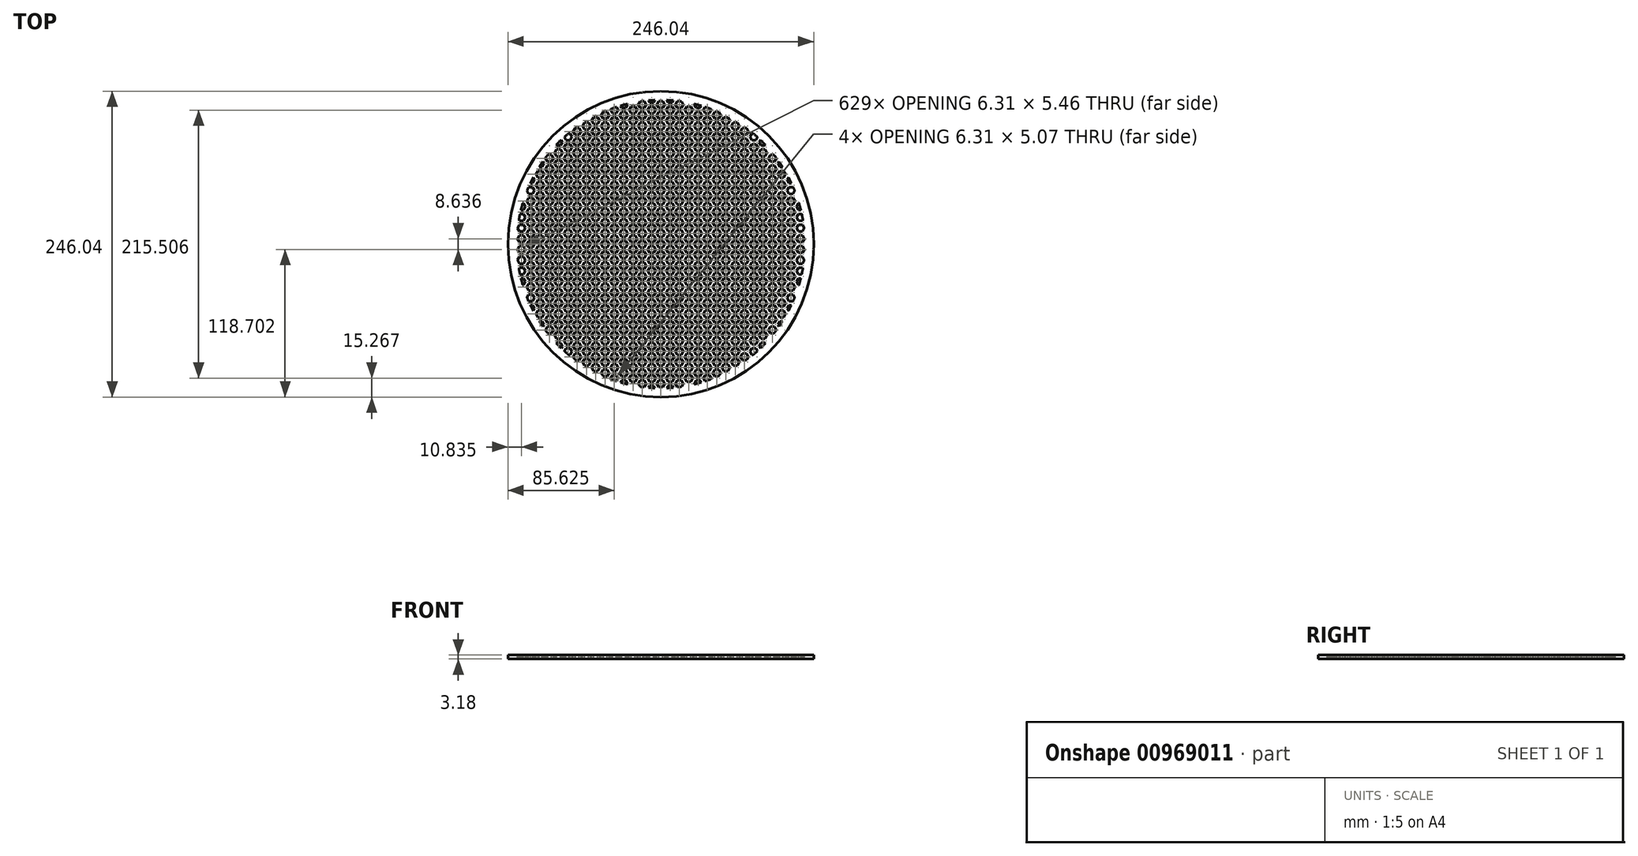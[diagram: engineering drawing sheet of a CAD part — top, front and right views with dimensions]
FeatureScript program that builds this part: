
annotation { "Feature Type Name" : "Feature", "Feature Type Description" : "" }
export const myFeature = defineFeature(function(context is Context, id is Id, definition is map)
    precondition{}
    {
        {
            var Q0;
            Q0=qCreatedBy(makeId("Top.planeOp"),FACE);
            var sketch = newSketch(context, id + "F0", { "sketchPlane" : qUnion([Q0])});
            skCircle(sketch, "E0", {"center": v(0, 0) * mm, "radius": 123.02 * mm});
            skSolve(sketch);
        }
        {
            var Q0;
            Q0=qSketchRegion(id+"F0",true);
            extrude(context, id + "F1", {"entities" : qUnion([Q0]), "depth" : 3.17 * mm, "offsetDistance" : 25.4 * mm});
        }
        {
            var Q0;
            Q0=makeQuery(id+"F1.opExtrude","CAP_FACE",FACE,{"disambiguationData":[OSD([sQuery(id+"F0.wireOp",EDGE,"E0")])],"isStart":false});
            var sketch = newSketch(context, id + "F2", { "sketchPlane" : qUnion([Q0])});
            skCircle(sketch, "E1.cCircle", {"center": v(-127.14, -133.86) * mm, "radius": 2.73 * mm, "construction": true});
            skLineSegment(sketch, "E1.0", {"start": v(-128.72, -131.13) * mm, "end": v(-125.57, -131.13) * mm});
            skLineSegment(sketch, "E1.1", {"start": v(-125.57, -131.13) * mm, "end": v(-124, -133.86) * mm});
            skLineSegment(sketch, "E1.2", {"start": v(-124, -133.86) * mm, "end": v(-125.57, -136.59) * mm});
            skLineSegment(sketch, "E1.3", {"start": v(-125.57, -136.59) * mm, "end": v(-128.72, -136.59) * mm});
            skLineSegment(sketch, "E1.4", {"start": v(-128.72, -136.59) * mm, "end": v(-130.3, -133.86) * mm});
            skLineSegment(sketch, "E1.5", {"start": v(-130.3, -133.86) * mm, "end": v(-128.72, -131.13) * mm});
            skPoint(sketch, "E1.0.midPoint", {"position": v(-127.14, -131.13) * mm});
            skCircle(sketch, "E2.cCircle", {"center": v(-119.66, -129.54) * mm, "radius": 2.73 * mm, "construction": true});
            skLineSegment(sketch, "E2.0", {"start": v(-121.24, -126.8) * mm, "end": v(-118.09, -126.8) * mm});
            skLineSegment(sketch, "E2.1", {"start": v(-118.09, -126.8) * mm, "end": v(-116.51, -129.54) * mm});
            skLineSegment(sketch, "E2.2", {"start": v(-116.51, -129.54) * mm, "end": v(-118.09, -132.27) * mm});
            skLineSegment(sketch, "E2.3", {"start": v(-118.09, -132.27) * mm, "end": v(-121.24, -132.27) * mm});
            skLineSegment(sketch, "E2.4", {"start": v(-121.24, -132.27) * mm, "end": v(-122.82, -129.54) * mm});
            skLineSegment(sketch, "E2.5", {"start": v(-122.82, -129.54) * mm, "end": v(-121.24, -126.8) * mm});
            skPoint(sketch, "E2.0.midPoint", {"position": v(-119.66, -126.8) * mm});
            skLineSegment(sketch, "E3.0.1.0", {"start": v(-128.72, -122.5) * mm, "end": v(-125.57, -122.5) * mm});
            skLineSegment(sketch, "E3.0.1.1", {"start": v(-125.57, -122.5) * mm, "end": v(-124, -125.22) * mm});
            skLineSegment(sketch, "E3.0.1.2", {"start": v(-124, -125.22) * mm, "end": v(-125.57, -127.95) * mm});
            skCircle(sketch, "E3.0.1.3", {"center": v(-127.14, -125.22) * mm, "radius": 2.73 * mm, "construction": true});
            skLineSegment(sketch, "E3.0.1.4", {"start": v(-125.57, -127.95) * mm, "end": v(-128.72, -127.95) * mm});
            skLineSegment(sketch, "E3.0.1.5", {"start": v(-128.72, -127.95) * mm, "end": v(-130.3, -125.22) * mm});
            skLineSegment(sketch, "E3.0.1.6", {"start": v(-130.3, -125.22) * mm, "end": v(-128.72, -122.5) * mm});
            skLineSegment(sketch, "E3.0.2.0", {"start": v(-128.72, -113.86) * mm, "end": v(-125.57, -113.86) * mm});
            skLineSegment(sketch, "E3.0.2.1", {"start": v(-125.57, -113.86) * mm, "end": v(-124, -116.59) * mm});
            skLineSegment(sketch, "E3.0.2.2", {"start": v(-124, -116.59) * mm, "end": v(-125.57, -119.32) * mm});
            skCircle(sketch, "E3.0.2.3", {"center": v(-127.14, -116.59) * mm, "radius": 2.73 * mm, "construction": true});
            skLineSegment(sketch, "E3.0.2.4", {"start": v(-125.57, -119.32) * mm, "end": v(-128.72, -119.32) * mm});
            skLineSegment(sketch, "E3.0.2.5", {"start": v(-128.72, -119.32) * mm, "end": v(-130.3, -116.59) * mm});
            skLineSegment(sketch, "E3.0.2.6", {"start": v(-130.3, -116.59) * mm, "end": v(-128.72, -113.86) * mm});
            skLineSegment(sketch, "E3.1.0.0", {"start": v(-113.76, -131.13) * mm, "end": v(-110.6, -131.13) * mm});
            skLineSegment(sketch, "E3.1.0.1", {"start": v(-110.6, -131.13) * mm, "end": v(-109.03, -133.86) * mm});
            skLineSegment(sketch, "E3.1.0.2", {"start": v(-109.03, -133.86) * mm, "end": v(-110.6, -136.59) * mm});
            skCircle(sketch, "E3.1.0.3", {"center": v(-112.19, -133.86) * mm, "radius": 2.73 * mm, "construction": true});
            skLineSegment(sketch, "E3.1.0.4", {"start": v(-110.6, -136.59) * mm, "end": v(-113.76, -136.59) * mm});
            skLineSegment(sketch, "E3.1.0.5", {"start": v(-113.76, -136.59) * mm, "end": v(-115.34, -133.86) * mm});
            skLineSegment(sketch, "E3.1.0.6", {"start": v(-115.34, -133.86) * mm, "end": v(-113.76, -131.13) * mm});
            skLineSegment(sketch, "E3.1.1.0", {"start": v(-113.76, -122.5) * mm, "end": v(-110.6, -122.5) * mm});
            skLineSegment(sketch, "E3.1.1.1", {"start": v(-110.6, -122.5) * mm, "end": v(-109.03, -125.22) * mm});
            skLineSegment(sketch, "E3.1.1.2", {"start": v(-109.03, -125.22) * mm, "end": v(-110.6, -127.95) * mm});
            skCircle(sketch, "E3.1.1.3", {"center": v(-112.19, -125.22) * mm, "radius": 2.73 * mm, "construction": true});
            skLineSegment(sketch, "E3.1.1.4", {"start": v(-110.6, -127.95) * mm, "end": v(-113.76, -127.95) * mm});
            skLineSegment(sketch, "E3.1.1.5", {"start": v(-113.76, -127.95) * mm, "end": v(-115.34, -125.22) * mm});
            skLineSegment(sketch, "E3.1.1.6", {"start": v(-115.34, -125.22) * mm, "end": v(-113.76, -122.5) * mm});
            skLineSegment(sketch, "E3.1.2.0", {"start": v(-113.76, -113.86) * mm, "end": v(-110.6, -113.86) * mm});
            skLineSegment(sketch, "E3.1.2.1", {"start": v(-110.6, -113.86) * mm, "end": v(-109.03, -116.59) * mm});
            skLineSegment(sketch, "E3.1.2.2", {"start": v(-109.03, -116.59) * mm, "end": v(-110.6, -119.32) * mm});
            skCircle(sketch, "E3.1.2.3", {"center": v(-112.19, -116.59) * mm, "radius": 2.73 * mm, "construction": true});
            skLineSegment(sketch, "E3.1.2.4", {"start": v(-110.6, -119.32) * mm, "end": v(-113.76, -119.32) * mm});
            skLineSegment(sketch, "E3.1.2.5", {"start": v(-113.76, -119.32) * mm, "end": v(-115.34, -116.59) * mm});
            skLineSegment(sketch, "E3.1.2.6", {"start": v(-115.34, -116.59) * mm, "end": v(-113.76, -113.86) * mm});
            skLineSegment(sketch, "E3.2.0.0", {"start": v(-98.8, -131.13) * mm, "end": v(-95.65, -131.13) * mm});
            skLineSegment(sketch, "E3.2.0.1", {"start": v(-95.65, -131.13) * mm, "end": v(-94.07, -133.86) * mm});
            skLineSegment(sketch, "E3.2.0.2", {"start": v(-94.07, -133.86) * mm, "end": v(-95.65, -136.59) * mm});
            skCircle(sketch, "E3.2.0.3", {"center": v(-97.23, -133.86) * mm, "radius": 2.73 * mm, "construction": true});
            skLineSegment(sketch, "E3.2.0.4", {"start": v(-95.65, -136.59) * mm, "end": v(-98.8, -136.59) * mm});
            skLineSegment(sketch, "E3.2.0.5", {"start": v(-98.8, -136.59) * mm, "end": v(-100.38, -133.86) * mm});
            skLineSegment(sketch, "E3.2.0.6", {"start": v(-100.38, -133.86) * mm, "end": v(-98.8, -131.13) * mm});
            skLineSegment(sketch, "E3.2.1.0", {"start": v(-98.8, -122.5) * mm, "end": v(-95.65, -122.5) * mm});
            skLineSegment(sketch, "E3.2.1.1", {"start": v(-95.65, -122.5) * mm, "end": v(-94.07, -125.22) * mm});
            skLineSegment(sketch, "E3.2.1.2", {"start": v(-94.07, -125.22) * mm, "end": v(-95.65, -127.95) * mm});
            skCircle(sketch, "E3.2.1.3", {"center": v(-97.23, -125.22) * mm, "radius": 2.73 * mm, "construction": true});
            skLineSegment(sketch, "E3.2.1.4", {"start": v(-95.65, -127.95) * mm, "end": v(-98.8, -127.95) * mm});
            skLineSegment(sketch, "E3.2.1.5", {"start": v(-98.8, -127.95) * mm, "end": v(-100.38, -125.22) * mm});
            skLineSegment(sketch, "E3.2.1.6", {"start": v(-100.38, -125.22) * mm, "end": v(-98.8, -122.5) * mm});
            skLineSegment(sketch, "E3.2.2.0", {"start": v(-98.8, -113.86) * mm, "end": v(-95.65, -113.86) * mm});
            skLineSegment(sketch, "E3.2.2.1", {"start": v(-95.65, -113.86) * mm, "end": v(-94.07, -116.59) * mm});
            skLineSegment(sketch, "E3.2.2.2", {"start": v(-94.07, -116.59) * mm, "end": v(-95.65, -119.32) * mm});
            skCircle(sketch, "E3.2.2.3", {"center": v(-97.23, -116.59) * mm, "radius": 2.73 * mm, "construction": true});
            skLineSegment(sketch, "E3.2.2.4", {"start": v(-95.65, -119.32) * mm, "end": v(-98.8, -119.32) * mm});
            skLineSegment(sketch, "E3.2.2.5", {"start": v(-98.8, -119.32) * mm, "end": v(-100.38, -116.59) * mm});
            skLineSegment(sketch, "E3.2.2.6", {"start": v(-100.38, -116.59) * mm, "end": v(-98.8, -113.86) * mm});
            skLineSegment(sketch, "E3.direction1", {"start": v(-128.72, -136.59) * mm, "end": v(-113.76, -136.59) * mm, "construction": true});
            skLineSegment(sketch, "E3.direction2", {"start": v(-128.72, -136.59) * mm, "end": v(-128.72, -127.95) * mm, "construction": true});
            skLineSegment(sketch, "E4.0.0.3", {"start": v(-128.72, -105.22) * mm, "end": v(-125.57, -105.22) * mm});
            skLineSegment(sketch, "E4.3.0.3", {"start": v(-125.57, -105.22) * mm, "end": v(-124, -107.95) * mm});
            skLineSegment(sketch, "E4.6.0.3", {"start": v(-124, -107.95) * mm, "end": v(-125.57, -110.68) * mm});
            skCircle(sketch, "E4.9.0.3", {"center": v(-127.14, -107.95) * mm, "radius": 2.73 * mm, "construction": true});
            skLineSegment(sketch, "E4.11.0.3", {"start": v(-125.57, -110.68) * mm, "end": v(-128.72, -110.68) * mm});
            skLineSegment(sketch, "E4.14.0.3", {"start": v(-128.72, -110.68) * mm, "end": v(-130.3, -107.95) * mm});
            skLineSegment(sketch, "E4.17.0.3", {"start": v(-130.3, -107.95) * mm, "end": v(-128.72, -105.22) * mm});
            skLineSegment(sketch, "E4.0.1.3", {"start": v(-113.76, -105.22) * mm, "end": v(-110.6, -105.22) * mm});
            skLineSegment(sketch, "E4.3.1.3", {"start": v(-110.6, -105.22) * mm, "end": v(-109.03, -107.95) * mm});
            skLineSegment(sketch, "E4.6.1.3", {"start": v(-109.03, -107.95) * mm, "end": v(-110.6, -110.68) * mm});
            skCircle(sketch, "E4.9.1.3", {"center": v(-112.19, -107.95) * mm, "radius": 2.73 * mm, "construction": true});
            skLineSegment(sketch, "E4.11.1.3", {"start": v(-110.6, -110.68) * mm, "end": v(-113.76, -110.68) * mm});
            skLineSegment(sketch, "E4.14.1.3", {"start": v(-113.76, -110.68) * mm, "end": v(-115.34, -107.95) * mm});
            skLineSegment(sketch, "E4.17.1.3", {"start": v(-115.34, -107.95) * mm, "end": v(-113.76, -105.22) * mm});
            skLineSegment(sketch, "E4.0.2.3", {"start": v(-98.8, -105.22) * mm, "end": v(-95.65, -105.22) * mm});
            skLineSegment(sketch, "E4.3.2.3", {"start": v(-95.65, -105.22) * mm, "end": v(-94.07, -107.95) * mm});
            skLineSegment(sketch, "E4.6.2.3", {"start": v(-94.07, -107.95) * mm, "end": v(-95.65, -110.68) * mm});
            skCircle(sketch, "E4.9.2.3", {"center": v(-97.23, -107.95) * mm, "radius": 2.73 * mm, "construction": true});
            skLineSegment(sketch, "E4.11.2.3", {"start": v(-95.65, -110.68) * mm, "end": v(-98.8, -110.68) * mm});
            skLineSegment(sketch, "E4.14.2.3", {"start": v(-98.8, -110.68) * mm, "end": v(-100.38, -107.95) * mm});
            skLineSegment(sketch, "E4.17.2.3", {"start": v(-100.38, -107.95) * mm, "end": v(-98.8, -105.22) * mm});
            skCircle(sketch, "E5.0.1.0", {"center": v(-119.66, -120.9) * mm, "radius": 2.73 * mm, "construction": true});
            skLineSegment(sketch, "E5.0.1.1", {"start": v(-122.82, -120.9) * mm, "end": v(-121.24, -118.17) * mm});
            skLineSegment(sketch, "E5.0.1.2", {"start": v(-121.24, -118.17) * mm, "end": v(-118.09, -118.17) * mm});
            skLineSegment(sketch, "E5.0.1.3", {"start": v(-118.09, -118.17) * mm, "end": v(-116.51, -120.9) * mm});
            skLineSegment(sketch, "E5.0.1.4", {"start": v(-116.51, -120.9) * mm, "end": v(-118.09, -123.63) * mm});
            skLineSegment(sketch, "E5.0.1.5", {"start": v(-118.09, -123.63) * mm, "end": v(-121.24, -123.63) * mm});
            skLineSegment(sketch, "E5.0.1.6", {"start": v(-121.24, -123.63) * mm, "end": v(-122.82, -120.9) * mm});
            skCircle(sketch, "E5.0.2.0", {"center": v(-119.66, -112.27) * mm, "radius": 2.73 * mm, "construction": true});
            skLineSegment(sketch, "E5.0.2.1", {"start": v(-122.82, -112.27) * mm, "end": v(-121.24, -109.54) * mm});
            skLineSegment(sketch, "E5.0.2.2", {"start": v(-121.24, -109.54) * mm, "end": v(-118.09, -109.54) * mm});
            skLineSegment(sketch, "E5.0.2.3", {"start": v(-118.09, -109.54) * mm, "end": v(-116.51, -112.27) * mm});
            skLineSegment(sketch, "E5.0.2.4", {"start": v(-116.51, -112.27) * mm, "end": v(-118.09, -115) * mm});
            skLineSegment(sketch, "E5.0.2.5", {"start": v(-118.09, -115) * mm, "end": v(-121.24, -115) * mm});
            skLineSegment(sketch, "E5.0.2.6", {"start": v(-121.24, -115) * mm, "end": v(-122.82, -112.27) * mm});
            skCircle(sketch, "E5.0.3.0", {"center": v(-119.66, -103.63) * mm, "radius": 2.73 * mm, "construction": true});
            skLineSegment(sketch, "E5.0.3.1", {"start": v(-122.82, -103.63) * mm, "end": v(-121.24, -100.9) * mm});
            skLineSegment(sketch, "E5.0.3.2", {"start": v(-121.24, -100.9) * mm, "end": v(-118.09, -100.9) * mm});
            skLineSegment(sketch, "E5.0.3.3", {"start": v(-118.09, -100.9) * mm, "end": v(-116.51, -103.63) * mm});
            skLineSegment(sketch, "E5.0.3.4", {"start": v(-116.51, -103.63) * mm, "end": v(-118.09, -106.36) * mm});
            skLineSegment(sketch, "E5.0.3.5", {"start": v(-118.09, -106.36) * mm, "end": v(-121.24, -106.36) * mm});
            skLineSegment(sketch, "E5.0.3.6", {"start": v(-121.24, -106.36) * mm, "end": v(-122.82, -103.63) * mm});
            skCircle(sketch, "E5.1.0.0", {"center": v(-104.7, -129.54) * mm, "radius": 2.73 * mm, "construction": true});
            skLineSegment(sketch, "E5.1.0.1", {"start": v(-107.86, -129.54) * mm, "end": v(-106.28, -126.8) * mm});
            skLineSegment(sketch, "E5.1.0.2", {"start": v(-106.28, -126.8) * mm, "end": v(-103.13, -126.8) * mm});
            skLineSegment(sketch, "E5.1.0.3", {"start": v(-103.13, -126.8) * mm, "end": v(-101.55, -129.54) * mm});
            skLineSegment(sketch, "E5.1.0.4", {"start": v(-101.55, -129.54) * mm, "end": v(-103.13, -132.27) * mm});
            skLineSegment(sketch, "E5.1.0.5", {"start": v(-103.13, -132.27) * mm, "end": v(-106.28, -132.27) * mm});
            skLineSegment(sketch, "E5.1.0.6", {"start": v(-106.28, -132.27) * mm, "end": v(-107.86, -129.54) * mm});
            skCircle(sketch, "E5.1.1.0", {"center": v(-104.7, -120.9) * mm, "radius": 2.73 * mm, "construction": true});
            skLineSegment(sketch, "E5.1.1.1", {"start": v(-107.86, -120.9) * mm, "end": v(-106.28, -118.17) * mm});
            skLineSegment(sketch, "E5.1.1.2", {"start": v(-106.28, -118.17) * mm, "end": v(-103.13, -118.17) * mm});
            skLineSegment(sketch, "E5.1.1.3", {"start": v(-103.13, -118.17) * mm, "end": v(-101.55, -120.9) * mm});
            skLineSegment(sketch, "E5.1.1.4", {"start": v(-101.55, -120.9) * mm, "end": v(-103.13, -123.63) * mm});
            skLineSegment(sketch, "E5.1.1.5", {"start": v(-103.13, -123.63) * mm, "end": v(-106.28, -123.63) * mm});
            skLineSegment(sketch, "E5.1.1.6", {"start": v(-106.28, -123.63) * mm, "end": v(-107.86, -120.9) * mm});
            skCircle(sketch, "E5.1.2.0", {"center": v(-104.7, -112.27) * mm, "radius": 2.73 * mm, "construction": true});
            skLineSegment(sketch, "E5.1.2.1", {"start": v(-107.86, -112.27) * mm, "end": v(-106.28, -109.54) * mm});
            skLineSegment(sketch, "E5.1.2.2", {"start": v(-106.28, -109.54) * mm, "end": v(-103.13, -109.54) * mm});
            skLineSegment(sketch, "E5.1.2.3", {"start": v(-103.13, -109.54) * mm, "end": v(-101.55, -112.27) * mm});
            skLineSegment(sketch, "E5.1.2.4", {"start": v(-101.55, -112.27) * mm, "end": v(-103.13, -115) * mm});
            skLineSegment(sketch, "E5.1.2.5", {"start": v(-103.13, -115) * mm, "end": v(-106.28, -115) * mm});
            skLineSegment(sketch, "E5.1.2.6", {"start": v(-106.28, -115) * mm, "end": v(-107.86, -112.27) * mm});
            skCircle(sketch, "E5.1.3.0", {"center": v(-104.7, -103.63) * mm, "radius": 2.73 * mm, "construction": true});
            skLineSegment(sketch, "E5.1.3.1", {"start": v(-107.86, -103.63) * mm, "end": v(-106.28, -100.9) * mm});
            skLineSegment(sketch, "E5.1.3.2", {"start": v(-106.28, -100.9) * mm, "end": v(-103.13, -100.9) * mm});
            skLineSegment(sketch, "E5.1.3.3", {"start": v(-103.13, -100.9) * mm, "end": v(-101.55, -103.63) * mm});
            skLineSegment(sketch, "E5.1.3.4", {"start": v(-101.55, -103.63) * mm, "end": v(-103.13, -106.36) * mm});
            skLineSegment(sketch, "E5.1.3.5", {"start": v(-103.13, -106.36) * mm, "end": v(-106.28, -106.36) * mm});
            skLineSegment(sketch, "E5.1.3.6", {"start": v(-106.28, -106.36) * mm, "end": v(-107.86, -103.63) * mm});
            skLineSegment(sketch, "E5.direction1", {"start": v(-121.24, -132.27) * mm, "end": v(-106.28, -132.27) * mm, "construction": true});
            skLineSegment(sketch, "E5.direction2", {"start": v(-121.24, -132.27) * mm, "end": v(-121.24, -123.63) * mm, "construction": true});
            skLineSegment(sketch, "E6.0.3.0", {"start": v(-83.85, -131.13) * mm, "end": v(-80.7, -131.13) * mm});
            skLineSegment(sketch, "E6.3.3.0", {"start": v(-80.7, -131.13) * mm, "end": v(-79.12, -133.86) * mm});
            skLineSegment(sketch, "E6.6.3.0", {"start": v(-79.12, -133.86) * mm, "end": v(-80.7, -136.59) * mm});
            skCircle(sketch, "E6.9.3.0", {"center": v(-82.27, -133.86) * mm, "radius": 2.73 * mm, "construction": true});
            skLineSegment(sketch, "E6.11.3.0", {"start": v(-80.7, -136.59) * mm, "end": v(-83.85, -136.59) * mm});
            skLineSegment(sketch, "E6.14.3.0", {"start": v(-83.85, -136.59) * mm, "end": v(-85.42, -133.86) * mm});
            skLineSegment(sketch, "E6.17.3.0", {"start": v(-85.42, -133.86) * mm, "end": v(-83.85, -131.13) * mm});
            skLineSegment(sketch, "E6.0.3.1", {"start": v(-83.85, -122.5) * mm, "end": v(-80.7, -122.5) * mm});
            skLineSegment(sketch, "E6.3.3.1", {"start": v(-80.7, -122.5) * mm, "end": v(-79.12, -125.22) * mm});
            skLineSegment(sketch, "E6.6.3.1", {"start": v(-79.12, -125.22) * mm, "end": v(-80.7, -127.95) * mm});
            skCircle(sketch, "E6.9.3.1", {"center": v(-82.27, -125.22) * mm, "radius": 2.73 * mm, "construction": true});
            skLineSegment(sketch, "E6.11.3.1", {"start": v(-80.7, -127.95) * mm, "end": v(-83.85, -127.95) * mm});
            skLineSegment(sketch, "E6.14.3.1", {"start": v(-83.85, -127.95) * mm, "end": v(-85.42, -125.22) * mm});
            skLineSegment(sketch, "E6.17.3.1", {"start": v(-85.42, -125.22) * mm, "end": v(-83.85, -122.5) * mm});
            skLineSegment(sketch, "E6.0.3.2", {"start": v(-83.85, -113.86) * mm, "end": v(-80.7, -113.86) * mm});
            skLineSegment(sketch, "E6.3.3.2", {"start": v(-80.7, -113.86) * mm, "end": v(-79.12, -116.59) * mm});
            skLineSegment(sketch, "E6.6.3.2", {"start": v(-79.12, -116.59) * mm, "end": v(-80.7, -119.32) * mm});
            skCircle(sketch, "E6.9.3.2", {"center": v(-82.27, -116.59) * mm, "radius": 2.73 * mm, "construction": true});
            skLineSegment(sketch, "E6.11.3.2", {"start": v(-80.7, -119.32) * mm, "end": v(-83.85, -119.32) * mm});
            skLineSegment(sketch, "E6.14.3.2", {"start": v(-83.85, -119.32) * mm, "end": v(-85.42, -116.59) * mm});
            skLineSegment(sketch, "E6.17.3.2", {"start": v(-85.42, -116.59) * mm, "end": v(-83.85, -113.86) * mm});
            skLineSegment(sketch, "E6.0.3.3", {"start": v(-83.85, -105.22) * mm, "end": v(-80.7, -105.22) * mm});
            skLineSegment(sketch, "E6.3.3.3", {"start": v(-80.7, -105.22) * mm, "end": v(-79.12, -107.95) * mm});
            skLineSegment(sketch, "E6.6.3.3", {"start": v(-79.12, -107.95) * mm, "end": v(-80.7, -110.68) * mm});
            skCircle(sketch, "E6.9.3.3", {"center": v(-82.27, -107.95) * mm, "radius": 2.73 * mm, "construction": true});
            skLineSegment(sketch, "E6.11.3.3", {"start": v(-80.7, -110.68) * mm, "end": v(-83.85, -110.68) * mm});
            skLineSegment(sketch, "E6.14.3.3", {"start": v(-83.85, -110.68) * mm, "end": v(-85.42, -107.95) * mm});
            skLineSegment(sketch, "E6.17.3.3", {"start": v(-85.42, -107.95) * mm, "end": v(-83.85, -105.22) * mm});
            skLineSegment(sketch, "E6.0.4.0", {"start": v(-68.89, -131.13) * mm, "end": v(-65.73, -131.13) * mm});
            skLineSegment(sketch, "E6.3.4.0", {"start": v(-65.73, -131.13) * mm, "end": v(-64.16, -133.86) * mm});
            skLineSegment(sketch, "E6.6.4.0", {"start": v(-64.16, -133.86) * mm, "end": v(-65.73, -136.59) * mm});
            skCircle(sketch, "E6.9.4.0", {"center": v(-67.31, -133.86) * mm, "radius": 2.73 * mm, "construction": true});
            skLineSegment(sketch, "E6.11.4.0", {"start": v(-65.73, -136.59) * mm, "end": v(-68.89, -136.59) * mm});
            skLineSegment(sketch, "E6.14.4.0", {"start": v(-68.89, -136.59) * mm, "end": v(-70.46, -133.86) * mm});
            skLineSegment(sketch, "E6.17.4.0", {"start": v(-70.46, -133.86) * mm, "end": v(-68.89, -131.13) * mm});
            skLineSegment(sketch, "E6.0.4.1", {"start": v(-68.89, -122.5) * mm, "end": v(-65.73, -122.5) * mm});
            skLineSegment(sketch, "E6.3.4.1", {"start": v(-65.73, -122.5) * mm, "end": v(-64.16, -125.22) * mm});
            skLineSegment(sketch, "E6.6.4.1", {"start": v(-64.16, -125.22) * mm, "end": v(-65.73, -127.95) * mm});
            skCircle(sketch, "E6.9.4.1", {"center": v(-67.31, -125.22) * mm, "radius": 2.73 * mm, "construction": true});
            skLineSegment(sketch, "E6.11.4.1", {"start": v(-65.73, -127.95) * mm, "end": v(-68.89, -127.95) * mm});
            skLineSegment(sketch, "E6.14.4.1", {"start": v(-68.89, -127.95) * mm, "end": v(-70.46, -125.22) * mm});
            skLineSegment(sketch, "E6.17.4.1", {"start": v(-70.46, -125.22) * mm, "end": v(-68.89, -122.5) * mm});
            skLineSegment(sketch, "E6.0.4.2", {"start": v(-68.89, -113.86) * mm, "end": v(-65.73, -113.86) * mm});
            skLineSegment(sketch, "E6.3.4.2", {"start": v(-65.73, -113.86) * mm, "end": v(-64.16, -116.59) * mm});
            skLineSegment(sketch, "E6.6.4.2", {"start": v(-64.16, -116.59) * mm, "end": v(-65.73, -119.32) * mm});
            skCircle(sketch, "E6.9.4.2", {"center": v(-67.31, -116.59) * mm, "radius": 2.73 * mm, "construction": true});
            skLineSegment(sketch, "E6.11.4.2", {"start": v(-65.73, -119.32) * mm, "end": v(-68.89, -119.32) * mm});
            skLineSegment(sketch, "E6.14.4.2", {"start": v(-68.89, -119.32) * mm, "end": v(-70.46, -116.59) * mm});
            skLineSegment(sketch, "E6.17.4.2", {"start": v(-70.46, -116.59) * mm, "end": v(-68.89, -113.86) * mm});
            skLineSegment(sketch, "E6.0.4.3", {"start": v(-68.89, -105.22) * mm, "end": v(-65.73, -105.22) * mm});
            skLineSegment(sketch, "E6.3.4.3", {"start": v(-65.73, -105.22) * mm, "end": v(-64.16, -107.95) * mm});
            skLineSegment(sketch, "E6.6.4.3", {"start": v(-64.16, -107.95) * mm, "end": v(-65.73, -110.68) * mm});
            skCircle(sketch, "E6.9.4.3", {"center": v(-67.31, -107.95) * mm, "radius": 2.73 * mm, "construction": true});
            skLineSegment(sketch, "E6.11.4.3", {"start": v(-65.73, -110.68) * mm, "end": v(-68.89, -110.68) * mm});
            skLineSegment(sketch, "E6.14.4.3", {"start": v(-68.89, -110.68) * mm, "end": v(-70.46, -107.95) * mm});
            skLineSegment(sketch, "E6.17.4.3", {"start": v(-70.46, -107.95) * mm, "end": v(-68.89, -105.22) * mm});
            skLineSegment(sketch, "E6.0.5.0", {"start": v(-53.93, -131.13) * mm, "end": v(-50.78, -131.13) * mm});
            skLineSegment(sketch, "E6.3.5.0", {"start": v(-50.78, -131.13) * mm, "end": v(-49.2, -133.86) * mm});
            skLineSegment(sketch, "E6.6.5.0", {"start": v(-49.2, -133.86) * mm, "end": v(-50.78, -136.59) * mm});
            skCircle(sketch, "E6.9.5.0", {"center": v(-52.35, -133.86) * mm, "radius": 2.73 * mm, "construction": true});
            skLineSegment(sketch, "E6.11.5.0", {"start": v(-50.78, -136.59) * mm, "end": v(-53.93, -136.59) * mm});
            skLineSegment(sketch, "E6.14.5.0", {"start": v(-53.93, -136.59) * mm, "end": v(-55.5, -133.86) * mm});
            skLineSegment(sketch, "E6.17.5.0", {"start": v(-55.5, -133.86) * mm, "end": v(-53.93, -131.13) * mm});
            skLineSegment(sketch, "E6.0.5.1", {"start": v(-53.93, -122.5) * mm, "end": v(-50.78, -122.5) * mm});
            skLineSegment(sketch, "E6.3.5.1", {"start": v(-50.78, -122.5) * mm, "end": v(-49.2, -125.22) * mm});
            skLineSegment(sketch, "E6.6.5.1", {"start": v(-49.2, -125.22) * mm, "end": v(-50.78, -127.95) * mm});
            skCircle(sketch, "E6.9.5.1", {"center": v(-52.35, -125.22) * mm, "radius": 2.73 * mm, "construction": true});
            skLineSegment(sketch, "E6.11.5.1", {"start": v(-50.78, -127.95) * mm, "end": v(-53.93, -127.95) * mm});
            skLineSegment(sketch, "E6.14.5.1", {"start": v(-53.93, -127.95) * mm, "end": v(-55.5, -125.22) * mm});
            skLineSegment(sketch, "E6.17.5.1", {"start": v(-55.5, -125.22) * mm, "end": v(-53.93, -122.5) * mm});
            skLineSegment(sketch, "E6.0.5.2", {"start": v(-53.93, -113.86) * mm, "end": v(-50.78, -113.86) * mm});
            skLineSegment(sketch, "E6.3.5.2", {"start": v(-50.78, -113.86) * mm, "end": v(-49.2, -116.59) * mm});
            skLineSegment(sketch, "E6.6.5.2", {"start": v(-49.2, -116.59) * mm, "end": v(-50.78, -119.32) * mm});
            skCircle(sketch, "E6.9.5.2", {"center": v(-52.35, -116.59) * mm, "radius": 2.73 * mm, "construction": true});
            skLineSegment(sketch, "E6.11.5.2", {"start": v(-50.78, -119.32) * mm, "end": v(-53.93, -119.32) * mm});
            skLineSegment(sketch, "E6.14.5.2", {"start": v(-53.93, -119.32) * mm, "end": v(-55.5, -116.59) * mm});
            skLineSegment(sketch, "E6.17.5.2", {"start": v(-55.5, -116.59) * mm, "end": v(-53.93, -113.86) * mm});
            skLineSegment(sketch, "E6.0.5.3", {"start": v(-53.93, -105.22) * mm, "end": v(-50.78, -105.22) * mm});
            skLineSegment(sketch, "E6.3.5.3", {"start": v(-50.78, -105.22) * mm, "end": v(-49.2, -107.95) * mm});
            skLineSegment(sketch, "E6.6.5.3", {"start": v(-49.2, -107.95) * mm, "end": v(-50.78, -110.68) * mm});
            skCircle(sketch, "E6.9.5.3", {"center": v(-52.35, -107.95) * mm, "radius": 2.73 * mm, "construction": true});
            skLineSegment(sketch, "E6.11.5.3", {"start": v(-50.78, -110.68) * mm, "end": v(-53.93, -110.68) * mm});
            skLineSegment(sketch, "E6.14.5.3", {"start": v(-53.93, -110.68) * mm, "end": v(-55.5, -107.95) * mm});
            skLineSegment(sketch, "E6.17.5.3", {"start": v(-55.5, -107.95) * mm, "end": v(-53.93, -105.22) * mm});
            skCircle(sketch, "E7.0.2.0", {"center": v(-89.75, -129.54) * mm, "radius": 2.73 * mm, "construction": true});
            skLineSegment(sketch, "E7.2.2.0", {"start": v(-92.9, -129.54) * mm, "end": v(-91.32, -126.8) * mm});
            skLineSegment(sketch, "E7.5.2.0", {"start": v(-91.32, -126.8) * mm, "end": v(-88.17, -126.8) * mm});
            skLineSegment(sketch, "E7.8.2.0", {"start": v(-88.17, -126.8) * mm, "end": v(-86.6, -129.54) * mm});
            skLineSegment(sketch, "E7.11.2.0", {"start": v(-86.6, -129.54) * mm, "end": v(-88.17, -132.27) * mm});
            skLineSegment(sketch, "E7.14.2.0", {"start": v(-88.17, -132.27) * mm, "end": v(-91.32, -132.27) * mm});
            skLineSegment(sketch, "E7.17.2.0", {"start": v(-91.32, -132.27) * mm, "end": v(-92.9, -129.54) * mm});
            skCircle(sketch, "E7.0.2.1", {"center": v(-89.75, -120.9) * mm, "radius": 2.73 * mm, "construction": true});
            skLineSegment(sketch, "E7.2.2.1", {"start": v(-92.9, -120.9) * mm, "end": v(-91.32, -118.17) * mm});
            skLineSegment(sketch, "E7.5.2.1", {"start": v(-91.32, -118.17) * mm, "end": v(-88.17, -118.17) * mm});
            skLineSegment(sketch, "E7.8.2.1", {"start": v(-88.17, -118.17) * mm, "end": v(-86.6, -120.9) * mm});
            skLineSegment(sketch, "E7.11.2.1", {"start": v(-86.6, -120.9) * mm, "end": v(-88.17, -123.63) * mm});
            skLineSegment(sketch, "E7.14.2.1", {"start": v(-88.17, -123.63) * mm, "end": v(-91.32, -123.63) * mm});
            skLineSegment(sketch, "E7.17.2.1", {"start": v(-91.32, -123.63) * mm, "end": v(-92.9, -120.9) * mm});
            skCircle(sketch, "E7.0.2.2", {"center": v(-89.75, -112.27) * mm, "radius": 2.73 * mm, "construction": true});
            skLineSegment(sketch, "E7.2.2.2", {"start": v(-92.9, -112.27) * mm, "end": v(-91.32, -109.54) * mm});
            skLineSegment(sketch, "E7.5.2.2", {"start": v(-91.32, -109.54) * mm, "end": v(-88.17, -109.54) * mm});
            skLineSegment(sketch, "E7.8.2.2", {"start": v(-88.17, -109.54) * mm, "end": v(-86.6, -112.27) * mm});
            skLineSegment(sketch, "E7.11.2.2", {"start": v(-86.6, -112.27) * mm, "end": v(-88.17, -115) * mm});
            skLineSegment(sketch, "E7.14.2.2", {"start": v(-88.17, -115) * mm, "end": v(-91.32, -115) * mm});
            skLineSegment(sketch, "E7.17.2.2", {"start": v(-91.32, -115) * mm, "end": v(-92.9, -112.27) * mm});
            skCircle(sketch, "E7.0.2.3", {"center": v(-89.75, -103.63) * mm, "radius": 2.73 * mm, "construction": true});
            skLineSegment(sketch, "E7.2.2.3", {"start": v(-92.9, -103.63) * mm, "end": v(-91.32, -100.9) * mm});
            skLineSegment(sketch, "E7.5.2.3", {"start": v(-91.32, -100.9) * mm, "end": v(-88.17, -100.9) * mm});
            skLineSegment(sketch, "E7.8.2.3", {"start": v(-88.17, -100.9) * mm, "end": v(-86.6, -103.63) * mm});
            skLineSegment(sketch, "E7.11.2.3", {"start": v(-86.6, -103.63) * mm, "end": v(-88.17, -106.36) * mm});
            skLineSegment(sketch, "E7.14.2.3", {"start": v(-88.17, -106.36) * mm, "end": v(-91.32, -106.36) * mm});
            skLineSegment(sketch, "E7.17.2.3", {"start": v(-91.32, -106.36) * mm, "end": v(-92.9, -103.63) * mm});
            skCircle(sketch, "E7.0.3.0", {"center": v(-74.8, -129.54) * mm, "radius": 2.73 * mm, "construction": true});
            skLineSegment(sketch, "E7.2.3.0", {"start": v(-77.94, -129.54) * mm, "end": v(-76.37, -126.8) * mm});
            skLineSegment(sketch, "E7.5.3.0", {"start": v(-76.37, -126.8) * mm, "end": v(-73.21, -126.8) * mm});
            skLineSegment(sketch, "E7.8.3.0", {"start": v(-73.21, -126.8) * mm, "end": v(-71.64, -129.54) * mm});
            skLineSegment(sketch, "E7.11.3.0", {"start": v(-71.64, -129.54) * mm, "end": v(-73.21, -132.27) * mm});
            skLineSegment(sketch, "E7.14.3.0", {"start": v(-73.21, -132.27) * mm, "end": v(-76.37, -132.27) * mm});
            skLineSegment(sketch, "E7.17.3.0", {"start": v(-76.37, -132.27) * mm, "end": v(-77.94, -129.54) * mm});
            skCircle(sketch, "E7.0.3.1", {"center": v(-74.8, -120.9) * mm, "radius": 2.73 * mm, "construction": true});
            skLineSegment(sketch, "E7.2.3.1", {"start": v(-77.94, -120.9) * mm, "end": v(-76.37, -118.17) * mm});
            skLineSegment(sketch, "E7.5.3.1", {"start": v(-76.37, -118.17) * mm, "end": v(-73.21, -118.17) * mm});
            skLineSegment(sketch, "E7.8.3.1", {"start": v(-73.21, -118.17) * mm, "end": v(-71.64, -120.9) * mm});
            skLineSegment(sketch, "E7.11.3.1", {"start": v(-71.64, -120.9) * mm, "end": v(-73.21, -123.63) * mm});
            skLineSegment(sketch, "E7.14.3.1", {"start": v(-73.21, -123.63) * mm, "end": v(-76.37, -123.63) * mm});
            skLineSegment(sketch, "E7.17.3.1", {"start": v(-76.37, -123.63) * mm, "end": v(-77.94, -120.9) * mm});
            skCircle(sketch, "E7.0.3.2", {"center": v(-74.8, -112.27) * mm, "radius": 2.73 * mm, "construction": true});
            skLineSegment(sketch, "E7.2.3.2", {"start": v(-77.94, -112.27) * mm, "end": v(-76.37, -109.54) * mm});
            skLineSegment(sketch, "E7.5.3.2", {"start": v(-76.37, -109.54) * mm, "end": v(-73.21, -109.54) * mm});
            skLineSegment(sketch, "E7.8.3.2", {"start": v(-73.21, -109.54) * mm, "end": v(-71.64, -112.27) * mm});
            skLineSegment(sketch, "E7.11.3.2", {"start": v(-71.64, -112.27) * mm, "end": v(-73.21, -115) * mm});
            skLineSegment(sketch, "E7.14.3.2", {"start": v(-73.21, -115) * mm, "end": v(-76.37, -115) * mm});
            skLineSegment(sketch, "E7.17.3.2", {"start": v(-76.37, -115) * mm, "end": v(-77.94, -112.27) * mm});
            skCircle(sketch, "E7.0.3.3", {"center": v(-74.8, -103.63) * mm, "radius": 2.73 * mm, "construction": true});
            skLineSegment(sketch, "E7.2.3.3", {"start": v(-77.94, -103.63) * mm, "end": v(-76.37, -100.9) * mm});
            skLineSegment(sketch, "E7.5.3.3", {"start": v(-76.37, -100.9) * mm, "end": v(-73.21, -100.9) * mm});
            skLineSegment(sketch, "E7.8.3.3", {"start": v(-73.21, -100.9) * mm, "end": v(-71.64, -103.63) * mm});
            skLineSegment(sketch, "E7.11.3.3", {"start": v(-71.64, -103.63) * mm, "end": v(-73.21, -106.36) * mm});
            skLineSegment(sketch, "E7.14.3.3", {"start": v(-73.21, -106.36) * mm, "end": v(-76.37, -106.36) * mm});
            skLineSegment(sketch, "E7.17.3.3", {"start": v(-76.37, -106.36) * mm, "end": v(-77.94, -103.63) * mm});
            skCircle(sketch, "E7.0.4.0", {"center": v(-59.83, -129.54) * mm, "radius": 2.73 * mm, "construction": true});
            skLineSegment(sketch, "E7.2.4.0", {"start": v(-62.99, -129.54) * mm, "end": v(-61.4, -126.8) * mm});
            skLineSegment(sketch, "E7.5.4.0", {"start": v(-61.4, -126.8) * mm, "end": v(-58.26, -126.8) * mm});
            skLineSegment(sketch, "E7.8.4.0", {"start": v(-58.26, -126.8) * mm, "end": v(-56.68, -129.54) * mm});
            skLineSegment(sketch, "E7.11.4.0", {"start": v(-56.68, -129.54) * mm, "end": v(-58.26, -132.27) * mm});
            skLineSegment(sketch, "E7.14.4.0", {"start": v(-58.26, -132.27) * mm, "end": v(-61.4, -132.27) * mm});
            skLineSegment(sketch, "E7.17.4.0", {"start": v(-61.4, -132.27) * mm, "end": v(-62.99, -129.54) * mm});
            skCircle(sketch, "E7.0.4.1", {"center": v(-59.83, -120.9) * mm, "radius": 2.73 * mm, "construction": true});
            skLineSegment(sketch, "E7.2.4.1", {"start": v(-62.99, -120.9) * mm, "end": v(-61.4, -118.17) * mm});
            skLineSegment(sketch, "E7.5.4.1", {"start": v(-61.4, -118.17) * mm, "end": v(-58.26, -118.17) * mm});
            skLineSegment(sketch, "E7.8.4.1", {"start": v(-58.26, -118.17) * mm, "end": v(-56.68, -120.9) * mm});
            skLineSegment(sketch, "E7.11.4.1", {"start": v(-56.68, -120.9) * mm, "end": v(-58.26, -123.63) * mm});
            skLineSegment(sketch, "E7.14.4.1", {"start": v(-58.26, -123.63) * mm, "end": v(-61.4, -123.63) * mm});
            skLineSegment(sketch, "E7.17.4.1", {"start": v(-61.4, -123.63) * mm, "end": v(-62.99, -120.9) * mm});
            skCircle(sketch, "E7.0.4.2", {"center": v(-59.83, -112.27) * mm, "radius": 2.73 * mm, "construction": true});
            skLineSegment(sketch, "E7.2.4.2", {"start": v(-62.99, -112.27) * mm, "end": v(-61.4, -109.54) * mm});
            skLineSegment(sketch, "E7.5.4.2", {"start": v(-61.4, -109.54) * mm, "end": v(-58.26, -109.54) * mm});
            skLineSegment(sketch, "E7.8.4.2", {"start": v(-58.26, -109.54) * mm, "end": v(-56.68, -112.27) * mm});
            skLineSegment(sketch, "E7.11.4.2", {"start": v(-56.68, -112.27) * mm, "end": v(-58.26, -115) * mm});
            skLineSegment(sketch, "E7.14.4.2", {"start": v(-58.26, -115) * mm, "end": v(-61.4, -115) * mm});
            skLineSegment(sketch, "E7.17.4.2", {"start": v(-61.4, -115) * mm, "end": v(-62.99, -112.27) * mm});
            skCircle(sketch, "E7.0.4.3", {"center": v(-59.83, -103.63) * mm, "radius": 2.73 * mm, "construction": true});
            skLineSegment(sketch, "E7.2.4.3", {"start": v(-62.99, -103.63) * mm, "end": v(-61.4, -100.9) * mm});
            skLineSegment(sketch, "E7.5.4.3", {"start": v(-61.4, -100.9) * mm, "end": v(-58.26, -100.9) * mm});
            skLineSegment(sketch, "E7.8.4.3", {"start": v(-58.26, -100.9) * mm, "end": v(-56.68, -103.63) * mm});
            skLineSegment(sketch, "E7.11.4.3", {"start": v(-56.68, -103.63) * mm, "end": v(-58.26, -106.36) * mm});
            skLineSegment(sketch, "E7.14.4.3", {"start": v(-58.26, -106.36) * mm, "end": v(-61.4, -106.36) * mm});
            skLineSegment(sketch, "E7.17.4.3", {"start": v(-61.4, -106.36) * mm, "end": v(-62.99, -103.63) * mm});
            skLineSegment(sketch, "E8.0.0.4", {"start": v(-128.72, -96.58) * mm, "end": v(-125.57, -96.58) * mm});
            skLineSegment(sketch, "E8.3.0.4", {"start": v(-125.57, -96.58) * mm, "end": v(-124, -99.31) * mm});
            skLineSegment(sketch, "E8.6.0.4", {"start": v(-124, -99.31) * mm, "end": v(-125.57, -102.04) * mm});
            skCircle(sketch, "E8.9.0.4", {"center": v(-127.14, -99.31) * mm, "radius": 2.73 * mm, "construction": true});
            skLineSegment(sketch, "E8.11.0.4", {"start": v(-125.57, -102.04) * mm, "end": v(-128.72, -102.04) * mm});
            skLineSegment(sketch, "E8.14.0.4", {"start": v(-128.72, -102.04) * mm, "end": v(-130.3, -99.31) * mm});
            skLineSegment(sketch, "E8.17.0.4", {"start": v(-130.3, -99.31) * mm, "end": v(-128.72, -96.58) * mm});
            skLineSegment(sketch, "E8.0.0.5", {"start": v(-128.72, -87.95) * mm, "end": v(-125.57, -87.95) * mm});
            skLineSegment(sketch, "E8.3.0.5", {"start": v(-125.57, -87.95) * mm, "end": v(-124, -90.68) * mm});
            skLineSegment(sketch, "E8.6.0.5", {"start": v(-124, -90.68) * mm, "end": v(-125.57, -93.4) * mm});
            skCircle(sketch, "E8.9.0.5", {"center": v(-127.14, -90.68) * mm, "radius": 2.73 * mm, "construction": true});
            skLineSegment(sketch, "E8.11.0.5", {"start": v(-125.57, -93.4) * mm, "end": v(-128.72, -93.4) * mm});
            skLineSegment(sketch, "E8.14.0.5", {"start": v(-128.72, -93.4) * mm, "end": v(-130.3, -90.68) * mm});
            skLineSegment(sketch, "E8.17.0.5", {"start": v(-130.3, -90.68) * mm, "end": v(-128.72, -87.95) * mm});
            skLineSegment(sketch, "E8.0.0.6", {"start": v(-128.72, -79.31) * mm, "end": v(-125.57, -79.31) * mm});
            skLineSegment(sketch, "E8.3.0.6", {"start": v(-125.57, -79.31) * mm, "end": v(-124, -82.04) * mm});
            skLineSegment(sketch, "E8.6.0.6", {"start": v(-124, -82.04) * mm, "end": v(-125.57, -84.77) * mm});
            skCircle(sketch, "E8.9.0.6", {"center": v(-127.14, -82.04) * mm, "radius": 2.73 * mm, "construction": true});
            skLineSegment(sketch, "E8.11.0.6", {"start": v(-125.57, -84.77) * mm, "end": v(-128.72, -84.77) * mm});
            skLineSegment(sketch, "E8.14.0.6", {"start": v(-128.72, -84.77) * mm, "end": v(-130.3, -82.04) * mm});
            skLineSegment(sketch, "E8.17.0.6", {"start": v(-130.3, -82.04) * mm, "end": v(-128.72, -79.31) * mm});
            skLineSegment(sketch, "E8.0.0.7", {"start": v(-128.72, -70.68) * mm, "end": v(-125.57, -70.68) * mm});
            skLineSegment(sketch, "E8.3.0.7", {"start": v(-125.57, -70.68) * mm, "end": v(-124, -73.4) * mm});
            skLineSegment(sketch, "E8.6.0.7", {"start": v(-124, -73.4) * mm, "end": v(-125.57, -76.14) * mm});
            skCircle(sketch, "E8.9.0.7", {"center": v(-127.14, -73.4) * mm, "radius": 2.73 * mm, "construction": true});
            skLineSegment(sketch, "E8.11.0.7", {"start": v(-125.57, -76.14) * mm, "end": v(-128.72, -76.14) * mm});
            skLineSegment(sketch, "E8.14.0.7", {"start": v(-128.72, -76.14) * mm, "end": v(-130.3, -73.4) * mm});
            skLineSegment(sketch, "E8.17.0.7", {"start": v(-130.3, -73.4) * mm, "end": v(-128.72, -70.68) * mm});
            skLineSegment(sketch, "E8.0.1.4", {"start": v(-113.76, -96.58) * mm, "end": v(-110.6, -96.58) * mm});
            skLineSegment(sketch, "E8.3.1.4", {"start": v(-110.6, -96.58) * mm, "end": v(-109.03, -99.31) * mm});
            skLineSegment(sketch, "E8.6.1.4", {"start": v(-109.03, -99.31) * mm, "end": v(-110.6, -102.04) * mm});
            skCircle(sketch, "E8.9.1.4", {"center": v(-112.19, -99.31) * mm, "radius": 2.73 * mm, "construction": true});
            skLineSegment(sketch, "E8.11.1.4", {"start": v(-110.6, -102.04) * mm, "end": v(-113.76, -102.04) * mm});
            skLineSegment(sketch, "E8.14.1.4", {"start": v(-113.76, -102.04) * mm, "end": v(-115.34, -99.31) * mm});
            skLineSegment(sketch, "E8.17.1.4", {"start": v(-115.34, -99.31) * mm, "end": v(-113.76, -96.58) * mm});
            skLineSegment(sketch, "E8.0.1.5", {"start": v(-113.76, -87.95) * mm, "end": v(-110.6, -87.95) * mm});
            skLineSegment(sketch, "E8.3.1.5", {"start": v(-110.6, -87.95) * mm, "end": v(-109.03, -90.68) * mm});
            skLineSegment(sketch, "E8.6.1.5", {"start": v(-109.03, -90.68) * mm, "end": v(-110.6, -93.4) * mm});
            skCircle(sketch, "E8.9.1.5", {"center": v(-112.19, -90.68) * mm, "radius": 2.73 * mm, "construction": true});
            skLineSegment(sketch, "E8.11.1.5", {"start": v(-110.6, -93.4) * mm, "end": v(-113.76, -93.4) * mm});
            skLineSegment(sketch, "E8.14.1.5", {"start": v(-113.76, -93.4) * mm, "end": v(-115.34, -90.68) * mm});
            skLineSegment(sketch, "E8.17.1.5", {"start": v(-115.34, -90.68) * mm, "end": v(-113.76, -87.95) * mm});
            skLineSegment(sketch, "E8.0.1.6", {"start": v(-113.76, -79.31) * mm, "end": v(-110.6, -79.31) * mm});
            skLineSegment(sketch, "E8.3.1.6", {"start": v(-110.6, -79.31) * mm, "end": v(-109.03, -82.04) * mm});
            skLineSegment(sketch, "E8.6.1.6", {"start": v(-109.03, -82.04) * mm, "end": v(-110.6, -84.77) * mm});
            skCircle(sketch, "E8.9.1.6", {"center": v(-112.19, -82.04) * mm, "radius": 2.73 * mm, "construction": true});
            skLineSegment(sketch, "E8.11.1.6", {"start": v(-110.6, -84.77) * mm, "end": v(-113.76, -84.77) * mm});
            skLineSegment(sketch, "E8.14.1.6", {"start": v(-113.76, -84.77) * mm, "end": v(-115.34, -82.04) * mm});
            skLineSegment(sketch, "E8.17.1.6", {"start": v(-115.34, -82.04) * mm, "end": v(-113.76, -79.31) * mm});
            skLineSegment(sketch, "E8.0.1.7", {"start": v(-113.76, -70.68) * mm, "end": v(-110.6, -70.68) * mm});
            skLineSegment(sketch, "E8.3.1.7", {"start": v(-110.6, -70.68) * mm, "end": v(-109.03, -73.4) * mm});
            skLineSegment(sketch, "E8.6.1.7", {"start": v(-109.03, -73.4) * mm, "end": v(-110.6, -76.14) * mm});
            skCircle(sketch, "E8.9.1.7", {"center": v(-112.19, -73.4) * mm, "radius": 2.73 * mm, "construction": true});
            skLineSegment(sketch, "E8.11.1.7", {"start": v(-110.6, -76.14) * mm, "end": v(-113.76, -76.14) * mm});
            skLineSegment(sketch, "E8.14.1.7", {"start": v(-113.76, -76.14) * mm, "end": v(-115.34, -73.4) * mm});
            skLineSegment(sketch, "E8.17.1.7", {"start": v(-115.34, -73.4) * mm, "end": v(-113.76, -70.68) * mm});
            skLineSegment(sketch, "E8.0.2.4", {"start": v(-98.8, -96.58) * mm, "end": v(-95.65, -96.58) * mm});
            skLineSegment(sketch, "E8.3.2.4", {"start": v(-95.65, -96.58) * mm, "end": v(-94.07, -99.31) * mm});
            skLineSegment(sketch, "E8.6.2.4", {"start": v(-94.07, -99.31) * mm, "end": v(-95.65, -102.04) * mm});
            skCircle(sketch, "E8.9.2.4", {"center": v(-97.23, -99.31) * mm, "radius": 2.73 * mm, "construction": true});
            skLineSegment(sketch, "E8.11.2.4", {"start": v(-95.65, -102.04) * mm, "end": v(-98.8, -102.04) * mm});
            skLineSegment(sketch, "E8.14.2.4", {"start": v(-98.8, -102.04) * mm, "end": v(-100.38, -99.31) * mm});
            skLineSegment(sketch, "E8.17.2.4", {"start": v(-100.38, -99.31) * mm, "end": v(-98.8, -96.58) * mm});
            skLineSegment(sketch, "E8.0.2.5", {"start": v(-98.8, -87.95) * mm, "end": v(-95.65, -87.95) * mm});
            skLineSegment(sketch, "E8.3.2.5", {"start": v(-95.65, -87.95) * mm, "end": v(-94.07, -90.68) * mm});
            skLineSegment(sketch, "E8.6.2.5", {"start": v(-94.07, -90.68) * mm, "end": v(-95.65, -93.4) * mm});
            skCircle(sketch, "E8.9.2.5", {"center": v(-97.23, -90.68) * mm, "radius": 2.73 * mm, "construction": true});
            skLineSegment(sketch, "E8.11.2.5", {"start": v(-95.65, -93.4) * mm, "end": v(-98.8, -93.4) * mm});
            skLineSegment(sketch, "E8.14.2.5", {"start": v(-98.8, -93.4) * mm, "end": v(-100.38, -90.68) * mm});
            skLineSegment(sketch, "E8.17.2.5", {"start": v(-100.38, -90.68) * mm, "end": v(-98.8, -87.95) * mm});
            skLineSegment(sketch, "E8.0.2.6", {"start": v(-98.8, -79.31) * mm, "end": v(-95.65, -79.31) * mm});
            skLineSegment(sketch, "E8.3.2.6", {"start": v(-95.65, -79.31) * mm, "end": v(-94.07, -82.04) * mm});
            skLineSegment(sketch, "E8.6.2.6", {"start": v(-94.07, -82.04) * mm, "end": v(-95.65, -84.77) * mm});
            skCircle(sketch, "E8.9.2.6", {"center": v(-97.23, -82.04) * mm, "radius": 2.73 * mm, "construction": true});
            skLineSegment(sketch, "E8.11.2.6", {"start": v(-95.65, -84.77) * mm, "end": v(-98.8, -84.77) * mm});
            skLineSegment(sketch, "E8.14.2.6", {"start": v(-98.8, -84.77) * mm, "end": v(-100.38, -82.04) * mm});
            skLineSegment(sketch, "E8.17.2.6", {"start": v(-100.38, -82.04) * mm, "end": v(-98.8, -79.31) * mm});
            skLineSegment(sketch, "E8.0.2.7", {"start": v(-98.8, -70.68) * mm, "end": v(-95.65, -70.68) * mm});
            skLineSegment(sketch, "E8.3.2.7", {"start": v(-95.65, -70.68) * mm, "end": v(-94.07, -73.4) * mm});
            skLineSegment(sketch, "E8.6.2.7", {"start": v(-94.07, -73.4) * mm, "end": v(-95.65, -76.14) * mm});
            skCircle(sketch, "E8.9.2.7", {"center": v(-97.23, -73.4) * mm, "radius": 2.73 * mm, "construction": true});
            skLineSegment(sketch, "E8.11.2.7", {"start": v(-95.65, -76.14) * mm, "end": v(-98.8, -76.14) * mm});
            skLineSegment(sketch, "E8.14.2.7", {"start": v(-98.8, -76.14) * mm, "end": v(-100.38, -73.4) * mm});
            skLineSegment(sketch, "E8.17.2.7", {"start": v(-100.38, -73.4) * mm, "end": v(-98.8, -70.68) * mm});
            skLineSegment(sketch, "E8.0.3.4", {"start": v(-83.85, -96.58) * mm, "end": v(-80.7, -96.58) * mm});
            skLineSegment(sketch, "E8.3.3.4", {"start": v(-80.7, -96.58) * mm, "end": v(-79.12, -99.31) * mm});
            skLineSegment(sketch, "E8.6.3.4", {"start": v(-79.12, -99.31) * mm, "end": v(-80.7, -102.04) * mm});
            skCircle(sketch, "E8.9.3.4", {"center": v(-82.27, -99.31) * mm, "radius": 2.73 * mm, "construction": true});
            skLineSegment(sketch, "E8.11.3.4", {"start": v(-80.7, -102.04) * mm, "end": v(-83.85, -102.04) * mm});
            skLineSegment(sketch, "E8.14.3.4", {"start": v(-83.85, -102.04) * mm, "end": v(-85.42, -99.31) * mm});
            skLineSegment(sketch, "E8.17.3.4", {"start": v(-85.42, -99.31) * mm, "end": v(-83.85, -96.58) * mm});
            skLineSegment(sketch, "E8.0.3.5", {"start": v(-83.85, -87.95) * mm, "end": v(-80.7, -87.95) * mm});
            skLineSegment(sketch, "E8.3.3.5", {"start": v(-80.7, -87.95) * mm, "end": v(-79.12, -90.68) * mm});
            skLineSegment(sketch, "E8.6.3.5", {"start": v(-79.12, -90.68) * mm, "end": v(-80.7, -93.4) * mm});
            skCircle(sketch, "E8.9.3.5", {"center": v(-82.27, -90.68) * mm, "radius": 2.73 * mm, "construction": true});
            skLineSegment(sketch, "E8.11.3.5", {"start": v(-80.7, -93.4) * mm, "end": v(-83.85, -93.4) * mm});
            skLineSegment(sketch, "E8.14.3.5", {"start": v(-83.85, -93.4) * mm, "end": v(-85.42, -90.68) * mm});
            skLineSegment(sketch, "E8.17.3.5", {"start": v(-85.42, -90.68) * mm, "end": v(-83.85, -87.95) * mm});
            skLineSegment(sketch, "E8.0.3.6", {"start": v(-83.85, -79.31) * mm, "end": v(-80.7, -79.31) * mm});
            skLineSegment(sketch, "E8.3.3.6", {"start": v(-80.7, -79.31) * mm, "end": v(-79.12, -82.04) * mm});
            skLineSegment(sketch, "E8.6.3.6", {"start": v(-79.12, -82.04) * mm, "end": v(-80.7, -84.77) * mm});
            skCircle(sketch, "E8.9.3.6", {"center": v(-82.27, -82.04) * mm, "radius": 2.73 * mm, "construction": true});
            skLineSegment(sketch, "E8.11.3.6", {"start": v(-80.7, -84.77) * mm, "end": v(-83.85, -84.77) * mm});
            skLineSegment(sketch, "E8.14.3.6", {"start": v(-83.85, -84.77) * mm, "end": v(-85.42, -82.04) * mm});
            skLineSegment(sketch, "E8.17.3.6", {"start": v(-85.42, -82.04) * mm, "end": v(-83.85, -79.31) * mm});
            skLineSegment(sketch, "E8.0.3.7", {"start": v(-83.85, -70.68) * mm, "end": v(-80.7, -70.68) * mm});
            skLineSegment(sketch, "E8.3.3.7", {"start": v(-80.7, -70.68) * mm, "end": v(-79.12, -73.4) * mm});
            skLineSegment(sketch, "E8.6.3.7", {"start": v(-79.12, -73.4) * mm, "end": v(-80.7, -76.14) * mm});
            skCircle(sketch, "E8.9.3.7", {"center": v(-82.27, -73.4) * mm, "radius": 2.73 * mm, "construction": true});
            skLineSegment(sketch, "E8.11.3.7", {"start": v(-80.7, -76.14) * mm, "end": v(-83.85, -76.14) * mm});
            skLineSegment(sketch, "E8.14.3.7", {"start": v(-83.85, -76.14) * mm, "end": v(-85.42, -73.4) * mm});
            skLineSegment(sketch, "E8.17.3.7", {"start": v(-85.42, -73.4) * mm, "end": v(-83.85, -70.68) * mm});
            skLineSegment(sketch, "E8.0.4.4", {"start": v(-68.89, -96.58) * mm, "end": v(-65.73, -96.58) * mm});
            skLineSegment(sketch, "E8.3.4.4", {"start": v(-65.73, -96.58) * mm, "end": v(-64.16, -99.31) * mm});
            skLineSegment(sketch, "E8.6.4.4", {"start": v(-64.16, -99.31) * mm, "end": v(-65.73, -102.04) * mm});
            skCircle(sketch, "E8.9.4.4", {"center": v(-67.31, -99.31) * mm, "radius": 2.73 * mm, "construction": true});
            skLineSegment(sketch, "E8.11.4.4", {"start": v(-65.73, -102.04) * mm, "end": v(-68.89, -102.04) * mm});
            skLineSegment(sketch, "E8.14.4.4", {"start": v(-68.89, -102.04) * mm, "end": v(-70.46, -99.31) * mm});
            skLineSegment(sketch, "E8.17.4.4", {"start": v(-70.46, -99.31) * mm, "end": v(-68.89, -96.58) * mm});
            skLineSegment(sketch, "E8.0.4.5", {"start": v(-68.89, -87.95) * mm, "end": v(-65.73, -87.95) * mm});
            skLineSegment(sketch, "E8.3.4.5", {"start": v(-65.73, -87.95) * mm, "end": v(-64.16, -90.68) * mm});
            skLineSegment(sketch, "E8.6.4.5", {"start": v(-64.16, -90.68) * mm, "end": v(-65.73, -93.4) * mm});
            skCircle(sketch, "E8.9.4.5", {"center": v(-67.31, -90.68) * mm, "radius": 2.73 * mm, "construction": true});
            skLineSegment(sketch, "E8.11.4.5", {"start": v(-65.73, -93.4) * mm, "end": v(-68.89, -93.4) * mm});
            skLineSegment(sketch, "E8.14.4.5", {"start": v(-68.89, -93.4) * mm, "end": v(-70.46, -90.68) * mm});
            skLineSegment(sketch, "E8.17.4.5", {"start": v(-70.46, -90.68) * mm, "end": v(-68.89, -87.95) * mm});
            skLineSegment(sketch, "E8.0.4.6", {"start": v(-68.89, -79.31) * mm, "end": v(-65.73, -79.31) * mm});
            skLineSegment(sketch, "E8.3.4.6", {"start": v(-65.73, -79.31) * mm, "end": v(-64.16, -82.04) * mm});
            skLineSegment(sketch, "E8.6.4.6", {"start": v(-64.16, -82.04) * mm, "end": v(-65.73, -84.77) * mm});
            skCircle(sketch, "E8.9.4.6", {"center": v(-67.31, -82.04) * mm, "radius": 2.73 * mm, "construction": true});
            skLineSegment(sketch, "E8.11.4.6", {"start": v(-65.73, -84.77) * mm, "end": v(-68.89, -84.77) * mm});
            skLineSegment(sketch, "E8.14.4.6", {"start": v(-68.89, -84.77) * mm, "end": v(-70.46, -82.04) * mm});
            skLineSegment(sketch, "E8.17.4.6", {"start": v(-70.46, -82.04) * mm, "end": v(-68.89, -79.31) * mm});
            skLineSegment(sketch, "E8.0.4.7", {"start": v(-68.89, -70.68) * mm, "end": v(-65.73, -70.68) * mm});
            skLineSegment(sketch, "E8.3.4.7", {"start": v(-65.73, -70.68) * mm, "end": v(-64.16, -73.4) * mm});
            skLineSegment(sketch, "E8.6.4.7", {"start": v(-64.16, -73.4) * mm, "end": v(-65.73, -76.14) * mm});
            skCircle(sketch, "E8.9.4.7", {"center": v(-67.31, -73.4) * mm, "radius": 2.73 * mm, "construction": true});
            skLineSegment(sketch, "E8.11.4.7", {"start": v(-65.73, -76.14) * mm, "end": v(-68.89, -76.14) * mm});
            skLineSegment(sketch, "E8.14.4.7", {"start": v(-68.89, -76.14) * mm, "end": v(-70.46, -73.4) * mm});
            skLineSegment(sketch, "E8.17.4.7", {"start": v(-70.46, -73.4) * mm, "end": v(-68.89, -70.68) * mm});
            skLineSegment(sketch, "E8.0.5.4", {"start": v(-53.93, -96.58) * mm, "end": v(-50.78, -96.58) * mm});
            skLineSegment(sketch, "E8.3.5.4", {"start": v(-50.78, -96.58) * mm, "end": v(-49.2, -99.31) * mm});
            skLineSegment(sketch, "E8.6.5.4", {"start": v(-49.2, -99.31) * mm, "end": v(-50.78, -102.04) * mm});
            skCircle(sketch, "E8.9.5.4", {"center": v(-52.35, -99.31) * mm, "radius": 2.73 * mm, "construction": true});
            skLineSegment(sketch, "E8.11.5.4", {"start": v(-50.78, -102.04) * mm, "end": v(-53.93, -102.04) * mm});
            skLineSegment(sketch, "E8.14.5.4", {"start": v(-53.93, -102.04) * mm, "end": v(-55.5, -99.31) * mm});
            skLineSegment(sketch, "E8.17.5.4", {"start": v(-55.5, -99.31) * mm, "end": v(-53.93, -96.58) * mm});
            skLineSegment(sketch, "E8.0.5.5", {"start": v(-53.93, -87.95) * mm, "end": v(-50.78, -87.95) * mm});
            skLineSegment(sketch, "E8.3.5.5", {"start": v(-50.78, -87.95) * mm, "end": v(-49.2, -90.68) * mm});
            skLineSegment(sketch, "E8.6.5.5", {"start": v(-49.2, -90.68) * mm, "end": v(-50.78, -93.4) * mm});
            skCircle(sketch, "E8.9.5.5", {"center": v(-52.35, -90.68) * mm, "radius": 2.73 * mm, "construction": true});
            skLineSegment(sketch, "E8.11.5.5", {"start": v(-50.78, -93.4) * mm, "end": v(-53.93, -93.4) * mm});
            skLineSegment(sketch, "E8.14.5.5", {"start": v(-53.93, -93.4) * mm, "end": v(-55.5, -90.68) * mm});
            skLineSegment(sketch, "E8.17.5.5", {"start": v(-55.5, -90.68) * mm, "end": v(-53.93, -87.95) * mm});
            skLineSegment(sketch, "E8.0.5.6", {"start": v(-53.93, -79.31) * mm, "end": v(-50.78, -79.31) * mm});
            skLineSegment(sketch, "E8.3.5.6", {"start": v(-50.78, -79.31) * mm, "end": v(-49.2, -82.04) * mm});
            skLineSegment(sketch, "E8.6.5.6", {"start": v(-49.2, -82.04) * mm, "end": v(-50.78, -84.77) * mm});
            skCircle(sketch, "E8.9.5.6", {"center": v(-52.35, -82.04) * mm, "radius": 2.73 * mm, "construction": true});
            skLineSegment(sketch, "E8.11.5.6", {"start": v(-50.78, -84.77) * mm, "end": v(-53.93, -84.77) * mm});
            skLineSegment(sketch, "E8.14.5.6", {"start": v(-53.93, -84.77) * mm, "end": v(-55.5, -82.04) * mm});
            skLineSegment(sketch, "E8.17.5.6", {"start": v(-55.5, -82.04) * mm, "end": v(-53.93, -79.31) * mm});
            skLineSegment(sketch, "E8.0.5.7", {"start": v(-53.93, -70.68) * mm, "end": v(-50.78, -70.68) * mm});
            skLineSegment(sketch, "E8.3.5.7", {"start": v(-50.78, -70.68) * mm, "end": v(-49.2, -73.4) * mm});
            skLineSegment(sketch, "E8.6.5.7", {"start": v(-49.2, -73.4) * mm, "end": v(-50.78, -76.14) * mm});
            skCircle(sketch, "E8.9.5.7", {"center": v(-52.35, -73.4) * mm, "radius": 2.73 * mm, "construction": true});
            skLineSegment(sketch, "E8.11.5.7", {"start": v(-50.78, -76.14) * mm, "end": v(-53.93, -76.14) * mm});
            skLineSegment(sketch, "E8.14.5.7", {"start": v(-53.93, -76.14) * mm, "end": v(-55.5, -73.4) * mm});
            skLineSegment(sketch, "E8.17.5.7", {"start": v(-55.5, -73.4) * mm, "end": v(-53.93, -70.68) * mm});
            skCircle(sketch, "E9.0.0.4", {"center": v(-119.66, -95) * mm, "radius": 2.73 * mm, "construction": true});
            skLineSegment(sketch, "E9.2.0.4", {"start": v(-122.82, -95) * mm, "end": v(-121.24, -92.27) * mm});
            skLineSegment(sketch, "E9.5.0.4", {"start": v(-121.24, -92.27) * mm, "end": v(-118.09, -92.27) * mm});
            skLineSegment(sketch, "E9.8.0.4", {"start": v(-118.09, -92.27) * mm, "end": v(-116.51, -95) * mm});
            skLineSegment(sketch, "E9.11.0.4", {"start": v(-116.51, -95) * mm, "end": v(-118.09, -97.73) * mm});
            skLineSegment(sketch, "E9.14.0.4", {"start": v(-118.09, -97.73) * mm, "end": v(-121.24, -97.73) * mm});
            skLineSegment(sketch, "E9.17.0.4", {"start": v(-121.24, -97.73) * mm, "end": v(-122.82, -95) * mm});
            skCircle(sketch, "E9.0.0.5", {"center": v(-119.66, -86.36) * mm, "radius": 2.73 * mm, "construction": true});
            skLineSegment(sketch, "E9.2.0.5", {"start": v(-122.82, -86.36) * mm, "end": v(-121.24, -83.63) * mm});
            skLineSegment(sketch, "E9.5.0.5", {"start": v(-121.24, -83.63) * mm, "end": v(-118.09, -83.63) * mm});
            skLineSegment(sketch, "E9.8.0.5", {"start": v(-118.09, -83.63) * mm, "end": v(-116.51, -86.36) * mm});
            skLineSegment(sketch, "E9.11.0.5", {"start": v(-116.51, -86.36) * mm, "end": v(-118.09, -89.1) * mm});
            skLineSegment(sketch, "E9.14.0.5", {"start": v(-118.09, -89.1) * mm, "end": v(-121.24, -89.1) * mm});
            skLineSegment(sketch, "E9.17.0.5", {"start": v(-121.24, -89.1) * mm, "end": v(-122.82, -86.36) * mm});
            skCircle(sketch, "E9.0.0.6", {"center": v(-119.66, -77.72) * mm, "radius": 2.73 * mm, "construction": true});
            skLineSegment(sketch, "E9.2.0.6", {"start": v(-122.82, -77.72) * mm, "end": v(-121.24, -75) * mm});
            skLineSegment(sketch, "E9.5.0.6", {"start": v(-121.24, -75) * mm, "end": v(-118.09, -75) * mm});
            skLineSegment(sketch, "E9.8.0.6", {"start": v(-118.09, -75) * mm, "end": v(-116.51, -77.72) * mm});
            skLineSegment(sketch, "E9.11.0.6", {"start": v(-116.51, -77.72) * mm, "end": v(-118.09, -80.45) * mm});
            skLineSegment(sketch, "E9.14.0.6", {"start": v(-118.09, -80.45) * mm, "end": v(-121.24, -80.45) * mm});
            skLineSegment(sketch, "E9.17.0.6", {"start": v(-121.24, -80.45) * mm, "end": v(-122.82, -77.72) * mm});
            skCircle(sketch, "E9.0.1.4", {"center": v(-104.7, -95) * mm, "radius": 2.73 * mm, "construction": true});
            skLineSegment(sketch, "E9.2.1.4", {"start": v(-107.86, -95) * mm, "end": v(-106.28, -92.27) * mm});
            skLineSegment(sketch, "E9.5.1.4", {"start": v(-106.28, -92.27) * mm, "end": v(-103.13, -92.27) * mm});
            skLineSegment(sketch, "E9.8.1.4", {"start": v(-103.13, -92.27) * mm, "end": v(-101.55, -95) * mm});
            skLineSegment(sketch, "E9.11.1.4", {"start": v(-101.55, -95) * mm, "end": v(-103.13, -97.73) * mm});
            skLineSegment(sketch, "E9.14.1.4", {"start": v(-103.13, -97.73) * mm, "end": v(-106.28, -97.73) * mm});
            skLineSegment(sketch, "E9.17.1.4", {"start": v(-106.28, -97.73) * mm, "end": v(-107.86, -95) * mm});
            skCircle(sketch, "E9.0.1.5", {"center": v(-104.7, -86.36) * mm, "radius": 2.73 * mm, "construction": true});
            skLineSegment(sketch, "E9.2.1.5", {"start": v(-107.86, -86.36) * mm, "end": v(-106.28, -83.63) * mm});
            skLineSegment(sketch, "E9.5.1.5", {"start": v(-106.28, -83.63) * mm, "end": v(-103.13, -83.63) * mm});
            skLineSegment(sketch, "E9.8.1.5", {"start": v(-103.13, -83.63) * mm, "end": v(-101.55, -86.36) * mm});
            skLineSegment(sketch, "E9.11.1.5", {"start": v(-101.55, -86.36) * mm, "end": v(-103.13, -89.1) * mm});
            skLineSegment(sketch, "E9.14.1.5", {"start": v(-103.13, -89.1) * mm, "end": v(-106.28, -89.1) * mm});
            skLineSegment(sketch, "E9.17.1.5", {"start": v(-106.28, -89.1) * mm, "end": v(-107.86, -86.36) * mm});
            skCircle(sketch, "E9.0.1.6", {"center": v(-104.7, -77.72) * mm, "radius": 2.73 * mm, "construction": true});
            skLineSegment(sketch, "E9.2.1.6", {"start": v(-107.86, -77.72) * mm, "end": v(-106.28, -75) * mm});
            skLineSegment(sketch, "E9.5.1.6", {"start": v(-106.28, -75) * mm, "end": v(-103.13, -75) * mm});
            skLineSegment(sketch, "E9.8.1.6", {"start": v(-103.13, -75) * mm, "end": v(-101.55, -77.72) * mm});
            skLineSegment(sketch, "E9.11.1.6", {"start": v(-101.55, -77.72) * mm, "end": v(-103.13, -80.45) * mm});
            skLineSegment(sketch, "E9.14.1.6", {"start": v(-103.13, -80.45) * mm, "end": v(-106.28, -80.45) * mm});
            skLineSegment(sketch, "E9.17.1.6", {"start": v(-106.28, -80.45) * mm, "end": v(-107.86, -77.72) * mm});
            skCircle(sketch, "E9.0.2.4", {"center": v(-89.75, -95) * mm, "radius": 2.73 * mm, "construction": true});
            skLineSegment(sketch, "E9.2.2.4", {"start": v(-92.9, -95) * mm, "end": v(-91.32, -92.27) * mm});
            skLineSegment(sketch, "E9.5.2.4", {"start": v(-91.32, -92.27) * mm, "end": v(-88.17, -92.27) * mm});
            skLineSegment(sketch, "E9.8.2.4", {"start": v(-88.17, -92.27) * mm, "end": v(-86.6, -95) * mm});
            skLineSegment(sketch, "E9.11.2.4", {"start": v(-86.6, -95) * mm, "end": v(-88.17, -97.73) * mm});
            skLineSegment(sketch, "E9.14.2.4", {"start": v(-88.17, -97.73) * mm, "end": v(-91.32, -97.73) * mm});
            skLineSegment(sketch, "E9.17.2.4", {"start": v(-91.32, -97.73) * mm, "end": v(-92.9, -95) * mm});
            skCircle(sketch, "E9.0.2.5", {"center": v(-89.75, -86.36) * mm, "radius": 2.73 * mm, "construction": true});
            skLineSegment(sketch, "E9.2.2.5", {"start": v(-92.9, -86.36) * mm, "end": v(-91.32, -83.63) * mm});
            skLineSegment(sketch, "E9.5.2.5", {"start": v(-91.32, -83.63) * mm, "end": v(-88.17, -83.63) * mm});
            skLineSegment(sketch, "E9.8.2.5", {"start": v(-88.17, -83.63) * mm, "end": v(-86.6, -86.36) * mm});
            skLineSegment(sketch, "E9.11.2.5", {"start": v(-86.6, -86.36) * mm, "end": v(-88.17, -89.1) * mm});
            skLineSegment(sketch, "E9.14.2.5", {"start": v(-88.17, -89.1) * mm, "end": v(-91.32, -89.1) * mm});
            skLineSegment(sketch, "E9.17.2.5", {"start": v(-91.32, -89.1) * mm, "end": v(-92.9, -86.36) * mm});
            skCircle(sketch, "E9.0.2.6", {"center": v(-89.75, -77.72) * mm, "radius": 2.73 * mm, "construction": true});
            skLineSegment(sketch, "E9.2.2.6", {"start": v(-92.9, -77.72) * mm, "end": v(-91.32, -75) * mm});
            skLineSegment(sketch, "E9.5.2.6", {"start": v(-91.32, -75) * mm, "end": v(-88.17, -75) * mm});
            skLineSegment(sketch, "E9.8.2.6", {"start": v(-88.17, -75) * mm, "end": v(-86.6, -77.72) * mm});
            skLineSegment(sketch, "E9.11.2.6", {"start": v(-86.6, -77.72) * mm, "end": v(-88.17, -80.45) * mm});
            skLineSegment(sketch, "E9.14.2.6", {"start": v(-88.17, -80.45) * mm, "end": v(-91.32, -80.45) * mm});
            skLineSegment(sketch, "E9.17.2.6", {"start": v(-91.32, -80.45) * mm, "end": v(-92.9, -77.72) * mm});
            skCircle(sketch, "E9.0.3.4", {"center": v(-74.8, -95) * mm, "radius": 2.73 * mm, "construction": true});
            skLineSegment(sketch, "E9.2.3.4", {"start": v(-77.94, -95) * mm, "end": v(-76.37, -92.27) * mm});
            skLineSegment(sketch, "E9.5.3.4", {"start": v(-76.37, -92.27) * mm, "end": v(-73.21, -92.27) * mm});
            skLineSegment(sketch, "E9.8.3.4", {"start": v(-73.21, -92.27) * mm, "end": v(-71.64, -95) * mm});
            skLineSegment(sketch, "E9.11.3.4", {"start": v(-71.64, -95) * mm, "end": v(-73.21, -97.73) * mm});
            skLineSegment(sketch, "E9.14.3.4", {"start": v(-73.21, -97.73) * mm, "end": v(-76.37, -97.73) * mm});
            skLineSegment(sketch, "E9.17.3.4", {"start": v(-76.37, -97.73) * mm, "end": v(-77.94, -95) * mm});
            skCircle(sketch, "E9.0.3.5", {"center": v(-74.8, -86.36) * mm, "radius": 2.73 * mm, "construction": true});
            skLineSegment(sketch, "E9.2.3.5", {"start": v(-77.94, -86.36) * mm, "end": v(-76.37, -83.63) * mm});
            skLineSegment(sketch, "E9.5.3.5", {"start": v(-76.37, -83.63) * mm, "end": v(-73.21, -83.63) * mm});
            skLineSegment(sketch, "E9.8.3.5", {"start": v(-73.21, -83.63) * mm, "end": v(-71.64, -86.36) * mm});
            skLineSegment(sketch, "E9.11.3.5", {"start": v(-71.64, -86.36) * mm, "end": v(-73.21, -89.1) * mm});
            skLineSegment(sketch, "E9.14.3.5", {"start": v(-73.21, -89.1) * mm, "end": v(-76.37, -89.1) * mm});
            skLineSegment(sketch, "E9.17.3.5", {"start": v(-76.37, -89.1) * mm, "end": v(-77.94, -86.36) * mm});
            skCircle(sketch, "E9.0.3.6", {"center": v(-74.8, -77.72) * mm, "radius": 2.73 * mm, "construction": true});
            skLineSegment(sketch, "E9.2.3.6", {"start": v(-77.94, -77.72) * mm, "end": v(-76.37, -75) * mm});
            skLineSegment(sketch, "E9.5.3.6", {"start": v(-76.37, -75) * mm, "end": v(-73.21, -75) * mm});
            skLineSegment(sketch, "E9.8.3.6", {"start": v(-73.21, -75) * mm, "end": v(-71.64, -77.72) * mm});
            skLineSegment(sketch, "E9.11.3.6", {"start": v(-71.64, -77.72) * mm, "end": v(-73.21, -80.45) * mm});
            skLineSegment(sketch, "E9.14.3.6", {"start": v(-73.21, -80.45) * mm, "end": v(-76.37, -80.45) * mm});
            skLineSegment(sketch, "E9.17.3.6", {"start": v(-76.37, -80.45) * mm, "end": v(-77.94, -77.72) * mm});
            skCircle(sketch, "E9.0.4.4", {"center": v(-59.83, -95) * mm, "radius": 2.73 * mm, "construction": true});
            skLineSegment(sketch, "E9.2.4.4", {"start": v(-62.99, -95) * mm, "end": v(-61.4, -92.27) * mm});
            skLineSegment(sketch, "E9.5.4.4", {"start": v(-61.4, -92.27) * mm, "end": v(-58.26, -92.27) * mm});
            skLineSegment(sketch, "E9.8.4.4", {"start": v(-58.26, -92.27) * mm, "end": v(-56.68, -95) * mm});
            skLineSegment(sketch, "E9.11.4.4", {"start": v(-56.68, -95) * mm, "end": v(-58.26, -97.73) * mm});
            skLineSegment(sketch, "E9.14.4.4", {"start": v(-58.26, -97.73) * mm, "end": v(-61.4, -97.73) * mm});
            skLineSegment(sketch, "E9.17.4.4", {"start": v(-61.4, -97.73) * mm, "end": v(-62.99, -95) * mm});
            skCircle(sketch, "E9.0.4.5", {"center": v(-59.83, -86.36) * mm, "radius": 2.73 * mm, "construction": true});
            skLineSegment(sketch, "E9.2.4.5", {"start": v(-62.99, -86.36) * mm, "end": v(-61.4, -83.63) * mm});
            skLineSegment(sketch, "E9.5.4.5", {"start": v(-61.4, -83.63) * mm, "end": v(-58.26, -83.63) * mm});
            skLineSegment(sketch, "E9.8.4.5", {"start": v(-58.26, -83.63) * mm, "end": v(-56.68, -86.36) * mm});
            skLineSegment(sketch, "E9.11.4.5", {"start": v(-56.68, -86.36) * mm, "end": v(-58.26, -89.1) * mm});
            skLineSegment(sketch, "E9.14.4.5", {"start": v(-58.26, -89.1) * mm, "end": v(-61.4, -89.1) * mm});
            skLineSegment(sketch, "E9.17.4.5", {"start": v(-61.4, -89.1) * mm, "end": v(-62.99, -86.36) * mm});
            skCircle(sketch, "E9.0.4.6", {"center": v(-59.83, -77.72) * mm, "radius": 2.73 * mm, "construction": true});
            skLineSegment(sketch, "E9.2.4.6", {"start": v(-62.99, -77.72) * mm, "end": v(-61.4, -75) * mm});
            skLineSegment(sketch, "E9.5.4.6", {"start": v(-61.4, -75) * mm, "end": v(-58.26, -75) * mm});
            skLineSegment(sketch, "E9.8.4.6", {"start": v(-58.26, -75) * mm, "end": v(-56.68, -77.72) * mm});
            skLineSegment(sketch, "E9.11.4.6", {"start": v(-56.68, -77.72) * mm, "end": v(-58.26, -80.45) * mm});
            skLineSegment(sketch, "E9.14.4.6", {"start": v(-58.26, -80.45) * mm, "end": v(-61.4, -80.45) * mm});
            skLineSegment(sketch, "E9.17.4.6", {"start": v(-61.4, -80.45) * mm, "end": v(-62.99, -77.72) * mm});
            skCircle(sketch, "E10.0.0.7", {"center": v(-119.66, -69.09) * mm, "radius": 2.73 * mm, "construction": true});
            skLineSegment(sketch, "E10.2.0.7", {"start": v(-122.82, -69.09) * mm, "end": v(-121.24, -66.36) * mm});
            skLineSegment(sketch, "E10.5.0.7", {"start": v(-121.24, -66.36) * mm, "end": v(-118.09, -66.36) * mm});
            skLineSegment(sketch, "E10.8.0.7", {"start": v(-118.09, -66.36) * mm, "end": v(-116.51, -69.09) * mm});
            skLineSegment(sketch, "E10.11.0.7", {"start": v(-116.51, -69.09) * mm, "end": v(-118.09, -71.82) * mm});
            skLineSegment(sketch, "E10.14.0.7", {"start": v(-118.09, -71.82) * mm, "end": v(-121.24, -71.82) * mm});
            skLineSegment(sketch, "E10.17.0.7", {"start": v(-121.24, -71.82) * mm, "end": v(-122.82, -69.09) * mm});
            skCircle(sketch, "E10.0.1.7", {"center": v(-104.7, -69.09) * mm, "radius": 2.73 * mm, "construction": true});
            skLineSegment(sketch, "E10.2.1.7", {"start": v(-107.86, -69.09) * mm, "end": v(-106.28, -66.36) * mm});
            skLineSegment(sketch, "E10.5.1.7", {"start": v(-106.28, -66.36) * mm, "end": v(-103.13, -66.36) * mm});
            skLineSegment(sketch, "E10.8.1.7", {"start": v(-103.13, -66.36) * mm, "end": v(-101.55, -69.09) * mm});
            skLineSegment(sketch, "E10.11.1.7", {"start": v(-101.55, -69.09) * mm, "end": v(-103.13, -71.82) * mm});
            skLineSegment(sketch, "E10.14.1.7", {"start": v(-103.13, -71.82) * mm, "end": v(-106.28, -71.82) * mm});
            skLineSegment(sketch, "E10.17.1.7", {"start": v(-106.28, -71.82) * mm, "end": v(-107.86, -69.09) * mm});
            skCircle(sketch, "E10.0.2.7", {"center": v(-89.75, -69.09) * mm, "radius": 2.73 * mm, "construction": true});
            skLineSegment(sketch, "E10.2.2.7", {"start": v(-92.9, -69.09) * mm, "end": v(-91.32, -66.36) * mm});
            skLineSegment(sketch, "E10.5.2.7", {"start": v(-91.32, -66.36) * mm, "end": v(-88.17, -66.36) * mm});
            skLineSegment(sketch, "E10.8.2.7", {"start": v(-88.17, -66.36) * mm, "end": v(-86.6, -69.09) * mm});
            skLineSegment(sketch, "E10.11.2.7", {"start": v(-86.6, -69.09) * mm, "end": v(-88.17, -71.82) * mm});
            skLineSegment(sketch, "E10.14.2.7", {"start": v(-88.17, -71.82) * mm, "end": v(-91.32, -71.82) * mm});
            skLineSegment(sketch, "E10.17.2.7", {"start": v(-91.32, -71.82) * mm, "end": v(-92.9, -69.09) * mm});
            skCircle(sketch, "E10.0.3.7", {"center": v(-74.8, -69.09) * mm, "radius": 2.73 * mm, "construction": true});
            skLineSegment(sketch, "E10.2.3.7", {"start": v(-77.94, -69.09) * mm, "end": v(-76.37, -66.36) * mm});
            skLineSegment(sketch, "E10.5.3.7", {"start": v(-76.37, -66.36) * mm, "end": v(-73.21, -66.36) * mm});
            skLineSegment(sketch, "E10.8.3.7", {"start": v(-73.21, -66.36) * mm, "end": v(-71.64, -69.09) * mm});
            skLineSegment(sketch, "E10.11.3.7", {"start": v(-71.64, -69.09) * mm, "end": v(-73.21, -71.82) * mm});
            skLineSegment(sketch, "E10.14.3.7", {"start": v(-73.21, -71.82) * mm, "end": v(-76.37, -71.82) * mm});
            skLineSegment(sketch, "E10.17.3.7", {"start": v(-76.37, -71.82) * mm, "end": v(-77.94, -69.09) * mm});
            skCircle(sketch, "E10.0.4.7", {"center": v(-59.83, -69.09) * mm, "radius": 2.73 * mm, "construction": true});
            skLineSegment(sketch, "E10.2.4.7", {"start": v(-62.99, -69.09) * mm, "end": v(-61.4, -66.36) * mm});
            skLineSegment(sketch, "E10.5.4.7", {"start": v(-61.4, -66.36) * mm, "end": v(-58.26, -66.36) * mm});
            skLineSegment(sketch, "E10.8.4.7", {"start": v(-58.26, -66.36) * mm, "end": v(-56.68, -69.09) * mm});
            skLineSegment(sketch, "E10.11.4.7", {"start": v(-56.68, -69.09) * mm, "end": v(-58.26, -71.82) * mm});
            skLineSegment(sketch, "E10.14.4.7", {"start": v(-58.26, -71.82) * mm, "end": v(-61.4, -71.82) * mm});
            skLineSegment(sketch, "E10.17.4.7", {"start": v(-61.4, -71.82) * mm, "end": v(-62.99, -69.09) * mm});
            skLineSegment(sketch, "E11.0.0.8", {"start": v(-128.72, -62.04) * mm, "end": v(-125.57, -62.04) * mm});
            skLineSegment(sketch, "E11.3.0.8", {"start": v(-125.57, -62.04) * mm, "end": v(-124, -64.77) * mm});
            skLineSegment(sketch, "E11.6.0.8", {"start": v(-124, -64.77) * mm, "end": v(-125.57, -67.5) * mm});
            skCircle(sketch, "E11.9.0.8", {"center": v(-127.14, -64.77) * mm, "radius": 2.73 * mm, "construction": true});
            skLineSegment(sketch, "E11.11.0.8", {"start": v(-125.57, -67.5) * mm, "end": v(-128.72, -67.5) * mm});
            skLineSegment(sketch, "E11.14.0.8", {"start": v(-128.72, -67.5) * mm, "end": v(-130.3, -64.77) * mm});
            skLineSegment(sketch, "E11.17.0.8", {"start": v(-130.3, -64.77) * mm, "end": v(-128.72, -62.04) * mm});
            skLineSegment(sketch, "E11.0.1.8", {"start": v(-113.76, -62.04) * mm, "end": v(-110.6, -62.04) * mm});
            skLineSegment(sketch, "E11.3.1.8", {"start": v(-110.6, -62.04) * mm, "end": v(-109.03, -64.77) * mm});
            skLineSegment(sketch, "E11.6.1.8", {"start": v(-109.03, -64.77) * mm, "end": v(-110.6, -67.5) * mm});
            skCircle(sketch, "E11.9.1.8", {"center": v(-112.19, -64.77) * mm, "radius": 2.73 * mm, "construction": true});
            skLineSegment(sketch, "E11.11.1.8", {"start": v(-110.6, -67.5) * mm, "end": v(-113.76, -67.5) * mm});
            skLineSegment(sketch, "E11.14.1.8", {"start": v(-113.76, -67.5) * mm, "end": v(-115.34, -64.77) * mm});
            skLineSegment(sketch, "E11.17.1.8", {"start": v(-115.34, -64.77) * mm, "end": v(-113.76, -62.04) * mm});
            skLineSegment(sketch, "E11.0.2.8", {"start": v(-98.8, -62.04) * mm, "end": v(-95.65, -62.04) * mm});
            skLineSegment(sketch, "E11.3.2.8", {"start": v(-95.65, -62.04) * mm, "end": v(-94.07, -64.77) * mm});
            skLineSegment(sketch, "E11.6.2.8", {"start": v(-94.07, -64.77) * mm, "end": v(-95.65, -67.5) * mm});
            skCircle(sketch, "E11.9.2.8", {"center": v(-97.23, -64.77) * mm, "radius": 2.73 * mm, "construction": true});
            skLineSegment(sketch, "E11.11.2.8", {"start": v(-95.65, -67.5) * mm, "end": v(-98.8, -67.5) * mm});
            skLineSegment(sketch, "E11.14.2.8", {"start": v(-98.8, -67.5) * mm, "end": v(-100.38, -64.77) * mm});
            skLineSegment(sketch, "E11.17.2.8", {"start": v(-100.38, -64.77) * mm, "end": v(-98.8, -62.04) * mm});
            skLineSegment(sketch, "E11.0.3.8", {"start": v(-83.85, -62.04) * mm, "end": v(-80.7, -62.04) * mm});
            skLineSegment(sketch, "E11.3.3.8", {"start": v(-80.7, -62.04) * mm, "end": v(-79.12, -64.77) * mm});
            skLineSegment(sketch, "E11.6.3.8", {"start": v(-79.12, -64.77) * mm, "end": v(-80.7, -67.5) * mm});
            skCircle(sketch, "E11.9.3.8", {"center": v(-82.27, -64.77) * mm, "radius": 2.73 * mm, "construction": true});
            skLineSegment(sketch, "E11.11.3.8", {"start": v(-80.7, -67.5) * mm, "end": v(-83.85, -67.5) * mm});
            skLineSegment(sketch, "E11.14.3.8", {"start": v(-83.85, -67.5) * mm, "end": v(-85.42, -64.77) * mm});
            skLineSegment(sketch, "E11.17.3.8", {"start": v(-85.42, -64.77) * mm, "end": v(-83.85, -62.04) * mm});
            skLineSegment(sketch, "E11.0.4.8", {"start": v(-68.89, -62.04) * mm, "end": v(-65.73, -62.04) * mm});
            skLineSegment(sketch, "E11.3.4.8", {"start": v(-65.73, -62.04) * mm, "end": v(-64.16, -64.77) * mm});
            skLineSegment(sketch, "E11.6.4.8", {"start": v(-64.16, -64.77) * mm, "end": v(-65.73, -67.5) * mm});
            skCircle(sketch, "E11.9.4.8", {"center": v(-67.31, -64.77) * mm, "radius": 2.73 * mm, "construction": true});
            skLineSegment(sketch, "E11.11.4.8", {"start": v(-65.73, -67.5) * mm, "end": v(-68.89, -67.5) * mm});
            skLineSegment(sketch, "E11.14.4.8", {"start": v(-68.89, -67.5) * mm, "end": v(-70.46, -64.77) * mm});
            skLineSegment(sketch, "E11.17.4.8", {"start": v(-70.46, -64.77) * mm, "end": v(-68.89, -62.04) * mm});
            skLineSegment(sketch, "E11.0.5.8", {"start": v(-53.93, -62.04) * mm, "end": v(-50.78, -62.04) * mm});
            skLineSegment(sketch, "E11.3.5.8", {"start": v(-50.78, -62.04) * mm, "end": v(-49.2, -64.77) * mm});
            skLineSegment(sketch, "E11.6.5.8", {"start": v(-49.2, -64.77) * mm, "end": v(-50.78, -67.5) * mm});
            skCircle(sketch, "E11.9.5.8", {"center": v(-52.35, -64.77) * mm, "radius": 2.73 * mm, "construction": true});
            skLineSegment(sketch, "E11.11.5.8", {"start": v(-50.78, -67.5) * mm, "end": v(-53.93, -67.5) * mm});
            skLineSegment(sketch, "E11.14.5.8", {"start": v(-53.93, -67.5) * mm, "end": v(-55.5, -64.77) * mm});
            skLineSegment(sketch, "E11.17.5.8", {"start": v(-55.5, -64.77) * mm, "end": v(-53.93, -62.04) * mm});
            skLineSegment(sketch, "E12.0.0.9", {"start": v(-128.72, -53.4) * mm, "end": v(-125.57, -53.4) * mm});
            skLineSegment(sketch, "E12.3.0.9", {"start": v(-125.57, -53.4) * mm, "end": v(-124, -56.13) * mm});
            skLineSegment(sketch, "E12.6.0.9", {"start": v(-124, -56.13) * mm, "end": v(-125.57, -58.86) * mm});
            skCircle(sketch, "E12.9.0.9", {"center": v(-127.14, -56.13) * mm, "radius": 2.73 * mm, "construction": true});
            skLineSegment(sketch, "E12.11.0.9", {"start": v(-125.57, -58.86) * mm, "end": v(-128.72, -58.86) * mm});
            skLineSegment(sketch, "E12.14.0.9", {"start": v(-128.72, -58.86) * mm, "end": v(-130.3, -56.13) * mm});
            skLineSegment(sketch, "E12.17.0.9", {"start": v(-130.3, -56.13) * mm, "end": v(-128.72, -53.4) * mm});
            skLineSegment(sketch, "E12.0.0.10", {"start": v(-128.72, -44.77) * mm, "end": v(-125.57, -44.77) * mm});
            skLineSegment(sketch, "E12.3.0.10", {"start": v(-125.57, -44.77) * mm, "end": v(-124, -47.5) * mm});
            skLineSegment(sketch, "E12.6.0.10", {"start": v(-124, -47.5) * mm, "end": v(-125.57, -50.23) * mm});
            skCircle(sketch, "E12.9.0.10", {"center": v(-127.14, -47.5) * mm, "radius": 2.73 * mm, "construction": true});
            skLineSegment(sketch, "E12.11.0.10", {"start": v(-125.57, -50.23) * mm, "end": v(-128.72, -50.23) * mm});
            skLineSegment(sketch, "E12.14.0.10", {"start": v(-128.72, -50.23) * mm, "end": v(-130.3, -47.5) * mm});
            skLineSegment(sketch, "E12.17.0.10", {"start": v(-130.3, -47.5) * mm, "end": v(-128.72, -44.77) * mm});
            skLineSegment(sketch, "E12.0.0.11", {"start": v(-128.72, -36.13) * mm, "end": v(-125.57, -36.13) * mm});
            skLineSegment(sketch, "E12.3.0.11", {"start": v(-125.57, -36.13) * mm, "end": v(-124, -38.86) * mm});
            skLineSegment(sketch, "E12.6.0.11", {"start": v(-124, -38.86) * mm, "end": v(-125.57, -41.6) * mm});
            skCircle(sketch, "E12.9.0.11", {"center": v(-127.14, -38.86) * mm, "radius": 2.73 * mm, "construction": true});
            skLineSegment(sketch, "E12.11.0.11", {"start": v(-125.57, -41.6) * mm, "end": v(-128.72, -41.6) * mm});
            skLineSegment(sketch, "E12.14.0.11", {"start": v(-128.72, -41.6) * mm, "end": v(-130.3, -38.86) * mm});
            skLineSegment(sketch, "E12.17.0.11", {"start": v(-130.3, -38.86) * mm, "end": v(-128.72, -36.13) * mm});
            skLineSegment(sketch, "E12.0.0.12", {"start": v(-128.72, -27.5) * mm, "end": v(-125.57, -27.5) * mm});
            skLineSegment(sketch, "E12.3.0.12", {"start": v(-125.57, -27.5) * mm, "end": v(-124, -30.23) * mm});
            skLineSegment(sketch, "E12.6.0.12", {"start": v(-124, -30.23) * mm, "end": v(-125.57, -32.96) * mm});
            skCircle(sketch, "E12.9.0.12", {"center": v(-127.14, -30.23) * mm, "radius": 2.73 * mm, "construction": true});
            skLineSegment(sketch, "E12.11.0.12", {"start": v(-125.57, -32.96) * mm, "end": v(-128.72, -32.96) * mm});
            skLineSegment(sketch, "E12.14.0.12", {"start": v(-128.72, -32.96) * mm, "end": v(-130.3, -30.23) * mm});
            skLineSegment(sketch, "E12.17.0.12", {"start": v(-130.3, -30.23) * mm, "end": v(-128.72, -27.5) * mm});
            skLineSegment(sketch, "E12.0.0.13", {"start": v(-128.72, -18.86) * mm, "end": v(-125.57, -18.86) * mm});
            skLineSegment(sketch, "E12.3.0.13", {"start": v(-125.57, -18.86) * mm, "end": v(-124, -21.6) * mm});
            skLineSegment(sketch, "E12.6.0.13", {"start": v(-124, -21.6) * mm, "end": v(-125.57, -24.32) * mm});
            skCircle(sketch, "E12.9.0.13", {"center": v(-127.14, -21.6) * mm, "radius": 2.73 * mm, "construction": true});
            skLineSegment(sketch, "E12.11.0.13", {"start": v(-125.57, -24.32) * mm, "end": v(-128.72, -24.32) * mm});
            skLineSegment(sketch, "E12.14.0.13", {"start": v(-128.72, -24.32) * mm, "end": v(-130.3, -21.6) * mm});
            skLineSegment(sketch, "E12.17.0.13", {"start": v(-130.3, -21.59) * mm, "end": v(-128.72, -18.86) * mm});
            skLineSegment(sketch, "E12.0.0.14", {"start": v(-128.72, -10.22) * mm, "end": v(-125.57, -10.22) * mm});
            skLineSegment(sketch, "E12.3.0.14", {"start": v(-125.57, -10.22) * mm, "end": v(-124, -12.95) * mm});
            skLineSegment(sketch, "E12.6.0.14", {"start": v(-124, -12.95) * mm, "end": v(-125.57, -15.68) * mm});
            skCircle(sketch, "E12.9.0.14", {"center": v(-127.14, -12.95) * mm, "radius": 2.73 * mm, "construction": true});
            skLineSegment(sketch, "E12.11.0.14", {"start": v(-125.57, -15.68) * mm, "end": v(-128.72, -15.68) * mm});
            skLineSegment(sketch, "E12.14.0.14", {"start": v(-128.72, -15.68) * mm, "end": v(-130.3, -12.95) * mm});
            skLineSegment(sketch, "E12.17.0.14", {"start": v(-130.3, -12.95) * mm, "end": v(-128.72, -10.22) * mm});
            skLineSegment(sketch, "E12.0.0.15", {"start": v(-128.72, -1.59) * mm, "end": v(-125.57, -1.59) * mm});
            skLineSegment(sketch, "E12.3.0.15", {"start": v(-125.57, -1.59) * mm, "end": v(-124, -4.32) * mm});
            skLineSegment(sketch, "E12.6.0.15", {"start": v(-124, -4.32) * mm, "end": v(-125.57, -7.05) * mm});
            skCircle(sketch, "E12.9.0.15", {"center": v(-127.14, -4.32) * mm, "radius": 2.73 * mm, "construction": true});
            skLineSegment(sketch, "E12.11.0.15", {"start": v(-125.57, -7.05) * mm, "end": v(-128.72, -7.05) * mm});
            skLineSegment(sketch, "E12.14.0.15", {"start": v(-128.72, -7.05) * mm, "end": v(-130.3, -4.32) * mm});
            skLineSegment(sketch, "E12.17.0.15", {"start": v(-130.3, -4.32) * mm, "end": v(-128.72, -1.59) * mm});
            skLineSegment(sketch, "E12.0.0.16", {"start": v(-128.72, 7.05) * mm, "end": v(-125.57, 7.05) * mm});
            skLineSegment(sketch, "E12.3.0.16", {"start": v(-125.57, 7.05) * mm, "end": v(-124, 4.32) * mm});
            skLineSegment(sketch, "E12.6.0.16", {"start": v(-124, 4.32) * mm, "end": v(-125.57, 1.59) * mm});
            skCircle(sketch, "E12.9.0.16", {"center": v(-127.14, 4.32) * mm, "radius": 2.73 * mm, "construction": true});
            skLineSegment(sketch, "E12.11.0.16", {"start": v(-125.57, 1.59) * mm, "end": v(-128.72, 1.59) * mm});
            skLineSegment(sketch, "E12.14.0.16", {"start": v(-128.72, 1.59) * mm, "end": v(-130.3, 4.32) * mm});
            skLineSegment(sketch, "E12.17.0.16", {"start": v(-130.3, 4.32) * mm, "end": v(-128.72, 7.05) * mm});
            skLineSegment(sketch, "E12.0.0.17", {"start": v(-128.72, 15.68) * mm, "end": v(-125.57, 15.68) * mm});
            skLineSegment(sketch, "E12.3.0.17", {"start": v(-125.57, 15.68) * mm, "end": v(-124, 12.95) * mm});
            skLineSegment(sketch, "E12.6.0.17", {"start": v(-124, 12.95) * mm, "end": v(-125.57, 10.22) * mm});
            skCircle(sketch, "E12.9.0.17", {"center": v(-127.14, 12.95) * mm, "radius": 2.73 * mm, "construction": true});
            skLineSegment(sketch, "E12.11.0.17", {"start": v(-125.57, 10.22) * mm, "end": v(-128.72, 10.22) * mm});
            skLineSegment(sketch, "E12.14.0.17", {"start": v(-128.72, 10.22) * mm, "end": v(-130.3, 12.95) * mm});
            skLineSegment(sketch, "E12.17.0.17", {"start": v(-130.3, 12.95) * mm, "end": v(-128.72, 15.68) * mm});
            skLineSegment(sketch, "E12.0.0.18", {"start": v(-128.72, 24.32) * mm, "end": v(-125.57, 24.32) * mm});
            skLineSegment(sketch, "E12.3.0.18", {"start": v(-125.57, 24.32) * mm, "end": v(-124, 21.59) * mm});
            skLineSegment(sketch, "E12.6.0.18", {"start": v(-124, 21.59) * mm, "end": v(-125.57, 18.86) * mm});
            skCircle(sketch, "E12.9.0.18", {"center": v(-127.14, 21.59) * mm, "radius": 2.73 * mm, "construction": true});
            skLineSegment(sketch, "E12.11.0.18", {"start": v(-125.57, 18.86) * mm, "end": v(-128.72, 18.86) * mm});
            skLineSegment(sketch, "E12.14.0.18", {"start": v(-128.72, 18.86) * mm, "end": v(-130.3, 21.59) * mm});
            skLineSegment(sketch, "E12.17.0.18", {"start": v(-130.3, 21.6) * mm, "end": v(-128.72, 24.32) * mm});
            skLineSegment(sketch, "E12.0.0.19", {"start": v(-128.72, 32.96) * mm, "end": v(-125.57, 32.96) * mm});
            skLineSegment(sketch, "E12.3.0.19", {"start": v(-125.57, 32.96) * mm, "end": v(-124, 30.23) * mm});
            skLineSegment(sketch, "E12.6.0.19", {"start": v(-124, 30.23) * mm, "end": v(-125.57, 27.5) * mm});
            skCircle(sketch, "E12.9.0.19", {"center": v(-127.14, 30.23) * mm, "radius": 2.73 * mm, "construction": true});
            skLineSegment(sketch, "E12.11.0.19", {"start": v(-125.57, 27.5) * mm, "end": v(-128.72, 27.5) * mm});
            skLineSegment(sketch, "E12.14.0.19", {"start": v(-128.72, 27.5) * mm, "end": v(-130.3, 30.23) * mm});
            skLineSegment(sketch, "E12.17.0.19", {"start": v(-130.3, 30.23) * mm, "end": v(-128.72, 32.96) * mm});
            skLineSegment(sketch, "E12.0.1.9", {"start": v(-113.76, -53.4) * mm, "end": v(-110.6, -53.4) * mm});
            skLineSegment(sketch, "E12.3.1.9", {"start": v(-110.6, -53.4) * mm, "end": v(-109.03, -56.13) * mm});
            skLineSegment(sketch, "E12.6.1.9", {"start": v(-109.03, -56.13) * mm, "end": v(-110.6, -58.86) * mm});
            skCircle(sketch, "E12.9.1.9", {"center": v(-112.19, -56.13) * mm, "radius": 2.73 * mm, "construction": true});
            skLineSegment(sketch, "E12.11.1.9", {"start": v(-110.6, -58.86) * mm, "end": v(-113.76, -58.86) * mm});
            skLineSegment(sketch, "E12.14.1.9", {"start": v(-113.76, -58.86) * mm, "end": v(-115.34, -56.13) * mm});
            skLineSegment(sketch, "E12.17.1.9", {"start": v(-115.34, -56.13) * mm, "end": v(-113.76, -53.4) * mm});
            skLineSegment(sketch, "E12.0.1.10", {"start": v(-113.76, -44.77) * mm, "end": v(-110.6, -44.77) * mm});
            skLineSegment(sketch, "E12.3.1.10", {"start": v(-110.6, -44.77) * mm, "end": v(-109.03, -47.5) * mm});
            skLineSegment(sketch, "E12.6.1.10", {"start": v(-109.03, -47.5) * mm, "end": v(-110.6, -50.23) * mm});
            skCircle(sketch, "E12.9.1.10", {"center": v(-112.19, -47.5) * mm, "radius": 2.73 * mm, "construction": true});
            skLineSegment(sketch, "E12.11.1.10", {"start": v(-110.6, -50.23) * mm, "end": v(-113.76, -50.23) * mm});
            skLineSegment(sketch, "E12.14.1.10", {"start": v(-113.76, -50.23) * mm, "end": v(-115.34, -47.5) * mm});
            skLineSegment(sketch, "E12.17.1.10", {"start": v(-115.34, -47.5) * mm, "end": v(-113.76, -44.77) * mm});
            skLineSegment(sketch, "E12.0.1.11", {"start": v(-113.76, -36.13) * mm, "end": v(-110.6, -36.13) * mm});
            skLineSegment(sketch, "E12.3.1.11", {"start": v(-110.6, -36.13) * mm, "end": v(-109.03, -38.86) * mm});
            skLineSegment(sketch, "E12.6.1.11", {"start": v(-109.03, -38.86) * mm, "end": v(-110.6, -41.6) * mm});
            skCircle(sketch, "E12.9.1.11", {"center": v(-112.19, -38.86) * mm, "radius": 2.73 * mm, "construction": true});
            skLineSegment(sketch, "E12.11.1.11", {"start": v(-110.6, -41.6) * mm, "end": v(-113.76, -41.6) * mm});
            skLineSegment(sketch, "E12.14.1.11", {"start": v(-113.76, -41.6) * mm, "end": v(-115.34, -38.86) * mm});
            skLineSegment(sketch, "E12.17.1.11", {"start": v(-115.34, -38.86) * mm, "end": v(-113.76, -36.13) * mm});
            skLineSegment(sketch, "E12.0.1.12", {"start": v(-113.76, -27.5) * mm, "end": v(-110.6, -27.5) * mm});
            skLineSegment(sketch, "E12.3.1.12", {"start": v(-110.6, -27.5) * mm, "end": v(-109.03, -30.23) * mm});
            skLineSegment(sketch, "E12.6.1.12", {"start": v(-109.03, -30.23) * mm, "end": v(-110.6, -32.96) * mm});
            skCircle(sketch, "E12.9.1.12", {"center": v(-112.19, -30.23) * mm, "radius": 2.73 * mm, "construction": true});
            skLineSegment(sketch, "E12.11.1.12", {"start": v(-110.6, -32.96) * mm, "end": v(-113.76, -32.96) * mm});
            skLineSegment(sketch, "E12.14.1.12", {"start": v(-113.76, -32.96) * mm, "end": v(-115.34, -30.23) * mm});
            skLineSegment(sketch, "E12.17.1.12", {"start": v(-115.34, -30.23) * mm, "end": v(-113.76, -27.5) * mm});
            skLineSegment(sketch, "E12.0.1.13", {"start": v(-113.76, -18.86) * mm, "end": v(-110.6, -18.86) * mm});
            skLineSegment(sketch, "E12.3.1.13", {"start": v(-110.6, -18.86) * mm, "end": v(-109.03, -21.6) * mm});
            skLineSegment(sketch, "E12.6.1.13", {"start": v(-109.03, -21.6) * mm, "end": v(-110.6, -24.32) * mm});
            skCircle(sketch, "E12.9.1.13", {"center": v(-112.19, -21.6) * mm, "radius": 2.73 * mm, "construction": true});
            skLineSegment(sketch, "E12.11.1.13", {"start": v(-110.6, -24.32) * mm, "end": v(-113.76, -24.32) * mm});
            skLineSegment(sketch, "E12.14.1.13", {"start": v(-113.76, -24.32) * mm, "end": v(-115.34, -21.6) * mm});
            skLineSegment(sketch, "E12.17.1.13", {"start": v(-115.34, -21.59) * mm, "end": v(-113.76, -18.86) * mm});
            skLineSegment(sketch, "E12.0.1.14", {"start": v(-113.76, -10.22) * mm, "end": v(-110.6, -10.22) * mm});
            skLineSegment(sketch, "E12.3.1.14", {"start": v(-110.6, -10.22) * mm, "end": v(-109.03, -12.95) * mm});
            skLineSegment(sketch, "E12.6.1.14", {"start": v(-109.03, -12.95) * mm, "end": v(-110.6, -15.68) * mm});
            skCircle(sketch, "E12.9.1.14", {"center": v(-112.19, -12.95) * mm, "radius": 2.73 * mm, "construction": true});
            skLineSegment(sketch, "E12.11.1.14", {"start": v(-110.6, -15.68) * mm, "end": v(-113.76, -15.68) * mm});
            skLineSegment(sketch, "E12.14.1.14", {"start": v(-113.76, -15.68) * mm, "end": v(-115.34, -12.95) * mm});
            skLineSegment(sketch, "E12.17.1.14", {"start": v(-115.34, -12.95) * mm, "end": v(-113.76, -10.22) * mm});
            skLineSegment(sketch, "E12.0.1.15", {"start": v(-113.76, -1.59) * mm, "end": v(-110.6, -1.59) * mm});
            skLineSegment(sketch, "E12.3.1.15", {"start": v(-110.6, -1.59) * mm, "end": v(-109.03, -4.32) * mm});
            skLineSegment(sketch, "E12.6.1.15", {"start": v(-109.03, -4.32) * mm, "end": v(-110.6, -7.05) * mm});
            skCircle(sketch, "E12.9.1.15", {"center": v(-112.19, -4.32) * mm, "radius": 2.73 * mm, "construction": true});
            skLineSegment(sketch, "E12.11.1.15", {"start": v(-110.6, -7.05) * mm, "end": v(-113.76, -7.05) * mm});
            skLineSegment(sketch, "E12.14.1.15", {"start": v(-113.76, -7.05) * mm, "end": v(-115.34, -4.32) * mm});
            skLineSegment(sketch, "E12.17.1.15", {"start": v(-115.34, -4.32) * mm, "end": v(-113.76, -1.59) * mm});
            skLineSegment(sketch, "E12.0.1.16", {"start": v(-113.76, 7.05) * mm, "end": v(-110.6, 7.05) * mm});
            skLineSegment(sketch, "E12.3.1.16", {"start": v(-110.6, 7.05) * mm, "end": v(-109.03, 4.32) * mm});
            skLineSegment(sketch, "E12.6.1.16", {"start": v(-109.03, 4.32) * mm, "end": v(-110.6, 1.59) * mm});
            skCircle(sketch, "E12.9.1.16", {"center": v(-112.19, 4.32) * mm, "radius": 2.73 * mm, "construction": true});
            skLineSegment(sketch, "E12.11.1.16", {"start": v(-110.6, 1.59) * mm, "end": v(-113.76, 1.59) * mm});
            skLineSegment(sketch, "E12.14.1.16", {"start": v(-113.76, 1.59) * mm, "end": v(-115.34, 4.32) * mm});
            skLineSegment(sketch, "E12.17.1.16", {"start": v(-115.34, 4.32) * mm, "end": v(-113.76, 7.05) * mm});
            skLineSegment(sketch, "E12.0.1.17", {"start": v(-113.76, 15.68) * mm, "end": v(-110.6, 15.68) * mm});
            skLineSegment(sketch, "E12.3.1.17", {"start": v(-110.6, 15.68) * mm, "end": v(-109.03, 12.95) * mm});
            skLineSegment(sketch, "E12.6.1.17", {"start": v(-109.03, 12.95) * mm, "end": v(-110.6, 10.22) * mm});
            skCircle(sketch, "E12.9.1.17", {"center": v(-112.19, 12.95) * mm, "radius": 2.73 * mm, "construction": true});
            skLineSegment(sketch, "E12.11.1.17", {"start": v(-110.6, 10.22) * mm, "end": v(-113.76, 10.22) * mm});
            skLineSegment(sketch, "E12.14.1.17", {"start": v(-113.76, 10.22) * mm, "end": v(-115.34, 12.95) * mm});
            skLineSegment(sketch, "E12.17.1.17", {"start": v(-115.34, 12.95) * mm, "end": v(-113.76, 15.68) * mm});
            skLineSegment(sketch, "E12.0.1.18", {"start": v(-113.76, 24.32) * mm, "end": v(-110.6, 24.32) * mm});
            skLineSegment(sketch, "E12.3.1.18", {"start": v(-110.6, 24.32) * mm, "end": v(-109.03, 21.59) * mm});
            skLineSegment(sketch, "E12.6.1.18", {"start": v(-109.03, 21.59) * mm, "end": v(-110.6, 18.86) * mm});
            skCircle(sketch, "E12.9.1.18", {"center": v(-112.19, 21.59) * mm, "radius": 2.73 * mm, "construction": true});
            skLineSegment(sketch, "E12.11.1.18", {"start": v(-110.6, 18.86) * mm, "end": v(-113.76, 18.86) * mm});
            skLineSegment(sketch, "E12.14.1.18", {"start": v(-113.76, 18.86) * mm, "end": v(-115.34, 21.59) * mm});
            skLineSegment(sketch, "E12.17.1.18", {"start": v(-115.34, 21.59) * mm, "end": v(-113.76, 24.32) * mm});
            skLineSegment(sketch, "E12.0.1.19", {"start": v(-113.76, 32.96) * mm, "end": v(-110.6, 32.96) * mm});
            skLineSegment(sketch, "E12.3.1.19", {"start": v(-110.6, 32.96) * mm, "end": v(-109.03, 30.23) * mm});
            skLineSegment(sketch, "E12.6.1.19", {"start": v(-109.03, 30.23) * mm, "end": v(-110.6, 27.5) * mm});
            skCircle(sketch, "E12.9.1.19", {"center": v(-112.19, 30.23) * mm, "radius": 2.73 * mm, "construction": true});
            skLineSegment(sketch, "E12.11.1.19", {"start": v(-110.6, 27.5) * mm, "end": v(-113.76, 27.5) * mm});
            skLineSegment(sketch, "E12.14.1.19", {"start": v(-113.76, 27.5) * mm, "end": v(-115.34, 30.23) * mm});
            skLineSegment(sketch, "E12.17.1.19", {"start": v(-115.34, 30.23) * mm, "end": v(-113.76, 32.96) * mm});
            skLineSegment(sketch, "E12.0.2.9", {"start": v(-98.8, -53.4) * mm, "end": v(-95.65, -53.4) * mm});
            skLineSegment(sketch, "E12.3.2.9", {"start": v(-95.65, -53.4) * mm, "end": v(-94.07, -56.13) * mm});
            skLineSegment(sketch, "E12.6.2.9", {"start": v(-94.07, -56.13) * mm, "end": v(-95.65, -58.86) * mm});
            skCircle(sketch, "E12.9.2.9", {"center": v(-97.23, -56.13) * mm, "radius": 2.73 * mm, "construction": true});
            skLineSegment(sketch, "E12.11.2.9", {"start": v(-95.65, -58.86) * mm, "end": v(-98.8, -58.86) * mm});
            skLineSegment(sketch, "E12.14.2.9", {"start": v(-98.8, -58.86) * mm, "end": v(-100.38, -56.13) * mm});
            skLineSegment(sketch, "E12.17.2.9", {"start": v(-100.38, -56.13) * mm, "end": v(-98.8, -53.4) * mm});
            skLineSegment(sketch, "E12.0.2.10", {"start": v(-98.8, -44.77) * mm, "end": v(-95.65, -44.77) * mm});
            skLineSegment(sketch, "E12.3.2.10", {"start": v(-95.65, -44.77) * mm, "end": v(-94.07, -47.5) * mm});
            skLineSegment(sketch, "E12.6.2.10", {"start": v(-94.07, -47.5) * mm, "end": v(-95.65, -50.23) * mm});
            skCircle(sketch, "E12.9.2.10", {"center": v(-97.23, -47.5) * mm, "radius": 2.73 * mm, "construction": true});
            skLineSegment(sketch, "E12.11.2.10", {"start": v(-95.65, -50.23) * mm, "end": v(-98.8, -50.23) * mm});
            skLineSegment(sketch, "E12.14.2.10", {"start": v(-98.8, -50.23) * mm, "end": v(-100.38, -47.5) * mm});
            skLineSegment(sketch, "E12.17.2.10", {"start": v(-100.38, -47.5) * mm, "end": v(-98.8, -44.77) * mm});
            skLineSegment(sketch, "E12.0.2.11", {"start": v(-98.8, -36.13) * mm, "end": v(-95.65, -36.13) * mm});
            skLineSegment(sketch, "E12.3.2.11", {"start": v(-95.65, -36.13) * mm, "end": v(-94.07, -38.86) * mm});
            skLineSegment(sketch, "E12.6.2.11", {"start": v(-94.07, -38.86) * mm, "end": v(-95.65, -41.6) * mm});
            skCircle(sketch, "E12.9.2.11", {"center": v(-97.23, -38.86) * mm, "radius": 2.73 * mm, "construction": true});
            skLineSegment(sketch, "E12.11.2.11", {"start": v(-95.65, -41.6) * mm, "end": v(-98.8, -41.6) * mm});
            skLineSegment(sketch, "E12.14.2.11", {"start": v(-98.8, -41.6) * mm, "end": v(-100.38, -38.86) * mm});
            skLineSegment(sketch, "E12.17.2.11", {"start": v(-100.38, -38.86) * mm, "end": v(-98.8, -36.13) * mm});
            skLineSegment(sketch, "E12.0.2.12", {"start": v(-98.8, -27.5) * mm, "end": v(-95.65, -27.5) * mm});
            skLineSegment(sketch, "E12.3.2.12", {"start": v(-95.65, -27.5) * mm, "end": v(-94.07, -30.23) * mm});
            skLineSegment(sketch, "E12.6.2.12", {"start": v(-94.07, -30.23) * mm, "end": v(-95.65, -32.96) * mm});
            skCircle(sketch, "E12.9.2.12", {"center": v(-97.23, -30.23) * mm, "radius": 2.73 * mm, "construction": true});
            skLineSegment(sketch, "E12.11.2.12", {"start": v(-95.65, -32.96) * mm, "end": v(-98.8, -32.96) * mm});
            skLineSegment(sketch, "E12.14.2.12", {"start": v(-98.8, -32.96) * mm, "end": v(-100.38, -30.23) * mm});
            skLineSegment(sketch, "E12.17.2.12", {"start": v(-100.38, -30.23) * mm, "end": v(-98.8, -27.5) * mm});
            skLineSegment(sketch, "E12.0.2.13", {"start": v(-98.8, -18.86) * mm, "end": v(-95.65, -18.86) * mm});
            skLineSegment(sketch, "E12.3.2.13", {"start": v(-95.65, -18.86) * mm, "end": v(-94.07, -21.6) * mm});
            skLineSegment(sketch, "E12.6.2.13", {"start": v(-94.07, -21.6) * mm, "end": v(-95.65, -24.32) * mm});
            skCircle(sketch, "E12.9.2.13", {"center": v(-97.23, -21.6) * mm, "radius": 2.73 * mm, "construction": true});
            skLineSegment(sketch, "E12.11.2.13", {"start": v(-95.65, -24.32) * mm, "end": v(-98.8, -24.32) * mm});
            skLineSegment(sketch, "E12.14.2.13", {"start": v(-98.8, -24.32) * mm, "end": v(-100.38, -21.6) * mm});
            skLineSegment(sketch, "E12.17.2.13", {"start": v(-100.38, -21.59) * mm, "end": v(-98.8, -18.86) * mm});
            skLineSegment(sketch, "E12.0.2.14", {"start": v(-98.8, -10.22) * mm, "end": v(-95.65, -10.22) * mm});
            skLineSegment(sketch, "E12.3.2.14", {"start": v(-95.65, -10.22) * mm, "end": v(-94.07, -12.95) * mm});
            skLineSegment(sketch, "E12.6.2.14", {"start": v(-94.07, -12.95) * mm, "end": v(-95.65, -15.68) * mm});
            skCircle(sketch, "E12.9.2.14", {"center": v(-97.23, -12.95) * mm, "radius": 2.73 * mm, "construction": true});
            skLineSegment(sketch, "E12.11.2.14", {"start": v(-95.65, -15.68) * mm, "end": v(-98.8, -15.68) * mm});
            skLineSegment(sketch, "E12.14.2.14", {"start": v(-98.8, -15.68) * mm, "end": v(-100.38, -12.95) * mm});
            skLineSegment(sketch, "E12.17.2.14", {"start": v(-100.38, -12.95) * mm, "end": v(-98.8, -10.22) * mm});
            skLineSegment(sketch, "E12.0.2.15", {"start": v(-98.8, -1.59) * mm, "end": v(-95.65, -1.59) * mm});
            skLineSegment(sketch, "E12.3.2.15", {"start": v(-95.65, -1.59) * mm, "end": v(-94.07, -4.32) * mm});
            skLineSegment(sketch, "E12.6.2.15", {"start": v(-94.07, -4.32) * mm, "end": v(-95.65, -7.05) * mm});
            skCircle(sketch, "E12.9.2.15", {"center": v(-97.23, -4.32) * mm, "radius": 2.73 * mm, "construction": true});
            skLineSegment(sketch, "E12.11.2.15", {"start": v(-95.65, -7.05) * mm, "end": v(-98.8, -7.05) * mm});
            skLineSegment(sketch, "E12.14.2.15", {"start": v(-98.8, -7.05) * mm, "end": v(-100.38, -4.32) * mm});
            skLineSegment(sketch, "E12.17.2.15", {"start": v(-100.38, -4.32) * mm, "end": v(-98.8, -1.59) * mm});
            skLineSegment(sketch, "E12.0.2.16", {"start": v(-98.8, 7.05) * mm, "end": v(-95.65, 7.05) * mm});
            skLineSegment(sketch, "E12.3.2.16", {"start": v(-95.65, 7.05) * mm, "end": v(-94.07, 4.32) * mm});
            skLineSegment(sketch, "E12.6.2.16", {"start": v(-94.07, 4.32) * mm, "end": v(-95.65, 1.59) * mm});
            skCircle(sketch, "E12.9.2.16", {"center": v(-97.23, 4.32) * mm, "radius": 2.73 * mm, "construction": true});
            skLineSegment(sketch, "E12.11.2.16", {"start": v(-95.65, 1.59) * mm, "end": v(-98.8, 1.59) * mm});
            skLineSegment(sketch, "E12.14.2.16", {"start": v(-98.8, 1.59) * mm, "end": v(-100.38, 4.32) * mm});
            skLineSegment(sketch, "E12.17.2.16", {"start": v(-100.38, 4.32) * mm, "end": v(-98.8, 7.05) * mm});
            skLineSegment(sketch, "E12.0.2.17", {"start": v(-98.8, 15.68) * mm, "end": v(-95.65, 15.68) * mm});
            skLineSegment(sketch, "E12.3.2.17", {"start": v(-95.65, 15.68) * mm, "end": v(-94.07, 12.95) * mm});
            skLineSegment(sketch, "E12.6.2.17", {"start": v(-94.07, 12.95) * mm, "end": v(-95.65, 10.22) * mm});
            skCircle(sketch, "E12.9.2.17", {"center": v(-97.23, 12.95) * mm, "radius": 2.73 * mm, "construction": true});
            skLineSegment(sketch, "E12.11.2.17", {"start": v(-95.65, 10.22) * mm, "end": v(-98.8, 10.22) * mm});
            skLineSegment(sketch, "E12.14.2.17", {"start": v(-98.8, 10.22) * mm, "end": v(-100.38, 12.95) * mm});
            skLineSegment(sketch, "E12.17.2.17", {"start": v(-100.38, 12.95) * mm, "end": v(-98.8, 15.68) * mm});
            skLineSegment(sketch, "E12.0.2.18", {"start": v(-98.8, 24.32) * mm, "end": v(-95.65, 24.32) * mm});
            skLineSegment(sketch, "E12.3.2.18", {"start": v(-95.65, 24.32) * mm, "end": v(-94.07, 21.59) * mm});
            skLineSegment(sketch, "E12.6.2.18", {"start": v(-94.07, 21.59) * mm, "end": v(-95.65, 18.86) * mm});
            skCircle(sketch, "E12.9.2.18", {"center": v(-97.23, 21.59) * mm, "radius": 2.73 * mm, "construction": true});
            skLineSegment(sketch, "E12.11.2.18", {"start": v(-95.65, 18.86) * mm, "end": v(-98.8, 18.86) * mm});
            skLineSegment(sketch, "E12.14.2.18", {"start": v(-98.8, 18.86) * mm, "end": v(-100.38, 21.59) * mm});
            skLineSegment(sketch, "E12.17.2.18", {"start": v(-100.38, 21.59) * mm, "end": v(-98.8, 24.32) * mm});
            skLineSegment(sketch, "E12.0.2.19", {"start": v(-98.8, 32.96) * mm, "end": v(-95.65, 32.96) * mm});
            skLineSegment(sketch, "E12.3.2.19", {"start": v(-95.65, 32.96) * mm, "end": v(-94.07, 30.23) * mm});
            skLineSegment(sketch, "E12.6.2.19", {"start": v(-94.07, 30.23) * mm, "end": v(-95.65, 27.5) * mm});
            skCircle(sketch, "E12.9.2.19", {"center": v(-97.23, 30.23) * mm, "radius": 2.73 * mm, "construction": true});
            skLineSegment(sketch, "E12.11.2.19", {"start": v(-95.65, 27.5) * mm, "end": v(-98.8, 27.5) * mm});
            skLineSegment(sketch, "E12.14.2.19", {"start": v(-98.8, 27.5) * mm, "end": v(-100.38, 30.23) * mm});
            skLineSegment(sketch, "E12.17.2.19", {"start": v(-100.38, 30.23) * mm, "end": v(-98.8, 32.96) * mm});
            skLineSegment(sketch, "E12.0.3.9", {"start": v(-83.85, -53.4) * mm, "end": v(-80.7, -53.4) * mm});
            skLineSegment(sketch, "E12.3.3.9", {"start": v(-80.7, -53.4) * mm, "end": v(-79.12, -56.13) * mm});
            skLineSegment(sketch, "E12.6.3.9", {"start": v(-79.12, -56.13) * mm, "end": v(-80.7, -58.86) * mm});
            skCircle(sketch, "E12.9.3.9", {"center": v(-82.27, -56.13) * mm, "radius": 2.73 * mm, "construction": true});
            skLineSegment(sketch, "E12.11.3.9", {"start": v(-80.7, -58.86) * mm, "end": v(-83.85, -58.86) * mm});
            skLineSegment(sketch, "E12.14.3.9", {"start": v(-83.85, -58.86) * mm, "end": v(-85.42, -56.13) * mm});
            skLineSegment(sketch, "E12.17.3.9", {"start": v(-85.42, -56.13) * mm, "end": v(-83.85, -53.4) * mm});
            skLineSegment(sketch, "E12.0.3.10", {"start": v(-83.85, -44.77) * mm, "end": v(-80.7, -44.77) * mm});
            skLineSegment(sketch, "E12.3.3.10", {"start": v(-80.7, -44.77) * mm, "end": v(-79.12, -47.5) * mm});
            skLineSegment(sketch, "E12.6.3.10", {"start": v(-79.12, -47.5) * mm, "end": v(-80.7, -50.23) * mm});
            skCircle(sketch, "E12.9.3.10", {"center": v(-82.27, -47.5) * mm, "radius": 2.73 * mm, "construction": true});
            skLineSegment(sketch, "E12.11.3.10", {"start": v(-80.7, -50.23) * mm, "end": v(-83.85, -50.23) * mm});
            skLineSegment(sketch, "E12.14.3.10", {"start": v(-83.85, -50.23) * mm, "end": v(-85.42, -47.5) * mm});
            skLineSegment(sketch, "E12.17.3.10", {"start": v(-85.42, -47.5) * mm, "end": v(-83.85, -44.77) * mm});
            skLineSegment(sketch, "E12.0.3.11", {"start": v(-83.85, -36.13) * mm, "end": v(-80.7, -36.13) * mm});
            skLineSegment(sketch, "E12.3.3.11", {"start": v(-80.7, -36.13) * mm, "end": v(-79.12, -38.86) * mm});
            skLineSegment(sketch, "E12.6.3.11", {"start": v(-79.12, -38.86) * mm, "end": v(-80.7, -41.6) * mm});
            skCircle(sketch, "E12.9.3.11", {"center": v(-82.27, -38.86) * mm, "radius": 2.73 * mm, "construction": true});
            skLineSegment(sketch, "E12.11.3.11", {"start": v(-80.7, -41.6) * mm, "end": v(-83.85, -41.6) * mm});
            skLineSegment(sketch, "E12.14.3.11", {"start": v(-83.85, -41.6) * mm, "end": v(-85.42, -38.86) * mm});
            skLineSegment(sketch, "E12.17.3.11", {"start": v(-85.42, -38.86) * mm, "end": v(-83.85, -36.13) * mm});
            skLineSegment(sketch, "E12.0.3.12", {"start": v(-83.85, -27.5) * mm, "end": v(-80.7, -27.5) * mm});
            skLineSegment(sketch, "E12.3.3.12", {"start": v(-80.7, -27.5) * mm, "end": v(-79.12, -30.23) * mm});
            skLineSegment(sketch, "E12.6.3.12", {"start": v(-79.12, -30.23) * mm, "end": v(-80.7, -32.96) * mm});
            skCircle(sketch, "E12.9.3.12", {"center": v(-82.27, -30.23) * mm, "radius": 2.73 * mm, "construction": true});
            skLineSegment(sketch, "E12.11.3.12", {"start": v(-80.7, -32.96) * mm, "end": v(-83.85, -32.96) * mm});
            skLineSegment(sketch, "E12.14.3.12", {"start": v(-83.85, -32.96) * mm, "end": v(-85.42, -30.23) * mm});
            skLineSegment(sketch, "E12.17.3.12", {"start": v(-85.42, -30.23) * mm, "end": v(-83.85, -27.5) * mm});
            skLineSegment(sketch, "E12.0.3.13", {"start": v(-83.85, -18.86) * mm, "end": v(-80.7, -18.86) * mm});
            skLineSegment(sketch, "E12.3.3.13", {"start": v(-80.7, -18.86) * mm, "end": v(-79.12, -21.6) * mm});
            skLineSegment(sketch, "E12.6.3.13", {"start": v(-79.12, -21.6) * mm, "end": v(-80.7, -24.32) * mm});
            skCircle(sketch, "E12.9.3.13", {"center": v(-82.27, -21.6) * mm, "radius": 2.73 * mm, "construction": true});
            skLineSegment(sketch, "E12.11.3.13", {"start": v(-80.7, -24.32) * mm, "end": v(-83.85, -24.32) * mm});
            skLineSegment(sketch, "E12.14.3.13", {"start": v(-83.85, -24.32) * mm, "end": v(-85.42, -21.6) * mm});
            skLineSegment(sketch, "E12.17.3.13", {"start": v(-85.42, -21.59) * mm, "end": v(-83.85, -18.86) * mm});
            skLineSegment(sketch, "E12.0.3.14", {"start": v(-83.85, -10.22) * mm, "end": v(-80.7, -10.22) * mm});
            skLineSegment(sketch, "E12.3.3.14", {"start": v(-80.7, -10.22) * mm, "end": v(-79.12, -12.95) * mm});
            skLineSegment(sketch, "E12.6.3.14", {"start": v(-79.12, -12.95) * mm, "end": v(-80.7, -15.68) * mm});
            skCircle(sketch, "E12.9.3.14", {"center": v(-82.27, -12.95) * mm, "radius": 2.73 * mm, "construction": true});
            skLineSegment(sketch, "E12.11.3.14", {"start": v(-80.7, -15.68) * mm, "end": v(-83.85, -15.68) * mm});
            skLineSegment(sketch, "E12.14.3.14", {"start": v(-83.85, -15.68) * mm, "end": v(-85.42, -12.95) * mm});
            skLineSegment(sketch, "E12.17.3.14", {"start": v(-85.42, -12.95) * mm, "end": v(-83.85, -10.22) * mm});
            skLineSegment(sketch, "E12.0.3.15", {"start": v(-83.85, -1.59) * mm, "end": v(-80.7, -1.59) * mm});
            skLineSegment(sketch, "E12.3.3.15", {"start": v(-80.7, -1.59) * mm, "end": v(-79.12, -4.32) * mm});
            skLineSegment(sketch, "E12.6.3.15", {"start": v(-79.12, -4.32) * mm, "end": v(-80.7, -7.05) * mm});
            skCircle(sketch, "E12.9.3.15", {"center": v(-82.27, -4.32) * mm, "radius": 2.73 * mm, "construction": true});
            skLineSegment(sketch, "E12.11.3.15", {"start": v(-80.7, -7.05) * mm, "end": v(-83.85, -7.05) * mm});
            skLineSegment(sketch, "E12.14.3.15", {"start": v(-83.85, -7.05) * mm, "end": v(-85.42, -4.32) * mm});
            skLineSegment(sketch, "E12.17.3.15", {"start": v(-85.42, -4.32) * mm, "end": v(-83.85, -1.59) * mm});
            skLineSegment(sketch, "E12.0.3.16", {"start": v(-83.85, 7.05) * mm, "end": v(-80.7, 7.05) * mm});
            skLineSegment(sketch, "E12.3.3.16", {"start": v(-80.7, 7.05) * mm, "end": v(-79.12, 4.32) * mm});
            skLineSegment(sketch, "E12.6.3.16", {"start": v(-79.12, 4.32) * mm, "end": v(-80.7, 1.59) * mm});
            skCircle(sketch, "E12.9.3.16", {"center": v(-82.27, 4.32) * mm, "radius": 2.73 * mm, "construction": true});
            skLineSegment(sketch, "E12.11.3.16", {"start": v(-80.7, 1.59) * mm, "end": v(-83.85, 1.59) * mm});
            skLineSegment(sketch, "E12.14.3.16", {"start": v(-83.85, 1.59) * mm, "end": v(-85.42, 4.32) * mm});
            skLineSegment(sketch, "E12.17.3.16", {"start": v(-85.42, 4.32) * mm, "end": v(-83.85, 7.05) * mm});
            skLineSegment(sketch, "E12.0.3.17", {"start": v(-83.85, 15.68) * mm, "end": v(-80.7, 15.68) * mm});
            skLineSegment(sketch, "E12.3.3.17", {"start": v(-80.7, 15.68) * mm, "end": v(-79.12, 12.95) * mm});
            skLineSegment(sketch, "E12.6.3.17", {"start": v(-79.12, 12.95) * mm, "end": v(-80.7, 10.22) * mm});
            skCircle(sketch, "E12.9.3.17", {"center": v(-82.27, 12.95) * mm, "radius": 2.73 * mm, "construction": true});
            skLineSegment(sketch, "E12.11.3.17", {"start": v(-80.7, 10.22) * mm, "end": v(-83.85, 10.22) * mm});
            skLineSegment(sketch, "E12.14.3.17", {"start": v(-83.85, 10.22) * mm, "end": v(-85.42, 12.95) * mm});
            skLineSegment(sketch, "E12.17.3.17", {"start": v(-85.42, 12.95) * mm, "end": v(-83.85, 15.68) * mm});
            skLineSegment(sketch, "E12.0.3.18", {"start": v(-83.85, 24.32) * mm, "end": v(-80.7, 24.32) * mm});
            skLineSegment(sketch, "E12.3.3.18", {"start": v(-80.7, 24.32) * mm, "end": v(-79.12, 21.59) * mm});
            skLineSegment(sketch, "E12.6.3.18", {"start": v(-79.12, 21.59) * mm, "end": v(-80.7, 18.86) * mm});
            skCircle(sketch, "E12.9.3.18", {"center": v(-82.27, 21.59) * mm, "radius": 2.73 * mm, "construction": true});
            skLineSegment(sketch, "E12.11.3.18", {"start": v(-80.7, 18.86) * mm, "end": v(-83.85, 18.86) * mm});
            skLineSegment(sketch, "E12.14.3.18", {"start": v(-83.85, 18.86) * mm, "end": v(-85.42, 21.59) * mm});
            skLineSegment(sketch, "E12.17.3.18", {"start": v(-85.42, 21.6) * mm, "end": v(-83.85, 24.32) * mm});
            skLineSegment(sketch, "E12.0.3.19", {"start": v(-83.85, 32.96) * mm, "end": v(-80.7, 32.96) * mm});
            skLineSegment(sketch, "E12.3.3.19", {"start": v(-80.7, 32.96) * mm, "end": v(-79.12, 30.23) * mm});
            skLineSegment(sketch, "E12.6.3.19", {"start": v(-79.12, 30.23) * mm, "end": v(-80.7, 27.5) * mm});
            skCircle(sketch, "E12.9.3.19", {"center": v(-82.27, 30.23) * mm, "radius": 2.73 * mm, "construction": true});
            skLineSegment(sketch, "E12.11.3.19", {"start": v(-80.7, 27.5) * mm, "end": v(-83.85, 27.5) * mm});
            skLineSegment(sketch, "E12.14.3.19", {"start": v(-83.85, 27.5) * mm, "end": v(-85.42, 30.23) * mm});
            skLineSegment(sketch, "E12.17.3.19", {"start": v(-85.42, 30.23) * mm, "end": v(-83.85, 32.96) * mm});
            skLineSegment(sketch, "E12.0.4.9", {"start": v(-68.89, -53.4) * mm, "end": v(-65.73, -53.4) * mm});
            skLineSegment(sketch, "E12.3.4.9", {"start": v(-65.73, -53.4) * mm, "end": v(-64.16, -56.13) * mm});
            skLineSegment(sketch, "E12.6.4.9", {"start": v(-64.16, -56.13) * mm, "end": v(-65.73, -58.86) * mm});
            skCircle(sketch, "E12.9.4.9", {"center": v(-67.31, -56.13) * mm, "radius": 2.73 * mm, "construction": true});
            skLineSegment(sketch, "E12.11.4.9", {"start": v(-65.73, -58.86) * mm, "end": v(-68.89, -58.86) * mm});
            skLineSegment(sketch, "E12.14.4.9", {"start": v(-68.89, -58.86) * mm, "end": v(-70.46, -56.13) * mm});
            skLineSegment(sketch, "E12.17.4.9", {"start": v(-70.46, -56.13) * mm, "end": v(-68.89, -53.4) * mm});
            skLineSegment(sketch, "E12.0.4.10", {"start": v(-68.89, -44.77) * mm, "end": v(-65.73, -44.77) * mm});
            skLineSegment(sketch, "E12.3.4.10", {"start": v(-65.73, -44.77) * mm, "end": v(-64.16, -47.5) * mm});
            skLineSegment(sketch, "E12.6.4.10", {"start": v(-64.16, -47.5) * mm, "end": v(-65.73, -50.23) * mm});
            skCircle(sketch, "E12.9.4.10", {"center": v(-67.31, -47.5) * mm, "radius": 2.73 * mm, "construction": true});
            skLineSegment(sketch, "E12.11.4.10", {"start": v(-65.73, -50.23) * mm, "end": v(-68.89, -50.23) * mm});
            skLineSegment(sketch, "E12.14.4.10", {"start": v(-68.89, -50.23) * mm, "end": v(-70.46, -47.5) * mm});
            skLineSegment(sketch, "E12.17.4.10", {"start": v(-70.46, -47.5) * mm, "end": v(-68.89, -44.77) * mm});
            skLineSegment(sketch, "E12.0.4.11", {"start": v(-68.89, -36.13) * mm, "end": v(-65.73, -36.13) * mm});
            skLineSegment(sketch, "E12.3.4.11", {"start": v(-65.73, -36.13) * mm, "end": v(-64.16, -38.86) * mm});
            skLineSegment(sketch, "E12.6.4.11", {"start": v(-64.16, -38.86) * mm, "end": v(-65.73, -41.6) * mm});
            skCircle(sketch, "E12.9.4.11", {"center": v(-67.31, -38.86) * mm, "radius": 2.73 * mm, "construction": true});
            skLineSegment(sketch, "E12.11.4.11", {"start": v(-65.73, -41.6) * mm, "end": v(-68.89, -41.6) * mm});
            skLineSegment(sketch, "E12.14.4.11", {"start": v(-68.89, -41.6) * mm, "end": v(-70.46, -38.86) * mm});
            skLineSegment(sketch, "E12.17.4.11", {"start": v(-70.46, -38.86) * mm, "end": v(-68.89, -36.13) * mm});
            skLineSegment(sketch, "E12.0.4.12", {"start": v(-68.89, -27.5) * mm, "end": v(-65.73, -27.5) * mm});
            skLineSegment(sketch, "E12.3.4.12", {"start": v(-65.73, -27.5) * mm, "end": v(-64.16, -30.23) * mm});
            skLineSegment(sketch, "E12.6.4.12", {"start": v(-64.16, -30.23) * mm, "end": v(-65.73, -32.96) * mm});
            skCircle(sketch, "E12.9.4.12", {"center": v(-67.31, -30.23) * mm, "radius": 2.73 * mm, "construction": true});
            skLineSegment(sketch, "E12.11.4.12", {"start": v(-65.73, -32.96) * mm, "end": v(-68.89, -32.96) * mm});
            skLineSegment(sketch, "E12.14.4.12", {"start": v(-68.89, -32.96) * mm, "end": v(-70.46, -30.23) * mm});
            skLineSegment(sketch, "E12.17.4.12", {"start": v(-70.46, -30.23) * mm, "end": v(-68.89, -27.5) * mm});
            skLineSegment(sketch, "E12.0.4.13", {"start": v(-68.89, -18.86) * mm, "end": v(-65.73, -18.86) * mm});
            skLineSegment(sketch, "E12.3.4.13", {"start": v(-65.73, -18.86) * mm, "end": v(-64.16, -21.6) * mm});
            skLineSegment(sketch, "E12.6.4.13", {"start": v(-64.16, -21.6) * mm, "end": v(-65.73, -24.32) * mm});
            skCircle(sketch, "E12.9.4.13", {"center": v(-67.31, -21.6) * mm, "radius": 2.73 * mm, "construction": true});
            skLineSegment(sketch, "E12.11.4.13", {"start": v(-65.73, -24.32) * mm, "end": v(-68.89, -24.32) * mm});
            skLineSegment(sketch, "E12.14.4.13", {"start": v(-68.89, -24.32) * mm, "end": v(-70.46, -21.6) * mm});
            skLineSegment(sketch, "E12.17.4.13", {"start": v(-70.46, -21.59) * mm, "end": v(-68.89, -18.86) * mm});
            skLineSegment(sketch, "E12.0.4.14", {"start": v(-68.89, -10.22) * mm, "end": v(-65.73, -10.22) * mm});
            skLineSegment(sketch, "E12.3.4.14", {"start": v(-65.73, -10.22) * mm, "end": v(-64.16, -12.95) * mm});
            skLineSegment(sketch, "E12.6.4.14", {"start": v(-64.16, -12.95) * mm, "end": v(-65.73, -15.68) * mm});
            skCircle(sketch, "E12.9.4.14", {"center": v(-67.31, -12.95) * mm, "radius": 2.73 * mm, "construction": true});
            skLineSegment(sketch, "E12.11.4.14", {"start": v(-65.73, -15.68) * mm, "end": v(-68.89, -15.68) * mm});
            skLineSegment(sketch, "E12.14.4.14", {"start": v(-68.89, -15.68) * mm, "end": v(-70.46, -12.95) * mm});
            skLineSegment(sketch, "E12.17.4.14", {"start": v(-70.46, -12.95) * mm, "end": v(-68.89, -10.22) * mm});
            skLineSegment(sketch, "E12.0.4.15", {"start": v(-68.89, -1.59) * mm, "end": v(-65.73, -1.59) * mm});
            skLineSegment(sketch, "E12.3.4.15", {"start": v(-65.73, -1.59) * mm, "end": v(-64.16, -4.32) * mm});
            skLineSegment(sketch, "E12.6.4.15", {"start": v(-64.16, -4.32) * mm, "end": v(-65.73, -7.05) * mm});
            skCircle(sketch, "E12.9.4.15", {"center": v(-67.31, -4.32) * mm, "radius": 2.73 * mm, "construction": true});
            skLineSegment(sketch, "E12.11.4.15", {"start": v(-65.73, -7.05) * mm, "end": v(-68.89, -7.05) * mm});
            skLineSegment(sketch, "E12.14.4.15", {"start": v(-68.89, -7.05) * mm, "end": v(-70.46, -4.32) * mm});
            skLineSegment(sketch, "E12.17.4.15", {"start": v(-70.46, -4.32) * mm, "end": v(-68.89, -1.59) * mm});
            skLineSegment(sketch, "E12.0.4.16", {"start": v(-68.89, 7.05) * mm, "end": v(-65.73, 7.05) * mm});
            skLineSegment(sketch, "E12.3.4.16", {"start": v(-65.73, 7.05) * mm, "end": v(-64.16, 4.32) * mm});
            skLineSegment(sketch, "E12.6.4.16", {"start": v(-64.16, 4.32) * mm, "end": v(-65.73, 1.59) * mm});
            skCircle(sketch, "E12.9.4.16", {"center": v(-67.31, 4.32) * mm, "radius": 2.73 * mm, "construction": true});
            skLineSegment(sketch, "E12.11.4.16", {"start": v(-65.73, 1.59) * mm, "end": v(-68.89, 1.59) * mm});
            skLineSegment(sketch, "E12.14.4.16", {"start": v(-68.89, 1.59) * mm, "end": v(-70.46, 4.32) * mm});
            skLineSegment(sketch, "E12.17.4.16", {"start": v(-70.46, 4.32) * mm, "end": v(-68.89, 7.05) * mm});
            skLineSegment(sketch, "E12.0.4.17", {"start": v(-68.89, 15.68) * mm, "end": v(-65.73, 15.68) * mm});
            skLineSegment(sketch, "E12.3.4.17", {"start": v(-65.73, 15.68) * mm, "end": v(-64.16, 12.95) * mm});
            skLineSegment(sketch, "E12.6.4.17", {"start": v(-64.16, 12.95) * mm, "end": v(-65.73, 10.22) * mm});
            skCircle(sketch, "E12.9.4.17", {"center": v(-67.31, 12.95) * mm, "radius": 2.73 * mm, "construction": true});
            skLineSegment(sketch, "E12.11.4.17", {"start": v(-65.73, 10.22) * mm, "end": v(-68.89, 10.22) * mm});
            skLineSegment(sketch, "E12.14.4.17", {"start": v(-68.89, 10.22) * mm, "end": v(-70.46, 12.95) * mm});
            skLineSegment(sketch, "E12.17.4.17", {"start": v(-70.46, 12.95) * mm, "end": v(-68.89, 15.68) * mm});
            skLineSegment(sketch, "E12.0.4.18", {"start": v(-68.89, 24.32) * mm, "end": v(-65.73, 24.32) * mm});
            skLineSegment(sketch, "E12.3.4.18", {"start": v(-65.73, 24.32) * mm, "end": v(-64.16, 21.59) * mm});
            skLineSegment(sketch, "E12.6.4.18", {"start": v(-64.16, 21.59) * mm, "end": v(-65.73, 18.86) * mm});
            skCircle(sketch, "E12.9.4.18", {"center": v(-67.31, 21.59) * mm, "radius": 2.73 * mm, "construction": true});
            skLineSegment(sketch, "E12.11.4.18", {"start": v(-65.73, 18.86) * mm, "end": v(-68.89, 18.86) * mm});
            skLineSegment(sketch, "E12.14.4.18", {"start": v(-68.89, 18.86) * mm, "end": v(-70.46, 21.59) * mm});
            skLineSegment(sketch, "E12.17.4.18", {"start": v(-70.46, 21.6) * mm, "end": v(-68.89, 24.32) * mm});
            skLineSegment(sketch, "E12.0.4.19", {"start": v(-68.89, 32.96) * mm, "end": v(-65.73, 32.96) * mm});
            skLineSegment(sketch, "E12.3.4.19", {"start": v(-65.73, 32.96) * mm, "end": v(-64.16, 30.23) * mm});
            skLineSegment(sketch, "E12.6.4.19", {"start": v(-64.16, 30.23) * mm, "end": v(-65.73, 27.5) * mm});
            skCircle(sketch, "E12.9.4.19", {"center": v(-67.31, 30.23) * mm, "radius": 2.73 * mm, "construction": true});
            skLineSegment(sketch, "E12.11.4.19", {"start": v(-65.73, 27.5) * mm, "end": v(-68.89, 27.5) * mm});
            skLineSegment(sketch, "E12.14.4.19", {"start": v(-68.89, 27.5) * mm, "end": v(-70.46, 30.23) * mm});
            skLineSegment(sketch, "E12.17.4.19", {"start": v(-70.46, 30.23) * mm, "end": v(-68.89, 32.96) * mm});
            skLineSegment(sketch, "E12.0.5.9", {"start": v(-53.93, -53.4) * mm, "end": v(-50.78, -53.4) * mm});
            skLineSegment(sketch, "E12.3.5.9", {"start": v(-50.78, -53.4) * mm, "end": v(-49.2, -56.13) * mm});
            skLineSegment(sketch, "E12.6.5.9", {"start": v(-49.2, -56.13) * mm, "end": v(-50.78, -58.86) * mm});
            skCircle(sketch, "E12.9.5.9", {"center": v(-52.35, -56.13) * mm, "radius": 2.73 * mm, "construction": true});
            skLineSegment(sketch, "E12.11.5.9", {"start": v(-50.78, -58.86) * mm, "end": v(-53.93, -58.86) * mm});
            skLineSegment(sketch, "E12.14.5.9", {"start": v(-53.93, -58.86) * mm, "end": v(-55.5, -56.13) * mm});
            skLineSegment(sketch, "E12.17.5.9", {"start": v(-55.5, -56.13) * mm, "end": v(-53.93, -53.4) * mm});
            skLineSegment(sketch, "E12.0.5.10", {"start": v(-53.93, -44.77) * mm, "end": v(-50.78, -44.77) * mm});
            skLineSegment(sketch, "E12.3.5.10", {"start": v(-50.78, -44.77) * mm, "end": v(-49.2, -47.5) * mm});
            skLineSegment(sketch, "E12.6.5.10", {"start": v(-49.2, -47.5) * mm, "end": v(-50.78, -50.23) * mm});
            skCircle(sketch, "E12.9.5.10", {"center": v(-52.35, -47.5) * mm, "radius": 2.73 * mm, "construction": true});
            skLineSegment(sketch, "E12.11.5.10", {"start": v(-50.78, -50.23) * mm, "end": v(-53.93, -50.23) * mm});
            skLineSegment(sketch, "E12.14.5.10", {"start": v(-53.93, -50.23) * mm, "end": v(-55.5, -47.5) * mm});
            skLineSegment(sketch, "E12.17.5.10", {"start": v(-55.5, -47.5) * mm, "end": v(-53.93, -44.77) * mm});
            skLineSegment(sketch, "E12.0.5.11", {"start": v(-53.93, -36.13) * mm, "end": v(-50.78, -36.13) * mm});
            skLineSegment(sketch, "E12.3.5.11", {"start": v(-50.78, -36.13) * mm, "end": v(-49.2, -38.86) * mm});
            skLineSegment(sketch, "E12.6.5.11", {"start": v(-49.2, -38.86) * mm, "end": v(-50.78, -41.6) * mm});
            skCircle(sketch, "E12.9.5.11", {"center": v(-52.35, -38.86) * mm, "radius": 2.73 * mm, "construction": true});
            skLineSegment(sketch, "E12.11.5.11", {"start": v(-50.78, -41.6) * mm, "end": v(-53.93, -41.6) * mm});
            skLineSegment(sketch, "E12.14.5.11", {"start": v(-53.93, -41.6) * mm, "end": v(-55.5, -38.86) * mm});
            skLineSegment(sketch, "E12.17.5.11", {"start": v(-55.5, -38.86) * mm, "end": v(-53.93, -36.13) * mm});
            skLineSegment(sketch, "E12.0.5.12", {"start": v(-53.93, -27.5) * mm, "end": v(-50.78, -27.5) * mm});
            skLineSegment(sketch, "E12.3.5.12", {"start": v(-50.78, -27.5) * mm, "end": v(-49.2, -30.23) * mm});
            skLineSegment(sketch, "E12.6.5.12", {"start": v(-49.2, -30.23) * mm, "end": v(-50.78, -32.96) * mm});
            skCircle(sketch, "E12.9.5.12", {"center": v(-52.35, -30.23) * mm, "radius": 2.73 * mm, "construction": true});
            skLineSegment(sketch, "E12.11.5.12", {"start": v(-50.78, -32.96) * mm, "end": v(-53.93, -32.96) * mm});
            skLineSegment(sketch, "E12.14.5.12", {"start": v(-53.93, -32.96) * mm, "end": v(-55.5, -30.23) * mm});
            skLineSegment(sketch, "E12.17.5.12", {"start": v(-55.5, -30.23) * mm, "end": v(-53.93, -27.5) * mm});
            skLineSegment(sketch, "E12.0.5.13", {"start": v(-53.93, -18.86) * mm, "end": v(-50.78, -18.86) * mm});
            skLineSegment(sketch, "E12.3.5.13", {"start": v(-50.78, -18.86) * mm, "end": v(-49.2, -21.6) * mm});
            skLineSegment(sketch, "E12.6.5.13", {"start": v(-49.2, -21.6) * mm, "end": v(-50.78, -24.32) * mm});
            skCircle(sketch, "E12.9.5.13", {"center": v(-52.35, -21.6) * mm, "radius": 2.73 * mm, "construction": true});
            skLineSegment(sketch, "E12.11.5.13", {"start": v(-50.78, -24.32) * mm, "end": v(-53.93, -24.32) * mm});
            skLineSegment(sketch, "E12.14.5.13", {"start": v(-53.93, -24.32) * mm, "end": v(-55.5, -21.6) * mm});
            skLineSegment(sketch, "E12.17.5.13", {"start": v(-55.5, -21.59) * mm, "end": v(-53.93, -18.86) * mm});
            skLineSegment(sketch, "E12.0.5.14", {"start": v(-53.93, -10.22) * mm, "end": v(-50.78, -10.22) * mm});
            skLineSegment(sketch, "E12.3.5.14", {"start": v(-50.78, -10.22) * mm, "end": v(-49.2, -12.95) * mm});
            skLineSegment(sketch, "E12.6.5.14", {"start": v(-49.2, -12.95) * mm, "end": v(-50.78, -15.68) * mm});
            skCircle(sketch, "E12.9.5.14", {"center": v(-52.35, -12.95) * mm, "radius": 2.73 * mm, "construction": true});
            skLineSegment(sketch, "E12.11.5.14", {"start": v(-50.78, -15.68) * mm, "end": v(-53.93, -15.68) * mm});
            skLineSegment(sketch, "E12.14.5.14", {"start": v(-53.93, -15.68) * mm, "end": v(-55.5, -12.95) * mm});
            skLineSegment(sketch, "E12.17.5.14", {"start": v(-55.5, -12.95) * mm, "end": v(-53.93, -10.22) * mm});
            skLineSegment(sketch, "E12.0.5.15", {"start": v(-53.93, -1.59) * mm, "end": v(-50.78, -1.59) * mm});
            skLineSegment(sketch, "E12.3.5.15", {"start": v(-50.78, -1.59) * mm, "end": v(-49.2, -4.32) * mm});
            skLineSegment(sketch, "E12.6.5.15", {"start": v(-49.2, -4.32) * mm, "end": v(-50.78, -7.05) * mm});
            skCircle(sketch, "E12.9.5.15", {"center": v(-52.35, -4.32) * mm, "radius": 2.73 * mm, "construction": true});
            skLineSegment(sketch, "E12.11.5.15", {"start": v(-50.78, -7.05) * mm, "end": v(-53.93, -7.05) * mm});
            skLineSegment(sketch, "E12.14.5.15", {"start": v(-53.93, -7.05) * mm, "end": v(-55.5, -4.32) * mm});
            skLineSegment(sketch, "E12.17.5.15", {"start": v(-55.5, -4.32) * mm, "end": v(-53.93, -1.59) * mm});
            skLineSegment(sketch, "E12.0.5.16", {"start": v(-53.93, 7.05) * mm, "end": v(-50.78, 7.05) * mm});
            skLineSegment(sketch, "E12.3.5.16", {"start": v(-50.78, 7.05) * mm, "end": v(-49.2, 4.32) * mm});
            skLineSegment(sketch, "E12.6.5.16", {"start": v(-49.2, 4.32) * mm, "end": v(-50.78, 1.59) * mm});
            skCircle(sketch, "E12.9.5.16", {"center": v(-52.35, 4.32) * mm, "radius": 2.73 * mm, "construction": true});
            skLineSegment(sketch, "E12.11.5.16", {"start": v(-50.78, 1.59) * mm, "end": v(-53.93, 1.59) * mm});
            skLineSegment(sketch, "E12.14.5.16", {"start": v(-53.93, 1.59) * mm, "end": v(-55.5, 4.32) * mm});
            skLineSegment(sketch, "E12.17.5.16", {"start": v(-55.5, 4.32) * mm, "end": v(-53.93, 7.05) * mm});
            skLineSegment(sketch, "E12.0.5.17", {"start": v(-53.93, 15.68) * mm, "end": v(-50.78, 15.68) * mm});
            skLineSegment(sketch, "E12.3.5.17", {"start": v(-50.78, 15.68) * mm, "end": v(-49.2, 12.95) * mm});
            skLineSegment(sketch, "E12.6.5.17", {"start": v(-49.2, 12.95) * mm, "end": v(-50.78, 10.22) * mm});
            skCircle(sketch, "E12.9.5.17", {"center": v(-52.35, 12.95) * mm, "radius": 2.73 * mm, "construction": true});
            skLineSegment(sketch, "E12.11.5.17", {"start": v(-50.78, 10.22) * mm, "end": v(-53.93, 10.22) * mm});
            skLineSegment(sketch, "E12.14.5.17", {"start": v(-53.93, 10.22) * mm, "end": v(-55.5, 12.95) * mm});
            skLineSegment(sketch, "E12.17.5.17", {"start": v(-55.5, 12.95) * mm, "end": v(-53.93, 15.68) * mm});
            skLineSegment(sketch, "E12.0.5.18", {"start": v(-53.93, 24.32) * mm, "end": v(-50.78, 24.32) * mm});
            skLineSegment(sketch, "E12.3.5.18", {"start": v(-50.78, 24.32) * mm, "end": v(-49.2, 21.59) * mm});
            skLineSegment(sketch, "E12.6.5.18", {"start": v(-49.2, 21.59) * mm, "end": v(-50.78, 18.86) * mm});
            skCircle(sketch, "E12.9.5.18", {"center": v(-52.35, 21.59) * mm, "radius": 2.73 * mm, "construction": true});
            skLineSegment(sketch, "E12.11.5.18", {"start": v(-50.78, 18.86) * mm, "end": v(-53.93, 18.86) * mm});
            skLineSegment(sketch, "E12.14.5.18", {"start": v(-53.93, 18.86) * mm, "end": v(-55.5, 21.59) * mm});
            skLineSegment(sketch, "E12.17.5.18", {"start": v(-55.5, 21.59) * mm, "end": v(-53.93, 24.32) * mm});
            skLineSegment(sketch, "E12.0.5.19", {"start": v(-53.93, 32.96) * mm, "end": v(-50.78, 32.96) * mm});
            skLineSegment(sketch, "E12.3.5.19", {"start": v(-50.78, 32.96) * mm, "end": v(-49.2, 30.23) * mm});
            skLineSegment(sketch, "E12.6.5.19", {"start": v(-49.2, 30.23) * mm, "end": v(-50.78, 27.5) * mm});
            skCircle(sketch, "E12.9.5.19", {"center": v(-52.35, 30.23) * mm, "radius": 2.73 * mm, "construction": true});
            skLineSegment(sketch, "E12.11.5.19", {"start": v(-50.78, 27.5) * mm, "end": v(-53.93, 27.5) * mm});
            skLineSegment(sketch, "E12.14.5.19", {"start": v(-53.93, 27.5) * mm, "end": v(-55.5, 30.23) * mm});
            skLineSegment(sketch, "E12.17.5.19", {"start": v(-55.5, 30.23) * mm, "end": v(-53.93, 32.96) * mm});
            skCircle(sketch, "E13.0.0.8", {"center": v(-119.66, -60.45) * mm, "radius": 2.73 * mm, "construction": true});
            skLineSegment(sketch, "E13.2.0.8", {"start": v(-122.82, -60.45) * mm, "end": v(-121.24, -57.72) * mm});
            skLineSegment(sketch, "E13.5.0.8", {"start": v(-121.24, -57.72) * mm, "end": v(-118.09, -57.72) * mm});
            skLineSegment(sketch, "E13.8.0.8", {"start": v(-118.09, -57.72) * mm, "end": v(-116.51, -60.45) * mm});
            skLineSegment(sketch, "E13.11.0.8", {"start": v(-116.51, -60.45) * mm, "end": v(-118.09, -63.18) * mm});
            skLineSegment(sketch, "E13.14.0.8", {"start": v(-118.09, -63.18) * mm, "end": v(-121.24, -63.18) * mm});
            skLineSegment(sketch, "E13.17.0.8", {"start": v(-121.24, -63.18) * mm, "end": v(-122.82, -60.45) * mm});
            skCircle(sketch, "E13.0.0.9", {"center": v(-119.66, -51.82) * mm, "radius": 2.73 * mm, "construction": true});
            skLineSegment(sketch, "E13.2.0.9", {"start": v(-122.82, -51.82) * mm, "end": v(-121.24, -49.09) * mm});
            skLineSegment(sketch, "E13.5.0.9", {"start": v(-121.24, -49.09) * mm, "end": v(-118.09, -49.09) * mm});
            skLineSegment(sketch, "E13.8.0.9", {"start": v(-118.09, -49.09) * mm, "end": v(-116.51, -51.82) * mm});
            skLineSegment(sketch, "E13.11.0.9", {"start": v(-116.51, -51.82) * mm, "end": v(-118.09, -54.55) * mm});
            skLineSegment(sketch, "E13.14.0.9", {"start": v(-118.09, -54.55) * mm, "end": v(-121.24, -54.55) * mm});
            skLineSegment(sketch, "E13.17.0.9", {"start": v(-121.24, -54.55) * mm, "end": v(-122.82, -51.82) * mm});
            skCircle(sketch, "E13.0.0.10", {"center": v(-119.66, -43.18) * mm, "radius": 2.73 * mm, "construction": true});
            skLineSegment(sketch, "E13.2.0.10", {"start": v(-122.82, -43.18) * mm, "end": v(-121.24, -40.45) * mm});
            skLineSegment(sketch, "E13.5.0.10", {"start": v(-121.24, -40.45) * mm, "end": v(-118.09, -40.45) * mm});
            skLineSegment(sketch, "E13.8.0.10", {"start": v(-118.09, -40.45) * mm, "end": v(-116.51, -43.18) * mm});
            skLineSegment(sketch, "E13.11.0.10", {"start": v(-116.51, -43.18) * mm, "end": v(-118.09, -45.91) * mm});
            skLineSegment(sketch, "E13.14.0.10", {"start": v(-118.09, -45.91) * mm, "end": v(-121.24, -45.91) * mm});
            skLineSegment(sketch, "E13.17.0.10", {"start": v(-121.24, -45.91) * mm, "end": v(-122.82, -43.18) * mm});
            skCircle(sketch, "E13.0.0.11", {"center": v(-119.66, -34.54) * mm, "radius": 2.73 * mm, "construction": true});
            skLineSegment(sketch, "E13.2.0.11", {"start": v(-122.82, -34.54) * mm, "end": v(-121.24, -31.81) * mm});
            skLineSegment(sketch, "E13.5.0.11", {"start": v(-121.24, -31.81) * mm, "end": v(-118.09, -31.81) * mm});
            skLineSegment(sketch, "E13.8.0.11", {"start": v(-118.09, -31.81) * mm, "end": v(-116.51, -34.54) * mm});
            skLineSegment(sketch, "E13.11.0.11", {"start": v(-116.51, -34.54) * mm, "end": v(-118.09, -37.27) * mm});
            skLineSegment(sketch, "E13.14.0.11", {"start": v(-118.09, -37.27) * mm, "end": v(-121.24, -37.27) * mm});
            skLineSegment(sketch, "E13.17.0.11", {"start": v(-121.24, -37.27) * mm, "end": v(-122.82, -34.54) * mm});
            skCircle(sketch, "E13.0.0.12", {"center": v(-119.66, -25.9) * mm, "radius": 2.73 * mm, "construction": true});
            skLineSegment(sketch, "E13.2.0.12", {"start": v(-122.82, -25.9) * mm, "end": v(-121.24, -23.18) * mm});
            skLineSegment(sketch, "E13.5.0.12", {"start": v(-121.24, -23.18) * mm, "end": v(-118.09, -23.18) * mm});
            skLineSegment(sketch, "E13.8.0.12", {"start": v(-118.09, -23.18) * mm, "end": v(-116.51, -25.9) * mm});
            skLineSegment(sketch, "E13.11.0.12", {"start": v(-116.51, -25.9) * mm, "end": v(-118.09, -28.64) * mm});
            skLineSegment(sketch, "E13.14.0.12", {"start": v(-118.09, -28.64) * mm, "end": v(-121.24, -28.64) * mm});
            skLineSegment(sketch, "E13.17.0.12", {"start": v(-121.24, -28.64) * mm, "end": v(-122.82, -25.9) * mm});
            skCircle(sketch, "E13.0.0.13", {"center": v(-119.66, -17.27) * mm, "radius": 2.73 * mm, "construction": true});
            skLineSegment(sketch, "E13.2.0.13", {"start": v(-122.82, -17.27) * mm, "end": v(-121.24, -14.54) * mm});
            skLineSegment(sketch, "E13.5.0.13", {"start": v(-121.24, -14.54) * mm, "end": v(-118.09, -14.54) * mm});
            skLineSegment(sketch, "E13.8.0.13", {"start": v(-118.09, -14.54) * mm, "end": v(-116.51, -17.27) * mm});
            skLineSegment(sketch, "E13.11.0.13", {"start": v(-116.51, -17.27) * mm, "end": v(-118.09, -20) * mm});
            skLineSegment(sketch, "E13.14.0.13", {"start": v(-118.09, -20) * mm, "end": v(-121.24, -20) * mm});
            skLineSegment(sketch, "E13.17.0.13", {"start": v(-121.24, -20) * mm, "end": v(-122.82, -17.27) * mm});
            skCircle(sketch, "E13.0.0.14", {"center": v(-119.66, -8.64) * mm, "radius": 2.73 * mm, "construction": true});
            skLineSegment(sketch, "E13.2.0.14", {"start": v(-122.82, -8.64) * mm, "end": v(-121.24, -5.9) * mm});
            skLineSegment(sketch, "E13.5.0.14", {"start": v(-121.24, -5.9) * mm, "end": v(-118.09, -5.9) * mm});
            skLineSegment(sketch, "E13.8.0.14", {"start": v(-118.09, -5.9) * mm, "end": v(-116.51, -8.64) * mm});
            skLineSegment(sketch, "E13.11.0.14", {"start": v(-116.51, -8.64) * mm, "end": v(-118.09, -11.37) * mm});
            skLineSegment(sketch, "E13.14.0.14", {"start": v(-118.09, -11.37) * mm, "end": v(-121.24, -11.37) * mm});
            skLineSegment(sketch, "E13.17.0.14", {"start": v(-121.24, -11.37) * mm, "end": v(-122.82, -8.64) * mm});
            skCircle(sketch, "E13.0.0.15", {"center": v(-119.66, 0) * mm, "radius": 2.73 * mm, "construction": true});
            skLineSegment(sketch, "E13.2.0.15", {"start": v(-122.82, 0) * mm, "end": v(-121.24, 2.73) * mm});
            skLineSegment(sketch, "E13.5.0.15", {"start": v(-121.24, 2.73) * mm, "end": v(-118.09, 2.73) * mm});
            skLineSegment(sketch, "E13.8.0.15", {"start": v(-118.09, 2.73) * mm, "end": v(-116.51, 0) * mm});
            skLineSegment(sketch, "E13.11.0.15", {"start": v(-116.51, 0) * mm, "end": v(-118.09, -2.73) * mm});
            skLineSegment(sketch, "E13.14.0.15", {"start": v(-118.09, -2.73) * mm, "end": v(-121.24, -2.73) * mm});
            skLineSegment(sketch, "E13.17.0.15", {"start": v(-121.24, -2.73) * mm, "end": v(-122.82, 0) * mm});
            skCircle(sketch, "E13.0.0.16", {"center": v(-119.66, 8.64) * mm, "radius": 2.73 * mm, "construction": true});
            skLineSegment(sketch, "E13.2.0.16", {"start": v(-122.82, 8.64) * mm, "end": v(-121.24, 11.37) * mm});
            skLineSegment(sketch, "E13.5.0.16", {"start": v(-121.24, 11.37) * mm, "end": v(-118.09, 11.37) * mm});
            skLineSegment(sketch, "E13.8.0.16", {"start": v(-118.09, 11.37) * mm, "end": v(-116.51, 8.64) * mm});
            skLineSegment(sketch, "E13.11.0.16", {"start": v(-116.51, 8.64) * mm, "end": v(-118.09, 5.9) * mm});
            skLineSegment(sketch, "E13.14.0.16", {"start": v(-118.09, 5.9) * mm, "end": v(-121.24, 5.9) * mm});
            skLineSegment(sketch, "E13.17.0.16", {"start": v(-121.24, 5.9) * mm, "end": v(-122.82, 8.64) * mm});
            skCircle(sketch, "E13.0.0.17", {"center": v(-119.66, 17.27) * mm, "radius": 2.73 * mm, "construction": true});
            skLineSegment(sketch, "E13.2.0.17", {"start": v(-122.82, 17.27) * mm, "end": v(-121.24, 20) * mm});
            skLineSegment(sketch, "E13.5.0.17", {"start": v(-121.24, 20) * mm, "end": v(-118.09, 20) * mm});
            skLineSegment(sketch, "E13.8.0.17", {"start": v(-118.09, 20) * mm, "end": v(-116.51, 17.27) * mm});
            skLineSegment(sketch, "E13.11.0.17", {"start": v(-116.51, 17.27) * mm, "end": v(-118.09, 14.54) * mm});
            skLineSegment(sketch, "E13.14.0.17", {"start": v(-118.09, 14.54) * mm, "end": v(-121.24, 14.54) * mm});
            skLineSegment(sketch, "E13.17.0.17", {"start": v(-121.24, 14.54) * mm, "end": v(-122.82, 17.27) * mm});
            skCircle(sketch, "E13.0.0.18", {"center": v(-119.66, 25.9) * mm, "radius": 2.73 * mm, "construction": true});
            skLineSegment(sketch, "E13.2.0.18", {"start": v(-122.82, 25.9) * mm, "end": v(-121.24, 28.64) * mm});
            skLineSegment(sketch, "E13.5.0.18", {"start": v(-121.24, 28.64) * mm, "end": v(-118.09, 28.64) * mm});
            skLineSegment(sketch, "E13.8.0.18", {"start": v(-118.09, 28.64) * mm, "end": v(-116.51, 25.9) * mm});
            skLineSegment(sketch, "E13.11.0.18", {"start": v(-116.51, 25.9) * mm, "end": v(-118.09, 23.18) * mm});
            skLineSegment(sketch, "E13.14.0.18", {"start": v(-118.09, 23.18) * mm, "end": v(-121.24, 23.18) * mm});
            skLineSegment(sketch, "E13.17.0.18", {"start": v(-121.24, 23.18) * mm, "end": v(-122.82, 25.9) * mm});
            skCircle(sketch, "E13.0.0.19", {"center": v(-119.66, 34.54) * mm, "radius": 2.73 * mm, "construction": true});
            skLineSegment(sketch, "E13.2.0.19", {"start": v(-122.82, 34.54) * mm, "end": v(-121.24, 37.27) * mm});
            skLineSegment(sketch, "E13.5.0.19", {"start": v(-121.24, 37.27) * mm, "end": v(-118.09, 37.27) * mm});
            skLineSegment(sketch, "E13.8.0.19", {"start": v(-118.09, 37.27) * mm, "end": v(-116.51, 34.54) * mm});
            skLineSegment(sketch, "E13.11.0.19", {"start": v(-116.51, 34.54) * mm, "end": v(-118.09, 31.81) * mm});
            skLineSegment(sketch, "E13.14.0.19", {"start": v(-118.09, 31.81) * mm, "end": v(-121.24, 31.81) * mm});
            skLineSegment(sketch, "E13.17.0.19", {"start": v(-121.24, 31.81) * mm, "end": v(-122.82, 34.54) * mm});
            skCircle(sketch, "E13.0.1.8", {"center": v(-104.7, -60.45) * mm, "radius": 2.73 * mm, "construction": true});
            skLineSegment(sketch, "E13.2.1.8", {"start": v(-107.86, -60.45) * mm, "end": v(-106.28, -57.72) * mm});
            skLineSegment(sketch, "E13.5.1.8", {"start": v(-106.28, -57.72) * mm, "end": v(-103.13, -57.72) * mm});
            skLineSegment(sketch, "E13.8.1.8", {"start": v(-103.13, -57.72) * mm, "end": v(-101.55, -60.45) * mm});
            skLineSegment(sketch, "E13.11.1.8", {"start": v(-101.55, -60.45) * mm, "end": v(-103.13, -63.18) * mm});
            skLineSegment(sketch, "E13.14.1.8", {"start": v(-103.13, -63.18) * mm, "end": v(-106.28, -63.18) * mm});
            skLineSegment(sketch, "E13.17.1.8", {"start": v(-106.28, -63.18) * mm, "end": v(-107.86, -60.45) * mm});
            skCircle(sketch, "E13.0.1.9", {"center": v(-104.7, -51.82) * mm, "radius": 2.73 * mm, "construction": true});
            skLineSegment(sketch, "E13.2.1.9", {"start": v(-107.86, -51.82) * mm, "end": v(-106.28, -49.09) * mm});
            skLineSegment(sketch, "E13.5.1.9", {"start": v(-106.28, -49.09) * mm, "end": v(-103.13, -49.09) * mm});
            skLineSegment(sketch, "E13.8.1.9", {"start": v(-103.13, -49.09) * mm, "end": v(-101.55, -51.82) * mm});
            skLineSegment(sketch, "E13.11.1.9", {"start": v(-101.55, -51.82) * mm, "end": v(-103.13, -54.55) * mm});
            skLineSegment(sketch, "E13.14.1.9", {"start": v(-103.13, -54.55) * mm, "end": v(-106.28, -54.55) * mm});
            skLineSegment(sketch, "E13.17.1.9", {"start": v(-106.28, -54.55) * mm, "end": v(-107.86, -51.82) * mm});
            skCircle(sketch, "E13.0.1.10", {"center": v(-104.7, -43.18) * mm, "radius": 2.73 * mm, "construction": true});
            skLineSegment(sketch, "E13.2.1.10", {"start": v(-107.86, -43.18) * mm, "end": v(-106.28, -40.45) * mm});
            skLineSegment(sketch, "E13.5.1.10", {"start": v(-106.28, -40.45) * mm, "end": v(-103.13, -40.45) * mm});
            skLineSegment(sketch, "E13.8.1.10", {"start": v(-103.13, -40.45) * mm, "end": v(-101.55, -43.18) * mm});
            skLineSegment(sketch, "E13.11.1.10", {"start": v(-101.55, -43.18) * mm, "end": v(-103.13, -45.91) * mm});
            skLineSegment(sketch, "E13.14.1.10", {"start": v(-103.13, -45.91) * mm, "end": v(-106.28, -45.91) * mm});
            skLineSegment(sketch, "E13.17.1.10", {"start": v(-106.28, -45.91) * mm, "end": v(-107.86, -43.18) * mm});
            skCircle(sketch, "E13.0.1.11", {"center": v(-104.7, -34.54) * mm, "radius": 2.73 * mm, "construction": true});
            skLineSegment(sketch, "E13.2.1.11", {"start": v(-107.86, -34.54) * mm, "end": v(-106.28, -31.81) * mm});
            skLineSegment(sketch, "E13.5.1.11", {"start": v(-106.28, -31.81) * mm, "end": v(-103.13, -31.81) * mm});
            skLineSegment(sketch, "E13.8.1.11", {"start": v(-103.13, -31.81) * mm, "end": v(-101.55, -34.54) * mm});
            skLineSegment(sketch, "E13.11.1.11", {"start": v(-101.55, -34.54) * mm, "end": v(-103.13, -37.27) * mm});
            skLineSegment(sketch, "E13.14.1.11", {"start": v(-103.13, -37.27) * mm, "end": v(-106.28, -37.27) * mm});
            skLineSegment(sketch, "E13.17.1.11", {"start": v(-106.28, -37.27) * mm, "end": v(-107.86, -34.54) * mm});
            skCircle(sketch, "E13.0.1.12", {"center": v(-104.7, -25.9) * mm, "radius": 2.73 * mm, "construction": true});
            skLineSegment(sketch, "E13.2.1.12", {"start": v(-107.86, -25.9) * mm, "end": v(-106.28, -23.18) * mm});
            skLineSegment(sketch, "E13.5.1.12", {"start": v(-106.28, -23.18) * mm, "end": v(-103.13, -23.18) * mm});
            skLineSegment(sketch, "E13.8.1.12", {"start": v(-103.13, -23.18) * mm, "end": v(-101.55, -25.9) * mm});
            skLineSegment(sketch, "E13.11.1.12", {"start": v(-101.55, -25.9) * mm, "end": v(-103.13, -28.64) * mm});
            skLineSegment(sketch, "E13.14.1.12", {"start": v(-103.13, -28.64) * mm, "end": v(-106.28, -28.64) * mm});
            skLineSegment(sketch, "E13.17.1.12", {"start": v(-106.28, -28.64) * mm, "end": v(-107.86, -25.9) * mm});
            skCircle(sketch, "E13.0.1.13", {"center": v(-104.7, -17.27) * mm, "radius": 2.73 * mm, "construction": true});
            skLineSegment(sketch, "E13.2.1.13", {"start": v(-107.86, -17.27) * mm, "end": v(-106.28, -14.54) * mm});
            skLineSegment(sketch, "E13.5.1.13", {"start": v(-106.28, -14.54) * mm, "end": v(-103.13, -14.54) * mm});
            skLineSegment(sketch, "E13.8.1.13", {"start": v(-103.13, -14.54) * mm, "end": v(-101.55, -17.27) * mm});
            skLineSegment(sketch, "E13.11.1.13", {"start": v(-101.55, -17.27) * mm, "end": v(-103.13, -20) * mm});
            skLineSegment(sketch, "E13.14.1.13", {"start": v(-103.13, -20) * mm, "end": v(-106.28, -20) * mm});
            skLineSegment(sketch, "E13.17.1.13", {"start": v(-106.28, -20) * mm, "end": v(-107.86, -17.27) * mm});
            skCircle(sketch, "E13.0.1.14", {"center": v(-104.7, -8.64) * mm, "radius": 2.73 * mm, "construction": true});
            skLineSegment(sketch, "E13.2.1.14", {"start": v(-107.86, -8.64) * mm, "end": v(-106.28, -5.9) * mm});
            skLineSegment(sketch, "E13.5.1.14", {"start": v(-106.28, -5.9) * mm, "end": v(-103.13, -5.9) * mm});
            skLineSegment(sketch, "E13.8.1.14", {"start": v(-103.13, -5.9) * mm, "end": v(-101.55, -8.64) * mm});
            skLineSegment(sketch, "E13.11.1.14", {"start": v(-101.55, -8.64) * mm, "end": v(-103.13, -11.37) * mm});
            skLineSegment(sketch, "E13.14.1.14", {"start": v(-103.13, -11.37) * mm, "end": v(-106.28, -11.37) * mm});
            skLineSegment(sketch, "E13.17.1.14", {"start": v(-106.28, -11.37) * mm, "end": v(-107.86, -8.64) * mm});
            skCircle(sketch, "E13.0.1.15", {"center": v(-104.7, 0) * mm, "radius": 2.73 * mm, "construction": true});
            skLineSegment(sketch, "E13.2.1.15", {"start": v(-107.86, 0) * mm, "end": v(-106.28, 2.73) * mm});
            skLineSegment(sketch, "E13.5.1.15", {"start": v(-106.28, 2.73) * mm, "end": v(-103.13, 2.73) * mm});
            skLineSegment(sketch, "E13.8.1.15", {"start": v(-103.13, 2.73) * mm, "end": v(-101.55, 0) * mm});
            skLineSegment(sketch, "E13.11.1.15", {"start": v(-101.55, 0) * mm, "end": v(-103.13, -2.73) * mm});
            skLineSegment(sketch, "E13.14.1.15", {"start": v(-103.13, -2.73) * mm, "end": v(-106.28, -2.73) * mm});
            skLineSegment(sketch, "E13.17.1.15", {"start": v(-106.28, -2.73) * mm, "end": v(-107.86, 0) * mm});
            skCircle(sketch, "E13.0.1.16", {"center": v(-104.7, 8.64) * mm, "radius": 2.73 * mm, "construction": true});
            skLineSegment(sketch, "E13.2.1.16", {"start": v(-107.86, 8.64) * mm, "end": v(-106.28, 11.37) * mm});
            skLineSegment(sketch, "E13.5.1.16", {"start": v(-106.28, 11.37) * mm, "end": v(-103.13, 11.37) * mm});
            skLineSegment(sketch, "E13.8.1.16", {"start": v(-103.13, 11.37) * mm, "end": v(-101.55, 8.64) * mm});
            skLineSegment(sketch, "E13.11.1.16", {"start": v(-101.55, 8.64) * mm, "end": v(-103.13, 5.9) * mm});
            skLineSegment(sketch, "E13.14.1.16", {"start": v(-103.13, 5.9) * mm, "end": v(-106.28, 5.9) * mm});
            skLineSegment(sketch, "E13.17.1.16", {"start": v(-106.28, 5.9) * mm, "end": v(-107.86, 8.64) * mm});
            skCircle(sketch, "E13.0.1.17", {"center": v(-104.7, 17.27) * mm, "radius": 2.73 * mm, "construction": true});
            skLineSegment(sketch, "E13.2.1.17", {"start": v(-107.86, 17.27) * mm, "end": v(-106.28, 20) * mm});
            skLineSegment(sketch, "E13.5.1.17", {"start": v(-106.28, 20) * mm, "end": v(-103.13, 20) * mm});
            skLineSegment(sketch, "E13.8.1.17", {"start": v(-103.13, 20) * mm, "end": v(-101.55, 17.27) * mm});
            skLineSegment(sketch, "E13.11.1.17", {"start": v(-101.55, 17.27) * mm, "end": v(-103.13, 14.54) * mm});
            skLineSegment(sketch, "E13.14.1.17", {"start": v(-103.13, 14.54) * mm, "end": v(-106.28, 14.54) * mm});
            skLineSegment(sketch, "E13.17.1.17", {"start": v(-106.28, 14.54) * mm, "end": v(-107.86, 17.27) * mm});
            skCircle(sketch, "E13.0.1.18", {"center": v(-104.7, 25.9) * mm, "radius": 2.73 * mm, "construction": true});
            skLineSegment(sketch, "E13.2.1.18", {"start": v(-107.86, 25.9) * mm, "end": v(-106.28, 28.64) * mm});
            skLineSegment(sketch, "E13.5.1.18", {"start": v(-106.28, 28.64) * mm, "end": v(-103.13, 28.64) * mm});
            skLineSegment(sketch, "E13.8.1.18", {"start": v(-103.13, 28.64) * mm, "end": v(-101.55, 25.9) * mm});
            skLineSegment(sketch, "E13.11.1.18", {"start": v(-101.55, 25.9) * mm, "end": v(-103.13, 23.18) * mm});
            skLineSegment(sketch, "E13.14.1.18", {"start": v(-103.13, 23.18) * mm, "end": v(-106.28, 23.18) * mm});
            skLineSegment(sketch, "E13.17.1.18", {"start": v(-106.28, 23.18) * mm, "end": v(-107.86, 25.9) * mm});
            skCircle(sketch, "E13.0.1.19", {"center": v(-104.7, 34.54) * mm, "radius": 2.73 * mm, "construction": true});
            skLineSegment(sketch, "E13.2.1.19", {"start": v(-107.86, 34.54) * mm, "end": v(-106.28, 37.27) * mm});
            skLineSegment(sketch, "E13.5.1.19", {"start": v(-106.28, 37.27) * mm, "end": v(-103.13, 37.27) * mm});
            skLineSegment(sketch, "E13.8.1.19", {"start": v(-103.13, 37.27) * mm, "end": v(-101.55, 34.54) * mm});
            skLineSegment(sketch, "E13.11.1.19", {"start": v(-101.55, 34.54) * mm, "end": v(-103.13, 31.81) * mm});
            skLineSegment(sketch, "E13.14.1.19", {"start": v(-103.13, 31.81) * mm, "end": v(-106.28, 31.81) * mm});
            skLineSegment(sketch, "E13.17.1.19", {"start": v(-106.28, 31.81) * mm, "end": v(-107.86, 34.54) * mm});
            skCircle(sketch, "E13.0.2.8", {"center": v(-89.75, -60.45) * mm, "radius": 2.73 * mm, "construction": true});
            skLineSegment(sketch, "E13.2.2.8", {"start": v(-92.9, -60.45) * mm, "end": v(-91.32, -57.72) * mm});
            skLineSegment(sketch, "E13.5.2.8", {"start": v(-91.32, -57.72) * mm, "end": v(-88.17, -57.72) * mm});
            skLineSegment(sketch, "E13.8.2.8", {"start": v(-88.17, -57.72) * mm, "end": v(-86.6, -60.45) * mm});
            skLineSegment(sketch, "E13.11.2.8", {"start": v(-86.6, -60.45) * mm, "end": v(-88.17, -63.18) * mm});
            skLineSegment(sketch, "E13.14.2.8", {"start": v(-88.17, -63.18) * mm, "end": v(-91.32, -63.18) * mm});
            skLineSegment(sketch, "E13.17.2.8", {"start": v(-91.32, -63.18) * mm, "end": v(-92.9, -60.45) * mm});
            skCircle(sketch, "E13.0.2.9", {"center": v(-89.75, -51.82) * mm, "radius": 2.73 * mm, "construction": true});
            skLineSegment(sketch, "E13.2.2.9", {"start": v(-92.9, -51.82) * mm, "end": v(-91.32, -49.09) * mm});
            skLineSegment(sketch, "E13.5.2.9", {"start": v(-91.32, -49.09) * mm, "end": v(-88.17, -49.09) * mm});
            skLineSegment(sketch, "E13.8.2.9", {"start": v(-88.17, -49.09) * mm, "end": v(-86.6, -51.82) * mm});
            skLineSegment(sketch, "E13.11.2.9", {"start": v(-86.6, -51.82) * mm, "end": v(-88.17, -54.55) * mm});
            skLineSegment(sketch, "E13.14.2.9", {"start": v(-88.17, -54.55) * mm, "end": v(-91.32, -54.55) * mm});
            skLineSegment(sketch, "E13.17.2.9", {"start": v(-91.32, -54.55) * mm, "end": v(-92.9, -51.82) * mm});
            skCircle(sketch, "E13.0.2.10", {"center": v(-89.75, -43.18) * mm, "radius": 2.73 * mm, "construction": true});
            skLineSegment(sketch, "E13.2.2.10", {"start": v(-92.9, -43.18) * mm, "end": v(-91.32, -40.45) * mm});
            skLineSegment(sketch, "E13.5.2.10", {"start": v(-91.32, -40.45) * mm, "end": v(-88.17, -40.45) * mm});
            skLineSegment(sketch, "E13.8.2.10", {"start": v(-88.17, -40.45) * mm, "end": v(-86.6, -43.18) * mm});
            skLineSegment(sketch, "E13.11.2.10", {"start": v(-86.6, -43.18) * mm, "end": v(-88.17, -45.91) * mm});
            skLineSegment(sketch, "E13.14.2.10", {"start": v(-88.17, -45.91) * mm, "end": v(-91.32, -45.91) * mm});
            skLineSegment(sketch, "E13.17.2.10", {"start": v(-91.32, -45.91) * mm, "end": v(-92.9, -43.18) * mm});
            skCircle(sketch, "E13.0.2.11", {"center": v(-89.75, -34.54) * mm, "radius": 2.73 * mm, "construction": true});
            skLineSegment(sketch, "E13.2.2.11", {"start": v(-92.9, -34.54) * mm, "end": v(-91.32, -31.81) * mm});
            skLineSegment(sketch, "E13.5.2.11", {"start": v(-91.32, -31.81) * mm, "end": v(-88.17, -31.81) * mm});
            skLineSegment(sketch, "E13.8.2.11", {"start": v(-88.17, -31.81) * mm, "end": v(-86.6, -34.54) * mm});
            skLineSegment(sketch, "E13.11.2.11", {"start": v(-86.6, -34.54) * mm, "end": v(-88.17, -37.27) * mm});
            skLineSegment(sketch, "E13.14.2.11", {"start": v(-88.17, -37.27) * mm, "end": v(-91.32, -37.27) * mm});
            skLineSegment(sketch, "E13.17.2.11", {"start": v(-91.32, -37.27) * mm, "end": v(-92.9, -34.54) * mm});
            skCircle(sketch, "E13.0.2.12", {"center": v(-89.75, -25.9) * mm, "radius": 2.73 * mm, "construction": true});
            skLineSegment(sketch, "E13.2.2.12", {"start": v(-92.9, -25.9) * mm, "end": v(-91.32, -23.18) * mm});
            skLineSegment(sketch, "E13.5.2.12", {"start": v(-91.32, -23.18) * mm, "end": v(-88.17, -23.18) * mm});
            skLineSegment(sketch, "E13.8.2.12", {"start": v(-88.17, -23.18) * mm, "end": v(-86.6, -25.9) * mm});
            skLineSegment(sketch, "E13.11.2.12", {"start": v(-86.6, -25.9) * mm, "end": v(-88.17, -28.64) * mm});
            skLineSegment(sketch, "E13.14.2.12", {"start": v(-88.17, -28.64) * mm, "end": v(-91.32, -28.64) * mm});
            skLineSegment(sketch, "E13.17.2.12", {"start": v(-91.32, -28.64) * mm, "end": v(-92.9, -25.9) * mm});
            skCircle(sketch, "E13.0.2.13", {"center": v(-89.75, -17.27) * mm, "radius": 2.73 * mm, "construction": true});
            skLineSegment(sketch, "E13.2.2.13", {"start": v(-92.9, -17.27) * mm, "end": v(-91.32, -14.54) * mm});
            skLineSegment(sketch, "E13.5.2.13", {"start": v(-91.32, -14.54) * mm, "end": v(-88.17, -14.54) * mm});
            skLineSegment(sketch, "E13.8.2.13", {"start": v(-88.17, -14.54) * mm, "end": v(-86.6, -17.27) * mm});
            skLineSegment(sketch, "E13.11.2.13", {"start": v(-86.6, -17.27) * mm, "end": v(-88.17, -20) * mm});
            skLineSegment(sketch, "E13.14.2.13", {"start": v(-88.17, -20) * mm, "end": v(-91.32, -20) * mm});
            skLineSegment(sketch, "E13.17.2.13", {"start": v(-91.32, -20) * mm, "end": v(-92.9, -17.27) * mm});
            skCircle(sketch, "E13.0.2.14", {"center": v(-89.75, -8.64) * mm, "radius": 2.73 * mm, "construction": true});
            skLineSegment(sketch, "E13.2.2.14", {"start": v(-92.9, -8.64) * mm, "end": v(-91.32, -5.9) * mm});
            skLineSegment(sketch, "E13.5.2.14", {"start": v(-91.32, -5.9) * mm, "end": v(-88.17, -5.9) * mm});
            skLineSegment(sketch, "E13.8.2.14", {"start": v(-88.17, -5.9) * mm, "end": v(-86.6, -8.64) * mm});
            skLineSegment(sketch, "E13.11.2.14", {"start": v(-86.6, -8.64) * mm, "end": v(-88.17, -11.37) * mm});
            skLineSegment(sketch, "E13.14.2.14", {"start": v(-88.17, -11.37) * mm, "end": v(-91.32, -11.37) * mm});
            skLineSegment(sketch, "E13.17.2.14", {"start": v(-91.32, -11.37) * mm, "end": v(-92.9, -8.64) * mm});
            skCircle(sketch, "E13.0.2.15", {"center": v(-89.75, 0) * mm, "radius": 2.73 * mm, "construction": true});
            skLineSegment(sketch, "E13.2.2.15", {"start": v(-92.9, 0) * mm, "end": v(-91.32, 2.73) * mm});
            skLineSegment(sketch, "E13.5.2.15", {"start": v(-91.32, 2.73) * mm, "end": v(-88.17, 2.73) * mm});
            skLineSegment(sketch, "E13.8.2.15", {"start": v(-88.17, 2.73) * mm, "end": v(-86.6, 0) * mm});
            skLineSegment(sketch, "E13.11.2.15", {"start": v(-86.6, 0) * mm, "end": v(-88.17, -2.73) * mm});
            skLineSegment(sketch, "E13.14.2.15", {"start": v(-88.17, -2.73) * mm, "end": v(-91.32, -2.73) * mm});
            skLineSegment(sketch, "E13.17.2.15", {"start": v(-91.32, -2.73) * mm, "end": v(-92.9, 0) * mm});
            skCircle(sketch, "E13.0.2.16", {"center": v(-89.75, 8.64) * mm, "radius": 2.73 * mm, "construction": true});
            skLineSegment(sketch, "E13.2.2.16", {"start": v(-92.9, 8.64) * mm, "end": v(-91.32, 11.37) * mm});
            skLineSegment(sketch, "E13.5.2.16", {"start": v(-91.32, 11.37) * mm, "end": v(-88.17, 11.37) * mm});
            skLineSegment(sketch, "E13.8.2.16", {"start": v(-88.17, 11.37) * mm, "end": v(-86.6, 8.64) * mm});
            skLineSegment(sketch, "E13.11.2.16", {"start": v(-86.6, 8.64) * mm, "end": v(-88.17, 5.9) * mm});
            skLineSegment(sketch, "E13.14.2.16", {"start": v(-88.17, 5.9) * mm, "end": v(-91.32, 5.9) * mm});
            skLineSegment(sketch, "E13.17.2.16", {"start": v(-91.32, 5.9) * mm, "end": v(-92.9, 8.64) * mm});
            skCircle(sketch, "E13.0.2.17", {"center": v(-89.75, 17.27) * mm, "radius": 2.73 * mm, "construction": true});
            skLineSegment(sketch, "E13.2.2.17", {"start": v(-92.9, 17.27) * mm, "end": v(-91.32, 20) * mm});
            skLineSegment(sketch, "E13.5.2.17", {"start": v(-91.32, 20) * mm, "end": v(-88.17, 20) * mm});
            skLineSegment(sketch, "E13.8.2.17", {"start": v(-88.17, 20) * mm, "end": v(-86.6, 17.27) * mm});
            skLineSegment(sketch, "E13.11.2.17", {"start": v(-86.6, 17.27) * mm, "end": v(-88.17, 14.54) * mm});
            skLineSegment(sketch, "E13.14.2.17", {"start": v(-88.17, 14.54) * mm, "end": v(-91.32, 14.54) * mm});
            skLineSegment(sketch, "E13.17.2.17", {"start": v(-91.32, 14.54) * mm, "end": v(-92.9, 17.27) * mm});
            skCircle(sketch, "E13.0.2.18", {"center": v(-89.75, 25.9) * mm, "radius": 2.73 * mm, "construction": true});
            skLineSegment(sketch, "E13.2.2.18", {"start": v(-92.9, 25.9) * mm, "end": v(-91.32, 28.64) * mm});
            skLineSegment(sketch, "E13.5.2.18", {"start": v(-91.32, 28.64) * mm, "end": v(-88.17, 28.64) * mm});
            skLineSegment(sketch, "E13.8.2.18", {"start": v(-88.17, 28.64) * mm, "end": v(-86.6, 25.9) * mm});
            skLineSegment(sketch, "E13.11.2.18", {"start": v(-86.6, 25.9) * mm, "end": v(-88.17, 23.18) * mm});
            skLineSegment(sketch, "E13.14.2.18", {"start": v(-88.17, 23.18) * mm, "end": v(-91.32, 23.18) * mm});
            skLineSegment(sketch, "E13.17.2.18", {"start": v(-91.32, 23.18) * mm, "end": v(-92.9, 25.9) * mm});
            skCircle(sketch, "E13.0.2.19", {"center": v(-89.75, 34.54) * mm, "radius": 2.73 * mm, "construction": true});
            skLineSegment(sketch, "E13.2.2.19", {"start": v(-92.9, 34.54) * mm, "end": v(-91.32, 37.27) * mm});
            skLineSegment(sketch, "E13.5.2.19", {"start": v(-91.32, 37.27) * mm, "end": v(-88.17, 37.27) * mm});
            skLineSegment(sketch, "E13.8.2.19", {"start": v(-88.17, 37.27) * mm, "end": v(-86.6, 34.54) * mm});
            skLineSegment(sketch, "E13.11.2.19", {"start": v(-86.6, 34.54) * mm, "end": v(-88.17, 31.81) * mm});
            skLineSegment(sketch, "E13.14.2.19", {"start": v(-88.17, 31.81) * mm, "end": v(-91.32, 31.81) * mm});
            skLineSegment(sketch, "E13.17.2.19", {"start": v(-91.32, 31.81) * mm, "end": v(-92.9, 34.54) * mm});
            skCircle(sketch, "E13.0.3.8", {"center": v(-74.8, -60.45) * mm, "radius": 2.73 * mm, "construction": true});
            skLineSegment(sketch, "E13.2.3.8", {"start": v(-77.94, -60.45) * mm, "end": v(-76.37, -57.72) * mm});
            skLineSegment(sketch, "E13.5.3.8", {"start": v(-76.37, -57.72) * mm, "end": v(-73.21, -57.72) * mm});
            skLineSegment(sketch, "E13.8.3.8", {"start": v(-73.21, -57.72) * mm, "end": v(-71.64, -60.45) * mm});
            skLineSegment(sketch, "E13.11.3.8", {"start": v(-71.64, -60.45) * mm, "end": v(-73.21, -63.18) * mm});
            skLineSegment(sketch, "E13.14.3.8", {"start": v(-73.21, -63.18) * mm, "end": v(-76.37, -63.18) * mm});
            skLineSegment(sketch, "E13.17.3.8", {"start": v(-76.37, -63.18) * mm, "end": v(-77.94, -60.45) * mm});
            skCircle(sketch, "E13.0.3.9", {"center": v(-74.8, -51.82) * mm, "radius": 2.73 * mm, "construction": true});
            skLineSegment(sketch, "E13.2.3.9", {"start": v(-77.94, -51.82) * mm, "end": v(-76.37, -49.09) * mm});
            skLineSegment(sketch, "E13.5.3.9", {"start": v(-76.37, -49.09) * mm, "end": v(-73.21, -49.09) * mm});
            skLineSegment(sketch, "E13.8.3.9", {"start": v(-73.21, -49.09) * mm, "end": v(-71.64, -51.82) * mm});
            skLineSegment(sketch, "E13.11.3.9", {"start": v(-71.64, -51.82) * mm, "end": v(-73.21, -54.55) * mm});
            skLineSegment(sketch, "E13.14.3.9", {"start": v(-73.21, -54.55) * mm, "end": v(-76.37, -54.55) * mm});
            skLineSegment(sketch, "E13.17.3.9", {"start": v(-76.37, -54.55) * mm, "end": v(-77.94, -51.82) * mm});
            skCircle(sketch, "E13.0.3.10", {"center": v(-74.8, -43.18) * mm, "radius": 2.73 * mm, "construction": true});
            skLineSegment(sketch, "E13.2.3.10", {"start": v(-77.94, -43.18) * mm, "end": v(-76.37, -40.45) * mm});
            skLineSegment(sketch, "E13.5.3.10", {"start": v(-76.37, -40.45) * mm, "end": v(-73.21, -40.45) * mm});
            skLineSegment(sketch, "E13.8.3.10", {"start": v(-73.21, -40.45) * mm, "end": v(-71.64, -43.18) * mm});
            skLineSegment(sketch, "E13.11.3.10", {"start": v(-71.64, -43.18) * mm, "end": v(-73.21, -45.91) * mm});
            skLineSegment(sketch, "E13.14.3.10", {"start": v(-73.21, -45.91) * mm, "end": v(-76.37, -45.91) * mm});
            skLineSegment(sketch, "E13.17.3.10", {"start": v(-76.37, -45.91) * mm, "end": v(-77.94, -43.18) * mm});
            skCircle(sketch, "E13.0.3.11", {"center": v(-74.8, -34.54) * mm, "radius": 2.73 * mm, "construction": true});
            skLineSegment(sketch, "E13.2.3.11", {"start": v(-77.94, -34.54) * mm, "end": v(-76.37, -31.81) * mm});
            skLineSegment(sketch, "E13.5.3.11", {"start": v(-76.37, -31.81) * mm, "end": v(-73.21, -31.81) * mm});
            skLineSegment(sketch, "E13.8.3.11", {"start": v(-73.21, -31.81) * mm, "end": v(-71.64, -34.54) * mm});
            skLineSegment(sketch, "E13.11.3.11", {"start": v(-71.64, -34.54) * mm, "end": v(-73.21, -37.27) * mm});
            skLineSegment(sketch, "E13.14.3.11", {"start": v(-73.21, -37.27) * mm, "end": v(-76.37, -37.27) * mm});
            skLineSegment(sketch, "E13.17.3.11", {"start": v(-76.37, -37.27) * mm, "end": v(-77.94, -34.54) * mm});
            skCircle(sketch, "E13.0.3.12", {"center": v(-74.8, -25.9) * mm, "radius": 2.73 * mm, "construction": true});
            skLineSegment(sketch, "E13.2.3.12", {"start": v(-77.94, -25.9) * mm, "end": v(-76.37, -23.18) * mm});
            skLineSegment(sketch, "E13.5.3.12", {"start": v(-76.37, -23.18) * mm, "end": v(-73.21, -23.18) * mm});
            skLineSegment(sketch, "E13.8.3.12", {"start": v(-73.21, -23.18) * mm, "end": v(-71.64, -25.9) * mm});
            skLineSegment(sketch, "E13.11.3.12", {"start": v(-71.64, -25.9) * mm, "end": v(-73.21, -28.64) * mm});
            skLineSegment(sketch, "E13.14.3.12", {"start": v(-73.21, -28.64) * mm, "end": v(-76.37, -28.64) * mm});
            skLineSegment(sketch, "E13.17.3.12", {"start": v(-76.37, -28.64) * mm, "end": v(-77.94, -25.9) * mm});
            skCircle(sketch, "E13.0.3.13", {"center": v(-74.8, -17.27) * mm, "radius": 2.73 * mm, "construction": true});
            skLineSegment(sketch, "E13.2.3.13", {"start": v(-77.94, -17.27) * mm, "end": v(-76.37, -14.54) * mm});
            skLineSegment(sketch, "E13.5.3.13", {"start": v(-76.37, -14.54) * mm, "end": v(-73.21, -14.54) * mm});
            skLineSegment(sketch, "E13.8.3.13", {"start": v(-73.21, -14.54) * mm, "end": v(-71.64, -17.27) * mm});
            skLineSegment(sketch, "E13.11.3.13", {"start": v(-71.64, -17.27) * mm, "end": v(-73.21, -20) * mm});
            skLineSegment(sketch, "E13.14.3.13", {"start": v(-73.21, -20) * mm, "end": v(-76.37, -20) * mm});
            skLineSegment(sketch, "E13.17.3.13", {"start": v(-76.37, -20) * mm, "end": v(-77.94, -17.27) * mm});
            skCircle(sketch, "E13.0.3.14", {"center": v(-74.8, -8.64) * mm, "radius": 2.73 * mm, "construction": true});
            skLineSegment(sketch, "E13.2.3.14", {"start": v(-77.94, -8.64) * mm, "end": v(-76.37, -5.9) * mm});
            skLineSegment(sketch, "E13.5.3.14", {"start": v(-76.37, -5.9) * mm, "end": v(-73.21, -5.9) * mm});
            skLineSegment(sketch, "E13.8.3.14", {"start": v(-73.21, -5.9) * mm, "end": v(-71.64, -8.64) * mm});
            skLineSegment(sketch, "E13.11.3.14", {"start": v(-71.64, -8.64) * mm, "end": v(-73.21, -11.37) * mm});
            skLineSegment(sketch, "E13.14.3.14", {"start": v(-73.21, -11.37) * mm, "end": v(-76.37, -11.37) * mm});
            skLineSegment(sketch, "E13.17.3.14", {"start": v(-76.37, -11.37) * mm, "end": v(-77.94, -8.64) * mm});
            skCircle(sketch, "E13.0.3.15", {"center": v(-74.8, 0) * mm, "radius": 2.73 * mm, "construction": true});
            skLineSegment(sketch, "E13.2.3.15", {"start": v(-77.94, 0) * mm, "end": v(-76.37, 2.73) * mm});
            skLineSegment(sketch, "E13.5.3.15", {"start": v(-76.37, 2.73) * mm, "end": v(-73.21, 2.73) * mm});
            skLineSegment(sketch, "E13.8.3.15", {"start": v(-73.21, 2.73) * mm, "end": v(-71.64, 0) * mm});
            skLineSegment(sketch, "E13.11.3.15", {"start": v(-71.64, 0) * mm, "end": v(-73.21, -2.73) * mm});
            skLineSegment(sketch, "E13.14.3.15", {"start": v(-73.21, -2.73) * mm, "end": v(-76.37, -2.73) * mm});
            skLineSegment(sketch, "E13.17.3.15", {"start": v(-76.37, -2.73) * mm, "end": v(-77.94, 0) * mm});
            skCircle(sketch, "E13.0.3.16", {"center": v(-74.8, 8.64) * mm, "radius": 2.73 * mm, "construction": true});
            skLineSegment(sketch, "E13.2.3.16", {"start": v(-77.94, 8.64) * mm, "end": v(-76.37, 11.37) * mm});
            skLineSegment(sketch, "E13.5.3.16", {"start": v(-76.37, 11.37) * mm, "end": v(-73.21, 11.37) * mm});
            skLineSegment(sketch, "E13.8.3.16", {"start": v(-73.21, 11.37) * mm, "end": v(-71.64, 8.64) * mm});
            skLineSegment(sketch, "E13.11.3.16", {"start": v(-71.64, 8.64) * mm, "end": v(-73.21, 5.9) * mm});
            skLineSegment(sketch, "E13.14.3.16", {"start": v(-73.21, 5.9) * mm, "end": v(-76.37, 5.9) * mm});
            skLineSegment(sketch, "E13.17.3.16", {"start": v(-76.37, 5.9) * mm, "end": v(-77.94, 8.64) * mm});
            skCircle(sketch, "E13.0.3.17", {"center": v(-74.8, 17.27) * mm, "radius": 2.73 * mm, "construction": true});
            skLineSegment(sketch, "E13.2.3.17", {"start": v(-77.94, 17.27) * mm, "end": v(-76.37, 20) * mm});
            skLineSegment(sketch, "E13.5.3.17", {"start": v(-76.37, 20) * mm, "end": v(-73.21, 20) * mm});
            skLineSegment(sketch, "E13.8.3.17", {"start": v(-73.21, 20) * mm, "end": v(-71.64, 17.27) * mm});
            skLineSegment(sketch, "E13.11.3.17", {"start": v(-71.64, 17.27) * mm, "end": v(-73.21, 14.54) * mm});
            skLineSegment(sketch, "E13.14.3.17", {"start": v(-73.21, 14.54) * mm, "end": v(-76.37, 14.54) * mm});
            skLineSegment(sketch, "E13.17.3.17", {"start": v(-76.37, 14.54) * mm, "end": v(-77.94, 17.27) * mm});
            skCircle(sketch, "E13.0.3.18", {"center": v(-74.8, 25.9) * mm, "radius": 2.73 * mm, "construction": true});
            skLineSegment(sketch, "E13.2.3.18", {"start": v(-77.94, 25.9) * mm, "end": v(-76.37, 28.64) * mm});
            skLineSegment(sketch, "E13.5.3.18", {"start": v(-76.37, 28.64) * mm, "end": v(-73.21, 28.64) * mm});
            skLineSegment(sketch, "E13.8.3.18", {"start": v(-73.21, 28.64) * mm, "end": v(-71.64, 25.9) * mm});
            skLineSegment(sketch, "E13.11.3.18", {"start": v(-71.64, 25.9) * mm, "end": v(-73.21, 23.18) * mm});
            skLineSegment(sketch, "E13.14.3.18", {"start": v(-73.21, 23.18) * mm, "end": v(-76.37, 23.18) * mm});
            skLineSegment(sketch, "E13.17.3.18", {"start": v(-76.37, 23.18) * mm, "end": v(-77.94, 25.9) * mm});
            skCircle(sketch, "E13.0.3.19", {"center": v(-74.8, 34.54) * mm, "radius": 2.73 * mm, "construction": true});
            skLineSegment(sketch, "E13.2.3.19", {"start": v(-77.94, 34.54) * mm, "end": v(-76.37, 37.27) * mm});
            skLineSegment(sketch, "E13.5.3.19", {"start": v(-76.37, 37.27) * mm, "end": v(-73.21, 37.27) * mm});
            skLineSegment(sketch, "E13.8.3.19", {"start": v(-73.21, 37.27) * mm, "end": v(-71.64, 34.54) * mm});
            skLineSegment(sketch, "E13.11.3.19", {"start": v(-71.64, 34.54) * mm, "end": v(-73.21, 31.81) * mm});
            skLineSegment(sketch, "E13.14.3.19", {"start": v(-73.21, 31.81) * mm, "end": v(-76.37, 31.81) * mm});
            skLineSegment(sketch, "E13.17.3.19", {"start": v(-76.37, 31.81) * mm, "end": v(-77.94, 34.54) * mm});
            skCircle(sketch, "E13.0.4.8", {"center": v(-59.83, -60.45) * mm, "radius": 2.73 * mm, "construction": true});
            skLineSegment(sketch, "E13.2.4.8", {"start": v(-62.99, -60.45) * mm, "end": v(-61.4, -57.72) * mm});
            skLineSegment(sketch, "E13.5.4.8", {"start": v(-61.4, -57.72) * mm, "end": v(-58.26, -57.72) * mm});
            skLineSegment(sketch, "E13.8.4.8", {"start": v(-58.26, -57.72) * mm, "end": v(-56.68, -60.45) * mm});
            skLineSegment(sketch, "E13.11.4.8", {"start": v(-56.68, -60.45) * mm, "end": v(-58.26, -63.18) * mm});
            skLineSegment(sketch, "E13.14.4.8", {"start": v(-58.26, -63.18) * mm, "end": v(-61.4, -63.18) * mm});
            skLineSegment(sketch, "E13.17.4.8", {"start": v(-61.4, -63.18) * mm, "end": v(-62.99, -60.45) * mm});
            skCircle(sketch, "E13.0.4.9", {"center": v(-59.83, -51.82) * mm, "radius": 2.73 * mm, "construction": true});
            skLineSegment(sketch, "E13.2.4.9", {"start": v(-62.99, -51.82) * mm, "end": v(-61.4, -49.09) * mm});
            skLineSegment(sketch, "E13.5.4.9", {"start": v(-61.4, -49.09) * mm, "end": v(-58.26, -49.09) * mm});
            skLineSegment(sketch, "E13.8.4.9", {"start": v(-58.26, -49.09) * mm, "end": v(-56.68, -51.82) * mm});
            skLineSegment(sketch, "E13.11.4.9", {"start": v(-56.68, -51.82) * mm, "end": v(-58.26, -54.55) * mm});
            skLineSegment(sketch, "E13.14.4.9", {"start": v(-58.26, -54.55) * mm, "end": v(-61.4, -54.55) * mm});
            skLineSegment(sketch, "E13.17.4.9", {"start": v(-61.4, -54.55) * mm, "end": v(-62.99, -51.82) * mm});
            skCircle(sketch, "E13.0.4.10", {"center": v(-59.83, -43.18) * mm, "radius": 2.73 * mm, "construction": true});
            skLineSegment(sketch, "E13.2.4.10", {"start": v(-62.99, -43.18) * mm, "end": v(-61.4, -40.45) * mm});
            skLineSegment(sketch, "E13.5.4.10", {"start": v(-61.4, -40.45) * mm, "end": v(-58.26, -40.45) * mm});
            skLineSegment(sketch, "E13.8.4.10", {"start": v(-58.26, -40.45) * mm, "end": v(-56.68, -43.18) * mm});
            skLineSegment(sketch, "E13.11.4.10", {"start": v(-56.68, -43.18) * mm, "end": v(-58.26, -45.91) * mm});
            skLineSegment(sketch, "E13.14.4.10", {"start": v(-58.26, -45.91) * mm, "end": v(-61.4, -45.91) * mm});
            skLineSegment(sketch, "E13.17.4.10", {"start": v(-61.4, -45.91) * mm, "end": v(-62.99, -43.18) * mm});
            skCircle(sketch, "E13.0.4.11", {"center": v(-59.83, -34.54) * mm, "radius": 2.73 * mm, "construction": true});
            skLineSegment(sketch, "E13.2.4.11", {"start": v(-62.99, -34.54) * mm, "end": v(-61.4, -31.81) * mm});
            skLineSegment(sketch, "E13.5.4.11", {"start": v(-61.4, -31.81) * mm, "end": v(-58.26, -31.81) * mm});
            skLineSegment(sketch, "E13.8.4.11", {"start": v(-58.26, -31.81) * mm, "end": v(-56.68, -34.54) * mm});
            skLineSegment(sketch, "E13.11.4.11", {"start": v(-56.68, -34.54) * mm, "end": v(-58.26, -37.27) * mm});
            skLineSegment(sketch, "E13.14.4.11", {"start": v(-58.26, -37.27) * mm, "end": v(-61.4, -37.27) * mm});
            skLineSegment(sketch, "E13.17.4.11", {"start": v(-61.4, -37.27) * mm, "end": v(-62.99, -34.54) * mm});
            skCircle(sketch, "E13.0.4.12", {"center": v(-59.83, -25.9) * mm, "radius": 2.73 * mm, "construction": true});
            skLineSegment(sketch, "E13.2.4.12", {"start": v(-62.99, -25.9) * mm, "end": v(-61.4, -23.18) * mm});
            skLineSegment(sketch, "E13.5.4.12", {"start": v(-61.4, -23.18) * mm, "end": v(-58.26, -23.18) * mm});
            skLineSegment(sketch, "E13.8.4.12", {"start": v(-58.26, -23.18) * mm, "end": v(-56.68, -25.9) * mm});
            skLineSegment(sketch, "E13.11.4.12", {"start": v(-56.68, -25.9) * mm, "end": v(-58.26, -28.64) * mm});
            skLineSegment(sketch, "E13.14.4.12", {"start": v(-58.26, -28.64) * mm, "end": v(-61.4, -28.64) * mm});
            skLineSegment(sketch, "E13.17.4.12", {"start": v(-61.4, -28.64) * mm, "end": v(-62.99, -25.9) * mm});
            skCircle(sketch, "E13.0.4.13", {"center": v(-59.83, -17.27) * mm, "radius": 2.73 * mm, "construction": true});
            skLineSegment(sketch, "E13.2.4.13", {"start": v(-62.99, -17.27) * mm, "end": v(-61.4, -14.54) * mm});
            skLineSegment(sketch, "E13.5.4.13", {"start": v(-61.4, -14.54) * mm, "end": v(-58.26, -14.54) * mm});
            skLineSegment(sketch, "E13.8.4.13", {"start": v(-58.26, -14.54) * mm, "end": v(-56.68, -17.27) * mm});
            skLineSegment(sketch, "E13.11.4.13", {"start": v(-56.68, -17.27) * mm, "end": v(-58.26, -20) * mm});
            skLineSegment(sketch, "E13.14.4.13", {"start": v(-58.26, -20) * mm, "end": v(-61.4, -20) * mm});
            skLineSegment(sketch, "E13.17.4.13", {"start": v(-61.4, -20) * mm, "end": v(-62.99, -17.27) * mm});
            skCircle(sketch, "E13.0.4.14", {"center": v(-59.83, -8.64) * mm, "radius": 2.73 * mm, "construction": true});
            skLineSegment(sketch, "E13.2.4.14", {"start": v(-62.99, -8.64) * mm, "end": v(-61.4, -5.9) * mm});
            skLineSegment(sketch, "E13.5.4.14", {"start": v(-61.4, -5.9) * mm, "end": v(-58.26, -5.9) * mm});
            skLineSegment(sketch, "E13.8.4.14", {"start": v(-58.26, -5.9) * mm, "end": v(-56.68, -8.64) * mm});
            skLineSegment(sketch, "E13.11.4.14", {"start": v(-56.68, -8.64) * mm, "end": v(-58.26, -11.37) * mm});
            skLineSegment(sketch, "E13.14.4.14", {"start": v(-58.26, -11.37) * mm, "end": v(-61.4, -11.37) * mm});
            skLineSegment(sketch, "E13.17.4.14", {"start": v(-61.4, -11.37) * mm, "end": v(-62.99, -8.64) * mm});
            skCircle(sketch, "E13.0.4.15", {"center": v(-59.83, 0) * mm, "radius": 2.73 * mm, "construction": true});
            skLineSegment(sketch, "E13.2.4.15", {"start": v(-62.99, 0) * mm, "end": v(-61.4, 2.73) * mm});
            skLineSegment(sketch, "E13.5.4.15", {"start": v(-61.4, 2.73) * mm, "end": v(-58.26, 2.73) * mm});
            skLineSegment(sketch, "E13.8.4.15", {"start": v(-58.26, 2.73) * mm, "end": v(-56.68, 0) * mm});
            skLineSegment(sketch, "E13.11.4.15", {"start": v(-56.68, 0) * mm, "end": v(-58.26, -2.73) * mm});
            skLineSegment(sketch, "E13.14.4.15", {"start": v(-58.26, -2.73) * mm, "end": v(-61.4, -2.73) * mm});
            skLineSegment(sketch, "E13.17.4.15", {"start": v(-61.4, -2.73) * mm, "end": v(-62.99, 0) * mm});
            skCircle(sketch, "E13.0.4.16", {"center": v(-59.83, 8.64) * mm, "radius": 2.73 * mm, "construction": true});
            skLineSegment(sketch, "E13.2.4.16", {"start": v(-62.99, 8.64) * mm, "end": v(-61.4, 11.37) * mm});
            skLineSegment(sketch, "E13.5.4.16", {"start": v(-61.4, 11.37) * mm, "end": v(-58.26, 11.37) * mm});
            skLineSegment(sketch, "E13.8.4.16", {"start": v(-58.26, 11.37) * mm, "end": v(-56.68, 8.64) * mm});
            skLineSegment(sketch, "E13.11.4.16", {"start": v(-56.68, 8.64) * mm, "end": v(-58.26, 5.9) * mm});
            skLineSegment(sketch, "E13.14.4.16", {"start": v(-58.26, 5.9) * mm, "end": v(-61.4, 5.9) * mm});
            skLineSegment(sketch, "E13.17.4.16", {"start": v(-61.4, 5.9) * mm, "end": v(-62.99, 8.64) * mm});
            skCircle(sketch, "E13.0.4.17", {"center": v(-59.83, 17.27) * mm, "radius": 2.73 * mm, "construction": true});
            skLineSegment(sketch, "E13.2.4.17", {"start": v(-62.99, 17.27) * mm, "end": v(-61.4, 20) * mm});
            skLineSegment(sketch, "E13.5.4.17", {"start": v(-61.4, 20) * mm, "end": v(-58.26, 20) * mm});
            skLineSegment(sketch, "E13.8.4.17", {"start": v(-58.26, 20) * mm, "end": v(-56.68, 17.27) * mm});
            skLineSegment(sketch, "E13.11.4.17", {"start": v(-56.68, 17.27) * mm, "end": v(-58.26, 14.54) * mm});
            skLineSegment(sketch, "E13.14.4.17", {"start": v(-58.26, 14.54) * mm, "end": v(-61.4, 14.54) * mm});
            skLineSegment(sketch, "E13.17.4.17", {"start": v(-61.4, 14.54) * mm, "end": v(-62.99, 17.27) * mm});
            skCircle(sketch, "E13.0.4.18", {"center": v(-59.83, 25.9) * mm, "radius": 2.73 * mm, "construction": true});
            skLineSegment(sketch, "E13.2.4.18", {"start": v(-62.99, 25.9) * mm, "end": v(-61.4, 28.64) * mm});
            skLineSegment(sketch, "E13.5.4.18", {"start": v(-61.4, 28.64) * mm, "end": v(-58.26, 28.64) * mm});
            skLineSegment(sketch, "E13.8.4.18", {"start": v(-58.26, 28.64) * mm, "end": v(-56.68, 25.9) * mm});
            skLineSegment(sketch, "E13.11.4.18", {"start": v(-56.68, 25.9) * mm, "end": v(-58.26, 23.18) * mm});
            skLineSegment(sketch, "E13.14.4.18", {"start": v(-58.26, 23.18) * mm, "end": v(-61.4, 23.18) * mm});
            skLineSegment(sketch, "E13.17.4.18", {"start": v(-61.4, 23.18) * mm, "end": v(-62.99, 25.9) * mm});
            skCircle(sketch, "E13.0.4.19", {"center": v(-59.83, 34.54) * mm, "radius": 2.73 * mm, "construction": true});
            skLineSegment(sketch, "E13.2.4.19", {"start": v(-62.99, 34.54) * mm, "end": v(-61.4, 37.27) * mm});
            skLineSegment(sketch, "E13.5.4.19", {"start": v(-61.4, 37.27) * mm, "end": v(-58.26, 37.27) * mm});
            skLineSegment(sketch, "E13.8.4.19", {"start": v(-58.26, 37.27) * mm, "end": v(-56.68, 34.54) * mm});
            skLineSegment(sketch, "E13.11.4.19", {"start": v(-56.68, 34.54) * mm, "end": v(-58.26, 31.81) * mm});
            skLineSegment(sketch, "E13.14.4.19", {"start": v(-58.26, 31.81) * mm, "end": v(-61.4, 31.81) * mm});
            skLineSegment(sketch, "E13.17.4.19", {"start": v(-61.4, 31.81) * mm, "end": v(-62.99, 34.54) * mm});
            skLineSegment(sketch, "E14.0.6.0", {"start": v(-38.97, -131.13) * mm, "end": v(-35.82, -131.13) * mm});
            skLineSegment(sketch, "E14.3.6.0", {"start": v(-35.82, -131.13) * mm, "end": v(-34.24, -133.86) * mm});
            skLineSegment(sketch, "E14.6.6.0", {"start": v(-34.24, -133.86) * mm, "end": v(-35.82, -136.59) * mm});
            skCircle(sketch, "E14.9.6.0", {"center": v(-37.4, -133.86) * mm, "radius": 2.73 * mm, "construction": true});
            skLineSegment(sketch, "E14.11.6.0", {"start": v(-35.82, -136.59) * mm, "end": v(-38.97, -136.59) * mm});
            skLineSegment(sketch, "E14.14.6.0", {"start": v(-38.97, -136.59) * mm, "end": v(-40.55, -133.86) * mm});
            skLineSegment(sketch, "E14.17.6.0", {"start": v(-40.55, -133.86) * mm, "end": v(-38.97, -131.13) * mm});
            skLineSegment(sketch, "E14.0.6.1", {"start": v(-38.97, -122.5) * mm, "end": v(-35.82, -122.5) * mm});
            skLineSegment(sketch, "E14.3.6.1", {"start": v(-35.82, -122.5) * mm, "end": v(-34.24, -125.22) * mm});
            skLineSegment(sketch, "E14.6.6.1", {"start": v(-34.24, -125.22) * mm, "end": v(-35.82, -127.95) * mm});
            skCircle(sketch, "E14.9.6.1", {"center": v(-37.4, -125.22) * mm, "radius": 2.73 * mm, "construction": true});
            skLineSegment(sketch, "E14.11.6.1", {"start": v(-35.82, -127.95) * mm, "end": v(-38.97, -127.95) * mm});
            skLineSegment(sketch, "E14.14.6.1", {"start": v(-38.97, -127.95) * mm, "end": v(-40.55, -125.22) * mm});
            skLineSegment(sketch, "E14.17.6.1", {"start": v(-40.55, -125.22) * mm, "end": v(-38.97, -122.5) * mm});
            skLineSegment(sketch, "E14.0.6.2", {"start": v(-38.97, -113.86) * mm, "end": v(-35.82, -113.86) * mm});
            skLineSegment(sketch, "E14.3.6.2", {"start": v(-35.82, -113.86) * mm, "end": v(-34.24, -116.59) * mm});
            skLineSegment(sketch, "E14.6.6.2", {"start": v(-34.24, -116.59) * mm, "end": v(-35.82, -119.32) * mm});
            skCircle(sketch, "E14.9.6.2", {"center": v(-37.4, -116.59) * mm, "radius": 2.73 * mm, "construction": true});
            skLineSegment(sketch, "E14.11.6.2", {"start": v(-35.82, -119.32) * mm, "end": v(-38.97, -119.32) * mm});
            skLineSegment(sketch, "E14.14.6.2", {"start": v(-38.97, -119.32) * mm, "end": v(-40.55, -116.59) * mm});
            skLineSegment(sketch, "E14.17.6.2", {"start": v(-40.55, -116.59) * mm, "end": v(-38.97, -113.86) * mm});
            skLineSegment(sketch, "E14.0.6.3", {"start": v(-38.97, -105.22) * mm, "end": v(-35.82, -105.22) * mm});
            skLineSegment(sketch, "E14.3.6.3", {"start": v(-35.82, -105.22) * mm, "end": v(-34.24, -107.95) * mm});
            skLineSegment(sketch, "E14.6.6.3", {"start": v(-34.24, -107.95) * mm, "end": v(-35.82, -110.68) * mm});
            skCircle(sketch, "E14.9.6.3", {"center": v(-37.4, -107.95) * mm, "radius": 2.73 * mm, "construction": true});
            skLineSegment(sketch, "E14.11.6.3", {"start": v(-35.82, -110.68) * mm, "end": v(-38.97, -110.68) * mm});
            skLineSegment(sketch, "E14.14.6.3", {"start": v(-38.97, -110.68) * mm, "end": v(-40.55, -107.95) * mm});
            skLineSegment(sketch, "E14.17.6.3", {"start": v(-40.55, -107.95) * mm, "end": v(-38.97, -105.22) * mm});
            skLineSegment(sketch, "E14.0.6.4", {"start": v(-38.97, -96.58) * mm, "end": v(-35.82, -96.58) * mm});
            skLineSegment(sketch, "E14.3.6.4", {"start": v(-35.82, -96.58) * mm, "end": v(-34.24, -99.31) * mm});
            skLineSegment(sketch, "E14.6.6.4", {"start": v(-34.24, -99.31) * mm, "end": v(-35.82, -102.04) * mm});
            skCircle(sketch, "E14.9.6.4", {"center": v(-37.4, -99.31) * mm, "radius": 2.73 * mm, "construction": true});
            skLineSegment(sketch, "E14.11.6.4", {"start": v(-35.82, -102.04) * mm, "end": v(-38.97, -102.04) * mm});
            skLineSegment(sketch, "E14.14.6.4", {"start": v(-38.97, -102.04) * mm, "end": v(-40.55, -99.31) * mm});
            skLineSegment(sketch, "E14.17.6.4", {"start": v(-40.55, -99.31) * mm, "end": v(-38.97, -96.58) * mm});
            skLineSegment(sketch, "E14.0.6.5", {"start": v(-38.97, -87.95) * mm, "end": v(-35.82, -87.95) * mm});
            skLineSegment(sketch, "E14.3.6.5", {"start": v(-35.82, -87.95) * mm, "end": v(-34.24, -90.68) * mm});
            skLineSegment(sketch, "E14.6.6.5", {"start": v(-34.24, -90.68) * mm, "end": v(-35.82, -93.4) * mm});
            skCircle(sketch, "E14.9.6.5", {"center": v(-37.4, -90.68) * mm, "radius": 2.73 * mm, "construction": true});
            skLineSegment(sketch, "E14.11.6.5", {"start": v(-35.82, -93.4) * mm, "end": v(-38.97, -93.4) * mm});
            skLineSegment(sketch, "E14.14.6.5", {"start": v(-38.97, -93.4) * mm, "end": v(-40.55, -90.68) * mm});
            skLineSegment(sketch, "E14.17.6.5", {"start": v(-40.55, -90.68) * mm, "end": v(-38.97, -87.95) * mm});
            skLineSegment(sketch, "E14.0.6.6", {"start": v(-38.97, -79.31) * mm, "end": v(-35.82, -79.31) * mm});
            skLineSegment(sketch, "E14.3.6.6", {"start": v(-35.82, -79.31) * mm, "end": v(-34.24, -82.04) * mm});
            skLineSegment(sketch, "E14.6.6.6", {"start": v(-34.24, -82.04) * mm, "end": v(-35.82, -84.77) * mm});
            skCircle(sketch, "E14.9.6.6", {"center": v(-37.4, -82.04) * mm, "radius": 2.73 * mm, "construction": true});
            skLineSegment(sketch, "E14.11.6.6", {"start": v(-35.82, -84.77) * mm, "end": v(-38.97, -84.77) * mm});
            skLineSegment(sketch, "E14.14.6.6", {"start": v(-38.97, -84.77) * mm, "end": v(-40.55, -82.04) * mm});
            skLineSegment(sketch, "E14.17.6.6", {"start": v(-40.55, -82.04) * mm, "end": v(-38.97, -79.31) * mm});
            skLineSegment(sketch, "E14.0.6.7", {"start": v(-38.97, -70.68) * mm, "end": v(-35.82, -70.68) * mm});
            skLineSegment(sketch, "E14.3.6.7", {"start": v(-35.82, -70.68) * mm, "end": v(-34.24, -73.4) * mm});
            skLineSegment(sketch, "E14.6.6.7", {"start": v(-34.24, -73.4) * mm, "end": v(-35.82, -76.14) * mm});
            skCircle(sketch, "E14.9.6.7", {"center": v(-37.4, -73.4) * mm, "radius": 2.73 * mm, "construction": true});
            skLineSegment(sketch, "E14.11.6.7", {"start": v(-35.82, -76.14) * mm, "end": v(-38.97, -76.14) * mm});
            skLineSegment(sketch, "E14.14.6.7", {"start": v(-38.97, -76.14) * mm, "end": v(-40.55, -73.4) * mm});
            skLineSegment(sketch, "E14.17.6.7", {"start": v(-40.55, -73.4) * mm, "end": v(-38.97, -70.68) * mm});
            skLineSegment(sketch, "E14.0.6.8", {"start": v(-38.97, -62.04) * mm, "end": v(-35.82, -62.04) * mm});
            skLineSegment(sketch, "E14.3.6.8", {"start": v(-35.82, -62.04) * mm, "end": v(-34.24, -64.77) * mm});
            skLineSegment(sketch, "E14.6.6.8", {"start": v(-34.24, -64.77) * mm, "end": v(-35.82, -67.5) * mm});
            skCircle(sketch, "E14.9.6.8", {"center": v(-37.4, -64.77) * mm, "radius": 2.73 * mm, "construction": true});
            skLineSegment(sketch, "E14.11.6.8", {"start": v(-35.82, -67.5) * mm, "end": v(-38.97, -67.5) * mm});
            skLineSegment(sketch, "E14.14.6.8", {"start": v(-38.97, -67.5) * mm, "end": v(-40.55, -64.77) * mm});
            skLineSegment(sketch, "E14.17.6.8", {"start": v(-40.55, -64.77) * mm, "end": v(-38.97, -62.04) * mm});
            skLineSegment(sketch, "E14.0.6.9", {"start": v(-38.97, -53.4) * mm, "end": v(-35.82, -53.4) * mm});
            skLineSegment(sketch, "E14.3.6.9", {"start": v(-35.82, -53.4) * mm, "end": v(-34.24, -56.13) * mm});
            skLineSegment(sketch, "E14.6.6.9", {"start": v(-34.24, -56.13) * mm, "end": v(-35.82, -58.86) * mm});
            skCircle(sketch, "E14.9.6.9", {"center": v(-37.4, -56.13) * mm, "radius": 2.73 * mm, "construction": true});
            skLineSegment(sketch, "E14.11.6.9", {"start": v(-35.82, -58.86) * mm, "end": v(-38.97, -58.86) * mm});
            skLineSegment(sketch, "E14.14.6.9", {"start": v(-38.97, -58.86) * mm, "end": v(-40.55, -56.13) * mm});
            skLineSegment(sketch, "E14.17.6.9", {"start": v(-40.55, -56.13) * mm, "end": v(-38.97, -53.4) * mm});
            skLineSegment(sketch, "E14.0.6.10", {"start": v(-38.97, -44.77) * mm, "end": v(-35.82, -44.77) * mm});
            skLineSegment(sketch, "E14.3.6.10", {"start": v(-35.82, -44.77) * mm, "end": v(-34.24, -47.5) * mm});
            skLineSegment(sketch, "E14.6.6.10", {"start": v(-34.24, -47.5) * mm, "end": v(-35.82, -50.23) * mm});
            skCircle(sketch, "E14.9.6.10", {"center": v(-37.4, -47.5) * mm, "radius": 2.73 * mm, "construction": true});
            skLineSegment(sketch, "E14.11.6.10", {"start": v(-35.82, -50.23) * mm, "end": v(-38.97, -50.23) * mm});
            skLineSegment(sketch, "E14.14.6.10", {"start": v(-38.97, -50.23) * mm, "end": v(-40.55, -47.5) * mm});
            skLineSegment(sketch, "E14.17.6.10", {"start": v(-40.55, -47.5) * mm, "end": v(-38.97, -44.77) * mm});
            skLineSegment(sketch, "E14.0.6.11", {"start": v(-38.97, -36.13) * mm, "end": v(-35.82, -36.13) * mm});
            skLineSegment(sketch, "E14.3.6.11", {"start": v(-35.82, -36.13) * mm, "end": v(-34.24, -38.86) * mm});
            skLineSegment(sketch, "E14.6.6.11", {"start": v(-34.24, -38.86) * mm, "end": v(-35.82, -41.6) * mm});
            skCircle(sketch, "E14.9.6.11", {"center": v(-37.4, -38.86) * mm, "radius": 2.73 * mm, "construction": true});
            skLineSegment(sketch, "E14.11.6.11", {"start": v(-35.82, -41.6) * mm, "end": v(-38.97, -41.6) * mm});
            skLineSegment(sketch, "E14.14.6.11", {"start": v(-38.97, -41.6) * mm, "end": v(-40.55, -38.86) * mm});
            skLineSegment(sketch, "E14.17.6.11", {"start": v(-40.55, -38.86) * mm, "end": v(-38.97, -36.13) * mm});
            skLineSegment(sketch, "E14.0.6.12", {"start": v(-38.97, -27.5) * mm, "end": v(-35.82, -27.5) * mm});
            skLineSegment(sketch, "E14.3.6.12", {"start": v(-35.82, -27.5) * mm, "end": v(-34.24, -30.23) * mm});
            skLineSegment(sketch, "E14.6.6.12", {"start": v(-34.24, -30.23) * mm, "end": v(-35.82, -32.96) * mm});
            skCircle(sketch, "E14.9.6.12", {"center": v(-37.4, -30.23) * mm, "radius": 2.73 * mm, "construction": true});
            skLineSegment(sketch, "E14.11.6.12", {"start": v(-35.82, -32.96) * mm, "end": v(-38.97, -32.96) * mm});
            skLineSegment(sketch, "E14.14.6.12", {"start": v(-38.97, -32.96) * mm, "end": v(-40.55, -30.23) * mm});
            skLineSegment(sketch, "E14.17.6.12", {"start": v(-40.55, -30.23) * mm, "end": v(-38.97, -27.5) * mm});
            skLineSegment(sketch, "E14.0.6.13", {"start": v(-38.97, -18.86) * mm, "end": v(-35.82, -18.86) * mm});
            skLineSegment(sketch, "E14.3.6.13", {"start": v(-35.82, -18.86) * mm, "end": v(-34.24, -21.6) * mm});
            skLineSegment(sketch, "E14.6.6.13", {"start": v(-34.24, -21.6) * mm, "end": v(-35.82, -24.32) * mm});
            skCircle(sketch, "E14.9.6.13", {"center": v(-37.4, -21.6) * mm, "radius": 2.73 * mm, "construction": true});
            skLineSegment(sketch, "E14.11.6.13", {"start": v(-35.82, -24.32) * mm, "end": v(-38.97, -24.32) * mm});
            skLineSegment(sketch, "E14.14.6.13", {"start": v(-38.97, -24.32) * mm, "end": v(-40.55, -21.6) * mm});
            skLineSegment(sketch, "E14.17.6.13", {"start": v(-40.55, -21.59) * mm, "end": v(-38.97, -18.86) * mm});
            skLineSegment(sketch, "E14.0.6.14", {"start": v(-38.97, -10.22) * mm, "end": v(-35.82, -10.22) * mm});
            skLineSegment(sketch, "E14.3.6.14", {"start": v(-35.82, -10.22) * mm, "end": v(-34.24, -12.95) * mm});
            skLineSegment(sketch, "E14.6.6.14", {"start": v(-34.24, -12.95) * mm, "end": v(-35.82, -15.68) * mm});
            skCircle(sketch, "E14.9.6.14", {"center": v(-37.4, -12.95) * mm, "radius": 2.73 * mm, "construction": true});
            skLineSegment(sketch, "E14.11.6.14", {"start": v(-35.82, -15.68) * mm, "end": v(-38.97, -15.68) * mm});
            skLineSegment(sketch, "E14.14.6.14", {"start": v(-38.97, -15.68) * mm, "end": v(-40.55, -12.95) * mm});
            skLineSegment(sketch, "E14.17.6.14", {"start": v(-40.55, -12.95) * mm, "end": v(-38.97, -10.22) * mm});
            skLineSegment(sketch, "E14.0.6.15", {"start": v(-38.97, -1.59) * mm, "end": v(-35.82, -1.59) * mm});
            skLineSegment(sketch, "E14.3.6.15", {"start": v(-35.82, -1.59) * mm, "end": v(-34.24, -4.32) * mm});
            skLineSegment(sketch, "E14.6.6.15", {"start": v(-34.24, -4.32) * mm, "end": v(-35.82, -7.05) * mm});
            skCircle(sketch, "E14.9.6.15", {"center": v(-37.4, -4.32) * mm, "radius": 2.73 * mm, "construction": true});
            skLineSegment(sketch, "E14.11.6.15", {"start": v(-35.82, -7.05) * mm, "end": v(-38.97, -7.05) * mm});
            skLineSegment(sketch, "E14.14.6.15", {"start": v(-38.97, -7.05) * mm, "end": v(-40.55, -4.32) * mm});
            skLineSegment(sketch, "E14.17.6.15", {"start": v(-40.55, -4.32) * mm, "end": v(-38.97, -1.59) * mm});
            skLineSegment(sketch, "E14.0.6.16", {"start": v(-38.97, 7.05) * mm, "end": v(-35.82, 7.05) * mm});
            skLineSegment(sketch, "E14.3.6.16", {"start": v(-35.82, 7.05) * mm, "end": v(-34.24, 4.32) * mm});
            skLineSegment(sketch, "E14.6.6.16", {"start": v(-34.24, 4.32) * mm, "end": v(-35.82, 1.59) * mm});
            skCircle(sketch, "E14.9.6.16", {"center": v(-37.4, 4.32) * mm, "radius": 2.73 * mm, "construction": true});
            skLineSegment(sketch, "E14.11.6.16", {"start": v(-35.82, 1.59) * mm, "end": v(-38.97, 1.59) * mm});
            skLineSegment(sketch, "E14.14.6.16", {"start": v(-38.97, 1.59) * mm, "end": v(-40.55, 4.32) * mm});
            skLineSegment(sketch, "E14.17.6.16", {"start": v(-40.55, 4.32) * mm, "end": v(-38.97, 7.05) * mm});
            skLineSegment(sketch, "E14.0.6.17", {"start": v(-38.97, 15.68) * mm, "end": v(-35.82, 15.68) * mm});
            skLineSegment(sketch, "E14.3.6.17", {"start": v(-35.82, 15.68) * mm, "end": v(-34.24, 12.95) * mm});
            skLineSegment(sketch, "E14.6.6.17", {"start": v(-34.24, 12.95) * mm, "end": v(-35.82, 10.22) * mm});
            skCircle(sketch, "E14.9.6.17", {"center": v(-37.4, 12.95) * mm, "radius": 2.73 * mm, "construction": true});
            skLineSegment(sketch, "E14.11.6.17", {"start": v(-35.82, 10.22) * mm, "end": v(-38.97, 10.22) * mm});
            skLineSegment(sketch, "E14.14.6.17", {"start": v(-38.97, 10.22) * mm, "end": v(-40.55, 12.95) * mm});
            skLineSegment(sketch, "E14.17.6.17", {"start": v(-40.55, 12.95) * mm, "end": v(-38.97, 15.68) * mm});
            skLineSegment(sketch, "E14.0.6.18", {"start": v(-38.97, 24.32) * mm, "end": v(-35.82, 24.32) * mm});
            skLineSegment(sketch, "E14.3.6.18", {"start": v(-35.82, 24.32) * mm, "end": v(-34.24, 21.59) * mm});
            skLineSegment(sketch, "E14.6.6.18", {"start": v(-34.24, 21.59) * mm, "end": v(-35.82, 18.86) * mm});
            skCircle(sketch, "E14.9.6.18", {"center": v(-37.4, 21.59) * mm, "radius": 2.73 * mm, "construction": true});
            skLineSegment(sketch, "E14.11.6.18", {"start": v(-35.82, 18.86) * mm, "end": v(-38.97, 18.86) * mm});
            skLineSegment(sketch, "E14.14.6.18", {"start": v(-38.97, 18.86) * mm, "end": v(-40.55, 21.59) * mm});
            skLineSegment(sketch, "E14.17.6.18", {"start": v(-40.55, 21.6) * mm, "end": v(-38.97, 24.32) * mm});
            skLineSegment(sketch, "E14.0.6.19", {"start": v(-38.97, 32.96) * mm, "end": v(-35.82, 32.96) * mm});
            skLineSegment(sketch, "E14.3.6.19", {"start": v(-35.82, 32.96) * mm, "end": v(-34.24, 30.23) * mm});
            skLineSegment(sketch, "E14.6.6.19", {"start": v(-34.24, 30.23) * mm, "end": v(-35.82, 27.5) * mm});
            skCircle(sketch, "E14.9.6.19", {"center": v(-37.4, 30.23) * mm, "radius": 2.73 * mm, "construction": true});
            skLineSegment(sketch, "E14.11.6.19", {"start": v(-35.82, 27.5) * mm, "end": v(-38.97, 27.5) * mm});
            skLineSegment(sketch, "E14.14.6.19", {"start": v(-38.97, 27.5) * mm, "end": v(-40.55, 30.23) * mm});
            skLineSegment(sketch, "E14.17.6.19", {"start": v(-40.55, 30.23) * mm, "end": v(-38.97, 32.96) * mm});
            skLineSegment(sketch, "E14.0.7.0", {"start": v(-24.01, -131.13) * mm, "end": v(-20.86, -131.13) * mm});
            skLineSegment(sketch, "E14.3.7.0", {"start": v(-20.86, -131.13) * mm, "end": v(-19.28, -133.86) * mm});
            skLineSegment(sketch, "E14.6.7.0", {"start": v(-19.28, -133.86) * mm, "end": v(-20.86, -136.59) * mm});
            skCircle(sketch, "E14.9.7.0", {"center": v(-22.44, -133.86) * mm, "radius": 2.73 * mm, "construction": true});
            skLineSegment(sketch, "E14.11.7.0", {"start": v(-20.86, -136.59) * mm, "end": v(-24.01, -136.59) * mm});
            skLineSegment(sketch, "E14.14.7.0", {"start": v(-24.01, -136.59) * mm, "end": v(-25.59, -133.86) * mm});
            skLineSegment(sketch, "E14.17.7.0", {"start": v(-25.59, -133.86) * mm, "end": v(-24.01, -131.13) * mm});
            skLineSegment(sketch, "E14.0.7.1", {"start": v(-24.01, -122.5) * mm, "end": v(-20.86, -122.5) * mm});
            skLineSegment(sketch, "E14.3.7.1", {"start": v(-20.86, -122.5) * mm, "end": v(-19.28, -125.22) * mm});
            skLineSegment(sketch, "E14.6.7.1", {"start": v(-19.28, -125.22) * mm, "end": v(-20.86, -127.95) * mm});
            skCircle(sketch, "E14.9.7.1", {"center": v(-22.44, -125.22) * mm, "radius": 2.73 * mm, "construction": true});
            skLineSegment(sketch, "E14.11.7.1", {"start": v(-20.86, -127.95) * mm, "end": v(-24.01, -127.95) * mm});
            skLineSegment(sketch, "E14.14.7.1", {"start": v(-24.01, -127.95) * mm, "end": v(-25.59, -125.22) * mm});
            skLineSegment(sketch, "E14.17.7.1", {"start": v(-25.59, -125.22) * mm, "end": v(-24.01, -122.5) * mm});
            skLineSegment(sketch, "E14.0.7.2", {"start": v(-24.01, -113.86) * mm, "end": v(-20.86, -113.86) * mm});
            skLineSegment(sketch, "E14.3.7.2", {"start": v(-20.86, -113.86) * mm, "end": v(-19.28, -116.59) * mm});
            skLineSegment(sketch, "E14.6.7.2", {"start": v(-19.28, -116.59) * mm, "end": v(-20.86, -119.32) * mm});
            skCircle(sketch, "E14.9.7.2", {"center": v(-22.44, -116.59) * mm, "radius": 2.73 * mm, "construction": true});
            skLineSegment(sketch, "E14.11.7.2", {"start": v(-20.86, -119.32) * mm, "end": v(-24.01, -119.32) * mm});
            skLineSegment(sketch, "E14.14.7.2", {"start": v(-24.01, -119.32) * mm, "end": v(-25.59, -116.59) * mm});
            skLineSegment(sketch, "E14.17.7.2", {"start": v(-25.59, -116.59) * mm, "end": v(-24.01, -113.86) * mm});
            skLineSegment(sketch, "E14.0.7.3", {"start": v(-24.01, -105.22) * mm, "end": v(-20.86, -105.22) * mm});
            skLineSegment(sketch, "E14.3.7.3", {"start": v(-20.86, -105.22) * mm, "end": v(-19.28, -107.95) * mm});
            skLineSegment(sketch, "E14.6.7.3", {"start": v(-19.28, -107.95) * mm, "end": v(-20.86, -110.68) * mm});
            skCircle(sketch, "E14.9.7.3", {"center": v(-22.44, -107.95) * mm, "radius": 2.73 * mm, "construction": true});
            skLineSegment(sketch, "E14.11.7.3", {"start": v(-20.86, -110.68) * mm, "end": v(-24.01, -110.68) * mm});
            skLineSegment(sketch, "E14.14.7.3", {"start": v(-24.01, -110.68) * mm, "end": v(-25.59, -107.95) * mm});
            skLineSegment(sketch, "E14.17.7.3", {"start": v(-25.59, -107.95) * mm, "end": v(-24.01, -105.22) * mm});
            skLineSegment(sketch, "E14.0.7.4", {"start": v(-24.01, -96.58) * mm, "end": v(-20.86, -96.58) * mm});
            skLineSegment(sketch, "E14.3.7.4", {"start": v(-20.86, -96.58) * mm, "end": v(-19.28, -99.31) * mm});
            skLineSegment(sketch, "E14.6.7.4", {"start": v(-19.28, -99.31) * mm, "end": v(-20.86, -102.04) * mm});
            skCircle(sketch, "E14.9.7.4", {"center": v(-22.44, -99.31) * mm, "radius": 2.73 * mm, "construction": true});
            skLineSegment(sketch, "E14.11.7.4", {"start": v(-20.86, -102.04) * mm, "end": v(-24.01, -102.04) * mm});
            skLineSegment(sketch, "E14.14.7.4", {"start": v(-24.01, -102.04) * mm, "end": v(-25.59, -99.31) * mm});
            skLineSegment(sketch, "E14.17.7.4", {"start": v(-25.59, -99.31) * mm, "end": v(-24.01, -96.58) * mm});
            skLineSegment(sketch, "E14.0.7.5", {"start": v(-24.01, -87.95) * mm, "end": v(-20.86, -87.95) * mm});
            skLineSegment(sketch, "E14.3.7.5", {"start": v(-20.86, -87.95) * mm, "end": v(-19.28, -90.68) * mm});
            skLineSegment(sketch, "E14.6.7.5", {"start": v(-19.28, -90.68) * mm, "end": v(-20.86, -93.4) * mm});
            skCircle(sketch, "E14.9.7.5", {"center": v(-22.44, -90.68) * mm, "radius": 2.73 * mm, "construction": true});
            skLineSegment(sketch, "E14.11.7.5", {"start": v(-20.86, -93.4) * mm, "end": v(-24.01, -93.4) * mm});
            skLineSegment(sketch, "E14.14.7.5", {"start": v(-24.01, -93.4) * mm, "end": v(-25.59, -90.68) * mm});
            skLineSegment(sketch, "E14.17.7.5", {"start": v(-25.59, -90.68) * mm, "end": v(-24.01, -87.95) * mm});
            skLineSegment(sketch, "E14.0.7.6", {"start": v(-24.01, -79.31) * mm, "end": v(-20.86, -79.31) * mm});
            skLineSegment(sketch, "E14.3.7.6", {"start": v(-20.86, -79.31) * mm, "end": v(-19.28, -82.04) * mm});
            skLineSegment(sketch, "E14.6.7.6", {"start": v(-19.28, -82.04) * mm, "end": v(-20.86, -84.77) * mm});
            skCircle(sketch, "E14.9.7.6", {"center": v(-22.44, -82.04) * mm, "radius": 2.73 * mm, "construction": true});
            skLineSegment(sketch, "E14.11.7.6", {"start": v(-20.86, -84.77) * mm, "end": v(-24.01, -84.77) * mm});
            skLineSegment(sketch, "E14.14.7.6", {"start": v(-24.01, -84.77) * mm, "end": v(-25.59, -82.04) * mm});
            skLineSegment(sketch, "E14.17.7.6", {"start": v(-25.59, -82.04) * mm, "end": v(-24.01, -79.31) * mm});
            skLineSegment(sketch, "E14.0.7.7", {"start": v(-24.01, -70.68) * mm, "end": v(-20.86, -70.68) * mm});
            skLineSegment(sketch, "E14.3.7.7", {"start": v(-20.86, -70.68) * mm, "end": v(-19.28, -73.4) * mm});
            skLineSegment(sketch, "E14.6.7.7", {"start": v(-19.28, -73.4) * mm, "end": v(-20.86, -76.14) * mm});
            skCircle(sketch, "E14.9.7.7", {"center": v(-22.44, -73.4) * mm, "radius": 2.73 * mm, "construction": true});
            skLineSegment(sketch, "E14.11.7.7", {"start": v(-20.86, -76.14) * mm, "end": v(-24.01, -76.14) * mm});
            skLineSegment(sketch, "E14.14.7.7", {"start": v(-24.01, -76.14) * mm, "end": v(-25.59, -73.4) * mm});
            skLineSegment(sketch, "E14.17.7.7", {"start": v(-25.59, -73.4) * mm, "end": v(-24.01, -70.68) * mm});
            skLineSegment(sketch, "E14.0.7.8", {"start": v(-24.01, -62.04) * mm, "end": v(-20.86, -62.04) * mm});
            skLineSegment(sketch, "E14.3.7.8", {"start": v(-20.86, -62.04) * mm, "end": v(-19.28, -64.77) * mm});
            skLineSegment(sketch, "E14.6.7.8", {"start": v(-19.28, -64.77) * mm, "end": v(-20.86, -67.5) * mm});
            skCircle(sketch, "E14.9.7.8", {"center": v(-22.44, -64.77) * mm, "radius": 2.73 * mm, "construction": true});
            skLineSegment(sketch, "E14.11.7.8", {"start": v(-20.86, -67.5) * mm, "end": v(-24.01, -67.5) * mm});
            skLineSegment(sketch, "E14.14.7.8", {"start": v(-24.01, -67.5) * mm, "end": v(-25.59, -64.77) * mm});
            skLineSegment(sketch, "E14.17.7.8", {"start": v(-25.59, -64.77) * mm, "end": v(-24.01, -62.04) * mm});
            skLineSegment(sketch, "E14.0.7.9", {"start": v(-24.01, -53.4) * mm, "end": v(-20.86, -53.4) * mm});
            skLineSegment(sketch, "E14.3.7.9", {"start": v(-20.86, -53.4) * mm, "end": v(-19.28, -56.13) * mm});
            skLineSegment(sketch, "E14.6.7.9", {"start": v(-19.28, -56.13) * mm, "end": v(-20.86, -58.86) * mm});
            skCircle(sketch, "E14.9.7.9", {"center": v(-22.44, -56.13) * mm, "radius": 2.73 * mm, "construction": true});
            skLineSegment(sketch, "E14.11.7.9", {"start": v(-20.86, -58.86) * mm, "end": v(-24.01, -58.86) * mm});
            skLineSegment(sketch, "E14.14.7.9", {"start": v(-24.01, -58.86) * mm, "end": v(-25.59, -56.13) * mm});
            skLineSegment(sketch, "E14.17.7.9", {"start": v(-25.59, -56.13) * mm, "end": v(-24.01, -53.4) * mm});
            skLineSegment(sketch, "E14.0.7.10", {"start": v(-24.01, -44.77) * mm, "end": v(-20.86, -44.77) * mm});
            skLineSegment(sketch, "E14.3.7.10", {"start": v(-20.86, -44.77) * mm, "end": v(-19.28, -47.5) * mm});
            skLineSegment(sketch, "E14.6.7.10", {"start": v(-19.28, -47.5) * mm, "end": v(-20.86, -50.23) * mm});
            skCircle(sketch, "E14.9.7.10", {"center": v(-22.44, -47.5) * mm, "radius": 2.73 * mm, "construction": true});
            skLineSegment(sketch, "E14.11.7.10", {"start": v(-20.86, -50.23) * mm, "end": v(-24.01, -50.23) * mm});
            skLineSegment(sketch, "E14.14.7.10", {"start": v(-24.01, -50.23) * mm, "end": v(-25.59, -47.5) * mm});
            skLineSegment(sketch, "E14.17.7.10", {"start": v(-25.59, -47.5) * mm, "end": v(-24.01, -44.77) * mm});
            skLineSegment(sketch, "E14.0.7.11", {"start": v(-24.01, -36.13) * mm, "end": v(-20.86, -36.13) * mm});
            skLineSegment(sketch, "E14.3.7.11", {"start": v(-20.86, -36.13) * mm, "end": v(-19.28, -38.86) * mm});
            skLineSegment(sketch, "E14.6.7.11", {"start": v(-19.28, -38.86) * mm, "end": v(-20.86, -41.6) * mm});
            skCircle(sketch, "E14.9.7.11", {"center": v(-22.44, -38.86) * mm, "radius": 2.73 * mm, "construction": true});
            skLineSegment(sketch, "E14.11.7.11", {"start": v(-20.86, -41.6) * mm, "end": v(-24.01, -41.6) * mm});
            skLineSegment(sketch, "E14.14.7.11", {"start": v(-24.01, -41.6) * mm, "end": v(-25.59, -38.86) * mm});
            skLineSegment(sketch, "E14.17.7.11", {"start": v(-25.59, -38.86) * mm, "end": v(-24.01, -36.13) * mm});
            skLineSegment(sketch, "E14.0.7.12", {"start": v(-24.01, -27.5) * mm, "end": v(-20.86, -27.5) * mm});
            skLineSegment(sketch, "E14.3.7.12", {"start": v(-20.86, -27.5) * mm, "end": v(-19.28, -30.23) * mm});
            skLineSegment(sketch, "E14.6.7.12", {"start": v(-19.28, -30.23) * mm, "end": v(-20.86, -32.96) * mm});
            skCircle(sketch, "E14.9.7.12", {"center": v(-22.44, -30.23) * mm, "radius": 2.73 * mm, "construction": true});
            skLineSegment(sketch, "E14.11.7.12", {"start": v(-20.86, -32.96) * mm, "end": v(-24.01, -32.96) * mm});
            skLineSegment(sketch, "E14.14.7.12", {"start": v(-24.01, -32.96) * mm, "end": v(-25.59, -30.23) * mm});
            skLineSegment(sketch, "E14.17.7.12", {"start": v(-25.59, -30.23) * mm, "end": v(-24.01, -27.5) * mm});
            skLineSegment(sketch, "E14.0.7.13", {"start": v(-24.01, -18.86) * mm, "end": v(-20.86, -18.86) * mm});
            skLineSegment(sketch, "E14.3.7.13", {"start": v(-20.86, -18.86) * mm, "end": v(-19.28, -21.6) * mm});
            skLineSegment(sketch, "E14.6.7.13", {"start": v(-19.28, -21.6) * mm, "end": v(-20.86, -24.32) * mm});
            skCircle(sketch, "E14.9.7.13", {"center": v(-22.44, -21.6) * mm, "radius": 2.73 * mm, "construction": true});
            skLineSegment(sketch, "E14.11.7.13", {"start": v(-20.86, -24.32) * mm, "end": v(-24.01, -24.32) * mm});
            skLineSegment(sketch, "E14.14.7.13", {"start": v(-24.01, -24.32) * mm, "end": v(-25.59, -21.6) * mm});
            skLineSegment(sketch, "E14.17.7.13", {"start": v(-25.59, -21.59) * mm, "end": v(-24.01, -18.86) * mm});
            skLineSegment(sketch, "E14.0.7.14", {"start": v(-24.01, -10.22) * mm, "end": v(-20.86, -10.22) * mm});
            skLineSegment(sketch, "E14.3.7.14", {"start": v(-20.86, -10.22) * mm, "end": v(-19.28, -12.95) * mm});
            skLineSegment(sketch, "E14.6.7.14", {"start": v(-19.28, -12.95) * mm, "end": v(-20.86, -15.68) * mm});
            skCircle(sketch, "E14.9.7.14", {"center": v(-22.44, -12.95) * mm, "radius": 2.73 * mm, "construction": true});
            skLineSegment(sketch, "E14.11.7.14", {"start": v(-20.86, -15.68) * mm, "end": v(-24.01, -15.68) * mm});
            skLineSegment(sketch, "E14.14.7.14", {"start": v(-24.01, -15.68) * mm, "end": v(-25.59, -12.95) * mm});
            skLineSegment(sketch, "E14.17.7.14", {"start": v(-25.59, -12.95) * mm, "end": v(-24.01, -10.22) * mm});
            skLineSegment(sketch, "E14.0.7.15", {"start": v(-24.01, -1.59) * mm, "end": v(-20.86, -1.59) * mm});
            skLineSegment(sketch, "E14.3.7.15", {"start": v(-20.86, -1.59) * mm, "end": v(-19.28, -4.32) * mm});
            skLineSegment(sketch, "E14.6.7.15", {"start": v(-19.28, -4.32) * mm, "end": v(-20.86, -7.05) * mm});
            skCircle(sketch, "E14.9.7.15", {"center": v(-22.44, -4.32) * mm, "radius": 2.73 * mm, "construction": true});
            skLineSegment(sketch, "E14.11.7.15", {"start": v(-20.86, -7.05) * mm, "end": v(-24.01, -7.05) * mm});
            skLineSegment(sketch, "E14.14.7.15", {"start": v(-24.01, -7.05) * mm, "end": v(-25.59, -4.32) * mm});
            skLineSegment(sketch, "E14.17.7.15", {"start": v(-25.59, -4.32) * mm, "end": v(-24.01, -1.59) * mm});
            skLineSegment(sketch, "E14.0.7.16", {"start": v(-24.01, 7.05) * mm, "end": v(-20.86, 7.05) * mm});
            skLineSegment(sketch, "E14.3.7.16", {"start": v(-20.86, 7.05) * mm, "end": v(-19.28, 4.32) * mm});
            skLineSegment(sketch, "E14.6.7.16", {"start": v(-19.28, 4.32) * mm, "end": v(-20.86, 1.59) * mm});
            skCircle(sketch, "E14.9.7.16", {"center": v(-22.44, 4.32) * mm, "radius": 2.73 * mm, "construction": true});
            skLineSegment(sketch, "E14.11.7.16", {"start": v(-20.86, 1.59) * mm, "end": v(-24.01, 1.59) * mm});
            skLineSegment(sketch, "E14.14.7.16", {"start": v(-24.01, 1.59) * mm, "end": v(-25.59, 4.32) * mm});
            skLineSegment(sketch, "E14.17.7.16", {"start": v(-25.59, 4.32) * mm, "end": v(-24.01, 7.05) * mm});
            skLineSegment(sketch, "E14.0.7.17", {"start": v(-24.01, 15.68) * mm, "end": v(-20.86, 15.68) * mm});
            skLineSegment(sketch, "E14.3.7.17", {"start": v(-20.86, 15.68) * mm, "end": v(-19.28, 12.95) * mm});
            skLineSegment(sketch, "E14.6.7.17", {"start": v(-19.28, 12.95) * mm, "end": v(-20.86, 10.22) * mm});
            skCircle(sketch, "E14.9.7.17", {"center": v(-22.44, 12.95) * mm, "radius": 2.73 * mm, "construction": true});
            skLineSegment(sketch, "E14.11.7.17", {"start": v(-20.86, 10.22) * mm, "end": v(-24.01, 10.22) * mm});
            skLineSegment(sketch, "E14.14.7.17", {"start": v(-24.01, 10.22) * mm, "end": v(-25.59, 12.95) * mm});
            skLineSegment(sketch, "E14.17.7.17", {"start": v(-25.59, 12.95) * mm, "end": v(-24.01, 15.68) * mm});
            skLineSegment(sketch, "E14.0.7.18", {"start": v(-24.01, 24.32) * mm, "end": v(-20.86, 24.32) * mm});
            skLineSegment(sketch, "E14.3.7.18", {"start": v(-20.86, 24.32) * mm, "end": v(-19.28, 21.59) * mm});
            skLineSegment(sketch, "E14.6.7.18", {"start": v(-19.28, 21.59) * mm, "end": v(-20.86, 18.86) * mm});
            skCircle(sketch, "E14.9.7.18", {"center": v(-22.44, 21.59) * mm, "radius": 2.73 * mm, "construction": true});
            skLineSegment(sketch, "E14.11.7.18", {"start": v(-20.86, 18.86) * mm, "end": v(-24.01, 18.86) * mm});
            skLineSegment(sketch, "E14.14.7.18", {"start": v(-24.01, 18.86) * mm, "end": v(-25.59, 21.59) * mm});
            skLineSegment(sketch, "E14.17.7.18", {"start": v(-25.59, 21.6) * mm, "end": v(-24.01, 24.32) * mm});
            skLineSegment(sketch, "E14.0.7.19", {"start": v(-24.01, 32.96) * mm, "end": v(-20.86, 32.96) * mm});
            skLineSegment(sketch, "E14.3.7.19", {"start": v(-20.86, 32.96) * mm, "end": v(-19.28, 30.23) * mm});
            skLineSegment(sketch, "E14.6.7.19", {"start": v(-19.28, 30.23) * mm, "end": v(-20.86, 27.5) * mm});
            skCircle(sketch, "E14.9.7.19", {"center": v(-22.44, 30.23) * mm, "radius": 2.73 * mm, "construction": true});
            skLineSegment(sketch, "E14.11.7.19", {"start": v(-20.86, 27.5) * mm, "end": v(-24.01, 27.5) * mm});
            skLineSegment(sketch, "E14.14.7.19", {"start": v(-24.01, 27.5) * mm, "end": v(-25.59, 30.23) * mm});
            skLineSegment(sketch, "E14.17.7.19", {"start": v(-25.59, 30.23) * mm, "end": v(-24.01, 32.96) * mm});
            skLineSegment(sketch, "E14.0.8.0", {"start": v(-9.06, -131.13) * mm, "end": v(-5.9, -131.13) * mm});
            skLineSegment(sketch, "E14.3.8.0", {"start": v(-5.9, -131.13) * mm, "end": v(-4.33, -133.86) * mm});
            skLineSegment(sketch, "E14.6.8.0", {"start": v(-4.33, -133.86) * mm, "end": v(-5.9, -136.59) * mm});
            skCircle(sketch, "E14.9.8.0", {"center": v(-7.48, -133.86) * mm, "radius": 2.73 * mm, "construction": true});
            skLineSegment(sketch, "E14.11.8.0", {"start": v(-5.9, -136.59) * mm, "end": v(-9.06, -136.59) * mm});
            skLineSegment(sketch, "E14.14.8.0", {"start": v(-9.06, -136.59) * mm, "end": v(-10.63, -133.86) * mm});
            skLineSegment(sketch, "E14.17.8.0", {"start": v(-10.63, -133.86) * mm, "end": v(-9.06, -131.13) * mm});
            skLineSegment(sketch, "E14.0.8.1", {"start": v(-9.06, -122.5) * mm, "end": v(-5.9, -122.5) * mm});
            skLineSegment(sketch, "E14.3.8.1", {"start": v(-5.9, -122.5) * mm, "end": v(-4.33, -125.22) * mm});
            skLineSegment(sketch, "E14.6.8.1", {"start": v(-4.33, -125.22) * mm, "end": v(-5.9, -127.95) * mm});
            skCircle(sketch, "E14.9.8.1", {"center": v(-7.48, -125.22) * mm, "radius": 2.73 * mm, "construction": true});
            skLineSegment(sketch, "E14.11.8.1", {"start": v(-5.9, -127.95) * mm, "end": v(-9.06, -127.95) * mm});
            skLineSegment(sketch, "E14.14.8.1", {"start": v(-9.06, -127.95) * mm, "end": v(-10.63, -125.22) * mm});
            skLineSegment(sketch, "E14.17.8.1", {"start": v(-10.63, -125.22) * mm, "end": v(-9.06, -122.5) * mm});
            skLineSegment(sketch, "E14.0.8.2", {"start": v(-9.06, -113.86) * mm, "end": v(-5.9, -113.86) * mm});
            skLineSegment(sketch, "E14.3.8.2", {"start": v(-5.9, -113.86) * mm, "end": v(-4.33, -116.59) * mm});
            skLineSegment(sketch, "E14.6.8.2", {"start": v(-4.33, -116.59) * mm, "end": v(-5.9, -119.32) * mm});
            skCircle(sketch, "E14.9.8.2", {"center": v(-7.48, -116.59) * mm, "radius": 2.73 * mm, "construction": true});
            skLineSegment(sketch, "E14.11.8.2", {"start": v(-5.9, -119.32) * mm, "end": v(-9.06, -119.32) * mm});
            skLineSegment(sketch, "E14.14.8.2", {"start": v(-9.06, -119.32) * mm, "end": v(-10.63, -116.59) * mm});
            skLineSegment(sketch, "E14.17.8.2", {"start": v(-10.63, -116.59) * mm, "end": v(-9.06, -113.86) * mm});
            skLineSegment(sketch, "E14.0.8.3", {"start": v(-9.06, -105.22) * mm, "end": v(-5.9, -105.22) * mm});
            skLineSegment(sketch, "E14.3.8.3", {"start": v(-5.9, -105.22) * mm, "end": v(-4.33, -107.95) * mm});
            skLineSegment(sketch, "E14.6.8.3", {"start": v(-4.33, -107.95) * mm, "end": v(-5.9, -110.68) * mm});
            skCircle(sketch, "E14.9.8.3", {"center": v(-7.48, -107.95) * mm, "radius": 2.73 * mm, "construction": true});
            skLineSegment(sketch, "E14.11.8.3", {"start": v(-5.9, -110.68) * mm, "end": v(-9.06, -110.68) * mm});
            skLineSegment(sketch, "E14.14.8.3", {"start": v(-9.06, -110.68) * mm, "end": v(-10.63, -107.95) * mm});
            skLineSegment(sketch, "E14.17.8.3", {"start": v(-10.63, -107.95) * mm, "end": v(-9.06, -105.22) * mm});
            skLineSegment(sketch, "E14.0.8.4", {"start": v(-9.06, -96.58) * mm, "end": v(-5.9, -96.58) * mm});
            skLineSegment(sketch, "E14.3.8.4", {"start": v(-5.9, -96.58) * mm, "end": v(-4.33, -99.31) * mm});
            skLineSegment(sketch, "E14.6.8.4", {"start": v(-4.33, -99.31) * mm, "end": v(-5.9, -102.04) * mm});
            skCircle(sketch, "E14.9.8.4", {"center": v(-7.48, -99.31) * mm, "radius": 2.73 * mm, "construction": true});
            skLineSegment(sketch, "E14.11.8.4", {"start": v(-5.9, -102.04) * mm, "end": v(-9.06, -102.04) * mm});
            skLineSegment(sketch, "E14.14.8.4", {"start": v(-9.06, -102.04) * mm, "end": v(-10.63, -99.31) * mm});
            skLineSegment(sketch, "E14.17.8.4", {"start": v(-10.63, -99.31) * mm, "end": v(-9.06, -96.58) * mm});
            skLineSegment(sketch, "E14.0.8.5", {"start": v(-9.06, -87.95) * mm, "end": v(-5.9, -87.95) * mm});
            skLineSegment(sketch, "E14.3.8.5", {"start": v(-5.9, -87.95) * mm, "end": v(-4.33, -90.68) * mm});
            skLineSegment(sketch, "E14.6.8.5", {"start": v(-4.33, -90.68) * mm, "end": v(-5.9, -93.4) * mm});
            skCircle(sketch, "E14.9.8.5", {"center": v(-7.48, -90.68) * mm, "radius": 2.73 * mm, "construction": true});
            skLineSegment(sketch, "E14.11.8.5", {"start": v(-5.9, -93.4) * mm, "end": v(-9.06, -93.4) * mm});
            skLineSegment(sketch, "E14.14.8.5", {"start": v(-9.06, -93.4) * mm, "end": v(-10.63, -90.68) * mm});
            skLineSegment(sketch, "E14.17.8.5", {"start": v(-10.63, -90.68) * mm, "end": v(-9.06, -87.95) * mm});
            skLineSegment(sketch, "E14.0.8.6", {"start": v(-9.06, -79.31) * mm, "end": v(-5.9, -79.31) * mm});
            skLineSegment(sketch, "E14.3.8.6", {"start": v(-5.9, -79.31) * mm, "end": v(-4.33, -82.04) * mm});
            skLineSegment(sketch, "E14.6.8.6", {"start": v(-4.33, -82.04) * mm, "end": v(-5.9, -84.77) * mm});
            skCircle(sketch, "E14.9.8.6", {"center": v(-7.48, -82.04) * mm, "radius": 2.73 * mm, "construction": true});
            skLineSegment(sketch, "E14.11.8.6", {"start": v(-5.9, -84.77) * mm, "end": v(-9.06, -84.77) * mm});
            skLineSegment(sketch, "E14.14.8.6", {"start": v(-9.06, -84.77) * mm, "end": v(-10.63, -82.04) * mm});
            skLineSegment(sketch, "E14.17.8.6", {"start": v(-10.63, -82.04) * mm, "end": v(-9.06, -79.31) * mm});
            skLineSegment(sketch, "E14.0.8.7", {"start": v(-9.06, -70.68) * mm, "end": v(-5.9, -70.68) * mm});
            skLineSegment(sketch, "E14.3.8.7", {"start": v(-5.9, -70.68) * mm, "end": v(-4.33, -73.4) * mm});
            skLineSegment(sketch, "E14.6.8.7", {"start": v(-4.33, -73.4) * mm, "end": v(-5.9, -76.14) * mm});
            skCircle(sketch, "E14.9.8.7", {"center": v(-7.48, -73.4) * mm, "radius": 2.73 * mm, "construction": true});
            skLineSegment(sketch, "E14.11.8.7", {"start": v(-5.9, -76.14) * mm, "end": v(-9.06, -76.14) * mm});
            skLineSegment(sketch, "E14.14.8.7", {"start": v(-9.06, -76.14) * mm, "end": v(-10.63, -73.4) * mm});
            skLineSegment(sketch, "E14.17.8.7", {"start": v(-10.63, -73.4) * mm, "end": v(-9.06, -70.68) * mm});
            skLineSegment(sketch, "E14.0.8.8", {"start": v(-9.06, -62.04) * mm, "end": v(-5.9, -62.04) * mm});
            skLineSegment(sketch, "E14.3.8.8", {"start": v(-5.9, -62.04) * mm, "end": v(-4.33, -64.77) * mm});
            skLineSegment(sketch, "E14.6.8.8", {"start": v(-4.33, -64.77) * mm, "end": v(-5.9, -67.5) * mm});
            skCircle(sketch, "E14.9.8.8", {"center": v(-7.48, -64.77) * mm, "radius": 2.73 * mm, "construction": true});
            skLineSegment(sketch, "E14.11.8.8", {"start": v(-5.9, -67.5) * mm, "end": v(-9.06, -67.5) * mm});
            skLineSegment(sketch, "E14.14.8.8", {"start": v(-9.06, -67.5) * mm, "end": v(-10.63, -64.77) * mm});
            skLineSegment(sketch, "E14.17.8.8", {"start": v(-10.63, -64.77) * mm, "end": v(-9.06, -62.04) * mm});
            skLineSegment(sketch, "E14.0.8.9", {"start": v(-9.06, -53.4) * mm, "end": v(-5.9, -53.4) * mm});
            skLineSegment(sketch, "E14.3.8.9", {"start": v(-5.9, -53.4) * mm, "end": v(-4.33, -56.13) * mm});
            skLineSegment(sketch, "E14.6.8.9", {"start": v(-4.33, -56.13) * mm, "end": v(-5.9, -58.86) * mm});
            skCircle(sketch, "E14.9.8.9", {"center": v(-7.48, -56.13) * mm, "radius": 2.73 * mm, "construction": true});
            skLineSegment(sketch, "E14.11.8.9", {"start": v(-5.9, -58.86) * mm, "end": v(-9.06, -58.86) * mm});
            skLineSegment(sketch, "E14.14.8.9", {"start": v(-9.06, -58.86) * mm, "end": v(-10.63, -56.13) * mm});
            skLineSegment(sketch, "E14.17.8.9", {"start": v(-10.63, -56.13) * mm, "end": v(-9.06, -53.4) * mm});
            skLineSegment(sketch, "E14.0.8.10", {"start": v(-9.06, -44.77) * mm, "end": v(-5.9, -44.77) * mm});
            skLineSegment(sketch, "E14.3.8.10", {"start": v(-5.9, -44.77) * mm, "end": v(-4.33, -47.5) * mm});
            skLineSegment(sketch, "E14.6.8.10", {"start": v(-4.33, -47.5) * mm, "end": v(-5.9, -50.23) * mm});
            skCircle(sketch, "E14.9.8.10", {"center": v(-7.48, -47.5) * mm, "radius": 2.73 * mm, "construction": true});
            skLineSegment(sketch, "E14.11.8.10", {"start": v(-5.9, -50.23) * mm, "end": v(-9.06, -50.23) * mm});
            skLineSegment(sketch, "E14.14.8.10", {"start": v(-9.06, -50.23) * mm, "end": v(-10.63, -47.5) * mm});
            skLineSegment(sketch, "E14.17.8.10", {"start": v(-10.63, -47.5) * mm, "end": v(-9.06, -44.77) * mm});
            skLineSegment(sketch, "E14.0.8.11", {"start": v(-9.06, -36.13) * mm, "end": v(-5.9, -36.13) * mm});
            skLineSegment(sketch, "E14.3.8.11", {"start": v(-5.9, -36.13) * mm, "end": v(-4.33, -38.86) * mm});
            skLineSegment(sketch, "E14.6.8.11", {"start": v(-4.33, -38.86) * mm, "end": v(-5.9, -41.6) * mm});
            skCircle(sketch, "E14.9.8.11", {"center": v(-7.48, -38.86) * mm, "radius": 2.73 * mm, "construction": true});
            skLineSegment(sketch, "E14.11.8.11", {"start": v(-5.9, -41.6) * mm, "end": v(-9.06, -41.6) * mm});
            skLineSegment(sketch, "E14.14.8.11", {"start": v(-9.06, -41.6) * mm, "end": v(-10.63, -38.86) * mm});
            skLineSegment(sketch, "E14.17.8.11", {"start": v(-10.63, -38.86) * mm, "end": v(-9.06, -36.13) * mm});
            skLineSegment(sketch, "E14.0.8.12", {"start": v(-9.06, -27.5) * mm, "end": v(-5.9, -27.5) * mm});
            skLineSegment(sketch, "E14.3.8.12", {"start": v(-5.9, -27.5) * mm, "end": v(-4.33, -30.23) * mm});
            skLineSegment(sketch, "E14.6.8.12", {"start": v(-4.33, -30.23) * mm, "end": v(-5.9, -32.96) * mm});
            skCircle(sketch, "E14.9.8.12", {"center": v(-7.48, -30.23) * mm, "radius": 2.73 * mm, "construction": true});
            skLineSegment(sketch, "E14.11.8.12", {"start": v(-5.9, -32.96) * mm, "end": v(-9.06, -32.96) * mm});
            skLineSegment(sketch, "E14.14.8.12", {"start": v(-9.06, -32.96) * mm, "end": v(-10.63, -30.23) * mm});
            skLineSegment(sketch, "E14.17.8.12", {"start": v(-10.63, -30.23) * mm, "end": v(-9.06, -27.5) * mm});
            skLineSegment(sketch, "E14.0.8.13", {"start": v(-9.06, -18.86) * mm, "end": v(-5.9, -18.86) * mm});
            skLineSegment(sketch, "E14.3.8.13", {"start": v(-5.9, -18.86) * mm, "end": v(-4.33, -21.6) * mm});
            skLineSegment(sketch, "E14.6.8.13", {"start": v(-4.33, -21.6) * mm, "end": v(-5.9, -24.32) * mm});
            skCircle(sketch, "E14.9.8.13", {"center": v(-7.48, -21.6) * mm, "radius": 2.73 * mm, "construction": true});
            skLineSegment(sketch, "E14.11.8.13", {"start": v(-5.9, -24.32) * mm, "end": v(-9.06, -24.32) * mm});
            skLineSegment(sketch, "E14.14.8.13", {"start": v(-9.06, -24.32) * mm, "end": v(-10.63, -21.6) * mm});
            skLineSegment(sketch, "E14.17.8.13", {"start": v(-10.63, -21.59) * mm, "end": v(-9.06, -18.86) * mm});
            skLineSegment(sketch, "E14.0.8.14", {"start": v(-9.06, -10.22) * mm, "end": v(-5.9, -10.22) * mm});
            skLineSegment(sketch, "E14.3.8.14", {"start": v(-5.9, -10.22) * mm, "end": v(-4.33, -12.95) * mm});
            skLineSegment(sketch, "E14.6.8.14", {"start": v(-4.33, -12.95) * mm, "end": v(-5.9, -15.68) * mm});
            skCircle(sketch, "E14.9.8.14", {"center": v(-7.48, -12.95) * mm, "radius": 2.73 * mm, "construction": true});
            skLineSegment(sketch, "E14.11.8.14", {"start": v(-5.9, -15.68) * mm, "end": v(-9.06, -15.68) * mm});
            skLineSegment(sketch, "E14.14.8.14", {"start": v(-9.06, -15.68) * mm, "end": v(-10.63, -12.95) * mm});
            skLineSegment(sketch, "E14.17.8.14", {"start": v(-10.63, -12.95) * mm, "end": v(-9.06, -10.22) * mm});
            skLineSegment(sketch, "E14.0.8.15", {"start": v(-9.06, -1.59) * mm, "end": v(-5.9, -1.59) * mm});
            skLineSegment(sketch, "E14.3.8.15", {"start": v(-5.9, -1.59) * mm, "end": v(-4.33, -4.32) * mm});
            skLineSegment(sketch, "E14.6.8.15", {"start": v(-4.33, -4.32) * mm, "end": v(-5.9, -7.05) * mm});
            skCircle(sketch, "E14.9.8.15", {"center": v(-7.48, -4.32) * mm, "radius": 2.73 * mm, "construction": true});
            skLineSegment(sketch, "E14.11.8.15", {"start": v(-5.9, -7.05) * mm, "end": v(-9.06, -7.05) * mm});
            skLineSegment(sketch, "E14.14.8.15", {"start": v(-9.06, -7.05) * mm, "end": v(-10.63, -4.32) * mm});
            skLineSegment(sketch, "E14.17.8.15", {"start": v(-10.63, -4.32) * mm, "end": v(-9.06, -1.59) * mm});
            skLineSegment(sketch, "E14.0.8.16", {"start": v(-9.06, 7.05) * mm, "end": v(-5.9, 7.05) * mm});
            skLineSegment(sketch, "E14.3.8.16", {"start": v(-5.9, 7.05) * mm, "end": v(-4.33, 4.32) * mm});
            skLineSegment(sketch, "E14.6.8.16", {"start": v(-4.33, 4.32) * mm, "end": v(-5.9, 1.59) * mm});
            skCircle(sketch, "E14.9.8.16", {"center": v(-7.48, 4.32) * mm, "radius": 2.73 * mm, "construction": true});
            skLineSegment(sketch, "E14.11.8.16", {"start": v(-5.9, 1.59) * mm, "end": v(-9.06, 1.59) * mm});
            skLineSegment(sketch, "E14.14.8.16", {"start": v(-9.06, 1.59) * mm, "end": v(-10.63, 4.32) * mm});
            skLineSegment(sketch, "E14.17.8.16", {"start": v(-10.63, 4.32) * mm, "end": v(-9.06, 7.05) * mm});
            skLineSegment(sketch, "E14.0.8.17", {"start": v(-9.06, 15.68) * mm, "end": v(-5.9, 15.68) * mm});
            skLineSegment(sketch, "E14.3.8.17", {"start": v(-5.9, 15.68) * mm, "end": v(-4.33, 12.95) * mm});
            skLineSegment(sketch, "E14.6.8.17", {"start": v(-4.33, 12.95) * mm, "end": v(-5.9, 10.22) * mm});
            skCircle(sketch, "E14.9.8.17", {"center": v(-7.48, 12.95) * mm, "radius": 2.73 * mm, "construction": true});
            skLineSegment(sketch, "E14.11.8.17", {"start": v(-5.9, 10.22) * mm, "end": v(-9.06, 10.22) * mm});
            skLineSegment(sketch, "E14.14.8.17", {"start": v(-9.06, 10.22) * mm, "end": v(-10.63, 12.95) * mm});
            skLineSegment(sketch, "E14.17.8.17", {"start": v(-10.63, 12.95) * mm, "end": v(-9.06, 15.68) * mm});
            skLineSegment(sketch, "E14.0.8.18", {"start": v(-9.06, 24.32) * mm, "end": v(-5.9, 24.32) * mm});
            skLineSegment(sketch, "E14.3.8.18", {"start": v(-5.9, 24.32) * mm, "end": v(-4.33, 21.59) * mm});
            skLineSegment(sketch, "E14.6.8.18", {"start": v(-4.33, 21.59) * mm, "end": v(-5.9, 18.86) * mm});
            skCircle(sketch, "E14.9.8.18", {"center": v(-7.48, 21.59) * mm, "radius": 2.73 * mm, "construction": true});
            skLineSegment(sketch, "E14.11.8.18", {"start": v(-5.9, 18.86) * mm, "end": v(-9.06, 18.86) * mm});
            skLineSegment(sketch, "E14.14.8.18", {"start": v(-9.06, 18.86) * mm, "end": v(-10.63, 21.59) * mm});
            skLineSegment(sketch, "E14.17.8.18", {"start": v(-10.63, 21.6) * mm, "end": v(-9.06, 24.32) * mm});
            skLineSegment(sketch, "E14.0.8.19", {"start": v(-9.06, 32.96) * mm, "end": v(-5.9, 32.96) * mm});
            skLineSegment(sketch, "E14.3.8.19", {"start": v(-5.9, 32.96) * mm, "end": v(-4.33, 30.23) * mm});
            skLineSegment(sketch, "E14.6.8.19", {"start": v(-4.33, 30.23) * mm, "end": v(-5.9, 27.5) * mm});
            skCircle(sketch, "E14.9.8.19", {"center": v(-7.48, 30.23) * mm, "radius": 2.73 * mm, "construction": true});
            skLineSegment(sketch, "E14.11.8.19", {"start": v(-5.9, 27.5) * mm, "end": v(-9.06, 27.5) * mm});
            skLineSegment(sketch, "E14.14.8.19", {"start": v(-9.06, 27.5) * mm, "end": v(-10.63, 30.23) * mm});
            skLineSegment(sketch, "E14.17.8.19", {"start": v(-10.63, 30.23) * mm, "end": v(-9.06, 32.96) * mm});
            skLineSegment(sketch, "E14.0.9.0", {"start": v(5.9, -131.13) * mm, "end": v(9.06, -131.13) * mm});
            skLineSegment(sketch, "E14.3.9.0", {"start": v(9.06, -131.13) * mm, "end": v(10.63, -133.86) * mm});
            skLineSegment(sketch, "E14.6.9.0", {"start": v(10.63, -133.86) * mm, "end": v(9.06, -136.59) * mm});
            skCircle(sketch, "E14.9.9.0", {"center": v(7.48, -133.86) * mm, "radius": 2.73 * mm, "construction": true});
            skLineSegment(sketch, "E14.11.9.0", {"start": v(9.06, -136.59) * mm, "end": v(5.9, -136.59) * mm});
            skLineSegment(sketch, "E14.14.9.0", {"start": v(5.9, -136.59) * mm, "end": v(4.33, -133.86) * mm});
            skLineSegment(sketch, "E14.17.9.0", {"start": v(4.33, -133.86) * mm, "end": v(5.9, -131.13) * mm});
            skLineSegment(sketch, "E14.0.9.1", {"start": v(5.9, -122.5) * mm, "end": v(9.06, -122.5) * mm});
            skLineSegment(sketch, "E14.3.9.1", {"start": v(9.06, -122.5) * mm, "end": v(10.63, -125.22) * mm});
            skLineSegment(sketch, "E14.6.9.1", {"start": v(10.63, -125.22) * mm, "end": v(9.06, -127.95) * mm});
            skCircle(sketch, "E14.9.9.1", {"center": v(7.48, -125.22) * mm, "radius": 2.73 * mm, "construction": true});
            skLineSegment(sketch, "E14.11.9.1", {"start": v(9.06, -127.95) * mm, "end": v(5.9, -127.95) * mm});
            skLineSegment(sketch, "E14.14.9.1", {"start": v(5.9, -127.95) * mm, "end": v(4.33, -125.22) * mm});
            skLineSegment(sketch, "E14.17.9.1", {"start": v(4.33, -125.22) * mm, "end": v(5.9, -122.5) * mm});
            skLineSegment(sketch, "E14.0.9.2", {"start": v(5.9, -113.86) * mm, "end": v(9.06, -113.86) * mm});
            skLineSegment(sketch, "E14.3.9.2", {"start": v(9.06, -113.86) * mm, "end": v(10.63, -116.59) * mm});
            skLineSegment(sketch, "E14.6.9.2", {"start": v(10.63, -116.59) * mm, "end": v(9.06, -119.32) * mm});
            skCircle(sketch, "E14.9.9.2", {"center": v(7.48, -116.59) * mm, "radius": 2.73 * mm, "construction": true});
            skLineSegment(sketch, "E14.11.9.2", {"start": v(9.06, -119.32) * mm, "end": v(5.9, -119.32) * mm});
            skLineSegment(sketch, "E14.14.9.2", {"start": v(5.9, -119.32) * mm, "end": v(4.33, -116.59) * mm});
            skLineSegment(sketch, "E14.17.9.2", {"start": v(4.33, -116.59) * mm, "end": v(5.9, -113.86) * mm});
            skLineSegment(sketch, "E14.0.9.3", {"start": v(5.9, -105.22) * mm, "end": v(9.06, -105.22) * mm});
            skLineSegment(sketch, "E14.3.9.3", {"start": v(9.06, -105.22) * mm, "end": v(10.63, -107.95) * mm});
            skLineSegment(sketch, "E14.6.9.3", {"start": v(10.63, -107.95) * mm, "end": v(9.06, -110.68) * mm});
            skCircle(sketch, "E14.9.9.3", {"center": v(7.48, -107.95) * mm, "radius": 2.73 * mm, "construction": true});
            skLineSegment(sketch, "E14.11.9.3", {"start": v(9.06, -110.68) * mm, "end": v(5.9, -110.68) * mm});
            skLineSegment(sketch, "E14.14.9.3", {"start": v(5.9, -110.68) * mm, "end": v(4.33, -107.95) * mm});
            skLineSegment(sketch, "E14.17.9.3", {"start": v(4.33, -107.95) * mm, "end": v(5.9, -105.22) * mm});
            skLineSegment(sketch, "E14.0.9.4", {"start": v(5.9, -96.58) * mm, "end": v(9.06, -96.58) * mm});
            skLineSegment(sketch, "E14.3.9.4", {"start": v(9.06, -96.58) * mm, "end": v(10.63, -99.31) * mm});
            skLineSegment(sketch, "E14.6.9.4", {"start": v(10.63, -99.31) * mm, "end": v(9.06, -102.04) * mm});
            skCircle(sketch, "E14.9.9.4", {"center": v(7.48, -99.31) * mm, "radius": 2.73 * mm, "construction": true});
            skLineSegment(sketch, "E14.11.9.4", {"start": v(9.06, -102.04) * mm, "end": v(5.9, -102.04) * mm});
            skLineSegment(sketch, "E14.14.9.4", {"start": v(5.9, -102.04) * mm, "end": v(4.33, -99.31) * mm});
            skLineSegment(sketch, "E14.17.9.4", {"start": v(4.33, -99.31) * mm, "end": v(5.9, -96.58) * mm});
            skLineSegment(sketch, "E14.0.9.5", {"start": v(5.9, -87.95) * mm, "end": v(9.06, -87.95) * mm});
            skLineSegment(sketch, "E14.3.9.5", {"start": v(9.06, -87.95) * mm, "end": v(10.63, -90.68) * mm});
            skLineSegment(sketch, "E14.6.9.5", {"start": v(10.63, -90.68) * mm, "end": v(9.06, -93.4) * mm});
            skCircle(sketch, "E14.9.9.5", {"center": v(7.48, -90.68) * mm, "radius": 2.73 * mm, "construction": true});
            skLineSegment(sketch, "E14.11.9.5", {"start": v(9.06, -93.4) * mm, "end": v(5.9, -93.4) * mm});
            skLineSegment(sketch, "E14.14.9.5", {"start": v(5.9, -93.4) * mm, "end": v(4.33, -90.68) * mm});
            skLineSegment(sketch, "E14.17.9.5", {"start": v(4.33, -90.68) * mm, "end": v(5.9, -87.95) * mm});
            skLineSegment(sketch, "E14.0.9.6", {"start": v(5.9, -79.31) * mm, "end": v(9.06, -79.31) * mm});
            skLineSegment(sketch, "E14.3.9.6", {"start": v(9.06, -79.31) * mm, "end": v(10.63, -82.04) * mm});
            skLineSegment(sketch, "E14.6.9.6", {"start": v(10.63, -82.04) * mm, "end": v(9.06, -84.77) * mm});
            skCircle(sketch, "E14.9.9.6", {"center": v(7.48, -82.04) * mm, "radius": 2.73 * mm, "construction": true});
            skLineSegment(sketch, "E14.11.9.6", {"start": v(9.06, -84.77) * mm, "end": v(5.9, -84.77) * mm});
            skLineSegment(sketch, "E14.14.9.6", {"start": v(5.9, -84.77) * mm, "end": v(4.33, -82.04) * mm});
            skLineSegment(sketch, "E14.17.9.6", {"start": v(4.33, -82.04) * mm, "end": v(5.9, -79.31) * mm});
            skLineSegment(sketch, "E14.0.9.7", {"start": v(5.9, -70.68) * mm, "end": v(9.06, -70.68) * mm});
            skLineSegment(sketch, "E14.3.9.7", {"start": v(9.06, -70.68) * mm, "end": v(10.63, -73.4) * mm});
            skLineSegment(sketch, "E14.6.9.7", {"start": v(10.63, -73.4) * mm, "end": v(9.06, -76.14) * mm});
            skCircle(sketch, "E14.9.9.7", {"center": v(7.48, -73.4) * mm, "radius": 2.73 * mm, "construction": true});
            skLineSegment(sketch, "E14.11.9.7", {"start": v(9.06, -76.14) * mm, "end": v(5.9, -76.14) * mm});
            skLineSegment(sketch, "E14.14.9.7", {"start": v(5.9, -76.14) * mm, "end": v(4.33, -73.4) * mm});
            skLineSegment(sketch, "E14.17.9.7", {"start": v(4.33, -73.4) * mm, "end": v(5.9, -70.68) * mm});
            skLineSegment(sketch, "E14.0.9.8", {"start": v(5.9, -62.04) * mm, "end": v(9.06, -62.04) * mm});
            skLineSegment(sketch, "E14.3.9.8", {"start": v(9.06, -62.04) * mm, "end": v(10.63, -64.77) * mm});
            skLineSegment(sketch, "E14.6.9.8", {"start": v(10.63, -64.77) * mm, "end": v(9.06, -67.5) * mm});
            skCircle(sketch, "E14.9.9.8", {"center": v(7.48, -64.77) * mm, "radius": 2.73 * mm, "construction": true});
            skLineSegment(sketch, "E14.11.9.8", {"start": v(9.06, -67.5) * mm, "end": v(5.9, -67.5) * mm});
            skLineSegment(sketch, "E14.14.9.8", {"start": v(5.9, -67.5) * mm, "end": v(4.33, -64.77) * mm});
            skLineSegment(sketch, "E14.17.9.8", {"start": v(4.33, -64.77) * mm, "end": v(5.9, -62.04) * mm});
            skLineSegment(sketch, "E14.0.9.9", {"start": v(5.9, -53.4) * mm, "end": v(9.06, -53.4) * mm});
            skLineSegment(sketch, "E14.3.9.9", {"start": v(9.06, -53.4) * mm, "end": v(10.63, -56.13) * mm});
            skLineSegment(sketch, "E14.6.9.9", {"start": v(10.63, -56.13) * mm, "end": v(9.06, -58.86) * mm});
            skCircle(sketch, "E14.9.9.9", {"center": v(7.48, -56.13) * mm, "radius": 2.73 * mm, "construction": true});
            skLineSegment(sketch, "E14.11.9.9", {"start": v(9.06, -58.86) * mm, "end": v(5.9, -58.86) * mm});
            skLineSegment(sketch, "E14.14.9.9", {"start": v(5.9, -58.86) * mm, "end": v(4.33, -56.13) * mm});
            skLineSegment(sketch, "E14.17.9.9", {"start": v(4.33, -56.13) * mm, "end": v(5.9, -53.4) * mm});
            skLineSegment(sketch, "E14.0.9.10", {"start": v(5.9, -44.77) * mm, "end": v(9.06, -44.77) * mm});
            skLineSegment(sketch, "E14.3.9.10", {"start": v(9.06, -44.77) * mm, "end": v(10.63, -47.5) * mm});
            skLineSegment(sketch, "E14.6.9.10", {"start": v(10.63, -47.5) * mm, "end": v(9.06, -50.23) * mm});
            skCircle(sketch, "E14.9.9.10", {"center": v(7.48, -47.5) * mm, "radius": 2.73 * mm, "construction": true});
            skLineSegment(sketch, "E14.11.9.10", {"start": v(9.06, -50.23) * mm, "end": v(5.9, -50.23) * mm});
            skLineSegment(sketch, "E14.14.9.10", {"start": v(5.9, -50.23) * mm, "end": v(4.33, -47.5) * mm});
            skLineSegment(sketch, "E14.17.9.10", {"start": v(4.33, -47.5) * mm, "end": v(5.9, -44.77) * mm});
            skLineSegment(sketch, "E14.0.9.11", {"start": v(5.9, -36.13) * mm, "end": v(9.06, -36.13) * mm});
            skLineSegment(sketch, "E14.3.9.11", {"start": v(9.06, -36.13) * mm, "end": v(10.63, -38.86) * mm});
            skLineSegment(sketch, "E14.6.9.11", {"start": v(10.63, -38.86) * mm, "end": v(9.06, -41.6) * mm});
            skCircle(sketch, "E14.9.9.11", {"center": v(7.48, -38.86) * mm, "radius": 2.73 * mm, "construction": true});
            skLineSegment(sketch, "E14.11.9.11", {"start": v(9.06, -41.6) * mm, "end": v(5.9, -41.6) * mm});
            skLineSegment(sketch, "E14.14.9.11", {"start": v(5.9, -41.6) * mm, "end": v(4.33, -38.86) * mm});
            skLineSegment(sketch, "E14.17.9.11", {"start": v(4.33, -38.86) * mm, "end": v(5.9, -36.13) * mm});
            skLineSegment(sketch, "E14.0.9.12", {"start": v(5.9, -27.5) * mm, "end": v(9.06, -27.5) * mm});
            skLineSegment(sketch, "E14.3.9.12", {"start": v(9.06, -27.5) * mm, "end": v(10.63, -30.23) * mm});
            skLineSegment(sketch, "E14.6.9.12", {"start": v(10.63, -30.23) * mm, "end": v(9.06, -32.96) * mm});
            skCircle(sketch, "E14.9.9.12", {"center": v(7.48, -30.23) * mm, "radius": 2.73 * mm, "construction": true});
            skLineSegment(sketch, "E14.11.9.12", {"start": v(9.06, -32.96) * mm, "end": v(5.9, -32.96) * mm});
            skLineSegment(sketch, "E14.14.9.12", {"start": v(5.9, -32.96) * mm, "end": v(4.33, -30.23) * mm});
            skLineSegment(sketch, "E14.17.9.12", {"start": v(4.33, -30.23) * mm, "end": v(5.9, -27.5) * mm});
            skLineSegment(sketch, "E14.0.9.13", {"start": v(5.9, -18.86) * mm, "end": v(9.06, -18.86) * mm});
            skLineSegment(sketch, "E14.3.9.13", {"start": v(9.06, -18.86) * mm, "end": v(10.63, -21.6) * mm});
            skLineSegment(sketch, "E14.6.9.13", {"start": v(10.63, -21.6) * mm, "end": v(9.06, -24.32) * mm});
            skCircle(sketch, "E14.9.9.13", {"center": v(7.48, -21.6) * mm, "radius": 2.73 * mm, "construction": true});
            skLineSegment(sketch, "E14.11.9.13", {"start": v(9.06, -24.32) * mm, "end": v(5.9, -24.32) * mm});
            skLineSegment(sketch, "E14.14.9.13", {"start": v(5.9, -24.32) * mm, "end": v(4.33, -21.6) * mm});
            skLineSegment(sketch, "E14.17.9.13", {"start": v(4.33, -21.59) * mm, "end": v(5.9, -18.86) * mm});
            skLineSegment(sketch, "E14.0.9.14", {"start": v(5.9, -10.22) * mm, "end": v(9.06, -10.22) * mm});
            skLineSegment(sketch, "E14.3.9.14", {"start": v(9.06, -10.22) * mm, "end": v(10.63, -12.95) * mm});
            skLineSegment(sketch, "E14.6.9.14", {"start": v(10.63, -12.95) * mm, "end": v(9.06, -15.68) * mm});
            skCircle(sketch, "E14.9.9.14", {"center": v(7.48, -12.95) * mm, "radius": 2.73 * mm, "construction": true});
            skLineSegment(sketch, "E14.11.9.14", {"start": v(9.06, -15.68) * mm, "end": v(5.9, -15.68) * mm});
            skLineSegment(sketch, "E14.14.9.14", {"start": v(5.9, -15.68) * mm, "end": v(4.33, -12.95) * mm});
            skLineSegment(sketch, "E14.17.9.14", {"start": v(4.33, -12.95) * mm, "end": v(5.9, -10.22) * mm});
            skLineSegment(sketch, "E14.0.9.15", {"start": v(5.9, -1.59) * mm, "end": v(9.06, -1.59) * mm});
            skLineSegment(sketch, "E14.3.9.15", {"start": v(9.06, -1.59) * mm, "end": v(10.63, -4.32) * mm});
            skLineSegment(sketch, "E14.6.9.15", {"start": v(10.63, -4.32) * mm, "end": v(9.06, -7.05) * mm});
            skCircle(sketch, "E14.9.9.15", {"center": v(7.48, -4.32) * mm, "radius": 2.73 * mm, "construction": true});
            skLineSegment(sketch, "E14.11.9.15", {"start": v(9.06, -7.05) * mm, "end": v(5.9, -7.05) * mm});
            skLineSegment(sketch, "E14.14.9.15", {"start": v(5.9, -7.05) * mm, "end": v(4.33, -4.32) * mm});
            skLineSegment(sketch, "E14.17.9.15", {"start": v(4.33, -4.32) * mm, "end": v(5.9, -1.59) * mm});
            skLineSegment(sketch, "E14.0.9.16", {"start": v(5.9, 7.05) * mm, "end": v(9.06, 7.05) * mm});
            skLineSegment(sketch, "E14.3.9.16", {"start": v(9.06, 7.05) * mm, "end": v(10.63, 4.32) * mm});
            skLineSegment(sketch, "E14.6.9.16", {"start": v(10.63, 4.32) * mm, "end": v(9.06, 1.59) * mm});
            skCircle(sketch, "E14.9.9.16", {"center": v(7.48, 4.32) * mm, "radius": 2.73 * mm, "construction": true});
            skLineSegment(sketch, "E14.11.9.16", {"start": v(9.06, 1.59) * mm, "end": v(5.9, 1.59) * mm});
            skLineSegment(sketch, "E14.14.9.16", {"start": v(5.9, 1.59) * mm, "end": v(4.33, 4.32) * mm});
            skLineSegment(sketch, "E14.17.9.16", {"start": v(4.33, 4.32) * mm, "end": v(5.9, 7.05) * mm});
            skLineSegment(sketch, "E14.0.9.17", {"start": v(5.9, 15.68) * mm, "end": v(9.06, 15.68) * mm});
            skLineSegment(sketch, "E14.3.9.17", {"start": v(9.06, 15.68) * mm, "end": v(10.63, 12.95) * mm});
            skLineSegment(sketch, "E14.6.9.17", {"start": v(10.63, 12.95) * mm, "end": v(9.06, 10.22) * mm});
            skCircle(sketch, "E14.9.9.17", {"center": v(7.48, 12.95) * mm, "radius": 2.73 * mm, "construction": true});
            skLineSegment(sketch, "E14.11.9.17", {"start": v(9.06, 10.22) * mm, "end": v(5.9, 10.22) * mm});
            skLineSegment(sketch, "E14.14.9.17", {"start": v(5.9, 10.22) * mm, "end": v(4.33, 12.95) * mm});
            skLineSegment(sketch, "E14.17.9.17", {"start": v(4.33, 12.95) * mm, "end": v(5.9, 15.68) * mm});
            skLineSegment(sketch, "E14.0.9.18", {"start": v(5.9, 24.32) * mm, "end": v(9.06, 24.32) * mm});
            skLineSegment(sketch, "E14.3.9.18", {"start": v(9.06, 24.32) * mm, "end": v(10.63, 21.59) * mm});
            skLineSegment(sketch, "E14.6.9.18", {"start": v(10.63, 21.59) * mm, "end": v(9.06, 18.86) * mm});
            skCircle(sketch, "E14.9.9.18", {"center": v(7.48, 21.59) * mm, "radius": 2.73 * mm, "construction": true});
            skLineSegment(sketch, "E14.11.9.18", {"start": v(9.06, 18.86) * mm, "end": v(5.9, 18.86) * mm});
            skLineSegment(sketch, "E14.14.9.18", {"start": v(5.9, 18.86) * mm, "end": v(4.33, 21.59) * mm});
            skLineSegment(sketch, "E14.17.9.18", {"start": v(4.33, 21.6) * mm, "end": v(5.9, 24.32) * mm});
            skLineSegment(sketch, "E14.0.9.19", {"start": v(5.9, 32.96) * mm, "end": v(9.06, 32.96) * mm});
            skLineSegment(sketch, "E14.3.9.19", {"start": v(9.06, 32.96) * mm, "end": v(10.63, 30.23) * mm});
            skLineSegment(sketch, "E14.6.9.19", {"start": v(10.63, 30.23) * mm, "end": v(9.06, 27.5) * mm});
            skCircle(sketch, "E14.9.9.19", {"center": v(7.48, 30.23) * mm, "radius": 2.73 * mm, "construction": true});
            skLineSegment(sketch, "E14.11.9.19", {"start": v(9.06, 27.5) * mm, "end": v(5.9, 27.5) * mm});
            skLineSegment(sketch, "E14.14.9.19", {"start": v(5.9, 27.5) * mm, "end": v(4.33, 30.23) * mm});
            skLineSegment(sketch, "E14.17.9.19", {"start": v(4.33, 30.23) * mm, "end": v(5.9, 32.96) * mm});
            skLineSegment(sketch, "E14.0.10.0", {"start": v(20.86, -131.13) * mm, "end": v(24.01, -131.13) * mm});
            skLineSegment(sketch, "E14.3.10.0", {"start": v(24.01, -131.13) * mm, "end": v(25.6, -133.86) * mm});
            skLineSegment(sketch, "E14.6.10.0", {"start": v(25.6, -133.86) * mm, "end": v(24.01, -136.59) * mm});
            skCircle(sketch, "E14.9.10.0", {"center": v(22.44, -133.86) * mm, "radius": 2.73 * mm, "construction": true});
            skLineSegment(sketch, "E14.11.10.0", {"start": v(24.01, -136.59) * mm, "end": v(20.86, -136.59) * mm});
            skLineSegment(sketch, "E14.14.10.0", {"start": v(20.86, -136.59) * mm, "end": v(19.28, -133.86) * mm});
            skLineSegment(sketch, "E14.17.10.0", {"start": v(19.28, -133.86) * mm, "end": v(20.86, -131.13) * mm});
            skLineSegment(sketch, "E14.0.10.1", {"start": v(20.86, -122.5) * mm, "end": v(24.01, -122.5) * mm});
            skLineSegment(sketch, "E14.3.10.1", {"start": v(24.01, -122.5) * mm, "end": v(25.6, -125.22) * mm});
            skLineSegment(sketch, "E14.6.10.1", {"start": v(25.6, -125.22) * mm, "end": v(24.01, -127.95) * mm});
            skCircle(sketch, "E14.9.10.1", {"center": v(22.44, -125.22) * mm, "radius": 2.73 * mm, "construction": true});
            skLineSegment(sketch, "E14.11.10.1", {"start": v(24.01, -127.95) * mm, "end": v(20.86, -127.95) * mm});
            skLineSegment(sketch, "E14.14.10.1", {"start": v(20.86, -127.95) * mm, "end": v(19.28, -125.22) * mm});
            skLineSegment(sketch, "E14.17.10.1", {"start": v(19.28, -125.22) * mm, "end": v(20.86, -122.5) * mm});
            skLineSegment(sketch, "E14.0.10.2", {"start": v(20.86, -113.86) * mm, "end": v(24.01, -113.86) * mm});
            skLineSegment(sketch, "E14.3.10.2", {"start": v(24.01, -113.86) * mm, "end": v(25.6, -116.59) * mm});
            skLineSegment(sketch, "E14.6.10.2", {"start": v(25.6, -116.59) * mm, "end": v(24.01, -119.32) * mm});
            skCircle(sketch, "E14.9.10.2", {"center": v(22.44, -116.59) * mm, "radius": 2.73 * mm, "construction": true});
            skLineSegment(sketch, "E14.11.10.2", {"start": v(24.01, -119.32) * mm, "end": v(20.86, -119.32) * mm});
            skLineSegment(sketch, "E14.14.10.2", {"start": v(20.86, -119.32) * mm, "end": v(19.28, -116.59) * mm});
            skLineSegment(sketch, "E14.17.10.2", {"start": v(19.28, -116.59) * mm, "end": v(20.86, -113.86) * mm});
            skLineSegment(sketch, "E14.0.10.3", {"start": v(20.86, -105.22) * mm, "end": v(24.01, -105.22) * mm});
            skLineSegment(sketch, "E14.3.10.3", {"start": v(24.01, -105.22) * mm, "end": v(25.6, -107.95) * mm});
            skLineSegment(sketch, "E14.6.10.3", {"start": v(25.6, -107.95) * mm, "end": v(24.01, -110.68) * mm});
            skCircle(sketch, "E14.9.10.3", {"center": v(22.44, -107.95) * mm, "radius": 2.73 * mm, "construction": true});
            skLineSegment(sketch, "E14.11.10.3", {"start": v(24.01, -110.68) * mm, "end": v(20.86, -110.68) * mm});
            skLineSegment(sketch, "E14.14.10.3", {"start": v(20.86, -110.68) * mm, "end": v(19.28, -107.95) * mm});
            skLineSegment(sketch, "E14.17.10.3", {"start": v(19.28, -107.95) * mm, "end": v(20.86, -105.22) * mm});
            skLineSegment(sketch, "E14.0.10.4", {"start": v(20.86, -96.58) * mm, "end": v(24.01, -96.58) * mm});
            skLineSegment(sketch, "E14.3.10.4", {"start": v(24.01, -96.58) * mm, "end": v(25.6, -99.31) * mm});
            skLineSegment(sketch, "E14.6.10.4", {"start": v(25.6, -99.31) * mm, "end": v(24.01, -102.04) * mm});
            skCircle(sketch, "E14.9.10.4", {"center": v(22.44, -99.31) * mm, "radius": 2.73 * mm, "construction": true});
            skLineSegment(sketch, "E14.11.10.4", {"start": v(24.01, -102.04) * mm, "end": v(20.86, -102.04) * mm});
            skLineSegment(sketch, "E14.14.10.4", {"start": v(20.86, -102.04) * mm, "end": v(19.28, -99.31) * mm});
            skLineSegment(sketch, "E14.17.10.4", {"start": v(19.28, -99.31) * mm, "end": v(20.86, -96.58) * mm});
            skLineSegment(sketch, "E14.0.10.5", {"start": v(20.86, -87.95) * mm, "end": v(24.01, -87.95) * mm});
            skLineSegment(sketch, "E14.3.10.5", {"start": v(24.01, -87.95) * mm, "end": v(25.6, -90.68) * mm});
            skLineSegment(sketch, "E14.6.10.5", {"start": v(25.6, -90.68) * mm, "end": v(24.01, -93.4) * mm});
            skCircle(sketch, "E14.9.10.5", {"center": v(22.44, -90.68) * mm, "radius": 2.73 * mm, "construction": true});
            skLineSegment(sketch, "E14.11.10.5", {"start": v(24.01, -93.4) * mm, "end": v(20.86, -93.4) * mm});
            skLineSegment(sketch, "E14.14.10.5", {"start": v(20.86, -93.4) * mm, "end": v(19.28, -90.68) * mm});
            skLineSegment(sketch, "E14.17.10.5", {"start": v(19.28, -90.68) * mm, "end": v(20.86, -87.95) * mm});
            skLineSegment(sketch, "E14.0.10.6", {"start": v(20.86, -79.31) * mm, "end": v(24.01, -79.31) * mm});
            skLineSegment(sketch, "E14.3.10.6", {"start": v(24.01, -79.31) * mm, "end": v(25.6, -82.04) * mm});
            skLineSegment(sketch, "E14.6.10.6", {"start": v(25.6, -82.04) * mm, "end": v(24.01, -84.77) * mm});
            skCircle(sketch, "E14.9.10.6", {"center": v(22.44, -82.04) * mm, "radius": 2.73 * mm, "construction": true});
            skLineSegment(sketch, "E14.11.10.6", {"start": v(24.01, -84.77) * mm, "end": v(20.86, -84.77) * mm});
            skLineSegment(sketch, "E14.14.10.6", {"start": v(20.86, -84.77) * mm, "end": v(19.28, -82.04) * mm});
            skLineSegment(sketch, "E14.17.10.6", {"start": v(19.28, -82.04) * mm, "end": v(20.86, -79.31) * mm});
            skLineSegment(sketch, "E14.0.10.7", {"start": v(20.86, -70.68) * mm, "end": v(24.01, -70.68) * mm});
            skLineSegment(sketch, "E14.3.10.7", {"start": v(24.01, -70.68) * mm, "end": v(25.6, -73.4) * mm});
            skLineSegment(sketch, "E14.6.10.7", {"start": v(25.6, -73.4) * mm, "end": v(24.01, -76.14) * mm});
            skCircle(sketch, "E14.9.10.7", {"center": v(22.44, -73.4) * mm, "radius": 2.73 * mm, "construction": true});
            skLineSegment(sketch, "E14.11.10.7", {"start": v(24.01, -76.14) * mm, "end": v(20.86, -76.14) * mm});
            skLineSegment(sketch, "E14.14.10.7", {"start": v(20.86, -76.14) * mm, "end": v(19.28, -73.4) * mm});
            skLineSegment(sketch, "E14.17.10.7", {"start": v(19.28, -73.4) * mm, "end": v(20.86, -70.68) * mm});
            skLineSegment(sketch, "E14.0.10.8", {"start": v(20.86, -62.04) * mm, "end": v(24.01, -62.04) * mm});
            skLineSegment(sketch, "E14.3.10.8", {"start": v(24.01, -62.04) * mm, "end": v(25.6, -64.77) * mm});
            skLineSegment(sketch, "E14.6.10.8", {"start": v(25.6, -64.77) * mm, "end": v(24.01, -67.5) * mm});
            skCircle(sketch, "E14.9.10.8", {"center": v(22.44, -64.77) * mm, "radius": 2.73 * mm, "construction": true});
            skLineSegment(sketch, "E14.11.10.8", {"start": v(24.01, -67.5) * mm, "end": v(20.86, -67.5) * mm});
            skLineSegment(sketch, "E14.14.10.8", {"start": v(20.86, -67.5) * mm, "end": v(19.28, -64.77) * mm});
            skLineSegment(sketch, "E14.17.10.8", {"start": v(19.28, -64.77) * mm, "end": v(20.86, -62.04) * mm});
            skLineSegment(sketch, "E14.0.10.9", {"start": v(20.86, -53.4) * mm, "end": v(24.01, -53.4) * mm});
            skLineSegment(sketch, "E14.3.10.9", {"start": v(24.01, -53.4) * mm, "end": v(25.6, -56.13) * mm});
            skLineSegment(sketch, "E14.6.10.9", {"start": v(25.6, -56.13) * mm, "end": v(24.01, -58.86) * mm});
            skCircle(sketch, "E14.9.10.9", {"center": v(22.44, -56.13) * mm, "radius": 2.73 * mm, "construction": true});
            skLineSegment(sketch, "E14.11.10.9", {"start": v(24.01, -58.86) * mm, "end": v(20.86, -58.86) * mm});
            skLineSegment(sketch, "E14.14.10.9", {"start": v(20.86, -58.86) * mm, "end": v(19.28, -56.13) * mm});
            skLineSegment(sketch, "E14.17.10.9", {"start": v(19.28, -56.13) * mm, "end": v(20.86, -53.4) * mm});
            skLineSegment(sketch, "E14.0.10.10", {"start": v(20.86, -44.77) * mm, "end": v(24.01, -44.77) * mm});
            skLineSegment(sketch, "E14.3.10.10", {"start": v(24.01, -44.77) * mm, "end": v(25.6, -47.5) * mm});
            skLineSegment(sketch, "E14.6.10.10", {"start": v(25.6, -47.5) * mm, "end": v(24.01, -50.23) * mm});
            skCircle(sketch, "E14.9.10.10", {"center": v(22.44, -47.5) * mm, "radius": 2.73 * mm, "construction": true});
            skLineSegment(sketch, "E14.11.10.10", {"start": v(24.01, -50.23) * mm, "end": v(20.86, -50.23) * mm});
            skLineSegment(sketch, "E14.14.10.10", {"start": v(20.86, -50.23) * mm, "end": v(19.28, -47.5) * mm});
            skLineSegment(sketch, "E14.17.10.10", {"start": v(19.28, -47.5) * mm, "end": v(20.86, -44.77) * mm});
            skLineSegment(sketch, "E14.0.10.11", {"start": v(20.86, -36.13) * mm, "end": v(24.01, -36.13) * mm});
            skLineSegment(sketch, "E14.3.10.11", {"start": v(24.01, -36.13) * mm, "end": v(25.6, -38.86) * mm});
            skLineSegment(sketch, "E14.6.10.11", {"start": v(25.6, -38.86) * mm, "end": v(24.01, -41.6) * mm});
            skCircle(sketch, "E14.9.10.11", {"center": v(22.44, -38.86) * mm, "radius": 2.73 * mm, "construction": true});
            skLineSegment(sketch, "E14.11.10.11", {"start": v(24.01, -41.6) * mm, "end": v(20.86, -41.6) * mm});
            skLineSegment(sketch, "E14.14.10.11", {"start": v(20.86, -41.6) * mm, "end": v(19.28, -38.86) * mm});
            skLineSegment(sketch, "E14.17.10.11", {"start": v(19.28, -38.86) * mm, "end": v(20.86, -36.13) * mm});
            skLineSegment(sketch, "E14.0.10.12", {"start": v(20.86, -27.5) * mm, "end": v(24.01, -27.5) * mm});
            skLineSegment(sketch, "E14.3.10.12", {"start": v(24.01, -27.5) * mm, "end": v(25.6, -30.23) * mm});
            skLineSegment(sketch, "E14.6.10.12", {"start": v(25.6, -30.23) * mm, "end": v(24.01, -32.96) * mm});
            skCircle(sketch, "E14.9.10.12", {"center": v(22.44, -30.23) * mm, "radius": 2.73 * mm, "construction": true});
            skLineSegment(sketch, "E14.11.10.12", {"start": v(24.01, -32.96) * mm, "end": v(20.86, -32.96) * mm});
            skLineSegment(sketch, "E14.14.10.12", {"start": v(20.86, -32.96) * mm, "end": v(19.28, -30.23) * mm});
            skLineSegment(sketch, "E14.17.10.12", {"start": v(19.28, -30.23) * mm, "end": v(20.86, -27.5) * mm});
            skLineSegment(sketch, "E14.0.10.13", {"start": v(20.86, -18.86) * mm, "end": v(24.01, -18.86) * mm});
            skLineSegment(sketch, "E14.3.10.13", {"start": v(24.01, -18.86) * mm, "end": v(25.6, -21.6) * mm});
            skLineSegment(sketch, "E14.6.10.13", {"start": v(25.6, -21.6) * mm, "end": v(24.01, -24.32) * mm});
            skCircle(sketch, "E14.9.10.13", {"center": v(22.44, -21.6) * mm, "radius": 2.73 * mm, "construction": true});
            skLineSegment(sketch, "E14.11.10.13", {"start": v(24.01, -24.32) * mm, "end": v(20.86, -24.32) * mm});
            skLineSegment(sketch, "E14.14.10.13", {"start": v(20.86, -24.32) * mm, "end": v(19.28, -21.6) * mm});
            skLineSegment(sketch, "E14.17.10.13", {"start": v(19.28, -21.59) * mm, "end": v(20.86, -18.86) * mm});
            skLineSegment(sketch, "E14.0.10.14", {"start": v(20.86, -10.22) * mm, "end": v(24.01, -10.22) * mm});
            skLineSegment(sketch, "E14.3.10.14", {"start": v(24.01, -10.22) * mm, "end": v(25.6, -12.95) * mm});
            skLineSegment(sketch, "E14.6.10.14", {"start": v(25.6, -12.95) * mm, "end": v(24.01, -15.68) * mm});
            skCircle(sketch, "E14.9.10.14", {"center": v(22.44, -12.95) * mm, "radius": 2.73 * mm, "construction": true});
            skLineSegment(sketch, "E14.11.10.14", {"start": v(24.01, -15.68) * mm, "end": v(20.86, -15.68) * mm});
            skLineSegment(sketch, "E14.14.10.14", {"start": v(20.86, -15.68) * mm, "end": v(19.28, -12.95) * mm});
            skLineSegment(sketch, "E14.17.10.14", {"start": v(19.28, -12.95) * mm, "end": v(20.86, -10.22) * mm});
            skLineSegment(sketch, "E14.0.10.15", {"start": v(20.86, -1.59) * mm, "end": v(24.01, -1.59) * mm});
            skLineSegment(sketch, "E14.3.10.15", {"start": v(24.01, -1.59) * mm, "end": v(25.6, -4.32) * mm});
            skLineSegment(sketch, "E14.6.10.15", {"start": v(25.6, -4.32) * mm, "end": v(24.01, -7.05) * mm});
            skCircle(sketch, "E14.9.10.15", {"center": v(22.44, -4.32) * mm, "radius": 2.73 * mm, "construction": true});
            skLineSegment(sketch, "E14.11.10.15", {"start": v(24.01, -7.05) * mm, "end": v(20.86, -7.05) * mm});
            skLineSegment(sketch, "E14.14.10.15", {"start": v(20.86, -7.05) * mm, "end": v(19.28, -4.32) * mm});
            skLineSegment(sketch, "E14.17.10.15", {"start": v(19.28, -4.32) * mm, "end": v(20.86, -1.59) * mm});
            skLineSegment(sketch, "E14.0.10.16", {"start": v(20.86, 7.05) * mm, "end": v(24.01, 7.05) * mm});
            skLineSegment(sketch, "E14.3.10.16", {"start": v(24.01, 7.05) * mm, "end": v(25.6, 4.32) * mm});
            skLineSegment(sketch, "E14.6.10.16", {"start": v(25.6, 4.32) * mm, "end": v(24.01, 1.59) * mm});
            skCircle(sketch, "E14.9.10.16", {"center": v(22.44, 4.32) * mm, "radius": 2.73 * mm, "construction": true});
            skLineSegment(sketch, "E14.11.10.16", {"start": v(24.01, 1.59) * mm, "end": v(20.86, 1.59) * mm});
            skLineSegment(sketch, "E14.14.10.16", {"start": v(20.86, 1.59) * mm, "end": v(19.28, 4.32) * mm});
            skLineSegment(sketch, "E14.17.10.16", {"start": v(19.28, 4.32) * mm, "end": v(20.86, 7.05) * mm});
            skLineSegment(sketch, "E14.0.10.17", {"start": v(20.86, 15.68) * mm, "end": v(24.01, 15.68) * mm});
            skLineSegment(sketch, "E14.3.10.17", {"start": v(24.01, 15.68) * mm, "end": v(25.6, 12.95) * mm});
            skLineSegment(sketch, "E14.6.10.17", {"start": v(25.6, 12.95) * mm, "end": v(24.01, 10.22) * mm});
            skCircle(sketch, "E14.9.10.17", {"center": v(22.44, 12.95) * mm, "radius": 2.73 * mm, "construction": true});
            skLineSegment(sketch, "E14.11.10.17", {"start": v(24.01, 10.22) * mm, "end": v(20.86, 10.22) * mm});
            skLineSegment(sketch, "E14.14.10.17", {"start": v(20.86, 10.22) * mm, "end": v(19.28, 12.95) * mm});
            skLineSegment(sketch, "E14.17.10.17", {"start": v(19.28, 12.95) * mm, "end": v(20.86, 15.68) * mm});
            skLineSegment(sketch, "E14.0.10.18", {"start": v(20.86, 24.32) * mm, "end": v(24.01, 24.32) * mm});
            skLineSegment(sketch, "E14.3.10.18", {"start": v(24.01, 24.32) * mm, "end": v(25.6, 21.59) * mm});
            skLineSegment(sketch, "E14.6.10.18", {"start": v(25.6, 21.59) * mm, "end": v(24.01, 18.86) * mm});
            skCircle(sketch, "E14.9.10.18", {"center": v(22.44, 21.59) * mm, "radius": 2.73 * mm, "construction": true});
            skLineSegment(sketch, "E14.11.10.18", {"start": v(24.01, 18.86) * mm, "end": v(20.86, 18.86) * mm});
            skLineSegment(sketch, "E14.14.10.18", {"start": v(20.86, 18.86) * mm, "end": v(19.28, 21.59) * mm});
            skLineSegment(sketch, "E14.17.10.18", {"start": v(19.28, 21.6) * mm, "end": v(20.86, 24.32) * mm});
            skLineSegment(sketch, "E14.0.10.19", {"start": v(20.86, 32.96) * mm, "end": v(24.01, 32.96) * mm});
            skLineSegment(sketch, "E14.3.10.19", {"start": v(24.01, 32.96) * mm, "end": v(25.6, 30.23) * mm});
            skLineSegment(sketch, "E14.6.10.19", {"start": v(25.6, 30.23) * mm, "end": v(24.01, 27.5) * mm});
            skCircle(sketch, "E14.9.10.19", {"center": v(22.44, 30.23) * mm, "radius": 2.73 * mm, "construction": true});
            skLineSegment(sketch, "E14.11.10.19", {"start": v(24.01, 27.5) * mm, "end": v(20.86, 27.5) * mm});
            skLineSegment(sketch, "E14.14.10.19", {"start": v(20.86, 27.5) * mm, "end": v(19.28, 30.23) * mm});
            skLineSegment(sketch, "E14.17.10.19", {"start": v(19.28, 30.23) * mm, "end": v(20.86, 32.96) * mm});
            skLineSegment(sketch, "E14.0.11.0", {"start": v(35.82, -131.13) * mm, "end": v(38.97, -131.13) * mm});
            skLineSegment(sketch, "E14.3.11.0", {"start": v(38.97, -131.13) * mm, "end": v(40.55, -133.86) * mm});
            skLineSegment(sketch, "E14.6.11.0", {"start": v(40.55, -133.86) * mm, "end": v(38.97, -136.59) * mm});
            skCircle(sketch, "E14.9.11.0", {"center": v(37.4, -133.86) * mm, "radius": 2.73 * mm, "construction": true});
            skLineSegment(sketch, "E14.11.11.0", {"start": v(38.97, -136.59) * mm, "end": v(35.82, -136.59) * mm});
            skLineSegment(sketch, "E14.14.11.0", {"start": v(35.82, -136.59) * mm, "end": v(34.24, -133.86) * mm});
            skLineSegment(sketch, "E14.17.11.0", {"start": v(34.24, -133.86) * mm, "end": v(35.82, -131.13) * mm});
            skLineSegment(sketch, "E14.0.11.1", {"start": v(35.82, -122.5) * mm, "end": v(38.97, -122.5) * mm});
            skLineSegment(sketch, "E14.3.11.1", {"start": v(38.97, -122.5) * mm, "end": v(40.55, -125.22) * mm});
            skLineSegment(sketch, "E14.6.11.1", {"start": v(40.55, -125.22) * mm, "end": v(38.97, -127.95) * mm});
            skCircle(sketch, "E14.9.11.1", {"center": v(37.4, -125.22) * mm, "radius": 2.73 * mm, "construction": true});
            skLineSegment(sketch, "E14.11.11.1", {"start": v(38.97, -127.95) * mm, "end": v(35.82, -127.95) * mm});
            skLineSegment(sketch, "E14.14.11.1", {"start": v(35.82, -127.95) * mm, "end": v(34.24, -125.22) * mm});
            skLineSegment(sketch, "E14.17.11.1", {"start": v(34.24, -125.22) * mm, "end": v(35.82, -122.5) * mm});
            skLineSegment(sketch, "E14.0.11.2", {"start": v(35.82, -113.86) * mm, "end": v(38.97, -113.86) * mm});
            skLineSegment(sketch, "E14.3.11.2", {"start": v(38.97, -113.86) * mm, "end": v(40.55, -116.59) * mm});
            skLineSegment(sketch, "E14.6.11.2", {"start": v(40.55, -116.59) * mm, "end": v(38.97, -119.32) * mm});
            skCircle(sketch, "E14.9.11.2", {"center": v(37.4, -116.59) * mm, "radius": 2.73 * mm, "construction": true});
            skLineSegment(sketch, "E14.11.11.2", {"start": v(38.97, -119.32) * mm, "end": v(35.82, -119.32) * mm});
            skLineSegment(sketch, "E14.14.11.2", {"start": v(35.82, -119.32) * mm, "end": v(34.24, -116.59) * mm});
            skLineSegment(sketch, "E14.17.11.2", {"start": v(34.24, -116.59) * mm, "end": v(35.82, -113.86) * mm});
            skLineSegment(sketch, "E14.0.11.3", {"start": v(35.82, -105.22) * mm, "end": v(38.97, -105.22) * mm});
            skLineSegment(sketch, "E14.3.11.3", {"start": v(38.97, -105.22) * mm, "end": v(40.55, -107.95) * mm});
            skLineSegment(sketch, "E14.6.11.3", {"start": v(40.55, -107.95) * mm, "end": v(38.97, -110.68) * mm});
            skCircle(sketch, "E14.9.11.3", {"center": v(37.4, -107.95) * mm, "radius": 2.73 * mm, "construction": true});
            skLineSegment(sketch, "E14.11.11.3", {"start": v(38.97, -110.68) * mm, "end": v(35.82, -110.68) * mm});
            skLineSegment(sketch, "E14.14.11.3", {"start": v(35.82, -110.68) * mm, "end": v(34.24, -107.95) * mm});
            skLineSegment(sketch, "E14.17.11.3", {"start": v(34.24, -107.95) * mm, "end": v(35.82, -105.22) * mm});
            skLineSegment(sketch, "E14.0.11.4", {"start": v(35.82, -96.58) * mm, "end": v(38.97, -96.58) * mm});
            skLineSegment(sketch, "E14.3.11.4", {"start": v(38.97, -96.58) * mm, "end": v(40.55, -99.31) * mm});
            skLineSegment(sketch, "E14.6.11.4", {"start": v(40.55, -99.31) * mm, "end": v(38.97, -102.04) * mm});
            skCircle(sketch, "E14.9.11.4", {"center": v(37.4, -99.31) * mm, "radius": 2.73 * mm, "construction": true});
            skLineSegment(sketch, "E14.11.11.4", {"start": v(38.97, -102.04) * mm, "end": v(35.82, -102.04) * mm});
            skLineSegment(sketch, "E14.14.11.4", {"start": v(35.82, -102.04) * mm, "end": v(34.24, -99.31) * mm});
            skLineSegment(sketch, "E14.17.11.4", {"start": v(34.24, -99.31) * mm, "end": v(35.82, -96.58) * mm});
            skLineSegment(sketch, "E14.0.11.5", {"start": v(35.82, -87.95) * mm, "end": v(38.97, -87.95) * mm});
            skLineSegment(sketch, "E14.3.11.5", {"start": v(38.97, -87.95) * mm, "end": v(40.55, -90.68) * mm});
            skLineSegment(sketch, "E14.6.11.5", {"start": v(40.55, -90.68) * mm, "end": v(38.97, -93.4) * mm});
            skCircle(sketch, "E14.9.11.5", {"center": v(37.4, -90.68) * mm, "radius": 2.73 * mm, "construction": true});
            skLineSegment(sketch, "E14.11.11.5", {"start": v(38.97, -93.4) * mm, "end": v(35.82, -93.4) * mm});
            skLineSegment(sketch, "E14.14.11.5", {"start": v(35.82, -93.4) * mm, "end": v(34.24, -90.68) * mm});
            skLineSegment(sketch, "E14.17.11.5", {"start": v(34.24, -90.68) * mm, "end": v(35.82, -87.95) * mm});
            skLineSegment(sketch, "E14.0.11.6", {"start": v(35.82, -79.31) * mm, "end": v(38.97, -79.31) * mm});
            skLineSegment(sketch, "E14.3.11.6", {"start": v(38.97, -79.31) * mm, "end": v(40.55, -82.04) * mm});
            skLineSegment(sketch, "E14.6.11.6", {"start": v(40.55, -82.04) * mm, "end": v(38.97, -84.77) * mm});
            skCircle(sketch, "E14.9.11.6", {"center": v(37.4, -82.04) * mm, "radius": 2.73 * mm, "construction": true});
            skLineSegment(sketch, "E14.11.11.6", {"start": v(38.97, -84.77) * mm, "end": v(35.82, -84.77) * mm});
            skLineSegment(sketch, "E14.14.11.6", {"start": v(35.82, -84.77) * mm, "end": v(34.24, -82.04) * mm});
            skLineSegment(sketch, "E14.17.11.6", {"start": v(34.24, -82.04) * mm, "end": v(35.82, -79.31) * mm});
            skLineSegment(sketch, "E14.0.11.7", {"start": v(35.82, -70.68) * mm, "end": v(38.97, -70.68) * mm});
            skLineSegment(sketch, "E14.3.11.7", {"start": v(38.97, -70.68) * mm, "end": v(40.55, -73.4) * mm});
            skLineSegment(sketch, "E14.6.11.7", {"start": v(40.55, -73.4) * mm, "end": v(38.97, -76.14) * mm});
            skCircle(sketch, "E14.9.11.7", {"center": v(37.4, -73.4) * mm, "radius": 2.73 * mm, "construction": true});
            skLineSegment(sketch, "E14.11.11.7", {"start": v(38.97, -76.14) * mm, "end": v(35.82, -76.14) * mm});
            skLineSegment(sketch, "E14.14.11.7", {"start": v(35.82, -76.14) * mm, "end": v(34.24, -73.4) * mm});
            skLineSegment(sketch, "E14.17.11.7", {"start": v(34.24, -73.4) * mm, "end": v(35.82, -70.68) * mm});
            skLineSegment(sketch, "E14.0.11.8", {"start": v(35.82, -62.04) * mm, "end": v(38.97, -62.04) * mm});
            skLineSegment(sketch, "E14.3.11.8", {"start": v(38.97, -62.04) * mm, "end": v(40.55, -64.77) * mm});
            skLineSegment(sketch, "E14.6.11.8", {"start": v(40.55, -64.77) * mm, "end": v(38.97, -67.5) * mm});
            skCircle(sketch, "E14.9.11.8", {"center": v(37.4, -64.77) * mm, "radius": 2.73 * mm, "construction": true});
            skLineSegment(sketch, "E14.11.11.8", {"start": v(38.97, -67.5) * mm, "end": v(35.82, -67.5) * mm});
            skLineSegment(sketch, "E14.14.11.8", {"start": v(35.82, -67.5) * mm, "end": v(34.24, -64.77) * mm});
            skLineSegment(sketch, "E14.17.11.8", {"start": v(34.24, -64.77) * mm, "end": v(35.82, -62.04) * mm});
            skLineSegment(sketch, "E14.0.11.9", {"start": v(35.82, -53.4) * mm, "end": v(38.97, -53.4) * mm});
            skLineSegment(sketch, "E14.3.11.9", {"start": v(38.97, -53.4) * mm, "end": v(40.55, -56.13) * mm});
            skLineSegment(sketch, "E14.6.11.9", {"start": v(40.55, -56.13) * mm, "end": v(38.97, -58.86) * mm});
            skCircle(sketch, "E14.9.11.9", {"center": v(37.4, -56.13) * mm, "radius": 2.73 * mm, "construction": true});
            skLineSegment(sketch, "E14.11.11.9", {"start": v(38.97, -58.86) * mm, "end": v(35.82, -58.86) * mm});
            skLineSegment(sketch, "E14.14.11.9", {"start": v(35.82, -58.86) * mm, "end": v(34.24, -56.13) * mm});
            skLineSegment(sketch, "E14.17.11.9", {"start": v(34.24, -56.13) * mm, "end": v(35.82, -53.4) * mm});
            skLineSegment(sketch, "E14.0.11.10", {"start": v(35.82, -44.77) * mm, "end": v(38.97, -44.77) * mm});
            skLineSegment(sketch, "E14.3.11.10", {"start": v(38.97, -44.77) * mm, "end": v(40.55, -47.5) * mm});
            skLineSegment(sketch, "E14.6.11.10", {"start": v(40.55, -47.5) * mm, "end": v(38.97, -50.23) * mm});
            skCircle(sketch, "E14.9.11.10", {"center": v(37.4, -47.5) * mm, "radius": 2.73 * mm, "construction": true});
            skLineSegment(sketch, "E14.11.11.10", {"start": v(38.97, -50.23) * mm, "end": v(35.82, -50.23) * mm});
            skLineSegment(sketch, "E14.14.11.10", {"start": v(35.82, -50.23) * mm, "end": v(34.24, -47.5) * mm});
            skLineSegment(sketch, "E14.17.11.10", {"start": v(34.24, -47.5) * mm, "end": v(35.82, -44.77) * mm});
            skLineSegment(sketch, "E14.0.11.11", {"start": v(35.82, -36.13) * mm, "end": v(38.97, -36.13) * mm});
            skLineSegment(sketch, "E14.3.11.11", {"start": v(38.97, -36.13) * mm, "end": v(40.55, -38.86) * mm});
            skLineSegment(sketch, "E14.6.11.11", {"start": v(40.55, -38.86) * mm, "end": v(38.97, -41.6) * mm});
            skCircle(sketch, "E14.9.11.11", {"center": v(37.4, -38.86) * mm, "radius": 2.73 * mm, "construction": true});
            skLineSegment(sketch, "E14.11.11.11", {"start": v(38.97, -41.6) * mm, "end": v(35.82, -41.6) * mm});
            skLineSegment(sketch, "E14.14.11.11", {"start": v(35.82, -41.6) * mm, "end": v(34.24, -38.86) * mm});
            skLineSegment(sketch, "E14.17.11.11", {"start": v(34.24, -38.86) * mm, "end": v(35.82, -36.13) * mm});
            skLineSegment(sketch, "E14.0.11.12", {"start": v(35.82, -27.5) * mm, "end": v(38.97, -27.5) * mm});
            skLineSegment(sketch, "E14.3.11.12", {"start": v(38.97, -27.5) * mm, "end": v(40.55, -30.23) * mm});
            skLineSegment(sketch, "E14.6.11.12", {"start": v(40.55, -30.23) * mm, "end": v(38.97, -32.96) * mm});
            skCircle(sketch, "E14.9.11.12", {"center": v(37.4, -30.23) * mm, "radius": 2.73 * mm, "construction": true});
            skLineSegment(sketch, "E14.11.11.12", {"start": v(38.97, -32.96) * mm, "end": v(35.82, -32.96) * mm});
            skLineSegment(sketch, "E14.14.11.12", {"start": v(35.82, -32.96) * mm, "end": v(34.24, -30.23) * mm});
            skLineSegment(sketch, "E14.17.11.12", {"start": v(34.24, -30.23) * mm, "end": v(35.82, -27.5) * mm});
            skLineSegment(sketch, "E14.0.11.13", {"start": v(35.82, -18.86) * mm, "end": v(38.97, -18.86) * mm});
            skLineSegment(sketch, "E14.3.11.13", {"start": v(38.97, -18.86) * mm, "end": v(40.55, -21.6) * mm});
            skLineSegment(sketch, "E14.6.11.13", {"start": v(40.55, -21.6) * mm, "end": v(38.97, -24.32) * mm});
            skCircle(sketch, "E14.9.11.13", {"center": v(37.4, -21.6) * mm, "radius": 2.73 * mm, "construction": true});
            skLineSegment(sketch, "E14.11.11.13", {"start": v(38.97, -24.32) * mm, "end": v(35.82, -24.32) * mm});
            skLineSegment(sketch, "E14.14.11.13", {"start": v(35.82, -24.32) * mm, "end": v(34.24, -21.6) * mm});
            skLineSegment(sketch, "E14.17.11.13", {"start": v(34.24, -21.6) * mm, "end": v(35.82, -18.86) * mm});
            skLineSegment(sketch, "E14.0.11.14", {"start": v(35.82, -10.22) * mm, "end": v(38.97, -10.22) * mm});
            skLineSegment(sketch, "E14.3.11.14", {"start": v(38.97, -10.22) * mm, "end": v(40.55, -12.95) * mm});
            skLineSegment(sketch, "E14.6.11.14", {"start": v(40.55, -12.95) * mm, "end": v(38.97, -15.68) * mm});
            skCircle(sketch, "E14.9.11.14", {"center": v(37.4, -12.95) * mm, "radius": 2.73 * mm, "construction": true});
            skLineSegment(sketch, "E14.11.11.14", {"start": v(38.97, -15.68) * mm, "end": v(35.82, -15.68) * mm});
            skLineSegment(sketch, "E14.14.11.14", {"start": v(35.82, -15.68) * mm, "end": v(34.24, -12.95) * mm});
            skLineSegment(sketch, "E14.17.11.14", {"start": v(34.24, -12.95) * mm, "end": v(35.82, -10.22) * mm});
            skLineSegment(sketch, "E14.0.11.15", {"start": v(35.82, -1.59) * mm, "end": v(38.97, -1.59) * mm});
            skLineSegment(sketch, "E14.3.11.15", {"start": v(38.97, -1.59) * mm, "end": v(40.55, -4.32) * mm});
            skLineSegment(sketch, "E14.6.11.15", {"start": v(40.55, -4.32) * mm, "end": v(38.97, -7.05) * mm});
            skCircle(sketch, "E14.9.11.15", {"center": v(37.4, -4.32) * mm, "radius": 2.73 * mm, "construction": true});
            skLineSegment(sketch, "E14.11.11.15", {"start": v(38.97, -7.05) * mm, "end": v(35.82, -7.05) * mm});
            skLineSegment(sketch, "E14.14.11.15", {"start": v(35.82, -7.05) * mm, "end": v(34.24, -4.32) * mm});
            skLineSegment(sketch, "E14.17.11.15", {"start": v(34.24, -4.32) * mm, "end": v(35.82, -1.59) * mm});
            skLineSegment(sketch, "E14.0.11.16", {"start": v(35.82, 7.05) * mm, "end": v(38.97, 7.05) * mm});
            skLineSegment(sketch, "E14.3.11.16", {"start": v(38.97, 7.05) * mm, "end": v(40.55, 4.32) * mm});
            skLineSegment(sketch, "E14.6.11.16", {"start": v(40.55, 4.32) * mm, "end": v(38.97, 1.59) * mm});
            skCircle(sketch, "E14.9.11.16", {"center": v(37.4, 4.32) * mm, "radius": 2.73 * mm, "construction": true});
            skLineSegment(sketch, "E14.11.11.16", {"start": v(38.97, 1.59) * mm, "end": v(35.82, 1.59) * mm});
            skLineSegment(sketch, "E14.14.11.16", {"start": v(35.82, 1.59) * mm, "end": v(34.24, 4.32) * mm});
            skLineSegment(sketch, "E14.17.11.16", {"start": v(34.24, 4.32) * mm, "end": v(35.82, 7.05) * mm});
            skLineSegment(sketch, "E14.0.11.17", {"start": v(35.82, 15.68) * mm, "end": v(38.97, 15.68) * mm});
            skLineSegment(sketch, "E14.3.11.17", {"start": v(38.97, 15.68) * mm, "end": v(40.55, 12.95) * mm});
            skLineSegment(sketch, "E14.6.11.17", {"start": v(40.55, 12.95) * mm, "end": v(38.97, 10.22) * mm});
            skCircle(sketch, "E14.9.11.17", {"center": v(37.4, 12.95) * mm, "radius": 2.73 * mm, "construction": true});
            skLineSegment(sketch, "E14.11.11.17", {"start": v(38.97, 10.22) * mm, "end": v(35.82, 10.22) * mm});
            skLineSegment(sketch, "E14.14.11.17", {"start": v(35.82, 10.22) * mm, "end": v(34.24, 12.95) * mm});
            skLineSegment(sketch, "E14.17.11.17", {"start": v(34.24, 12.95) * mm, "end": v(35.82, 15.68) * mm});
            skLineSegment(sketch, "E14.0.11.18", {"start": v(35.82, 24.32) * mm, "end": v(38.97, 24.32) * mm});
            skLineSegment(sketch, "E14.3.11.18", {"start": v(38.97, 24.32) * mm, "end": v(40.55, 21.59) * mm});
            skLineSegment(sketch, "E14.6.11.18", {"start": v(40.55, 21.59) * mm, "end": v(38.97, 18.86) * mm});
            skCircle(sketch, "E14.9.11.18", {"center": v(37.4, 21.59) * mm, "radius": 2.73 * mm, "construction": true});
            skLineSegment(sketch, "E14.11.11.18", {"start": v(38.97, 18.86) * mm, "end": v(35.82, 18.86) * mm});
            skLineSegment(sketch, "E14.14.11.18", {"start": v(35.82, 18.86) * mm, "end": v(34.24, 21.59) * mm});
            skLineSegment(sketch, "E14.17.11.18", {"start": v(34.24, 21.59) * mm, "end": v(35.82, 24.32) * mm});
            skLineSegment(sketch, "E14.0.11.19", {"start": v(35.82, 32.96) * mm, "end": v(38.97, 32.96) * mm});
            skLineSegment(sketch, "E14.3.11.19", {"start": v(38.97, 32.96) * mm, "end": v(40.55, 30.23) * mm});
            skLineSegment(sketch, "E14.6.11.19", {"start": v(40.55, 30.23) * mm, "end": v(38.97, 27.5) * mm});
            skCircle(sketch, "E14.9.11.19", {"center": v(37.4, 30.23) * mm, "radius": 2.73 * mm, "construction": true});
            skLineSegment(sketch, "E14.11.11.19", {"start": v(38.97, 27.5) * mm, "end": v(35.82, 27.5) * mm});
            skLineSegment(sketch, "E14.14.11.19", {"start": v(35.82, 27.5) * mm, "end": v(34.24, 30.23) * mm});
            skLineSegment(sketch, "E14.17.11.19", {"start": v(34.24, 30.23) * mm, "end": v(35.82, 32.96) * mm});
            skLineSegment(sketch, "E14.0.12.0", {"start": v(50.78, -131.13) * mm, "end": v(53.93, -131.13) * mm});
            skLineSegment(sketch, "E14.3.12.0", {"start": v(53.93, -131.13) * mm, "end": v(55.5, -133.86) * mm});
            skLineSegment(sketch, "E14.6.12.0", {"start": v(55.5, -133.86) * mm, "end": v(53.93, -136.59) * mm});
            skCircle(sketch, "E14.9.12.0", {"center": v(52.35, -133.86) * mm, "radius": 2.73 * mm, "construction": true});
            skLineSegment(sketch, "E14.11.12.0", {"start": v(53.93, -136.59) * mm, "end": v(50.78, -136.59) * mm});
            skLineSegment(sketch, "E14.14.12.0", {"start": v(50.78, -136.59) * mm, "end": v(49.2, -133.86) * mm});
            skLineSegment(sketch, "E14.17.12.0", {"start": v(49.2, -133.86) * mm, "end": v(50.78, -131.13) * mm});
            skLineSegment(sketch, "E14.0.12.1", {"start": v(50.78, -122.5) * mm, "end": v(53.93, -122.5) * mm});
            skLineSegment(sketch, "E14.3.12.1", {"start": v(53.93, -122.5) * mm, "end": v(55.5, -125.22) * mm});
            skLineSegment(sketch, "E14.6.12.1", {"start": v(55.5, -125.22) * mm, "end": v(53.93, -127.95) * mm});
            skCircle(sketch, "E14.9.12.1", {"center": v(52.35, -125.22) * mm, "radius": 2.73 * mm, "construction": true});
            skLineSegment(sketch, "E14.11.12.1", {"start": v(53.93, -127.95) * mm, "end": v(50.78, -127.95) * mm});
            skLineSegment(sketch, "E14.14.12.1", {"start": v(50.78, -127.95) * mm, "end": v(49.2, -125.22) * mm});
            skLineSegment(sketch, "E14.17.12.1", {"start": v(49.2, -125.22) * mm, "end": v(50.78, -122.5) * mm});
            skLineSegment(sketch, "E14.0.12.2", {"start": v(50.78, -113.86) * mm, "end": v(53.93, -113.86) * mm});
            skLineSegment(sketch, "E14.3.12.2", {"start": v(53.93, -113.86) * mm, "end": v(55.5, -116.59) * mm});
            skLineSegment(sketch, "E14.6.12.2", {"start": v(55.5, -116.59) * mm, "end": v(53.93, -119.32) * mm});
            skCircle(sketch, "E14.9.12.2", {"center": v(52.35, -116.59) * mm, "radius": 2.73 * mm, "construction": true});
            skLineSegment(sketch, "E14.11.12.2", {"start": v(53.93, -119.32) * mm, "end": v(50.78, -119.32) * mm});
            skLineSegment(sketch, "E14.14.12.2", {"start": v(50.78, -119.32) * mm, "end": v(49.2, -116.59) * mm});
            skLineSegment(sketch, "E14.17.12.2", {"start": v(49.2, -116.59) * mm, "end": v(50.78, -113.86) * mm});
            skLineSegment(sketch, "E14.0.12.3", {"start": v(50.78, -105.22) * mm, "end": v(53.93, -105.22) * mm});
            skLineSegment(sketch, "E14.3.12.3", {"start": v(53.93, -105.22) * mm, "end": v(55.5, -107.95) * mm});
            skLineSegment(sketch, "E14.6.12.3", {"start": v(55.5, -107.95) * mm, "end": v(53.93, -110.68) * mm});
            skCircle(sketch, "E14.9.12.3", {"center": v(52.35, -107.95) * mm, "radius": 2.73 * mm, "construction": true});
            skLineSegment(sketch, "E14.11.12.3", {"start": v(53.93, -110.68) * mm, "end": v(50.78, -110.68) * mm});
            skLineSegment(sketch, "E14.14.12.3", {"start": v(50.78, -110.68) * mm, "end": v(49.2, -107.95) * mm});
            skLineSegment(sketch, "E14.17.12.3", {"start": v(49.2, -107.95) * mm, "end": v(50.78, -105.22) * mm});
            skLineSegment(sketch, "E14.0.12.4", {"start": v(50.78, -96.58) * mm, "end": v(53.93, -96.58) * mm});
            skLineSegment(sketch, "E14.3.12.4", {"start": v(53.93, -96.58) * mm, "end": v(55.5, -99.31) * mm});
            skLineSegment(sketch, "E14.6.12.4", {"start": v(55.5, -99.31) * mm, "end": v(53.93, -102.04) * mm});
            skCircle(sketch, "E14.9.12.4", {"center": v(52.35, -99.31) * mm, "radius": 2.73 * mm, "construction": true});
            skLineSegment(sketch, "E14.11.12.4", {"start": v(53.93, -102.04) * mm, "end": v(50.78, -102.04) * mm});
            skLineSegment(sketch, "E14.14.12.4", {"start": v(50.78, -102.04) * mm, "end": v(49.2, -99.31) * mm});
            skLineSegment(sketch, "E14.17.12.4", {"start": v(49.2, -99.31) * mm, "end": v(50.78, -96.58) * mm});
            skLineSegment(sketch, "E14.0.12.5", {"start": v(50.78, -87.95) * mm, "end": v(53.93, -87.95) * mm});
            skLineSegment(sketch, "E14.3.12.5", {"start": v(53.93, -87.95) * mm, "end": v(55.5, -90.68) * mm});
            skLineSegment(sketch, "E14.6.12.5", {"start": v(55.5, -90.68) * mm, "end": v(53.93, -93.4) * mm});
            skCircle(sketch, "E14.9.12.5", {"center": v(52.35, -90.68) * mm, "radius": 2.73 * mm, "construction": true});
            skLineSegment(sketch, "E14.11.12.5", {"start": v(53.93, -93.4) * mm, "end": v(50.78, -93.4) * mm});
            skLineSegment(sketch, "E14.14.12.5", {"start": v(50.78, -93.4) * mm, "end": v(49.2, -90.68) * mm});
            skLineSegment(sketch, "E14.17.12.5", {"start": v(49.2, -90.68) * mm, "end": v(50.78, -87.95) * mm});
            skLineSegment(sketch, "E14.0.12.6", {"start": v(50.78, -79.31) * mm, "end": v(53.93, -79.31) * mm});
            skLineSegment(sketch, "E14.3.12.6", {"start": v(53.93, -79.31) * mm, "end": v(55.5, -82.04) * mm});
            skLineSegment(sketch, "E14.6.12.6", {"start": v(55.5, -82.04) * mm, "end": v(53.93, -84.77) * mm});
            skCircle(sketch, "E14.9.12.6", {"center": v(52.35, -82.04) * mm, "radius": 2.73 * mm, "construction": true});
            skLineSegment(sketch, "E14.11.12.6", {"start": v(53.93, -84.77) * mm, "end": v(50.78, -84.77) * mm});
            skLineSegment(sketch, "E14.14.12.6", {"start": v(50.78, -84.77) * mm, "end": v(49.2, -82.04) * mm});
            skLineSegment(sketch, "E14.17.12.6", {"start": v(49.2, -82.04) * mm, "end": v(50.78, -79.31) * mm});
            skLineSegment(sketch, "E14.0.12.7", {"start": v(50.78, -70.68) * mm, "end": v(53.93, -70.68) * mm});
            skLineSegment(sketch, "E14.3.12.7", {"start": v(53.93, -70.68) * mm, "end": v(55.5, -73.4) * mm});
            skLineSegment(sketch, "E14.6.12.7", {"start": v(55.5, -73.4) * mm, "end": v(53.93, -76.14) * mm});
            skCircle(sketch, "E14.9.12.7", {"center": v(52.35, -73.4) * mm, "radius": 2.73 * mm, "construction": true});
            skLineSegment(sketch, "E14.11.12.7", {"start": v(53.93, -76.14) * mm, "end": v(50.78, -76.14) * mm});
            skLineSegment(sketch, "E14.14.12.7", {"start": v(50.78, -76.14) * mm, "end": v(49.2, -73.4) * mm});
            skLineSegment(sketch, "E14.17.12.7", {"start": v(49.2, -73.4) * mm, "end": v(50.78, -70.68) * mm});
            skLineSegment(sketch, "E14.0.12.8", {"start": v(50.78, -62.04) * mm, "end": v(53.93, -62.04) * mm});
            skLineSegment(sketch, "E14.3.12.8", {"start": v(53.93, -62.04) * mm, "end": v(55.5, -64.77) * mm});
            skLineSegment(sketch, "E14.6.12.8", {"start": v(55.5, -64.77) * mm, "end": v(53.93, -67.5) * mm});
            skCircle(sketch, "E14.9.12.8", {"center": v(52.35, -64.77) * mm, "radius": 2.73 * mm, "construction": true});
            skLineSegment(sketch, "E14.11.12.8", {"start": v(53.93, -67.5) * mm, "end": v(50.78, -67.5) * mm});
            skLineSegment(sketch, "E14.14.12.8", {"start": v(50.78, -67.5) * mm, "end": v(49.2, -64.77) * mm});
            skLineSegment(sketch, "E14.17.12.8", {"start": v(49.2, -64.77) * mm, "end": v(50.78, -62.04) * mm});
            skLineSegment(sketch, "E14.0.12.9", {"start": v(50.78, -53.4) * mm, "end": v(53.93, -53.4) * mm});
            skLineSegment(sketch, "E14.3.12.9", {"start": v(53.93, -53.4) * mm, "end": v(55.5, -56.13) * mm});
            skLineSegment(sketch, "E14.6.12.9", {"start": v(55.5, -56.13) * mm, "end": v(53.93, -58.86) * mm});
            skCircle(sketch, "E14.9.12.9", {"center": v(52.35, -56.13) * mm, "radius": 2.73 * mm, "construction": true});
            skLineSegment(sketch, "E14.11.12.9", {"start": v(53.93, -58.86) * mm, "end": v(50.78, -58.86) * mm});
            skLineSegment(sketch, "E14.14.12.9", {"start": v(50.78, -58.86) * mm, "end": v(49.2, -56.13) * mm});
            skLineSegment(sketch, "E14.17.12.9", {"start": v(49.2, -56.13) * mm, "end": v(50.78, -53.4) * mm});
            skLineSegment(sketch, "E14.0.12.10", {"start": v(50.78, -44.77) * mm, "end": v(53.93, -44.77) * mm});
            skLineSegment(sketch, "E14.3.12.10", {"start": v(53.93, -44.77) * mm, "end": v(55.5, -47.5) * mm});
            skLineSegment(sketch, "E14.6.12.10", {"start": v(55.5, -47.5) * mm, "end": v(53.93, -50.23) * mm});
            skCircle(sketch, "E14.9.12.10", {"center": v(52.35, -47.5) * mm, "radius": 2.73 * mm, "construction": true});
            skLineSegment(sketch, "E14.11.12.10", {"start": v(53.93, -50.23) * mm, "end": v(50.78, -50.23) * mm});
            skLineSegment(sketch, "E14.14.12.10", {"start": v(50.78, -50.23) * mm, "end": v(49.2, -47.5) * mm});
            skLineSegment(sketch, "E14.17.12.10", {"start": v(49.2, -47.5) * mm, "end": v(50.78, -44.77) * mm});
            skLineSegment(sketch, "E14.0.12.11", {"start": v(50.78, -36.13) * mm, "end": v(53.93, -36.13) * mm});
            skLineSegment(sketch, "E14.3.12.11", {"start": v(53.93, -36.13) * mm, "end": v(55.5, -38.86) * mm});
            skLineSegment(sketch, "E14.6.12.11", {"start": v(55.5, -38.86) * mm, "end": v(53.93, -41.6) * mm});
            skCircle(sketch, "E14.9.12.11", {"center": v(52.35, -38.86) * mm, "radius": 2.73 * mm, "construction": true});
            skLineSegment(sketch, "E14.11.12.11", {"start": v(53.93, -41.6) * mm, "end": v(50.78, -41.6) * mm});
            skLineSegment(sketch, "E14.14.12.11", {"start": v(50.78, -41.6) * mm, "end": v(49.2, -38.86) * mm});
            skLineSegment(sketch, "E14.17.12.11", {"start": v(49.2, -38.86) * mm, "end": v(50.78, -36.13) * mm});
            skLineSegment(sketch, "E14.0.12.12", {"start": v(50.78, -27.5) * mm, "end": v(53.93, -27.5) * mm});
            skLineSegment(sketch, "E14.3.12.12", {"start": v(53.93, -27.5) * mm, "end": v(55.5, -30.23) * mm});
            skLineSegment(sketch, "E14.6.12.12", {"start": v(55.5, -30.23) * mm, "end": v(53.93, -32.96) * mm});
            skCircle(sketch, "E14.9.12.12", {"center": v(52.35, -30.23) * mm, "radius": 2.73 * mm, "construction": true});
            skLineSegment(sketch, "E14.11.12.12", {"start": v(53.93, -32.96) * mm, "end": v(50.78, -32.96) * mm});
            skLineSegment(sketch, "E14.14.12.12", {"start": v(50.78, -32.96) * mm, "end": v(49.2, -30.23) * mm});
            skLineSegment(sketch, "E14.17.12.12", {"start": v(49.2, -30.23) * mm, "end": v(50.78, -27.5) * mm});
            skLineSegment(sketch, "E14.0.12.13", {"start": v(50.78, -18.86) * mm, "end": v(53.93, -18.86) * mm});
            skLineSegment(sketch, "E14.3.12.13", {"start": v(53.93, -18.86) * mm, "end": v(55.5, -21.6) * mm});
            skLineSegment(sketch, "E14.6.12.13", {"start": v(55.5, -21.6) * mm, "end": v(53.93, -24.32) * mm});
            skCircle(sketch, "E14.9.12.13", {"center": v(52.35, -21.6) * mm, "radius": 2.73 * mm, "construction": true});
            skLineSegment(sketch, "E14.11.12.13", {"start": v(53.93, -24.32) * mm, "end": v(50.78, -24.32) * mm});
            skLineSegment(sketch, "E14.14.12.13", {"start": v(50.78, -24.32) * mm, "end": v(49.2, -21.6) * mm});
            skLineSegment(sketch, "E14.17.12.13", {"start": v(49.2, -21.59) * mm, "end": v(50.78, -18.86) * mm});
            skLineSegment(sketch, "E14.0.12.14", {"start": v(50.78, -10.22) * mm, "end": v(53.93, -10.22) * mm});
            skLineSegment(sketch, "E14.3.12.14", {"start": v(53.93, -10.22) * mm, "end": v(55.5, -12.95) * mm});
            skLineSegment(sketch, "E14.6.12.14", {"start": v(55.5, -12.95) * mm, "end": v(53.93, -15.68) * mm});
            skCircle(sketch, "E14.9.12.14", {"center": v(52.35, -12.95) * mm, "radius": 2.73 * mm, "construction": true});
            skLineSegment(sketch, "E14.11.12.14", {"start": v(53.93, -15.68) * mm, "end": v(50.78, -15.68) * mm});
            skLineSegment(sketch, "E14.14.12.14", {"start": v(50.78, -15.68) * mm, "end": v(49.2, -12.95) * mm});
            skLineSegment(sketch, "E14.17.12.14", {"start": v(49.2, -12.95) * mm, "end": v(50.78, -10.22) * mm});
            skLineSegment(sketch, "E14.0.12.15", {"start": v(50.78, -1.59) * mm, "end": v(53.93, -1.59) * mm});
            skLineSegment(sketch, "E14.3.12.15", {"start": v(53.93, -1.59) * mm, "end": v(55.5, -4.32) * mm});
            skLineSegment(sketch, "E14.6.12.15", {"start": v(55.5, -4.32) * mm, "end": v(53.93, -7.05) * mm});
            skCircle(sketch, "E14.9.12.15", {"center": v(52.35, -4.32) * mm, "radius": 2.73 * mm, "construction": true});
            skLineSegment(sketch, "E14.11.12.15", {"start": v(53.93, -7.05) * mm, "end": v(50.78, -7.05) * mm});
            skLineSegment(sketch, "E14.14.12.15", {"start": v(50.78, -7.05) * mm, "end": v(49.2, -4.32) * mm});
            skLineSegment(sketch, "E14.17.12.15", {"start": v(49.2, -4.32) * mm, "end": v(50.78, -1.59) * mm});
            skLineSegment(sketch, "E14.0.12.16", {"start": v(50.78, 7.05) * mm, "end": v(53.93, 7.05) * mm});
            skLineSegment(sketch, "E14.3.12.16", {"start": v(53.93, 7.05) * mm, "end": v(55.5, 4.32) * mm});
            skLineSegment(sketch, "E14.6.12.16", {"start": v(55.5, 4.32) * mm, "end": v(53.93, 1.59) * mm});
            skCircle(sketch, "E14.9.12.16", {"center": v(52.35, 4.32) * mm, "radius": 2.73 * mm, "construction": true});
            skLineSegment(sketch, "E14.11.12.16", {"start": v(53.93, 1.59) * mm, "end": v(50.78, 1.59) * mm});
            skLineSegment(sketch, "E14.14.12.16", {"start": v(50.78, 1.59) * mm, "end": v(49.2, 4.32) * mm});
            skLineSegment(sketch, "E14.17.12.16", {"start": v(49.2, 4.32) * mm, "end": v(50.78, 7.05) * mm});
            skLineSegment(sketch, "E14.0.12.17", {"start": v(50.78, 15.68) * mm, "end": v(53.93, 15.68) * mm});
            skLineSegment(sketch, "E14.3.12.17", {"start": v(53.93, 15.68) * mm, "end": v(55.5, 12.95) * mm});
            skLineSegment(sketch, "E14.6.12.17", {"start": v(55.5, 12.95) * mm, "end": v(53.93, 10.22) * mm});
            skCircle(sketch, "E14.9.12.17", {"center": v(52.35, 12.95) * mm, "radius": 2.73 * mm, "construction": true});
            skLineSegment(sketch, "E14.11.12.17", {"start": v(53.93, 10.22) * mm, "end": v(50.78, 10.22) * mm});
            skLineSegment(sketch, "E14.14.12.17", {"start": v(50.78, 10.22) * mm, "end": v(49.2, 12.95) * mm});
            skLineSegment(sketch, "E14.17.12.17", {"start": v(49.2, 12.95) * mm, "end": v(50.78, 15.68) * mm});
            skLineSegment(sketch, "E14.0.12.18", {"start": v(50.78, 24.32) * mm, "end": v(53.93, 24.32) * mm});
            skLineSegment(sketch, "E14.3.12.18", {"start": v(53.93, 24.32) * mm, "end": v(55.5, 21.59) * mm});
            skLineSegment(sketch, "E14.6.12.18", {"start": v(55.5, 21.59) * mm, "end": v(53.93, 18.86) * mm});
            skCircle(sketch, "E14.9.12.18", {"center": v(52.35, 21.59) * mm, "radius": 2.73 * mm, "construction": true});
            skLineSegment(sketch, "E14.11.12.18", {"start": v(53.93, 18.86) * mm, "end": v(50.78, 18.86) * mm});
            skLineSegment(sketch, "E14.14.12.18", {"start": v(50.78, 18.86) * mm, "end": v(49.2, 21.59) * mm});
            skLineSegment(sketch, "E14.17.12.18", {"start": v(49.2, 21.6) * mm, "end": v(50.78, 24.32) * mm});
            skLineSegment(sketch, "E14.0.12.19", {"start": v(50.78, 32.96) * mm, "end": v(53.93, 32.96) * mm});
            skLineSegment(sketch, "E14.3.12.19", {"start": v(53.93, 32.96) * mm, "end": v(55.5, 30.23) * mm});
            skLineSegment(sketch, "E14.6.12.19", {"start": v(55.5, 30.23) * mm, "end": v(53.93, 27.5) * mm});
            skCircle(sketch, "E14.9.12.19", {"center": v(52.35, 30.23) * mm, "radius": 2.73 * mm, "construction": true});
            skLineSegment(sketch, "E14.11.12.19", {"start": v(53.93, 27.5) * mm, "end": v(50.78, 27.5) * mm});
            skLineSegment(sketch, "E14.14.12.19", {"start": v(50.78, 27.5) * mm, "end": v(49.2, 30.23) * mm});
            skLineSegment(sketch, "E14.17.12.19", {"start": v(49.2, 30.23) * mm, "end": v(50.78, 32.96) * mm});
            skLineSegment(sketch, "E14.0.13.0", {"start": v(65.73, -131.13) * mm, "end": v(68.89, -131.13) * mm});
            skLineSegment(sketch, "E14.3.13.0", {"start": v(68.89, -131.13) * mm, "end": v(70.46, -133.86) * mm});
            skLineSegment(sketch, "E14.6.13.0", {"start": v(70.46, -133.86) * mm, "end": v(68.89, -136.59) * mm});
            skCircle(sketch, "E14.9.13.0", {"center": v(67.31, -133.86) * mm, "radius": 2.73 * mm, "construction": true});
            skLineSegment(sketch, "E14.11.13.0", {"start": v(68.89, -136.59) * mm, "end": v(65.73, -136.59) * mm});
            skLineSegment(sketch, "E14.14.13.0", {"start": v(65.73, -136.59) * mm, "end": v(64.16, -133.86) * mm});
            skLineSegment(sketch, "E14.17.13.0", {"start": v(64.16, -133.86) * mm, "end": v(65.73, -131.13) * mm});
            skLineSegment(sketch, "E14.0.13.1", {"start": v(65.73, -122.5) * mm, "end": v(68.89, -122.5) * mm});
            skLineSegment(sketch, "E14.3.13.1", {"start": v(68.89, -122.5) * mm, "end": v(70.46, -125.22) * mm});
            skLineSegment(sketch, "E14.6.13.1", {"start": v(70.46, -125.22) * mm, "end": v(68.89, -127.95) * mm});
            skCircle(sketch, "E14.9.13.1", {"center": v(67.31, -125.22) * mm, "radius": 2.73 * mm, "construction": true});
            skLineSegment(sketch, "E14.11.13.1", {"start": v(68.89, -127.95) * mm, "end": v(65.73, -127.95) * mm});
            skLineSegment(sketch, "E14.14.13.1", {"start": v(65.73, -127.95) * mm, "end": v(64.16, -125.22) * mm});
            skLineSegment(sketch, "E14.17.13.1", {"start": v(64.16, -125.22) * mm, "end": v(65.73, -122.5) * mm});
            skLineSegment(sketch, "E14.0.13.2", {"start": v(65.73, -113.86) * mm, "end": v(68.89, -113.86) * mm});
            skLineSegment(sketch, "E14.3.13.2", {"start": v(68.89, -113.86) * mm, "end": v(70.46, -116.59) * mm});
            skLineSegment(sketch, "E14.6.13.2", {"start": v(70.46, -116.59) * mm, "end": v(68.89, -119.32) * mm});
            skCircle(sketch, "E14.9.13.2", {"center": v(67.31, -116.59) * mm, "radius": 2.73 * mm, "construction": true});
            skLineSegment(sketch, "E14.11.13.2", {"start": v(68.89, -119.32) * mm, "end": v(65.73, -119.32) * mm});
            skLineSegment(sketch, "E14.14.13.2", {"start": v(65.73, -119.32) * mm, "end": v(64.16, -116.59) * mm});
            skLineSegment(sketch, "E14.17.13.2", {"start": v(64.16, -116.59) * mm, "end": v(65.73, -113.86) * mm});
            skLineSegment(sketch, "E14.0.13.3", {"start": v(65.73, -105.22) * mm, "end": v(68.89, -105.22) * mm});
            skLineSegment(sketch, "E14.3.13.3", {"start": v(68.89, -105.22) * mm, "end": v(70.46, -107.95) * mm});
            skLineSegment(sketch, "E14.6.13.3", {"start": v(70.46, -107.95) * mm, "end": v(68.89, -110.68) * mm});
            skCircle(sketch, "E14.9.13.3", {"center": v(67.31, -107.95) * mm, "radius": 2.73 * mm, "construction": true});
            skLineSegment(sketch, "E14.11.13.3", {"start": v(68.89, -110.68) * mm, "end": v(65.73, -110.68) * mm});
            skLineSegment(sketch, "E14.14.13.3", {"start": v(65.73, -110.68) * mm, "end": v(64.16, -107.95) * mm});
            skLineSegment(sketch, "E14.17.13.3", {"start": v(64.16, -107.95) * mm, "end": v(65.73, -105.22) * mm});
            skLineSegment(sketch, "E14.0.13.4", {"start": v(65.73, -96.58) * mm, "end": v(68.89, -96.58) * mm});
            skLineSegment(sketch, "E14.3.13.4", {"start": v(68.89, -96.58) * mm, "end": v(70.46, -99.31) * mm});
            skLineSegment(sketch, "E14.6.13.4", {"start": v(70.46, -99.31) * mm, "end": v(68.89, -102.04) * mm});
            skCircle(sketch, "E14.9.13.4", {"center": v(67.31, -99.31) * mm, "radius": 2.73 * mm, "construction": true});
            skLineSegment(sketch, "E14.11.13.4", {"start": v(68.89, -102.04) * mm, "end": v(65.73, -102.04) * mm});
            skLineSegment(sketch, "E14.14.13.4", {"start": v(65.73, -102.04) * mm, "end": v(64.16, -99.31) * mm});
            skLineSegment(sketch, "E14.17.13.4", {"start": v(64.16, -99.31) * mm, "end": v(65.73, -96.58) * mm});
            skLineSegment(sketch, "E14.0.13.5", {"start": v(65.73, -87.95) * mm, "end": v(68.89, -87.95) * mm});
            skLineSegment(sketch, "E14.3.13.5", {"start": v(68.89, -87.95) * mm, "end": v(70.46, -90.68) * mm});
            skLineSegment(sketch, "E14.6.13.5", {"start": v(70.46, -90.68) * mm, "end": v(68.89, -93.4) * mm});
            skCircle(sketch, "E14.9.13.5", {"center": v(67.31, -90.68) * mm, "radius": 2.73 * mm, "construction": true});
            skLineSegment(sketch, "E14.11.13.5", {"start": v(68.89, -93.4) * mm, "end": v(65.73, -93.4) * mm});
            skLineSegment(sketch, "E14.14.13.5", {"start": v(65.73, -93.4) * mm, "end": v(64.16, -90.68) * mm});
            skLineSegment(sketch, "E14.17.13.5", {"start": v(64.16, -90.68) * mm, "end": v(65.73, -87.95) * mm});
            skLineSegment(sketch, "E14.0.13.6", {"start": v(65.73, -79.31) * mm, "end": v(68.89, -79.31) * mm});
            skLineSegment(sketch, "E14.3.13.6", {"start": v(68.89, -79.31) * mm, "end": v(70.46, -82.04) * mm});
            skLineSegment(sketch, "E14.6.13.6", {"start": v(70.46, -82.04) * mm, "end": v(68.89, -84.77) * mm});
            skCircle(sketch, "E14.9.13.6", {"center": v(67.31, -82.04) * mm, "radius": 2.73 * mm, "construction": true});
            skLineSegment(sketch, "E14.11.13.6", {"start": v(68.89, -84.77) * mm, "end": v(65.73, -84.77) * mm});
            skLineSegment(sketch, "E14.14.13.6", {"start": v(65.73, -84.77) * mm, "end": v(64.16, -82.04) * mm});
            skLineSegment(sketch, "E14.17.13.6", {"start": v(64.16, -82.04) * mm, "end": v(65.73, -79.31) * mm});
            skLineSegment(sketch, "E14.0.13.7", {"start": v(65.73, -70.68) * mm, "end": v(68.89, -70.68) * mm});
            skLineSegment(sketch, "E14.3.13.7", {"start": v(68.89, -70.68) * mm, "end": v(70.46, -73.4) * mm});
            skLineSegment(sketch, "E14.6.13.7", {"start": v(70.46, -73.4) * mm, "end": v(68.89, -76.14) * mm});
            skCircle(sketch, "E14.9.13.7", {"center": v(67.31, -73.4) * mm, "radius": 2.73 * mm, "construction": true});
            skLineSegment(sketch, "E14.11.13.7", {"start": v(68.89, -76.14) * mm, "end": v(65.73, -76.14) * mm});
            skLineSegment(sketch, "E14.14.13.7", {"start": v(65.73, -76.14) * mm, "end": v(64.16, -73.4) * mm});
            skLineSegment(sketch, "E14.17.13.7", {"start": v(64.16, -73.4) * mm, "end": v(65.73, -70.68) * mm});
            skLineSegment(sketch, "E14.0.13.8", {"start": v(65.73, -62.04) * mm, "end": v(68.89, -62.04) * mm});
            skLineSegment(sketch, "E14.3.13.8", {"start": v(68.89, -62.04) * mm, "end": v(70.46, -64.77) * mm});
            skLineSegment(sketch, "E14.6.13.8", {"start": v(70.46, -64.77) * mm, "end": v(68.89, -67.5) * mm});
            skCircle(sketch, "E14.9.13.8", {"center": v(67.31, -64.77) * mm, "radius": 2.73 * mm, "construction": true});
            skLineSegment(sketch, "E14.11.13.8", {"start": v(68.89, -67.5) * mm, "end": v(65.73, -67.5) * mm});
            skLineSegment(sketch, "E14.14.13.8", {"start": v(65.73, -67.5) * mm, "end": v(64.16, -64.77) * mm});
            skLineSegment(sketch, "E14.17.13.8", {"start": v(64.16, -64.77) * mm, "end": v(65.73, -62.04) * mm});
            skLineSegment(sketch, "E14.0.13.9", {"start": v(65.73, -53.4) * mm, "end": v(68.89, -53.4) * mm});
            skLineSegment(sketch, "E14.3.13.9", {"start": v(68.89, -53.4) * mm, "end": v(70.46, -56.13) * mm});
            skLineSegment(sketch, "E14.6.13.9", {"start": v(70.46, -56.13) * mm, "end": v(68.89, -58.86) * mm});
            skCircle(sketch, "E14.9.13.9", {"center": v(67.31, -56.13) * mm, "radius": 2.73 * mm, "construction": true});
            skLineSegment(sketch, "E14.11.13.9", {"start": v(68.89, -58.86) * mm, "end": v(65.73, -58.86) * mm});
            skLineSegment(sketch, "E14.14.13.9", {"start": v(65.73, -58.86) * mm, "end": v(64.16, -56.13) * mm});
            skLineSegment(sketch, "E14.17.13.9", {"start": v(64.16, -56.13) * mm, "end": v(65.73, -53.4) * mm});
            skLineSegment(sketch, "E14.0.13.10", {"start": v(65.73, -44.77) * mm, "end": v(68.89, -44.77) * mm});
            skLineSegment(sketch, "E14.3.13.10", {"start": v(68.89, -44.77) * mm, "end": v(70.46, -47.5) * mm});
            skLineSegment(sketch, "E14.6.13.10", {"start": v(70.46, -47.5) * mm, "end": v(68.89, -50.23) * mm});
            skCircle(sketch, "E14.9.13.10", {"center": v(67.31, -47.5) * mm, "radius": 2.73 * mm, "construction": true});
            skLineSegment(sketch, "E14.11.13.10", {"start": v(68.89, -50.23) * mm, "end": v(65.73, -50.23) * mm});
            skLineSegment(sketch, "E14.14.13.10", {"start": v(65.73, -50.23) * mm, "end": v(64.16, -47.5) * mm});
            skLineSegment(sketch, "E14.17.13.10", {"start": v(64.16, -47.5) * mm, "end": v(65.73, -44.77) * mm});
            skLineSegment(sketch, "E14.0.13.11", {"start": v(65.73, -36.13) * mm, "end": v(68.89, -36.13) * mm});
            skLineSegment(sketch, "E14.3.13.11", {"start": v(68.89, -36.13) * mm, "end": v(70.46, -38.86) * mm});
            skLineSegment(sketch, "E14.6.13.11", {"start": v(70.46, -38.86) * mm, "end": v(68.89, -41.6) * mm});
            skCircle(sketch, "E14.9.13.11", {"center": v(67.31, -38.86) * mm, "radius": 2.73 * mm, "construction": true});
            skLineSegment(sketch, "E14.11.13.11", {"start": v(68.89, -41.6) * mm, "end": v(65.73, -41.6) * mm});
            skLineSegment(sketch, "E14.14.13.11", {"start": v(65.73, -41.6) * mm, "end": v(64.16, -38.86) * mm});
            skLineSegment(sketch, "E14.17.13.11", {"start": v(64.16, -38.86) * mm, "end": v(65.73, -36.13) * mm});
            skLineSegment(sketch, "E14.0.13.12", {"start": v(65.73, -27.5) * mm, "end": v(68.89, -27.5) * mm});
            skLineSegment(sketch, "E14.3.13.12", {"start": v(68.89, -27.5) * mm, "end": v(70.46, -30.23) * mm});
            skLineSegment(sketch, "E14.6.13.12", {"start": v(70.46, -30.23) * mm, "end": v(68.89, -32.96) * mm});
            skCircle(sketch, "E14.9.13.12", {"center": v(67.31, -30.23) * mm, "radius": 2.73 * mm, "construction": true});
            skLineSegment(sketch, "E14.11.13.12", {"start": v(68.89, -32.96) * mm, "end": v(65.73, -32.96) * mm});
            skLineSegment(sketch, "E14.14.13.12", {"start": v(65.73, -32.96) * mm, "end": v(64.16, -30.23) * mm});
            skLineSegment(sketch, "E14.17.13.12", {"start": v(64.16, -30.23) * mm, "end": v(65.73, -27.5) * mm});
            skLineSegment(sketch, "E14.0.13.13", {"start": v(65.73, -18.86) * mm, "end": v(68.89, -18.86) * mm});
            skLineSegment(sketch, "E14.3.13.13", {"start": v(68.89, -18.86) * mm, "end": v(70.46, -21.6) * mm});
            skLineSegment(sketch, "E14.6.13.13", {"start": v(70.46, -21.6) * mm, "end": v(68.89, -24.32) * mm});
            skCircle(sketch, "E14.9.13.13", {"center": v(67.31, -21.6) * mm, "radius": 2.73 * mm, "construction": true});
            skLineSegment(sketch, "E14.11.13.13", {"start": v(68.89, -24.32) * mm, "end": v(65.73, -24.32) * mm});
            skLineSegment(sketch, "E14.14.13.13", {"start": v(65.73, -24.32) * mm, "end": v(64.16, -21.6) * mm});
            skLineSegment(sketch, "E14.17.13.13", {"start": v(64.16, -21.59) * mm, "end": v(65.73, -18.86) * mm});
            skLineSegment(sketch, "E14.0.13.14", {"start": v(65.73, -10.22) * mm, "end": v(68.89, -10.22) * mm});
            skLineSegment(sketch, "E14.3.13.14", {"start": v(68.89, -10.22) * mm, "end": v(70.46, -12.95) * mm});
            skLineSegment(sketch, "E14.6.13.14", {"start": v(70.46, -12.95) * mm, "end": v(68.89, -15.68) * mm});
            skCircle(sketch, "E14.9.13.14", {"center": v(67.31, -12.95) * mm, "radius": 2.73 * mm, "construction": true});
            skLineSegment(sketch, "E14.11.13.14", {"start": v(68.89, -15.68) * mm, "end": v(65.73, -15.68) * mm});
            skLineSegment(sketch, "E14.14.13.14", {"start": v(65.73, -15.68) * mm, "end": v(64.16, -12.95) * mm});
            skLineSegment(sketch, "E14.17.13.14", {"start": v(64.16, -12.95) * mm, "end": v(65.73, -10.22) * mm});
            skLineSegment(sketch, "E14.0.13.15", {"start": v(65.73, -1.59) * mm, "end": v(68.89, -1.59) * mm});
            skLineSegment(sketch, "E14.3.13.15", {"start": v(68.89, -1.59) * mm, "end": v(70.46, -4.32) * mm});
            skLineSegment(sketch, "E14.6.13.15", {"start": v(70.46, -4.32) * mm, "end": v(68.89, -7.05) * mm});
            skCircle(sketch, "E14.9.13.15", {"center": v(67.31, -4.32) * mm, "radius": 2.73 * mm, "construction": true});
            skLineSegment(sketch, "E14.11.13.15", {"start": v(68.89, -7.05) * mm, "end": v(65.73, -7.05) * mm});
            skLineSegment(sketch, "E14.14.13.15", {"start": v(65.73, -7.05) * mm, "end": v(64.16, -4.32) * mm});
            skLineSegment(sketch, "E14.17.13.15", {"start": v(64.16, -4.32) * mm, "end": v(65.73, -1.59) * mm});
            skLineSegment(sketch, "E14.0.13.16", {"start": v(65.73, 7.05) * mm, "end": v(68.89, 7.05) * mm});
            skLineSegment(sketch, "E14.3.13.16", {"start": v(68.89, 7.05) * mm, "end": v(70.46, 4.32) * mm});
            skLineSegment(sketch, "E14.6.13.16", {"start": v(70.46, 4.32) * mm, "end": v(68.89, 1.59) * mm});
            skCircle(sketch, "E14.9.13.16", {"center": v(67.31, 4.32) * mm, "radius": 2.73 * mm, "construction": true});
            skLineSegment(sketch, "E14.11.13.16", {"start": v(68.89, 1.59) * mm, "end": v(65.73, 1.59) * mm});
            skLineSegment(sketch, "E14.14.13.16", {"start": v(65.73, 1.59) * mm, "end": v(64.16, 4.32) * mm});
            skLineSegment(sketch, "E14.17.13.16", {"start": v(64.16, 4.32) * mm, "end": v(65.73, 7.05) * mm});
            skLineSegment(sketch, "E14.0.13.17", {"start": v(65.73, 15.68) * mm, "end": v(68.89, 15.68) * mm});
            skLineSegment(sketch, "E14.3.13.17", {"start": v(68.89, 15.68) * mm, "end": v(70.46, 12.95) * mm});
            skLineSegment(sketch, "E14.6.13.17", {"start": v(70.46, 12.95) * mm, "end": v(68.89, 10.22) * mm});
            skCircle(sketch, "E14.9.13.17", {"center": v(67.31, 12.95) * mm, "radius": 2.73 * mm, "construction": true});
            skLineSegment(sketch, "E14.11.13.17", {"start": v(68.89, 10.22) * mm, "end": v(65.73, 10.22) * mm});
            skLineSegment(sketch, "E14.14.13.17", {"start": v(65.73, 10.22) * mm, "end": v(64.16, 12.95) * mm});
            skLineSegment(sketch, "E14.17.13.17", {"start": v(64.16, 12.95) * mm, "end": v(65.73, 15.68) * mm});
            skLineSegment(sketch, "E14.0.13.18", {"start": v(65.73, 24.32) * mm, "end": v(68.89, 24.32) * mm});
            skLineSegment(sketch, "E14.3.13.18", {"start": v(68.89, 24.32) * mm, "end": v(70.46, 21.59) * mm});
            skLineSegment(sketch, "E14.6.13.18", {"start": v(70.46, 21.59) * mm, "end": v(68.89, 18.86) * mm});
            skCircle(sketch, "E14.9.13.18", {"center": v(67.31, 21.59) * mm, "radius": 2.73 * mm, "construction": true});
            skLineSegment(sketch, "E14.11.13.18", {"start": v(68.89, 18.86) * mm, "end": v(65.73, 18.86) * mm});
            skLineSegment(sketch, "E14.14.13.18", {"start": v(65.73, 18.86) * mm, "end": v(64.16, 21.59) * mm});
            skLineSegment(sketch, "E14.17.13.18", {"start": v(64.16, 21.6) * mm, "end": v(65.73, 24.32) * mm});
            skLineSegment(sketch, "E14.0.13.19", {"start": v(65.73, 32.96) * mm, "end": v(68.89, 32.96) * mm});
            skLineSegment(sketch, "E14.3.13.19", {"start": v(68.89, 32.96) * mm, "end": v(70.46, 30.23) * mm});
            skLineSegment(sketch, "E14.6.13.19", {"start": v(70.46, 30.23) * mm, "end": v(68.89, 27.5) * mm});
            skCircle(sketch, "E14.9.13.19", {"center": v(67.31, 30.23) * mm, "radius": 2.73 * mm, "construction": true});
            skLineSegment(sketch, "E14.11.13.19", {"start": v(68.89, 27.5) * mm, "end": v(65.73, 27.5) * mm});
            skLineSegment(sketch, "E14.14.13.19", {"start": v(65.73, 27.5) * mm, "end": v(64.16, 30.23) * mm});
            skLineSegment(sketch, "E14.17.13.19", {"start": v(64.16, 30.23) * mm, "end": v(65.73, 32.96) * mm});
            skLineSegment(sketch, "E14.0.14.0", {"start": v(80.7, -131.13) * mm, "end": v(83.85, -131.13) * mm});
            skLineSegment(sketch, "E14.3.14.0", {"start": v(83.85, -131.13) * mm, "end": v(85.42, -133.86) * mm});
            skLineSegment(sketch, "E14.6.14.0", {"start": v(85.42, -133.86) * mm, "end": v(83.85, -136.59) * mm});
            skCircle(sketch, "E14.9.14.0", {"center": v(82.27, -133.86) * mm, "radius": 2.73 * mm, "construction": true});
            skLineSegment(sketch, "E14.11.14.0", {"start": v(83.85, -136.59) * mm, "end": v(80.7, -136.59) * mm});
            skLineSegment(sketch, "E14.14.14.0", {"start": v(80.7, -136.59) * mm, "end": v(79.12, -133.86) * mm});
            skLineSegment(sketch, "E14.17.14.0", {"start": v(79.12, -133.86) * mm, "end": v(80.7, -131.13) * mm});
            skLineSegment(sketch, "E14.0.14.1", {"start": v(80.7, -122.5) * mm, "end": v(83.85, -122.5) * mm});
            skLineSegment(sketch, "E14.3.14.1", {"start": v(83.85, -122.5) * mm, "end": v(85.42, -125.22) * mm});
            skLineSegment(sketch, "E14.6.14.1", {"start": v(85.42, -125.22) * mm, "end": v(83.85, -127.95) * mm});
            skCircle(sketch, "E14.9.14.1", {"center": v(82.27, -125.22) * mm, "radius": 2.73 * mm, "construction": true});
            skLineSegment(sketch, "E14.11.14.1", {"start": v(83.85, -127.95) * mm, "end": v(80.7, -127.95) * mm});
            skLineSegment(sketch, "E14.14.14.1", {"start": v(80.7, -127.95) * mm, "end": v(79.12, -125.22) * mm});
            skLineSegment(sketch, "E14.17.14.1", {"start": v(79.12, -125.22) * mm, "end": v(80.7, -122.5) * mm});
            skLineSegment(sketch, "E14.0.14.2", {"start": v(80.7, -113.86) * mm, "end": v(83.85, -113.86) * mm});
            skLineSegment(sketch, "E14.3.14.2", {"start": v(83.85, -113.86) * mm, "end": v(85.42, -116.59) * mm});
            skLineSegment(sketch, "E14.6.14.2", {"start": v(85.42, -116.59) * mm, "end": v(83.85, -119.32) * mm});
            skCircle(sketch, "E14.9.14.2", {"center": v(82.27, -116.59) * mm, "radius": 2.73 * mm, "construction": true});
            skLineSegment(sketch, "E14.11.14.2", {"start": v(83.85, -119.32) * mm, "end": v(80.7, -119.32) * mm});
            skLineSegment(sketch, "E14.14.14.2", {"start": v(80.7, -119.32) * mm, "end": v(79.12, -116.59) * mm});
            skLineSegment(sketch, "E14.17.14.2", {"start": v(79.12, -116.59) * mm, "end": v(80.7, -113.86) * mm});
            skLineSegment(sketch, "E14.0.14.3", {"start": v(80.7, -105.22) * mm, "end": v(83.85, -105.22) * mm});
            skLineSegment(sketch, "E14.3.14.3", {"start": v(83.85, -105.22) * mm, "end": v(85.42, -107.95) * mm});
            skLineSegment(sketch, "E14.6.14.3", {"start": v(85.42, -107.95) * mm, "end": v(83.85, -110.68) * mm});
            skCircle(sketch, "E14.9.14.3", {"center": v(82.27, -107.95) * mm, "radius": 2.73 * mm, "construction": true});
            skLineSegment(sketch, "E14.11.14.3", {"start": v(83.85, -110.68) * mm, "end": v(80.7, -110.68) * mm});
            skLineSegment(sketch, "E14.14.14.3", {"start": v(80.7, -110.68) * mm, "end": v(79.12, -107.95) * mm});
            skLineSegment(sketch, "E14.17.14.3", {"start": v(79.12, -107.95) * mm, "end": v(80.7, -105.22) * mm});
            skLineSegment(sketch, "E14.0.14.4", {"start": v(80.7, -96.58) * mm, "end": v(83.85, -96.58) * mm});
            skLineSegment(sketch, "E14.3.14.4", {"start": v(83.85, -96.58) * mm, "end": v(85.42, -99.31) * mm});
            skLineSegment(sketch, "E14.6.14.4", {"start": v(85.42, -99.31) * mm, "end": v(83.85, -102.04) * mm});
            skCircle(sketch, "E14.9.14.4", {"center": v(82.27, -99.31) * mm, "radius": 2.73 * mm, "construction": true});
            skLineSegment(sketch, "E14.11.14.4", {"start": v(83.85, -102.04) * mm, "end": v(80.7, -102.04) * mm});
            skLineSegment(sketch, "E14.14.14.4", {"start": v(80.7, -102.04) * mm, "end": v(79.12, -99.31) * mm});
            skLineSegment(sketch, "E14.17.14.4", {"start": v(79.12, -99.31) * mm, "end": v(80.7, -96.58) * mm});
            skLineSegment(sketch, "E14.0.14.5", {"start": v(80.7, -87.95) * mm, "end": v(83.85, -87.95) * mm});
            skLineSegment(sketch, "E14.3.14.5", {"start": v(83.85, -87.95) * mm, "end": v(85.42, -90.68) * mm});
            skLineSegment(sketch, "E14.6.14.5", {"start": v(85.42, -90.68) * mm, "end": v(83.85, -93.4) * mm});
            skCircle(sketch, "E14.9.14.5", {"center": v(82.27, -90.68) * mm, "radius": 2.73 * mm, "construction": true});
            skLineSegment(sketch, "E14.11.14.5", {"start": v(83.85, -93.4) * mm, "end": v(80.7, -93.4) * mm});
            skLineSegment(sketch, "E14.14.14.5", {"start": v(80.7, -93.4) * mm, "end": v(79.12, -90.68) * mm});
            skLineSegment(sketch, "E14.17.14.5", {"start": v(79.12, -90.68) * mm, "end": v(80.7, -87.95) * mm});
            skLineSegment(sketch, "E14.0.14.6", {"start": v(80.7, -79.31) * mm, "end": v(83.85, -79.31) * mm});
            skLineSegment(sketch, "E14.3.14.6", {"start": v(83.85, -79.31) * mm, "end": v(85.42, -82.04) * mm});
            skLineSegment(sketch, "E14.6.14.6", {"start": v(85.42, -82.04) * mm, "end": v(83.85, -84.77) * mm});
            skCircle(sketch, "E14.9.14.6", {"center": v(82.27, -82.04) * mm, "radius": 2.73 * mm, "construction": true});
            skLineSegment(sketch, "E14.11.14.6", {"start": v(83.85, -84.77) * mm, "end": v(80.7, -84.77) * mm});
            skLineSegment(sketch, "E14.14.14.6", {"start": v(80.7, -84.77) * mm, "end": v(79.12, -82.04) * mm});
            skLineSegment(sketch, "E14.17.14.6", {"start": v(79.12, -82.04) * mm, "end": v(80.7, -79.31) * mm});
            skLineSegment(sketch, "E14.0.14.7", {"start": v(80.7, -70.68) * mm, "end": v(83.85, -70.68) * mm});
            skLineSegment(sketch, "E14.3.14.7", {"start": v(83.85, -70.68) * mm, "end": v(85.42, -73.4) * mm});
            skLineSegment(sketch, "E14.6.14.7", {"start": v(85.42, -73.4) * mm, "end": v(83.85, -76.14) * mm});
            skCircle(sketch, "E14.9.14.7", {"center": v(82.27, -73.4) * mm, "radius": 2.73 * mm, "construction": true});
            skLineSegment(sketch, "E14.11.14.7", {"start": v(83.85, -76.14) * mm, "end": v(80.7, -76.14) * mm});
            skLineSegment(sketch, "E14.14.14.7", {"start": v(80.7, -76.14) * mm, "end": v(79.12, -73.4) * mm});
            skLineSegment(sketch, "E14.17.14.7", {"start": v(79.12, -73.4) * mm, "end": v(80.7, -70.68) * mm});
            skLineSegment(sketch, "E14.0.14.8", {"start": v(80.7, -62.04) * mm, "end": v(83.85, -62.04) * mm});
            skLineSegment(sketch, "E14.3.14.8", {"start": v(83.85, -62.04) * mm, "end": v(85.42, -64.77) * mm});
            skLineSegment(sketch, "E14.6.14.8", {"start": v(85.42, -64.77) * mm, "end": v(83.85, -67.5) * mm});
            skCircle(sketch, "E14.9.14.8", {"center": v(82.27, -64.77) * mm, "radius": 2.73 * mm, "construction": true});
            skLineSegment(sketch, "E14.11.14.8", {"start": v(83.85, -67.5) * mm, "end": v(80.7, -67.5) * mm});
            skLineSegment(sketch, "E14.14.14.8", {"start": v(80.7, -67.5) * mm, "end": v(79.12, -64.77) * mm});
            skLineSegment(sketch, "E14.17.14.8", {"start": v(79.12, -64.77) * mm, "end": v(80.7, -62.04) * mm});
            skLineSegment(sketch, "E14.0.14.9", {"start": v(80.7, -53.4) * mm, "end": v(83.85, -53.4) * mm});
            skLineSegment(sketch, "E14.3.14.9", {"start": v(83.85, -53.4) * mm, "end": v(85.42, -56.13) * mm});
            skLineSegment(sketch, "E14.6.14.9", {"start": v(85.42, -56.13) * mm, "end": v(83.85, -58.86) * mm});
            skCircle(sketch, "E14.9.14.9", {"center": v(82.27, -56.13) * mm, "radius": 2.73 * mm, "construction": true});
            skLineSegment(sketch, "E14.11.14.9", {"start": v(83.85, -58.86) * mm, "end": v(80.7, -58.86) * mm});
            skLineSegment(sketch, "E14.14.14.9", {"start": v(80.7, -58.86) * mm, "end": v(79.12, -56.13) * mm});
            skLineSegment(sketch, "E14.17.14.9", {"start": v(79.12, -56.13) * mm, "end": v(80.7, -53.4) * mm});
            skLineSegment(sketch, "E14.0.14.10", {"start": v(80.7, -44.77) * mm, "end": v(83.85, -44.77) * mm});
            skLineSegment(sketch, "E14.3.14.10", {"start": v(83.85, -44.77) * mm, "end": v(85.42, -47.5) * mm});
            skLineSegment(sketch, "E14.6.14.10", {"start": v(85.42, -47.5) * mm, "end": v(83.85, -50.23) * mm});
            skCircle(sketch, "E14.9.14.10", {"center": v(82.27, -47.5) * mm, "radius": 2.73 * mm, "construction": true});
            skLineSegment(sketch, "E14.11.14.10", {"start": v(83.85, -50.23) * mm, "end": v(80.7, -50.23) * mm});
            skLineSegment(sketch, "E14.14.14.10", {"start": v(80.7, -50.23) * mm, "end": v(79.12, -47.5) * mm});
            skLineSegment(sketch, "E14.17.14.10", {"start": v(79.12, -47.5) * mm, "end": v(80.7, -44.77) * mm});
            skLineSegment(sketch, "E14.0.14.11", {"start": v(80.7, -36.13) * mm, "end": v(83.85, -36.13) * mm});
            skLineSegment(sketch, "E14.3.14.11", {"start": v(83.85, -36.13) * mm, "end": v(85.42, -38.86) * mm});
            skLineSegment(sketch, "E14.6.14.11", {"start": v(85.42, -38.86) * mm, "end": v(83.85, -41.6) * mm});
            skCircle(sketch, "E14.9.14.11", {"center": v(82.27, -38.86) * mm, "radius": 2.73 * mm, "construction": true});
            skLineSegment(sketch, "E14.11.14.11", {"start": v(83.85, -41.6) * mm, "end": v(80.7, -41.6) * mm});
            skLineSegment(sketch, "E14.14.14.11", {"start": v(80.7, -41.6) * mm, "end": v(79.12, -38.86) * mm});
            skLineSegment(sketch, "E14.17.14.11", {"start": v(79.12, -38.86) * mm, "end": v(80.7, -36.13) * mm});
            skLineSegment(sketch, "E14.0.14.12", {"start": v(80.7, -27.5) * mm, "end": v(83.85, -27.5) * mm});
            skLineSegment(sketch, "E14.3.14.12", {"start": v(83.85, -27.5) * mm, "end": v(85.42, -30.23) * mm});
            skLineSegment(sketch, "E14.6.14.12", {"start": v(85.42, -30.23) * mm, "end": v(83.85, -32.96) * mm});
            skCircle(sketch, "E14.9.14.12", {"center": v(82.27, -30.23) * mm, "radius": 2.73 * mm, "construction": true});
            skLineSegment(sketch, "E14.11.14.12", {"start": v(83.85, -32.96) * mm, "end": v(80.7, -32.96) * mm});
            skLineSegment(sketch, "E14.14.14.12", {"start": v(80.7, -32.96) * mm, "end": v(79.12, -30.23) * mm});
            skLineSegment(sketch, "E14.17.14.12", {"start": v(79.12, -30.23) * mm, "end": v(80.7, -27.5) * mm});
            skLineSegment(sketch, "E14.0.14.13", {"start": v(80.7, -18.86) * mm, "end": v(83.85, -18.86) * mm});
            skLineSegment(sketch, "E14.3.14.13", {"start": v(83.85, -18.86) * mm, "end": v(85.42, -21.6) * mm});
            skLineSegment(sketch, "E14.6.14.13", {"start": v(85.42, -21.6) * mm, "end": v(83.85, -24.32) * mm});
            skCircle(sketch, "E14.9.14.13", {"center": v(82.27, -21.6) * mm, "radius": 2.73 * mm, "construction": true});
            skLineSegment(sketch, "E14.11.14.13", {"start": v(83.85, -24.32) * mm, "end": v(80.7, -24.32) * mm});
            skLineSegment(sketch, "E14.14.14.13", {"start": v(80.7, -24.32) * mm, "end": v(79.12, -21.6) * mm});
            skLineSegment(sketch, "E14.17.14.13", {"start": v(79.12, -21.59) * mm, "end": v(80.7, -18.86) * mm});
            skLineSegment(sketch, "E14.0.14.14", {"start": v(80.7, -10.22) * mm, "end": v(83.85, -10.22) * mm});
            skLineSegment(sketch, "E14.3.14.14", {"start": v(83.85, -10.22) * mm, "end": v(85.42, -12.95) * mm});
            skLineSegment(sketch, "E14.6.14.14", {"start": v(85.42, -12.95) * mm, "end": v(83.85, -15.68) * mm});
            skCircle(sketch, "E14.9.14.14", {"center": v(82.27, -12.95) * mm, "radius": 2.73 * mm, "construction": true});
            skLineSegment(sketch, "E14.11.14.14", {"start": v(83.85, -15.68) * mm, "end": v(80.7, -15.68) * mm});
            skLineSegment(sketch, "E14.14.14.14", {"start": v(80.7, -15.68) * mm, "end": v(79.12, -12.95) * mm});
            skLineSegment(sketch, "E14.17.14.14", {"start": v(79.12, -12.95) * mm, "end": v(80.7, -10.22) * mm});
            skLineSegment(sketch, "E14.0.14.15", {"start": v(80.7, -1.59) * mm, "end": v(83.85, -1.59) * mm});
            skLineSegment(sketch, "E14.3.14.15", {"start": v(83.85, -1.59) * mm, "end": v(85.42, -4.32) * mm});
            skLineSegment(sketch, "E14.6.14.15", {"start": v(85.42, -4.32) * mm, "end": v(83.85, -7.05) * mm});
            skCircle(sketch, "E14.9.14.15", {"center": v(82.27, -4.32) * mm, "radius": 2.73 * mm, "construction": true});
            skLineSegment(sketch, "E14.11.14.15", {"start": v(83.85, -7.05) * mm, "end": v(80.7, -7.05) * mm});
            skLineSegment(sketch, "E14.14.14.15", {"start": v(80.7, -7.05) * mm, "end": v(79.12, -4.32) * mm});
            skLineSegment(sketch, "E14.17.14.15", {"start": v(79.12, -4.32) * mm, "end": v(80.7, -1.59) * mm});
            skLineSegment(sketch, "E14.0.14.16", {"start": v(80.7, 7.05) * mm, "end": v(83.85, 7.05) * mm});
            skLineSegment(sketch, "E14.3.14.16", {"start": v(83.85, 7.05) * mm, "end": v(85.42, 4.32) * mm});
            skLineSegment(sketch, "E14.6.14.16", {"start": v(85.42, 4.32) * mm, "end": v(83.85, 1.59) * mm});
            skCircle(sketch, "E14.9.14.16", {"center": v(82.27, 4.32) * mm, "radius": 2.73 * mm, "construction": true});
            skLineSegment(sketch, "E14.11.14.16", {"start": v(83.85, 1.59) * mm, "end": v(80.7, 1.59) * mm});
            skLineSegment(sketch, "E14.14.14.16", {"start": v(80.7, 1.59) * mm, "end": v(79.12, 4.32) * mm});
            skLineSegment(sketch, "E14.17.14.16", {"start": v(79.12, 4.32) * mm, "end": v(80.7, 7.05) * mm});
            skLineSegment(sketch, "E14.0.14.17", {"start": v(80.7, 15.68) * mm, "end": v(83.85, 15.68) * mm});
            skLineSegment(sketch, "E14.3.14.17", {"start": v(83.85, 15.68) * mm, "end": v(85.42, 12.95) * mm});
            skLineSegment(sketch, "E14.6.14.17", {"start": v(85.42, 12.95) * mm, "end": v(83.85, 10.22) * mm});
            skCircle(sketch, "E14.9.14.17", {"center": v(82.27, 12.95) * mm, "radius": 2.73 * mm, "construction": true});
            skLineSegment(sketch, "E14.11.14.17", {"start": v(83.85, 10.22) * mm, "end": v(80.7, 10.22) * mm});
            skLineSegment(sketch, "E14.14.14.17", {"start": v(80.7, 10.22) * mm, "end": v(79.12, 12.95) * mm});
            skLineSegment(sketch, "E14.17.14.17", {"start": v(79.12, 12.95) * mm, "end": v(80.7, 15.68) * mm});
            skLineSegment(sketch, "E14.0.14.18", {"start": v(80.7, 24.32) * mm, "end": v(83.85, 24.32) * mm});
            skLineSegment(sketch, "E14.3.14.18", {"start": v(83.85, 24.32) * mm, "end": v(85.42, 21.59) * mm});
            skLineSegment(sketch, "E14.6.14.18", {"start": v(85.42, 21.59) * mm, "end": v(83.85, 18.86) * mm});
            skCircle(sketch, "E14.9.14.18", {"center": v(82.27, 21.59) * mm, "radius": 2.73 * mm, "construction": true});
            skLineSegment(sketch, "E14.11.14.18", {"start": v(83.85, 18.86) * mm, "end": v(80.7, 18.86) * mm});
            skLineSegment(sketch, "E14.14.14.18", {"start": v(80.7, 18.86) * mm, "end": v(79.12, 21.59) * mm});
            skLineSegment(sketch, "E14.17.14.18", {"start": v(79.12, 21.59) * mm, "end": v(80.7, 24.32) * mm});
            skLineSegment(sketch, "E14.0.14.19", {"start": v(80.7, 32.96) * mm, "end": v(83.85, 32.96) * mm});
            skLineSegment(sketch, "E14.3.14.19", {"start": v(83.85, 32.96) * mm, "end": v(85.42, 30.23) * mm});
            skLineSegment(sketch, "E14.6.14.19", {"start": v(85.42, 30.23) * mm, "end": v(83.85, 27.5) * mm});
            skCircle(sketch, "E14.9.14.19", {"center": v(82.27, 30.23) * mm, "radius": 2.73 * mm, "construction": true});
            skLineSegment(sketch, "E14.11.14.19", {"start": v(83.85, 27.5) * mm, "end": v(80.7, 27.5) * mm});
            skLineSegment(sketch, "E14.14.14.19", {"start": v(80.7, 27.5) * mm, "end": v(79.12, 30.23) * mm});
            skLineSegment(sketch, "E14.17.14.19", {"start": v(79.12, 30.23) * mm, "end": v(80.7, 32.96) * mm});
            skLineSegment(sketch, "E14.0.15.0", {"start": v(95.65, -131.13) * mm, "end": v(98.8, -131.13) * mm});
            skLineSegment(sketch, "E14.3.15.0", {"start": v(98.8, -131.13) * mm, "end": v(100.38, -133.86) * mm});
            skLineSegment(sketch, "E14.6.15.0", {"start": v(100.38, -133.86) * mm, "end": v(98.8, -136.59) * mm});
            skCircle(sketch, "E14.9.15.0", {"center": v(97.23, -133.86) * mm, "radius": 2.73 * mm, "construction": true});
            skLineSegment(sketch, "E14.11.15.0", {"start": v(98.8, -136.59) * mm, "end": v(95.65, -136.59) * mm});
            skLineSegment(sketch, "E14.14.15.0", {"start": v(95.65, -136.59) * mm, "end": v(94.07, -133.86) * mm});
            skLineSegment(sketch, "E14.17.15.0", {"start": v(94.07, -133.86) * mm, "end": v(95.65, -131.13) * mm});
            skLineSegment(sketch, "E14.0.15.1", {"start": v(95.65, -122.5) * mm, "end": v(98.8, -122.5) * mm});
            skLineSegment(sketch, "E14.3.15.1", {"start": v(98.8, -122.5) * mm, "end": v(100.38, -125.22) * mm});
            skLineSegment(sketch, "E14.6.15.1", {"start": v(100.38, -125.22) * mm, "end": v(98.8, -127.95) * mm});
            skCircle(sketch, "E14.9.15.1", {"center": v(97.23, -125.22) * mm, "radius": 2.73 * mm, "construction": true});
            skLineSegment(sketch, "E14.11.15.1", {"start": v(98.8, -127.95) * mm, "end": v(95.65, -127.95) * mm});
            skLineSegment(sketch, "E14.14.15.1", {"start": v(95.65, -127.95) * mm, "end": v(94.07, -125.22) * mm});
            skLineSegment(sketch, "E14.17.15.1", {"start": v(94.07, -125.22) * mm, "end": v(95.65, -122.5) * mm});
            skLineSegment(sketch, "E14.0.15.2", {"start": v(95.65, -113.86) * mm, "end": v(98.8, -113.86) * mm});
            skLineSegment(sketch, "E14.3.15.2", {"start": v(98.8, -113.86) * mm, "end": v(100.38, -116.59) * mm});
            skLineSegment(sketch, "E14.6.15.2", {"start": v(100.38, -116.59) * mm, "end": v(98.8, -119.32) * mm});
            skCircle(sketch, "E14.9.15.2", {"center": v(97.23, -116.59) * mm, "radius": 2.73 * mm, "construction": true});
            skLineSegment(sketch, "E14.11.15.2", {"start": v(98.8, -119.32) * mm, "end": v(95.65, -119.32) * mm});
            skLineSegment(sketch, "E14.14.15.2", {"start": v(95.65, -119.32) * mm, "end": v(94.07, -116.59) * mm});
            skLineSegment(sketch, "E14.17.15.2", {"start": v(94.07, -116.59) * mm, "end": v(95.65, -113.86) * mm});
            skLineSegment(sketch, "E14.0.15.3", {"start": v(95.65, -105.22) * mm, "end": v(98.8, -105.22) * mm});
            skLineSegment(sketch, "E14.3.15.3", {"start": v(98.8, -105.22) * mm, "end": v(100.38, -107.95) * mm});
            skLineSegment(sketch, "E14.6.15.3", {"start": v(100.38, -107.95) * mm, "end": v(98.8, -110.68) * mm});
            skCircle(sketch, "E14.9.15.3", {"center": v(97.23, -107.95) * mm, "radius": 2.73 * mm, "construction": true});
            skLineSegment(sketch, "E14.11.15.3", {"start": v(98.8, -110.68) * mm, "end": v(95.65, -110.68) * mm});
            skLineSegment(sketch, "E14.14.15.3", {"start": v(95.65, -110.68) * mm, "end": v(94.07, -107.95) * mm});
            skLineSegment(sketch, "E14.17.15.3", {"start": v(94.07, -107.95) * mm, "end": v(95.65, -105.22) * mm});
            skLineSegment(sketch, "E14.0.15.4", {"start": v(95.65, -96.58) * mm, "end": v(98.8, -96.58) * mm});
            skLineSegment(sketch, "E14.3.15.4", {"start": v(98.8, -96.58) * mm, "end": v(100.38, -99.31) * mm});
            skLineSegment(sketch, "E14.6.15.4", {"start": v(100.38, -99.31) * mm, "end": v(98.8, -102.04) * mm});
            skCircle(sketch, "E14.9.15.4", {"center": v(97.23, -99.31) * mm, "radius": 2.73 * mm, "construction": true});
            skLineSegment(sketch, "E14.11.15.4", {"start": v(98.8, -102.04) * mm, "end": v(95.65, -102.04) * mm});
            skLineSegment(sketch, "E14.14.15.4", {"start": v(95.65, -102.04) * mm, "end": v(94.07, -99.31) * mm});
            skLineSegment(sketch, "E14.17.15.4", {"start": v(94.07, -99.31) * mm, "end": v(95.65, -96.58) * mm});
            skLineSegment(sketch, "E14.0.15.5", {"start": v(95.65, -87.95) * mm, "end": v(98.8, -87.95) * mm});
            skLineSegment(sketch, "E14.3.15.5", {"start": v(98.8, -87.95) * mm, "end": v(100.38, -90.68) * mm});
            skLineSegment(sketch, "E14.6.15.5", {"start": v(100.38, -90.68) * mm, "end": v(98.8, -93.4) * mm});
            skCircle(sketch, "E14.9.15.5", {"center": v(97.23, -90.68) * mm, "radius": 2.73 * mm, "construction": true});
            skLineSegment(sketch, "E14.11.15.5", {"start": v(98.8, -93.4) * mm, "end": v(95.65, -93.4) * mm});
            skLineSegment(sketch, "E14.14.15.5", {"start": v(95.65, -93.4) * mm, "end": v(94.07, -90.68) * mm});
            skLineSegment(sketch, "E14.17.15.5", {"start": v(94.07, -90.68) * mm, "end": v(95.65, -87.95) * mm});
            skLineSegment(sketch, "E14.0.15.6", {"start": v(95.65, -79.31) * mm, "end": v(98.8, -79.31) * mm});
            skLineSegment(sketch, "E14.3.15.6", {"start": v(98.8, -79.31) * mm, "end": v(100.38, -82.04) * mm});
            skLineSegment(sketch, "E14.6.15.6", {"start": v(100.38, -82.04) * mm, "end": v(98.8, -84.77) * mm});
            skCircle(sketch, "E14.9.15.6", {"center": v(97.23, -82.04) * mm, "radius": 2.73 * mm, "construction": true});
            skLineSegment(sketch, "E14.11.15.6", {"start": v(98.8, -84.77) * mm, "end": v(95.65, -84.77) * mm});
            skLineSegment(sketch, "E14.14.15.6", {"start": v(95.65, -84.77) * mm, "end": v(94.07, -82.04) * mm});
            skLineSegment(sketch, "E14.17.15.6", {"start": v(94.07, -82.04) * mm, "end": v(95.65, -79.31) * mm});
            skLineSegment(sketch, "E14.0.15.7", {"start": v(95.65, -70.68) * mm, "end": v(98.8, -70.68) * mm});
            skLineSegment(sketch, "E14.3.15.7", {"start": v(98.8, -70.68) * mm, "end": v(100.38, -73.4) * mm});
            skLineSegment(sketch, "E14.6.15.7", {"start": v(100.38, -73.4) * mm, "end": v(98.8, -76.14) * mm});
            skCircle(sketch, "E14.9.15.7", {"center": v(97.23, -73.4) * mm, "radius": 2.73 * mm, "construction": true});
            skLineSegment(sketch, "E14.11.15.7", {"start": v(98.8, -76.14) * mm, "end": v(95.65, -76.14) * mm});
            skLineSegment(sketch, "E14.14.15.7", {"start": v(95.65, -76.14) * mm, "end": v(94.07, -73.4) * mm});
            skLineSegment(sketch, "E14.17.15.7", {"start": v(94.07, -73.4) * mm, "end": v(95.65, -70.68) * mm});
            skLineSegment(sketch, "E14.0.15.8", {"start": v(95.65, -62.04) * mm, "end": v(98.8, -62.04) * mm});
            skLineSegment(sketch, "E14.3.15.8", {"start": v(98.8, -62.04) * mm, "end": v(100.38, -64.77) * mm});
            skLineSegment(sketch, "E14.6.15.8", {"start": v(100.38, -64.77) * mm, "end": v(98.8, -67.5) * mm});
            skCircle(sketch, "E14.9.15.8", {"center": v(97.23, -64.77) * mm, "radius": 2.73 * mm, "construction": true});
            skLineSegment(sketch, "E14.11.15.8", {"start": v(98.8, -67.5) * mm, "end": v(95.65, -67.5) * mm});
            skLineSegment(sketch, "E14.14.15.8", {"start": v(95.65, -67.5) * mm, "end": v(94.07, -64.77) * mm});
            skLineSegment(sketch, "E14.17.15.8", {"start": v(94.07, -64.77) * mm, "end": v(95.65, -62.04) * mm});
            skLineSegment(sketch, "E14.0.15.9", {"start": v(95.65, -53.4) * mm, "end": v(98.8, -53.4) * mm});
            skLineSegment(sketch, "E14.3.15.9", {"start": v(98.8, -53.4) * mm, "end": v(100.38, -56.13) * mm});
            skLineSegment(sketch, "E14.6.15.9", {"start": v(100.38, -56.13) * mm, "end": v(98.8, -58.86) * mm});
            skCircle(sketch, "E14.9.15.9", {"center": v(97.23, -56.13) * mm, "radius": 2.73 * mm, "construction": true});
            skLineSegment(sketch, "E14.11.15.9", {"start": v(98.8, -58.86) * mm, "end": v(95.65, -58.86) * mm});
            skLineSegment(sketch, "E14.14.15.9", {"start": v(95.65, -58.86) * mm, "end": v(94.07, -56.13) * mm});
            skLineSegment(sketch, "E14.17.15.9", {"start": v(94.07, -56.13) * mm, "end": v(95.65, -53.4) * mm});
            skLineSegment(sketch, "E14.0.15.10", {"start": v(95.65, -44.77) * mm, "end": v(98.8, -44.77) * mm});
            skLineSegment(sketch, "E14.3.15.10", {"start": v(98.8, -44.77) * mm, "end": v(100.38, -47.5) * mm});
            skLineSegment(sketch, "E14.6.15.10", {"start": v(100.38, -47.5) * mm, "end": v(98.8, -50.23) * mm});
            skCircle(sketch, "E14.9.15.10", {"center": v(97.23, -47.5) * mm, "radius": 2.73 * mm, "construction": true});
            skLineSegment(sketch, "E14.11.15.10", {"start": v(98.8, -50.23) * mm, "end": v(95.65, -50.23) * mm});
            skLineSegment(sketch, "E14.14.15.10", {"start": v(95.65, -50.23) * mm, "end": v(94.07, -47.5) * mm});
            skLineSegment(sketch, "E14.17.15.10", {"start": v(94.07, -47.5) * mm, "end": v(95.65, -44.77) * mm});
            skLineSegment(sketch, "E14.0.15.11", {"start": v(95.65, -36.13) * mm, "end": v(98.8, -36.13) * mm});
            skLineSegment(sketch, "E14.3.15.11", {"start": v(98.8, -36.13) * mm, "end": v(100.38, -38.86) * mm});
            skLineSegment(sketch, "E14.6.15.11", {"start": v(100.38, -38.86) * mm, "end": v(98.8, -41.6) * mm});
            skCircle(sketch, "E14.9.15.11", {"center": v(97.23, -38.86) * mm, "radius": 2.73 * mm, "construction": true});
            skLineSegment(sketch, "E14.11.15.11", {"start": v(98.8, -41.6) * mm, "end": v(95.65, -41.6) * mm});
            skLineSegment(sketch, "E14.14.15.11", {"start": v(95.65, -41.6) * mm, "end": v(94.07, -38.86) * mm});
            skLineSegment(sketch, "E14.17.15.11", {"start": v(94.07, -38.86) * mm, "end": v(95.65, -36.13) * mm});
            skLineSegment(sketch, "E14.0.15.12", {"start": v(95.65, -27.5) * mm, "end": v(98.8, -27.5) * mm});
            skLineSegment(sketch, "E14.3.15.12", {"start": v(98.8, -27.5) * mm, "end": v(100.38, -30.23) * mm});
            skLineSegment(sketch, "E14.6.15.12", {"start": v(100.38, -30.23) * mm, "end": v(98.8, -32.96) * mm});
            skCircle(sketch, "E14.9.15.12", {"center": v(97.23, -30.23) * mm, "radius": 2.73 * mm, "construction": true});
            skLineSegment(sketch, "E14.11.15.12", {"start": v(98.8, -32.96) * mm, "end": v(95.65, -32.96) * mm});
            skLineSegment(sketch, "E14.14.15.12", {"start": v(95.65, -32.96) * mm, "end": v(94.07, -30.23) * mm});
            skLineSegment(sketch, "E14.17.15.12", {"start": v(94.07, -30.23) * mm, "end": v(95.65, -27.5) * mm});
            skLineSegment(sketch, "E14.0.15.13", {"start": v(95.65, -18.86) * mm, "end": v(98.8, -18.86) * mm});
            skLineSegment(sketch, "E14.3.15.13", {"start": v(98.8, -18.86) * mm, "end": v(100.38, -21.6) * mm});
            skLineSegment(sketch, "E14.6.15.13", {"start": v(100.38, -21.6) * mm, "end": v(98.8, -24.32) * mm});
            skCircle(sketch, "E14.9.15.13", {"center": v(97.23, -21.6) * mm, "radius": 2.73 * mm, "construction": true});
            skLineSegment(sketch, "E14.11.15.13", {"start": v(98.8, -24.32) * mm, "end": v(95.65, -24.32) * mm});
            skLineSegment(sketch, "E14.14.15.13", {"start": v(95.65, -24.32) * mm, "end": v(94.07, -21.6) * mm});
            skLineSegment(sketch, "E14.17.15.13", {"start": v(94.07, -21.59) * mm, "end": v(95.65, -18.86) * mm});
            skLineSegment(sketch, "E14.0.15.14", {"start": v(95.65, -10.22) * mm, "end": v(98.8, -10.22) * mm});
            skLineSegment(sketch, "E14.3.15.14", {"start": v(98.8, -10.22) * mm, "end": v(100.38, -12.95) * mm});
            skLineSegment(sketch, "E14.6.15.14", {"start": v(100.38, -12.95) * mm, "end": v(98.8, -15.68) * mm});
            skCircle(sketch, "E14.9.15.14", {"center": v(97.23, -12.95) * mm, "radius": 2.73 * mm, "construction": true});
            skLineSegment(sketch, "E14.11.15.14", {"start": v(98.8, -15.68) * mm, "end": v(95.65, -15.68) * mm});
            skLineSegment(sketch, "E14.14.15.14", {"start": v(95.65, -15.68) * mm, "end": v(94.07, -12.95) * mm});
            skLineSegment(sketch, "E14.17.15.14", {"start": v(94.07, -12.95) * mm, "end": v(95.65, -10.22) * mm});
            skLineSegment(sketch, "E14.0.15.15", {"start": v(95.65, -1.59) * mm, "end": v(98.8, -1.59) * mm});
            skLineSegment(sketch, "E14.3.15.15", {"start": v(98.8, -1.59) * mm, "end": v(100.38, -4.32) * mm});
            skLineSegment(sketch, "E14.6.15.15", {"start": v(100.38, -4.32) * mm, "end": v(98.8, -7.05) * mm});
            skCircle(sketch, "E14.9.15.15", {"center": v(97.23, -4.32) * mm, "radius": 2.73 * mm, "construction": true});
            skLineSegment(sketch, "E14.11.15.15", {"start": v(98.8, -7.05) * mm, "end": v(95.65, -7.05) * mm});
            skLineSegment(sketch, "E14.14.15.15", {"start": v(95.65, -7.05) * mm, "end": v(94.07, -4.32) * mm});
            skLineSegment(sketch, "E14.17.15.15", {"start": v(94.07, -4.32) * mm, "end": v(95.65, -1.59) * mm});
            skLineSegment(sketch, "E14.0.15.16", {"start": v(95.65, 7.05) * mm, "end": v(98.8, 7.05) * mm});
            skLineSegment(sketch, "E14.3.15.16", {"start": v(98.8, 7.05) * mm, "end": v(100.38, 4.32) * mm});
            skLineSegment(sketch, "E14.6.15.16", {"start": v(100.38, 4.32) * mm, "end": v(98.8, 1.59) * mm});
            skCircle(sketch, "E14.9.15.16", {"center": v(97.23, 4.32) * mm, "radius": 2.73 * mm, "construction": true});
            skLineSegment(sketch, "E14.11.15.16", {"start": v(98.8, 1.59) * mm, "end": v(95.65, 1.59) * mm});
            skLineSegment(sketch, "E14.14.15.16", {"start": v(95.65, 1.59) * mm, "end": v(94.07, 4.32) * mm});
            skLineSegment(sketch, "E14.17.15.16", {"start": v(94.07, 4.32) * mm, "end": v(95.65, 7.05) * mm});
            skLineSegment(sketch, "E14.0.15.17", {"start": v(95.65, 15.68) * mm, "end": v(98.8, 15.68) * mm});
            skLineSegment(sketch, "E14.3.15.17", {"start": v(98.8, 15.68) * mm, "end": v(100.38, 12.95) * mm});
            skLineSegment(sketch, "E14.6.15.17", {"start": v(100.38, 12.95) * mm, "end": v(98.8, 10.22) * mm});
            skCircle(sketch, "E14.9.15.17", {"center": v(97.23, 12.95) * mm, "radius": 2.73 * mm, "construction": true});
            skLineSegment(sketch, "E14.11.15.17", {"start": v(98.8, 10.22) * mm, "end": v(95.65, 10.22) * mm});
            skLineSegment(sketch, "E14.14.15.17", {"start": v(95.65, 10.22) * mm, "end": v(94.07, 12.95) * mm});
            skLineSegment(sketch, "E14.17.15.17", {"start": v(94.07, 12.95) * mm, "end": v(95.65, 15.68) * mm});
            skLineSegment(sketch, "E14.0.15.18", {"start": v(95.65, 24.32) * mm, "end": v(98.8, 24.32) * mm});
            skLineSegment(sketch, "E14.3.15.18", {"start": v(98.8, 24.32) * mm, "end": v(100.38, 21.59) * mm});
            skLineSegment(sketch, "E14.6.15.18", {"start": v(100.38, 21.59) * mm, "end": v(98.8, 18.86) * mm});
            skCircle(sketch, "E14.9.15.18", {"center": v(97.23, 21.59) * mm, "radius": 2.73 * mm, "construction": true});
            skLineSegment(sketch, "E14.11.15.18", {"start": v(98.8, 18.86) * mm, "end": v(95.65, 18.86) * mm});
            skLineSegment(sketch, "E14.14.15.18", {"start": v(95.65, 18.86) * mm, "end": v(94.07, 21.59) * mm});
            skLineSegment(sketch, "E14.17.15.18", {"start": v(94.07, 21.59) * mm, "end": v(95.65, 24.32) * mm});
            skLineSegment(sketch, "E14.0.15.19", {"start": v(95.65, 32.96) * mm, "end": v(98.8, 32.96) * mm});
            skLineSegment(sketch, "E14.3.15.19", {"start": v(98.8, 32.96) * mm, "end": v(100.38, 30.23) * mm});
            skLineSegment(sketch, "E14.6.15.19", {"start": v(100.38, 30.23) * mm, "end": v(98.8, 27.5) * mm});
            skCircle(sketch, "E14.9.15.19", {"center": v(97.23, 30.23) * mm, "radius": 2.73 * mm, "construction": true});
            skLineSegment(sketch, "E14.11.15.19", {"start": v(98.8, 27.5) * mm, "end": v(95.65, 27.5) * mm});
            skLineSegment(sketch, "E14.14.15.19", {"start": v(95.65, 27.5) * mm, "end": v(94.07, 30.23) * mm});
            skLineSegment(sketch, "E14.17.15.19", {"start": v(94.07, 30.23) * mm, "end": v(95.65, 32.96) * mm});
            skLineSegment(sketch, "E14.0.16.0", {"start": v(110.6, -131.13) * mm, "end": v(113.76, -131.13) * mm});
            skLineSegment(sketch, "E14.3.16.0", {"start": v(113.76, -131.13) * mm, "end": v(115.34, -133.86) * mm});
            skLineSegment(sketch, "E14.6.16.0", {"start": v(115.34, -133.86) * mm, "end": v(113.76, -136.59) * mm});
            skCircle(sketch, "E14.9.16.0", {"center": v(112.19, -133.86) * mm, "radius": 2.73 * mm, "construction": true});
            skLineSegment(sketch, "E14.11.16.0", {"start": v(113.76, -136.59) * mm, "end": v(110.6, -136.59) * mm});
            skLineSegment(sketch, "E14.14.16.0", {"start": v(110.6, -136.59) * mm, "end": v(109.03, -133.86) * mm});
            skLineSegment(sketch, "E14.17.16.0", {"start": v(109.03, -133.86) * mm, "end": v(110.6, -131.13) * mm});
            skLineSegment(sketch, "E14.0.16.1", {"start": v(110.6, -122.5) * mm, "end": v(113.76, -122.5) * mm});
            skLineSegment(sketch, "E14.3.16.1", {"start": v(113.76, -122.5) * mm, "end": v(115.34, -125.22) * mm});
            skLineSegment(sketch, "E14.6.16.1", {"start": v(115.34, -125.22) * mm, "end": v(113.76, -127.95) * mm});
            skCircle(sketch, "E14.9.16.1", {"center": v(112.19, -125.22) * mm, "radius": 2.73 * mm, "construction": true});
            skLineSegment(sketch, "E14.11.16.1", {"start": v(113.76, -127.95) * mm, "end": v(110.6, -127.95) * mm});
            skLineSegment(sketch, "E14.14.16.1", {"start": v(110.6, -127.95) * mm, "end": v(109.03, -125.22) * mm});
            skLineSegment(sketch, "E14.17.16.1", {"start": v(109.03, -125.22) * mm, "end": v(110.6, -122.5) * mm});
            skLineSegment(sketch, "E14.0.16.2", {"start": v(110.6, -113.86) * mm, "end": v(113.76, -113.86) * mm});
            skLineSegment(sketch, "E14.3.16.2", {"start": v(113.76, -113.86) * mm, "end": v(115.34, -116.59) * mm});
            skLineSegment(sketch, "E14.6.16.2", {"start": v(115.34, -116.59) * mm, "end": v(113.76, -119.32) * mm});
            skCircle(sketch, "E14.9.16.2", {"center": v(112.19, -116.59) * mm, "radius": 2.73 * mm, "construction": true});
            skLineSegment(sketch, "E14.11.16.2", {"start": v(113.76, -119.32) * mm, "end": v(110.6, -119.32) * mm});
            skLineSegment(sketch, "E14.14.16.2", {"start": v(110.6, -119.32) * mm, "end": v(109.03, -116.59) * mm});
            skLineSegment(sketch, "E14.17.16.2", {"start": v(109.03, -116.59) * mm, "end": v(110.6, -113.86) * mm});
            skLineSegment(sketch, "E14.0.16.3", {"start": v(110.6, -105.22) * mm, "end": v(113.76, -105.22) * mm});
            skLineSegment(sketch, "E14.3.16.3", {"start": v(113.76, -105.22) * mm, "end": v(115.34, -107.95) * mm});
            skLineSegment(sketch, "E14.6.16.3", {"start": v(115.34, -107.95) * mm, "end": v(113.76, -110.68) * mm});
            skCircle(sketch, "E14.9.16.3", {"center": v(112.19, -107.95) * mm, "radius": 2.73 * mm, "construction": true});
            skLineSegment(sketch, "E14.11.16.3", {"start": v(113.76, -110.68) * mm, "end": v(110.6, -110.68) * mm});
            skLineSegment(sketch, "E14.14.16.3", {"start": v(110.6, -110.68) * mm, "end": v(109.03, -107.95) * mm});
            skLineSegment(sketch, "E14.17.16.3", {"start": v(109.03, -107.95) * mm, "end": v(110.6, -105.22) * mm});
            skLineSegment(sketch, "E14.0.16.4", {"start": v(110.6, -96.58) * mm, "end": v(113.76, -96.58) * mm});
            skLineSegment(sketch, "E14.3.16.4", {"start": v(113.76, -96.58) * mm, "end": v(115.34, -99.31) * mm});
            skLineSegment(sketch, "E14.6.16.4", {"start": v(115.34, -99.31) * mm, "end": v(113.76, -102.04) * mm});
            skCircle(sketch, "E14.9.16.4", {"center": v(112.19, -99.31) * mm, "radius": 2.73 * mm, "construction": true});
            skLineSegment(sketch, "E14.11.16.4", {"start": v(113.76, -102.04) * mm, "end": v(110.6, -102.04) * mm});
            skLineSegment(sketch, "E14.14.16.4", {"start": v(110.6, -102.04) * mm, "end": v(109.03, -99.31) * mm});
            skLineSegment(sketch, "E14.17.16.4", {"start": v(109.03, -99.31) * mm, "end": v(110.6, -96.58) * mm});
            skLineSegment(sketch, "E14.0.16.5", {"start": v(110.6, -87.95) * mm, "end": v(113.76, -87.95) * mm});
            skLineSegment(sketch, "E14.3.16.5", {"start": v(113.76, -87.95) * mm, "end": v(115.34, -90.68) * mm});
            skLineSegment(sketch, "E14.6.16.5", {"start": v(115.34, -90.68) * mm, "end": v(113.76, -93.4) * mm});
            skCircle(sketch, "E14.9.16.5", {"center": v(112.19, -90.68) * mm, "radius": 2.73 * mm, "construction": true});
            skLineSegment(sketch, "E14.11.16.5", {"start": v(113.76, -93.4) * mm, "end": v(110.6, -93.4) * mm});
            skLineSegment(sketch, "E14.14.16.5", {"start": v(110.6, -93.4) * mm, "end": v(109.03, -90.68) * mm});
            skLineSegment(sketch, "E14.17.16.5", {"start": v(109.03, -90.68) * mm, "end": v(110.6, -87.95) * mm});
            skLineSegment(sketch, "E14.0.16.6", {"start": v(110.6, -79.31) * mm, "end": v(113.76, -79.31) * mm});
            skLineSegment(sketch, "E14.3.16.6", {"start": v(113.76, -79.31) * mm, "end": v(115.34, -82.04) * mm});
            skLineSegment(sketch, "E14.6.16.6", {"start": v(115.34, -82.04) * mm, "end": v(113.76, -84.77) * mm});
            skCircle(sketch, "E14.9.16.6", {"center": v(112.19, -82.04) * mm, "radius": 2.73 * mm, "construction": true});
            skLineSegment(sketch, "E14.11.16.6", {"start": v(113.76, -84.77) * mm, "end": v(110.6, -84.77) * mm});
            skLineSegment(sketch, "E14.14.16.6", {"start": v(110.6, -84.77) * mm, "end": v(109.03, -82.04) * mm});
            skLineSegment(sketch, "E14.17.16.6", {"start": v(109.03, -82.04) * mm, "end": v(110.6, -79.31) * mm});
            skLineSegment(sketch, "E14.0.16.7", {"start": v(110.6, -70.68) * mm, "end": v(113.76, -70.68) * mm});
            skLineSegment(sketch, "E14.3.16.7", {"start": v(113.76, -70.68) * mm, "end": v(115.34, -73.4) * mm});
            skLineSegment(sketch, "E14.6.16.7", {"start": v(115.34, -73.4) * mm, "end": v(113.76, -76.14) * mm});
            skCircle(sketch, "E14.9.16.7", {"center": v(112.19, -73.4) * mm, "radius": 2.73 * mm, "construction": true});
            skLineSegment(sketch, "E14.11.16.7", {"start": v(113.76, -76.14) * mm, "end": v(110.6, -76.14) * mm});
            skLineSegment(sketch, "E14.14.16.7", {"start": v(110.6, -76.14) * mm, "end": v(109.03, -73.4) * mm});
            skLineSegment(sketch, "E14.17.16.7", {"start": v(109.03, -73.4) * mm, "end": v(110.6, -70.68) * mm});
            skLineSegment(sketch, "E14.0.16.8", {"start": v(110.6, -62.04) * mm, "end": v(113.76, -62.04) * mm});
            skLineSegment(sketch, "E14.3.16.8", {"start": v(113.76, -62.04) * mm, "end": v(115.34, -64.77) * mm});
            skLineSegment(sketch, "E14.6.16.8", {"start": v(115.34, -64.77) * mm, "end": v(113.76, -67.5) * mm});
            skCircle(sketch, "E14.9.16.8", {"center": v(112.19, -64.77) * mm, "radius": 2.73 * mm, "construction": true});
            skLineSegment(sketch, "E14.11.16.8", {"start": v(113.76, -67.5) * mm, "end": v(110.6, -67.5) * mm});
            skLineSegment(sketch, "E14.14.16.8", {"start": v(110.6, -67.5) * mm, "end": v(109.03, -64.77) * mm});
            skLineSegment(sketch, "E14.17.16.8", {"start": v(109.03, -64.77) * mm, "end": v(110.6, -62.04) * mm});
            skLineSegment(sketch, "E14.0.16.9", {"start": v(110.6, -53.4) * mm, "end": v(113.76, -53.4) * mm});
            skLineSegment(sketch, "E14.3.16.9", {"start": v(113.76, -53.4) * mm, "end": v(115.34, -56.13) * mm});
            skLineSegment(sketch, "E14.6.16.9", {"start": v(115.34, -56.13) * mm, "end": v(113.76, -58.86) * mm});
            skCircle(sketch, "E14.9.16.9", {"center": v(112.19, -56.13) * mm, "radius": 2.73 * mm, "construction": true});
            skLineSegment(sketch, "E14.11.16.9", {"start": v(113.76, -58.86) * mm, "end": v(110.6, -58.86) * mm});
            skLineSegment(sketch, "E14.14.16.9", {"start": v(110.6, -58.86) * mm, "end": v(109.03, -56.13) * mm});
            skLineSegment(sketch, "E14.17.16.9", {"start": v(109.03, -56.13) * mm, "end": v(110.6, -53.4) * mm});
            skLineSegment(sketch, "E14.0.16.10", {"start": v(110.6, -44.77) * mm, "end": v(113.76, -44.77) * mm});
            skLineSegment(sketch, "E14.3.16.10", {"start": v(113.76, -44.77) * mm, "end": v(115.34, -47.5) * mm});
            skLineSegment(sketch, "E14.6.16.10", {"start": v(115.34, -47.5) * mm, "end": v(113.76, -50.23) * mm});
            skCircle(sketch, "E14.9.16.10", {"center": v(112.19, -47.5) * mm, "radius": 2.73 * mm, "construction": true});
            skLineSegment(sketch, "E14.11.16.10", {"start": v(113.76, -50.23) * mm, "end": v(110.6, -50.23) * mm});
            skLineSegment(sketch, "E14.14.16.10", {"start": v(110.6, -50.23) * mm, "end": v(109.03, -47.5) * mm});
            skLineSegment(sketch, "E14.17.16.10", {"start": v(109.03, -47.5) * mm, "end": v(110.6, -44.77) * mm});
            skLineSegment(sketch, "E14.0.16.11", {"start": v(110.6, -36.13) * mm, "end": v(113.76, -36.13) * mm});
            skLineSegment(sketch, "E14.3.16.11", {"start": v(113.76, -36.13) * mm, "end": v(115.34, -38.86) * mm});
            skLineSegment(sketch, "E14.6.16.11", {"start": v(115.34, -38.86) * mm, "end": v(113.76, -41.6) * mm});
            skCircle(sketch, "E14.9.16.11", {"center": v(112.19, -38.86) * mm, "radius": 2.73 * mm, "construction": true});
            skLineSegment(sketch, "E14.11.16.11", {"start": v(113.76, -41.6) * mm, "end": v(110.6, -41.6) * mm});
            skLineSegment(sketch, "E14.14.16.11", {"start": v(110.6, -41.6) * mm, "end": v(109.03, -38.86) * mm});
            skLineSegment(sketch, "E14.17.16.11", {"start": v(109.03, -38.86) * mm, "end": v(110.6, -36.13) * mm});
            skLineSegment(sketch, "E14.0.16.12", {"start": v(110.6, -27.5) * mm, "end": v(113.76, -27.5) * mm});
            skLineSegment(sketch, "E14.3.16.12", {"start": v(113.76, -27.5) * mm, "end": v(115.34, -30.23) * mm});
            skLineSegment(sketch, "E14.6.16.12", {"start": v(115.34, -30.23) * mm, "end": v(113.76, -32.96) * mm});
            skCircle(sketch, "E14.9.16.12", {"center": v(112.19, -30.23) * mm, "radius": 2.73 * mm, "construction": true});
            skLineSegment(sketch, "E14.11.16.12", {"start": v(113.76, -32.96) * mm, "end": v(110.6, -32.96) * mm});
            skLineSegment(sketch, "E14.14.16.12", {"start": v(110.6, -32.96) * mm, "end": v(109.03, -30.23) * mm});
            skLineSegment(sketch, "E14.17.16.12", {"start": v(109.03, -30.23) * mm, "end": v(110.6, -27.5) * mm});
            skLineSegment(sketch, "E14.0.16.13", {"start": v(110.6, -18.86) * mm, "end": v(113.76, -18.86) * mm});
            skLineSegment(sketch, "E14.3.16.13", {"start": v(113.76, -18.86) * mm, "end": v(115.34, -21.6) * mm});
            skLineSegment(sketch, "E14.6.16.13", {"start": v(115.34, -21.6) * mm, "end": v(113.76, -24.32) * mm});
            skCircle(sketch, "E14.9.16.13", {"center": v(112.19, -21.6) * mm, "radius": 2.73 * mm, "construction": true});
            skLineSegment(sketch, "E14.11.16.13", {"start": v(113.76, -24.32) * mm, "end": v(110.6, -24.32) * mm});
            skLineSegment(sketch, "E14.14.16.13", {"start": v(110.6, -24.32) * mm, "end": v(109.03, -21.6) * mm});
            skLineSegment(sketch, "E14.17.16.13", {"start": v(109.03, -21.59) * mm, "end": v(110.6, -18.86) * mm});
            skLineSegment(sketch, "E14.0.16.14", {"start": v(110.6, -10.22) * mm, "end": v(113.76, -10.22) * mm});
            skLineSegment(sketch, "E14.3.16.14", {"start": v(113.76, -10.22) * mm, "end": v(115.34, -12.95) * mm});
            skLineSegment(sketch, "E14.6.16.14", {"start": v(115.34, -12.95) * mm, "end": v(113.76, -15.68) * mm});
            skCircle(sketch, "E14.9.16.14", {"center": v(112.19, -12.95) * mm, "radius": 2.73 * mm, "construction": true});
            skLineSegment(sketch, "E14.11.16.14", {"start": v(113.76, -15.68) * mm, "end": v(110.6, -15.68) * mm});
            skLineSegment(sketch, "E14.14.16.14", {"start": v(110.6, -15.68) * mm, "end": v(109.03, -12.95) * mm});
            skLineSegment(sketch, "E14.17.16.14", {"start": v(109.03, -12.95) * mm, "end": v(110.6, -10.22) * mm});
            skLineSegment(sketch, "E14.0.16.15", {"start": v(110.6, -1.59) * mm, "end": v(113.76, -1.59) * mm});
            skLineSegment(sketch, "E14.3.16.15", {"start": v(113.76, -1.59) * mm, "end": v(115.34, -4.32) * mm});
            skLineSegment(sketch, "E14.6.16.15", {"start": v(115.34, -4.32) * mm, "end": v(113.76, -7.05) * mm});
            skCircle(sketch, "E14.9.16.15", {"center": v(112.19, -4.32) * mm, "radius": 2.73 * mm, "construction": true});
            skLineSegment(sketch, "E14.11.16.15", {"start": v(113.76, -7.05) * mm, "end": v(110.6, -7.05) * mm});
            skLineSegment(sketch, "E14.14.16.15", {"start": v(110.6, -7.05) * mm, "end": v(109.03, -4.32) * mm});
            skLineSegment(sketch, "E14.17.16.15", {"start": v(109.03, -4.32) * mm, "end": v(110.6, -1.59) * mm});
            skLineSegment(sketch, "E14.0.16.16", {"start": v(110.6, 7.05) * mm, "end": v(113.76, 7.05) * mm});
            skLineSegment(sketch, "E14.3.16.16", {"start": v(113.76, 7.05) * mm, "end": v(115.34, 4.32) * mm});
            skLineSegment(sketch, "E14.6.16.16", {"start": v(115.34, 4.32) * mm, "end": v(113.76, 1.59) * mm});
            skCircle(sketch, "E14.9.16.16", {"center": v(112.19, 4.32) * mm, "radius": 2.73 * mm, "construction": true});
            skLineSegment(sketch, "E14.11.16.16", {"start": v(113.76, 1.59) * mm, "end": v(110.6, 1.59) * mm});
            skLineSegment(sketch, "E14.14.16.16", {"start": v(110.6, 1.59) * mm, "end": v(109.03, 4.32) * mm});
            skLineSegment(sketch, "E14.17.16.16", {"start": v(109.03, 4.32) * mm, "end": v(110.6, 7.05) * mm});
            skLineSegment(sketch, "E14.0.16.17", {"start": v(110.6, 15.68) * mm, "end": v(113.76, 15.68) * mm});
            skLineSegment(sketch, "E14.3.16.17", {"start": v(113.76, 15.68) * mm, "end": v(115.34, 12.95) * mm});
            skLineSegment(sketch, "E14.6.16.17", {"start": v(115.34, 12.95) * mm, "end": v(113.76, 10.22) * mm});
            skCircle(sketch, "E14.9.16.17", {"center": v(112.19, 12.95) * mm, "radius": 2.73 * mm, "construction": true});
            skLineSegment(sketch, "E14.11.16.17", {"start": v(113.76, 10.22) * mm, "end": v(110.6, 10.22) * mm});
            skLineSegment(sketch, "E14.14.16.17", {"start": v(110.6, 10.22) * mm, "end": v(109.03, 12.95) * mm});
            skLineSegment(sketch, "E14.17.16.17", {"start": v(109.03, 12.95) * mm, "end": v(110.6, 15.68) * mm});
            skLineSegment(sketch, "E14.0.16.18", {"start": v(110.6, 24.32) * mm, "end": v(113.76, 24.32) * mm});
            skLineSegment(sketch, "E14.3.16.18", {"start": v(113.76, 24.32) * mm, "end": v(115.34, 21.59) * mm});
            skLineSegment(sketch, "E14.6.16.18", {"start": v(115.34, 21.59) * mm, "end": v(113.76, 18.86) * mm});
            skCircle(sketch, "E14.9.16.18", {"center": v(112.19, 21.59) * mm, "radius": 2.73 * mm, "construction": true});
            skLineSegment(sketch, "E14.11.16.18", {"start": v(113.76, 18.86) * mm, "end": v(110.6, 18.86) * mm});
            skLineSegment(sketch, "E14.14.16.18", {"start": v(110.6, 18.86) * mm, "end": v(109.03, 21.59) * mm});
            skLineSegment(sketch, "E14.17.16.18", {"start": v(109.03, 21.59) * mm, "end": v(110.6, 24.32) * mm});
            skLineSegment(sketch, "E14.0.16.19", {"start": v(110.6, 32.96) * mm, "end": v(113.76, 32.96) * mm});
            skLineSegment(sketch, "E14.3.16.19", {"start": v(113.76, 32.96) * mm, "end": v(115.34, 30.23) * mm});
            skLineSegment(sketch, "E14.6.16.19", {"start": v(115.34, 30.23) * mm, "end": v(113.76, 27.5) * mm});
            skCircle(sketch, "E14.9.16.19", {"center": v(112.19, 30.23) * mm, "radius": 2.73 * mm, "construction": true});
            skLineSegment(sketch, "E14.11.16.19", {"start": v(113.76, 27.5) * mm, "end": v(110.6, 27.5) * mm});
            skLineSegment(sketch, "E14.14.16.19", {"start": v(110.6, 27.5) * mm, "end": v(109.03, 30.23) * mm});
            skLineSegment(sketch, "E14.17.16.19", {"start": v(109.03, 30.23) * mm, "end": v(110.6, 32.96) * mm});
            skLineSegment(sketch, "E14.0.17.0", {"start": v(125.57, -131.13) * mm, "end": v(128.72, -131.13) * mm});
            skLineSegment(sketch, "E14.3.17.0", {"start": v(128.72, -131.13) * mm, "end": v(130.3, -133.86) * mm});
            skLineSegment(sketch, "E14.6.17.0", {"start": v(130.3, -133.86) * mm, "end": v(128.72, -136.59) * mm});
            skCircle(sketch, "E14.9.17.0", {"center": v(127.14, -133.86) * mm, "radius": 2.73 * mm, "construction": true});
            skLineSegment(sketch, "E14.11.17.0", {"start": v(128.72, -136.59) * mm, "end": v(125.57, -136.59) * mm});
            skLineSegment(sketch, "E14.14.17.0", {"start": v(125.57, -136.59) * mm, "end": v(124, -133.86) * mm});
            skLineSegment(sketch, "E14.17.17.0", {"start": v(124, -133.86) * mm, "end": v(125.57, -131.13) * mm});
            skLineSegment(sketch, "E14.0.17.1", {"start": v(125.57, -122.5) * mm, "end": v(128.72, -122.5) * mm});
            skLineSegment(sketch, "E14.3.17.1", {"start": v(128.72, -122.5) * mm, "end": v(130.3, -125.22) * mm});
            skLineSegment(sketch, "E14.6.17.1", {"start": v(130.3, -125.22) * mm, "end": v(128.72, -127.95) * mm});
            skCircle(sketch, "E14.9.17.1", {"center": v(127.14, -125.22) * mm, "radius": 2.73 * mm, "construction": true});
            skLineSegment(sketch, "E14.11.17.1", {"start": v(128.72, -127.95) * mm, "end": v(125.57, -127.95) * mm});
            skLineSegment(sketch, "E14.14.17.1", {"start": v(125.57, -127.95) * mm, "end": v(124, -125.22) * mm});
            skLineSegment(sketch, "E14.17.17.1", {"start": v(124, -125.22) * mm, "end": v(125.57, -122.5) * mm});
            skLineSegment(sketch, "E14.0.17.2", {"start": v(125.57, -113.86) * mm, "end": v(128.72, -113.86) * mm});
            skLineSegment(sketch, "E14.3.17.2", {"start": v(128.72, -113.86) * mm, "end": v(130.3, -116.59) * mm});
            skLineSegment(sketch, "E14.6.17.2", {"start": v(130.3, -116.59) * mm, "end": v(128.72, -119.32) * mm});
            skCircle(sketch, "E14.9.17.2", {"center": v(127.14, -116.59) * mm, "radius": 2.73 * mm, "construction": true});
            skLineSegment(sketch, "E14.11.17.2", {"start": v(128.72, -119.32) * mm, "end": v(125.57, -119.32) * mm});
            skLineSegment(sketch, "E14.14.17.2", {"start": v(125.57, -119.32) * mm, "end": v(124, -116.59) * mm});
            skLineSegment(sketch, "E14.17.17.2", {"start": v(124, -116.59) * mm, "end": v(125.57, -113.86) * mm});
            skLineSegment(sketch, "E14.0.17.3", {"start": v(125.57, -105.22) * mm, "end": v(128.72, -105.22) * mm});
            skLineSegment(sketch, "E14.3.17.3", {"start": v(128.72, -105.22) * mm, "end": v(130.3, -107.95) * mm});
            skLineSegment(sketch, "E14.6.17.3", {"start": v(130.3, -107.95) * mm, "end": v(128.72, -110.68) * mm});
            skCircle(sketch, "E14.9.17.3", {"center": v(127.14, -107.95) * mm, "radius": 2.73 * mm, "construction": true});
            skLineSegment(sketch, "E14.11.17.3", {"start": v(128.72, -110.68) * mm, "end": v(125.57, -110.68) * mm});
            skLineSegment(sketch, "E14.14.17.3", {"start": v(125.57, -110.68) * mm, "end": v(124, -107.95) * mm});
            skLineSegment(sketch, "E14.17.17.3", {"start": v(124, -107.95) * mm, "end": v(125.57, -105.22) * mm});
            skLineSegment(sketch, "E14.0.17.4", {"start": v(125.57, -96.58) * mm, "end": v(128.72, -96.58) * mm});
            skLineSegment(sketch, "E14.3.17.4", {"start": v(128.72, -96.58) * mm, "end": v(130.3, -99.31) * mm});
            skLineSegment(sketch, "E14.6.17.4", {"start": v(130.3, -99.31) * mm, "end": v(128.72, -102.04) * mm});
            skCircle(sketch, "E14.9.17.4", {"center": v(127.14, -99.31) * mm, "radius": 2.73 * mm, "construction": true});
            skLineSegment(sketch, "E14.11.17.4", {"start": v(128.72, -102.04) * mm, "end": v(125.57, -102.04) * mm});
            skLineSegment(sketch, "E14.14.17.4", {"start": v(125.57, -102.04) * mm, "end": v(124, -99.31) * mm});
            skLineSegment(sketch, "E14.17.17.4", {"start": v(124, -99.31) * mm, "end": v(125.57, -96.58) * mm});
            skLineSegment(sketch, "E14.0.17.5", {"start": v(125.57, -87.95) * mm, "end": v(128.72, -87.95) * mm});
            skLineSegment(sketch, "E14.3.17.5", {"start": v(128.72, -87.95) * mm, "end": v(130.3, -90.68) * mm});
            skLineSegment(sketch, "E14.6.17.5", {"start": v(130.3, -90.68) * mm, "end": v(128.72, -93.4) * mm});
            skCircle(sketch, "E14.9.17.5", {"center": v(127.14, -90.68) * mm, "radius": 2.73 * mm, "construction": true});
            skLineSegment(sketch, "E14.11.17.5", {"start": v(128.72, -93.4) * mm, "end": v(125.57, -93.4) * mm});
            skLineSegment(sketch, "E14.14.17.5", {"start": v(125.57, -93.4) * mm, "end": v(124, -90.68) * mm});
            skLineSegment(sketch, "E14.17.17.5", {"start": v(124, -90.68) * mm, "end": v(125.57, -87.95) * mm});
            skLineSegment(sketch, "E14.0.17.6", {"start": v(125.57, -79.31) * mm, "end": v(128.72, -79.31) * mm});
            skLineSegment(sketch, "E14.3.17.6", {"start": v(128.72, -79.31) * mm, "end": v(130.3, -82.04) * mm});
            skLineSegment(sketch, "E14.6.17.6", {"start": v(130.3, -82.04) * mm, "end": v(128.72, -84.77) * mm});
            skCircle(sketch, "E14.9.17.6", {"center": v(127.14, -82.04) * mm, "radius": 2.73 * mm, "construction": true});
            skLineSegment(sketch, "E14.11.17.6", {"start": v(128.72, -84.77) * mm, "end": v(125.57, -84.77) * mm});
            skLineSegment(sketch, "E14.14.17.6", {"start": v(125.57, -84.77) * mm, "end": v(124, -82.04) * mm});
            skLineSegment(sketch, "E14.17.17.6", {"start": v(124, -82.04) * mm, "end": v(125.57, -79.31) * mm});
            skLineSegment(sketch, "E14.0.17.7", {"start": v(125.57, -70.68) * mm, "end": v(128.72, -70.68) * mm});
            skLineSegment(sketch, "E14.3.17.7", {"start": v(128.72, -70.68) * mm, "end": v(130.3, -73.4) * mm});
            skLineSegment(sketch, "E14.6.17.7", {"start": v(130.3, -73.4) * mm, "end": v(128.72, -76.14) * mm});
            skCircle(sketch, "E14.9.17.7", {"center": v(127.14, -73.4) * mm, "radius": 2.73 * mm, "construction": true});
            skLineSegment(sketch, "E14.11.17.7", {"start": v(128.72, -76.14) * mm, "end": v(125.57, -76.14) * mm});
            skLineSegment(sketch, "E14.14.17.7", {"start": v(125.57, -76.14) * mm, "end": v(124, -73.4) * mm});
            skLineSegment(sketch, "E14.17.17.7", {"start": v(124, -73.4) * mm, "end": v(125.57, -70.68) * mm});
            skLineSegment(sketch, "E14.0.17.8", {"start": v(125.57, -62.04) * mm, "end": v(128.72, -62.04) * mm});
            skLineSegment(sketch, "E14.3.17.8", {"start": v(128.72, -62.04) * mm, "end": v(130.3, -64.77) * mm});
            skLineSegment(sketch, "E14.6.17.8", {"start": v(130.3, -64.77) * mm, "end": v(128.72, -67.5) * mm});
            skCircle(sketch, "E14.9.17.8", {"center": v(127.14, -64.77) * mm, "radius": 2.73 * mm, "construction": true});
            skLineSegment(sketch, "E14.11.17.8", {"start": v(128.72, -67.5) * mm, "end": v(125.57, -67.5) * mm});
            skLineSegment(sketch, "E14.14.17.8", {"start": v(125.57, -67.5) * mm, "end": v(124, -64.77) * mm});
            skLineSegment(sketch, "E14.17.17.8", {"start": v(124, -64.77) * mm, "end": v(125.57, -62.04) * mm});
            skLineSegment(sketch, "E14.0.17.9", {"start": v(125.57, -53.4) * mm, "end": v(128.72, -53.4) * mm});
            skLineSegment(sketch, "E14.3.17.9", {"start": v(128.72, -53.4) * mm, "end": v(130.3, -56.13) * mm});
            skLineSegment(sketch, "E14.6.17.9", {"start": v(130.3, -56.13) * mm, "end": v(128.72, -58.86) * mm});
            skCircle(sketch, "E14.9.17.9", {"center": v(127.14, -56.13) * mm, "radius": 2.73 * mm, "construction": true});
            skLineSegment(sketch, "E14.11.17.9", {"start": v(128.72, -58.86) * mm, "end": v(125.57, -58.86) * mm});
            skLineSegment(sketch, "E14.14.17.9", {"start": v(125.57, -58.86) * mm, "end": v(124, -56.13) * mm});
            skLineSegment(sketch, "E14.17.17.9", {"start": v(124, -56.13) * mm, "end": v(125.57, -53.4) * mm});
            skLineSegment(sketch, "E14.0.17.10", {"start": v(125.57, -44.77) * mm, "end": v(128.72, -44.77) * mm});
            skLineSegment(sketch, "E14.3.17.10", {"start": v(128.72, -44.77) * mm, "end": v(130.3, -47.5) * mm});
            skLineSegment(sketch, "E14.6.17.10", {"start": v(130.3, -47.5) * mm, "end": v(128.72, -50.23) * mm});
            skCircle(sketch, "E14.9.17.10", {"center": v(127.14, -47.5) * mm, "radius": 2.73 * mm, "construction": true});
            skLineSegment(sketch, "E14.11.17.10", {"start": v(128.72, -50.23) * mm, "end": v(125.57, -50.23) * mm});
            skLineSegment(sketch, "E14.14.17.10", {"start": v(125.57, -50.23) * mm, "end": v(124, -47.5) * mm});
            skLineSegment(sketch, "E14.17.17.10", {"start": v(124, -47.5) * mm, "end": v(125.57, -44.77) * mm});
            skLineSegment(sketch, "E14.0.17.11", {"start": v(125.57, -36.13) * mm, "end": v(128.72, -36.13) * mm});
            skLineSegment(sketch, "E14.3.17.11", {"start": v(128.72, -36.13) * mm, "end": v(130.3, -38.86) * mm});
            skLineSegment(sketch, "E14.6.17.11", {"start": v(130.3, -38.86) * mm, "end": v(128.72, -41.6) * mm});
            skCircle(sketch, "E14.9.17.11", {"center": v(127.14, -38.86) * mm, "radius": 2.73 * mm, "construction": true});
            skLineSegment(sketch, "E14.11.17.11", {"start": v(128.72, -41.6) * mm, "end": v(125.57, -41.6) * mm});
            skLineSegment(sketch, "E14.14.17.11", {"start": v(125.57, -41.6) * mm, "end": v(124, -38.86) * mm});
            skLineSegment(sketch, "E14.17.17.11", {"start": v(124, -38.86) * mm, "end": v(125.57, -36.13) * mm});
            skLineSegment(sketch, "E14.0.17.12", {"start": v(125.57, -27.5) * mm, "end": v(128.72, -27.5) * mm});
            skLineSegment(sketch, "E14.3.17.12", {"start": v(128.72, -27.5) * mm, "end": v(130.3, -30.23) * mm});
            skLineSegment(sketch, "E14.6.17.12", {"start": v(130.3, -30.23) * mm, "end": v(128.72, -32.96) * mm});
            skCircle(sketch, "E14.9.17.12", {"center": v(127.14, -30.23) * mm, "radius": 2.73 * mm, "construction": true});
            skLineSegment(sketch, "E14.11.17.12", {"start": v(128.72, -32.96) * mm, "end": v(125.57, -32.96) * mm});
            skLineSegment(sketch, "E14.14.17.12", {"start": v(125.57, -32.96) * mm, "end": v(124, -30.23) * mm});
            skLineSegment(sketch, "E14.17.17.12", {"start": v(124, -30.23) * mm, "end": v(125.57, -27.5) * mm});
            skLineSegment(sketch, "E14.0.17.13", {"start": v(125.57, -18.86) * mm, "end": v(128.72, -18.86) * mm});
            skLineSegment(sketch, "E14.3.17.13", {"start": v(128.72, -18.86) * mm, "end": v(130.3, -21.6) * mm});
            skLineSegment(sketch, "E14.6.17.13", {"start": v(130.3, -21.6) * mm, "end": v(128.72, -24.32) * mm});
            skCircle(sketch, "E14.9.17.13", {"center": v(127.14, -21.6) * mm, "radius": 2.73 * mm, "construction": true});
            skLineSegment(sketch, "E14.11.17.13", {"start": v(128.72, -24.32) * mm, "end": v(125.57, -24.32) * mm});
            skLineSegment(sketch, "E14.14.17.13", {"start": v(125.57, -24.32) * mm, "end": v(124, -21.6) * mm});
            skLineSegment(sketch, "E14.17.17.13", {"start": v(124, -21.59) * mm, "end": v(125.57, -18.86) * mm});
            skLineSegment(sketch, "E14.0.17.14", {"start": v(125.57, -10.22) * mm, "end": v(128.72, -10.22) * mm});
            skLineSegment(sketch, "E14.3.17.14", {"start": v(128.72, -10.22) * mm, "end": v(130.3, -12.95) * mm});
            skLineSegment(sketch, "E14.6.17.14", {"start": v(130.3, -12.95) * mm, "end": v(128.72, -15.68) * mm});
            skCircle(sketch, "E14.9.17.14", {"center": v(127.14, -12.95) * mm, "radius": 2.73 * mm, "construction": true});
            skLineSegment(sketch, "E14.11.17.14", {"start": v(128.72, -15.68) * mm, "end": v(125.57, -15.68) * mm});
            skLineSegment(sketch, "E14.14.17.14", {"start": v(125.57, -15.68) * mm, "end": v(124, -12.95) * mm});
            skLineSegment(sketch, "E14.17.17.14", {"start": v(124, -12.95) * mm, "end": v(125.57, -10.22) * mm});
            skLineSegment(sketch, "E14.0.17.15", {"start": v(125.57, -1.59) * mm, "end": v(128.72, -1.59) * mm});
            skLineSegment(sketch, "E14.3.17.15", {"start": v(128.72, -1.59) * mm, "end": v(130.3, -4.32) * mm});
            skLineSegment(sketch, "E14.6.17.15", {"start": v(130.3, -4.32) * mm, "end": v(128.72, -7.05) * mm});
            skCircle(sketch, "E14.9.17.15", {"center": v(127.14, -4.32) * mm, "radius": 2.73 * mm, "construction": true});
            skLineSegment(sketch, "E14.11.17.15", {"start": v(128.72, -7.05) * mm, "end": v(125.57, -7.05) * mm});
            skLineSegment(sketch, "E14.14.17.15", {"start": v(125.57, -7.05) * mm, "end": v(124, -4.32) * mm});
            skLineSegment(sketch, "E14.17.17.15", {"start": v(124, -4.32) * mm, "end": v(125.57, -1.59) * mm});
            skLineSegment(sketch, "E14.0.17.16", {"start": v(125.57, 7.05) * mm, "end": v(128.72, 7.05) * mm});
            skLineSegment(sketch, "E14.3.17.16", {"start": v(128.72, 7.05) * mm, "end": v(130.3, 4.32) * mm});
            skLineSegment(sketch, "E14.6.17.16", {"start": v(130.3, 4.32) * mm, "end": v(128.72, 1.59) * mm});
            skCircle(sketch, "E14.9.17.16", {"center": v(127.14, 4.32) * mm, "radius": 2.73 * mm, "construction": true});
            skLineSegment(sketch, "E14.11.17.16", {"start": v(128.72, 1.59) * mm, "end": v(125.57, 1.59) * mm});
            skLineSegment(sketch, "E14.14.17.16", {"start": v(125.57, 1.59) * mm, "end": v(124, 4.32) * mm});
            skLineSegment(sketch, "E14.17.17.16", {"start": v(124, 4.32) * mm, "end": v(125.57, 7.05) * mm});
            skLineSegment(sketch, "E14.0.17.17", {"start": v(125.57, 15.68) * mm, "end": v(128.72, 15.68) * mm});
            skLineSegment(sketch, "E14.3.17.17", {"start": v(128.72, 15.68) * mm, "end": v(130.3, 12.95) * mm});
            skLineSegment(sketch, "E14.6.17.17", {"start": v(130.3, 12.95) * mm, "end": v(128.72, 10.22) * mm});
            skCircle(sketch, "E14.9.17.17", {"center": v(127.14, 12.95) * mm, "radius": 2.73 * mm, "construction": true});
            skLineSegment(sketch, "E14.11.17.17", {"start": v(128.72, 10.22) * mm, "end": v(125.57, 10.22) * mm});
            skLineSegment(sketch, "E14.14.17.17", {"start": v(125.57, 10.22) * mm, "end": v(124, 12.95) * mm});
            skLineSegment(sketch, "E14.17.17.17", {"start": v(124, 12.95) * mm, "end": v(125.57, 15.68) * mm});
            skLineSegment(sketch, "E14.0.17.18", {"start": v(125.57, 24.32) * mm, "end": v(128.72, 24.32) * mm});
            skLineSegment(sketch, "E14.3.17.18", {"start": v(128.72, 24.32) * mm, "end": v(130.3, 21.59) * mm});
            skLineSegment(sketch, "E14.6.17.18", {"start": v(130.3, 21.59) * mm, "end": v(128.72, 18.86) * mm});
            skCircle(sketch, "E14.9.17.18", {"center": v(127.14, 21.59) * mm, "radius": 2.73 * mm, "construction": true});
            skLineSegment(sketch, "E14.11.17.18", {"start": v(128.72, 18.86) * mm, "end": v(125.57, 18.86) * mm});
            skLineSegment(sketch, "E14.14.17.18", {"start": v(125.57, 18.86) * mm, "end": v(124, 21.59) * mm});
            skLineSegment(sketch, "E14.17.17.18", {"start": v(124, 21.59) * mm, "end": v(125.57, 24.32) * mm});
            skLineSegment(sketch, "E14.0.17.19", {"start": v(125.57, 32.96) * mm, "end": v(128.72, 32.96) * mm});
            skLineSegment(sketch, "E14.3.17.19", {"start": v(128.72, 32.96) * mm, "end": v(130.3, 30.23) * mm});
            skLineSegment(sketch, "E14.6.17.19", {"start": v(130.3, 30.23) * mm, "end": v(128.72, 27.5) * mm});
            skCircle(sketch, "E14.9.17.19", {"center": v(127.14, 30.23) * mm, "radius": 2.73 * mm, "construction": true});
            skLineSegment(sketch, "E14.11.17.19", {"start": v(128.72, 27.5) * mm, "end": v(125.57, 27.5) * mm});
            skLineSegment(sketch, "E14.14.17.19", {"start": v(125.57, 27.5) * mm, "end": v(124, 30.23) * mm});
            skLineSegment(sketch, "E14.17.17.19", {"start": v(124, 30.23) * mm, "end": v(125.57, 32.96) * mm});
            skLineSegment(sketch, "E14.0.18.0", {"start": v(140.53, -131.13) * mm, "end": v(143.68, -131.13) * mm});
            skLineSegment(sketch, "E14.3.18.0", {"start": v(143.68, -131.13) * mm, "end": v(145.25, -133.86) * mm});
            skLineSegment(sketch, "E14.6.18.0", {"start": v(145.25, -133.86) * mm, "end": v(143.68, -136.59) * mm});
            skCircle(sketch, "E14.9.18.0", {"center": v(142.1, -133.86) * mm, "radius": 2.73 * mm, "construction": true});
            skLineSegment(sketch, "E14.11.18.0", {"start": v(143.68, -136.59) * mm, "end": v(140.53, -136.59) * mm});
            skLineSegment(sketch, "E14.14.18.0", {"start": v(140.53, -136.59) * mm, "end": v(138.95, -133.86) * mm});
            skLineSegment(sketch, "E14.17.18.0", {"start": v(138.95, -133.86) * mm, "end": v(140.53, -131.13) * mm});
            skLineSegment(sketch, "E14.0.18.1", {"start": v(140.53, -122.5) * mm, "end": v(143.68, -122.5) * mm});
            skLineSegment(sketch, "E14.3.18.1", {"start": v(143.68, -122.5) * mm, "end": v(145.25, -125.22) * mm});
            skLineSegment(sketch, "E14.6.18.1", {"start": v(145.25, -125.22) * mm, "end": v(143.68, -127.95) * mm});
            skCircle(sketch, "E14.9.18.1", {"center": v(142.1, -125.22) * mm, "radius": 2.73 * mm, "construction": true});
            skLineSegment(sketch, "E14.11.18.1", {"start": v(143.68, -127.95) * mm, "end": v(140.53, -127.95) * mm});
            skLineSegment(sketch, "E14.14.18.1", {"start": v(140.53, -127.95) * mm, "end": v(138.95, -125.22) * mm});
            skLineSegment(sketch, "E14.17.18.1", {"start": v(138.95, -125.22) * mm, "end": v(140.53, -122.5) * mm});
            skLineSegment(sketch, "E14.0.18.2", {"start": v(140.53, -113.86) * mm, "end": v(143.68, -113.86) * mm});
            skLineSegment(sketch, "E14.3.18.2", {"start": v(143.68, -113.86) * mm, "end": v(145.25, -116.59) * mm});
            skLineSegment(sketch, "E14.6.18.2", {"start": v(145.25, -116.59) * mm, "end": v(143.68, -119.32) * mm});
            skCircle(sketch, "E14.9.18.2", {"center": v(142.1, -116.59) * mm, "radius": 2.73 * mm, "construction": true});
            skLineSegment(sketch, "E14.11.18.2", {"start": v(143.68, -119.32) * mm, "end": v(140.53, -119.32) * mm});
            skLineSegment(sketch, "E14.14.18.2", {"start": v(140.53, -119.32) * mm, "end": v(138.95, -116.59) * mm});
            skLineSegment(sketch, "E14.17.18.2", {"start": v(138.95, -116.59) * mm, "end": v(140.53, -113.86) * mm});
            skLineSegment(sketch, "E14.0.18.3", {"start": v(140.53, -105.22) * mm, "end": v(143.68, -105.22) * mm});
            skLineSegment(sketch, "E14.3.18.3", {"start": v(143.68, -105.22) * mm, "end": v(145.25, -107.95) * mm});
            skLineSegment(sketch, "E14.6.18.3", {"start": v(145.25, -107.95) * mm, "end": v(143.68, -110.68) * mm});
            skCircle(sketch, "E14.9.18.3", {"center": v(142.1, -107.95) * mm, "radius": 2.73 * mm, "construction": true});
            skLineSegment(sketch, "E14.11.18.3", {"start": v(143.68, -110.68) * mm, "end": v(140.53, -110.68) * mm});
            skLineSegment(sketch, "E14.14.18.3", {"start": v(140.53, -110.68) * mm, "end": v(138.95, -107.95) * mm});
            skLineSegment(sketch, "E14.17.18.3", {"start": v(138.95, -107.95) * mm, "end": v(140.53, -105.22) * mm});
            skLineSegment(sketch, "E14.0.18.4", {"start": v(140.53, -96.58) * mm, "end": v(143.68, -96.58) * mm});
            skLineSegment(sketch, "E14.3.18.4", {"start": v(143.68, -96.58) * mm, "end": v(145.25, -99.31) * mm});
            skLineSegment(sketch, "E14.6.18.4", {"start": v(145.25, -99.31) * mm, "end": v(143.68, -102.04) * mm});
            skCircle(sketch, "E14.9.18.4", {"center": v(142.1, -99.31) * mm, "radius": 2.73 * mm, "construction": true});
            skLineSegment(sketch, "E14.11.18.4", {"start": v(143.68, -102.04) * mm, "end": v(140.53, -102.04) * mm});
            skLineSegment(sketch, "E14.14.18.4", {"start": v(140.53, -102.04) * mm, "end": v(138.95, -99.31) * mm});
            skLineSegment(sketch, "E14.17.18.4", {"start": v(138.95, -99.31) * mm, "end": v(140.53, -96.58) * mm});
            skLineSegment(sketch, "E14.0.18.5", {"start": v(140.53, -87.95) * mm, "end": v(143.68, -87.95) * mm});
            skLineSegment(sketch, "E14.3.18.5", {"start": v(143.68, -87.95) * mm, "end": v(145.25, -90.68) * mm});
            skLineSegment(sketch, "E14.6.18.5", {"start": v(145.25, -90.68) * mm, "end": v(143.68, -93.4) * mm});
            skCircle(sketch, "E14.9.18.5", {"center": v(142.1, -90.68) * mm, "radius": 2.73 * mm, "construction": true});
            skLineSegment(sketch, "E14.11.18.5", {"start": v(143.68, -93.4) * mm, "end": v(140.53, -93.4) * mm});
            skLineSegment(sketch, "E14.14.18.5", {"start": v(140.53, -93.4) * mm, "end": v(138.95, -90.68) * mm});
            skLineSegment(sketch, "E14.17.18.5", {"start": v(138.95, -90.68) * mm, "end": v(140.53, -87.95) * mm});
            skLineSegment(sketch, "E14.0.18.6", {"start": v(140.53, -79.31) * mm, "end": v(143.68, -79.31) * mm});
            skLineSegment(sketch, "E14.3.18.6", {"start": v(143.68, -79.31) * mm, "end": v(145.25, -82.04) * mm});
            skLineSegment(sketch, "E14.6.18.6", {"start": v(145.25, -82.04) * mm, "end": v(143.68, -84.77) * mm});
            skCircle(sketch, "E14.9.18.6", {"center": v(142.1, -82.04) * mm, "radius": 2.73 * mm, "construction": true});
            skLineSegment(sketch, "E14.11.18.6", {"start": v(143.68, -84.77) * mm, "end": v(140.53, -84.77) * mm});
            skLineSegment(sketch, "E14.14.18.6", {"start": v(140.53, -84.77) * mm, "end": v(138.95, -82.04) * mm});
            skLineSegment(sketch, "E14.17.18.6", {"start": v(138.95, -82.04) * mm, "end": v(140.53, -79.31) * mm});
            skLineSegment(sketch, "E14.0.18.7", {"start": v(140.53, -70.68) * mm, "end": v(143.68, -70.68) * mm});
            skLineSegment(sketch, "E14.3.18.7", {"start": v(143.68, -70.68) * mm, "end": v(145.25, -73.4) * mm});
            skLineSegment(sketch, "E14.6.18.7", {"start": v(145.25, -73.4) * mm, "end": v(143.68, -76.14) * mm});
            skCircle(sketch, "E14.9.18.7", {"center": v(142.1, -73.4) * mm, "radius": 2.73 * mm, "construction": true});
            skLineSegment(sketch, "E14.11.18.7", {"start": v(143.68, -76.14) * mm, "end": v(140.53, -76.14) * mm});
            skLineSegment(sketch, "E14.14.18.7", {"start": v(140.53, -76.14) * mm, "end": v(138.95, -73.4) * mm});
            skLineSegment(sketch, "E14.17.18.7", {"start": v(138.95, -73.4) * mm, "end": v(140.53, -70.68) * mm});
            skLineSegment(sketch, "E14.0.18.8", {"start": v(140.53, -62.04) * mm, "end": v(143.68, -62.04) * mm});
            skLineSegment(sketch, "E14.3.18.8", {"start": v(143.68, -62.04) * mm, "end": v(145.25, -64.77) * mm});
            skLineSegment(sketch, "E14.6.18.8", {"start": v(145.25, -64.77) * mm, "end": v(143.68, -67.5) * mm});
            skCircle(sketch, "E14.9.18.8", {"center": v(142.1, -64.77) * mm, "radius": 2.73 * mm, "construction": true});
            skLineSegment(sketch, "E14.11.18.8", {"start": v(143.68, -67.5) * mm, "end": v(140.53, -67.5) * mm});
            skLineSegment(sketch, "E14.14.18.8", {"start": v(140.53, -67.5) * mm, "end": v(138.95, -64.77) * mm});
            skLineSegment(sketch, "E14.17.18.8", {"start": v(138.95, -64.77) * mm, "end": v(140.53, -62.04) * mm});
            skLineSegment(sketch, "E14.0.18.9", {"start": v(140.53, -53.4) * mm, "end": v(143.68, -53.4) * mm});
            skLineSegment(sketch, "E14.3.18.9", {"start": v(143.68, -53.4) * mm, "end": v(145.25, -56.13) * mm});
            skLineSegment(sketch, "E14.6.18.9", {"start": v(145.25, -56.13) * mm, "end": v(143.68, -58.86) * mm});
            skCircle(sketch, "E14.9.18.9", {"center": v(142.1, -56.13) * mm, "radius": 2.73 * mm, "construction": true});
            skLineSegment(sketch, "E14.11.18.9", {"start": v(143.68, -58.86) * mm, "end": v(140.53, -58.86) * mm});
            skLineSegment(sketch, "E14.14.18.9", {"start": v(140.53, -58.86) * mm, "end": v(138.95, -56.13) * mm});
            skLineSegment(sketch, "E14.17.18.9", {"start": v(138.95, -56.13) * mm, "end": v(140.53, -53.4) * mm});
            skLineSegment(sketch, "E14.0.18.10", {"start": v(140.53, -44.77) * mm, "end": v(143.68, -44.77) * mm});
            skLineSegment(sketch, "E14.3.18.10", {"start": v(143.68, -44.77) * mm, "end": v(145.25, -47.5) * mm});
            skLineSegment(sketch, "E14.6.18.10", {"start": v(145.25, -47.5) * mm, "end": v(143.68, -50.23) * mm});
            skCircle(sketch, "E14.9.18.10", {"center": v(142.1, -47.5) * mm, "radius": 2.73 * mm, "construction": true});
            skLineSegment(sketch, "E14.11.18.10", {"start": v(143.68, -50.23) * mm, "end": v(140.53, -50.23) * mm});
            skLineSegment(sketch, "E14.14.18.10", {"start": v(140.53, -50.23) * mm, "end": v(138.95, -47.5) * mm});
            skLineSegment(sketch, "E14.17.18.10", {"start": v(138.95, -47.5) * mm, "end": v(140.53, -44.77) * mm});
            skLineSegment(sketch, "E14.0.18.11", {"start": v(140.53, -36.13) * mm, "end": v(143.68, -36.13) * mm});
            skLineSegment(sketch, "E14.3.18.11", {"start": v(143.68, -36.13) * mm, "end": v(145.25, -38.86) * mm});
            skLineSegment(sketch, "E14.6.18.11", {"start": v(145.25, -38.86) * mm, "end": v(143.68, -41.6) * mm});
            skCircle(sketch, "E14.9.18.11", {"center": v(142.1, -38.86) * mm, "radius": 2.73 * mm, "construction": true});
            skLineSegment(sketch, "E14.11.18.11", {"start": v(143.68, -41.6) * mm, "end": v(140.53, -41.6) * mm});
            skLineSegment(sketch, "E14.14.18.11", {"start": v(140.53, -41.6) * mm, "end": v(138.95, -38.86) * mm});
            skLineSegment(sketch, "E14.17.18.11", {"start": v(138.95, -38.86) * mm, "end": v(140.53, -36.13) * mm});
            skLineSegment(sketch, "E14.0.18.12", {"start": v(140.53, -27.5) * mm, "end": v(143.68, -27.5) * mm});
            skLineSegment(sketch, "E14.3.18.12", {"start": v(143.68, -27.5) * mm, "end": v(145.25, -30.23) * mm});
            skLineSegment(sketch, "E14.6.18.12", {"start": v(145.25, -30.23) * mm, "end": v(143.68, -32.96) * mm});
            skCircle(sketch, "E14.9.18.12", {"center": v(142.1, -30.23) * mm, "radius": 2.73 * mm, "construction": true});
            skLineSegment(sketch, "E14.11.18.12", {"start": v(143.68, -32.96) * mm, "end": v(140.53, -32.96) * mm});
            skLineSegment(sketch, "E14.14.18.12", {"start": v(140.53, -32.96) * mm, "end": v(138.95, -30.23) * mm});
            skLineSegment(sketch, "E14.17.18.12", {"start": v(138.95, -30.23) * mm, "end": v(140.53, -27.5) * mm});
            skLineSegment(sketch, "E14.0.18.13", {"start": v(140.53, -18.86) * mm, "end": v(143.68, -18.86) * mm});
            skLineSegment(sketch, "E14.3.18.13", {"start": v(143.68, -18.86) * mm, "end": v(145.25, -21.6) * mm});
            skLineSegment(sketch, "E14.6.18.13", {"start": v(145.25, -21.6) * mm, "end": v(143.68, -24.32) * mm});
            skCircle(sketch, "E14.9.18.13", {"center": v(142.1, -21.6) * mm, "radius": 2.73 * mm, "construction": true});
            skLineSegment(sketch, "E14.11.18.13", {"start": v(143.68, -24.32) * mm, "end": v(140.53, -24.32) * mm});
            skLineSegment(sketch, "E14.14.18.13", {"start": v(140.53, -24.32) * mm, "end": v(138.95, -21.6) * mm});
            skLineSegment(sketch, "E14.17.18.13", {"start": v(138.95, -21.59) * mm, "end": v(140.53, -18.86) * mm});
            skLineSegment(sketch, "E14.0.18.14", {"start": v(140.53, -10.22) * mm, "end": v(143.68, -10.22) * mm});
            skLineSegment(sketch, "E14.3.18.14", {"start": v(143.68, -10.22) * mm, "end": v(145.25, -12.95) * mm});
            skLineSegment(sketch, "E14.6.18.14", {"start": v(145.25, -12.95) * mm, "end": v(143.68, -15.68) * mm});
            skCircle(sketch, "E14.9.18.14", {"center": v(142.1, -12.95) * mm, "radius": 2.73 * mm, "construction": true});
            skLineSegment(sketch, "E14.11.18.14", {"start": v(143.68, -15.68) * mm, "end": v(140.53, -15.68) * mm});
            skLineSegment(sketch, "E14.14.18.14", {"start": v(140.53, -15.68) * mm, "end": v(138.95, -12.95) * mm});
            skLineSegment(sketch, "E14.17.18.14", {"start": v(138.95, -12.95) * mm, "end": v(140.53, -10.22) * mm});
            skLineSegment(sketch, "E14.0.18.15", {"start": v(140.53, -1.59) * mm, "end": v(143.68, -1.59) * mm});
            skLineSegment(sketch, "E14.3.18.15", {"start": v(143.68, -1.59) * mm, "end": v(145.25, -4.32) * mm});
            skLineSegment(sketch, "E14.6.18.15", {"start": v(145.25, -4.32) * mm, "end": v(143.68, -7.05) * mm});
            skCircle(sketch, "E14.9.18.15", {"center": v(142.1, -4.32) * mm, "radius": 2.73 * mm, "construction": true});
            skLineSegment(sketch, "E14.11.18.15", {"start": v(143.68, -7.05) * mm, "end": v(140.53, -7.05) * mm});
            skLineSegment(sketch, "E14.14.18.15", {"start": v(140.53, -7.05) * mm, "end": v(138.95, -4.32) * mm});
            skLineSegment(sketch, "E14.17.18.15", {"start": v(138.95, -4.32) * mm, "end": v(140.53, -1.59) * mm});
            skLineSegment(sketch, "E14.0.18.16", {"start": v(140.53, 7.05) * mm, "end": v(143.68, 7.05) * mm});
            skLineSegment(sketch, "E14.3.18.16", {"start": v(143.68, 7.05) * mm, "end": v(145.25, 4.32) * mm});
            skLineSegment(sketch, "E14.6.18.16", {"start": v(145.25, 4.32) * mm, "end": v(143.68, 1.59) * mm});
            skCircle(sketch, "E14.9.18.16", {"center": v(142.1, 4.32) * mm, "radius": 2.73 * mm, "construction": true});
            skLineSegment(sketch, "E14.11.18.16", {"start": v(143.68, 1.59) * mm, "end": v(140.53, 1.59) * mm});
            skLineSegment(sketch, "E14.14.18.16", {"start": v(140.53, 1.59) * mm, "end": v(138.95, 4.32) * mm});
            skLineSegment(sketch, "E14.17.18.16", {"start": v(138.95, 4.32) * mm, "end": v(140.53, 7.05) * mm});
            skLineSegment(sketch, "E14.0.18.17", {"start": v(140.53, 15.68) * mm, "end": v(143.68, 15.68) * mm});
            skLineSegment(sketch, "E14.3.18.17", {"start": v(143.68, 15.68) * mm, "end": v(145.25, 12.95) * mm});
            skLineSegment(sketch, "E14.6.18.17", {"start": v(145.25, 12.95) * mm, "end": v(143.68, 10.22) * mm});
            skCircle(sketch, "E14.9.18.17", {"center": v(142.1, 12.95) * mm, "radius": 2.73 * mm, "construction": true});
            skLineSegment(sketch, "E14.11.18.17", {"start": v(143.68, 10.22) * mm, "end": v(140.53, 10.22) * mm});
            skLineSegment(sketch, "E14.14.18.17", {"start": v(140.53, 10.22) * mm, "end": v(138.95, 12.95) * mm});
            skLineSegment(sketch, "E14.17.18.17", {"start": v(138.95, 12.95) * mm, "end": v(140.53, 15.68) * mm});
            skLineSegment(sketch, "E14.0.18.18", {"start": v(140.53, 24.32) * mm, "end": v(143.68, 24.32) * mm});
            skLineSegment(sketch, "E14.3.18.18", {"start": v(143.68, 24.32) * mm, "end": v(145.25, 21.59) * mm});
            skLineSegment(sketch, "E14.6.18.18", {"start": v(145.25, 21.59) * mm, "end": v(143.68, 18.86) * mm});
            skCircle(sketch, "E14.9.18.18", {"center": v(142.1, 21.59) * mm, "radius": 2.73 * mm, "construction": true});
            skLineSegment(sketch, "E14.11.18.18", {"start": v(143.68, 18.86) * mm, "end": v(140.53, 18.86) * mm});
            skLineSegment(sketch, "E14.14.18.18", {"start": v(140.53, 18.86) * mm, "end": v(138.95, 21.59) * mm});
            skLineSegment(sketch, "E14.17.18.18", {"start": v(138.95, 21.59) * mm, "end": v(140.53, 24.32) * mm});
            skLineSegment(sketch, "E14.0.18.19", {"start": v(140.53, 32.96) * mm, "end": v(143.68, 32.96) * mm});
            skLineSegment(sketch, "E14.3.18.19", {"start": v(143.68, 32.96) * mm, "end": v(145.25, 30.23) * mm});
            skLineSegment(sketch, "E14.6.18.19", {"start": v(145.25, 30.23) * mm, "end": v(143.68, 27.5) * mm});
            skCircle(sketch, "E14.9.18.19", {"center": v(142.1, 30.23) * mm, "radius": 2.73 * mm, "construction": true});
            skLineSegment(sketch, "E14.11.18.19", {"start": v(143.68, 27.5) * mm, "end": v(140.53, 27.5) * mm});
            skLineSegment(sketch, "E14.14.18.19", {"start": v(140.53, 27.5) * mm, "end": v(138.95, 30.23) * mm});
            skLineSegment(sketch, "E14.17.18.19", {"start": v(138.95, 30.23) * mm, "end": v(140.53, 32.96) * mm});
            skLineSegment(sketch, "E14.0.19.0", {"start": v(155.48, -131.13) * mm, "end": v(158.64, -131.13) * mm});
            skLineSegment(sketch, "E14.3.19.0", {"start": v(158.64, -131.13) * mm, "end": v(160.21, -133.86) * mm});
            skLineSegment(sketch, "E14.6.19.0", {"start": v(160.21, -133.86) * mm, "end": v(158.64, -136.59) * mm});
            skCircle(sketch, "E14.9.19.0", {"center": v(157.06, -133.86) * mm, "radius": 2.73 * mm, "construction": true});
            skLineSegment(sketch, "E14.11.19.0", {"start": v(158.64, -136.59) * mm, "end": v(155.48, -136.59) * mm});
            skLineSegment(sketch, "E14.14.19.0", {"start": v(155.48, -136.59) * mm, "end": v(153.9, -133.86) * mm});
            skLineSegment(sketch, "E14.17.19.0", {"start": v(153.9, -133.86) * mm, "end": v(155.48, -131.13) * mm});
            skLineSegment(sketch, "E14.0.19.1", {"start": v(155.48, -122.5) * mm, "end": v(158.64, -122.5) * mm});
            skLineSegment(sketch, "E14.3.19.1", {"start": v(158.64, -122.5) * mm, "end": v(160.21, -125.22) * mm});
            skLineSegment(sketch, "E14.6.19.1", {"start": v(160.21, -125.22) * mm, "end": v(158.64, -127.95) * mm});
            skCircle(sketch, "E14.9.19.1", {"center": v(157.06, -125.22) * mm, "radius": 2.73 * mm, "construction": true});
            skLineSegment(sketch, "E14.11.19.1", {"start": v(158.64, -127.95) * mm, "end": v(155.48, -127.95) * mm});
            skLineSegment(sketch, "E14.14.19.1", {"start": v(155.48, -127.95) * mm, "end": v(153.9, -125.22) * mm});
            skLineSegment(sketch, "E14.17.19.1", {"start": v(153.9, -125.22) * mm, "end": v(155.48, -122.5) * mm});
            skLineSegment(sketch, "E14.0.19.2", {"start": v(155.48, -113.86) * mm, "end": v(158.64, -113.86) * mm});
            skLineSegment(sketch, "E14.3.19.2", {"start": v(158.64, -113.86) * mm, "end": v(160.21, -116.59) * mm});
            skLineSegment(sketch, "E14.6.19.2", {"start": v(160.21, -116.59) * mm, "end": v(158.64, -119.32) * mm});
            skCircle(sketch, "E14.9.19.2", {"center": v(157.06, -116.59) * mm, "radius": 2.73 * mm, "construction": true});
            skLineSegment(sketch, "E14.11.19.2", {"start": v(158.64, -119.32) * mm, "end": v(155.48, -119.32) * mm});
            skLineSegment(sketch, "E14.14.19.2", {"start": v(155.48, -119.32) * mm, "end": v(153.9, -116.59) * mm});
            skLineSegment(sketch, "E14.17.19.2", {"start": v(153.9, -116.59) * mm, "end": v(155.48, -113.86) * mm});
            skLineSegment(sketch, "E14.0.19.3", {"start": v(155.48, -105.22) * mm, "end": v(158.64, -105.22) * mm});
            skLineSegment(sketch, "E14.3.19.3", {"start": v(158.64, -105.22) * mm, "end": v(160.21, -107.95) * mm});
            skLineSegment(sketch, "E14.6.19.3", {"start": v(160.21, -107.95) * mm, "end": v(158.64, -110.68) * mm});
            skCircle(sketch, "E14.9.19.3", {"center": v(157.06, -107.95) * mm, "radius": 2.73 * mm, "construction": true});
            skLineSegment(sketch, "E14.11.19.3", {"start": v(158.64, -110.68) * mm, "end": v(155.48, -110.68) * mm});
            skLineSegment(sketch, "E14.14.19.3", {"start": v(155.48, -110.68) * mm, "end": v(153.9, -107.95) * mm});
            skLineSegment(sketch, "E14.17.19.3", {"start": v(153.9, -107.95) * mm, "end": v(155.48, -105.22) * mm});
            skLineSegment(sketch, "E14.0.19.4", {"start": v(155.48, -96.58) * mm, "end": v(158.64, -96.58) * mm});
            skLineSegment(sketch, "E14.3.19.4", {"start": v(158.64, -96.58) * mm, "end": v(160.21, -99.31) * mm});
            skLineSegment(sketch, "E14.6.19.4", {"start": v(160.21, -99.31) * mm, "end": v(158.64, -102.04) * mm});
            skCircle(sketch, "E14.9.19.4", {"center": v(157.06, -99.31) * mm, "radius": 2.73 * mm, "construction": true});
            skLineSegment(sketch, "E14.11.19.4", {"start": v(158.64, -102.04) * mm, "end": v(155.48, -102.04) * mm});
            skLineSegment(sketch, "E14.14.19.4", {"start": v(155.48, -102.04) * mm, "end": v(153.9, -99.31) * mm});
            skLineSegment(sketch, "E14.17.19.4", {"start": v(153.9, -99.31) * mm, "end": v(155.48, -96.58) * mm});
            skLineSegment(sketch, "E14.0.19.5", {"start": v(155.48, -87.95) * mm, "end": v(158.64, -87.95) * mm});
            skLineSegment(sketch, "E14.3.19.5", {"start": v(158.64, -87.95) * mm, "end": v(160.21, -90.68) * mm});
            skLineSegment(sketch, "E14.6.19.5", {"start": v(160.21, -90.68) * mm, "end": v(158.64, -93.4) * mm});
            skCircle(sketch, "E14.9.19.5", {"center": v(157.06, -90.68) * mm, "radius": 2.73 * mm, "construction": true});
            skLineSegment(sketch, "E14.11.19.5", {"start": v(158.64, -93.4) * mm, "end": v(155.48, -93.4) * mm});
            skLineSegment(sketch, "E14.14.19.5", {"start": v(155.48, -93.4) * mm, "end": v(153.9, -90.68) * mm});
            skLineSegment(sketch, "E14.17.19.5", {"start": v(153.9, -90.68) * mm, "end": v(155.48, -87.95) * mm});
            skLineSegment(sketch, "E14.0.19.6", {"start": v(155.48, -79.31) * mm, "end": v(158.64, -79.31) * mm});
            skLineSegment(sketch, "E14.3.19.6", {"start": v(158.64, -79.31) * mm, "end": v(160.21, -82.04) * mm});
            skLineSegment(sketch, "E14.6.19.6", {"start": v(160.21, -82.04) * mm, "end": v(158.64, -84.77) * mm});
            skCircle(sketch, "E14.9.19.6", {"center": v(157.06, -82.04) * mm, "radius": 2.73 * mm, "construction": true});
            skLineSegment(sketch, "E14.11.19.6", {"start": v(158.64, -84.77) * mm, "end": v(155.48, -84.77) * mm});
            skLineSegment(sketch, "E14.14.19.6", {"start": v(155.48, -84.77) * mm, "end": v(153.9, -82.04) * mm});
            skLineSegment(sketch, "E14.17.19.6", {"start": v(153.9, -82.04) * mm, "end": v(155.48, -79.31) * mm});
            skLineSegment(sketch, "E14.0.19.7", {"start": v(155.48, -70.68) * mm, "end": v(158.64, -70.68) * mm});
            skLineSegment(sketch, "E14.3.19.7", {"start": v(158.64, -70.68) * mm, "end": v(160.21, -73.4) * mm});
            skLineSegment(sketch, "E14.6.19.7", {"start": v(160.21, -73.4) * mm, "end": v(158.64, -76.14) * mm});
            skCircle(sketch, "E14.9.19.7", {"center": v(157.06, -73.4) * mm, "radius": 2.73 * mm, "construction": true});
            skLineSegment(sketch, "E14.11.19.7", {"start": v(158.64, -76.14) * mm, "end": v(155.48, -76.14) * mm});
            skLineSegment(sketch, "E14.14.19.7", {"start": v(155.48, -76.14) * mm, "end": v(153.9, -73.4) * mm});
            skLineSegment(sketch, "E14.17.19.7", {"start": v(153.9, -73.4) * mm, "end": v(155.48, -70.68) * mm});
            skLineSegment(sketch, "E14.0.19.8", {"start": v(155.48, -62.04) * mm, "end": v(158.64, -62.04) * mm});
            skLineSegment(sketch, "E14.3.19.8", {"start": v(158.64, -62.04) * mm, "end": v(160.21, -64.77) * mm});
            skLineSegment(sketch, "E14.6.19.8", {"start": v(160.21, -64.77) * mm, "end": v(158.64, -67.5) * mm});
            skCircle(sketch, "E14.9.19.8", {"center": v(157.06, -64.77) * mm, "radius": 2.73 * mm, "construction": true});
            skLineSegment(sketch, "E14.11.19.8", {"start": v(158.64, -67.5) * mm, "end": v(155.48, -67.5) * mm});
            skLineSegment(sketch, "E14.14.19.8", {"start": v(155.48, -67.5) * mm, "end": v(153.9, -64.77) * mm});
            skLineSegment(sketch, "E14.17.19.8", {"start": v(153.9, -64.77) * mm, "end": v(155.48, -62.04) * mm});
            skLineSegment(sketch, "E14.0.19.9", {"start": v(155.48, -53.4) * mm, "end": v(158.64, -53.4) * mm});
            skLineSegment(sketch, "E14.3.19.9", {"start": v(158.64, -53.4) * mm, "end": v(160.21, -56.13) * mm});
            skLineSegment(sketch, "E14.6.19.9", {"start": v(160.21, -56.13) * mm, "end": v(158.64, -58.86) * mm});
            skCircle(sketch, "E14.9.19.9", {"center": v(157.06, -56.13) * mm, "radius": 2.73 * mm, "construction": true});
            skLineSegment(sketch, "E14.11.19.9", {"start": v(158.64, -58.86) * mm, "end": v(155.48, -58.86) * mm});
            skLineSegment(sketch, "E14.14.19.9", {"start": v(155.48, -58.86) * mm, "end": v(153.9, -56.13) * mm});
            skLineSegment(sketch, "E14.17.19.9", {"start": v(153.9, -56.13) * mm, "end": v(155.48, -53.4) * mm});
            skLineSegment(sketch, "E14.0.19.10", {"start": v(155.48, -44.77) * mm, "end": v(158.64, -44.77) * mm});
            skLineSegment(sketch, "E14.3.19.10", {"start": v(158.64, -44.77) * mm, "end": v(160.21, -47.5) * mm});
            skLineSegment(sketch, "E14.6.19.10", {"start": v(160.21, -47.5) * mm, "end": v(158.64, -50.23) * mm});
            skCircle(sketch, "E14.9.19.10", {"center": v(157.06, -47.5) * mm, "radius": 2.73 * mm, "construction": true});
            skLineSegment(sketch, "E14.11.19.10", {"start": v(158.64, -50.23) * mm, "end": v(155.48, -50.23) * mm});
            skLineSegment(sketch, "E14.14.19.10", {"start": v(155.48, -50.23) * mm, "end": v(153.9, -47.5) * mm});
            skLineSegment(sketch, "E14.17.19.10", {"start": v(153.9, -47.5) * mm, "end": v(155.48, -44.77) * mm});
            skLineSegment(sketch, "E14.0.19.11", {"start": v(155.48, -36.13) * mm, "end": v(158.64, -36.13) * mm});
            skLineSegment(sketch, "E14.3.19.11", {"start": v(158.64, -36.13) * mm, "end": v(160.21, -38.86) * mm});
            skLineSegment(sketch, "E14.6.19.11", {"start": v(160.21, -38.86) * mm, "end": v(158.64, -41.6) * mm});
            skCircle(sketch, "E14.9.19.11", {"center": v(157.06, -38.86) * mm, "radius": 2.73 * mm, "construction": true});
            skLineSegment(sketch, "E14.11.19.11", {"start": v(158.64, -41.6) * mm, "end": v(155.48, -41.6) * mm});
            skLineSegment(sketch, "E14.14.19.11", {"start": v(155.48, -41.6) * mm, "end": v(153.9, -38.86) * mm});
            skLineSegment(sketch, "E14.17.19.11", {"start": v(153.9, -38.86) * mm, "end": v(155.48, -36.13) * mm});
            skLineSegment(sketch, "E14.0.19.12", {"start": v(155.48, -27.5) * mm, "end": v(158.64, -27.5) * mm});
            skLineSegment(sketch, "E14.3.19.12", {"start": v(158.64, -27.5) * mm, "end": v(160.21, -30.23) * mm});
            skLineSegment(sketch, "E14.6.19.12", {"start": v(160.21, -30.23) * mm, "end": v(158.64, -32.96) * mm});
            skCircle(sketch, "E14.9.19.12", {"center": v(157.06, -30.23) * mm, "radius": 2.73 * mm, "construction": true});
            skLineSegment(sketch, "E14.11.19.12", {"start": v(158.64, -32.96) * mm, "end": v(155.48, -32.96) * mm});
            skLineSegment(sketch, "E14.14.19.12", {"start": v(155.48, -32.96) * mm, "end": v(153.9, -30.23) * mm});
            skLineSegment(sketch, "E14.17.19.12", {"start": v(153.9, -30.23) * mm, "end": v(155.48, -27.5) * mm});
            skLineSegment(sketch, "E14.0.19.13", {"start": v(155.48, -18.86) * mm, "end": v(158.64, -18.86) * mm});
            skLineSegment(sketch, "E14.3.19.13", {"start": v(158.64, -18.86) * mm, "end": v(160.21, -21.6) * mm});
            skLineSegment(sketch, "E14.6.19.13", {"start": v(160.21, -21.6) * mm, "end": v(158.64, -24.32) * mm});
            skCircle(sketch, "E14.9.19.13", {"center": v(157.06, -21.6) * mm, "radius": 2.73 * mm, "construction": true});
            skLineSegment(sketch, "E14.11.19.13", {"start": v(158.64, -24.32) * mm, "end": v(155.48, -24.32) * mm});
            skLineSegment(sketch, "E14.14.19.13", {"start": v(155.48, -24.32) * mm, "end": v(153.9, -21.6) * mm});
            skLineSegment(sketch, "E14.17.19.13", {"start": v(153.9, -21.59) * mm, "end": v(155.48, -18.86) * mm});
            skLineSegment(sketch, "E14.0.19.14", {"start": v(155.48, -10.22) * mm, "end": v(158.64, -10.22) * mm});
            skLineSegment(sketch, "E14.3.19.14", {"start": v(158.64, -10.22) * mm, "end": v(160.21, -12.95) * mm});
            skLineSegment(sketch, "E14.6.19.14", {"start": v(160.21, -12.95) * mm, "end": v(158.64, -15.68) * mm});
            skCircle(sketch, "E14.9.19.14", {"center": v(157.06, -12.95) * mm, "radius": 2.73 * mm, "construction": true});
            skLineSegment(sketch, "E14.11.19.14", {"start": v(158.64, -15.68) * mm, "end": v(155.48, -15.68) * mm});
            skLineSegment(sketch, "E14.14.19.14", {"start": v(155.48, -15.68) * mm, "end": v(153.9, -12.95) * mm});
            skLineSegment(sketch, "E14.17.19.14", {"start": v(153.9, -12.95) * mm, "end": v(155.48, -10.22) * mm});
            skLineSegment(sketch, "E14.0.19.15", {"start": v(155.48, -1.59) * mm, "end": v(158.64, -1.59) * mm});
            skLineSegment(sketch, "E14.3.19.15", {"start": v(158.64, -1.59) * mm, "end": v(160.21, -4.32) * mm});
            skLineSegment(sketch, "E14.6.19.15", {"start": v(160.21, -4.32) * mm, "end": v(158.64, -7.05) * mm});
            skCircle(sketch, "E14.9.19.15", {"center": v(157.06, -4.32) * mm, "radius": 2.73 * mm, "construction": true});
            skLineSegment(sketch, "E14.11.19.15", {"start": v(158.64, -7.05) * mm, "end": v(155.48, -7.05) * mm});
            skLineSegment(sketch, "E14.14.19.15", {"start": v(155.48, -7.05) * mm, "end": v(153.9, -4.32) * mm});
            skLineSegment(sketch, "E14.17.19.15", {"start": v(153.9, -4.32) * mm, "end": v(155.48, -1.59) * mm});
            skLineSegment(sketch, "E14.0.19.16", {"start": v(155.48, 7.05) * mm, "end": v(158.64, 7.05) * mm});
            skLineSegment(sketch, "E14.3.19.16", {"start": v(158.64, 7.05) * mm, "end": v(160.21, 4.32) * mm});
            skLineSegment(sketch, "E14.6.19.16", {"start": v(160.21, 4.32) * mm, "end": v(158.64, 1.59) * mm});
            skCircle(sketch, "E14.9.19.16", {"center": v(157.06, 4.32) * mm, "radius": 2.73 * mm, "construction": true});
            skLineSegment(sketch, "E14.11.19.16", {"start": v(158.64, 1.59) * mm, "end": v(155.48, 1.59) * mm});
            skLineSegment(sketch, "E14.14.19.16", {"start": v(155.48, 1.59) * mm, "end": v(153.9, 4.32) * mm});
            skLineSegment(sketch, "E14.17.19.16", {"start": v(153.9, 4.32) * mm, "end": v(155.48, 7.05) * mm});
            skLineSegment(sketch, "E14.0.19.17", {"start": v(155.48, 15.68) * mm, "end": v(158.64, 15.68) * mm});
            skLineSegment(sketch, "E14.3.19.17", {"start": v(158.64, 15.68) * mm, "end": v(160.21, 12.95) * mm});
            skLineSegment(sketch, "E14.6.19.17", {"start": v(160.21, 12.95) * mm, "end": v(158.64, 10.22) * mm});
            skCircle(sketch, "E14.9.19.17", {"center": v(157.06, 12.95) * mm, "radius": 2.73 * mm, "construction": true});
            skLineSegment(sketch, "E14.11.19.17", {"start": v(158.64, 10.22) * mm, "end": v(155.48, 10.22) * mm});
            skLineSegment(sketch, "E14.14.19.17", {"start": v(155.48, 10.22) * mm, "end": v(153.9, 12.95) * mm});
            skLineSegment(sketch, "E14.17.19.17", {"start": v(153.9, 12.95) * mm, "end": v(155.48, 15.68) * mm});
            skLineSegment(sketch, "E14.0.19.18", {"start": v(155.48, 24.32) * mm, "end": v(158.64, 24.32) * mm});
            skLineSegment(sketch, "E14.3.19.18", {"start": v(158.64, 24.32) * mm, "end": v(160.21, 21.59) * mm});
            skLineSegment(sketch, "E14.6.19.18", {"start": v(160.21, 21.59) * mm, "end": v(158.64, 18.86) * mm});
            skCircle(sketch, "E14.9.19.18", {"center": v(157.06, 21.59) * mm, "radius": 2.73 * mm, "construction": true});
            skLineSegment(sketch, "E14.11.19.18", {"start": v(158.64, 18.86) * mm, "end": v(155.48, 18.86) * mm});
            skLineSegment(sketch, "E14.14.19.18", {"start": v(155.48, 18.86) * mm, "end": v(153.9, 21.59) * mm});
            skLineSegment(sketch, "E14.17.19.18", {"start": v(153.9, 21.6) * mm, "end": v(155.48, 24.32) * mm});
            skLineSegment(sketch, "E14.0.19.19", {"start": v(155.48, 32.96) * mm, "end": v(158.64, 32.96) * mm});
            skLineSegment(sketch, "E14.3.19.19", {"start": v(158.64, 32.96) * mm, "end": v(160.21, 30.23) * mm});
            skLineSegment(sketch, "E14.6.19.19", {"start": v(160.21, 30.23) * mm, "end": v(158.64, 27.5) * mm});
            skCircle(sketch, "E14.9.19.19", {"center": v(157.06, 30.23) * mm, "radius": 2.73 * mm, "construction": true});
            skLineSegment(sketch, "E14.11.19.19", {"start": v(158.64, 27.5) * mm, "end": v(155.48, 27.5) * mm});
            skLineSegment(sketch, "E14.14.19.19", {"start": v(155.48, 27.5) * mm, "end": v(153.9, 30.23) * mm});
            skLineSegment(sketch, "E14.17.19.19", {"start": v(153.9, 30.23) * mm, "end": v(155.48, 32.96) * mm});
            skCircle(sketch, "E15.0.5.0", {"center": v(-44.87, -129.54) * mm, "radius": 2.73 * mm, "construction": true});
            skLineSegment(sketch, "E15.2.5.0", {"start": v(-48.03, -129.54) * mm, "end": v(-46.45, -126.8) * mm});
            skLineSegment(sketch, "E15.5.5.0", {"start": v(-46.45, -126.8) * mm, "end": v(-43.3, -126.8) * mm});
            skLineSegment(sketch, "E15.8.5.0", {"start": v(-43.3, -126.8) * mm, "end": v(-41.72, -129.54) * mm});
            skLineSegment(sketch, "E15.11.5.0", {"start": v(-41.72, -129.54) * mm, "end": v(-43.3, -132.27) * mm});
            skLineSegment(sketch, "E15.14.5.0", {"start": v(-43.3, -132.27) * mm, "end": v(-46.45, -132.27) * mm});
            skLineSegment(sketch, "E15.17.5.0", {"start": v(-46.45, -132.27) * mm, "end": v(-48.03, -129.54) * mm});
            skCircle(sketch, "E15.0.5.1", {"center": v(-44.87, -120.9) * mm, "radius": 2.73 * mm, "construction": true});
            skLineSegment(sketch, "E15.2.5.1", {"start": v(-48.03, -120.9) * mm, "end": v(-46.45, -118.17) * mm});
            skLineSegment(sketch, "E15.5.5.1", {"start": v(-46.45, -118.17) * mm, "end": v(-43.3, -118.17) * mm});
            skLineSegment(sketch, "E15.8.5.1", {"start": v(-43.3, -118.17) * mm, "end": v(-41.72, -120.9) * mm});
            skLineSegment(sketch, "E15.11.5.1", {"start": v(-41.72, -120.9) * mm, "end": v(-43.3, -123.63) * mm});
            skLineSegment(sketch, "E15.14.5.1", {"start": v(-43.3, -123.63) * mm, "end": v(-46.45, -123.63) * mm});
            skLineSegment(sketch, "E15.17.5.1", {"start": v(-46.45, -123.63) * mm, "end": v(-48.03, -120.9) * mm});
            skCircle(sketch, "E15.0.5.2", {"center": v(-44.87, -112.27) * mm, "radius": 2.73 * mm, "construction": true});
            skLineSegment(sketch, "E15.2.5.2", {"start": v(-48.03, -112.27) * mm, "end": v(-46.45, -109.54) * mm});
            skLineSegment(sketch, "E15.5.5.2", {"start": v(-46.45, -109.54) * mm, "end": v(-43.3, -109.54) * mm});
            skLineSegment(sketch, "E15.8.5.2", {"start": v(-43.3, -109.54) * mm, "end": v(-41.72, -112.27) * mm});
            skLineSegment(sketch, "E15.11.5.2", {"start": v(-41.72, -112.27) * mm, "end": v(-43.3, -115) * mm});
            skLineSegment(sketch, "E15.14.5.2", {"start": v(-43.3, -115) * mm, "end": v(-46.45, -115) * mm});
            skLineSegment(sketch, "E15.17.5.2", {"start": v(-46.45, -115) * mm, "end": v(-48.03, -112.27) * mm});
            skCircle(sketch, "E15.0.5.3", {"center": v(-44.87, -103.63) * mm, "radius": 2.73 * mm, "construction": true});
            skLineSegment(sketch, "E15.2.5.3", {"start": v(-48.03, -103.63) * mm, "end": v(-46.45, -100.9) * mm});
            skLineSegment(sketch, "E15.5.5.3", {"start": v(-46.45, -100.9) * mm, "end": v(-43.3, -100.9) * mm});
            skLineSegment(sketch, "E15.8.5.3", {"start": v(-43.3, -100.9) * mm, "end": v(-41.72, -103.63) * mm});
            skLineSegment(sketch, "E15.11.5.3", {"start": v(-41.72, -103.63) * mm, "end": v(-43.3, -106.36) * mm});
            skLineSegment(sketch, "E15.14.5.3", {"start": v(-43.3, -106.36) * mm, "end": v(-46.45, -106.36) * mm});
            skLineSegment(sketch, "E15.17.5.3", {"start": v(-46.45, -106.36) * mm, "end": v(-48.03, -103.63) * mm});
            skCircle(sketch, "E15.0.5.4", {"center": v(-44.87, -95) * mm, "radius": 2.73 * mm, "construction": true});
            skLineSegment(sketch, "E15.2.5.4", {"start": v(-48.03, -95) * mm, "end": v(-46.45, -92.27) * mm});
            skLineSegment(sketch, "E15.5.5.4", {"start": v(-46.45, -92.27) * mm, "end": v(-43.3, -92.27) * mm});
            skLineSegment(sketch, "E15.8.5.4", {"start": v(-43.3, -92.27) * mm, "end": v(-41.72, -95) * mm});
            skLineSegment(sketch, "E15.11.5.4", {"start": v(-41.72, -95) * mm, "end": v(-43.3, -97.73) * mm});
            skLineSegment(sketch, "E15.14.5.4", {"start": v(-43.3, -97.73) * mm, "end": v(-46.45, -97.73) * mm});
            skLineSegment(sketch, "E15.17.5.4", {"start": v(-46.45, -97.73) * mm, "end": v(-48.03, -95) * mm});
            skCircle(sketch, "E15.0.5.5", {"center": v(-44.87, -86.36) * mm, "radius": 2.73 * mm, "construction": true});
            skLineSegment(sketch, "E15.2.5.5", {"start": v(-48.03, -86.36) * mm, "end": v(-46.45, -83.63) * mm});
            skLineSegment(sketch, "E15.5.5.5", {"start": v(-46.45, -83.63) * mm, "end": v(-43.3, -83.63) * mm});
            skLineSegment(sketch, "E15.8.5.5", {"start": v(-43.3, -83.63) * mm, "end": v(-41.72, -86.36) * mm});
            skLineSegment(sketch, "E15.11.5.5", {"start": v(-41.72, -86.36) * mm, "end": v(-43.3, -89.1) * mm});
            skLineSegment(sketch, "E15.14.5.5", {"start": v(-43.3, -89.1) * mm, "end": v(-46.45, -89.1) * mm});
            skLineSegment(sketch, "E15.17.5.5", {"start": v(-46.45, -89.1) * mm, "end": v(-48.03, -86.36) * mm});
            skCircle(sketch, "E15.0.5.6", {"center": v(-44.87, -77.72) * mm, "radius": 2.73 * mm, "construction": true});
            skLineSegment(sketch, "E15.2.5.6", {"start": v(-48.03, -77.72) * mm, "end": v(-46.45, -75) * mm});
            skLineSegment(sketch, "E15.5.5.6", {"start": v(-46.45, -75) * mm, "end": v(-43.3, -75) * mm});
            skLineSegment(sketch, "E15.8.5.6", {"start": v(-43.3, -75) * mm, "end": v(-41.72, -77.72) * mm});
            skLineSegment(sketch, "E15.11.5.6", {"start": v(-41.72, -77.72) * mm, "end": v(-43.3, -80.45) * mm});
            skLineSegment(sketch, "E15.14.5.6", {"start": v(-43.3, -80.45) * mm, "end": v(-46.45, -80.45) * mm});
            skLineSegment(sketch, "E15.17.5.6", {"start": v(-46.45, -80.45) * mm, "end": v(-48.03, -77.72) * mm});
            skCircle(sketch, "E15.0.5.7", {"center": v(-44.87, -69.09) * mm, "radius": 2.73 * mm, "construction": true});
            skLineSegment(sketch, "E15.2.5.7", {"start": v(-48.03, -69.09) * mm, "end": v(-46.45, -66.36) * mm});
            skLineSegment(sketch, "E15.5.5.7", {"start": v(-46.45, -66.36) * mm, "end": v(-43.3, -66.36) * mm});
            skLineSegment(sketch, "E15.8.5.7", {"start": v(-43.3, -66.36) * mm, "end": v(-41.72, -69.09) * mm});
            skLineSegment(sketch, "E15.11.5.7", {"start": v(-41.72, -69.09) * mm, "end": v(-43.3, -71.82) * mm});
            skLineSegment(sketch, "E15.14.5.7", {"start": v(-43.3, -71.82) * mm, "end": v(-46.45, -71.82) * mm});
            skLineSegment(sketch, "E15.17.5.7", {"start": v(-46.45, -71.82) * mm, "end": v(-48.03, -69.09) * mm});
            skCircle(sketch, "E15.0.5.8", {"center": v(-44.87, -60.45) * mm, "radius": 2.73 * mm, "construction": true});
            skLineSegment(sketch, "E15.2.5.8", {"start": v(-48.03, -60.45) * mm, "end": v(-46.45, -57.72) * mm});
            skLineSegment(sketch, "E15.5.5.8", {"start": v(-46.45, -57.72) * mm, "end": v(-43.3, -57.72) * mm});
            skLineSegment(sketch, "E15.8.5.8", {"start": v(-43.3, -57.72) * mm, "end": v(-41.72, -60.45) * mm});
            skLineSegment(sketch, "E15.11.5.8", {"start": v(-41.72, -60.45) * mm, "end": v(-43.3, -63.18) * mm});
            skLineSegment(sketch, "E15.14.5.8", {"start": v(-43.3, -63.18) * mm, "end": v(-46.45, -63.18) * mm});
            skLineSegment(sketch, "E15.17.5.8", {"start": v(-46.45, -63.18) * mm, "end": v(-48.03, -60.45) * mm});
            skCircle(sketch, "E15.0.5.9", {"center": v(-44.87, -51.82) * mm, "radius": 2.73 * mm, "construction": true});
            skLineSegment(sketch, "E15.2.5.9", {"start": v(-48.03, -51.82) * mm, "end": v(-46.45, -49.09) * mm});
            skLineSegment(sketch, "E15.5.5.9", {"start": v(-46.45, -49.09) * mm, "end": v(-43.3, -49.09) * mm});
            skLineSegment(sketch, "E15.8.5.9", {"start": v(-43.3, -49.09) * mm, "end": v(-41.72, -51.82) * mm});
            skLineSegment(sketch, "E15.11.5.9", {"start": v(-41.72, -51.82) * mm, "end": v(-43.3, -54.55) * mm});
            skLineSegment(sketch, "E15.14.5.9", {"start": v(-43.3, -54.55) * mm, "end": v(-46.45, -54.55) * mm});
            skLineSegment(sketch, "E15.17.5.9", {"start": v(-46.45, -54.55) * mm, "end": v(-48.03, -51.82) * mm});
            skCircle(sketch, "E15.0.5.10", {"center": v(-44.87, -43.18) * mm, "radius": 2.73 * mm, "construction": true});
            skLineSegment(sketch, "E15.2.5.10", {"start": v(-48.03, -43.18) * mm, "end": v(-46.45, -40.45) * mm});
            skLineSegment(sketch, "E15.5.5.10", {"start": v(-46.45, -40.45) * mm, "end": v(-43.3, -40.45) * mm});
            skLineSegment(sketch, "E15.8.5.10", {"start": v(-43.3, -40.45) * mm, "end": v(-41.72, -43.18) * mm});
            skLineSegment(sketch, "E15.11.5.10", {"start": v(-41.72, -43.18) * mm, "end": v(-43.3, -45.91) * mm});
            skLineSegment(sketch, "E15.14.5.10", {"start": v(-43.3, -45.91) * mm, "end": v(-46.45, -45.91) * mm});
            skLineSegment(sketch, "E15.17.5.10", {"start": v(-46.45, -45.91) * mm, "end": v(-48.03, -43.18) * mm});
            skCircle(sketch, "E15.0.5.11", {"center": v(-44.87, -34.54) * mm, "radius": 2.73 * mm, "construction": true});
            skLineSegment(sketch, "E15.2.5.11", {"start": v(-48.03, -34.54) * mm, "end": v(-46.45, -31.81) * mm});
            skLineSegment(sketch, "E15.5.5.11", {"start": v(-46.45, -31.81) * mm, "end": v(-43.3, -31.81) * mm});
            skLineSegment(sketch, "E15.8.5.11", {"start": v(-43.3, -31.81) * mm, "end": v(-41.72, -34.54) * mm});
            skLineSegment(sketch, "E15.11.5.11", {"start": v(-41.72, -34.54) * mm, "end": v(-43.3, -37.27) * mm});
            skLineSegment(sketch, "E15.14.5.11", {"start": v(-43.3, -37.27) * mm, "end": v(-46.45, -37.27) * mm});
            skLineSegment(sketch, "E15.17.5.11", {"start": v(-46.45, -37.27) * mm, "end": v(-48.03, -34.54) * mm});
            skCircle(sketch, "E15.0.5.12", {"center": v(-44.87, -25.9) * mm, "radius": 2.73 * mm, "construction": true});
            skLineSegment(sketch, "E15.2.5.12", {"start": v(-48.03, -25.9) * mm, "end": v(-46.45, -23.18) * mm});
            skLineSegment(sketch, "E15.5.5.12", {"start": v(-46.45, -23.18) * mm, "end": v(-43.3, -23.18) * mm});
            skLineSegment(sketch, "E15.8.5.12", {"start": v(-43.3, -23.18) * mm, "end": v(-41.72, -25.9) * mm});
            skLineSegment(sketch, "E15.11.5.12", {"start": v(-41.72, -25.9) * mm, "end": v(-43.3, -28.64) * mm});
            skLineSegment(sketch, "E15.14.5.12", {"start": v(-43.3, -28.64) * mm, "end": v(-46.45, -28.64) * mm});
            skLineSegment(sketch, "E15.17.5.12", {"start": v(-46.45, -28.64) * mm, "end": v(-48.03, -25.9) * mm});
            skCircle(sketch, "E15.0.5.13", {"center": v(-44.87, -17.27) * mm, "radius": 2.73 * mm, "construction": true});
            skLineSegment(sketch, "E15.2.5.13", {"start": v(-48.03, -17.27) * mm, "end": v(-46.45, -14.54) * mm});
            skLineSegment(sketch, "E15.5.5.13", {"start": v(-46.45, -14.54) * mm, "end": v(-43.3, -14.54) * mm});
            skLineSegment(sketch, "E15.8.5.13", {"start": v(-43.3, -14.54) * mm, "end": v(-41.72, -17.27) * mm});
            skLineSegment(sketch, "E15.11.5.13", {"start": v(-41.72, -17.27) * mm, "end": v(-43.3, -20) * mm});
            skLineSegment(sketch, "E15.14.5.13", {"start": v(-43.3, -20) * mm, "end": v(-46.45, -20) * mm});
            skLineSegment(sketch, "E15.17.5.13", {"start": v(-46.45, -20) * mm, "end": v(-48.03, -17.27) * mm});
            skCircle(sketch, "E15.0.5.14", {"center": v(-44.87, -8.64) * mm, "radius": 2.73 * mm, "construction": true});
            skLineSegment(sketch, "E15.2.5.14", {"start": v(-48.03, -8.64) * mm, "end": v(-46.45, -5.9) * mm});
            skLineSegment(sketch, "E15.5.5.14", {"start": v(-46.45, -5.9) * mm, "end": v(-43.3, -5.9) * mm});
            skLineSegment(sketch, "E15.8.5.14", {"start": v(-43.3, -5.9) * mm, "end": v(-41.72, -8.64) * mm});
            skLineSegment(sketch, "E15.11.5.14", {"start": v(-41.72, -8.64) * mm, "end": v(-43.3, -11.37) * mm});
            skLineSegment(sketch, "E15.14.5.14", {"start": v(-43.3, -11.37) * mm, "end": v(-46.45, -11.37) * mm});
            skLineSegment(sketch, "E15.17.5.14", {"start": v(-46.45, -11.37) * mm, "end": v(-48.03, -8.64) * mm});
            skCircle(sketch, "E15.0.5.15", {"center": v(-44.87, 0) * mm, "radius": 2.73 * mm, "construction": true});
            skLineSegment(sketch, "E15.2.5.15", {"start": v(-48.03, 0) * mm, "end": v(-46.45, 2.73) * mm});
            skLineSegment(sketch, "E15.5.5.15", {"start": v(-46.45, 2.73) * mm, "end": v(-43.3, 2.73) * mm});
            skLineSegment(sketch, "E15.8.5.15", {"start": v(-43.3, 2.73) * mm, "end": v(-41.72, 0) * mm});
            skLineSegment(sketch, "E15.11.5.15", {"start": v(-41.72, 0) * mm, "end": v(-43.3, -2.73) * mm});
            skLineSegment(sketch, "E15.14.5.15", {"start": v(-43.3, -2.73) * mm, "end": v(-46.45, -2.73) * mm});
            skLineSegment(sketch, "E15.17.5.15", {"start": v(-46.45, -2.73) * mm, "end": v(-48.03, 0) * mm});
            skCircle(sketch, "E15.0.5.16", {"center": v(-44.87, 8.64) * mm, "radius": 2.73 * mm, "construction": true});
            skLineSegment(sketch, "E15.2.5.16", {"start": v(-48.03, 8.64) * mm, "end": v(-46.45, 11.37) * mm});
            skLineSegment(sketch, "E15.5.5.16", {"start": v(-46.45, 11.37) * mm, "end": v(-43.3, 11.37) * mm});
            skLineSegment(sketch, "E15.8.5.16", {"start": v(-43.3, 11.37) * mm, "end": v(-41.72, 8.64) * mm});
            skLineSegment(sketch, "E15.11.5.16", {"start": v(-41.72, 8.64) * mm, "end": v(-43.3, 5.9) * mm});
            skLineSegment(sketch, "E15.14.5.16", {"start": v(-43.3, 5.9) * mm, "end": v(-46.45, 5.9) * mm});
            skLineSegment(sketch, "E15.17.5.16", {"start": v(-46.45, 5.9) * mm, "end": v(-48.03, 8.64) * mm});
            skCircle(sketch, "E15.0.5.17", {"center": v(-44.87, 17.27) * mm, "radius": 2.73 * mm, "construction": true});
            skLineSegment(sketch, "E15.2.5.17", {"start": v(-48.03, 17.27) * mm, "end": v(-46.45, 20) * mm});
            skLineSegment(sketch, "E15.5.5.17", {"start": v(-46.45, 20) * mm, "end": v(-43.3, 20) * mm});
            skLineSegment(sketch, "E15.8.5.17", {"start": v(-43.3, 20) * mm, "end": v(-41.72, 17.27) * mm});
            skLineSegment(sketch, "E15.11.5.17", {"start": v(-41.72, 17.27) * mm, "end": v(-43.3, 14.54) * mm});
            skLineSegment(sketch, "E15.14.5.17", {"start": v(-43.3, 14.54) * mm, "end": v(-46.45, 14.54) * mm});
            skLineSegment(sketch, "E15.17.5.17", {"start": v(-46.45, 14.54) * mm, "end": v(-48.03, 17.27) * mm});
            skCircle(sketch, "E15.0.5.18", {"center": v(-44.87, 25.9) * mm, "radius": 2.73 * mm, "construction": true});
            skLineSegment(sketch, "E15.2.5.18", {"start": v(-48.03, 25.9) * mm, "end": v(-46.45, 28.64) * mm});
            skLineSegment(sketch, "E15.5.5.18", {"start": v(-46.45, 28.64) * mm, "end": v(-43.3, 28.64) * mm});
            skLineSegment(sketch, "E15.8.5.18", {"start": v(-43.3, 28.64) * mm, "end": v(-41.72, 25.9) * mm});
            skLineSegment(sketch, "E15.11.5.18", {"start": v(-41.72, 25.9) * mm, "end": v(-43.3, 23.18) * mm});
            skLineSegment(sketch, "E15.14.5.18", {"start": v(-43.3, 23.18) * mm, "end": v(-46.45, 23.18) * mm});
            skLineSegment(sketch, "E15.17.5.18", {"start": v(-46.45, 23.18) * mm, "end": v(-48.03, 25.9) * mm});
            skCircle(sketch, "E15.0.5.19", {"center": v(-44.87, 34.54) * mm, "radius": 2.73 * mm, "construction": true});
            skLineSegment(sketch, "E15.2.5.19", {"start": v(-48.03, 34.54) * mm, "end": v(-46.45, 37.27) * mm});
            skLineSegment(sketch, "E15.5.5.19", {"start": v(-46.45, 37.27) * mm, "end": v(-43.3, 37.27) * mm});
            skLineSegment(sketch, "E15.8.5.19", {"start": v(-43.3, 37.27) * mm, "end": v(-41.72, 34.54) * mm});
            skLineSegment(sketch, "E15.11.5.19", {"start": v(-41.72, 34.54) * mm, "end": v(-43.3, 31.81) * mm});
            skLineSegment(sketch, "E15.14.5.19", {"start": v(-43.3, 31.81) * mm, "end": v(-46.45, 31.81) * mm});
            skLineSegment(sketch, "E15.17.5.19", {"start": v(-46.45, 31.81) * mm, "end": v(-48.03, 34.54) * mm});
            skCircle(sketch, "E15.0.6.0", {"center": v(-29.92, -129.54) * mm, "radius": 2.73 * mm, "construction": true});
            skLineSegment(sketch, "E15.2.6.0", {"start": v(-33.07, -129.54) * mm, "end": v(-31.5, -126.8) * mm});
            skLineSegment(sketch, "E15.5.6.0", {"start": v(-31.5, -126.8) * mm, "end": v(-28.34, -126.8) * mm});
            skLineSegment(sketch, "E15.8.6.0", {"start": v(-28.34, -126.8) * mm, "end": v(-26.76, -129.54) * mm});
            skLineSegment(sketch, "E15.11.6.0", {"start": v(-26.76, -129.54) * mm, "end": v(-28.34, -132.27) * mm});
            skLineSegment(sketch, "E15.14.6.0", {"start": v(-28.34, -132.27) * mm, "end": v(-31.5, -132.27) * mm});
            skLineSegment(sketch, "E15.17.6.0", {"start": v(-31.5, -132.27) * mm, "end": v(-33.07, -129.54) * mm});
            skCircle(sketch, "E15.0.6.1", {"center": v(-29.92, -120.9) * mm, "radius": 2.73 * mm, "construction": true});
            skLineSegment(sketch, "E15.2.6.1", {"start": v(-33.07, -120.9) * mm, "end": v(-31.5, -118.17) * mm});
            skLineSegment(sketch, "E15.5.6.1", {"start": v(-31.5, -118.17) * mm, "end": v(-28.34, -118.17) * mm});
            skLineSegment(sketch, "E15.8.6.1", {"start": v(-28.34, -118.17) * mm, "end": v(-26.76, -120.9) * mm});
            skLineSegment(sketch, "E15.11.6.1", {"start": v(-26.76, -120.9) * mm, "end": v(-28.34, -123.63) * mm});
            skLineSegment(sketch, "E15.14.6.1", {"start": v(-28.34, -123.63) * mm, "end": v(-31.5, -123.63) * mm});
            skLineSegment(sketch, "E15.17.6.1", {"start": v(-31.5, -123.63) * mm, "end": v(-33.07, -120.9) * mm});
            skCircle(sketch, "E15.0.6.2", {"center": v(-29.92, -112.27) * mm, "radius": 2.73 * mm, "construction": true});
            skLineSegment(sketch, "E15.2.6.2", {"start": v(-33.07, -112.27) * mm, "end": v(-31.5, -109.54) * mm});
            skLineSegment(sketch, "E15.5.6.2", {"start": v(-31.5, -109.54) * mm, "end": v(-28.34, -109.54) * mm});
            skLineSegment(sketch, "E15.8.6.2", {"start": v(-28.34, -109.54) * mm, "end": v(-26.76, -112.27) * mm});
            skLineSegment(sketch, "E15.11.6.2", {"start": v(-26.76, -112.27) * mm, "end": v(-28.34, -115) * mm});
            skLineSegment(sketch, "E15.14.6.2", {"start": v(-28.34, -115) * mm, "end": v(-31.5, -115) * mm});
            skLineSegment(sketch, "E15.17.6.2", {"start": v(-31.5, -115) * mm, "end": v(-33.07, -112.27) * mm});
            skCircle(sketch, "E15.0.6.3", {"center": v(-29.92, -103.63) * mm, "radius": 2.73 * mm, "construction": true});
            skLineSegment(sketch, "E15.2.6.3", {"start": v(-33.07, -103.63) * mm, "end": v(-31.5, -100.9) * mm});
            skLineSegment(sketch, "E15.5.6.3", {"start": v(-31.5, -100.9) * mm, "end": v(-28.34, -100.9) * mm});
            skLineSegment(sketch, "E15.8.6.3", {"start": v(-28.34, -100.9) * mm, "end": v(-26.76, -103.63) * mm});
            skLineSegment(sketch, "E15.11.6.3", {"start": v(-26.76, -103.63) * mm, "end": v(-28.34, -106.36) * mm});
            skLineSegment(sketch, "E15.14.6.3", {"start": v(-28.34, -106.36) * mm, "end": v(-31.5, -106.36) * mm});
            skLineSegment(sketch, "E15.17.6.3", {"start": v(-31.5, -106.36) * mm, "end": v(-33.07, -103.63) * mm});
            skCircle(sketch, "E15.0.6.4", {"center": v(-29.92, -95) * mm, "radius": 2.73 * mm, "construction": true});
            skLineSegment(sketch, "E15.2.6.4", {"start": v(-33.07, -95) * mm, "end": v(-31.5, -92.27) * mm});
            skLineSegment(sketch, "E15.5.6.4", {"start": v(-31.5, -92.27) * mm, "end": v(-28.34, -92.27) * mm});
            skLineSegment(sketch, "E15.8.6.4", {"start": v(-28.34, -92.27) * mm, "end": v(-26.76, -95) * mm});
            skLineSegment(sketch, "E15.11.6.4", {"start": v(-26.76, -95) * mm, "end": v(-28.34, -97.73) * mm});
            skLineSegment(sketch, "E15.14.6.4", {"start": v(-28.34, -97.73) * mm, "end": v(-31.5, -97.73) * mm});
            skLineSegment(sketch, "E15.17.6.4", {"start": v(-31.5, -97.73) * mm, "end": v(-33.07, -95) * mm});
            skCircle(sketch, "E15.0.6.5", {"center": v(-29.92, -86.36) * mm, "radius": 2.73 * mm, "construction": true});
            skLineSegment(sketch, "E15.2.6.5", {"start": v(-33.07, -86.36) * mm, "end": v(-31.5, -83.63) * mm});
            skLineSegment(sketch, "E15.5.6.5", {"start": v(-31.5, -83.63) * mm, "end": v(-28.34, -83.63) * mm});
            skLineSegment(sketch, "E15.8.6.5", {"start": v(-28.34, -83.63) * mm, "end": v(-26.76, -86.36) * mm});
            skLineSegment(sketch, "E15.11.6.5", {"start": v(-26.76, -86.36) * mm, "end": v(-28.34, -89.1) * mm});
            skLineSegment(sketch, "E15.14.6.5", {"start": v(-28.34, -89.1) * mm, "end": v(-31.5, -89.1) * mm});
            skLineSegment(sketch, "E15.17.6.5", {"start": v(-31.5, -89.1) * mm, "end": v(-33.07, -86.36) * mm});
            skCircle(sketch, "E15.0.6.6", {"center": v(-29.92, -77.72) * mm, "radius": 2.73 * mm, "construction": true});
            skLineSegment(sketch, "E15.2.6.6", {"start": v(-33.07, -77.72) * mm, "end": v(-31.5, -75) * mm});
            skLineSegment(sketch, "E15.5.6.6", {"start": v(-31.5, -75) * mm, "end": v(-28.34, -75) * mm});
            skLineSegment(sketch, "E15.8.6.6", {"start": v(-28.34, -75) * mm, "end": v(-26.76, -77.72) * mm});
            skLineSegment(sketch, "E15.11.6.6", {"start": v(-26.76, -77.72) * mm, "end": v(-28.34, -80.45) * mm});
            skLineSegment(sketch, "E15.14.6.6", {"start": v(-28.34, -80.45) * mm, "end": v(-31.5, -80.45) * mm});
            skLineSegment(sketch, "E15.17.6.6", {"start": v(-31.5, -80.45) * mm, "end": v(-33.07, -77.72) * mm});
            skCircle(sketch, "E15.0.6.7", {"center": v(-29.92, -69.09) * mm, "radius": 2.73 * mm, "construction": true});
            skLineSegment(sketch, "E15.2.6.7", {"start": v(-33.07, -69.09) * mm, "end": v(-31.5, -66.36) * mm});
            skLineSegment(sketch, "E15.5.6.7", {"start": v(-31.5, -66.36) * mm, "end": v(-28.34, -66.36) * mm});
            skLineSegment(sketch, "E15.8.6.7", {"start": v(-28.34, -66.36) * mm, "end": v(-26.76, -69.09) * mm});
            skLineSegment(sketch, "E15.11.6.7", {"start": v(-26.76, -69.09) * mm, "end": v(-28.34, -71.82) * mm});
            skLineSegment(sketch, "E15.14.6.7", {"start": v(-28.34, -71.82) * mm, "end": v(-31.5, -71.82) * mm});
            skLineSegment(sketch, "E15.17.6.7", {"start": v(-31.5, -71.82) * mm, "end": v(-33.07, -69.09) * mm});
            skCircle(sketch, "E15.0.6.8", {"center": v(-29.92, -60.45) * mm, "radius": 2.73 * mm, "construction": true});
            skLineSegment(sketch, "E15.2.6.8", {"start": v(-33.07, -60.45) * mm, "end": v(-31.5, -57.72) * mm});
            skLineSegment(sketch, "E15.5.6.8", {"start": v(-31.5, -57.72) * mm, "end": v(-28.34, -57.72) * mm});
            skLineSegment(sketch, "E15.8.6.8", {"start": v(-28.34, -57.72) * mm, "end": v(-26.76, -60.45) * mm});
            skLineSegment(sketch, "E15.11.6.8", {"start": v(-26.76, -60.45) * mm, "end": v(-28.34, -63.18) * mm});
            skLineSegment(sketch, "E15.14.6.8", {"start": v(-28.34, -63.18) * mm, "end": v(-31.5, -63.18) * mm});
            skLineSegment(sketch, "E15.17.6.8", {"start": v(-31.5, -63.18) * mm, "end": v(-33.07, -60.45) * mm});
            skCircle(sketch, "E15.0.6.9", {"center": v(-29.92, -51.82) * mm, "radius": 2.73 * mm, "construction": true});
            skLineSegment(sketch, "E15.2.6.9", {"start": v(-33.07, -51.82) * mm, "end": v(-31.5, -49.09) * mm});
            skLineSegment(sketch, "E15.5.6.9", {"start": v(-31.5, -49.09) * mm, "end": v(-28.34, -49.09) * mm});
            skLineSegment(sketch, "E15.8.6.9", {"start": v(-28.34, -49.09) * mm, "end": v(-26.76, -51.82) * mm});
            skLineSegment(sketch, "E15.11.6.9", {"start": v(-26.76, -51.82) * mm, "end": v(-28.34, -54.55) * mm});
            skLineSegment(sketch, "E15.14.6.9", {"start": v(-28.34, -54.55) * mm, "end": v(-31.5, -54.55) * mm});
            skLineSegment(sketch, "E15.17.6.9", {"start": v(-31.5, -54.55) * mm, "end": v(-33.07, -51.82) * mm});
            skCircle(sketch, "E15.0.6.10", {"center": v(-29.92, -43.18) * mm, "radius": 2.73 * mm, "construction": true});
            skLineSegment(sketch, "E15.2.6.10", {"start": v(-33.07, -43.18) * mm, "end": v(-31.5, -40.45) * mm});
            skLineSegment(sketch, "E15.5.6.10", {"start": v(-31.5, -40.45) * mm, "end": v(-28.34, -40.45) * mm});
            skLineSegment(sketch, "E15.8.6.10", {"start": v(-28.34, -40.45) * mm, "end": v(-26.76, -43.18) * mm});
            skLineSegment(sketch, "E15.11.6.10", {"start": v(-26.76, -43.18) * mm, "end": v(-28.34, -45.91) * mm});
            skLineSegment(sketch, "E15.14.6.10", {"start": v(-28.34, -45.91) * mm, "end": v(-31.5, -45.91) * mm});
            skLineSegment(sketch, "E15.17.6.10", {"start": v(-31.5, -45.91) * mm, "end": v(-33.07, -43.18) * mm});
            skCircle(sketch, "E15.0.6.11", {"center": v(-29.92, -34.54) * mm, "radius": 2.73 * mm, "construction": true});
            skLineSegment(sketch, "E15.2.6.11", {"start": v(-33.07, -34.54) * mm, "end": v(-31.5, -31.81) * mm});
            skLineSegment(sketch, "E15.5.6.11", {"start": v(-31.5, -31.81) * mm, "end": v(-28.34, -31.81) * mm});
            skLineSegment(sketch, "E15.8.6.11", {"start": v(-28.34, -31.81) * mm, "end": v(-26.76, -34.54) * mm});
            skLineSegment(sketch, "E15.11.6.11", {"start": v(-26.76, -34.54) * mm, "end": v(-28.34, -37.27) * mm});
            skLineSegment(sketch, "E15.14.6.11", {"start": v(-28.34, -37.27) * mm, "end": v(-31.5, -37.27) * mm});
            skLineSegment(sketch, "E15.17.6.11", {"start": v(-31.5, -37.27) * mm, "end": v(-33.07, -34.54) * mm});
            skCircle(sketch, "E15.0.6.12", {"center": v(-29.92, -25.9) * mm, "radius": 2.73 * mm, "construction": true});
            skLineSegment(sketch, "E15.2.6.12", {"start": v(-33.07, -25.9) * mm, "end": v(-31.5, -23.18) * mm});
            skLineSegment(sketch, "E15.5.6.12", {"start": v(-31.5, -23.18) * mm, "end": v(-28.34, -23.18) * mm});
            skLineSegment(sketch, "E15.8.6.12", {"start": v(-28.34, -23.18) * mm, "end": v(-26.76, -25.9) * mm});
            skLineSegment(sketch, "E15.11.6.12", {"start": v(-26.76, -25.9) * mm, "end": v(-28.34, -28.64) * mm});
            skLineSegment(sketch, "E15.14.6.12", {"start": v(-28.34, -28.64) * mm, "end": v(-31.5, -28.64) * mm});
            skLineSegment(sketch, "E15.17.6.12", {"start": v(-31.5, -28.64) * mm, "end": v(-33.07, -25.9) * mm});
            skCircle(sketch, "E15.0.6.13", {"center": v(-29.92, -17.27) * mm, "radius": 2.73 * mm, "construction": true});
            skLineSegment(sketch, "E15.2.6.13", {"start": v(-33.07, -17.27) * mm, "end": v(-31.5, -14.54) * mm});
            skLineSegment(sketch, "E15.5.6.13", {"start": v(-31.5, -14.54) * mm, "end": v(-28.34, -14.54) * mm});
            skLineSegment(sketch, "E15.8.6.13", {"start": v(-28.34, -14.54) * mm, "end": v(-26.76, -17.27) * mm});
            skLineSegment(sketch, "E15.11.6.13", {"start": v(-26.76, -17.27) * mm, "end": v(-28.34, -20) * mm});
            skLineSegment(sketch, "E15.14.6.13", {"start": v(-28.34, -20) * mm, "end": v(-31.5, -20) * mm});
            skLineSegment(sketch, "E15.17.6.13", {"start": v(-31.5, -20) * mm, "end": v(-33.07, -17.27) * mm});
            skCircle(sketch, "E15.0.6.14", {"center": v(-29.92, -8.64) * mm, "radius": 2.73 * mm, "construction": true});
            skLineSegment(sketch, "E15.2.6.14", {"start": v(-33.07, -8.64) * mm, "end": v(-31.5, -5.9) * mm});
            skLineSegment(sketch, "E15.5.6.14", {"start": v(-31.5, -5.9) * mm, "end": v(-28.34, -5.9) * mm});
            skLineSegment(sketch, "E15.8.6.14", {"start": v(-28.34, -5.9) * mm, "end": v(-26.76, -8.64) * mm});
            skLineSegment(sketch, "E15.11.6.14", {"start": v(-26.76, -8.64) * mm, "end": v(-28.34, -11.37) * mm});
            skLineSegment(sketch, "E15.14.6.14", {"start": v(-28.34, -11.37) * mm, "end": v(-31.5, -11.37) * mm});
            skLineSegment(sketch, "E15.17.6.14", {"start": v(-31.5, -11.37) * mm, "end": v(-33.07, -8.64) * mm});
            skCircle(sketch, "E15.0.6.15", {"center": v(-29.92, 0) * mm, "radius": 2.73 * mm, "construction": true});
            skLineSegment(sketch, "E15.2.6.15", {"start": v(-33.07, 0) * mm, "end": v(-31.5, 2.73) * mm});
            skLineSegment(sketch, "E15.5.6.15", {"start": v(-31.5, 2.73) * mm, "end": v(-28.34, 2.73) * mm});
            skLineSegment(sketch, "E15.8.6.15", {"start": v(-28.34, 2.73) * mm, "end": v(-26.76, 0) * mm});
            skLineSegment(sketch, "E15.11.6.15", {"start": v(-26.76, 0) * mm, "end": v(-28.34, -2.73) * mm});
            skLineSegment(sketch, "E15.14.6.15", {"start": v(-28.34, -2.73) * mm, "end": v(-31.5, -2.73) * mm});
            skLineSegment(sketch, "E15.17.6.15", {"start": v(-31.5, -2.73) * mm, "end": v(-33.07, 0) * mm});
            skCircle(sketch, "E15.0.6.16", {"center": v(-29.92, 8.64) * mm, "radius": 2.73 * mm, "construction": true});
            skLineSegment(sketch, "E15.2.6.16", {"start": v(-33.07, 8.64) * mm, "end": v(-31.5, 11.37) * mm});
            skLineSegment(sketch, "E15.5.6.16", {"start": v(-31.5, 11.37) * mm, "end": v(-28.34, 11.37) * mm});
            skLineSegment(sketch, "E15.8.6.16", {"start": v(-28.34, 11.37) * mm, "end": v(-26.76, 8.64) * mm});
            skLineSegment(sketch, "E15.11.6.16", {"start": v(-26.76, 8.64) * mm, "end": v(-28.34, 5.9) * mm});
            skLineSegment(sketch, "E15.14.6.16", {"start": v(-28.34, 5.9) * mm, "end": v(-31.5, 5.9) * mm});
            skLineSegment(sketch, "E15.17.6.16", {"start": v(-31.5, 5.9) * mm, "end": v(-33.07, 8.64) * mm});
            skCircle(sketch, "E15.0.6.17", {"center": v(-29.92, 17.27) * mm, "radius": 2.73 * mm, "construction": true});
            skLineSegment(sketch, "E15.2.6.17", {"start": v(-33.07, 17.27) * mm, "end": v(-31.5, 20) * mm});
            skLineSegment(sketch, "E15.5.6.17", {"start": v(-31.5, 20) * mm, "end": v(-28.34, 20) * mm});
            skLineSegment(sketch, "E15.8.6.17", {"start": v(-28.34, 20) * mm, "end": v(-26.76, 17.27) * mm});
            skLineSegment(sketch, "E15.11.6.17", {"start": v(-26.76, 17.27) * mm, "end": v(-28.34, 14.54) * mm});
            skLineSegment(sketch, "E15.14.6.17", {"start": v(-28.34, 14.54) * mm, "end": v(-31.5, 14.54) * mm});
            skLineSegment(sketch, "E15.17.6.17", {"start": v(-31.5, 14.54) * mm, "end": v(-33.07, 17.27) * mm});
            skCircle(sketch, "E15.0.6.18", {"center": v(-29.92, 25.9) * mm, "radius": 2.73 * mm, "construction": true});
            skLineSegment(sketch, "E15.2.6.18", {"start": v(-33.07, 25.9) * mm, "end": v(-31.5, 28.64) * mm});
            skLineSegment(sketch, "E15.5.6.18", {"start": v(-31.5, 28.64) * mm, "end": v(-28.34, 28.64) * mm});
            skLineSegment(sketch, "E15.8.6.18", {"start": v(-28.34, 28.64) * mm, "end": v(-26.76, 25.9) * mm});
            skLineSegment(sketch, "E15.11.6.18", {"start": v(-26.76, 25.9) * mm, "end": v(-28.34, 23.18) * mm});
            skLineSegment(sketch, "E15.14.6.18", {"start": v(-28.34, 23.18) * mm, "end": v(-31.5, 23.18) * mm});
            skLineSegment(sketch, "E15.17.6.18", {"start": v(-31.5, 23.18) * mm, "end": v(-33.07, 25.9) * mm});
            skCircle(sketch, "E15.0.6.19", {"center": v(-29.92, 34.54) * mm, "radius": 2.73 * mm, "construction": true});
            skLineSegment(sketch, "E15.2.6.19", {"start": v(-33.07, 34.54) * mm, "end": v(-31.5, 37.27) * mm});
            skLineSegment(sketch, "E15.5.6.19", {"start": v(-31.5, 37.27) * mm, "end": v(-28.34, 37.27) * mm});
            skLineSegment(sketch, "E15.8.6.19", {"start": v(-28.34, 37.27) * mm, "end": v(-26.76, 34.54) * mm});
            skLineSegment(sketch, "E15.11.6.19", {"start": v(-26.76, 34.54) * mm, "end": v(-28.34, 31.81) * mm});
            skLineSegment(sketch, "E15.14.6.19", {"start": v(-28.34, 31.81) * mm, "end": v(-31.5, 31.81) * mm});
            skLineSegment(sketch, "E15.17.6.19", {"start": v(-31.5, 31.81) * mm, "end": v(-33.07, 34.54) * mm});
            skCircle(sketch, "E15.0.7.0", {"center": v(-14.96, -129.54) * mm, "radius": 2.73 * mm, "construction": true});
            skLineSegment(sketch, "E15.2.7.0", {"start": v(-18.11, -129.54) * mm, "end": v(-16.53, -126.8) * mm});
            skLineSegment(sketch, "E15.5.7.0", {"start": v(-16.53, -126.8) * mm, "end": v(-13.38, -126.8) * mm});
            skLineSegment(sketch, "E15.8.7.0", {"start": v(-13.38, -126.8) * mm, "end": v(-11.8, -129.54) * mm});
            skLineSegment(sketch, "E15.11.7.0", {"start": v(-11.8, -129.54) * mm, "end": v(-13.38, -132.27) * mm});
            skLineSegment(sketch, "E15.14.7.0", {"start": v(-13.38, -132.27) * mm, "end": v(-16.53, -132.27) * mm});
            skLineSegment(sketch, "E15.17.7.0", {"start": v(-16.53, -132.27) * mm, "end": v(-18.11, -129.54) * mm});
            skCircle(sketch, "E15.0.7.1", {"center": v(-14.96, -120.9) * mm, "radius": 2.73 * mm, "construction": true});
            skLineSegment(sketch, "E15.2.7.1", {"start": v(-18.11, -120.9) * mm, "end": v(-16.53, -118.17) * mm});
            skLineSegment(sketch, "E15.5.7.1", {"start": v(-16.53, -118.17) * mm, "end": v(-13.38, -118.17) * mm});
            skLineSegment(sketch, "E15.8.7.1", {"start": v(-13.38, -118.17) * mm, "end": v(-11.8, -120.9) * mm});
            skLineSegment(sketch, "E15.11.7.1", {"start": v(-11.8, -120.9) * mm, "end": v(-13.38, -123.63) * mm});
            skLineSegment(sketch, "E15.14.7.1", {"start": v(-13.38, -123.63) * mm, "end": v(-16.53, -123.63) * mm});
            skLineSegment(sketch, "E15.17.7.1", {"start": v(-16.53, -123.63) * mm, "end": v(-18.11, -120.9) * mm});
            skCircle(sketch, "E15.0.7.2", {"center": v(-14.96, -112.27) * mm, "radius": 2.73 * mm, "construction": true});
            skLineSegment(sketch, "E15.2.7.2", {"start": v(-18.11, -112.27) * mm, "end": v(-16.53, -109.54) * mm});
            skLineSegment(sketch, "E15.5.7.2", {"start": v(-16.53, -109.54) * mm, "end": v(-13.38, -109.54) * mm});
            skLineSegment(sketch, "E15.8.7.2", {"start": v(-13.38, -109.54) * mm, "end": v(-11.8, -112.27) * mm});
            skLineSegment(sketch, "E15.11.7.2", {"start": v(-11.8, -112.27) * mm, "end": v(-13.38, -115) * mm});
            skLineSegment(sketch, "E15.14.7.2", {"start": v(-13.38, -115) * mm, "end": v(-16.53, -115) * mm});
            skLineSegment(sketch, "E15.17.7.2", {"start": v(-16.53, -115) * mm, "end": v(-18.11, -112.27) * mm});
            skCircle(sketch, "E15.0.7.3", {"center": v(-14.96, -103.63) * mm, "radius": 2.73 * mm, "construction": true});
            skLineSegment(sketch, "E15.2.7.3", {"start": v(-18.11, -103.63) * mm, "end": v(-16.53, -100.9) * mm});
            skLineSegment(sketch, "E15.5.7.3", {"start": v(-16.53, -100.9) * mm, "end": v(-13.38, -100.9) * mm});
            skLineSegment(sketch, "E15.8.7.3", {"start": v(-13.38, -100.9) * mm, "end": v(-11.8, -103.63) * mm});
            skLineSegment(sketch, "E15.11.7.3", {"start": v(-11.8, -103.63) * mm, "end": v(-13.38, -106.36) * mm});
            skLineSegment(sketch, "E15.14.7.3", {"start": v(-13.38, -106.36) * mm, "end": v(-16.53, -106.36) * mm});
            skLineSegment(sketch, "E15.17.7.3", {"start": v(-16.53, -106.36) * mm, "end": v(-18.11, -103.63) * mm});
            skCircle(sketch, "E15.0.7.4", {"center": v(-14.96, -95) * mm, "radius": 2.73 * mm, "construction": true});
            skLineSegment(sketch, "E15.2.7.4", {"start": v(-18.11, -95) * mm, "end": v(-16.53, -92.27) * mm});
            skLineSegment(sketch, "E15.5.7.4", {"start": v(-16.53, -92.27) * mm, "end": v(-13.38, -92.27) * mm});
            skLineSegment(sketch, "E15.8.7.4", {"start": v(-13.38, -92.27) * mm, "end": v(-11.8, -95) * mm});
            skLineSegment(sketch, "E15.11.7.4", {"start": v(-11.8, -95) * mm, "end": v(-13.38, -97.73) * mm});
            skLineSegment(sketch, "E15.14.7.4", {"start": v(-13.38, -97.73) * mm, "end": v(-16.53, -97.73) * mm});
            skLineSegment(sketch, "E15.17.7.4", {"start": v(-16.53, -97.73) * mm, "end": v(-18.11, -95) * mm});
            skCircle(sketch, "E15.0.7.5", {"center": v(-14.96, -86.36) * mm, "radius": 2.73 * mm, "construction": true});
            skLineSegment(sketch, "E15.2.7.5", {"start": v(-18.11, -86.36) * mm, "end": v(-16.53, -83.63) * mm});
            skLineSegment(sketch, "E15.5.7.5", {"start": v(-16.53, -83.63) * mm, "end": v(-13.38, -83.63) * mm});
            skLineSegment(sketch, "E15.8.7.5", {"start": v(-13.38, -83.63) * mm, "end": v(-11.8, -86.36) * mm});
            skLineSegment(sketch, "E15.11.7.5", {"start": v(-11.8, -86.36) * mm, "end": v(-13.38, -89.1) * mm});
            skLineSegment(sketch, "E15.14.7.5", {"start": v(-13.38, -89.1) * mm, "end": v(-16.53, -89.1) * mm});
            skLineSegment(sketch, "E15.17.7.5", {"start": v(-16.53, -89.1) * mm, "end": v(-18.11, -86.36) * mm});
            skCircle(sketch, "E15.0.7.6", {"center": v(-14.96, -77.72) * mm, "radius": 2.73 * mm, "construction": true});
            skLineSegment(sketch, "E15.2.7.6", {"start": v(-18.11, -77.72) * mm, "end": v(-16.53, -75) * mm});
            skLineSegment(sketch, "E15.5.7.6", {"start": v(-16.53, -75) * mm, "end": v(-13.38, -75) * mm});
            skLineSegment(sketch, "E15.8.7.6", {"start": v(-13.38, -75) * mm, "end": v(-11.8, -77.72) * mm});
            skLineSegment(sketch, "E15.11.7.6", {"start": v(-11.8, -77.72) * mm, "end": v(-13.38, -80.45) * mm});
            skLineSegment(sketch, "E15.14.7.6", {"start": v(-13.38, -80.45) * mm, "end": v(-16.53, -80.45) * mm});
            skLineSegment(sketch, "E15.17.7.6", {"start": v(-16.53, -80.45) * mm, "end": v(-18.11, -77.72) * mm});
            skCircle(sketch, "E15.0.7.7", {"center": v(-14.96, -69.09) * mm, "radius": 2.73 * mm, "construction": true});
            skLineSegment(sketch, "E15.2.7.7", {"start": v(-18.11, -69.09) * mm, "end": v(-16.53, -66.36) * mm});
            skLineSegment(sketch, "E15.5.7.7", {"start": v(-16.53, -66.36) * mm, "end": v(-13.38, -66.36) * mm});
            skLineSegment(sketch, "E15.8.7.7", {"start": v(-13.38, -66.36) * mm, "end": v(-11.8, -69.09) * mm});
            skLineSegment(sketch, "E15.11.7.7", {"start": v(-11.8, -69.09) * mm, "end": v(-13.38, -71.82) * mm});
            skLineSegment(sketch, "E15.14.7.7", {"start": v(-13.38, -71.82) * mm, "end": v(-16.53, -71.82) * mm});
            skLineSegment(sketch, "E15.17.7.7", {"start": v(-16.53, -71.82) * mm, "end": v(-18.11, -69.09) * mm});
            skCircle(sketch, "E15.0.7.8", {"center": v(-14.96, -60.45) * mm, "radius": 2.73 * mm, "construction": true});
            skLineSegment(sketch, "E15.2.7.8", {"start": v(-18.11, -60.45) * mm, "end": v(-16.53, -57.72) * mm});
            skLineSegment(sketch, "E15.5.7.8", {"start": v(-16.53, -57.72) * mm, "end": v(-13.38, -57.72) * mm});
            skLineSegment(sketch, "E15.8.7.8", {"start": v(-13.38, -57.72) * mm, "end": v(-11.8, -60.45) * mm});
            skLineSegment(sketch, "E15.11.7.8", {"start": v(-11.8, -60.45) * mm, "end": v(-13.38, -63.18) * mm});
            skLineSegment(sketch, "E15.14.7.8", {"start": v(-13.38, -63.18) * mm, "end": v(-16.53, -63.18) * mm});
            skLineSegment(sketch, "E15.17.7.8", {"start": v(-16.53, -63.18) * mm, "end": v(-18.11, -60.45) * mm});
            skCircle(sketch, "E15.0.7.9", {"center": v(-14.96, -51.82) * mm, "radius": 2.73 * mm, "construction": true});
            skLineSegment(sketch, "E15.2.7.9", {"start": v(-18.11, -51.82) * mm, "end": v(-16.53, -49.09) * mm});
            skLineSegment(sketch, "E15.5.7.9", {"start": v(-16.53, -49.09) * mm, "end": v(-13.38, -49.09) * mm});
            skLineSegment(sketch, "E15.8.7.9", {"start": v(-13.38, -49.09) * mm, "end": v(-11.8, -51.82) * mm});
            skLineSegment(sketch, "E15.11.7.9", {"start": v(-11.8, -51.82) * mm, "end": v(-13.38, -54.55) * mm});
            skLineSegment(sketch, "E15.14.7.9", {"start": v(-13.38, -54.55) * mm, "end": v(-16.53, -54.55) * mm});
            skLineSegment(sketch, "E15.17.7.9", {"start": v(-16.53, -54.55) * mm, "end": v(-18.11, -51.82) * mm});
            skCircle(sketch, "E15.0.7.10", {"center": v(-14.96, -43.18) * mm, "radius": 2.73 * mm, "construction": true});
            skLineSegment(sketch, "E15.2.7.10", {"start": v(-18.11, -43.18) * mm, "end": v(-16.53, -40.45) * mm});
            skLineSegment(sketch, "E15.5.7.10", {"start": v(-16.53, -40.45) * mm, "end": v(-13.38, -40.45) * mm});
            skLineSegment(sketch, "E15.8.7.10", {"start": v(-13.38, -40.45) * mm, "end": v(-11.8, -43.18) * mm});
            skLineSegment(sketch, "E15.11.7.10", {"start": v(-11.8, -43.18) * mm, "end": v(-13.38, -45.91) * mm});
            skLineSegment(sketch, "E15.14.7.10", {"start": v(-13.38, -45.91) * mm, "end": v(-16.53, -45.91) * mm});
            skLineSegment(sketch, "E15.17.7.10", {"start": v(-16.53, -45.91) * mm, "end": v(-18.11, -43.18) * mm});
            skCircle(sketch, "E15.0.7.11", {"center": v(-14.96, -34.54) * mm, "radius": 2.73 * mm, "construction": true});
            skLineSegment(sketch, "E15.2.7.11", {"start": v(-18.11, -34.54) * mm, "end": v(-16.53, -31.81) * mm});
            skLineSegment(sketch, "E15.5.7.11", {"start": v(-16.53, -31.81) * mm, "end": v(-13.38, -31.81) * mm});
            skLineSegment(sketch, "E15.8.7.11", {"start": v(-13.38, -31.81) * mm, "end": v(-11.8, -34.54) * mm});
            skLineSegment(sketch, "E15.11.7.11", {"start": v(-11.8, -34.54) * mm, "end": v(-13.38, -37.27) * mm});
            skLineSegment(sketch, "E15.14.7.11", {"start": v(-13.38, -37.27) * mm, "end": v(-16.53, -37.27) * mm});
            skLineSegment(sketch, "E15.17.7.11", {"start": v(-16.53, -37.27) * mm, "end": v(-18.11, -34.54) * mm});
            skCircle(sketch, "E15.0.7.12", {"center": v(-14.96, -25.9) * mm, "radius": 2.73 * mm, "construction": true});
            skLineSegment(sketch, "E15.2.7.12", {"start": v(-18.11, -25.9) * mm, "end": v(-16.53, -23.18) * mm});
            skLineSegment(sketch, "E15.5.7.12", {"start": v(-16.53, -23.18) * mm, "end": v(-13.38, -23.18) * mm});
            skLineSegment(sketch, "E15.8.7.12", {"start": v(-13.38, -23.18) * mm, "end": v(-11.8, -25.9) * mm});
            skLineSegment(sketch, "E15.11.7.12", {"start": v(-11.8, -25.9) * mm, "end": v(-13.38, -28.64) * mm});
            skLineSegment(sketch, "E15.14.7.12", {"start": v(-13.38, -28.64) * mm, "end": v(-16.53, -28.64) * mm});
            skLineSegment(sketch, "E15.17.7.12", {"start": v(-16.53, -28.64) * mm, "end": v(-18.11, -25.9) * mm});
            skCircle(sketch, "E15.0.7.13", {"center": v(-14.96, -17.27) * mm, "radius": 2.73 * mm, "construction": true});
            skLineSegment(sketch, "E15.2.7.13", {"start": v(-18.11, -17.27) * mm, "end": v(-16.53, -14.54) * mm});
            skLineSegment(sketch, "E15.5.7.13", {"start": v(-16.53, -14.54) * mm, "end": v(-13.38, -14.54) * mm});
            skLineSegment(sketch, "E15.8.7.13", {"start": v(-13.38, -14.54) * mm, "end": v(-11.8, -17.27) * mm});
            skLineSegment(sketch, "E15.11.7.13", {"start": v(-11.8, -17.27) * mm, "end": v(-13.38, -20) * mm});
            skLineSegment(sketch, "E15.14.7.13", {"start": v(-13.38, -20) * mm, "end": v(-16.53, -20) * mm});
            skLineSegment(sketch, "E15.17.7.13", {"start": v(-16.53, -20) * mm, "end": v(-18.11, -17.27) * mm});
            skCircle(sketch, "E15.0.7.14", {"center": v(-14.96, -8.64) * mm, "radius": 2.73 * mm, "construction": true});
            skLineSegment(sketch, "E15.2.7.14", {"start": v(-18.11, -8.64) * mm, "end": v(-16.53, -5.9) * mm});
            skLineSegment(sketch, "E15.5.7.14", {"start": v(-16.53, -5.9) * mm, "end": v(-13.38, -5.9) * mm});
            skLineSegment(sketch, "E15.8.7.14", {"start": v(-13.38, -5.9) * mm, "end": v(-11.8, -8.64) * mm});
            skLineSegment(sketch, "E15.11.7.14", {"start": v(-11.8, -8.64) * mm, "end": v(-13.38, -11.37) * mm});
            skLineSegment(sketch, "E15.14.7.14", {"start": v(-13.38, -11.37) * mm, "end": v(-16.53, -11.37) * mm});
            skLineSegment(sketch, "E15.17.7.14", {"start": v(-16.53, -11.37) * mm, "end": v(-18.11, -8.64) * mm});
            skCircle(sketch, "E15.0.7.15", {"center": v(-14.96, 0) * mm, "radius": 2.73 * mm, "construction": true});
            skLineSegment(sketch, "E15.2.7.15", {"start": v(-18.11, 0) * mm, "end": v(-16.53, 2.73) * mm});
            skLineSegment(sketch, "E15.5.7.15", {"start": v(-16.53, 2.73) * mm, "end": v(-13.38, 2.73) * mm});
            skLineSegment(sketch, "E15.8.7.15", {"start": v(-13.38, 2.73) * mm, "end": v(-11.8, 0) * mm});
            skLineSegment(sketch, "E15.11.7.15", {"start": v(-11.8, 0) * mm, "end": v(-13.38, -2.73) * mm});
            skLineSegment(sketch, "E15.14.7.15", {"start": v(-13.38, -2.73) * mm, "end": v(-16.53, -2.73) * mm});
            skLineSegment(sketch, "E15.17.7.15", {"start": v(-16.53, -2.73) * mm, "end": v(-18.11, 0) * mm});
            skCircle(sketch, "E15.0.7.16", {"center": v(-14.96, 8.64) * mm, "radius": 2.73 * mm, "construction": true});
            skLineSegment(sketch, "E15.2.7.16", {"start": v(-18.11, 8.64) * mm, "end": v(-16.53, 11.37) * mm});
            skLineSegment(sketch, "E15.5.7.16", {"start": v(-16.53, 11.37) * mm, "end": v(-13.38, 11.37) * mm});
            skLineSegment(sketch, "E15.8.7.16", {"start": v(-13.38, 11.37) * mm, "end": v(-11.8, 8.64) * mm});
            skLineSegment(sketch, "E15.11.7.16", {"start": v(-11.8, 8.64) * mm, "end": v(-13.38, 5.9) * mm});
            skLineSegment(sketch, "E15.14.7.16", {"start": v(-13.38, 5.9) * mm, "end": v(-16.53, 5.9) * mm});
            skLineSegment(sketch, "E15.17.7.16", {"start": v(-16.53, 5.9) * mm, "end": v(-18.11, 8.64) * mm});
            skCircle(sketch, "E15.0.7.17", {"center": v(-14.96, 17.27) * mm, "radius": 2.73 * mm, "construction": true});
            skLineSegment(sketch, "E15.2.7.17", {"start": v(-18.11, 17.27) * mm, "end": v(-16.53, 20) * mm});
            skLineSegment(sketch, "E15.5.7.17", {"start": v(-16.53, 20) * mm, "end": v(-13.38, 20) * mm});
            skLineSegment(sketch, "E15.8.7.17", {"start": v(-13.38, 20) * mm, "end": v(-11.8, 17.27) * mm});
            skLineSegment(sketch, "E15.11.7.17", {"start": v(-11.8, 17.27) * mm, "end": v(-13.38, 14.54) * mm});
            skLineSegment(sketch, "E15.14.7.17", {"start": v(-13.38, 14.54) * mm, "end": v(-16.53, 14.54) * mm});
            skLineSegment(sketch, "E15.17.7.17", {"start": v(-16.53, 14.54) * mm, "end": v(-18.11, 17.27) * mm});
            skCircle(sketch, "E15.0.7.18", {"center": v(-14.96, 25.9) * mm, "radius": 2.73 * mm, "construction": true});
            skLineSegment(sketch, "E15.2.7.18", {"start": v(-18.11, 25.9) * mm, "end": v(-16.53, 28.64) * mm});
            skLineSegment(sketch, "E15.5.7.18", {"start": v(-16.53, 28.64) * mm, "end": v(-13.38, 28.64) * mm});
            skLineSegment(sketch, "E15.8.7.18", {"start": v(-13.38, 28.64) * mm, "end": v(-11.8, 25.9) * mm});
            skLineSegment(sketch, "E15.11.7.18", {"start": v(-11.8, 25.9) * mm, "end": v(-13.38, 23.18) * mm});
            skLineSegment(sketch, "E15.14.7.18", {"start": v(-13.38, 23.18) * mm, "end": v(-16.53, 23.18) * mm});
            skLineSegment(sketch, "E15.17.7.18", {"start": v(-16.53, 23.18) * mm, "end": v(-18.11, 25.9) * mm});
            skCircle(sketch, "E15.0.7.19", {"center": v(-14.96, 34.54) * mm, "radius": 2.73 * mm, "construction": true});
            skLineSegment(sketch, "E15.2.7.19", {"start": v(-18.11, 34.54) * mm, "end": v(-16.53, 37.27) * mm});
            skLineSegment(sketch, "E15.5.7.19", {"start": v(-16.53, 37.27) * mm, "end": v(-13.38, 37.27) * mm});
            skLineSegment(sketch, "E15.8.7.19", {"start": v(-13.38, 37.27) * mm, "end": v(-11.8, 34.54) * mm});
            skLineSegment(sketch, "E15.11.7.19", {"start": v(-11.8, 34.54) * mm, "end": v(-13.38, 31.81) * mm});
            skLineSegment(sketch, "E15.14.7.19", {"start": v(-13.38, 31.81) * mm, "end": v(-16.53, 31.81) * mm});
            skLineSegment(sketch, "E15.17.7.19", {"start": v(-16.53, 31.81) * mm, "end": v(-18.11, 34.54) * mm});
            skCircle(sketch, "E15.0.8.0", {"center": v(0, -129.54) * mm, "radius": 2.73 * mm, "construction": true});
            skLineSegment(sketch, "E15.2.8.0", {"start": v(-3.15, -129.54) * mm, "end": v(-1.58, -126.8) * mm});
            skLineSegment(sketch, "E15.5.8.0", {"start": v(-1.58, -126.8) * mm, "end": v(1.58, -126.8) * mm});
            skLineSegment(sketch, "E15.8.8.0", {"start": v(1.58, -126.8) * mm, "end": v(3.15, -129.54) * mm});
            skLineSegment(sketch, "E15.11.8.0", {"start": v(3.15, -129.54) * mm, "end": v(1.58, -132.27) * mm});
            skLineSegment(sketch, "E15.14.8.0", {"start": v(1.58, -132.27) * mm, "end": v(-1.58, -132.27) * mm});
            skLineSegment(sketch, "E15.17.8.0", {"start": v(-1.58, -132.27) * mm, "end": v(-3.15, -129.54) * mm});
            skCircle(sketch, "E15.0.8.1", {"center": v(0, -120.9) * mm, "radius": 2.73 * mm, "construction": true});
            skLineSegment(sketch, "E15.2.8.1", {"start": v(-3.15, -120.9) * mm, "end": v(-1.58, -118.17) * mm});
            skLineSegment(sketch, "E15.5.8.1", {"start": v(-1.58, -118.17) * mm, "end": v(1.58, -118.17) * mm});
            skLineSegment(sketch, "E15.8.8.1", {"start": v(1.58, -118.17) * mm, "end": v(3.15, -120.9) * mm});
            skLineSegment(sketch, "E15.11.8.1", {"start": v(3.15, -120.9) * mm, "end": v(1.58, -123.63) * mm});
            skLineSegment(sketch, "E15.14.8.1", {"start": v(1.58, -123.63) * mm, "end": v(-1.58, -123.63) * mm});
            skLineSegment(sketch, "E15.17.8.1", {"start": v(-1.58, -123.63) * mm, "end": v(-3.15, -120.9) * mm});
            skCircle(sketch, "E15.0.8.2", {"center": v(0, -112.27) * mm, "radius": 2.73 * mm, "construction": true});
            skLineSegment(sketch, "E15.2.8.2", {"start": v(-3.15, -112.27) * mm, "end": v(-1.58, -109.54) * mm});
            skLineSegment(sketch, "E15.5.8.2", {"start": v(-1.58, -109.54) * mm, "end": v(1.58, -109.54) * mm});
            skLineSegment(sketch, "E15.8.8.2", {"start": v(1.58, -109.54) * mm, "end": v(3.15, -112.27) * mm});
            skLineSegment(sketch, "E15.11.8.2", {"start": v(3.15, -112.27) * mm, "end": v(1.58, -115) * mm});
            skLineSegment(sketch, "E15.14.8.2", {"start": v(1.58, -115) * mm, "end": v(-1.58, -115) * mm});
            skLineSegment(sketch, "E15.17.8.2", {"start": v(-1.58, -115) * mm, "end": v(-3.15, -112.27) * mm});
            skCircle(sketch, "E15.0.8.3", {"center": v(0, -103.63) * mm, "radius": 2.73 * mm, "construction": true});
            skLineSegment(sketch, "E15.2.8.3", {"start": v(-3.15, -103.63) * mm, "end": v(-1.58, -100.9) * mm});
            skLineSegment(sketch, "E15.5.8.3", {"start": v(-1.58, -100.9) * mm, "end": v(1.58, -100.9) * mm});
            skLineSegment(sketch, "E15.8.8.3", {"start": v(1.58, -100.9) * mm, "end": v(3.15, -103.63) * mm});
            skLineSegment(sketch, "E15.11.8.3", {"start": v(3.15, -103.63) * mm, "end": v(1.58, -106.36) * mm});
            skLineSegment(sketch, "E15.14.8.3", {"start": v(1.58, -106.36) * mm, "end": v(-1.58, -106.36) * mm});
            skLineSegment(sketch, "E15.17.8.3", {"start": v(-1.58, -106.36) * mm, "end": v(-3.15, -103.63) * mm});
            skCircle(sketch, "E15.0.8.4", {"center": v(0, -95) * mm, "radius": 2.73 * mm, "construction": true});
            skLineSegment(sketch, "E15.2.8.4", {"start": v(-3.15, -95) * mm, "end": v(-1.58, -92.27) * mm});
            skLineSegment(sketch, "E15.5.8.4", {"start": v(-1.58, -92.27) * mm, "end": v(1.58, -92.27) * mm});
            skLineSegment(sketch, "E15.8.8.4", {"start": v(1.58, -92.27) * mm, "end": v(3.15, -95) * mm});
            skLineSegment(sketch, "E15.11.8.4", {"start": v(3.15, -95) * mm, "end": v(1.58, -97.73) * mm});
            skLineSegment(sketch, "E15.14.8.4", {"start": v(1.58, -97.73) * mm, "end": v(-1.58, -97.73) * mm});
            skLineSegment(sketch, "E15.17.8.4", {"start": v(-1.58, -97.73) * mm, "end": v(-3.15, -95) * mm});
            skCircle(sketch, "E15.0.8.5", {"center": v(0, -86.36) * mm, "radius": 2.73 * mm, "construction": true});
            skLineSegment(sketch, "E15.2.8.5", {"start": v(-3.15, -86.36) * mm, "end": v(-1.58, -83.63) * mm});
            skLineSegment(sketch, "E15.5.8.5", {"start": v(-1.58, -83.63) * mm, "end": v(1.58, -83.63) * mm});
            skLineSegment(sketch, "E15.8.8.5", {"start": v(1.58, -83.63) * mm, "end": v(3.15, -86.36) * mm});
            skLineSegment(sketch, "E15.11.8.5", {"start": v(3.15, -86.36) * mm, "end": v(1.58, -89.1) * mm});
            skLineSegment(sketch, "E15.14.8.5", {"start": v(1.58, -89.1) * mm, "end": v(-1.58, -89.1) * mm});
            skLineSegment(sketch, "E15.17.8.5", {"start": v(-1.58, -89.1) * mm, "end": v(-3.15, -86.36) * mm});
            skCircle(sketch, "E15.0.8.6", {"center": v(0, -77.72) * mm, "radius": 2.73 * mm, "construction": true});
            skLineSegment(sketch, "E15.2.8.6", {"start": v(-3.15, -77.72) * mm, "end": v(-1.58, -75) * mm});
            skLineSegment(sketch, "E15.5.8.6", {"start": v(-1.58, -75) * mm, "end": v(1.58, -75) * mm});
            skLineSegment(sketch, "E15.8.8.6", {"start": v(1.58, -75) * mm, "end": v(3.15, -77.72) * mm});
            skLineSegment(sketch, "E15.11.8.6", {"start": v(3.15, -77.72) * mm, "end": v(1.58, -80.45) * mm});
            skLineSegment(sketch, "E15.14.8.6", {"start": v(1.58, -80.45) * mm, "end": v(-1.58, -80.45) * mm});
            skLineSegment(sketch, "E15.17.8.6", {"start": v(-1.58, -80.45) * mm, "end": v(-3.15, -77.72) * mm});
            skCircle(sketch, "E15.0.8.7", {"center": v(0, -69.09) * mm, "radius": 2.73 * mm, "construction": true});
            skLineSegment(sketch, "E15.2.8.7", {"start": v(-3.15, -69.09) * mm, "end": v(-1.58, -66.36) * mm});
            skLineSegment(sketch, "E15.5.8.7", {"start": v(-1.58, -66.36) * mm, "end": v(1.58, -66.36) * mm});
            skLineSegment(sketch, "E15.8.8.7", {"start": v(1.58, -66.36) * mm, "end": v(3.15, -69.09) * mm});
            skLineSegment(sketch, "E15.11.8.7", {"start": v(3.15, -69.09) * mm, "end": v(1.58, -71.82) * mm});
            skLineSegment(sketch, "E15.14.8.7", {"start": v(1.58, -71.82) * mm, "end": v(-1.58, -71.82) * mm});
            skLineSegment(sketch, "E15.17.8.7", {"start": v(-1.58, -71.82) * mm, "end": v(-3.15, -69.09) * mm});
            skCircle(sketch, "E15.0.8.8", {"center": v(0, -60.45) * mm, "radius": 2.73 * mm, "construction": true});
            skLineSegment(sketch, "E15.2.8.8", {"start": v(-3.15, -60.45) * mm, "end": v(-1.58, -57.72) * mm});
            skLineSegment(sketch, "E15.5.8.8", {"start": v(-1.58, -57.72) * mm, "end": v(1.58, -57.72) * mm});
            skLineSegment(sketch, "E15.8.8.8", {"start": v(1.58, -57.72) * mm, "end": v(3.15, -60.45) * mm});
            skLineSegment(sketch, "E15.11.8.8", {"start": v(3.15, -60.45) * mm, "end": v(1.58, -63.18) * mm});
            skLineSegment(sketch, "E15.14.8.8", {"start": v(1.58, -63.18) * mm, "end": v(-1.58, -63.18) * mm});
            skLineSegment(sketch, "E15.17.8.8", {"start": v(-1.58, -63.18) * mm, "end": v(-3.15, -60.45) * mm});
            skCircle(sketch, "E15.0.8.9", {"center": v(0, -51.82) * mm, "radius": 2.73 * mm, "construction": true});
            skLineSegment(sketch, "E15.2.8.9", {"start": v(-3.15, -51.82) * mm, "end": v(-1.58, -49.09) * mm});
            skLineSegment(sketch, "E15.5.8.9", {"start": v(-1.58, -49.09) * mm, "end": v(1.58, -49.09) * mm});
            skLineSegment(sketch, "E15.8.8.9", {"start": v(1.58, -49.09) * mm, "end": v(3.15, -51.82) * mm});
            skLineSegment(sketch, "E15.11.8.9", {"start": v(3.15, -51.82) * mm, "end": v(1.58, -54.55) * mm});
            skLineSegment(sketch, "E15.14.8.9", {"start": v(1.58, -54.55) * mm, "end": v(-1.58, -54.55) * mm});
            skLineSegment(sketch, "E15.17.8.9", {"start": v(-1.58, -54.55) * mm, "end": v(-3.15, -51.82) * mm});
            skCircle(sketch, "E15.0.8.10", {"center": v(0, -43.18) * mm, "radius": 2.73 * mm, "construction": true});
            skLineSegment(sketch, "E15.2.8.10", {"start": v(-3.15, -43.18) * mm, "end": v(-1.58, -40.45) * mm});
            skLineSegment(sketch, "E15.5.8.10", {"start": v(-1.58, -40.45) * mm, "end": v(1.58, -40.45) * mm});
            skLineSegment(sketch, "E15.8.8.10", {"start": v(1.58, -40.45) * mm, "end": v(3.15, -43.18) * mm});
            skLineSegment(sketch, "E15.11.8.10", {"start": v(3.15, -43.18) * mm, "end": v(1.58, -45.91) * mm});
            skLineSegment(sketch, "E15.14.8.10", {"start": v(1.58, -45.91) * mm, "end": v(-1.58, -45.91) * mm});
            skLineSegment(sketch, "E15.17.8.10", {"start": v(-1.58, -45.91) * mm, "end": v(-3.15, -43.18) * mm});
            skCircle(sketch, "E15.0.8.11", {"center": v(0, -34.54) * mm, "radius": 2.73 * mm, "construction": true});
            skLineSegment(sketch, "E15.2.8.11", {"start": v(-3.15, -34.54) * mm, "end": v(-1.58, -31.81) * mm});
            skLineSegment(sketch, "E15.5.8.11", {"start": v(-1.58, -31.81) * mm, "end": v(1.58, -31.81) * mm});
            skLineSegment(sketch, "E15.8.8.11", {"start": v(1.58, -31.81) * mm, "end": v(3.15, -34.54) * mm});
            skLineSegment(sketch, "E15.11.8.11", {"start": v(3.15, -34.54) * mm, "end": v(1.58, -37.27) * mm});
            skLineSegment(sketch, "E15.14.8.11", {"start": v(1.58, -37.27) * mm, "end": v(-1.58, -37.27) * mm});
            skLineSegment(sketch, "E15.17.8.11", {"start": v(-1.58, -37.27) * mm, "end": v(-3.15, -34.54) * mm});
            skCircle(sketch, "E15.0.8.12", {"center": v(0, -25.9) * mm, "radius": 2.73 * mm, "construction": true});
            skLineSegment(sketch, "E15.2.8.12", {"start": v(-3.15, -25.9) * mm, "end": v(-1.58, -23.18) * mm});
            skLineSegment(sketch, "E15.5.8.12", {"start": v(-1.58, -23.18) * mm, "end": v(1.58, -23.18) * mm});
            skLineSegment(sketch, "E15.8.8.12", {"start": v(1.58, -23.18) * mm, "end": v(3.15, -25.9) * mm});
            skLineSegment(sketch, "E15.11.8.12", {"start": v(3.15, -25.9) * mm, "end": v(1.58, -28.64) * mm});
            skLineSegment(sketch, "E15.14.8.12", {"start": v(1.58, -28.64) * mm, "end": v(-1.58, -28.64) * mm});
            skLineSegment(sketch, "E15.17.8.12", {"start": v(-1.58, -28.64) * mm, "end": v(-3.15, -25.9) * mm});
            skCircle(sketch, "E15.0.8.13", {"center": v(0, -17.27) * mm, "radius": 2.73 * mm, "construction": true});
            skLineSegment(sketch, "E15.2.8.13", {"start": v(-3.15, -17.27) * mm, "end": v(-1.58, -14.54) * mm});
            skLineSegment(sketch, "E15.5.8.13", {"start": v(-1.58, -14.54) * mm, "end": v(1.58, -14.54) * mm});
            skLineSegment(sketch, "E15.8.8.13", {"start": v(1.58, -14.54) * mm, "end": v(3.15, -17.27) * mm});
            skLineSegment(sketch, "E15.11.8.13", {"start": v(3.15, -17.27) * mm, "end": v(1.58, -20) * mm});
            skLineSegment(sketch, "E15.14.8.13", {"start": v(1.58, -20) * mm, "end": v(-1.58, -20) * mm});
            skLineSegment(sketch, "E15.17.8.13", {"start": v(-1.58, -20) * mm, "end": v(-3.15, -17.27) * mm});
            skCircle(sketch, "E15.0.8.14", {"center": v(0, -8.64) * mm, "radius": 2.73 * mm, "construction": true});
            skLineSegment(sketch, "E15.2.8.14", {"start": v(-3.15, -8.64) * mm, "end": v(-1.58, -5.9) * mm});
            skLineSegment(sketch, "E15.5.8.14", {"start": v(-1.58, -5.9) * mm, "end": v(1.58, -5.9) * mm});
            skLineSegment(sketch, "E15.8.8.14", {"start": v(1.58, -5.9) * mm, "end": v(3.15, -8.64) * mm});
            skLineSegment(sketch, "E15.11.8.14", {"start": v(3.15, -8.64) * mm, "end": v(1.58, -11.37) * mm});
            skLineSegment(sketch, "E15.14.8.14", {"start": v(1.58, -11.37) * mm, "end": v(-1.58, -11.37) * mm});
            skLineSegment(sketch, "E15.17.8.14", {"start": v(-1.58, -11.37) * mm, "end": v(-3.15, -8.64) * mm});
            skCircle(sketch, "E15.0.8.15", {"center": v(0, 0) * mm, "radius": 2.73 * mm, "construction": true});
            skLineSegment(sketch, "E15.2.8.15", {"start": v(-3.15, 0) * mm, "end": v(-1.58, 2.73) * mm});
            skLineSegment(sketch, "E15.5.8.15", {"start": v(-1.58, 2.73) * mm, "end": v(1.58, 2.73) * mm});
            skLineSegment(sketch, "E15.8.8.15", {"start": v(1.58, 2.73) * mm, "end": v(3.15, 0) * mm});
            skLineSegment(sketch, "E15.11.8.15", {"start": v(3.15, 0) * mm, "end": v(1.58, -2.73) * mm});
            skLineSegment(sketch, "E15.14.8.15", {"start": v(1.58, -2.73) * mm, "end": v(-1.58, -2.73) * mm});
            skLineSegment(sketch, "E15.17.8.15", {"start": v(-1.58, -2.73) * mm, "end": v(-3.15, 0) * mm});
            skCircle(sketch, "E15.0.8.16", {"center": v(0, 8.64) * mm, "radius": 2.73 * mm, "construction": true});
            skLineSegment(sketch, "E15.2.8.16", {"start": v(-3.15, 8.64) * mm, "end": v(-1.58, 11.37) * mm});
            skLineSegment(sketch, "E15.5.8.16", {"start": v(-1.58, 11.37) * mm, "end": v(1.58, 11.37) * mm});
            skLineSegment(sketch, "E15.8.8.16", {"start": v(1.58, 11.37) * mm, "end": v(3.15, 8.64) * mm});
            skLineSegment(sketch, "E15.11.8.16", {"start": v(3.15, 8.64) * mm, "end": v(1.58, 5.9) * mm});
            skLineSegment(sketch, "E15.14.8.16", {"start": v(1.58, 5.9) * mm, "end": v(-1.58, 5.9) * mm});
            skLineSegment(sketch, "E15.17.8.16", {"start": v(-1.58, 5.9) * mm, "end": v(-3.15, 8.64) * mm});
            skCircle(sketch, "E15.0.8.17", {"center": v(0, 17.27) * mm, "radius": 2.73 * mm, "construction": true});
            skLineSegment(sketch, "E15.2.8.17", {"start": v(-3.15, 17.27) * mm, "end": v(-1.58, 20) * mm});
            skLineSegment(sketch, "E15.5.8.17", {"start": v(-1.58, 20) * mm, "end": v(1.58, 20) * mm});
            skLineSegment(sketch, "E15.8.8.17", {"start": v(1.58, 20) * mm, "end": v(3.15, 17.27) * mm});
            skLineSegment(sketch, "E15.11.8.17", {"start": v(3.15, 17.27) * mm, "end": v(1.58, 14.54) * mm});
            skLineSegment(sketch, "E15.14.8.17", {"start": v(1.58, 14.54) * mm, "end": v(-1.58, 14.54) * mm});
            skLineSegment(sketch, "E15.17.8.17", {"start": v(-1.58, 14.54) * mm, "end": v(-3.15, 17.27) * mm});
            skCircle(sketch, "E15.0.8.18", {"center": v(0, 25.9) * mm, "radius": 2.73 * mm, "construction": true});
            skLineSegment(sketch, "E15.2.8.18", {"start": v(-3.15, 25.9) * mm, "end": v(-1.58, 28.64) * mm});
            skLineSegment(sketch, "E15.5.8.18", {"start": v(-1.58, 28.64) * mm, "end": v(1.58, 28.64) * mm});
            skLineSegment(sketch, "E15.8.8.18", {"start": v(1.58, 28.64) * mm, "end": v(3.15, 25.9) * mm});
            skLineSegment(sketch, "E15.11.8.18", {"start": v(3.15, 25.9) * mm, "end": v(1.58, 23.18) * mm});
            skLineSegment(sketch, "E15.14.8.18", {"start": v(1.58, 23.18) * mm, "end": v(-1.58, 23.18) * mm});
            skLineSegment(sketch, "E15.17.8.18", {"start": v(-1.58, 23.18) * mm, "end": v(-3.15, 25.9) * mm});
            skCircle(sketch, "E15.0.8.19", {"center": v(0, 34.54) * mm, "radius": 2.73 * mm, "construction": true});
            skLineSegment(sketch, "E15.2.8.19", {"start": v(-3.15, 34.54) * mm, "end": v(-1.58, 37.27) * mm});
            skLineSegment(sketch, "E15.5.8.19", {"start": v(-1.58, 37.27) * mm, "end": v(1.58, 37.27) * mm});
            skLineSegment(sketch, "E15.8.8.19", {"start": v(1.58, 37.27) * mm, "end": v(3.15, 34.54) * mm});
            skLineSegment(sketch, "E15.11.8.19", {"start": v(3.15, 34.54) * mm, "end": v(1.58, 31.81) * mm});
            skLineSegment(sketch, "E15.14.8.19", {"start": v(1.58, 31.81) * mm, "end": v(-1.58, 31.81) * mm});
            skLineSegment(sketch, "E15.17.8.19", {"start": v(-1.58, 31.81) * mm, "end": v(-3.15, 34.54) * mm});
            skCircle(sketch, "E15.0.9.0", {"center": v(14.96, -129.54) * mm, "radius": 2.73 * mm, "construction": true});
            skLineSegment(sketch, "E15.2.9.0", {"start": v(11.8, -129.54) * mm, "end": v(13.38, -126.8) * mm});
            skLineSegment(sketch, "E15.5.9.0", {"start": v(13.38, -126.8) * mm, "end": v(16.53, -126.8) * mm});
            skLineSegment(sketch, "E15.8.9.0", {"start": v(16.53, -126.8) * mm, "end": v(18.11, -129.54) * mm});
            skLineSegment(sketch, "E15.11.9.0", {"start": v(18.11, -129.54) * mm, "end": v(16.53, -132.27) * mm});
            skLineSegment(sketch, "E15.14.9.0", {"start": v(16.53, -132.27) * mm, "end": v(13.38, -132.27) * mm});
            skLineSegment(sketch, "E15.17.9.0", {"start": v(13.38, -132.27) * mm, "end": v(11.8, -129.54) * mm});
            skCircle(sketch, "E15.0.9.1", {"center": v(14.96, -120.9) * mm, "radius": 2.73 * mm, "construction": true});
            skLineSegment(sketch, "E15.2.9.1", {"start": v(11.8, -120.9) * mm, "end": v(13.38, -118.17) * mm});
            skLineSegment(sketch, "E15.5.9.1", {"start": v(13.38, -118.17) * mm, "end": v(16.53, -118.17) * mm});
            skLineSegment(sketch, "E15.8.9.1", {"start": v(16.53, -118.17) * mm, "end": v(18.11, -120.9) * mm});
            skLineSegment(sketch, "E15.11.9.1", {"start": v(18.11, -120.9) * mm, "end": v(16.53, -123.63) * mm});
            skLineSegment(sketch, "E15.14.9.1", {"start": v(16.53, -123.63) * mm, "end": v(13.38, -123.63) * mm});
            skLineSegment(sketch, "E15.17.9.1", {"start": v(13.38, -123.63) * mm, "end": v(11.8, -120.9) * mm});
            skCircle(sketch, "E15.0.9.2", {"center": v(14.96, -112.27) * mm, "radius": 2.73 * mm, "construction": true});
            skLineSegment(sketch, "E15.2.9.2", {"start": v(11.8, -112.27) * mm, "end": v(13.38, -109.54) * mm});
            skLineSegment(sketch, "E15.5.9.2", {"start": v(13.38, -109.54) * mm, "end": v(16.53, -109.54) * mm});
            skLineSegment(sketch, "E15.8.9.2", {"start": v(16.53, -109.54) * mm, "end": v(18.11, -112.27) * mm});
            skLineSegment(sketch, "E15.11.9.2", {"start": v(18.11, -112.27) * mm, "end": v(16.53, -115) * mm});
            skLineSegment(sketch, "E15.14.9.2", {"start": v(16.53, -115) * mm, "end": v(13.38, -115) * mm});
            skLineSegment(sketch, "E15.17.9.2", {"start": v(13.38, -115) * mm, "end": v(11.8, -112.27) * mm});
            skCircle(sketch, "E15.0.9.3", {"center": v(14.96, -103.63) * mm, "radius": 2.73 * mm, "construction": true});
            skLineSegment(sketch, "E15.2.9.3", {"start": v(11.8, -103.63) * mm, "end": v(13.38, -100.9) * mm});
            skLineSegment(sketch, "E15.5.9.3", {"start": v(13.38, -100.9) * mm, "end": v(16.53, -100.9) * mm});
            skLineSegment(sketch, "E15.8.9.3", {"start": v(16.53, -100.9) * mm, "end": v(18.11, -103.63) * mm});
            skLineSegment(sketch, "E15.11.9.3", {"start": v(18.11, -103.63) * mm, "end": v(16.53, -106.36) * mm});
            skLineSegment(sketch, "E15.14.9.3", {"start": v(16.53, -106.36) * mm, "end": v(13.38, -106.36) * mm});
            skLineSegment(sketch, "E15.17.9.3", {"start": v(13.38, -106.36) * mm, "end": v(11.8, -103.63) * mm});
            skCircle(sketch, "E15.0.9.4", {"center": v(14.96, -95) * mm, "radius": 2.73 * mm, "construction": true});
            skLineSegment(sketch, "E15.2.9.4", {"start": v(11.8, -95) * mm, "end": v(13.38, -92.27) * mm});
            skLineSegment(sketch, "E15.5.9.4", {"start": v(13.38, -92.27) * mm, "end": v(16.53, -92.27) * mm});
            skLineSegment(sketch, "E15.8.9.4", {"start": v(16.53, -92.27) * mm, "end": v(18.11, -95) * mm});
            skLineSegment(sketch, "E15.11.9.4", {"start": v(18.11, -95) * mm, "end": v(16.53, -97.73) * mm});
            skLineSegment(sketch, "E15.14.9.4", {"start": v(16.53, -97.73) * mm, "end": v(13.38, -97.73) * mm});
            skLineSegment(sketch, "E15.17.9.4", {"start": v(13.38, -97.73) * mm, "end": v(11.8, -95) * mm});
            skCircle(sketch, "E15.0.9.5", {"center": v(14.96, -86.36) * mm, "radius": 2.73 * mm, "construction": true});
            skLineSegment(sketch, "E15.2.9.5", {"start": v(11.8, -86.36) * mm, "end": v(13.38, -83.63) * mm});
            skLineSegment(sketch, "E15.5.9.5", {"start": v(13.38, -83.63) * mm, "end": v(16.53, -83.63) * mm});
            skLineSegment(sketch, "E15.8.9.5", {"start": v(16.53, -83.63) * mm, "end": v(18.11, -86.36) * mm});
            skLineSegment(sketch, "E15.11.9.5", {"start": v(18.11, -86.36) * mm, "end": v(16.53, -89.1) * mm});
            skLineSegment(sketch, "E15.14.9.5", {"start": v(16.53, -89.1) * mm, "end": v(13.38, -89.1) * mm});
            skLineSegment(sketch, "E15.17.9.5", {"start": v(13.38, -89.1) * mm, "end": v(11.8, -86.36) * mm});
            skCircle(sketch, "E15.0.9.6", {"center": v(14.96, -77.72) * mm, "radius": 2.73 * mm, "construction": true});
            skLineSegment(sketch, "E15.2.9.6", {"start": v(11.8, -77.72) * mm, "end": v(13.38, -75) * mm});
            skLineSegment(sketch, "E15.5.9.6", {"start": v(13.38, -75) * mm, "end": v(16.53, -75) * mm});
            skLineSegment(sketch, "E15.8.9.6", {"start": v(16.53, -75) * mm, "end": v(18.11, -77.72) * mm});
            skLineSegment(sketch, "E15.11.9.6", {"start": v(18.11, -77.72) * mm, "end": v(16.53, -80.45) * mm});
            skLineSegment(sketch, "E15.14.9.6", {"start": v(16.53, -80.45) * mm, "end": v(13.38, -80.45) * mm});
            skLineSegment(sketch, "E15.17.9.6", {"start": v(13.38, -80.45) * mm, "end": v(11.8, -77.72) * mm});
            skCircle(sketch, "E15.0.9.7", {"center": v(14.96, -69.09) * mm, "radius": 2.73 * mm, "construction": true});
            skLineSegment(sketch, "E15.2.9.7", {"start": v(11.8, -69.09) * mm, "end": v(13.38, -66.36) * mm});
            skLineSegment(sketch, "E15.5.9.7", {"start": v(13.38, -66.36) * mm, "end": v(16.53, -66.36) * mm});
            skLineSegment(sketch, "E15.8.9.7", {"start": v(16.53, -66.36) * mm, "end": v(18.11, -69.09) * mm});
            skLineSegment(sketch, "E15.11.9.7", {"start": v(18.11, -69.09) * mm, "end": v(16.53, -71.82) * mm});
            skLineSegment(sketch, "E15.14.9.7", {"start": v(16.53, -71.82) * mm, "end": v(13.38, -71.82) * mm});
            skLineSegment(sketch, "E15.17.9.7", {"start": v(13.38, -71.82) * mm, "end": v(11.8, -69.09) * mm});
            skCircle(sketch, "E15.0.9.8", {"center": v(14.96, -60.45) * mm, "radius": 2.73 * mm, "construction": true});
            skLineSegment(sketch, "E15.2.9.8", {"start": v(11.8, -60.45) * mm, "end": v(13.38, -57.72) * mm});
            skLineSegment(sketch, "E15.5.9.8", {"start": v(13.38, -57.72) * mm, "end": v(16.53, -57.72) * mm});
            skLineSegment(sketch, "E15.8.9.8", {"start": v(16.53, -57.72) * mm, "end": v(18.11, -60.45) * mm});
            skLineSegment(sketch, "E15.11.9.8", {"start": v(18.11, -60.45) * mm, "end": v(16.53, -63.18) * mm});
            skLineSegment(sketch, "E15.14.9.8", {"start": v(16.53, -63.18) * mm, "end": v(13.38, -63.18) * mm});
            skLineSegment(sketch, "E15.17.9.8", {"start": v(13.38, -63.18) * mm, "end": v(11.8, -60.45) * mm});
            skCircle(sketch, "E15.0.9.9", {"center": v(14.96, -51.82) * mm, "radius": 2.73 * mm, "construction": true});
            skLineSegment(sketch, "E15.2.9.9", {"start": v(11.8, -51.82) * mm, "end": v(13.38, -49.09) * mm});
            skLineSegment(sketch, "E15.5.9.9", {"start": v(13.38, -49.09) * mm, "end": v(16.53, -49.09) * mm});
            skLineSegment(sketch, "E15.8.9.9", {"start": v(16.53, -49.09) * mm, "end": v(18.11, -51.82) * mm});
            skLineSegment(sketch, "E15.11.9.9", {"start": v(18.11, -51.82) * mm, "end": v(16.53, -54.55) * mm});
            skLineSegment(sketch, "E15.14.9.9", {"start": v(16.53, -54.55) * mm, "end": v(13.38, -54.55) * mm});
            skLineSegment(sketch, "E15.17.9.9", {"start": v(13.38, -54.55) * mm, "end": v(11.8, -51.82) * mm});
            skCircle(sketch, "E15.0.9.10", {"center": v(14.96, -43.18) * mm, "radius": 2.73 * mm, "construction": true});
            skLineSegment(sketch, "E15.2.9.10", {"start": v(11.8, -43.18) * mm, "end": v(13.38, -40.45) * mm});
            skLineSegment(sketch, "E15.5.9.10", {"start": v(13.38, -40.45) * mm, "end": v(16.53, -40.45) * mm});
            skLineSegment(sketch, "E15.8.9.10", {"start": v(16.53, -40.45) * mm, "end": v(18.11, -43.18) * mm});
            skLineSegment(sketch, "E15.11.9.10", {"start": v(18.11, -43.18) * mm, "end": v(16.53, -45.91) * mm});
            skLineSegment(sketch, "E15.14.9.10", {"start": v(16.53, -45.91) * mm, "end": v(13.38, -45.91) * mm});
            skLineSegment(sketch, "E15.17.9.10", {"start": v(13.38, -45.91) * mm, "end": v(11.8, -43.18) * mm});
            skCircle(sketch, "E15.0.9.11", {"center": v(14.96, -34.54) * mm, "radius": 2.73 * mm, "construction": true});
            skLineSegment(sketch, "E15.2.9.11", {"start": v(11.8, -34.54) * mm, "end": v(13.38, -31.81) * mm});
            skLineSegment(sketch, "E15.5.9.11", {"start": v(13.38, -31.81) * mm, "end": v(16.53, -31.81) * mm});
            skLineSegment(sketch, "E15.8.9.11", {"start": v(16.53, -31.81) * mm, "end": v(18.11, -34.54) * mm});
            skLineSegment(sketch, "E15.11.9.11", {"start": v(18.11, -34.54) * mm, "end": v(16.53, -37.27) * mm});
            skLineSegment(sketch, "E15.14.9.11", {"start": v(16.53, -37.27) * mm, "end": v(13.38, -37.27) * mm});
            skLineSegment(sketch, "E15.17.9.11", {"start": v(13.38, -37.27) * mm, "end": v(11.8, -34.54) * mm});
            skCircle(sketch, "E15.0.9.12", {"center": v(14.96, -25.9) * mm, "radius": 2.73 * mm, "construction": true});
            skLineSegment(sketch, "E15.2.9.12", {"start": v(11.8, -25.9) * mm, "end": v(13.38, -23.18) * mm});
            skLineSegment(sketch, "E15.5.9.12", {"start": v(13.38, -23.18) * mm, "end": v(16.53, -23.18) * mm});
            skLineSegment(sketch, "E15.8.9.12", {"start": v(16.53, -23.18) * mm, "end": v(18.11, -25.9) * mm});
            skLineSegment(sketch, "E15.11.9.12", {"start": v(18.11, -25.9) * mm, "end": v(16.53, -28.64) * mm});
            skLineSegment(sketch, "E15.14.9.12", {"start": v(16.53, -28.64) * mm, "end": v(13.38, -28.64) * mm});
            skLineSegment(sketch, "E15.17.9.12", {"start": v(13.38, -28.64) * mm, "end": v(11.8, -25.9) * mm});
            skCircle(sketch, "E15.0.9.13", {"center": v(14.96, -17.27) * mm, "radius": 2.73 * mm, "construction": true});
            skLineSegment(sketch, "E15.2.9.13", {"start": v(11.8, -17.27) * mm, "end": v(13.38, -14.54) * mm});
            skLineSegment(sketch, "E15.5.9.13", {"start": v(13.38, -14.54) * mm, "end": v(16.53, -14.54) * mm});
            skLineSegment(sketch, "E15.8.9.13", {"start": v(16.53, -14.54) * mm, "end": v(18.11, -17.27) * mm});
            skLineSegment(sketch, "E15.11.9.13", {"start": v(18.11, -17.27) * mm, "end": v(16.53, -20) * mm});
            skLineSegment(sketch, "E15.14.9.13", {"start": v(16.53, -20) * mm, "end": v(13.38, -20) * mm});
            skLineSegment(sketch, "E15.17.9.13", {"start": v(13.38, -20) * mm, "end": v(11.8, -17.27) * mm});
            skCircle(sketch, "E15.0.9.14", {"center": v(14.96, -8.64) * mm, "radius": 2.73 * mm, "construction": true});
            skLineSegment(sketch, "E15.2.9.14", {"start": v(11.8, -8.64) * mm, "end": v(13.38, -5.9) * mm});
            skLineSegment(sketch, "E15.5.9.14", {"start": v(13.38, -5.9) * mm, "end": v(16.53, -5.9) * mm});
            skLineSegment(sketch, "E15.8.9.14", {"start": v(16.53, -5.9) * mm, "end": v(18.11, -8.64) * mm});
            skLineSegment(sketch, "E15.11.9.14", {"start": v(18.11, -8.64) * mm, "end": v(16.53, -11.37) * mm});
            skLineSegment(sketch, "E15.14.9.14", {"start": v(16.53, -11.37) * mm, "end": v(13.38, -11.37) * mm});
            skLineSegment(sketch, "E15.17.9.14", {"start": v(13.38, -11.37) * mm, "end": v(11.8, -8.64) * mm});
            skCircle(sketch, "E15.0.9.15", {"center": v(14.96, 0) * mm, "radius": 2.73 * mm, "construction": true});
            skLineSegment(sketch, "E15.2.9.15", {"start": v(11.8, 0) * mm, "end": v(13.38, 2.73) * mm});
            skLineSegment(sketch, "E15.5.9.15", {"start": v(13.38, 2.73) * mm, "end": v(16.53, 2.73) * mm});
            skLineSegment(sketch, "E15.8.9.15", {"start": v(16.53, 2.73) * mm, "end": v(18.11, 0) * mm});
            skLineSegment(sketch, "E15.11.9.15", {"start": v(18.11, 0) * mm, "end": v(16.53, -2.73) * mm});
            skLineSegment(sketch, "E15.14.9.15", {"start": v(16.53, -2.73) * mm, "end": v(13.38, -2.73) * mm});
            skLineSegment(sketch, "E15.17.9.15", {"start": v(13.38, -2.73) * mm, "end": v(11.8, 0) * mm});
            skCircle(sketch, "E15.0.9.16", {"center": v(14.96, 8.64) * mm, "radius": 2.73 * mm, "construction": true});
            skLineSegment(sketch, "E15.2.9.16", {"start": v(11.8, 8.64) * mm, "end": v(13.38, 11.37) * mm});
            skLineSegment(sketch, "E15.5.9.16", {"start": v(13.38, 11.37) * mm, "end": v(16.53, 11.37) * mm});
            skLineSegment(sketch, "E15.8.9.16", {"start": v(16.53, 11.37) * mm, "end": v(18.11, 8.64) * mm});
            skLineSegment(sketch, "E15.11.9.16", {"start": v(18.11, 8.64) * mm, "end": v(16.53, 5.9) * mm});
            skLineSegment(sketch, "E15.14.9.16", {"start": v(16.53, 5.9) * mm, "end": v(13.38, 5.9) * mm});
            skLineSegment(sketch, "E15.17.9.16", {"start": v(13.38, 5.9) * mm, "end": v(11.8, 8.64) * mm});
            skCircle(sketch, "E15.0.9.17", {"center": v(14.96, 17.27) * mm, "radius": 2.73 * mm, "construction": true});
            skLineSegment(sketch, "E15.2.9.17", {"start": v(11.8, 17.27) * mm, "end": v(13.38, 20) * mm});
            skLineSegment(sketch, "E15.5.9.17", {"start": v(13.38, 20) * mm, "end": v(16.53, 20) * mm});
            skLineSegment(sketch, "E15.8.9.17", {"start": v(16.53, 20) * mm, "end": v(18.11, 17.27) * mm});
            skLineSegment(sketch, "E15.11.9.17", {"start": v(18.11, 17.27) * mm, "end": v(16.53, 14.54) * mm});
            skLineSegment(sketch, "E15.14.9.17", {"start": v(16.53, 14.54) * mm, "end": v(13.38, 14.54) * mm});
            skLineSegment(sketch, "E15.17.9.17", {"start": v(13.38, 14.54) * mm, "end": v(11.8, 17.27) * mm});
            skCircle(sketch, "E15.0.9.18", {"center": v(14.96, 25.9) * mm, "radius": 2.73 * mm, "construction": true});
            skLineSegment(sketch, "E15.2.9.18", {"start": v(11.8, 25.9) * mm, "end": v(13.38, 28.64) * mm});
            skLineSegment(sketch, "E15.5.9.18", {"start": v(13.38, 28.64) * mm, "end": v(16.53, 28.64) * mm});
            skLineSegment(sketch, "E15.8.9.18", {"start": v(16.53, 28.64) * mm, "end": v(18.11, 25.9) * mm});
            skLineSegment(sketch, "E15.11.9.18", {"start": v(18.11, 25.9) * mm, "end": v(16.53, 23.18) * mm});
            skLineSegment(sketch, "E15.14.9.18", {"start": v(16.53, 23.18) * mm, "end": v(13.38, 23.18) * mm});
            skLineSegment(sketch, "E15.17.9.18", {"start": v(13.38, 23.18) * mm, "end": v(11.8, 25.9) * mm});
            skCircle(sketch, "E15.0.9.19", {"center": v(14.96, 34.54) * mm, "radius": 2.73 * mm, "construction": true});
            skLineSegment(sketch, "E15.2.9.19", {"start": v(11.8, 34.54) * mm, "end": v(13.38, 37.27) * mm});
            skLineSegment(sketch, "E15.5.9.19", {"start": v(13.38, 37.27) * mm, "end": v(16.53, 37.27) * mm});
            skLineSegment(sketch, "E15.8.9.19", {"start": v(16.53, 37.27) * mm, "end": v(18.11, 34.54) * mm});
            skLineSegment(sketch, "E15.11.9.19", {"start": v(18.11, 34.54) * mm, "end": v(16.53, 31.81) * mm});
            skLineSegment(sketch, "E15.14.9.19", {"start": v(16.53, 31.81) * mm, "end": v(13.38, 31.81) * mm});
            skLineSegment(sketch, "E15.17.9.19", {"start": v(13.38, 31.81) * mm, "end": v(11.8, 34.54) * mm});
            skCircle(sketch, "E15.0.10.0", {"center": v(29.92, -129.54) * mm, "radius": 2.73 * mm, "construction": true});
            skLineSegment(sketch, "E15.2.10.0", {"start": v(26.76, -129.54) * mm, "end": v(28.34, -126.8) * mm});
            skLineSegment(sketch, "E15.5.10.0", {"start": v(28.34, -126.8) * mm, "end": v(31.5, -126.8) * mm});
            skLineSegment(sketch, "E15.8.10.0", {"start": v(31.5, -126.8) * mm, "end": v(33.07, -129.54) * mm});
            skLineSegment(sketch, "E15.11.10.0", {"start": v(33.07, -129.54) * mm, "end": v(31.5, -132.27) * mm});
            skLineSegment(sketch, "E15.14.10.0", {"start": v(31.5, -132.27) * mm, "end": v(28.34, -132.27) * mm});
            skLineSegment(sketch, "E15.17.10.0", {"start": v(28.34, -132.27) * mm, "end": v(26.76, -129.54) * mm});
            skCircle(sketch, "E15.0.10.1", {"center": v(29.92, -120.9) * mm, "radius": 2.73 * mm, "construction": true});
            skLineSegment(sketch, "E15.2.10.1", {"start": v(26.76, -120.9) * mm, "end": v(28.34, -118.17) * mm});
            skLineSegment(sketch, "E15.5.10.1", {"start": v(28.34, -118.17) * mm, "end": v(31.5, -118.17) * mm});
            skLineSegment(sketch, "E15.8.10.1", {"start": v(31.5, -118.17) * mm, "end": v(33.07, -120.9) * mm});
            skLineSegment(sketch, "E15.11.10.1", {"start": v(33.07, -120.9) * mm, "end": v(31.5, -123.63) * mm});
            skLineSegment(sketch, "E15.14.10.1", {"start": v(31.5, -123.63) * mm, "end": v(28.34, -123.63) * mm});
            skLineSegment(sketch, "E15.17.10.1", {"start": v(28.34, -123.63) * mm, "end": v(26.76, -120.9) * mm});
            skCircle(sketch, "E15.0.10.2", {"center": v(29.92, -112.27) * mm, "radius": 2.73 * mm, "construction": true});
            skLineSegment(sketch, "E15.2.10.2", {"start": v(26.76, -112.27) * mm, "end": v(28.34, -109.54) * mm});
            skLineSegment(sketch, "E15.5.10.2", {"start": v(28.34, -109.54) * mm, "end": v(31.5, -109.54) * mm});
            skLineSegment(sketch, "E15.8.10.2", {"start": v(31.5, -109.54) * mm, "end": v(33.07, -112.27) * mm});
            skLineSegment(sketch, "E15.11.10.2", {"start": v(33.07, -112.27) * mm, "end": v(31.5, -115) * mm});
            skLineSegment(sketch, "E15.14.10.2", {"start": v(31.5, -115) * mm, "end": v(28.34, -115) * mm});
            skLineSegment(sketch, "E15.17.10.2", {"start": v(28.34, -115) * mm, "end": v(26.76, -112.27) * mm});
            skCircle(sketch, "E15.0.10.3", {"center": v(29.92, -103.63) * mm, "radius": 2.73 * mm, "construction": true});
            skLineSegment(sketch, "E15.2.10.3", {"start": v(26.76, -103.63) * mm, "end": v(28.34, -100.9) * mm});
            skLineSegment(sketch, "E15.5.10.3", {"start": v(28.34, -100.9) * mm, "end": v(31.5, -100.9) * mm});
            skLineSegment(sketch, "E15.8.10.3", {"start": v(31.5, -100.9) * mm, "end": v(33.07, -103.63) * mm});
            skLineSegment(sketch, "E15.11.10.3", {"start": v(33.07, -103.63) * mm, "end": v(31.5, -106.36) * mm});
            skLineSegment(sketch, "E15.14.10.3", {"start": v(31.5, -106.36) * mm, "end": v(28.34, -106.36) * mm});
            skLineSegment(sketch, "E15.17.10.3", {"start": v(28.34, -106.36) * mm, "end": v(26.76, -103.63) * mm});
            skCircle(sketch, "E15.0.10.4", {"center": v(29.92, -95) * mm, "radius": 2.73 * mm, "construction": true});
            skLineSegment(sketch, "E15.2.10.4", {"start": v(26.76, -95) * mm, "end": v(28.34, -92.27) * mm});
            skLineSegment(sketch, "E15.5.10.4", {"start": v(28.34, -92.27) * mm, "end": v(31.5, -92.27) * mm});
            skLineSegment(sketch, "E15.8.10.4", {"start": v(31.5, -92.27) * mm, "end": v(33.07, -95) * mm});
            skLineSegment(sketch, "E15.11.10.4", {"start": v(33.07, -95) * mm, "end": v(31.5, -97.73) * mm});
            skLineSegment(sketch, "E15.14.10.4", {"start": v(31.5, -97.73) * mm, "end": v(28.34, -97.73) * mm});
            skLineSegment(sketch, "E15.17.10.4", {"start": v(28.34, -97.73) * mm, "end": v(26.76, -95) * mm});
            skCircle(sketch, "E15.0.10.5", {"center": v(29.92, -86.36) * mm, "radius": 2.73 * mm, "construction": true});
            skLineSegment(sketch, "E15.2.10.5", {"start": v(26.76, -86.36) * mm, "end": v(28.34, -83.63) * mm});
            skLineSegment(sketch, "E15.5.10.5", {"start": v(28.34, -83.63) * mm, "end": v(31.5, -83.63) * mm});
            skLineSegment(sketch, "E15.8.10.5", {"start": v(31.5, -83.63) * mm, "end": v(33.07, -86.36) * mm});
            skLineSegment(sketch, "E15.11.10.5", {"start": v(33.07, -86.36) * mm, "end": v(31.5, -89.1) * mm});
            skLineSegment(sketch, "E15.14.10.5", {"start": v(31.5, -89.1) * mm, "end": v(28.34, -89.1) * mm});
            skLineSegment(sketch, "E15.17.10.5", {"start": v(28.34, -89.1) * mm, "end": v(26.76, -86.36) * mm});
            skCircle(sketch, "E15.0.10.6", {"center": v(29.92, -77.72) * mm, "radius": 2.73 * mm, "construction": true});
            skLineSegment(sketch, "E15.2.10.6", {"start": v(26.76, -77.72) * mm, "end": v(28.34, -75) * mm});
            skLineSegment(sketch, "E15.5.10.6", {"start": v(28.34, -75) * mm, "end": v(31.5, -75) * mm});
            skLineSegment(sketch, "E15.8.10.6", {"start": v(31.5, -75) * mm, "end": v(33.07, -77.72) * mm});
            skLineSegment(sketch, "E15.11.10.6", {"start": v(33.07, -77.72) * mm, "end": v(31.5, -80.45) * mm});
            skLineSegment(sketch, "E15.14.10.6", {"start": v(31.5, -80.45) * mm, "end": v(28.34, -80.45) * mm});
            skLineSegment(sketch, "E15.17.10.6", {"start": v(28.34, -80.45) * mm, "end": v(26.76, -77.72) * mm});
            skCircle(sketch, "E15.0.10.7", {"center": v(29.92, -69.09) * mm, "radius": 2.73 * mm, "construction": true});
            skLineSegment(sketch, "E15.2.10.7", {"start": v(26.76, -69.09) * mm, "end": v(28.34, -66.36) * mm});
            skLineSegment(sketch, "E15.5.10.7", {"start": v(28.34, -66.36) * mm, "end": v(31.5, -66.36) * mm});
            skLineSegment(sketch, "E15.8.10.7", {"start": v(31.5, -66.36) * mm, "end": v(33.07, -69.09) * mm});
            skLineSegment(sketch, "E15.11.10.7", {"start": v(33.07, -69.09) * mm, "end": v(31.5, -71.82) * mm});
            skLineSegment(sketch, "E15.14.10.7", {"start": v(31.5, -71.82) * mm, "end": v(28.34, -71.82) * mm});
            skLineSegment(sketch, "E15.17.10.7", {"start": v(28.34, -71.82) * mm, "end": v(26.76, -69.09) * mm});
            skCircle(sketch, "E15.0.10.8", {"center": v(29.92, -60.45) * mm, "radius": 2.73 * mm, "construction": true});
            skLineSegment(sketch, "E15.2.10.8", {"start": v(26.76, -60.45) * mm, "end": v(28.34, -57.72) * mm});
            skLineSegment(sketch, "E15.5.10.8", {"start": v(28.34, -57.72) * mm, "end": v(31.5, -57.72) * mm});
            skLineSegment(sketch, "E15.8.10.8", {"start": v(31.5, -57.72) * mm, "end": v(33.07, -60.45) * mm});
            skLineSegment(sketch, "E15.11.10.8", {"start": v(33.07, -60.45) * mm, "end": v(31.5, -63.18) * mm});
            skLineSegment(sketch, "E15.14.10.8", {"start": v(31.5, -63.18) * mm, "end": v(28.34, -63.18) * mm});
            skLineSegment(sketch, "E15.17.10.8", {"start": v(28.34, -63.18) * mm, "end": v(26.76, -60.45) * mm});
            skCircle(sketch, "E15.0.10.9", {"center": v(29.92, -51.82) * mm, "radius": 2.73 * mm, "construction": true});
            skLineSegment(sketch, "E15.2.10.9", {"start": v(26.76, -51.82) * mm, "end": v(28.34, -49.09) * mm});
            skLineSegment(sketch, "E15.5.10.9", {"start": v(28.34, -49.09) * mm, "end": v(31.5, -49.09) * mm});
            skLineSegment(sketch, "E15.8.10.9", {"start": v(31.5, -49.09) * mm, "end": v(33.07, -51.82) * mm});
            skLineSegment(sketch, "E15.11.10.9", {"start": v(33.07, -51.82) * mm, "end": v(31.5, -54.55) * mm});
            skLineSegment(sketch, "E15.14.10.9", {"start": v(31.5, -54.55) * mm, "end": v(28.34, -54.55) * mm});
            skLineSegment(sketch, "E15.17.10.9", {"start": v(28.34, -54.55) * mm, "end": v(26.76, -51.82) * mm});
            skCircle(sketch, "E15.0.10.10", {"center": v(29.92, -43.18) * mm, "radius": 2.73 * mm, "construction": true});
            skLineSegment(sketch, "E15.2.10.10", {"start": v(26.76, -43.18) * mm, "end": v(28.34, -40.45) * mm});
            skLineSegment(sketch, "E15.5.10.10", {"start": v(28.34, -40.45) * mm, "end": v(31.5, -40.45) * mm});
            skLineSegment(sketch, "E15.8.10.10", {"start": v(31.5, -40.45) * mm, "end": v(33.07, -43.18) * mm});
            skLineSegment(sketch, "E15.11.10.10", {"start": v(33.07, -43.18) * mm, "end": v(31.5, -45.91) * mm});
            skLineSegment(sketch, "E15.14.10.10", {"start": v(31.5, -45.91) * mm, "end": v(28.34, -45.91) * mm});
            skLineSegment(sketch, "E15.17.10.10", {"start": v(28.34, -45.91) * mm, "end": v(26.76, -43.18) * mm});
            skCircle(sketch, "E15.0.10.11", {"center": v(29.92, -34.54) * mm, "radius": 2.73 * mm, "construction": true});
            skLineSegment(sketch, "E15.2.10.11", {"start": v(26.76, -34.54) * mm, "end": v(28.34, -31.81) * mm});
            skLineSegment(sketch, "E15.5.10.11", {"start": v(28.34, -31.81) * mm, "end": v(31.5, -31.81) * mm});
            skLineSegment(sketch, "E15.8.10.11", {"start": v(31.5, -31.81) * mm, "end": v(33.07, -34.54) * mm});
            skLineSegment(sketch, "E15.11.10.11", {"start": v(33.07, -34.54) * mm, "end": v(31.5, -37.27) * mm});
            skLineSegment(sketch, "E15.14.10.11", {"start": v(31.5, -37.27) * mm, "end": v(28.34, -37.27) * mm});
            skLineSegment(sketch, "E15.17.10.11", {"start": v(28.34, -37.27) * mm, "end": v(26.76, -34.54) * mm});
            skCircle(sketch, "E15.0.10.12", {"center": v(29.92, -25.9) * mm, "radius": 2.73 * mm, "construction": true});
            skLineSegment(sketch, "E15.2.10.12", {"start": v(26.76, -25.9) * mm, "end": v(28.34, -23.18) * mm});
            skLineSegment(sketch, "E15.5.10.12", {"start": v(28.34, -23.18) * mm, "end": v(31.5, -23.18) * mm});
            skLineSegment(sketch, "E15.8.10.12", {"start": v(31.5, -23.18) * mm, "end": v(33.07, -25.9) * mm});
            skLineSegment(sketch, "E15.11.10.12", {"start": v(33.07, -25.9) * mm, "end": v(31.5, -28.64) * mm});
            skLineSegment(sketch, "E15.14.10.12", {"start": v(31.5, -28.64) * mm, "end": v(28.34, -28.64) * mm});
            skLineSegment(sketch, "E15.17.10.12", {"start": v(28.34, -28.64) * mm, "end": v(26.76, -25.9) * mm});
            skCircle(sketch, "E15.0.10.13", {"center": v(29.92, -17.27) * mm, "radius": 2.73 * mm, "construction": true});
            skLineSegment(sketch, "E15.2.10.13", {"start": v(26.76, -17.27) * mm, "end": v(28.34, -14.54) * mm});
            skLineSegment(sketch, "E15.5.10.13", {"start": v(28.34, -14.54) * mm, "end": v(31.5, -14.54) * mm});
            skLineSegment(sketch, "E15.8.10.13", {"start": v(31.5, -14.54) * mm, "end": v(33.07, -17.27) * mm});
            skLineSegment(sketch, "E15.11.10.13", {"start": v(33.07, -17.27) * mm, "end": v(31.5, -20) * mm});
            skLineSegment(sketch, "E15.14.10.13", {"start": v(31.5, -20) * mm, "end": v(28.34, -20) * mm});
            skLineSegment(sketch, "E15.17.10.13", {"start": v(28.34, -20) * mm, "end": v(26.76, -17.27) * mm});
            skCircle(sketch, "E15.0.10.14", {"center": v(29.92, -8.64) * mm, "radius": 2.73 * mm, "construction": true});
            skLineSegment(sketch, "E15.2.10.14", {"start": v(26.76, -8.64) * mm, "end": v(28.34, -5.9) * mm});
            skLineSegment(sketch, "E15.5.10.14", {"start": v(28.34, -5.9) * mm, "end": v(31.5, -5.9) * mm});
            skLineSegment(sketch, "E15.8.10.14", {"start": v(31.5, -5.9) * mm, "end": v(33.07, -8.64) * mm});
            skLineSegment(sketch, "E15.11.10.14", {"start": v(33.07, -8.64) * mm, "end": v(31.5, -11.37) * mm});
            skLineSegment(sketch, "E15.14.10.14", {"start": v(31.5, -11.37) * mm, "end": v(28.34, -11.37) * mm});
            skLineSegment(sketch, "E15.17.10.14", {"start": v(28.34, -11.37) * mm, "end": v(26.76, -8.64) * mm});
            skCircle(sketch, "E15.0.10.15", {"center": v(29.92, 0) * mm, "radius": 2.73 * mm, "construction": true});
            skLineSegment(sketch, "E15.2.10.15", {"start": v(26.76, 0) * mm, "end": v(28.34, 2.73) * mm});
            skLineSegment(sketch, "E15.5.10.15", {"start": v(28.34, 2.73) * mm, "end": v(31.5, 2.73) * mm});
            skLineSegment(sketch, "E15.8.10.15", {"start": v(31.5, 2.73) * mm, "end": v(33.07, 0) * mm});
            skLineSegment(sketch, "E15.11.10.15", {"start": v(33.07, 0) * mm, "end": v(31.5, -2.73) * mm});
            skLineSegment(sketch, "E15.14.10.15", {"start": v(31.5, -2.73) * mm, "end": v(28.34, -2.73) * mm});
            skLineSegment(sketch, "E15.17.10.15", {"start": v(28.34, -2.73) * mm, "end": v(26.76, 0) * mm});
            skCircle(sketch, "E15.0.10.16", {"center": v(29.92, 8.64) * mm, "radius": 2.73 * mm, "construction": true});
            skLineSegment(sketch, "E15.2.10.16", {"start": v(26.76, 8.64) * mm, "end": v(28.34, 11.37) * mm});
            skLineSegment(sketch, "E15.5.10.16", {"start": v(28.34, 11.37) * mm, "end": v(31.5, 11.37) * mm});
            skLineSegment(sketch, "E15.8.10.16", {"start": v(31.5, 11.37) * mm, "end": v(33.07, 8.64) * mm});
            skLineSegment(sketch, "E15.11.10.16", {"start": v(33.07, 8.64) * mm, "end": v(31.5, 5.9) * mm});
            skLineSegment(sketch, "E15.14.10.16", {"start": v(31.5, 5.9) * mm, "end": v(28.34, 5.9) * mm});
            skLineSegment(sketch, "E15.17.10.16", {"start": v(28.34, 5.9) * mm, "end": v(26.76, 8.64) * mm});
            skCircle(sketch, "E15.0.10.17", {"center": v(29.92, 17.27) * mm, "radius": 2.73 * mm, "construction": true});
            skLineSegment(sketch, "E15.2.10.17", {"start": v(26.76, 17.27) * mm, "end": v(28.34, 20) * mm});
            skLineSegment(sketch, "E15.5.10.17", {"start": v(28.34, 20) * mm, "end": v(31.5, 20) * mm});
            skLineSegment(sketch, "E15.8.10.17", {"start": v(31.5, 20) * mm, "end": v(33.07, 17.27) * mm});
            skLineSegment(sketch, "E15.11.10.17", {"start": v(33.07, 17.27) * mm, "end": v(31.5, 14.54) * mm});
            skLineSegment(sketch, "E15.14.10.17", {"start": v(31.5, 14.54) * mm, "end": v(28.34, 14.54) * mm});
            skLineSegment(sketch, "E15.17.10.17", {"start": v(28.34, 14.54) * mm, "end": v(26.76, 17.27) * mm});
            skCircle(sketch, "E15.0.10.18", {"center": v(29.92, 25.9) * mm, "radius": 2.73 * mm, "construction": true});
            skLineSegment(sketch, "E15.2.10.18", {"start": v(26.76, 25.9) * mm, "end": v(28.34, 28.64) * mm});
            skLineSegment(sketch, "E15.5.10.18", {"start": v(28.34, 28.64) * mm, "end": v(31.5, 28.64) * mm});
            skLineSegment(sketch, "E15.8.10.18", {"start": v(31.5, 28.64) * mm, "end": v(33.07, 25.9) * mm});
            skLineSegment(sketch, "E15.11.10.18", {"start": v(33.07, 25.9) * mm, "end": v(31.5, 23.18) * mm});
            skLineSegment(sketch, "E15.14.10.18", {"start": v(31.5, 23.18) * mm, "end": v(28.34, 23.18) * mm});
            skLineSegment(sketch, "E15.17.10.18", {"start": v(28.34, 23.18) * mm, "end": v(26.76, 25.9) * mm});
            skCircle(sketch, "E15.0.10.19", {"center": v(29.92, 34.54) * mm, "radius": 2.73 * mm, "construction": true});
            skLineSegment(sketch, "E15.2.10.19", {"start": v(26.76, 34.54) * mm, "end": v(28.34, 37.27) * mm});
            skLineSegment(sketch, "E15.5.10.19", {"start": v(28.34, 37.27) * mm, "end": v(31.5, 37.27) * mm});
            skLineSegment(sketch, "E15.8.10.19", {"start": v(31.5, 37.27) * mm, "end": v(33.07, 34.54) * mm});
            skLineSegment(sketch, "E15.11.10.19", {"start": v(33.07, 34.54) * mm, "end": v(31.5, 31.81) * mm});
            skLineSegment(sketch, "E15.14.10.19", {"start": v(31.5, 31.81) * mm, "end": v(28.34, 31.81) * mm});
            skLineSegment(sketch, "E15.17.10.19", {"start": v(28.34, 31.81) * mm, "end": v(26.76, 34.54) * mm});
            skCircle(sketch, "E15.0.11.0", {"center": v(44.87, -129.54) * mm, "radius": 2.73 * mm, "construction": true});
            skLineSegment(sketch, "E15.2.11.0", {"start": v(41.72, -129.54) * mm, "end": v(43.3, -126.8) * mm});
            skLineSegment(sketch, "E15.5.11.0", {"start": v(43.3, -126.8) * mm, "end": v(46.45, -126.8) * mm});
            skLineSegment(sketch, "E15.8.11.0", {"start": v(46.45, -126.8) * mm, "end": v(48.03, -129.54) * mm});
            skLineSegment(sketch, "E15.11.11.0", {"start": v(48.03, -129.54) * mm, "end": v(46.45, -132.27) * mm});
            skLineSegment(sketch, "E15.14.11.0", {"start": v(46.45, -132.27) * mm, "end": v(43.3, -132.27) * mm});
            skLineSegment(sketch, "E15.17.11.0", {"start": v(43.3, -132.27) * mm, "end": v(41.72, -129.54) * mm});
            skCircle(sketch, "E15.0.11.1", {"center": v(44.87, -120.9) * mm, "radius": 2.73 * mm, "construction": true});
            skLineSegment(sketch, "E15.2.11.1", {"start": v(41.72, -120.9) * mm, "end": v(43.3, -118.17) * mm});
            skLineSegment(sketch, "E15.5.11.1", {"start": v(43.3, -118.17) * mm, "end": v(46.45, -118.17) * mm});
            skLineSegment(sketch, "E15.8.11.1", {"start": v(46.45, -118.17) * mm, "end": v(48.03, -120.9) * mm});
            skLineSegment(sketch, "E15.11.11.1", {"start": v(48.03, -120.9) * mm, "end": v(46.45, -123.63) * mm});
            skLineSegment(sketch, "E15.14.11.1", {"start": v(46.45, -123.63) * mm, "end": v(43.3, -123.63) * mm});
            skLineSegment(sketch, "E15.17.11.1", {"start": v(43.3, -123.63) * mm, "end": v(41.72, -120.9) * mm});
            skCircle(sketch, "E15.0.11.2", {"center": v(44.87, -112.27) * mm, "radius": 2.73 * mm, "construction": true});
            skLineSegment(sketch, "E15.2.11.2", {"start": v(41.72, -112.27) * mm, "end": v(43.3, -109.54) * mm});
            skLineSegment(sketch, "E15.5.11.2", {"start": v(43.3, -109.54) * mm, "end": v(46.45, -109.54) * mm});
            skLineSegment(sketch, "E15.8.11.2", {"start": v(46.45, -109.54) * mm, "end": v(48.03, -112.27) * mm});
            skLineSegment(sketch, "E15.11.11.2", {"start": v(48.03, -112.27) * mm, "end": v(46.45, -115) * mm});
            skLineSegment(sketch, "E15.14.11.2", {"start": v(46.45, -115) * mm, "end": v(43.3, -115) * mm});
            skLineSegment(sketch, "E15.17.11.2", {"start": v(43.3, -115) * mm, "end": v(41.72, -112.27) * mm});
            skCircle(sketch, "E15.0.11.3", {"center": v(44.87, -103.63) * mm, "radius": 2.73 * mm, "construction": true});
            skLineSegment(sketch, "E15.2.11.3", {"start": v(41.72, -103.63) * mm, "end": v(43.3, -100.9) * mm});
            skLineSegment(sketch, "E15.5.11.3", {"start": v(43.3, -100.9) * mm, "end": v(46.45, -100.9) * mm});
            skLineSegment(sketch, "E15.8.11.3", {"start": v(46.45, -100.9) * mm, "end": v(48.03, -103.63) * mm});
            skLineSegment(sketch, "E15.11.11.3", {"start": v(48.03, -103.63) * mm, "end": v(46.45, -106.36) * mm});
            skLineSegment(sketch, "E15.14.11.3", {"start": v(46.45, -106.36) * mm, "end": v(43.3, -106.36) * mm});
            skLineSegment(sketch, "E15.17.11.3", {"start": v(43.3, -106.36) * mm, "end": v(41.72, -103.63) * mm});
            skCircle(sketch, "E15.0.11.4", {"center": v(44.87, -95) * mm, "radius": 2.73 * mm, "construction": true});
            skLineSegment(sketch, "E15.2.11.4", {"start": v(41.72, -95) * mm, "end": v(43.3, -92.27) * mm});
            skLineSegment(sketch, "E15.5.11.4", {"start": v(43.3, -92.27) * mm, "end": v(46.45, -92.27) * mm});
            skLineSegment(sketch, "E15.8.11.4", {"start": v(46.45, -92.27) * mm, "end": v(48.03, -95) * mm});
            skLineSegment(sketch, "E15.11.11.4", {"start": v(48.03, -95) * mm, "end": v(46.45, -97.73) * mm});
            skLineSegment(sketch, "E15.14.11.4", {"start": v(46.45, -97.73) * mm, "end": v(43.3, -97.73) * mm});
            skLineSegment(sketch, "E15.17.11.4", {"start": v(43.3, -97.73) * mm, "end": v(41.72, -95) * mm});
            skCircle(sketch, "E15.0.11.5", {"center": v(44.87, -86.36) * mm, "radius": 2.73 * mm, "construction": true});
            skLineSegment(sketch, "E15.2.11.5", {"start": v(41.72, -86.36) * mm, "end": v(43.3, -83.63) * mm});
            skLineSegment(sketch, "E15.5.11.5", {"start": v(43.3, -83.63) * mm, "end": v(46.45, -83.63) * mm});
            skLineSegment(sketch, "E15.8.11.5", {"start": v(46.45, -83.63) * mm, "end": v(48.03, -86.36) * mm});
            skLineSegment(sketch, "E15.11.11.5", {"start": v(48.03, -86.36) * mm, "end": v(46.45, -89.1) * mm});
            skLineSegment(sketch, "E15.14.11.5", {"start": v(46.45, -89.1) * mm, "end": v(43.3, -89.1) * mm});
            skLineSegment(sketch, "E15.17.11.5", {"start": v(43.3, -89.1) * mm, "end": v(41.72, -86.36) * mm});
            skCircle(sketch, "E15.0.11.6", {"center": v(44.87, -77.72) * mm, "radius": 2.73 * mm, "construction": true});
            skLineSegment(sketch, "E15.2.11.6", {"start": v(41.72, -77.72) * mm, "end": v(43.3, -75) * mm});
            skLineSegment(sketch, "E15.5.11.6", {"start": v(43.3, -75) * mm, "end": v(46.45, -75) * mm});
            skLineSegment(sketch, "E15.8.11.6", {"start": v(46.45, -75) * mm, "end": v(48.03, -77.72) * mm});
            skLineSegment(sketch, "E15.11.11.6", {"start": v(48.03, -77.72) * mm, "end": v(46.45, -80.45) * mm});
            skLineSegment(sketch, "E15.14.11.6", {"start": v(46.45, -80.45) * mm, "end": v(43.3, -80.45) * mm});
            skLineSegment(sketch, "E15.17.11.6", {"start": v(43.3, -80.45) * mm, "end": v(41.72, -77.72) * mm});
            skCircle(sketch, "E15.0.11.7", {"center": v(44.87, -69.09) * mm, "radius": 2.73 * mm, "construction": true});
            skLineSegment(sketch, "E15.2.11.7", {"start": v(41.72, -69.09) * mm, "end": v(43.3, -66.36) * mm});
            skLineSegment(sketch, "E15.5.11.7", {"start": v(43.3, -66.36) * mm, "end": v(46.45, -66.36) * mm});
            skLineSegment(sketch, "E15.8.11.7", {"start": v(46.45, -66.36) * mm, "end": v(48.03, -69.09) * mm});
            skLineSegment(sketch, "E15.11.11.7", {"start": v(48.03, -69.09) * mm, "end": v(46.45, -71.82) * mm});
            skLineSegment(sketch, "E15.14.11.7", {"start": v(46.45, -71.82) * mm, "end": v(43.3, -71.82) * mm});
            skLineSegment(sketch, "E15.17.11.7", {"start": v(43.3, -71.82) * mm, "end": v(41.72, -69.09) * mm});
            skCircle(sketch, "E15.0.11.8", {"center": v(44.87, -60.45) * mm, "radius": 2.73 * mm, "construction": true});
            skLineSegment(sketch, "E15.2.11.8", {"start": v(41.72, -60.45) * mm, "end": v(43.3, -57.72) * mm});
            skLineSegment(sketch, "E15.5.11.8", {"start": v(43.3, -57.72) * mm, "end": v(46.45, -57.72) * mm});
            skLineSegment(sketch, "E15.8.11.8", {"start": v(46.45, -57.72) * mm, "end": v(48.03, -60.45) * mm});
            skLineSegment(sketch, "E15.11.11.8", {"start": v(48.03, -60.45) * mm, "end": v(46.45, -63.18) * mm});
            skLineSegment(sketch, "E15.14.11.8", {"start": v(46.45, -63.18) * mm, "end": v(43.3, -63.18) * mm});
            skLineSegment(sketch, "E15.17.11.8", {"start": v(43.3, -63.18) * mm, "end": v(41.72, -60.45) * mm});
            skCircle(sketch, "E15.0.11.9", {"center": v(44.87, -51.82) * mm, "radius": 2.73 * mm, "construction": true});
            skLineSegment(sketch, "E15.2.11.9", {"start": v(41.72, -51.82) * mm, "end": v(43.3, -49.09) * mm});
            skLineSegment(sketch, "E15.5.11.9", {"start": v(43.3, -49.09) * mm, "end": v(46.45, -49.09) * mm});
            skLineSegment(sketch, "E15.8.11.9", {"start": v(46.45, -49.09) * mm, "end": v(48.03, -51.82) * mm});
            skLineSegment(sketch, "E15.11.11.9", {"start": v(48.03, -51.82) * mm, "end": v(46.45, -54.55) * mm});
            skLineSegment(sketch, "E15.14.11.9", {"start": v(46.45, -54.55) * mm, "end": v(43.3, -54.55) * mm});
            skLineSegment(sketch, "E15.17.11.9", {"start": v(43.3, -54.55) * mm, "end": v(41.72, -51.82) * mm});
            skCircle(sketch, "E15.0.11.10", {"center": v(44.87, -43.18) * mm, "radius": 2.73 * mm, "construction": true});
            skLineSegment(sketch, "E15.2.11.10", {"start": v(41.72, -43.18) * mm, "end": v(43.3, -40.45) * mm});
            skLineSegment(sketch, "E15.5.11.10", {"start": v(43.3, -40.45) * mm, "end": v(46.45, -40.45) * mm});
            skLineSegment(sketch, "E15.8.11.10", {"start": v(46.45, -40.45) * mm, "end": v(48.03, -43.18) * mm});
            skLineSegment(sketch, "E15.11.11.10", {"start": v(48.03, -43.18) * mm, "end": v(46.45, -45.91) * mm});
            skLineSegment(sketch, "E15.14.11.10", {"start": v(46.45, -45.91) * mm, "end": v(43.3, -45.91) * mm});
            skLineSegment(sketch, "E15.17.11.10", {"start": v(43.3, -45.91) * mm, "end": v(41.72, -43.18) * mm});
            skCircle(sketch, "E15.0.11.11", {"center": v(44.87, -34.54) * mm, "radius": 2.73 * mm, "construction": true});
            skLineSegment(sketch, "E15.2.11.11", {"start": v(41.72, -34.54) * mm, "end": v(43.3, -31.81) * mm});
            skLineSegment(sketch, "E15.5.11.11", {"start": v(43.3, -31.81) * mm, "end": v(46.45, -31.81) * mm});
            skLineSegment(sketch, "E15.8.11.11", {"start": v(46.45, -31.81) * mm, "end": v(48.03, -34.54) * mm});
            skLineSegment(sketch, "E15.11.11.11", {"start": v(48.03, -34.54) * mm, "end": v(46.45, -37.27) * mm});
            skLineSegment(sketch, "E15.14.11.11", {"start": v(46.45, -37.27) * mm, "end": v(43.3, -37.27) * mm});
            skLineSegment(sketch, "E15.17.11.11", {"start": v(43.3, -37.27) * mm, "end": v(41.72, -34.54) * mm});
            skCircle(sketch, "E15.0.11.12", {"center": v(44.87, -25.9) * mm, "radius": 2.73 * mm, "construction": true});
            skLineSegment(sketch, "E15.2.11.12", {"start": v(41.72, -25.9) * mm, "end": v(43.3, -23.18) * mm});
            skLineSegment(sketch, "E15.5.11.12", {"start": v(43.3, -23.18) * mm, "end": v(46.45, -23.18) * mm});
            skLineSegment(sketch, "E15.8.11.12", {"start": v(46.45, -23.18) * mm, "end": v(48.03, -25.9) * mm});
            skLineSegment(sketch, "E15.11.11.12", {"start": v(48.03, -25.9) * mm, "end": v(46.45, -28.64) * mm});
            skLineSegment(sketch, "E15.14.11.12", {"start": v(46.45, -28.64) * mm, "end": v(43.3, -28.64) * mm});
            skLineSegment(sketch, "E15.17.11.12", {"start": v(43.3, -28.64) * mm, "end": v(41.72, -25.9) * mm});
            skCircle(sketch, "E15.0.11.13", {"center": v(44.87, -17.27) * mm, "radius": 2.73 * mm, "construction": true});
            skLineSegment(sketch, "E15.2.11.13", {"start": v(41.72, -17.27) * mm, "end": v(43.3, -14.54) * mm});
            skLineSegment(sketch, "E15.5.11.13", {"start": v(43.3, -14.54) * mm, "end": v(46.45, -14.54) * mm});
            skLineSegment(sketch, "E15.8.11.13", {"start": v(46.45, -14.54) * mm, "end": v(48.03, -17.27) * mm});
            skLineSegment(sketch, "E15.11.11.13", {"start": v(48.03, -17.27) * mm, "end": v(46.45, -20) * mm});
            skLineSegment(sketch, "E15.14.11.13", {"start": v(46.45, -20) * mm, "end": v(43.3, -20) * mm});
            skLineSegment(sketch, "E15.17.11.13", {"start": v(43.3, -20) * mm, "end": v(41.72, -17.27) * mm});
            skCircle(sketch, "E15.0.11.14", {"center": v(44.87, -8.64) * mm, "radius": 2.73 * mm, "construction": true});
            skLineSegment(sketch, "E15.2.11.14", {"start": v(41.72, -8.64) * mm, "end": v(43.3, -5.9) * mm});
            skLineSegment(sketch, "E15.5.11.14", {"start": v(43.3, -5.9) * mm, "end": v(46.45, -5.9) * mm});
            skLineSegment(sketch, "E15.8.11.14", {"start": v(46.45, -5.9) * mm, "end": v(48.03, -8.64) * mm});
            skLineSegment(sketch, "E15.11.11.14", {"start": v(48.03, -8.64) * mm, "end": v(46.45, -11.37) * mm});
            skLineSegment(sketch, "E15.14.11.14", {"start": v(46.45, -11.37) * mm, "end": v(43.3, -11.37) * mm});
            skLineSegment(sketch, "E15.17.11.14", {"start": v(43.3, -11.37) * mm, "end": v(41.72, -8.64) * mm});
            skCircle(sketch, "E15.0.11.15", {"center": v(44.87, 0) * mm, "radius": 2.73 * mm, "construction": true});
            skLineSegment(sketch, "E15.2.11.15", {"start": v(41.72, 0) * mm, "end": v(43.3, 2.73) * mm});
            skLineSegment(sketch, "E15.5.11.15", {"start": v(43.3, 2.73) * mm, "end": v(46.45, 2.73) * mm});
            skLineSegment(sketch, "E15.8.11.15", {"start": v(46.45, 2.73) * mm, "end": v(48.03, 0) * mm});
            skLineSegment(sketch, "E15.11.11.15", {"start": v(48.03, 0) * mm, "end": v(46.45, -2.73) * mm});
            skLineSegment(sketch, "E15.14.11.15", {"start": v(46.45, -2.73) * mm, "end": v(43.3, -2.73) * mm});
            skLineSegment(sketch, "E15.17.11.15", {"start": v(43.3, -2.73) * mm, "end": v(41.72, 0) * mm});
            skCircle(sketch, "E15.0.11.16", {"center": v(44.87, 8.64) * mm, "radius": 2.73 * mm, "construction": true});
            skLineSegment(sketch, "E15.2.11.16", {"start": v(41.72, 8.64) * mm, "end": v(43.3, 11.37) * mm});
            skLineSegment(sketch, "E15.5.11.16", {"start": v(43.3, 11.37) * mm, "end": v(46.45, 11.37) * mm});
            skLineSegment(sketch, "E15.8.11.16", {"start": v(46.45, 11.37) * mm, "end": v(48.03, 8.64) * mm});
            skLineSegment(sketch, "E15.11.11.16", {"start": v(48.03, 8.64) * mm, "end": v(46.45, 5.9) * mm});
            skLineSegment(sketch, "E15.14.11.16", {"start": v(46.45, 5.9) * mm, "end": v(43.3, 5.9) * mm});
            skLineSegment(sketch, "E15.17.11.16", {"start": v(43.3, 5.9) * mm, "end": v(41.72, 8.64) * mm});
            skCircle(sketch, "E15.0.11.17", {"center": v(44.87, 17.27) * mm, "radius": 2.73 * mm, "construction": true});
            skLineSegment(sketch, "E15.2.11.17", {"start": v(41.72, 17.27) * mm, "end": v(43.3, 20) * mm});
            skLineSegment(sketch, "E15.5.11.17", {"start": v(43.3, 20) * mm, "end": v(46.45, 20) * mm});
            skLineSegment(sketch, "E15.8.11.17", {"start": v(46.45, 20) * mm, "end": v(48.03, 17.27) * mm});
            skLineSegment(sketch, "E15.11.11.17", {"start": v(48.03, 17.27) * mm, "end": v(46.45, 14.54) * mm});
            skLineSegment(sketch, "E15.14.11.17", {"start": v(46.45, 14.54) * mm, "end": v(43.3, 14.54) * mm});
            skLineSegment(sketch, "E15.17.11.17", {"start": v(43.3, 14.54) * mm, "end": v(41.72, 17.27) * mm});
            skCircle(sketch, "E15.0.11.18", {"center": v(44.87, 25.9) * mm, "radius": 2.73 * mm, "construction": true});
            skLineSegment(sketch, "E15.2.11.18", {"start": v(41.72, 25.9) * mm, "end": v(43.3, 28.64) * mm});
            skLineSegment(sketch, "E15.5.11.18", {"start": v(43.3, 28.64) * mm, "end": v(46.45, 28.64) * mm});
            skLineSegment(sketch, "E15.8.11.18", {"start": v(46.45, 28.64) * mm, "end": v(48.03, 25.9) * mm});
            skLineSegment(sketch, "E15.11.11.18", {"start": v(48.03, 25.9) * mm, "end": v(46.45, 23.18) * mm});
            skLineSegment(sketch, "E15.14.11.18", {"start": v(46.45, 23.18) * mm, "end": v(43.3, 23.18) * mm});
            skLineSegment(sketch, "E15.17.11.18", {"start": v(43.3, 23.18) * mm, "end": v(41.72, 25.9) * mm});
            skCircle(sketch, "E15.0.11.19", {"center": v(44.87, 34.54) * mm, "radius": 2.73 * mm, "construction": true});
            skLineSegment(sketch, "E15.2.11.19", {"start": v(41.72, 34.54) * mm, "end": v(43.3, 37.27) * mm});
            skLineSegment(sketch, "E15.5.11.19", {"start": v(43.3, 37.27) * mm, "end": v(46.45, 37.27) * mm});
            skLineSegment(sketch, "E15.8.11.19", {"start": v(46.45, 37.27) * mm, "end": v(48.03, 34.54) * mm});
            skLineSegment(sketch, "E15.11.11.19", {"start": v(48.03, 34.54) * mm, "end": v(46.45, 31.81) * mm});
            skLineSegment(sketch, "E15.14.11.19", {"start": v(46.45, 31.81) * mm, "end": v(43.3, 31.81) * mm});
            skLineSegment(sketch, "E15.17.11.19", {"start": v(43.3, 31.81) * mm, "end": v(41.72, 34.54) * mm});
            skCircle(sketch, "E15.0.12.0", {"center": v(59.83, -129.54) * mm, "radius": 2.73 * mm, "construction": true});
            skLineSegment(sketch, "E15.2.12.0", {"start": v(56.68, -129.54) * mm, "end": v(58.26, -126.8) * mm});
            skLineSegment(sketch, "E15.5.12.0", {"start": v(58.26, -126.8) * mm, "end": v(61.4, -126.8) * mm});
            skLineSegment(sketch, "E15.8.12.0", {"start": v(61.4, -126.8) * mm, "end": v(62.99, -129.54) * mm});
            skLineSegment(sketch, "E15.11.12.0", {"start": v(62.99, -129.54) * mm, "end": v(61.4, -132.27) * mm});
            skLineSegment(sketch, "E15.14.12.0", {"start": v(61.4, -132.27) * mm, "end": v(58.26, -132.27) * mm});
            skLineSegment(sketch, "E15.17.12.0", {"start": v(58.26, -132.27) * mm, "end": v(56.68, -129.54) * mm});
            skCircle(sketch, "E15.0.12.1", {"center": v(59.83, -120.9) * mm, "radius": 2.73 * mm, "construction": true});
            skLineSegment(sketch, "E15.2.12.1", {"start": v(56.68, -120.9) * mm, "end": v(58.26, -118.17) * mm});
            skLineSegment(sketch, "E15.5.12.1", {"start": v(58.26, -118.17) * mm, "end": v(61.4, -118.17) * mm});
            skLineSegment(sketch, "E15.8.12.1", {"start": v(61.4, -118.17) * mm, "end": v(62.99, -120.9) * mm});
            skLineSegment(sketch, "E15.11.12.1", {"start": v(62.99, -120.9) * mm, "end": v(61.4, -123.63) * mm});
            skLineSegment(sketch, "E15.14.12.1", {"start": v(61.4, -123.63) * mm, "end": v(58.26, -123.63) * mm});
            skLineSegment(sketch, "E15.17.12.1", {"start": v(58.26, -123.63) * mm, "end": v(56.68, -120.9) * mm});
            skCircle(sketch, "E15.0.12.2", {"center": v(59.83, -112.27) * mm, "radius": 2.73 * mm, "construction": true});
            skLineSegment(sketch, "E15.2.12.2", {"start": v(56.68, -112.27) * mm, "end": v(58.26, -109.54) * mm});
            skLineSegment(sketch, "E15.5.12.2", {"start": v(58.26, -109.54) * mm, "end": v(61.4, -109.54) * mm});
            skLineSegment(sketch, "E15.8.12.2", {"start": v(61.4, -109.54) * mm, "end": v(62.99, -112.27) * mm});
            skLineSegment(sketch, "E15.11.12.2", {"start": v(62.99, -112.27) * mm, "end": v(61.4, -115) * mm});
            skLineSegment(sketch, "E15.14.12.2", {"start": v(61.4, -115) * mm, "end": v(58.26, -115) * mm});
            skLineSegment(sketch, "E15.17.12.2", {"start": v(58.26, -115) * mm, "end": v(56.68, -112.27) * mm});
            skCircle(sketch, "E15.0.12.3", {"center": v(59.83, -103.63) * mm, "radius": 2.73 * mm, "construction": true});
            skLineSegment(sketch, "E15.2.12.3", {"start": v(56.68, -103.63) * mm, "end": v(58.26, -100.9) * mm});
            skLineSegment(sketch, "E15.5.12.3", {"start": v(58.26, -100.9) * mm, "end": v(61.4, -100.9) * mm});
            skLineSegment(sketch, "E15.8.12.3", {"start": v(61.4, -100.9) * mm, "end": v(62.99, -103.63) * mm});
            skLineSegment(sketch, "E15.11.12.3", {"start": v(62.99, -103.63) * mm, "end": v(61.4, -106.36) * mm});
            skLineSegment(sketch, "E15.14.12.3", {"start": v(61.4, -106.36) * mm, "end": v(58.26, -106.36) * mm});
            skLineSegment(sketch, "E15.17.12.3", {"start": v(58.26, -106.36) * mm, "end": v(56.68, -103.63) * mm});
            skCircle(sketch, "E15.0.12.4", {"center": v(59.83, -95) * mm, "radius": 2.73 * mm, "construction": true});
            skLineSegment(sketch, "E15.2.12.4", {"start": v(56.68, -95) * mm, "end": v(58.26, -92.27) * mm});
            skLineSegment(sketch, "E15.5.12.4", {"start": v(58.26, -92.27) * mm, "end": v(61.4, -92.27) * mm});
            skLineSegment(sketch, "E15.8.12.4", {"start": v(61.4, -92.27) * mm, "end": v(62.99, -95) * mm});
            skLineSegment(sketch, "E15.11.12.4", {"start": v(62.99, -95) * mm, "end": v(61.4, -97.73) * mm});
            skLineSegment(sketch, "E15.14.12.4", {"start": v(61.4, -97.73) * mm, "end": v(58.26, -97.73) * mm});
            skLineSegment(sketch, "E15.17.12.4", {"start": v(58.26, -97.73) * mm, "end": v(56.68, -95) * mm});
            skCircle(sketch, "E15.0.12.5", {"center": v(59.83, -86.36) * mm, "radius": 2.73 * mm, "construction": true});
            skLineSegment(sketch, "E15.2.12.5", {"start": v(56.68, -86.36) * mm, "end": v(58.26, -83.63) * mm});
            skLineSegment(sketch, "E15.5.12.5", {"start": v(58.26, -83.63) * mm, "end": v(61.4, -83.63) * mm});
            skLineSegment(sketch, "E15.8.12.5", {"start": v(61.4, -83.63) * mm, "end": v(62.99, -86.36) * mm});
            skLineSegment(sketch, "E15.11.12.5", {"start": v(62.99, -86.36) * mm, "end": v(61.4, -89.1) * mm});
            skLineSegment(sketch, "E15.14.12.5", {"start": v(61.4, -89.1) * mm, "end": v(58.26, -89.1) * mm});
            skLineSegment(sketch, "E15.17.12.5", {"start": v(58.26, -89.1) * mm, "end": v(56.68, -86.36) * mm});
            skCircle(sketch, "E15.0.12.6", {"center": v(59.83, -77.72) * mm, "radius": 2.73 * mm, "construction": true});
            skLineSegment(sketch, "E15.2.12.6", {"start": v(56.68, -77.72) * mm, "end": v(58.26, -75) * mm});
            skLineSegment(sketch, "E15.5.12.6", {"start": v(58.26, -75) * mm, "end": v(61.4, -75) * mm});
            skLineSegment(sketch, "E15.8.12.6", {"start": v(61.4, -75) * mm, "end": v(62.99, -77.72) * mm});
            skLineSegment(sketch, "E15.11.12.6", {"start": v(62.99, -77.72) * mm, "end": v(61.4, -80.45) * mm});
            skLineSegment(sketch, "E15.14.12.6", {"start": v(61.4, -80.45) * mm, "end": v(58.26, -80.45) * mm});
            skLineSegment(sketch, "E15.17.12.6", {"start": v(58.26, -80.45) * mm, "end": v(56.68, -77.72) * mm});
            skCircle(sketch, "E15.0.12.7", {"center": v(59.83, -69.09) * mm, "radius": 2.73 * mm, "construction": true});
            skLineSegment(sketch, "E15.2.12.7", {"start": v(56.68, -69.09) * mm, "end": v(58.26, -66.36) * mm});
            skLineSegment(sketch, "E15.5.12.7", {"start": v(58.26, -66.36) * mm, "end": v(61.4, -66.36) * mm});
            skLineSegment(sketch, "E15.8.12.7", {"start": v(61.4, -66.36) * mm, "end": v(62.99, -69.09) * mm});
            skLineSegment(sketch, "E15.11.12.7", {"start": v(62.99, -69.09) * mm, "end": v(61.4, -71.82) * mm});
            skLineSegment(sketch, "E15.14.12.7", {"start": v(61.4, -71.82) * mm, "end": v(58.26, -71.82) * mm});
            skLineSegment(sketch, "E15.17.12.7", {"start": v(58.26, -71.82) * mm, "end": v(56.68, -69.09) * mm});
            skCircle(sketch, "E15.0.12.8", {"center": v(59.83, -60.45) * mm, "radius": 2.73 * mm, "construction": true});
            skLineSegment(sketch, "E15.2.12.8", {"start": v(56.68, -60.45) * mm, "end": v(58.26, -57.72) * mm});
            skLineSegment(sketch, "E15.5.12.8", {"start": v(58.26, -57.72) * mm, "end": v(61.4, -57.72) * mm});
            skLineSegment(sketch, "E15.8.12.8", {"start": v(61.4, -57.72) * mm, "end": v(62.99, -60.45) * mm});
            skLineSegment(sketch, "E15.11.12.8", {"start": v(62.99, -60.45) * mm, "end": v(61.4, -63.18) * mm});
            skLineSegment(sketch, "E15.14.12.8", {"start": v(61.4, -63.18) * mm, "end": v(58.26, -63.18) * mm});
            skLineSegment(sketch, "E15.17.12.8", {"start": v(58.26, -63.18) * mm, "end": v(56.68, -60.45) * mm});
            skCircle(sketch, "E15.0.12.9", {"center": v(59.83, -51.82) * mm, "radius": 2.73 * mm, "construction": true});
            skLineSegment(sketch, "E15.2.12.9", {"start": v(56.68, -51.82) * mm, "end": v(58.26, -49.09) * mm});
            skLineSegment(sketch, "E15.5.12.9", {"start": v(58.26, -49.09) * mm, "end": v(61.4, -49.09) * mm});
            skLineSegment(sketch, "E15.8.12.9", {"start": v(61.4, -49.09) * mm, "end": v(62.99, -51.82) * mm});
            skLineSegment(sketch, "E15.11.12.9", {"start": v(62.99, -51.82) * mm, "end": v(61.4, -54.55) * mm});
            skLineSegment(sketch, "E15.14.12.9", {"start": v(61.4, -54.55) * mm, "end": v(58.26, -54.55) * mm});
            skLineSegment(sketch, "E15.17.12.9", {"start": v(58.26, -54.55) * mm, "end": v(56.68, -51.82) * mm});
            skCircle(sketch, "E15.0.12.10", {"center": v(59.83, -43.18) * mm, "radius": 2.73 * mm, "construction": true});
            skLineSegment(sketch, "E15.2.12.10", {"start": v(56.68, -43.18) * mm, "end": v(58.26, -40.45) * mm});
            skLineSegment(sketch, "E15.5.12.10", {"start": v(58.26, -40.45) * mm, "end": v(61.4, -40.45) * mm});
            skLineSegment(sketch, "E15.8.12.10", {"start": v(61.4, -40.45) * mm, "end": v(62.99, -43.18) * mm});
            skLineSegment(sketch, "E15.11.12.10", {"start": v(62.99, -43.18) * mm, "end": v(61.4, -45.91) * mm});
            skLineSegment(sketch, "E15.14.12.10", {"start": v(61.4, -45.91) * mm, "end": v(58.26, -45.91) * mm});
            skLineSegment(sketch, "E15.17.12.10", {"start": v(58.26, -45.91) * mm, "end": v(56.68, -43.18) * mm});
            skCircle(sketch, "E15.0.12.11", {"center": v(59.83, -34.54) * mm, "radius": 2.73 * mm, "construction": true});
            skLineSegment(sketch, "E15.2.12.11", {"start": v(56.68, -34.54) * mm, "end": v(58.26, -31.81) * mm});
            skLineSegment(sketch, "E15.5.12.11", {"start": v(58.26, -31.81) * mm, "end": v(61.4, -31.81) * mm});
            skLineSegment(sketch, "E15.8.12.11", {"start": v(61.4, -31.81) * mm, "end": v(62.99, -34.54) * mm});
            skLineSegment(sketch, "E15.11.12.11", {"start": v(62.99, -34.54) * mm, "end": v(61.4, -37.27) * mm});
            skLineSegment(sketch, "E15.14.12.11", {"start": v(61.4, -37.27) * mm, "end": v(58.26, -37.27) * mm});
            skLineSegment(sketch, "E15.17.12.11", {"start": v(58.26, -37.27) * mm, "end": v(56.68, -34.54) * mm});
            skCircle(sketch, "E15.0.12.12", {"center": v(59.83, -25.9) * mm, "radius": 2.73 * mm, "construction": true});
            skLineSegment(sketch, "E15.2.12.12", {"start": v(56.68, -25.9) * mm, "end": v(58.26, -23.18) * mm});
            skLineSegment(sketch, "E15.5.12.12", {"start": v(58.26, -23.18) * mm, "end": v(61.4, -23.18) * mm});
            skLineSegment(sketch, "E15.8.12.12", {"start": v(61.4, -23.18) * mm, "end": v(62.99, -25.9) * mm});
            skLineSegment(sketch, "E15.11.12.12", {"start": v(62.99, -25.9) * mm, "end": v(61.4, -28.64) * mm});
            skLineSegment(sketch, "E15.14.12.12", {"start": v(61.4, -28.64) * mm, "end": v(58.26, -28.64) * mm});
            skLineSegment(sketch, "E15.17.12.12", {"start": v(58.26, -28.64) * mm, "end": v(56.68, -25.9) * mm});
            skCircle(sketch, "E15.0.12.13", {"center": v(59.83, -17.27) * mm, "radius": 2.73 * mm, "construction": true});
            skLineSegment(sketch, "E15.2.12.13", {"start": v(56.68, -17.27) * mm, "end": v(58.26, -14.54) * mm});
            skLineSegment(sketch, "E15.5.12.13", {"start": v(58.26, -14.54) * mm, "end": v(61.4, -14.54) * mm});
            skLineSegment(sketch, "E15.8.12.13", {"start": v(61.4, -14.54) * mm, "end": v(62.99, -17.27) * mm});
            skLineSegment(sketch, "E15.11.12.13", {"start": v(62.99, -17.27) * mm, "end": v(61.4, -20) * mm});
            skLineSegment(sketch, "E15.14.12.13", {"start": v(61.4, -20) * mm, "end": v(58.26, -20) * mm});
            skLineSegment(sketch, "E15.17.12.13", {"start": v(58.26, -20) * mm, "end": v(56.68, -17.27) * mm});
            skCircle(sketch, "E15.0.12.14", {"center": v(59.83, -8.64) * mm, "radius": 2.73 * mm, "construction": true});
            skLineSegment(sketch, "E15.2.12.14", {"start": v(56.68, -8.64) * mm, "end": v(58.26, -5.9) * mm});
            skLineSegment(sketch, "E15.5.12.14", {"start": v(58.26, -5.9) * mm, "end": v(61.4, -5.9) * mm});
            skLineSegment(sketch, "E15.8.12.14", {"start": v(61.4, -5.9) * mm, "end": v(62.99, -8.64) * mm});
            skLineSegment(sketch, "E15.11.12.14", {"start": v(62.99, -8.64) * mm, "end": v(61.4, -11.37) * mm});
            skLineSegment(sketch, "E15.14.12.14", {"start": v(61.4, -11.37) * mm, "end": v(58.26, -11.37) * mm});
            skLineSegment(sketch, "E15.17.12.14", {"start": v(58.26, -11.37) * mm, "end": v(56.68, -8.64) * mm});
            skCircle(sketch, "E15.0.12.15", {"center": v(59.83, 0) * mm, "radius": 2.73 * mm, "construction": true});
            skLineSegment(sketch, "E15.2.12.15", {"start": v(56.68, 0) * mm, "end": v(58.26, 2.73) * mm});
            skLineSegment(sketch, "E15.5.12.15", {"start": v(58.26, 2.73) * mm, "end": v(61.4, 2.73) * mm});
            skLineSegment(sketch, "E15.8.12.15", {"start": v(61.4, 2.73) * mm, "end": v(62.99, 0) * mm});
            skLineSegment(sketch, "E15.11.12.15", {"start": v(62.99, 0) * mm, "end": v(61.4, -2.73) * mm});
            skLineSegment(sketch, "E15.14.12.15", {"start": v(61.4, -2.73) * mm, "end": v(58.26, -2.73) * mm});
            skLineSegment(sketch, "E15.17.12.15", {"start": v(58.26, -2.73) * mm, "end": v(56.68, 0) * mm});
            skCircle(sketch, "E15.0.12.16", {"center": v(59.83, 8.64) * mm, "radius": 2.73 * mm, "construction": true});
            skLineSegment(sketch, "E15.2.12.16", {"start": v(56.68, 8.64) * mm, "end": v(58.26, 11.37) * mm});
            skLineSegment(sketch, "E15.5.12.16", {"start": v(58.26, 11.37) * mm, "end": v(61.4, 11.37) * mm});
            skLineSegment(sketch, "E15.8.12.16", {"start": v(61.4, 11.37) * mm, "end": v(62.99, 8.64) * mm});
            skLineSegment(sketch, "E15.11.12.16", {"start": v(62.99, 8.64) * mm, "end": v(61.4, 5.9) * mm});
            skLineSegment(sketch, "E15.14.12.16", {"start": v(61.4, 5.9) * mm, "end": v(58.26, 5.9) * mm});
            skLineSegment(sketch, "E15.17.12.16", {"start": v(58.26, 5.9) * mm, "end": v(56.68, 8.64) * mm});
            skCircle(sketch, "E15.0.12.17", {"center": v(59.83, 17.27) * mm, "radius": 2.73 * mm, "construction": true});
            skLineSegment(sketch, "E15.2.12.17", {"start": v(56.68, 17.27) * mm, "end": v(58.26, 20) * mm});
            skLineSegment(sketch, "E15.5.12.17", {"start": v(58.26, 20) * mm, "end": v(61.4, 20) * mm});
            skLineSegment(sketch, "E15.8.12.17", {"start": v(61.4, 20) * mm, "end": v(62.99, 17.27) * mm});
            skLineSegment(sketch, "E15.11.12.17", {"start": v(62.99, 17.27) * mm, "end": v(61.4, 14.54) * mm});
            skLineSegment(sketch, "E15.14.12.17", {"start": v(61.4, 14.54) * mm, "end": v(58.26, 14.54) * mm});
            skLineSegment(sketch, "E15.17.12.17", {"start": v(58.26, 14.54) * mm, "end": v(56.68, 17.27) * mm});
            skCircle(sketch, "E15.0.12.18", {"center": v(59.83, 25.9) * mm, "radius": 2.73 * mm, "construction": true});
            skLineSegment(sketch, "E15.2.12.18", {"start": v(56.68, 25.9) * mm, "end": v(58.26, 28.64) * mm});
            skLineSegment(sketch, "E15.5.12.18", {"start": v(58.26, 28.64) * mm, "end": v(61.4, 28.64) * mm});
            skLineSegment(sketch, "E15.8.12.18", {"start": v(61.4, 28.64) * mm, "end": v(62.99, 25.9) * mm});
            skLineSegment(sketch, "E15.11.12.18", {"start": v(62.99, 25.9) * mm, "end": v(61.4, 23.18) * mm});
            skLineSegment(sketch, "E15.14.12.18", {"start": v(61.4, 23.18) * mm, "end": v(58.26, 23.18) * mm});
            skLineSegment(sketch, "E15.17.12.18", {"start": v(58.26, 23.18) * mm, "end": v(56.68, 25.9) * mm});
            skCircle(sketch, "E15.0.12.19", {"center": v(59.83, 34.54) * mm, "radius": 2.73 * mm, "construction": true});
            skLineSegment(sketch, "E15.2.12.19", {"start": v(56.68, 34.54) * mm, "end": v(58.26, 37.27) * mm});
            skLineSegment(sketch, "E15.5.12.19", {"start": v(58.26, 37.27) * mm, "end": v(61.4, 37.27) * mm});
            skLineSegment(sketch, "E15.8.12.19", {"start": v(61.4, 37.27) * mm, "end": v(62.99, 34.54) * mm});
            skLineSegment(sketch, "E15.11.12.19", {"start": v(62.99, 34.54) * mm, "end": v(61.4, 31.81) * mm});
            skLineSegment(sketch, "E15.14.12.19", {"start": v(61.4, 31.81) * mm, "end": v(58.26, 31.81) * mm});
            skLineSegment(sketch, "E15.17.12.19", {"start": v(58.26, 31.81) * mm, "end": v(56.68, 34.54) * mm});
            skCircle(sketch, "E15.0.13.0", {"center": v(74.8, -129.54) * mm, "radius": 2.73 * mm, "construction": true});
            skLineSegment(sketch, "E15.2.13.0", {"start": v(71.64, -129.54) * mm, "end": v(73.21, -126.8) * mm});
            skLineSegment(sketch, "E15.5.13.0", {"start": v(73.21, -126.8) * mm, "end": v(76.37, -126.8) * mm});
            skLineSegment(sketch, "E15.8.13.0", {"start": v(76.37, -126.8) * mm, "end": v(77.94, -129.54) * mm});
            skLineSegment(sketch, "E15.11.13.0", {"start": v(77.94, -129.54) * mm, "end": v(76.37, -132.27) * mm});
            skLineSegment(sketch, "E15.14.13.0", {"start": v(76.37, -132.27) * mm, "end": v(73.21, -132.27) * mm});
            skLineSegment(sketch, "E15.17.13.0", {"start": v(73.21, -132.27) * mm, "end": v(71.64, -129.54) * mm});
            skCircle(sketch, "E15.0.13.1", {"center": v(74.8, -120.9) * mm, "radius": 2.73 * mm, "construction": true});
            skLineSegment(sketch, "E15.2.13.1", {"start": v(71.64, -120.9) * mm, "end": v(73.21, -118.17) * mm});
            skLineSegment(sketch, "E15.5.13.1", {"start": v(73.21, -118.17) * mm, "end": v(76.37, -118.17) * mm});
            skLineSegment(sketch, "E15.8.13.1", {"start": v(76.37, -118.17) * mm, "end": v(77.94, -120.9) * mm});
            skLineSegment(sketch, "E15.11.13.1", {"start": v(77.94, -120.9) * mm, "end": v(76.37, -123.63) * mm});
            skLineSegment(sketch, "E15.14.13.1", {"start": v(76.37, -123.63) * mm, "end": v(73.21, -123.63) * mm});
            skLineSegment(sketch, "E15.17.13.1", {"start": v(73.21, -123.63) * mm, "end": v(71.64, -120.9) * mm});
            skCircle(sketch, "E15.0.13.2", {"center": v(74.8, -112.27) * mm, "radius": 2.73 * mm, "construction": true});
            skLineSegment(sketch, "E15.2.13.2", {"start": v(71.64, -112.27) * mm, "end": v(73.21, -109.54) * mm});
            skLineSegment(sketch, "E15.5.13.2", {"start": v(73.21, -109.54) * mm, "end": v(76.37, -109.54) * mm});
            skLineSegment(sketch, "E15.8.13.2", {"start": v(76.37, -109.54) * mm, "end": v(77.94, -112.27) * mm});
            skLineSegment(sketch, "E15.11.13.2", {"start": v(77.94, -112.27) * mm, "end": v(76.37, -115) * mm});
            skLineSegment(sketch, "E15.14.13.2", {"start": v(76.37, -115) * mm, "end": v(73.21, -115) * mm});
            skLineSegment(sketch, "E15.17.13.2", {"start": v(73.21, -115) * mm, "end": v(71.64, -112.27) * mm});
            skCircle(sketch, "E15.0.13.3", {"center": v(74.8, -103.63) * mm, "radius": 2.73 * mm, "construction": true});
            skLineSegment(sketch, "E15.2.13.3", {"start": v(71.64, -103.63) * mm, "end": v(73.21, -100.9) * mm});
            skLineSegment(sketch, "E15.5.13.3", {"start": v(73.21, -100.9) * mm, "end": v(76.37, -100.9) * mm});
            skLineSegment(sketch, "E15.8.13.3", {"start": v(76.37, -100.9) * mm, "end": v(77.94, -103.63) * mm});
            skLineSegment(sketch, "E15.11.13.3", {"start": v(77.94, -103.63) * mm, "end": v(76.37, -106.36) * mm});
            skLineSegment(sketch, "E15.14.13.3", {"start": v(76.37, -106.36) * mm, "end": v(73.21, -106.36) * mm});
            skLineSegment(sketch, "E15.17.13.3", {"start": v(73.21, -106.36) * mm, "end": v(71.64, -103.63) * mm});
            skCircle(sketch, "E15.0.13.4", {"center": v(74.8, -95) * mm, "radius": 2.73 * mm, "construction": true});
            skLineSegment(sketch, "E15.2.13.4", {"start": v(71.64, -95) * mm, "end": v(73.21, -92.27) * mm});
            skLineSegment(sketch, "E15.5.13.4", {"start": v(73.21, -92.27) * mm, "end": v(76.37, -92.27) * mm});
            skLineSegment(sketch, "E15.8.13.4", {"start": v(76.37, -92.27) * mm, "end": v(77.94, -95) * mm});
            skLineSegment(sketch, "E15.11.13.4", {"start": v(77.94, -95) * mm, "end": v(76.37, -97.73) * mm});
            skLineSegment(sketch, "E15.14.13.4", {"start": v(76.37, -97.73) * mm, "end": v(73.21, -97.73) * mm});
            skLineSegment(sketch, "E15.17.13.4", {"start": v(73.21, -97.73) * mm, "end": v(71.64, -95) * mm});
            skCircle(sketch, "E15.0.13.5", {"center": v(74.8, -86.36) * mm, "radius": 2.73 * mm, "construction": true});
            skLineSegment(sketch, "E15.2.13.5", {"start": v(71.64, -86.36) * mm, "end": v(73.21, -83.63) * mm});
            skLineSegment(sketch, "E15.5.13.5", {"start": v(73.21, -83.63) * mm, "end": v(76.37, -83.63) * mm});
            skLineSegment(sketch, "E15.8.13.5", {"start": v(76.37, -83.63) * mm, "end": v(77.94, -86.36) * mm});
            skLineSegment(sketch, "E15.11.13.5", {"start": v(77.94, -86.36) * mm, "end": v(76.37, -89.1) * mm});
            skLineSegment(sketch, "E15.14.13.5", {"start": v(76.37, -89.1) * mm, "end": v(73.21, -89.1) * mm});
            skLineSegment(sketch, "E15.17.13.5", {"start": v(73.21, -89.1) * mm, "end": v(71.64, -86.36) * mm});
            skCircle(sketch, "E15.0.13.6", {"center": v(74.8, -77.72) * mm, "radius": 2.73 * mm, "construction": true});
            skLineSegment(sketch, "E15.2.13.6", {"start": v(71.64, -77.72) * mm, "end": v(73.21, -75) * mm});
            skLineSegment(sketch, "E15.5.13.6", {"start": v(73.21, -75) * mm, "end": v(76.37, -75) * mm});
            skLineSegment(sketch, "E15.8.13.6", {"start": v(76.37, -75) * mm, "end": v(77.94, -77.72) * mm});
            skLineSegment(sketch, "E15.11.13.6", {"start": v(77.94, -77.72) * mm, "end": v(76.37, -80.45) * mm});
            skLineSegment(sketch, "E15.14.13.6", {"start": v(76.37, -80.45) * mm, "end": v(73.21, -80.45) * mm});
            skLineSegment(sketch, "E15.17.13.6", {"start": v(73.21, -80.45) * mm, "end": v(71.64, -77.72) * mm});
            skCircle(sketch, "E15.0.13.7", {"center": v(74.8, -69.09) * mm, "radius": 2.73 * mm, "construction": true});
            skLineSegment(sketch, "E15.2.13.7", {"start": v(71.64, -69.09) * mm, "end": v(73.21, -66.36) * mm});
            skLineSegment(sketch, "E15.5.13.7", {"start": v(73.21, -66.36) * mm, "end": v(76.37, -66.36) * mm});
            skLineSegment(sketch, "E15.8.13.7", {"start": v(76.37, -66.36) * mm, "end": v(77.94, -69.09) * mm});
            skLineSegment(sketch, "E15.11.13.7", {"start": v(77.94, -69.09) * mm, "end": v(76.37, -71.82) * mm});
            skLineSegment(sketch, "E15.14.13.7", {"start": v(76.37, -71.82) * mm, "end": v(73.21, -71.82) * mm});
            skLineSegment(sketch, "E15.17.13.7", {"start": v(73.21, -71.82) * mm, "end": v(71.64, -69.09) * mm});
            skCircle(sketch, "E15.0.13.8", {"center": v(74.8, -60.45) * mm, "radius": 2.73 * mm, "construction": true});
            skLineSegment(sketch, "E15.2.13.8", {"start": v(71.64, -60.45) * mm, "end": v(73.21, -57.72) * mm});
            skLineSegment(sketch, "E15.5.13.8", {"start": v(73.21, -57.72) * mm, "end": v(76.37, -57.72) * mm});
            skLineSegment(sketch, "E15.8.13.8", {"start": v(76.37, -57.72) * mm, "end": v(77.94, -60.45) * mm});
            skLineSegment(sketch, "E15.11.13.8", {"start": v(77.94, -60.45) * mm, "end": v(76.37, -63.18) * mm});
            skLineSegment(sketch, "E15.14.13.8", {"start": v(76.37, -63.18) * mm, "end": v(73.21, -63.18) * mm});
            skLineSegment(sketch, "E15.17.13.8", {"start": v(73.21, -63.18) * mm, "end": v(71.64, -60.45) * mm});
            skCircle(sketch, "E15.0.13.9", {"center": v(74.8, -51.82) * mm, "radius": 2.73 * mm, "construction": true});
            skLineSegment(sketch, "E15.2.13.9", {"start": v(71.64, -51.82) * mm, "end": v(73.21, -49.09) * mm});
            skLineSegment(sketch, "E15.5.13.9", {"start": v(73.21, -49.09) * mm, "end": v(76.37, -49.09) * mm});
            skLineSegment(sketch, "E15.8.13.9", {"start": v(76.37, -49.09) * mm, "end": v(77.94, -51.82) * mm});
            skLineSegment(sketch, "E15.11.13.9", {"start": v(77.94, -51.82) * mm, "end": v(76.37, -54.55) * mm});
            skLineSegment(sketch, "E15.14.13.9", {"start": v(76.37, -54.55) * mm, "end": v(73.21, -54.55) * mm});
            skLineSegment(sketch, "E15.17.13.9", {"start": v(73.21, -54.55) * mm, "end": v(71.64, -51.82) * mm});
            skCircle(sketch, "E15.0.13.10", {"center": v(74.8, -43.18) * mm, "radius": 2.73 * mm, "construction": true});
            skLineSegment(sketch, "E15.2.13.10", {"start": v(71.64, -43.18) * mm, "end": v(73.21, -40.45) * mm});
            skLineSegment(sketch, "E15.5.13.10", {"start": v(73.21, -40.45) * mm, "end": v(76.37, -40.45) * mm});
            skLineSegment(sketch, "E15.8.13.10", {"start": v(76.37, -40.45) * mm, "end": v(77.94, -43.18) * mm});
            skLineSegment(sketch, "E15.11.13.10", {"start": v(77.94, -43.18) * mm, "end": v(76.37, -45.91) * mm});
            skLineSegment(sketch, "E15.14.13.10", {"start": v(76.37, -45.91) * mm, "end": v(73.21, -45.91) * mm});
            skLineSegment(sketch, "E15.17.13.10", {"start": v(73.21, -45.91) * mm, "end": v(71.64, -43.18) * mm});
            skCircle(sketch, "E15.0.13.11", {"center": v(74.8, -34.54) * mm, "radius": 2.73 * mm, "construction": true});
            skLineSegment(sketch, "E15.2.13.11", {"start": v(71.64, -34.54) * mm, "end": v(73.21, -31.81) * mm});
            skLineSegment(sketch, "E15.5.13.11", {"start": v(73.21, -31.81) * mm, "end": v(76.37, -31.81) * mm});
            skLineSegment(sketch, "E15.8.13.11", {"start": v(76.37, -31.81) * mm, "end": v(77.94, -34.54) * mm});
            skLineSegment(sketch, "E15.11.13.11", {"start": v(77.94, -34.54) * mm, "end": v(76.37, -37.27) * mm});
            skLineSegment(sketch, "E15.14.13.11", {"start": v(76.37, -37.27) * mm, "end": v(73.21, -37.27) * mm});
            skLineSegment(sketch, "E15.17.13.11", {"start": v(73.21, -37.27) * mm, "end": v(71.64, -34.54) * mm});
            skCircle(sketch, "E15.0.13.12", {"center": v(74.8, -25.9) * mm, "radius": 2.73 * mm, "construction": true});
            skLineSegment(sketch, "E15.2.13.12", {"start": v(71.64, -25.9) * mm, "end": v(73.21, -23.18) * mm});
            skLineSegment(sketch, "E15.5.13.12", {"start": v(73.21, -23.18) * mm, "end": v(76.37, -23.18) * mm});
            skLineSegment(sketch, "E15.8.13.12", {"start": v(76.37, -23.18) * mm, "end": v(77.94, -25.9) * mm});
            skLineSegment(sketch, "E15.11.13.12", {"start": v(77.94, -25.9) * mm, "end": v(76.37, -28.64) * mm});
            skLineSegment(sketch, "E15.14.13.12", {"start": v(76.37, -28.64) * mm, "end": v(73.21, -28.64) * mm});
            skLineSegment(sketch, "E15.17.13.12", {"start": v(73.21, -28.64) * mm, "end": v(71.64, -25.9) * mm});
            skCircle(sketch, "E15.0.13.13", {"center": v(74.8, -17.27) * mm, "radius": 2.73 * mm, "construction": true});
            skLineSegment(sketch, "E15.2.13.13", {"start": v(71.64, -17.27) * mm, "end": v(73.21, -14.54) * mm});
            skLineSegment(sketch, "E15.5.13.13", {"start": v(73.21, -14.54) * mm, "end": v(76.37, -14.54) * mm});
            skLineSegment(sketch, "E15.8.13.13", {"start": v(76.37, -14.54) * mm, "end": v(77.94, -17.27) * mm});
            skLineSegment(sketch, "E15.11.13.13", {"start": v(77.94, -17.27) * mm, "end": v(76.37, -20) * mm});
            skLineSegment(sketch, "E15.14.13.13", {"start": v(76.37, -20) * mm, "end": v(73.21, -20) * mm});
            skLineSegment(sketch, "E15.17.13.13", {"start": v(73.21, -20) * mm, "end": v(71.64, -17.27) * mm});
            skCircle(sketch, "E15.0.13.14", {"center": v(74.8, -8.64) * mm, "radius": 2.73 * mm, "construction": true});
            skLineSegment(sketch, "E15.2.13.14", {"start": v(71.64, -8.64) * mm, "end": v(73.21, -5.9) * mm});
            skLineSegment(sketch, "E15.5.13.14", {"start": v(73.21, -5.9) * mm, "end": v(76.37, -5.9) * mm});
            skLineSegment(sketch, "E15.8.13.14", {"start": v(76.37, -5.9) * mm, "end": v(77.94, -8.64) * mm});
            skLineSegment(sketch, "E15.11.13.14", {"start": v(77.94, -8.64) * mm, "end": v(76.37, -11.37) * mm});
            skLineSegment(sketch, "E15.14.13.14", {"start": v(76.37, -11.37) * mm, "end": v(73.21, -11.37) * mm});
            skLineSegment(sketch, "E15.17.13.14", {"start": v(73.21, -11.37) * mm, "end": v(71.64, -8.64) * mm});
            skCircle(sketch, "E15.0.13.15", {"center": v(74.8, 0) * mm, "radius": 2.73 * mm, "construction": true});
            skLineSegment(sketch, "E15.2.13.15", {"start": v(71.64, 0) * mm, "end": v(73.21, 2.73) * mm});
            skLineSegment(sketch, "E15.5.13.15", {"start": v(73.21, 2.73) * mm, "end": v(76.37, 2.73) * mm});
            skLineSegment(sketch, "E15.8.13.15", {"start": v(76.37, 2.73) * mm, "end": v(77.94, 0) * mm});
            skLineSegment(sketch, "E15.11.13.15", {"start": v(77.94, 0) * mm, "end": v(76.37, -2.73) * mm});
            skLineSegment(sketch, "E15.14.13.15", {"start": v(76.37, -2.73) * mm, "end": v(73.21, -2.73) * mm});
            skLineSegment(sketch, "E15.17.13.15", {"start": v(73.21, -2.73) * mm, "end": v(71.64, 0) * mm});
            skCircle(sketch, "E15.0.13.16", {"center": v(74.8, 8.64) * mm, "radius": 2.73 * mm, "construction": true});
            skLineSegment(sketch, "E15.2.13.16", {"start": v(71.64, 8.64) * mm, "end": v(73.21, 11.37) * mm});
            skLineSegment(sketch, "E15.5.13.16", {"start": v(73.21, 11.37) * mm, "end": v(76.37, 11.37) * mm});
            skLineSegment(sketch, "E15.8.13.16", {"start": v(76.37, 11.37) * mm, "end": v(77.94, 8.64) * mm});
            skLineSegment(sketch, "E15.11.13.16", {"start": v(77.94, 8.64) * mm, "end": v(76.37, 5.9) * mm});
            skLineSegment(sketch, "E15.14.13.16", {"start": v(76.37, 5.9) * mm, "end": v(73.21, 5.9) * mm});
            skLineSegment(sketch, "E15.17.13.16", {"start": v(73.21, 5.9) * mm, "end": v(71.64, 8.64) * mm});
            skCircle(sketch, "E15.0.13.17", {"center": v(74.8, 17.27) * mm, "radius": 2.73 * mm, "construction": true});
            skLineSegment(sketch, "E15.2.13.17", {"start": v(71.64, 17.27) * mm, "end": v(73.21, 20) * mm});
            skLineSegment(sketch, "E15.5.13.17", {"start": v(73.21, 20) * mm, "end": v(76.37, 20) * mm});
            skLineSegment(sketch, "E15.8.13.17", {"start": v(76.37, 20) * mm, "end": v(77.94, 17.27) * mm});
            skLineSegment(sketch, "E15.11.13.17", {"start": v(77.94, 17.27) * mm, "end": v(76.37, 14.54) * mm});
            skLineSegment(sketch, "E15.14.13.17", {"start": v(76.37, 14.54) * mm, "end": v(73.21, 14.54) * mm});
            skLineSegment(sketch, "E15.17.13.17", {"start": v(73.21, 14.54) * mm, "end": v(71.64, 17.27) * mm});
            skCircle(sketch, "E15.0.13.18", {"center": v(74.8, 25.9) * mm, "radius": 2.73 * mm, "construction": true});
            skLineSegment(sketch, "E15.2.13.18", {"start": v(71.64, 25.9) * mm, "end": v(73.21, 28.64) * mm});
            skLineSegment(sketch, "E15.5.13.18", {"start": v(73.21, 28.64) * mm, "end": v(76.37, 28.64) * mm});
            skLineSegment(sketch, "E15.8.13.18", {"start": v(76.37, 28.64) * mm, "end": v(77.94, 25.9) * mm});
            skLineSegment(sketch, "E15.11.13.18", {"start": v(77.94, 25.9) * mm, "end": v(76.37, 23.18) * mm});
            skLineSegment(sketch, "E15.14.13.18", {"start": v(76.37, 23.18) * mm, "end": v(73.21, 23.18) * mm});
            skLineSegment(sketch, "E15.17.13.18", {"start": v(73.21, 23.18) * mm, "end": v(71.64, 25.9) * mm});
            skCircle(sketch, "E15.0.13.19", {"center": v(74.8, 34.54) * mm, "radius": 2.73 * mm, "construction": true});
            skLineSegment(sketch, "E15.2.13.19", {"start": v(71.64, 34.54) * mm, "end": v(73.21, 37.27) * mm});
            skLineSegment(sketch, "E15.5.13.19", {"start": v(73.21, 37.27) * mm, "end": v(76.37, 37.27) * mm});
            skLineSegment(sketch, "E15.8.13.19", {"start": v(76.37, 37.27) * mm, "end": v(77.94, 34.54) * mm});
            skLineSegment(sketch, "E15.11.13.19", {"start": v(77.94, 34.54) * mm, "end": v(76.37, 31.81) * mm});
            skLineSegment(sketch, "E15.14.13.19", {"start": v(76.37, 31.81) * mm, "end": v(73.21, 31.81) * mm});
            skLineSegment(sketch, "E15.17.13.19", {"start": v(73.21, 31.81) * mm, "end": v(71.64, 34.54) * mm});
            skCircle(sketch, "E15.0.14.0", {"center": v(89.75, -129.54) * mm, "radius": 2.73 * mm, "construction": true});
            skLineSegment(sketch, "E15.2.14.0", {"start": v(86.6, -129.54) * mm, "end": v(88.17, -126.8) * mm});
            skLineSegment(sketch, "E15.5.14.0", {"start": v(88.17, -126.8) * mm, "end": v(91.32, -126.8) * mm});
            skLineSegment(sketch, "E15.8.14.0", {"start": v(91.32, -126.8) * mm, "end": v(92.9, -129.54) * mm});
            skLineSegment(sketch, "E15.11.14.0", {"start": v(92.9, -129.54) * mm, "end": v(91.32, -132.27) * mm});
            skLineSegment(sketch, "E15.14.14.0", {"start": v(91.32, -132.27) * mm, "end": v(88.17, -132.27) * mm});
            skLineSegment(sketch, "E15.17.14.0", {"start": v(88.17, -132.27) * mm, "end": v(86.6, -129.54) * mm});
            skCircle(sketch, "E15.0.14.1", {"center": v(89.75, -120.9) * mm, "radius": 2.73 * mm, "construction": true});
            skLineSegment(sketch, "E15.2.14.1", {"start": v(86.6, -120.9) * mm, "end": v(88.17, -118.17) * mm});
            skLineSegment(sketch, "E15.5.14.1", {"start": v(88.17, -118.17) * mm, "end": v(91.32, -118.17) * mm});
            skLineSegment(sketch, "E15.8.14.1", {"start": v(91.32, -118.17) * mm, "end": v(92.9, -120.9) * mm});
            skLineSegment(sketch, "E15.11.14.1", {"start": v(92.9, -120.9) * mm, "end": v(91.32, -123.63) * mm});
            skLineSegment(sketch, "E15.14.14.1", {"start": v(91.32, -123.63) * mm, "end": v(88.17, -123.63) * mm});
            skLineSegment(sketch, "E15.17.14.1", {"start": v(88.17, -123.63) * mm, "end": v(86.6, -120.9) * mm});
            skCircle(sketch, "E15.0.14.2", {"center": v(89.75, -112.27) * mm, "radius": 2.73 * mm, "construction": true});
            skLineSegment(sketch, "E15.2.14.2", {"start": v(86.6, -112.27) * mm, "end": v(88.17, -109.54) * mm});
            skLineSegment(sketch, "E15.5.14.2", {"start": v(88.17, -109.54) * mm, "end": v(91.32, -109.54) * mm});
            skLineSegment(sketch, "E15.8.14.2", {"start": v(91.32, -109.54) * mm, "end": v(92.9, -112.27) * mm});
            skLineSegment(sketch, "E15.11.14.2", {"start": v(92.9, -112.27) * mm, "end": v(91.32, -115) * mm});
            skLineSegment(sketch, "E15.14.14.2", {"start": v(91.32, -115) * mm, "end": v(88.17, -115) * mm});
            skLineSegment(sketch, "E15.17.14.2", {"start": v(88.17, -115) * mm, "end": v(86.6, -112.27) * mm});
            skCircle(sketch, "E15.0.14.3", {"center": v(89.75, -103.63) * mm, "radius": 2.73 * mm, "construction": true});
            skLineSegment(sketch, "E15.2.14.3", {"start": v(86.6, -103.63) * mm, "end": v(88.17, -100.9) * mm});
            skLineSegment(sketch, "E15.5.14.3", {"start": v(88.17, -100.9) * mm, "end": v(91.32, -100.9) * mm});
            skLineSegment(sketch, "E15.8.14.3", {"start": v(91.32, -100.9) * mm, "end": v(92.9, -103.63) * mm});
            skLineSegment(sketch, "E15.11.14.3", {"start": v(92.9, -103.63) * mm, "end": v(91.32, -106.36) * mm});
            skLineSegment(sketch, "E15.14.14.3", {"start": v(91.32, -106.36) * mm, "end": v(88.17, -106.36) * mm});
            skLineSegment(sketch, "E15.17.14.3", {"start": v(88.17, -106.36) * mm, "end": v(86.6, -103.63) * mm});
            skCircle(sketch, "E15.0.14.4", {"center": v(89.75, -95) * mm, "radius": 2.73 * mm, "construction": true});
            skLineSegment(sketch, "E15.2.14.4", {"start": v(86.6, -95) * mm, "end": v(88.17, -92.27) * mm});
            skLineSegment(sketch, "E15.5.14.4", {"start": v(88.17, -92.27) * mm, "end": v(91.32, -92.27) * mm});
            skLineSegment(sketch, "E15.8.14.4", {"start": v(91.32, -92.27) * mm, "end": v(92.9, -95) * mm});
            skLineSegment(sketch, "E15.11.14.4", {"start": v(92.9, -95) * mm, "end": v(91.32, -97.73) * mm});
            skLineSegment(sketch, "E15.14.14.4", {"start": v(91.32, -97.73) * mm, "end": v(88.17, -97.73) * mm});
            skLineSegment(sketch, "E15.17.14.4", {"start": v(88.17, -97.73) * mm, "end": v(86.6, -95) * mm});
            skCircle(sketch, "E15.0.14.5", {"center": v(89.75, -86.36) * mm, "radius": 2.73 * mm, "construction": true});
            skLineSegment(sketch, "E15.2.14.5", {"start": v(86.6, -86.36) * mm, "end": v(88.17, -83.63) * mm});
            skLineSegment(sketch, "E15.5.14.5", {"start": v(88.17, -83.63) * mm, "end": v(91.32, -83.63) * mm});
            skLineSegment(sketch, "E15.8.14.5", {"start": v(91.32, -83.63) * mm, "end": v(92.9, -86.36) * mm});
            skLineSegment(sketch, "E15.11.14.5", {"start": v(92.9, -86.36) * mm, "end": v(91.32, -89.1) * mm});
            skLineSegment(sketch, "E15.14.14.5", {"start": v(91.32, -89.1) * mm, "end": v(88.17, -89.1) * mm});
            skLineSegment(sketch, "E15.17.14.5", {"start": v(88.17, -89.1) * mm, "end": v(86.6, -86.36) * mm});
            skCircle(sketch, "E15.0.14.6", {"center": v(89.75, -77.72) * mm, "radius": 2.73 * mm, "construction": true});
            skLineSegment(sketch, "E15.2.14.6", {"start": v(86.6, -77.72) * mm, "end": v(88.17, -75) * mm});
            skLineSegment(sketch, "E15.5.14.6", {"start": v(88.17, -75) * mm, "end": v(91.32, -75) * mm});
            skLineSegment(sketch, "E15.8.14.6", {"start": v(91.32, -75) * mm, "end": v(92.9, -77.72) * mm});
            skLineSegment(sketch, "E15.11.14.6", {"start": v(92.9, -77.72) * mm, "end": v(91.32, -80.45) * mm});
            skLineSegment(sketch, "E15.14.14.6", {"start": v(91.32, -80.45) * mm, "end": v(88.17, -80.45) * mm});
            skLineSegment(sketch, "E15.17.14.6", {"start": v(88.17, -80.45) * mm, "end": v(86.6, -77.72) * mm});
            skCircle(sketch, "E15.0.14.7", {"center": v(89.75, -69.09) * mm, "radius": 2.73 * mm, "construction": true});
            skLineSegment(sketch, "E15.2.14.7", {"start": v(86.6, -69.09) * mm, "end": v(88.17, -66.36) * mm});
            skLineSegment(sketch, "E15.5.14.7", {"start": v(88.17, -66.36) * mm, "end": v(91.32, -66.36) * mm});
            skLineSegment(sketch, "E15.8.14.7", {"start": v(91.32, -66.36) * mm, "end": v(92.9, -69.09) * mm});
            skLineSegment(sketch, "E15.11.14.7", {"start": v(92.9, -69.09) * mm, "end": v(91.32, -71.82) * mm});
            skLineSegment(sketch, "E15.14.14.7", {"start": v(91.32, -71.82) * mm, "end": v(88.17, -71.82) * mm});
            skLineSegment(sketch, "E15.17.14.7", {"start": v(88.17, -71.82) * mm, "end": v(86.6, -69.09) * mm});
            skCircle(sketch, "E15.0.14.8", {"center": v(89.75, -60.45) * mm, "radius": 2.73 * mm, "construction": true});
            skLineSegment(sketch, "E15.2.14.8", {"start": v(86.6, -60.45) * mm, "end": v(88.17, -57.72) * mm});
            skLineSegment(sketch, "E15.5.14.8", {"start": v(88.17, -57.72) * mm, "end": v(91.32, -57.72) * mm});
            skLineSegment(sketch, "E15.8.14.8", {"start": v(91.32, -57.72) * mm, "end": v(92.9, -60.45) * mm});
            skLineSegment(sketch, "E15.11.14.8", {"start": v(92.9, -60.45) * mm, "end": v(91.32, -63.18) * mm});
            skLineSegment(sketch, "E15.14.14.8", {"start": v(91.32, -63.18) * mm, "end": v(88.17, -63.18) * mm});
            skLineSegment(sketch, "E15.17.14.8", {"start": v(88.17, -63.18) * mm, "end": v(86.6, -60.45) * mm});
            skCircle(sketch, "E15.0.14.9", {"center": v(89.75, -51.82) * mm, "radius": 2.73 * mm, "construction": true});
            skLineSegment(sketch, "E15.2.14.9", {"start": v(86.6, -51.82) * mm, "end": v(88.17, -49.09) * mm});
            skLineSegment(sketch, "E15.5.14.9", {"start": v(88.17, -49.09) * mm, "end": v(91.32, -49.09) * mm});
            skLineSegment(sketch, "E15.8.14.9", {"start": v(91.32, -49.09) * mm, "end": v(92.9, -51.82) * mm});
            skLineSegment(sketch, "E15.11.14.9", {"start": v(92.9, -51.82) * mm, "end": v(91.32, -54.55) * mm});
            skLineSegment(sketch, "E15.14.14.9", {"start": v(91.32, -54.55) * mm, "end": v(88.17, -54.55) * mm});
            skLineSegment(sketch, "E15.17.14.9", {"start": v(88.17, -54.55) * mm, "end": v(86.6, -51.82) * mm});
            skCircle(sketch, "E15.0.14.10", {"center": v(89.75, -43.18) * mm, "radius": 2.73 * mm, "construction": true});
            skLineSegment(sketch, "E15.2.14.10", {"start": v(86.6, -43.18) * mm, "end": v(88.17, -40.45) * mm});
            skLineSegment(sketch, "E15.5.14.10", {"start": v(88.17, -40.45) * mm, "end": v(91.32, -40.45) * mm});
            skLineSegment(sketch, "E15.8.14.10", {"start": v(91.32, -40.45) * mm, "end": v(92.9, -43.18) * mm});
            skLineSegment(sketch, "E15.11.14.10", {"start": v(92.9, -43.18) * mm, "end": v(91.32, -45.91) * mm});
            skLineSegment(sketch, "E15.14.14.10", {"start": v(91.32, -45.91) * mm, "end": v(88.17, -45.91) * mm});
            skLineSegment(sketch, "E15.17.14.10", {"start": v(88.17, -45.91) * mm, "end": v(86.6, -43.18) * mm});
            skCircle(sketch, "E15.0.14.11", {"center": v(89.75, -34.54) * mm, "radius": 2.73 * mm, "construction": true});
            skLineSegment(sketch, "E15.2.14.11", {"start": v(86.6, -34.54) * mm, "end": v(88.17, -31.81) * mm});
            skLineSegment(sketch, "E15.5.14.11", {"start": v(88.17, -31.81) * mm, "end": v(91.32, -31.81) * mm});
            skLineSegment(sketch, "E15.8.14.11", {"start": v(91.32, -31.81) * mm, "end": v(92.9, -34.54) * mm});
            skLineSegment(sketch, "E15.11.14.11", {"start": v(92.9, -34.54) * mm, "end": v(91.32, -37.27) * mm});
            skLineSegment(sketch, "E15.14.14.11", {"start": v(91.32, -37.27) * mm, "end": v(88.17, -37.27) * mm});
            skLineSegment(sketch, "E15.17.14.11", {"start": v(88.17, -37.27) * mm, "end": v(86.6, -34.54) * mm});
            skCircle(sketch, "E15.0.14.12", {"center": v(89.75, -25.9) * mm, "radius": 2.73 * mm, "construction": true});
            skLineSegment(sketch, "E15.2.14.12", {"start": v(86.6, -25.9) * mm, "end": v(88.17, -23.18) * mm});
            skLineSegment(sketch, "E15.5.14.12", {"start": v(88.17, -23.18) * mm, "end": v(91.32, -23.18) * mm});
            skLineSegment(sketch, "E15.8.14.12", {"start": v(91.32, -23.18) * mm, "end": v(92.9, -25.9) * mm});
            skLineSegment(sketch, "E15.11.14.12", {"start": v(92.9, -25.9) * mm, "end": v(91.32, -28.64) * mm});
            skLineSegment(sketch, "E15.14.14.12", {"start": v(91.32, -28.64) * mm, "end": v(88.17, -28.64) * mm});
            skLineSegment(sketch, "E15.17.14.12", {"start": v(88.17, -28.64) * mm, "end": v(86.6, -25.9) * mm});
            skCircle(sketch, "E15.0.14.13", {"center": v(89.75, -17.27) * mm, "radius": 2.73 * mm, "construction": true});
            skLineSegment(sketch, "E15.2.14.13", {"start": v(86.6, -17.27) * mm, "end": v(88.17, -14.54) * mm});
            skLineSegment(sketch, "E15.5.14.13", {"start": v(88.17, -14.54) * mm, "end": v(91.32, -14.54) * mm});
            skLineSegment(sketch, "E15.8.14.13", {"start": v(91.32, -14.54) * mm, "end": v(92.9, -17.27) * mm});
            skLineSegment(sketch, "E15.11.14.13", {"start": v(92.9, -17.27) * mm, "end": v(91.32, -20) * mm});
            skLineSegment(sketch, "E15.14.14.13", {"start": v(91.32, -20) * mm, "end": v(88.17, -20) * mm});
            skLineSegment(sketch, "E15.17.14.13", {"start": v(88.17, -20) * mm, "end": v(86.6, -17.27) * mm});
            skCircle(sketch, "E15.0.14.14", {"center": v(89.75, -8.64) * mm, "radius": 2.73 * mm, "construction": true});
            skLineSegment(sketch, "E15.2.14.14", {"start": v(86.6, -8.64) * mm, "end": v(88.17, -5.9) * mm});
            skLineSegment(sketch, "E15.5.14.14", {"start": v(88.17, -5.9) * mm, "end": v(91.32, -5.9) * mm});
            skLineSegment(sketch, "E15.8.14.14", {"start": v(91.32, -5.9) * mm, "end": v(92.9, -8.64) * mm});
            skLineSegment(sketch, "E15.11.14.14", {"start": v(92.9, -8.64) * mm, "end": v(91.32, -11.37) * mm});
            skLineSegment(sketch, "E15.14.14.14", {"start": v(91.32, -11.37) * mm, "end": v(88.17, -11.37) * mm});
            skLineSegment(sketch, "E15.17.14.14", {"start": v(88.17, -11.37) * mm, "end": v(86.6, -8.64) * mm});
            skCircle(sketch, "E15.0.14.15", {"center": v(89.75, 0) * mm, "radius": 2.73 * mm, "construction": true});
            skLineSegment(sketch, "E15.2.14.15", {"start": v(86.6, 0) * mm, "end": v(88.17, 2.73) * mm});
            skLineSegment(sketch, "E15.5.14.15", {"start": v(88.17, 2.73) * mm, "end": v(91.32, 2.73) * mm});
            skLineSegment(sketch, "E15.8.14.15", {"start": v(91.32, 2.73) * mm, "end": v(92.9, 0) * mm});
            skLineSegment(sketch, "E15.11.14.15", {"start": v(92.9, 0) * mm, "end": v(91.32, -2.73) * mm});
            skLineSegment(sketch, "E15.14.14.15", {"start": v(91.32, -2.73) * mm, "end": v(88.17, -2.73) * mm});
            skLineSegment(sketch, "E15.17.14.15", {"start": v(88.17, -2.73) * mm, "end": v(86.6, 0) * mm});
            skCircle(sketch, "E15.0.14.16", {"center": v(89.75, 8.64) * mm, "radius": 2.73 * mm, "construction": true});
            skLineSegment(sketch, "E15.2.14.16", {"start": v(86.6, 8.64) * mm, "end": v(88.17, 11.37) * mm});
            skLineSegment(sketch, "E15.5.14.16", {"start": v(88.17, 11.37) * mm, "end": v(91.32, 11.37) * mm});
            skLineSegment(sketch, "E15.8.14.16", {"start": v(91.32, 11.37) * mm, "end": v(92.9, 8.64) * mm});
            skLineSegment(sketch, "E15.11.14.16", {"start": v(92.9, 8.64) * mm, "end": v(91.32, 5.9) * mm});
            skLineSegment(sketch, "E15.14.14.16", {"start": v(91.32, 5.9) * mm, "end": v(88.17, 5.9) * mm});
            skLineSegment(sketch, "E15.17.14.16", {"start": v(88.17, 5.9) * mm, "end": v(86.6, 8.64) * mm});
            skCircle(sketch, "E15.0.14.17", {"center": v(89.75, 17.27) * mm, "radius": 2.73 * mm, "construction": true});
            skLineSegment(sketch, "E15.2.14.17", {"start": v(86.6, 17.27) * mm, "end": v(88.17, 20) * mm});
            skLineSegment(sketch, "E15.5.14.17", {"start": v(88.17, 20) * mm, "end": v(91.32, 20) * mm});
            skLineSegment(sketch, "E15.8.14.17", {"start": v(91.32, 20) * mm, "end": v(92.9, 17.27) * mm});
            skLineSegment(sketch, "E15.11.14.17", {"start": v(92.9, 17.27) * mm, "end": v(91.32, 14.54) * mm});
            skLineSegment(sketch, "E15.14.14.17", {"start": v(91.32, 14.54) * mm, "end": v(88.17, 14.54) * mm});
            skLineSegment(sketch, "E15.17.14.17", {"start": v(88.17, 14.54) * mm, "end": v(86.6, 17.27) * mm});
            skCircle(sketch, "E15.0.14.18", {"center": v(89.75, 25.9) * mm, "radius": 2.73 * mm, "construction": true});
            skLineSegment(sketch, "E15.2.14.18", {"start": v(86.6, 25.9) * mm, "end": v(88.17, 28.64) * mm});
            skLineSegment(sketch, "E15.5.14.18", {"start": v(88.17, 28.64) * mm, "end": v(91.32, 28.64) * mm});
            skLineSegment(sketch, "E15.8.14.18", {"start": v(91.32, 28.64) * mm, "end": v(92.9, 25.9) * mm});
            skLineSegment(sketch, "E15.11.14.18", {"start": v(92.9, 25.9) * mm, "end": v(91.32, 23.18) * mm});
            skLineSegment(sketch, "E15.14.14.18", {"start": v(91.32, 23.18) * mm, "end": v(88.17, 23.18) * mm});
            skLineSegment(sketch, "E15.17.14.18", {"start": v(88.17, 23.18) * mm, "end": v(86.6, 25.9) * mm});
            skCircle(sketch, "E15.0.14.19", {"center": v(89.75, 34.54) * mm, "radius": 2.73 * mm, "construction": true});
            skLineSegment(sketch, "E15.2.14.19", {"start": v(86.6, 34.54) * mm, "end": v(88.17, 37.27) * mm});
            skLineSegment(sketch, "E15.5.14.19", {"start": v(88.17, 37.27) * mm, "end": v(91.32, 37.27) * mm});
            skLineSegment(sketch, "E15.8.14.19", {"start": v(91.32, 37.27) * mm, "end": v(92.9, 34.54) * mm});
            skLineSegment(sketch, "E15.11.14.19", {"start": v(92.9, 34.54) * mm, "end": v(91.32, 31.81) * mm});
            skLineSegment(sketch, "E15.14.14.19", {"start": v(91.32, 31.81) * mm, "end": v(88.17, 31.81) * mm});
            skLineSegment(sketch, "E15.17.14.19", {"start": v(88.17, 31.81) * mm, "end": v(86.6, 34.54) * mm});
            skCircle(sketch, "E15.0.15.0", {"center": v(104.7, -129.54) * mm, "radius": 2.73 * mm, "construction": true});
            skLineSegment(sketch, "E15.2.15.0", {"start": v(101.55, -129.54) * mm, "end": v(103.13, -126.8) * mm});
            skLineSegment(sketch, "E15.5.15.0", {"start": v(103.13, -126.8) * mm, "end": v(106.28, -126.8) * mm});
            skLineSegment(sketch, "E15.8.15.0", {"start": v(106.28, -126.8) * mm, "end": v(107.86, -129.54) * mm});
            skLineSegment(sketch, "E15.11.15.0", {"start": v(107.86, -129.54) * mm, "end": v(106.28, -132.27) * mm});
            skLineSegment(sketch, "E15.14.15.0", {"start": v(106.28, -132.27) * mm, "end": v(103.13, -132.27) * mm});
            skLineSegment(sketch, "E15.17.15.0", {"start": v(103.13, -132.27) * mm, "end": v(101.55, -129.54) * mm});
            skCircle(sketch, "E15.0.15.1", {"center": v(104.7, -120.9) * mm, "radius": 2.73 * mm, "construction": true});
            skLineSegment(sketch, "E15.2.15.1", {"start": v(101.55, -120.9) * mm, "end": v(103.13, -118.17) * mm});
            skLineSegment(sketch, "E15.5.15.1", {"start": v(103.13, -118.17) * mm, "end": v(106.28, -118.17) * mm});
            skLineSegment(sketch, "E15.8.15.1", {"start": v(106.28, -118.17) * mm, "end": v(107.86, -120.9) * mm});
            skLineSegment(sketch, "E15.11.15.1", {"start": v(107.86, -120.9) * mm, "end": v(106.28, -123.63) * mm});
            skLineSegment(sketch, "E15.14.15.1", {"start": v(106.28, -123.63) * mm, "end": v(103.13, -123.63) * mm});
            skLineSegment(sketch, "E15.17.15.1", {"start": v(103.13, -123.63) * mm, "end": v(101.55, -120.9) * mm});
            skCircle(sketch, "E15.0.15.2", {"center": v(104.7, -112.27) * mm, "radius": 2.73 * mm, "construction": true});
            skLineSegment(sketch, "E15.2.15.2", {"start": v(101.55, -112.27) * mm, "end": v(103.13, -109.54) * mm});
            skLineSegment(sketch, "E15.5.15.2", {"start": v(103.13, -109.54) * mm, "end": v(106.28, -109.54) * mm});
            skLineSegment(sketch, "E15.8.15.2", {"start": v(106.28, -109.54) * mm, "end": v(107.86, -112.27) * mm});
            skLineSegment(sketch, "E15.11.15.2", {"start": v(107.86, -112.27) * mm, "end": v(106.28, -115) * mm});
            skLineSegment(sketch, "E15.14.15.2", {"start": v(106.28, -115) * mm, "end": v(103.13, -115) * mm});
            skLineSegment(sketch, "E15.17.15.2", {"start": v(103.13, -115) * mm, "end": v(101.55, -112.27) * mm});
            skCircle(sketch, "E15.0.15.3", {"center": v(104.7, -103.63) * mm, "radius": 2.73 * mm, "construction": true});
            skLineSegment(sketch, "E15.2.15.3", {"start": v(101.55, -103.63) * mm, "end": v(103.13, -100.9) * mm});
            skLineSegment(sketch, "E15.5.15.3", {"start": v(103.13, -100.9) * mm, "end": v(106.28, -100.9) * mm});
            skLineSegment(sketch, "E15.8.15.3", {"start": v(106.28, -100.9) * mm, "end": v(107.86, -103.63) * mm});
            skLineSegment(sketch, "E15.11.15.3", {"start": v(107.86, -103.63) * mm, "end": v(106.28, -106.36) * mm});
            skLineSegment(sketch, "E15.14.15.3", {"start": v(106.28, -106.36) * mm, "end": v(103.13, -106.36) * mm});
            skLineSegment(sketch, "E15.17.15.3", {"start": v(103.13, -106.36) * mm, "end": v(101.55, -103.63) * mm});
            skCircle(sketch, "E15.0.15.4", {"center": v(104.7, -95) * mm, "radius": 2.73 * mm, "construction": true});
            skLineSegment(sketch, "E15.2.15.4", {"start": v(101.55, -95) * mm, "end": v(103.13, -92.27) * mm});
            skLineSegment(sketch, "E15.5.15.4", {"start": v(103.13, -92.27) * mm, "end": v(106.28, -92.27) * mm});
            skLineSegment(sketch, "E15.8.15.4", {"start": v(106.28, -92.27) * mm, "end": v(107.86, -95) * mm});
            skLineSegment(sketch, "E15.11.15.4", {"start": v(107.86, -95) * mm, "end": v(106.28, -97.73) * mm});
            skLineSegment(sketch, "E15.14.15.4", {"start": v(106.28, -97.73) * mm, "end": v(103.13, -97.73) * mm});
            skLineSegment(sketch, "E15.17.15.4", {"start": v(103.13, -97.73) * mm, "end": v(101.55, -95) * mm});
            skCircle(sketch, "E15.0.15.5", {"center": v(104.7, -86.36) * mm, "radius": 2.73 * mm, "construction": true});
            skLineSegment(sketch, "E15.2.15.5", {"start": v(101.55, -86.36) * mm, "end": v(103.13, -83.63) * mm});
            skLineSegment(sketch, "E15.5.15.5", {"start": v(103.13, -83.63) * mm, "end": v(106.28, -83.63) * mm});
            skLineSegment(sketch, "E15.8.15.5", {"start": v(106.28, -83.63) * mm, "end": v(107.86, -86.36) * mm});
            skLineSegment(sketch, "E15.11.15.5", {"start": v(107.86, -86.36) * mm, "end": v(106.28, -89.1) * mm});
            skLineSegment(sketch, "E15.14.15.5", {"start": v(106.28, -89.1) * mm, "end": v(103.13, -89.1) * mm});
            skLineSegment(sketch, "E15.17.15.5", {"start": v(103.13, -89.1) * mm, "end": v(101.55, -86.36) * mm});
            skCircle(sketch, "E15.0.15.6", {"center": v(104.7, -77.72) * mm, "radius": 2.73 * mm, "construction": true});
            skLineSegment(sketch, "E15.2.15.6", {"start": v(101.55, -77.72) * mm, "end": v(103.13, -75) * mm});
            skLineSegment(sketch, "E15.5.15.6", {"start": v(103.13, -75) * mm, "end": v(106.28, -75) * mm});
            skLineSegment(sketch, "E15.8.15.6", {"start": v(106.28, -75) * mm, "end": v(107.86, -77.72) * mm});
            skLineSegment(sketch, "E15.11.15.6", {"start": v(107.86, -77.72) * mm, "end": v(106.28, -80.45) * mm});
            skLineSegment(sketch, "E15.14.15.6", {"start": v(106.28, -80.45) * mm, "end": v(103.13, -80.45) * mm});
            skLineSegment(sketch, "E15.17.15.6", {"start": v(103.13, -80.45) * mm, "end": v(101.55, -77.72) * mm});
            skCircle(sketch, "E15.0.15.7", {"center": v(104.7, -69.09) * mm, "radius": 2.73 * mm, "construction": true});
            skLineSegment(sketch, "E15.2.15.7", {"start": v(101.55, -69.09) * mm, "end": v(103.13, -66.36) * mm});
            skLineSegment(sketch, "E15.5.15.7", {"start": v(103.13, -66.36) * mm, "end": v(106.28, -66.36) * mm});
            skLineSegment(sketch, "E15.8.15.7", {"start": v(106.28, -66.36) * mm, "end": v(107.86, -69.09) * mm});
            skLineSegment(sketch, "E15.11.15.7", {"start": v(107.86, -69.09) * mm, "end": v(106.28, -71.82) * mm});
            skLineSegment(sketch, "E15.14.15.7", {"start": v(106.28, -71.82) * mm, "end": v(103.13, -71.82) * mm});
            skLineSegment(sketch, "E15.17.15.7", {"start": v(103.13, -71.82) * mm, "end": v(101.55, -69.09) * mm});
            skCircle(sketch, "E15.0.15.8", {"center": v(104.7, -60.45) * mm, "radius": 2.73 * mm, "construction": true});
            skLineSegment(sketch, "E15.2.15.8", {"start": v(101.55, -60.45) * mm, "end": v(103.13, -57.72) * mm});
            skLineSegment(sketch, "E15.5.15.8", {"start": v(103.13, -57.72) * mm, "end": v(106.28, -57.72) * mm});
            skLineSegment(sketch, "E15.8.15.8", {"start": v(106.28, -57.72) * mm, "end": v(107.86, -60.45) * mm});
            skLineSegment(sketch, "E15.11.15.8", {"start": v(107.86, -60.45) * mm, "end": v(106.28, -63.18) * mm});
            skLineSegment(sketch, "E15.14.15.8", {"start": v(106.28, -63.18) * mm, "end": v(103.13, -63.18) * mm});
            skLineSegment(sketch, "E15.17.15.8", {"start": v(103.13, -63.18) * mm, "end": v(101.55, -60.45) * mm});
            skCircle(sketch, "E15.0.15.9", {"center": v(104.7, -51.82) * mm, "radius": 2.73 * mm, "construction": true});
            skLineSegment(sketch, "E15.2.15.9", {"start": v(101.55, -51.82) * mm, "end": v(103.13, -49.09) * mm});
            skLineSegment(sketch, "E15.5.15.9", {"start": v(103.13, -49.09) * mm, "end": v(106.28, -49.09) * mm});
            skLineSegment(sketch, "E15.8.15.9", {"start": v(106.28, -49.09) * mm, "end": v(107.86, -51.82) * mm});
            skLineSegment(sketch, "E15.11.15.9", {"start": v(107.86, -51.82) * mm, "end": v(106.28, -54.55) * mm});
            skLineSegment(sketch, "E15.14.15.9", {"start": v(106.28, -54.55) * mm, "end": v(103.13, -54.55) * mm});
            skLineSegment(sketch, "E15.17.15.9", {"start": v(103.13, -54.55) * mm, "end": v(101.55, -51.82) * mm});
            skCircle(sketch, "E15.0.15.10", {"center": v(104.7, -43.18) * mm, "radius": 2.73 * mm, "construction": true});
            skLineSegment(sketch, "E15.2.15.10", {"start": v(101.55, -43.18) * mm, "end": v(103.13, -40.45) * mm});
            skLineSegment(sketch, "E15.5.15.10", {"start": v(103.13, -40.45) * mm, "end": v(106.28, -40.45) * mm});
            skLineSegment(sketch, "E15.8.15.10", {"start": v(106.28, -40.45) * mm, "end": v(107.86, -43.18) * mm});
            skLineSegment(sketch, "E15.11.15.10", {"start": v(107.86, -43.18) * mm, "end": v(106.28, -45.91) * mm});
            skLineSegment(sketch, "E15.14.15.10", {"start": v(106.28, -45.91) * mm, "end": v(103.13, -45.91) * mm});
            skLineSegment(sketch, "E15.17.15.10", {"start": v(103.13, -45.91) * mm, "end": v(101.55, -43.18) * mm});
            skCircle(sketch, "E15.0.15.11", {"center": v(104.7, -34.54) * mm, "radius": 2.73 * mm, "construction": true});
            skLineSegment(sketch, "E15.2.15.11", {"start": v(101.55, -34.54) * mm, "end": v(103.13, -31.81) * mm});
            skLineSegment(sketch, "E15.5.15.11", {"start": v(103.13, -31.81) * mm, "end": v(106.28, -31.81) * mm});
            skLineSegment(sketch, "E15.8.15.11", {"start": v(106.28, -31.81) * mm, "end": v(107.86, -34.54) * mm});
            skLineSegment(sketch, "E15.11.15.11", {"start": v(107.86, -34.54) * mm, "end": v(106.28, -37.27) * mm});
            skLineSegment(sketch, "E15.14.15.11", {"start": v(106.28, -37.27) * mm, "end": v(103.13, -37.27) * mm});
            skLineSegment(sketch, "E15.17.15.11", {"start": v(103.13, -37.27) * mm, "end": v(101.55, -34.54) * mm});
            skCircle(sketch, "E15.0.15.12", {"center": v(104.7, -25.9) * mm, "radius": 2.73 * mm, "construction": true});
            skLineSegment(sketch, "E15.2.15.12", {"start": v(101.55, -25.9) * mm, "end": v(103.13, -23.18) * mm});
            skLineSegment(sketch, "E15.5.15.12", {"start": v(103.13, -23.18) * mm, "end": v(106.28, -23.18) * mm});
            skLineSegment(sketch, "E15.8.15.12", {"start": v(106.28, -23.18) * mm, "end": v(107.86, -25.9) * mm});
            skLineSegment(sketch, "E15.11.15.12", {"start": v(107.86, -25.9) * mm, "end": v(106.28, -28.64) * mm});
            skLineSegment(sketch, "E15.14.15.12", {"start": v(106.28, -28.64) * mm, "end": v(103.13, -28.64) * mm});
            skLineSegment(sketch, "E15.17.15.12", {"start": v(103.13, -28.64) * mm, "end": v(101.55, -25.9) * mm});
            skCircle(sketch, "E15.0.15.13", {"center": v(104.7, -17.27) * mm, "radius": 2.73 * mm, "construction": true});
            skLineSegment(sketch, "E15.2.15.13", {"start": v(101.55, -17.27) * mm, "end": v(103.13, -14.54) * mm});
            skLineSegment(sketch, "E15.5.15.13", {"start": v(103.13, -14.54) * mm, "end": v(106.28, -14.54) * mm});
            skLineSegment(sketch, "E15.8.15.13", {"start": v(106.28, -14.54) * mm, "end": v(107.86, -17.27) * mm});
            skLineSegment(sketch, "E15.11.15.13", {"start": v(107.86, -17.27) * mm, "end": v(106.28, -20) * mm});
            skLineSegment(sketch, "E15.14.15.13", {"start": v(106.28, -20) * mm, "end": v(103.13, -20) * mm});
            skLineSegment(sketch, "E15.17.15.13", {"start": v(103.13, -20) * mm, "end": v(101.55, -17.27) * mm});
            skCircle(sketch, "E15.0.15.14", {"center": v(104.7, -8.64) * mm, "radius": 2.73 * mm, "construction": true});
            skLineSegment(sketch, "E15.2.15.14", {"start": v(101.55, -8.64) * mm, "end": v(103.13, -5.9) * mm});
            skLineSegment(sketch, "E15.5.15.14", {"start": v(103.13, -5.9) * mm, "end": v(106.28, -5.9) * mm});
            skLineSegment(sketch, "E15.8.15.14", {"start": v(106.28, -5.9) * mm, "end": v(107.86, -8.64) * mm});
            skLineSegment(sketch, "E15.11.15.14", {"start": v(107.86, -8.64) * mm, "end": v(106.28, -11.37) * mm});
            skLineSegment(sketch, "E15.14.15.14", {"start": v(106.28, -11.37) * mm, "end": v(103.13, -11.37) * mm});
            skLineSegment(sketch, "E15.17.15.14", {"start": v(103.13, -11.37) * mm, "end": v(101.55, -8.64) * mm});
            skCircle(sketch, "E15.0.15.15", {"center": v(104.7, 0) * mm, "radius": 2.73 * mm, "construction": true});
            skLineSegment(sketch, "E15.2.15.15", {"start": v(101.55, 0) * mm, "end": v(103.13, 2.73) * mm});
            skLineSegment(sketch, "E15.5.15.15", {"start": v(103.13, 2.73) * mm, "end": v(106.28, 2.73) * mm});
            skLineSegment(sketch, "E15.8.15.15", {"start": v(106.28, 2.73) * mm, "end": v(107.86, 0) * mm});
            skLineSegment(sketch, "E15.11.15.15", {"start": v(107.86, 0) * mm, "end": v(106.28, -2.73) * mm});
            skLineSegment(sketch, "E15.14.15.15", {"start": v(106.28, -2.73) * mm, "end": v(103.13, -2.73) * mm});
            skLineSegment(sketch, "E15.17.15.15", {"start": v(103.13, -2.73) * mm, "end": v(101.55, 0) * mm});
            skCircle(sketch, "E15.0.15.16", {"center": v(104.7, 8.64) * mm, "radius": 2.73 * mm, "construction": true});
            skLineSegment(sketch, "E15.2.15.16", {"start": v(101.55, 8.64) * mm, "end": v(103.13, 11.37) * mm});
            skLineSegment(sketch, "E15.5.15.16", {"start": v(103.13, 11.37) * mm, "end": v(106.28, 11.37) * mm});
            skLineSegment(sketch, "E15.8.15.16", {"start": v(106.28, 11.37) * mm, "end": v(107.86, 8.64) * mm});
            skLineSegment(sketch, "E15.11.15.16", {"start": v(107.86, 8.64) * mm, "end": v(106.28, 5.9) * mm});
            skLineSegment(sketch, "E15.14.15.16", {"start": v(106.28, 5.9) * mm, "end": v(103.13, 5.9) * mm});
            skLineSegment(sketch, "E15.17.15.16", {"start": v(103.13, 5.9) * mm, "end": v(101.55, 8.64) * mm});
            skCircle(sketch, "E15.0.15.17", {"center": v(104.7, 17.27) * mm, "radius": 2.73 * mm, "construction": true});
            skLineSegment(sketch, "E15.2.15.17", {"start": v(101.55, 17.27) * mm, "end": v(103.13, 20) * mm});
            skLineSegment(sketch, "E15.5.15.17", {"start": v(103.13, 20) * mm, "end": v(106.28, 20) * mm});
            skLineSegment(sketch, "E15.8.15.17", {"start": v(106.28, 20) * mm, "end": v(107.86, 17.27) * mm});
            skLineSegment(sketch, "E15.11.15.17", {"start": v(107.86, 17.27) * mm, "end": v(106.28, 14.54) * mm});
            skLineSegment(sketch, "E15.14.15.17", {"start": v(106.28, 14.54) * mm, "end": v(103.13, 14.54) * mm});
            skLineSegment(sketch, "E15.17.15.17", {"start": v(103.13, 14.54) * mm, "end": v(101.55, 17.27) * mm});
            skCircle(sketch, "E15.0.15.18", {"center": v(104.7, 25.9) * mm, "radius": 2.73 * mm, "construction": true});
            skLineSegment(sketch, "E15.2.15.18", {"start": v(101.55, 25.9) * mm, "end": v(103.13, 28.64) * mm});
            skLineSegment(sketch, "E15.5.15.18", {"start": v(103.13, 28.64) * mm, "end": v(106.28, 28.64) * mm});
            skLineSegment(sketch, "E15.8.15.18", {"start": v(106.28, 28.64) * mm, "end": v(107.86, 25.9) * mm});
            skLineSegment(sketch, "E15.11.15.18", {"start": v(107.86, 25.9) * mm, "end": v(106.28, 23.18) * mm});
            skLineSegment(sketch, "E15.14.15.18", {"start": v(106.28, 23.18) * mm, "end": v(103.13, 23.18) * mm});
            skLineSegment(sketch, "E15.17.15.18", {"start": v(103.13, 23.18) * mm, "end": v(101.55, 25.9) * mm});
            skCircle(sketch, "E15.0.15.19", {"center": v(104.7, 34.54) * mm, "radius": 2.73 * mm, "construction": true});
            skLineSegment(sketch, "E15.2.15.19", {"start": v(101.55, 34.54) * mm, "end": v(103.13, 37.27) * mm});
            skLineSegment(sketch, "E15.5.15.19", {"start": v(103.13, 37.27) * mm, "end": v(106.28, 37.27) * mm});
            skLineSegment(sketch, "E15.8.15.19", {"start": v(106.28, 37.27) * mm, "end": v(107.86, 34.54) * mm});
            skLineSegment(sketch, "E15.11.15.19", {"start": v(107.86, 34.54) * mm, "end": v(106.28, 31.81) * mm});
            skLineSegment(sketch, "E15.14.15.19", {"start": v(106.28, 31.81) * mm, "end": v(103.13, 31.81) * mm});
            skLineSegment(sketch, "E15.17.15.19", {"start": v(103.13, 31.81) * mm, "end": v(101.55, 34.54) * mm});
            skCircle(sketch, "E15.0.16.0", {"center": v(119.66, -129.54) * mm, "radius": 2.73 * mm, "construction": true});
            skLineSegment(sketch, "E15.2.16.0", {"start": v(116.51, -129.54) * mm, "end": v(118.09, -126.8) * mm});
            skLineSegment(sketch, "E15.5.16.0", {"start": v(118.09, -126.8) * mm, "end": v(121.24, -126.8) * mm});
            skLineSegment(sketch, "E15.8.16.0", {"start": v(121.24, -126.8) * mm, "end": v(122.82, -129.54) * mm});
            skLineSegment(sketch, "E15.11.16.0", {"start": v(122.82, -129.54) * mm, "end": v(121.24, -132.27) * mm});
            skLineSegment(sketch, "E15.14.16.0", {"start": v(121.24, -132.27) * mm, "end": v(118.09, -132.27) * mm});
            skLineSegment(sketch, "E15.17.16.0", {"start": v(118.09, -132.27) * mm, "end": v(116.51, -129.54) * mm});
            skCircle(sketch, "E15.0.16.1", {"center": v(119.66, -120.9) * mm, "radius": 2.73 * mm, "construction": true});
            skLineSegment(sketch, "E15.2.16.1", {"start": v(116.51, -120.9) * mm, "end": v(118.09, -118.17) * mm});
            skLineSegment(sketch, "E15.5.16.1", {"start": v(118.09, -118.17) * mm, "end": v(121.24, -118.17) * mm});
            skLineSegment(sketch, "E15.8.16.1", {"start": v(121.24, -118.17) * mm, "end": v(122.82, -120.9) * mm});
            skLineSegment(sketch, "E15.11.16.1", {"start": v(122.82, -120.9) * mm, "end": v(121.24, -123.63) * mm});
            skLineSegment(sketch, "E15.14.16.1", {"start": v(121.24, -123.63) * mm, "end": v(118.09, -123.63) * mm});
            skLineSegment(sketch, "E15.17.16.1", {"start": v(118.09, -123.63) * mm, "end": v(116.51, -120.9) * mm});
            skCircle(sketch, "E15.0.16.2", {"center": v(119.66, -112.27) * mm, "radius": 2.73 * mm, "construction": true});
            skLineSegment(sketch, "E15.2.16.2", {"start": v(116.51, -112.27) * mm, "end": v(118.09, -109.54) * mm});
            skLineSegment(sketch, "E15.5.16.2", {"start": v(118.09, -109.54) * mm, "end": v(121.24, -109.54) * mm});
            skLineSegment(sketch, "E15.8.16.2", {"start": v(121.24, -109.54) * mm, "end": v(122.82, -112.27) * mm});
            skLineSegment(sketch, "E15.11.16.2", {"start": v(122.82, -112.27) * mm, "end": v(121.24, -115) * mm});
            skLineSegment(sketch, "E15.14.16.2", {"start": v(121.24, -115) * mm, "end": v(118.09, -115) * mm});
            skLineSegment(sketch, "E15.17.16.2", {"start": v(118.09, -115) * mm, "end": v(116.51, -112.27) * mm});
            skCircle(sketch, "E15.0.16.3", {"center": v(119.66, -103.63) * mm, "radius": 2.73 * mm, "construction": true});
            skLineSegment(sketch, "E15.2.16.3", {"start": v(116.51, -103.63) * mm, "end": v(118.09, -100.9) * mm});
            skLineSegment(sketch, "E15.5.16.3", {"start": v(118.09, -100.9) * mm, "end": v(121.24, -100.9) * mm});
            skLineSegment(sketch, "E15.8.16.3", {"start": v(121.24, -100.9) * mm, "end": v(122.82, -103.63) * mm});
            skLineSegment(sketch, "E15.11.16.3", {"start": v(122.82, -103.63) * mm, "end": v(121.24, -106.36) * mm});
            skLineSegment(sketch, "E15.14.16.3", {"start": v(121.24, -106.36) * mm, "end": v(118.09, -106.36) * mm});
            skLineSegment(sketch, "E15.17.16.3", {"start": v(118.09, -106.36) * mm, "end": v(116.51, -103.63) * mm});
            skCircle(sketch, "E15.0.16.4", {"center": v(119.66, -95) * mm, "radius": 2.73 * mm, "construction": true});
            skLineSegment(sketch, "E15.2.16.4", {"start": v(116.51, -95) * mm, "end": v(118.09, -92.27) * mm});
            skLineSegment(sketch, "E15.5.16.4", {"start": v(118.09, -92.27) * mm, "end": v(121.24, -92.27) * mm});
            skLineSegment(sketch, "E15.8.16.4", {"start": v(121.24, -92.27) * mm, "end": v(122.82, -95) * mm});
            skLineSegment(sketch, "E15.11.16.4", {"start": v(122.82, -95) * mm, "end": v(121.24, -97.73) * mm});
            skLineSegment(sketch, "E15.14.16.4", {"start": v(121.24, -97.73) * mm, "end": v(118.09, -97.73) * mm});
            skLineSegment(sketch, "E15.17.16.4", {"start": v(118.09, -97.73) * mm, "end": v(116.51, -95) * mm});
            skCircle(sketch, "E15.0.16.5", {"center": v(119.66, -86.36) * mm, "radius": 2.73 * mm, "construction": true});
            skLineSegment(sketch, "E15.2.16.5", {"start": v(116.51, -86.36) * mm, "end": v(118.09, -83.63) * mm});
            skLineSegment(sketch, "E15.5.16.5", {"start": v(118.09, -83.63) * mm, "end": v(121.24, -83.63) * mm});
            skLineSegment(sketch, "E15.8.16.5", {"start": v(121.24, -83.63) * mm, "end": v(122.82, -86.36) * mm});
            skLineSegment(sketch, "E15.11.16.5", {"start": v(122.82, -86.36) * mm, "end": v(121.24, -89.1) * mm});
            skLineSegment(sketch, "E15.14.16.5", {"start": v(121.24, -89.1) * mm, "end": v(118.09, -89.1) * mm});
            skLineSegment(sketch, "E15.17.16.5", {"start": v(118.09, -89.1) * mm, "end": v(116.51, -86.36) * mm});
            skCircle(sketch, "E15.0.16.6", {"center": v(119.66, -77.72) * mm, "radius": 2.73 * mm, "construction": true});
            skLineSegment(sketch, "E15.2.16.6", {"start": v(116.51, -77.72) * mm, "end": v(118.09, -75) * mm});
            skLineSegment(sketch, "E15.5.16.6", {"start": v(118.09, -75) * mm, "end": v(121.24, -75) * mm});
            skLineSegment(sketch, "E15.8.16.6", {"start": v(121.24, -75) * mm, "end": v(122.82, -77.72) * mm});
            skLineSegment(sketch, "E15.11.16.6", {"start": v(122.82, -77.72) * mm, "end": v(121.24, -80.45) * mm});
            skLineSegment(sketch, "E15.14.16.6", {"start": v(121.24, -80.45) * mm, "end": v(118.09, -80.45) * mm});
            skLineSegment(sketch, "E15.17.16.6", {"start": v(118.09, -80.45) * mm, "end": v(116.51, -77.72) * mm});
            skCircle(sketch, "E15.0.16.7", {"center": v(119.66, -69.09) * mm, "radius": 2.73 * mm, "construction": true});
            skLineSegment(sketch, "E15.2.16.7", {"start": v(116.51, -69.09) * mm, "end": v(118.09, -66.36) * mm});
            skLineSegment(sketch, "E15.5.16.7", {"start": v(118.09, -66.36) * mm, "end": v(121.24, -66.36) * mm});
            skLineSegment(sketch, "E15.8.16.7", {"start": v(121.24, -66.36) * mm, "end": v(122.82, -69.09) * mm});
            skLineSegment(sketch, "E15.11.16.7", {"start": v(122.82, -69.09) * mm, "end": v(121.24, -71.82) * mm});
            skLineSegment(sketch, "E15.14.16.7", {"start": v(121.24, -71.82) * mm, "end": v(118.09, -71.82) * mm});
            skLineSegment(sketch, "E15.17.16.7", {"start": v(118.09, -71.82) * mm, "end": v(116.51, -69.09) * mm});
            skCircle(sketch, "E15.0.16.8", {"center": v(119.66, -60.45) * mm, "radius": 2.73 * mm, "construction": true});
            skLineSegment(sketch, "E15.2.16.8", {"start": v(116.51, -60.45) * mm, "end": v(118.09, -57.72) * mm});
            skLineSegment(sketch, "E15.5.16.8", {"start": v(118.09, -57.72) * mm, "end": v(121.24, -57.72) * mm});
            skLineSegment(sketch, "E15.8.16.8", {"start": v(121.24, -57.72) * mm, "end": v(122.82, -60.45) * mm});
            skLineSegment(sketch, "E15.11.16.8", {"start": v(122.82, -60.45) * mm, "end": v(121.24, -63.18) * mm});
            skLineSegment(sketch, "E15.14.16.8", {"start": v(121.24, -63.18) * mm, "end": v(118.09, -63.18) * mm});
            skLineSegment(sketch, "E15.17.16.8", {"start": v(118.09, -63.18) * mm, "end": v(116.51, -60.45) * mm});
            skCircle(sketch, "E15.0.16.9", {"center": v(119.66, -51.82) * mm, "radius": 2.73 * mm, "construction": true});
            skLineSegment(sketch, "E15.2.16.9", {"start": v(116.51, -51.82) * mm, "end": v(118.09, -49.09) * mm});
            skLineSegment(sketch, "E15.5.16.9", {"start": v(118.09, -49.09) * mm, "end": v(121.24, -49.09) * mm});
            skLineSegment(sketch, "E15.8.16.9", {"start": v(121.24, -49.09) * mm, "end": v(122.82, -51.82) * mm});
            skLineSegment(sketch, "E15.11.16.9", {"start": v(122.82, -51.82) * mm, "end": v(121.24, -54.55) * mm});
            skLineSegment(sketch, "E15.14.16.9", {"start": v(121.24, -54.55) * mm, "end": v(118.09, -54.55) * mm});
            skLineSegment(sketch, "E15.17.16.9", {"start": v(118.09, -54.55) * mm, "end": v(116.51, -51.82) * mm});
            skCircle(sketch, "E15.0.16.10", {"center": v(119.66, -43.18) * mm, "radius": 2.73 * mm, "construction": true});
            skLineSegment(sketch, "E15.2.16.10", {"start": v(116.51, -43.18) * mm, "end": v(118.09, -40.45) * mm});
            skLineSegment(sketch, "E15.5.16.10", {"start": v(118.09, -40.45) * mm, "end": v(121.24, -40.45) * mm});
            skLineSegment(sketch, "E15.8.16.10", {"start": v(121.24, -40.45) * mm, "end": v(122.82, -43.18) * mm});
            skLineSegment(sketch, "E15.11.16.10", {"start": v(122.82, -43.18) * mm, "end": v(121.24, -45.91) * mm});
            skLineSegment(sketch, "E15.14.16.10", {"start": v(121.24, -45.91) * mm, "end": v(118.09, -45.91) * mm});
            skLineSegment(sketch, "E15.17.16.10", {"start": v(118.09, -45.91) * mm, "end": v(116.51, -43.18) * mm});
            skCircle(sketch, "E15.0.16.11", {"center": v(119.66, -34.54) * mm, "radius": 2.73 * mm, "construction": true});
            skLineSegment(sketch, "E15.2.16.11", {"start": v(116.51, -34.54) * mm, "end": v(118.09, -31.81) * mm});
            skLineSegment(sketch, "E15.5.16.11", {"start": v(118.09, -31.81) * mm, "end": v(121.24, -31.81) * mm});
            skLineSegment(sketch, "E15.8.16.11", {"start": v(121.24, -31.81) * mm, "end": v(122.82, -34.54) * mm});
            skLineSegment(sketch, "E15.11.16.11", {"start": v(122.82, -34.54) * mm, "end": v(121.24, -37.27) * mm});
            skLineSegment(sketch, "E15.14.16.11", {"start": v(121.24, -37.27) * mm, "end": v(118.09, -37.27) * mm});
            skLineSegment(sketch, "E15.17.16.11", {"start": v(118.09, -37.27) * mm, "end": v(116.51, -34.54) * mm});
            skCircle(sketch, "E15.0.16.12", {"center": v(119.66, -25.9) * mm, "radius": 2.73 * mm, "construction": true});
            skLineSegment(sketch, "E15.2.16.12", {"start": v(116.51, -25.9) * mm, "end": v(118.09, -23.18) * mm});
            skLineSegment(sketch, "E15.5.16.12", {"start": v(118.09, -23.18) * mm, "end": v(121.24, -23.18) * mm});
            skLineSegment(sketch, "E15.8.16.12", {"start": v(121.24, -23.18) * mm, "end": v(122.82, -25.9) * mm});
            skLineSegment(sketch, "E15.11.16.12", {"start": v(122.82, -25.9) * mm, "end": v(121.24, -28.64) * mm});
            skLineSegment(sketch, "E15.14.16.12", {"start": v(121.24, -28.64) * mm, "end": v(118.09, -28.64) * mm});
            skLineSegment(sketch, "E15.17.16.12", {"start": v(118.09, -28.64) * mm, "end": v(116.51, -25.9) * mm});
            skCircle(sketch, "E15.0.16.13", {"center": v(119.66, -17.27) * mm, "radius": 2.73 * mm, "construction": true});
            skLineSegment(sketch, "E15.2.16.13", {"start": v(116.51, -17.27) * mm, "end": v(118.09, -14.54) * mm});
            skLineSegment(sketch, "E15.5.16.13", {"start": v(118.09, -14.54) * mm, "end": v(121.24, -14.54) * mm});
            skLineSegment(sketch, "E15.8.16.13", {"start": v(121.24, -14.54) * mm, "end": v(122.82, -17.27) * mm});
            skLineSegment(sketch, "E15.11.16.13", {"start": v(122.82, -17.27) * mm, "end": v(121.24, -20) * mm});
            skLineSegment(sketch, "E15.14.16.13", {"start": v(121.24, -20) * mm, "end": v(118.09, -20) * mm});
            skLineSegment(sketch, "E15.17.16.13", {"start": v(118.09, -20) * mm, "end": v(116.51, -17.27) * mm});
            skCircle(sketch, "E15.0.16.14", {"center": v(119.66, -8.64) * mm, "radius": 2.73 * mm, "construction": true});
            skLineSegment(sketch, "E15.2.16.14", {"start": v(116.51, -8.64) * mm, "end": v(118.09, -5.9) * mm});
            skLineSegment(sketch, "E15.5.16.14", {"start": v(118.09, -5.9) * mm, "end": v(121.24, -5.9) * mm});
            skLineSegment(sketch, "E15.8.16.14", {"start": v(121.24, -5.9) * mm, "end": v(122.82, -8.64) * mm});
            skLineSegment(sketch, "E15.11.16.14", {"start": v(122.82, -8.64) * mm, "end": v(121.24, -11.37) * mm});
            skLineSegment(sketch, "E15.14.16.14", {"start": v(121.24, -11.37) * mm, "end": v(118.09, -11.37) * mm});
            skLineSegment(sketch, "E15.17.16.14", {"start": v(118.09, -11.37) * mm, "end": v(116.51, -8.64) * mm});
            skCircle(sketch, "E15.0.16.15", {"center": v(119.66, 0) * mm, "radius": 2.73 * mm, "construction": true});
            skLineSegment(sketch, "E15.2.16.15", {"start": v(116.51, 0) * mm, "end": v(118.09, 2.73) * mm});
            skLineSegment(sketch, "E15.5.16.15", {"start": v(118.09, 2.73) * mm, "end": v(121.24, 2.73) * mm});
            skLineSegment(sketch, "E15.8.16.15", {"start": v(121.24, 2.73) * mm, "end": v(122.82, 0) * mm});
            skLineSegment(sketch, "E15.11.16.15", {"start": v(122.82, 0) * mm, "end": v(121.24, -2.73) * mm});
            skLineSegment(sketch, "E15.14.16.15", {"start": v(121.24, -2.73) * mm, "end": v(118.09, -2.73) * mm});
            skLineSegment(sketch, "E15.17.16.15", {"start": v(118.09, -2.73) * mm, "end": v(116.51, 0) * mm});
            skCircle(sketch, "E15.0.16.16", {"center": v(119.66, 8.64) * mm, "radius": 2.73 * mm, "construction": true});
            skLineSegment(sketch, "E15.2.16.16", {"start": v(116.51, 8.64) * mm, "end": v(118.09, 11.37) * mm});
            skLineSegment(sketch, "E15.5.16.16", {"start": v(118.09, 11.37) * mm, "end": v(121.24, 11.37) * mm});
            skLineSegment(sketch, "E15.8.16.16", {"start": v(121.24, 11.37) * mm, "end": v(122.82, 8.64) * mm});
            skLineSegment(sketch, "E15.11.16.16", {"start": v(122.82, 8.64) * mm, "end": v(121.24, 5.9) * mm});
            skLineSegment(sketch, "E15.14.16.16", {"start": v(121.24, 5.9) * mm, "end": v(118.09, 5.9) * mm});
            skLineSegment(sketch, "E15.17.16.16", {"start": v(118.09, 5.9) * mm, "end": v(116.51, 8.64) * mm});
            skCircle(sketch, "E15.0.16.17", {"center": v(119.66, 17.27) * mm, "radius": 2.73 * mm, "construction": true});
            skLineSegment(sketch, "E15.2.16.17", {"start": v(116.51, 17.27) * mm, "end": v(118.09, 20) * mm});
            skLineSegment(sketch, "E15.5.16.17", {"start": v(118.09, 20) * mm, "end": v(121.24, 20) * mm});
            skLineSegment(sketch, "E15.8.16.17", {"start": v(121.24, 20) * mm, "end": v(122.82, 17.27) * mm});
            skLineSegment(sketch, "E15.11.16.17", {"start": v(122.82, 17.27) * mm, "end": v(121.24, 14.54) * mm});
            skLineSegment(sketch, "E15.14.16.17", {"start": v(121.24, 14.54) * mm, "end": v(118.09, 14.54) * mm});
            skLineSegment(sketch, "E15.17.16.17", {"start": v(118.09, 14.54) * mm, "end": v(116.51, 17.27) * mm});
            skCircle(sketch, "E15.0.16.18", {"center": v(119.66, 25.9) * mm, "radius": 2.73 * mm, "construction": true});
            skLineSegment(sketch, "E15.2.16.18", {"start": v(116.51, 25.9) * mm, "end": v(118.09, 28.64) * mm});
            skLineSegment(sketch, "E15.5.16.18", {"start": v(118.09, 28.64) * mm, "end": v(121.24, 28.64) * mm});
            skLineSegment(sketch, "E15.8.16.18", {"start": v(121.24, 28.64) * mm, "end": v(122.82, 25.9) * mm});
            skLineSegment(sketch, "E15.11.16.18", {"start": v(122.82, 25.9) * mm, "end": v(121.24, 23.18) * mm});
            skLineSegment(sketch, "E15.14.16.18", {"start": v(121.24, 23.18) * mm, "end": v(118.09, 23.18) * mm});
            skLineSegment(sketch, "E15.17.16.18", {"start": v(118.09, 23.18) * mm, "end": v(116.51, 25.9) * mm});
            skCircle(sketch, "E15.0.16.19", {"center": v(119.66, 34.54) * mm, "radius": 2.73 * mm, "construction": true});
            skLineSegment(sketch, "E15.2.16.19", {"start": v(116.51, 34.54) * mm, "end": v(118.09, 37.27) * mm});
            skLineSegment(sketch, "E15.5.16.19", {"start": v(118.09, 37.27) * mm, "end": v(121.24, 37.27) * mm});
            skLineSegment(sketch, "E15.8.16.19", {"start": v(121.24, 37.27) * mm, "end": v(122.82, 34.54) * mm});
            skLineSegment(sketch, "E15.11.16.19", {"start": v(122.82, 34.54) * mm, "end": v(121.24, 31.81) * mm});
            skLineSegment(sketch, "E15.14.16.19", {"start": v(121.24, 31.81) * mm, "end": v(118.09, 31.81) * mm});
            skLineSegment(sketch, "E15.17.16.19", {"start": v(118.09, 31.81) * mm, "end": v(116.51, 34.54) * mm});
            skCircle(sketch, "E15.0.17.0", {"center": v(134.62, -129.54) * mm, "radius": 2.73 * mm, "construction": true});
            skLineSegment(sketch, "E15.2.17.0", {"start": v(131.47, -129.54) * mm, "end": v(133.05, -126.8) * mm});
            skLineSegment(sketch, "E15.5.17.0", {"start": v(133.05, -126.8) * mm, "end": v(136.2, -126.8) * mm});
            skLineSegment(sketch, "E15.8.17.0", {"start": v(136.2, -126.8) * mm, "end": v(137.78, -129.54) * mm});
            skLineSegment(sketch, "E15.11.17.0", {"start": v(137.78, -129.54) * mm, "end": v(136.2, -132.27) * mm});
            skLineSegment(sketch, "E15.14.17.0", {"start": v(136.2, -132.27) * mm, "end": v(133.05, -132.27) * mm});
            skLineSegment(sketch, "E15.17.17.0", {"start": v(133.05, -132.27) * mm, "end": v(131.47, -129.54) * mm});
            skCircle(sketch, "E15.0.17.1", {"center": v(134.62, -120.9) * mm, "radius": 2.73 * mm, "construction": true});
            skLineSegment(sketch, "E15.2.17.1", {"start": v(131.47, -120.9) * mm, "end": v(133.05, -118.17) * mm});
            skLineSegment(sketch, "E15.5.17.1", {"start": v(133.05, -118.17) * mm, "end": v(136.2, -118.17) * mm});
            skLineSegment(sketch, "E15.8.17.1", {"start": v(136.2, -118.17) * mm, "end": v(137.78, -120.9) * mm});
            skLineSegment(sketch, "E15.11.17.1", {"start": v(137.78, -120.9) * mm, "end": v(136.2, -123.63) * mm});
            skLineSegment(sketch, "E15.14.17.1", {"start": v(136.2, -123.63) * mm, "end": v(133.05, -123.63) * mm});
            skLineSegment(sketch, "E15.17.17.1", {"start": v(133.05, -123.63) * mm, "end": v(131.47, -120.9) * mm});
            skCircle(sketch, "E15.0.17.2", {"center": v(134.62, -112.27) * mm, "radius": 2.73 * mm, "construction": true});
            skLineSegment(sketch, "E15.2.17.2", {"start": v(131.47, -112.27) * mm, "end": v(133.05, -109.54) * mm});
            skLineSegment(sketch, "E15.5.17.2", {"start": v(133.05, -109.54) * mm, "end": v(136.2, -109.54) * mm});
            skLineSegment(sketch, "E15.8.17.2", {"start": v(136.2, -109.54) * mm, "end": v(137.78, -112.27) * mm});
            skLineSegment(sketch, "E15.11.17.2", {"start": v(137.78, -112.27) * mm, "end": v(136.2, -115) * mm});
            skLineSegment(sketch, "E15.14.17.2", {"start": v(136.2, -115) * mm, "end": v(133.05, -115) * mm});
            skLineSegment(sketch, "E15.17.17.2", {"start": v(133.05, -115) * mm, "end": v(131.47, -112.27) * mm});
            skCircle(sketch, "E15.0.17.3", {"center": v(134.62, -103.63) * mm, "radius": 2.73 * mm, "construction": true});
            skLineSegment(sketch, "E15.2.17.3", {"start": v(131.47, -103.63) * mm, "end": v(133.05, -100.9) * mm});
            skLineSegment(sketch, "E15.5.17.3", {"start": v(133.05, -100.9) * mm, "end": v(136.2, -100.9) * mm});
            skLineSegment(sketch, "E15.8.17.3", {"start": v(136.2, -100.9) * mm, "end": v(137.78, -103.63) * mm});
            skLineSegment(sketch, "E15.11.17.3", {"start": v(137.78, -103.63) * mm, "end": v(136.2, -106.36) * mm});
            skLineSegment(sketch, "E15.14.17.3", {"start": v(136.2, -106.36) * mm, "end": v(133.05, -106.36) * mm});
            skLineSegment(sketch, "E15.17.17.3", {"start": v(133.05, -106.36) * mm, "end": v(131.47, -103.63) * mm});
            skCircle(sketch, "E15.0.17.4", {"center": v(134.62, -95) * mm, "radius": 2.73 * mm, "construction": true});
            skLineSegment(sketch, "E15.2.17.4", {"start": v(131.47, -95) * mm, "end": v(133.05, -92.27) * mm});
            skLineSegment(sketch, "E15.5.17.4", {"start": v(133.05, -92.27) * mm, "end": v(136.2, -92.27) * mm});
            skLineSegment(sketch, "E15.8.17.4", {"start": v(136.2, -92.27) * mm, "end": v(137.78, -95) * mm});
            skLineSegment(sketch, "E15.11.17.4", {"start": v(137.78, -95) * mm, "end": v(136.2, -97.73) * mm});
            skLineSegment(sketch, "E15.14.17.4", {"start": v(136.2, -97.73) * mm, "end": v(133.05, -97.73) * mm});
            skLineSegment(sketch, "E15.17.17.4", {"start": v(133.05, -97.73) * mm, "end": v(131.47, -95) * mm});
            skCircle(sketch, "E15.0.17.5", {"center": v(134.62, -86.36) * mm, "radius": 2.73 * mm, "construction": true});
            skLineSegment(sketch, "E15.2.17.5", {"start": v(131.47, -86.36) * mm, "end": v(133.05, -83.63) * mm});
            skLineSegment(sketch, "E15.5.17.5", {"start": v(133.05, -83.63) * mm, "end": v(136.2, -83.63) * mm});
            skLineSegment(sketch, "E15.8.17.5", {"start": v(136.2, -83.63) * mm, "end": v(137.78, -86.36) * mm});
            skLineSegment(sketch, "E15.11.17.5", {"start": v(137.78, -86.36) * mm, "end": v(136.2, -89.1) * mm});
            skLineSegment(sketch, "E15.14.17.5", {"start": v(136.2, -89.1) * mm, "end": v(133.05, -89.1) * mm});
            skLineSegment(sketch, "E15.17.17.5", {"start": v(133.05, -89.1) * mm, "end": v(131.47, -86.36) * mm});
            skCircle(sketch, "E15.0.17.6", {"center": v(134.62, -77.72) * mm, "radius": 2.73 * mm, "construction": true});
            skLineSegment(sketch, "E15.2.17.6", {"start": v(131.47, -77.72) * mm, "end": v(133.05, -75) * mm});
            skLineSegment(sketch, "E15.5.17.6", {"start": v(133.05, -75) * mm, "end": v(136.2, -75) * mm});
            skLineSegment(sketch, "E15.8.17.6", {"start": v(136.2, -75) * mm, "end": v(137.78, -77.72) * mm});
            skLineSegment(sketch, "E15.11.17.6", {"start": v(137.78, -77.72) * mm, "end": v(136.2, -80.45) * mm});
            skLineSegment(sketch, "E15.14.17.6", {"start": v(136.2, -80.45) * mm, "end": v(133.05, -80.45) * mm});
            skLineSegment(sketch, "E15.17.17.6", {"start": v(133.05, -80.45) * mm, "end": v(131.47, -77.72) * mm});
            skCircle(sketch, "E15.0.17.7", {"center": v(134.62, -69.09) * mm, "radius": 2.73 * mm, "construction": true});
            skLineSegment(sketch, "E15.2.17.7", {"start": v(131.47, -69.09) * mm, "end": v(133.05, -66.36) * mm});
            skLineSegment(sketch, "E15.5.17.7", {"start": v(133.05, -66.36) * mm, "end": v(136.2, -66.36) * mm});
            skLineSegment(sketch, "E15.8.17.7", {"start": v(136.2, -66.36) * mm, "end": v(137.78, -69.09) * mm});
            skLineSegment(sketch, "E15.11.17.7", {"start": v(137.78, -69.09) * mm, "end": v(136.2, -71.82) * mm});
            skLineSegment(sketch, "E15.14.17.7", {"start": v(136.2, -71.82) * mm, "end": v(133.05, -71.82) * mm});
            skLineSegment(sketch, "E15.17.17.7", {"start": v(133.05, -71.82) * mm, "end": v(131.47, -69.09) * mm});
            skCircle(sketch, "E15.0.17.8", {"center": v(134.62, -60.45) * mm, "radius": 2.73 * mm, "construction": true});
            skLineSegment(sketch, "E15.2.17.8", {"start": v(131.47, -60.45) * mm, "end": v(133.05, -57.72) * mm});
            skLineSegment(sketch, "E15.5.17.8", {"start": v(133.05, -57.72) * mm, "end": v(136.2, -57.72) * mm});
            skLineSegment(sketch, "E15.8.17.8", {"start": v(136.2, -57.72) * mm, "end": v(137.78, -60.45) * mm});
            skLineSegment(sketch, "E15.11.17.8", {"start": v(137.78, -60.45) * mm, "end": v(136.2, -63.18) * mm});
            skLineSegment(sketch, "E15.14.17.8", {"start": v(136.2, -63.18) * mm, "end": v(133.05, -63.18) * mm});
            skLineSegment(sketch, "E15.17.17.8", {"start": v(133.05, -63.18) * mm, "end": v(131.47, -60.45) * mm});
            skCircle(sketch, "E15.0.17.9", {"center": v(134.62, -51.82) * mm, "radius": 2.73 * mm, "construction": true});
            skLineSegment(sketch, "E15.2.17.9", {"start": v(131.47, -51.82) * mm, "end": v(133.05, -49.09) * mm});
            skLineSegment(sketch, "E15.5.17.9", {"start": v(133.05, -49.09) * mm, "end": v(136.2, -49.09) * mm});
            skLineSegment(sketch, "E15.8.17.9", {"start": v(136.2, -49.09) * mm, "end": v(137.78, -51.82) * mm});
            skLineSegment(sketch, "E15.11.17.9", {"start": v(137.78, -51.82) * mm, "end": v(136.2, -54.55) * mm});
            skLineSegment(sketch, "E15.14.17.9", {"start": v(136.2, -54.55) * mm, "end": v(133.05, -54.55) * mm});
            skLineSegment(sketch, "E15.17.17.9", {"start": v(133.05, -54.55) * mm, "end": v(131.47, -51.82) * mm});
            skCircle(sketch, "E15.0.17.10", {"center": v(134.62, -43.18) * mm, "radius": 2.73 * mm, "construction": true});
            skLineSegment(sketch, "E15.2.17.10", {"start": v(131.47, -43.18) * mm, "end": v(133.05, -40.45) * mm});
            skLineSegment(sketch, "E15.5.17.10", {"start": v(133.05, -40.45) * mm, "end": v(136.2, -40.45) * mm});
            skLineSegment(sketch, "E15.8.17.10", {"start": v(136.2, -40.45) * mm, "end": v(137.78, -43.18) * mm});
            skLineSegment(sketch, "E15.11.17.10", {"start": v(137.78, -43.18) * mm, "end": v(136.2, -45.91) * mm});
            skLineSegment(sketch, "E15.14.17.10", {"start": v(136.2, -45.91) * mm, "end": v(133.05, -45.91) * mm});
            skLineSegment(sketch, "E15.17.17.10", {"start": v(133.05, -45.91) * mm, "end": v(131.47, -43.18) * mm});
            skCircle(sketch, "E15.0.17.11", {"center": v(134.62, -34.54) * mm, "radius": 2.73 * mm, "construction": true});
            skLineSegment(sketch, "E15.2.17.11", {"start": v(131.47, -34.54) * mm, "end": v(133.05, -31.81) * mm});
            skLineSegment(sketch, "E15.5.17.11", {"start": v(133.05, -31.81) * mm, "end": v(136.2, -31.81) * mm});
            skLineSegment(sketch, "E15.8.17.11", {"start": v(136.2, -31.81) * mm, "end": v(137.78, -34.54) * mm});
            skLineSegment(sketch, "E15.11.17.11", {"start": v(137.78, -34.54) * mm, "end": v(136.2, -37.27) * mm});
            skLineSegment(sketch, "E15.14.17.11", {"start": v(136.2, -37.27) * mm, "end": v(133.05, -37.27) * mm});
            skLineSegment(sketch, "E15.17.17.11", {"start": v(133.05, -37.27) * mm, "end": v(131.47, -34.54) * mm});
            skCircle(sketch, "E15.0.17.12", {"center": v(134.62, -25.9) * mm, "radius": 2.73 * mm, "construction": true});
            skLineSegment(sketch, "E15.2.17.12", {"start": v(131.47, -25.9) * mm, "end": v(133.05, -23.18) * mm});
            skLineSegment(sketch, "E15.5.17.12", {"start": v(133.05, -23.18) * mm, "end": v(136.2, -23.18) * mm});
            skLineSegment(sketch, "E15.8.17.12", {"start": v(136.2, -23.18) * mm, "end": v(137.78, -25.9) * mm});
            skLineSegment(sketch, "E15.11.17.12", {"start": v(137.78, -25.9) * mm, "end": v(136.2, -28.64) * mm});
            skLineSegment(sketch, "E15.14.17.12", {"start": v(136.2, -28.64) * mm, "end": v(133.05, -28.64) * mm});
            skLineSegment(sketch, "E15.17.17.12", {"start": v(133.05, -28.64) * mm, "end": v(131.47, -25.9) * mm});
            skCircle(sketch, "E15.0.17.13", {"center": v(134.62, -17.27) * mm, "radius": 2.73 * mm, "construction": true});
            skLineSegment(sketch, "E15.2.17.13", {"start": v(131.47, -17.27) * mm, "end": v(133.05, -14.54) * mm});
            skLineSegment(sketch, "E15.5.17.13", {"start": v(133.05, -14.54) * mm, "end": v(136.2, -14.54) * mm});
            skLineSegment(sketch, "E15.8.17.13", {"start": v(136.2, -14.54) * mm, "end": v(137.78, -17.27) * mm});
            skLineSegment(sketch, "E15.11.17.13", {"start": v(137.78, -17.27) * mm, "end": v(136.2, -20) * mm});
            skLineSegment(sketch, "E15.14.17.13", {"start": v(136.2, -20) * mm, "end": v(133.05, -20) * mm});
            skLineSegment(sketch, "E15.17.17.13", {"start": v(133.05, -20) * mm, "end": v(131.47, -17.27) * mm});
            skCircle(sketch, "E15.0.17.14", {"center": v(134.62, -8.64) * mm, "radius": 2.73 * mm, "construction": true});
            skLineSegment(sketch, "E15.2.17.14", {"start": v(131.47, -8.64) * mm, "end": v(133.05, -5.9) * mm});
            skLineSegment(sketch, "E15.5.17.14", {"start": v(133.05, -5.9) * mm, "end": v(136.2, -5.9) * mm});
            skLineSegment(sketch, "E15.8.17.14", {"start": v(136.2, -5.9) * mm, "end": v(137.78, -8.64) * mm});
            skLineSegment(sketch, "E15.11.17.14", {"start": v(137.78, -8.64) * mm, "end": v(136.2, -11.37) * mm});
            skLineSegment(sketch, "E15.14.17.14", {"start": v(136.2, -11.37) * mm, "end": v(133.05, -11.37) * mm});
            skLineSegment(sketch, "E15.17.17.14", {"start": v(133.05, -11.37) * mm, "end": v(131.47, -8.64) * mm});
            skCircle(sketch, "E15.0.17.15", {"center": v(134.62, 0) * mm, "radius": 2.73 * mm, "construction": true});
            skLineSegment(sketch, "E15.2.17.15", {"start": v(131.47, 0) * mm, "end": v(133.05, 2.73) * mm});
            skLineSegment(sketch, "E15.5.17.15", {"start": v(133.05, 2.73) * mm, "end": v(136.2, 2.73) * mm});
            skLineSegment(sketch, "E15.8.17.15", {"start": v(136.2, 2.73) * mm, "end": v(137.78, 0) * mm});
            skLineSegment(sketch, "E15.11.17.15", {"start": v(137.78, 0) * mm, "end": v(136.2, -2.73) * mm});
            skLineSegment(sketch, "E15.14.17.15", {"start": v(136.2, -2.73) * mm, "end": v(133.05, -2.73) * mm});
            skLineSegment(sketch, "E15.17.17.15", {"start": v(133.05, -2.73) * mm, "end": v(131.47, 0) * mm});
            skCircle(sketch, "E15.0.17.16", {"center": v(134.62, 8.64) * mm, "radius": 2.73 * mm, "construction": true});
            skLineSegment(sketch, "E15.2.17.16", {"start": v(131.47, 8.64) * mm, "end": v(133.05, 11.37) * mm});
            skLineSegment(sketch, "E15.5.17.16", {"start": v(133.05, 11.37) * mm, "end": v(136.2, 11.37) * mm});
            skLineSegment(sketch, "E15.8.17.16", {"start": v(136.2, 11.37) * mm, "end": v(137.78, 8.64) * mm});
            skLineSegment(sketch, "E15.11.17.16", {"start": v(137.78, 8.64) * mm, "end": v(136.2, 5.9) * mm});
            skLineSegment(sketch, "E15.14.17.16", {"start": v(136.2, 5.9) * mm, "end": v(133.05, 5.9) * mm});
            skLineSegment(sketch, "E15.17.17.16", {"start": v(133.05, 5.9) * mm, "end": v(131.47, 8.64) * mm});
            skCircle(sketch, "E15.0.17.17", {"center": v(134.62, 17.27) * mm, "radius": 2.73 * mm, "construction": true});
            skLineSegment(sketch, "E15.2.17.17", {"start": v(131.47, 17.27) * mm, "end": v(133.05, 20) * mm});
            skLineSegment(sketch, "E15.5.17.17", {"start": v(133.05, 20) * mm, "end": v(136.2, 20) * mm});
            skLineSegment(sketch, "E15.8.17.17", {"start": v(136.2, 20) * mm, "end": v(137.78, 17.27) * mm});
            skLineSegment(sketch, "E15.11.17.17", {"start": v(137.78, 17.27) * mm, "end": v(136.2, 14.54) * mm});
            skLineSegment(sketch, "E15.14.17.17", {"start": v(136.2, 14.54) * mm, "end": v(133.05, 14.54) * mm});
            skLineSegment(sketch, "E15.17.17.17", {"start": v(133.05, 14.54) * mm, "end": v(131.47, 17.27) * mm});
            skCircle(sketch, "E15.0.17.18", {"center": v(134.62, 25.9) * mm, "radius": 2.73 * mm, "construction": true});
            skLineSegment(sketch, "E15.2.17.18", {"start": v(131.47, 25.9) * mm, "end": v(133.05, 28.64) * mm});
            skLineSegment(sketch, "E15.5.17.18", {"start": v(133.05, 28.64) * mm, "end": v(136.2, 28.64) * mm});
            skLineSegment(sketch, "E15.8.17.18", {"start": v(136.2, 28.64) * mm, "end": v(137.78, 25.9) * mm});
            skLineSegment(sketch, "E15.11.17.18", {"start": v(137.78, 25.9) * mm, "end": v(136.2, 23.18) * mm});
            skLineSegment(sketch, "E15.14.17.18", {"start": v(136.2, 23.18) * mm, "end": v(133.05, 23.18) * mm});
            skLineSegment(sketch, "E15.17.17.18", {"start": v(133.05, 23.18) * mm, "end": v(131.47, 25.9) * mm});
            skCircle(sketch, "E15.0.17.19", {"center": v(134.62, 34.54) * mm, "radius": 2.73 * mm, "construction": true});
            skLineSegment(sketch, "E15.2.17.19", {"start": v(131.47, 34.54) * mm, "end": v(133.05, 37.27) * mm});
            skLineSegment(sketch, "E15.5.17.19", {"start": v(133.05, 37.27) * mm, "end": v(136.2, 37.27) * mm});
            skLineSegment(sketch, "E15.8.17.19", {"start": v(136.2, 37.27) * mm, "end": v(137.78, 34.54) * mm});
            skLineSegment(sketch, "E15.11.17.19", {"start": v(137.78, 34.54) * mm, "end": v(136.2, 31.81) * mm});
            skLineSegment(sketch, "E15.14.17.19", {"start": v(136.2, 31.81) * mm, "end": v(133.05, 31.81) * mm});
            skLineSegment(sketch, "E15.17.17.19", {"start": v(133.05, 31.81) * mm, "end": v(131.47, 34.54) * mm});
            skCircle(sketch, "E15.0.18.0", {"center": v(149.58, -129.54) * mm, "radius": 2.73 * mm, "construction": true});
            skLineSegment(sketch, "E15.2.18.0", {"start": v(146.43, -129.54) * mm, "end": v(148, -126.8) * mm});
            skLineSegment(sketch, "E15.5.18.0", {"start": v(148, -126.8) * mm, "end": v(151.16, -126.8) * mm});
            skLineSegment(sketch, "E15.8.18.0", {"start": v(151.16, -126.8) * mm, "end": v(152.73, -129.54) * mm});
            skLineSegment(sketch, "E15.11.18.0", {"start": v(152.73, -129.54) * mm, "end": v(151.16, -132.27) * mm});
            skLineSegment(sketch, "E15.14.18.0", {"start": v(151.16, -132.27) * mm, "end": v(148, -132.27) * mm});
            skLineSegment(sketch, "E15.17.18.0", {"start": v(148, -132.27) * mm, "end": v(146.43, -129.54) * mm});
            skCircle(sketch, "E15.0.18.1", {"center": v(149.58, -120.9) * mm, "radius": 2.73 * mm, "construction": true});
            skLineSegment(sketch, "E15.2.18.1", {"start": v(146.43, -120.9) * mm, "end": v(148, -118.17) * mm});
            skLineSegment(sketch, "E15.5.18.1", {"start": v(148, -118.17) * mm, "end": v(151.16, -118.17) * mm});
            skLineSegment(sketch, "E15.8.18.1", {"start": v(151.16, -118.17) * mm, "end": v(152.73, -120.9) * mm});
            skLineSegment(sketch, "E15.11.18.1", {"start": v(152.73, -120.9) * mm, "end": v(151.16, -123.63) * mm});
            skLineSegment(sketch, "E15.14.18.1", {"start": v(151.16, -123.63) * mm, "end": v(148, -123.63) * mm});
            skLineSegment(sketch, "E15.17.18.1", {"start": v(148, -123.63) * mm, "end": v(146.43, -120.9) * mm});
            skCircle(sketch, "E15.0.18.2", {"center": v(149.58, -112.27) * mm, "radius": 2.73 * mm, "construction": true});
            skLineSegment(sketch, "E15.2.18.2", {"start": v(146.43, -112.27) * mm, "end": v(148, -109.54) * mm});
            skLineSegment(sketch, "E15.5.18.2", {"start": v(148, -109.54) * mm, "end": v(151.16, -109.54) * mm});
            skLineSegment(sketch, "E15.8.18.2", {"start": v(151.16, -109.54) * mm, "end": v(152.73, -112.27) * mm});
            skLineSegment(sketch, "E15.11.18.2", {"start": v(152.73, -112.27) * mm, "end": v(151.16, -115) * mm});
            skLineSegment(sketch, "E15.14.18.2", {"start": v(151.16, -115) * mm, "end": v(148, -115) * mm});
            skLineSegment(sketch, "E15.17.18.2", {"start": v(148, -115) * mm, "end": v(146.43, -112.27) * mm});
            skCircle(sketch, "E15.0.18.3", {"center": v(149.58, -103.63) * mm, "radius": 2.73 * mm, "construction": true});
            skLineSegment(sketch, "E15.2.18.3", {"start": v(146.43, -103.63) * mm, "end": v(148, -100.9) * mm});
            skLineSegment(sketch, "E15.5.18.3", {"start": v(148, -100.9) * mm, "end": v(151.16, -100.9) * mm});
            skLineSegment(sketch, "E15.8.18.3", {"start": v(151.16, -100.9) * mm, "end": v(152.73, -103.63) * mm});
            skLineSegment(sketch, "E15.11.18.3", {"start": v(152.73, -103.63) * mm, "end": v(151.16, -106.36) * mm});
            skLineSegment(sketch, "E15.14.18.3", {"start": v(151.16, -106.36) * mm, "end": v(148, -106.36) * mm});
            skLineSegment(sketch, "E15.17.18.3", {"start": v(148, -106.36) * mm, "end": v(146.43, -103.63) * mm});
            skCircle(sketch, "E15.0.18.4", {"center": v(149.58, -95) * mm, "radius": 2.73 * mm, "construction": true});
            skLineSegment(sketch, "E15.2.18.4", {"start": v(146.43, -95) * mm, "end": v(148, -92.27) * mm});
            skLineSegment(sketch, "E15.5.18.4", {"start": v(148, -92.27) * mm, "end": v(151.16, -92.27) * mm});
            skLineSegment(sketch, "E15.8.18.4", {"start": v(151.16, -92.27) * mm, "end": v(152.73, -95) * mm});
            skLineSegment(sketch, "E15.11.18.4", {"start": v(152.73, -95) * mm, "end": v(151.16, -97.73) * mm});
            skLineSegment(sketch, "E15.14.18.4", {"start": v(151.16, -97.73) * mm, "end": v(148, -97.73) * mm});
            skLineSegment(sketch, "E15.17.18.4", {"start": v(148, -97.73) * mm, "end": v(146.43, -95) * mm});
            skCircle(sketch, "E15.0.18.5", {"center": v(149.58, -86.36) * mm, "radius": 2.73 * mm, "construction": true});
            skLineSegment(sketch, "E15.2.18.5", {"start": v(146.43, -86.36) * mm, "end": v(148, -83.63) * mm});
            skLineSegment(sketch, "E15.5.18.5", {"start": v(148, -83.63) * mm, "end": v(151.16, -83.63) * mm});
            skLineSegment(sketch, "E15.8.18.5", {"start": v(151.16, -83.63) * mm, "end": v(152.73, -86.36) * mm});
            skLineSegment(sketch, "E15.11.18.5", {"start": v(152.73, -86.36) * mm, "end": v(151.16, -89.1) * mm});
            skLineSegment(sketch, "E15.14.18.5", {"start": v(151.16, -89.1) * mm, "end": v(148, -89.1) * mm});
            skLineSegment(sketch, "E15.17.18.5", {"start": v(148, -89.1) * mm, "end": v(146.43, -86.36) * mm});
            skCircle(sketch, "E15.0.18.6", {"center": v(149.58, -77.72) * mm, "radius": 2.73 * mm, "construction": true});
            skLineSegment(sketch, "E15.2.18.6", {"start": v(146.43, -77.72) * mm, "end": v(148, -75) * mm});
            skLineSegment(sketch, "E15.5.18.6", {"start": v(148, -75) * mm, "end": v(151.16, -75) * mm});
            skLineSegment(sketch, "E15.8.18.6", {"start": v(151.16, -75) * mm, "end": v(152.73, -77.72) * mm});
            skLineSegment(sketch, "E15.11.18.6", {"start": v(152.73, -77.72) * mm, "end": v(151.16, -80.45) * mm});
            skLineSegment(sketch, "E15.14.18.6", {"start": v(151.16, -80.45) * mm, "end": v(148, -80.45) * mm});
            skLineSegment(sketch, "E15.17.18.6", {"start": v(148, -80.45) * mm, "end": v(146.43, -77.72) * mm});
            skCircle(sketch, "E15.0.18.7", {"center": v(149.58, -69.09) * mm, "radius": 2.73 * mm, "construction": true});
            skLineSegment(sketch, "E15.2.18.7", {"start": v(146.43, -69.09) * mm, "end": v(148, -66.36) * mm});
            skLineSegment(sketch, "E15.5.18.7", {"start": v(148, -66.36) * mm, "end": v(151.16, -66.36) * mm});
            skLineSegment(sketch, "E15.8.18.7", {"start": v(151.16, -66.36) * mm, "end": v(152.73, -69.09) * mm});
            skLineSegment(sketch, "E15.11.18.7", {"start": v(152.73, -69.09) * mm, "end": v(151.16, -71.82) * mm});
            skLineSegment(sketch, "E15.14.18.7", {"start": v(151.16, -71.82) * mm, "end": v(148, -71.82) * mm});
            skLineSegment(sketch, "E15.17.18.7", {"start": v(148, -71.82) * mm, "end": v(146.43, -69.09) * mm});
            skCircle(sketch, "E15.0.18.8", {"center": v(149.58, -60.45) * mm, "radius": 2.73 * mm, "construction": true});
            skLineSegment(sketch, "E15.2.18.8", {"start": v(146.43, -60.45) * mm, "end": v(148, -57.72) * mm});
            skLineSegment(sketch, "E15.5.18.8", {"start": v(148, -57.72) * mm, "end": v(151.16, -57.72) * mm});
            skLineSegment(sketch, "E15.8.18.8", {"start": v(151.16, -57.72) * mm, "end": v(152.73, -60.45) * mm});
            skLineSegment(sketch, "E15.11.18.8", {"start": v(152.73, -60.45) * mm, "end": v(151.16, -63.18) * mm});
            skLineSegment(sketch, "E15.14.18.8", {"start": v(151.16, -63.18) * mm, "end": v(148, -63.18) * mm});
            skLineSegment(sketch, "E15.17.18.8", {"start": v(148, -63.18) * mm, "end": v(146.43, -60.45) * mm});
            skCircle(sketch, "E15.0.18.9", {"center": v(149.58, -51.82) * mm, "radius": 2.73 * mm, "construction": true});
            skLineSegment(sketch, "E15.2.18.9", {"start": v(146.43, -51.82) * mm, "end": v(148, -49.09) * mm});
            skLineSegment(sketch, "E15.5.18.9", {"start": v(148, -49.09) * mm, "end": v(151.16, -49.09) * mm});
            skLineSegment(sketch, "E15.8.18.9", {"start": v(151.16, -49.09) * mm, "end": v(152.73, -51.82) * mm});
            skLineSegment(sketch, "E15.11.18.9", {"start": v(152.73, -51.82) * mm, "end": v(151.16, -54.55) * mm});
            skLineSegment(sketch, "E15.14.18.9", {"start": v(151.16, -54.55) * mm, "end": v(148, -54.55) * mm});
            skLineSegment(sketch, "E15.17.18.9", {"start": v(148, -54.55) * mm, "end": v(146.43, -51.82) * mm});
            skCircle(sketch, "E15.0.18.10", {"center": v(149.58, -43.18) * mm, "radius": 2.73 * mm, "construction": true});
            skLineSegment(sketch, "E15.2.18.10", {"start": v(146.43, -43.18) * mm, "end": v(148, -40.45) * mm});
            skLineSegment(sketch, "E15.5.18.10", {"start": v(148, -40.45) * mm, "end": v(151.16, -40.45) * mm});
            skLineSegment(sketch, "E15.8.18.10", {"start": v(151.16, -40.45) * mm, "end": v(152.73, -43.18) * mm});
            skLineSegment(sketch, "E15.11.18.10", {"start": v(152.73, -43.18) * mm, "end": v(151.16, -45.91) * mm});
            skLineSegment(sketch, "E15.14.18.10", {"start": v(151.16, -45.91) * mm, "end": v(148, -45.91) * mm});
            skLineSegment(sketch, "E15.17.18.10", {"start": v(148, -45.91) * mm, "end": v(146.43, -43.18) * mm});
            skCircle(sketch, "E15.0.18.11", {"center": v(149.58, -34.54) * mm, "radius": 2.73 * mm, "construction": true});
            skLineSegment(sketch, "E15.2.18.11", {"start": v(146.43, -34.54) * mm, "end": v(148, -31.81) * mm});
            skLineSegment(sketch, "E15.5.18.11", {"start": v(148, -31.81) * mm, "end": v(151.16, -31.81) * mm});
            skLineSegment(sketch, "E15.8.18.11", {"start": v(151.16, -31.81) * mm, "end": v(152.73, -34.54) * mm});
            skLineSegment(sketch, "E15.11.18.11", {"start": v(152.73, -34.54) * mm, "end": v(151.16, -37.27) * mm});
            skLineSegment(sketch, "E15.14.18.11", {"start": v(151.16, -37.27) * mm, "end": v(148, -37.27) * mm});
            skLineSegment(sketch, "E15.17.18.11", {"start": v(148, -37.27) * mm, "end": v(146.43, -34.54) * mm});
            skCircle(sketch, "E15.0.18.12", {"center": v(149.58, -25.9) * mm, "radius": 2.73 * mm, "construction": true});
            skLineSegment(sketch, "E15.2.18.12", {"start": v(146.43, -25.9) * mm, "end": v(148, -23.18) * mm});
            skLineSegment(sketch, "E15.5.18.12", {"start": v(148, -23.18) * mm, "end": v(151.16, -23.18) * mm});
            skLineSegment(sketch, "E15.8.18.12", {"start": v(151.16, -23.18) * mm, "end": v(152.73, -25.9) * mm});
            skLineSegment(sketch, "E15.11.18.12", {"start": v(152.73, -25.9) * mm, "end": v(151.16, -28.64) * mm});
            skLineSegment(sketch, "E15.14.18.12", {"start": v(151.16, -28.64) * mm, "end": v(148, -28.64) * mm});
            skLineSegment(sketch, "E15.17.18.12", {"start": v(148, -28.64) * mm, "end": v(146.43, -25.9) * mm});
            skCircle(sketch, "E15.0.18.13", {"center": v(149.58, -17.27) * mm, "radius": 2.73 * mm, "construction": true});
            skLineSegment(sketch, "E15.2.18.13", {"start": v(146.43, -17.27) * mm, "end": v(148, -14.54) * mm});
            skLineSegment(sketch, "E15.5.18.13", {"start": v(148, -14.54) * mm, "end": v(151.16, -14.54) * mm});
            skLineSegment(sketch, "E15.8.18.13", {"start": v(151.16, -14.54) * mm, "end": v(152.73, -17.27) * mm});
            skLineSegment(sketch, "E15.11.18.13", {"start": v(152.73, -17.27) * mm, "end": v(151.16, -20) * mm});
            skLineSegment(sketch, "E15.14.18.13", {"start": v(151.16, -20) * mm, "end": v(148, -20) * mm});
            skLineSegment(sketch, "E15.17.18.13", {"start": v(148, -20) * mm, "end": v(146.43, -17.27) * mm});
            skCircle(sketch, "E15.0.18.14", {"center": v(149.58, -8.64) * mm, "radius": 2.73 * mm, "construction": true});
            skLineSegment(sketch, "E15.2.18.14", {"start": v(146.43, -8.64) * mm, "end": v(148, -5.9) * mm});
            skLineSegment(sketch, "E15.5.18.14", {"start": v(148, -5.9) * mm, "end": v(151.16, -5.9) * mm});
            skLineSegment(sketch, "E15.8.18.14", {"start": v(151.16, -5.9) * mm, "end": v(152.73, -8.64) * mm});
            skLineSegment(sketch, "E15.11.18.14", {"start": v(152.73, -8.64) * mm, "end": v(151.16, -11.37) * mm});
            skLineSegment(sketch, "E15.14.18.14", {"start": v(151.16, -11.37) * mm, "end": v(148, -11.37) * mm});
            skLineSegment(sketch, "E15.17.18.14", {"start": v(148, -11.37) * mm, "end": v(146.43, -8.64) * mm});
            skCircle(sketch, "E15.0.18.15", {"center": v(149.58, 0) * mm, "radius": 2.73 * mm, "construction": true});
            skLineSegment(sketch, "E15.2.18.15", {"start": v(146.43, 0) * mm, "end": v(148, 2.73) * mm});
            skLineSegment(sketch, "E15.5.18.15", {"start": v(148, 2.73) * mm, "end": v(151.16, 2.73) * mm});
            skLineSegment(sketch, "E15.8.18.15", {"start": v(151.16, 2.73) * mm, "end": v(152.73, 0) * mm});
            skLineSegment(sketch, "E15.11.18.15", {"start": v(152.73, 0) * mm, "end": v(151.16, -2.73) * mm});
            skLineSegment(sketch, "E15.14.18.15", {"start": v(151.16, -2.73) * mm, "end": v(148, -2.73) * mm});
            skLineSegment(sketch, "E15.17.18.15", {"start": v(148, -2.73) * mm, "end": v(146.43, 0) * mm});
            skCircle(sketch, "E15.0.18.16", {"center": v(149.58, 8.64) * mm, "radius": 2.73 * mm, "construction": true});
            skLineSegment(sketch, "E15.2.18.16", {"start": v(146.43, 8.64) * mm, "end": v(148, 11.37) * mm});
            skLineSegment(sketch, "E15.5.18.16", {"start": v(148, 11.37) * mm, "end": v(151.16, 11.37) * mm});
            skLineSegment(sketch, "E15.8.18.16", {"start": v(151.16, 11.37) * mm, "end": v(152.73, 8.64) * mm});
            skLineSegment(sketch, "E15.11.18.16", {"start": v(152.73, 8.64) * mm, "end": v(151.16, 5.9) * mm});
            skLineSegment(sketch, "E15.14.18.16", {"start": v(151.16, 5.9) * mm, "end": v(148, 5.9) * mm});
            skLineSegment(sketch, "E15.17.18.16", {"start": v(148, 5.9) * mm, "end": v(146.43, 8.64) * mm});
            skCircle(sketch, "E15.0.18.17", {"center": v(149.58, 17.27) * mm, "radius": 2.73 * mm, "construction": true});
            skLineSegment(sketch, "E15.2.18.17", {"start": v(146.43, 17.27) * mm, "end": v(148, 20) * mm});
            skLineSegment(sketch, "E15.5.18.17", {"start": v(148, 20) * mm, "end": v(151.16, 20) * mm});
            skLineSegment(sketch, "E15.8.18.17", {"start": v(151.16, 20) * mm, "end": v(152.73, 17.27) * mm});
            skLineSegment(sketch, "E15.11.18.17", {"start": v(152.73, 17.27) * mm, "end": v(151.16, 14.54) * mm});
            skLineSegment(sketch, "E15.14.18.17", {"start": v(151.16, 14.54) * mm, "end": v(148, 14.54) * mm});
            skLineSegment(sketch, "E15.17.18.17", {"start": v(148, 14.54) * mm, "end": v(146.43, 17.27) * mm});
            skCircle(sketch, "E15.0.18.18", {"center": v(149.58, 25.9) * mm, "radius": 2.73 * mm, "construction": true});
            skLineSegment(sketch, "E15.2.18.18", {"start": v(146.43, 25.9) * mm, "end": v(148, 28.64) * mm});
            skLineSegment(sketch, "E15.5.18.18", {"start": v(148, 28.64) * mm, "end": v(151.16, 28.64) * mm});
            skLineSegment(sketch, "E15.8.18.18", {"start": v(151.16, 28.64) * mm, "end": v(152.73, 25.9) * mm});
            skLineSegment(sketch, "E15.11.18.18", {"start": v(152.73, 25.9) * mm, "end": v(151.16, 23.18) * mm});
            skLineSegment(sketch, "E15.14.18.18", {"start": v(151.16, 23.18) * mm, "end": v(148, 23.18) * mm});
            skLineSegment(sketch, "E15.17.18.18", {"start": v(148, 23.18) * mm, "end": v(146.43, 25.9) * mm});
            skCircle(sketch, "E15.0.18.19", {"center": v(149.58, 34.54) * mm, "radius": 2.73 * mm, "construction": true});
            skLineSegment(sketch, "E15.2.18.19", {"start": v(146.43, 34.54) * mm, "end": v(148, 37.27) * mm});
            skLineSegment(sketch, "E15.5.18.19", {"start": v(148, 37.27) * mm, "end": v(151.16, 37.27) * mm});
            skLineSegment(sketch, "E15.8.18.19", {"start": v(151.16, 37.27) * mm, "end": v(152.73, 34.54) * mm});
            skLineSegment(sketch, "E15.11.18.19", {"start": v(152.73, 34.54) * mm, "end": v(151.16, 31.81) * mm});
            skLineSegment(sketch, "E15.14.18.19", {"start": v(151.16, 31.81) * mm, "end": v(148, 31.81) * mm});
            skLineSegment(sketch, "E15.17.18.19", {"start": v(148, 31.81) * mm, "end": v(146.43, 34.54) * mm});
            skCircle(sketch, "E15.0.19.0", {"center": v(164.54, -129.54) * mm, "radius": 2.73 * mm, "construction": true});
            skLineSegment(sketch, "E15.2.19.0", {"start": v(161.39, -129.54) * mm, "end": v(162.96, -126.8) * mm});
            skLineSegment(sketch, "E15.5.19.0", {"start": v(162.96, -126.8) * mm, "end": v(166.12, -126.8) * mm});
            skLineSegment(sketch, "E15.8.19.0", {"start": v(166.12, -126.8) * mm, "end": v(167.7, -129.54) * mm});
            skLineSegment(sketch, "E15.11.19.0", {"start": v(167.7, -129.54) * mm, "end": v(166.12, -132.27) * mm});
            skLineSegment(sketch, "E15.14.19.0", {"start": v(166.12, -132.27) * mm, "end": v(162.96, -132.27) * mm});
            skLineSegment(sketch, "E15.17.19.0", {"start": v(162.96, -132.27) * mm, "end": v(161.39, -129.54) * mm});
            skCircle(sketch, "E15.0.19.1", {"center": v(164.54, -120.9) * mm, "radius": 2.73 * mm, "construction": true});
            skLineSegment(sketch, "E15.2.19.1", {"start": v(161.39, -120.9) * mm, "end": v(162.96, -118.17) * mm});
            skLineSegment(sketch, "E15.5.19.1", {"start": v(162.96, -118.17) * mm, "end": v(166.12, -118.17) * mm});
            skLineSegment(sketch, "E15.8.19.1", {"start": v(166.12, -118.17) * mm, "end": v(167.7, -120.9) * mm});
            skLineSegment(sketch, "E15.11.19.1", {"start": v(167.7, -120.9) * mm, "end": v(166.12, -123.63) * mm});
            skLineSegment(sketch, "E15.14.19.1", {"start": v(166.12, -123.63) * mm, "end": v(162.96, -123.63) * mm});
            skLineSegment(sketch, "E15.17.19.1", {"start": v(162.96, -123.63) * mm, "end": v(161.39, -120.9) * mm});
            skCircle(sketch, "E15.0.19.2", {"center": v(164.54, -112.27) * mm, "radius": 2.73 * mm, "construction": true});
            skLineSegment(sketch, "E15.2.19.2", {"start": v(161.39, -112.27) * mm, "end": v(162.96, -109.54) * mm});
            skLineSegment(sketch, "E15.5.19.2", {"start": v(162.96, -109.54) * mm, "end": v(166.12, -109.54) * mm});
            skLineSegment(sketch, "E15.8.19.2", {"start": v(166.12, -109.54) * mm, "end": v(167.7, -112.27) * mm});
            skLineSegment(sketch, "E15.11.19.2", {"start": v(167.7, -112.27) * mm, "end": v(166.12, -115) * mm});
            skLineSegment(sketch, "E15.14.19.2", {"start": v(166.12, -115) * mm, "end": v(162.96, -115) * mm});
            skLineSegment(sketch, "E15.17.19.2", {"start": v(162.96, -115) * mm, "end": v(161.39, -112.27) * mm});
            skCircle(sketch, "E15.0.19.3", {"center": v(164.54, -103.63) * mm, "radius": 2.73 * mm, "construction": true});
            skLineSegment(sketch, "E15.2.19.3", {"start": v(161.39, -103.63) * mm, "end": v(162.96, -100.9) * mm});
            skLineSegment(sketch, "E15.5.19.3", {"start": v(162.96, -100.9) * mm, "end": v(166.12, -100.9) * mm});
            skLineSegment(sketch, "E15.8.19.3", {"start": v(166.12, -100.9) * mm, "end": v(167.7, -103.63) * mm});
            skLineSegment(sketch, "E15.11.19.3", {"start": v(167.7, -103.63) * mm, "end": v(166.12, -106.36) * mm});
            skLineSegment(sketch, "E15.14.19.3", {"start": v(166.12, -106.36) * mm, "end": v(162.96, -106.36) * mm});
            skLineSegment(sketch, "E15.17.19.3", {"start": v(162.96, -106.36) * mm, "end": v(161.39, -103.63) * mm});
            skCircle(sketch, "E15.0.19.4", {"center": v(164.54, -95) * mm, "radius": 2.73 * mm, "construction": true});
            skLineSegment(sketch, "E15.2.19.4", {"start": v(161.39, -95) * mm, "end": v(162.96, -92.27) * mm});
            skLineSegment(sketch, "E15.5.19.4", {"start": v(162.96, -92.27) * mm, "end": v(166.12, -92.27) * mm});
            skLineSegment(sketch, "E15.8.19.4", {"start": v(166.12, -92.27) * mm, "end": v(167.7, -95) * mm});
            skLineSegment(sketch, "E15.11.19.4", {"start": v(167.7, -95) * mm, "end": v(166.12, -97.73) * mm});
            skLineSegment(sketch, "E15.14.19.4", {"start": v(166.12, -97.73) * mm, "end": v(162.96, -97.73) * mm});
            skLineSegment(sketch, "E15.17.19.4", {"start": v(162.96, -97.73) * mm, "end": v(161.39, -95) * mm});
            skCircle(sketch, "E15.0.19.5", {"center": v(164.54, -86.36) * mm, "radius": 2.73 * mm, "construction": true});
            skLineSegment(sketch, "E15.2.19.5", {"start": v(161.39, -86.36) * mm, "end": v(162.96, -83.63) * mm});
            skLineSegment(sketch, "E15.5.19.5", {"start": v(162.96, -83.63) * mm, "end": v(166.12, -83.63) * mm});
            skLineSegment(sketch, "E15.8.19.5", {"start": v(166.12, -83.63) * mm, "end": v(167.7, -86.36) * mm});
            skLineSegment(sketch, "E15.11.19.5", {"start": v(167.7, -86.36) * mm, "end": v(166.12, -89.1) * mm});
            skLineSegment(sketch, "E15.14.19.5", {"start": v(166.12, -89.1) * mm, "end": v(162.96, -89.1) * mm});
            skLineSegment(sketch, "E15.17.19.5", {"start": v(162.96, -89.1) * mm, "end": v(161.39, -86.36) * mm});
            skCircle(sketch, "E15.0.19.6", {"center": v(164.54, -77.72) * mm, "radius": 2.73 * mm, "construction": true});
            skLineSegment(sketch, "E15.2.19.6", {"start": v(161.39, -77.72) * mm, "end": v(162.96, -75) * mm});
            skLineSegment(sketch, "E15.5.19.6", {"start": v(162.96, -75) * mm, "end": v(166.12, -75) * mm});
            skLineSegment(sketch, "E15.8.19.6", {"start": v(166.12, -75) * mm, "end": v(167.7, -77.72) * mm});
            skLineSegment(sketch, "E15.11.19.6", {"start": v(167.7, -77.72) * mm, "end": v(166.12, -80.45) * mm});
            skLineSegment(sketch, "E15.14.19.6", {"start": v(166.12, -80.45) * mm, "end": v(162.96, -80.45) * mm});
            skLineSegment(sketch, "E15.17.19.6", {"start": v(162.96, -80.45) * mm, "end": v(161.39, -77.72) * mm});
            skCircle(sketch, "E15.0.19.7", {"center": v(164.54, -69.09) * mm, "radius": 2.73 * mm, "construction": true});
            skLineSegment(sketch, "E15.2.19.7", {"start": v(161.39, -69.09) * mm, "end": v(162.96, -66.36) * mm});
            skLineSegment(sketch, "E15.5.19.7", {"start": v(162.96, -66.36) * mm, "end": v(166.12, -66.36) * mm});
            skLineSegment(sketch, "E15.8.19.7", {"start": v(166.12, -66.36) * mm, "end": v(167.7, -69.09) * mm});
            skLineSegment(sketch, "E15.11.19.7", {"start": v(167.7, -69.09) * mm, "end": v(166.12, -71.82) * mm});
            skLineSegment(sketch, "E15.14.19.7", {"start": v(166.12, -71.82) * mm, "end": v(162.96, -71.82) * mm});
            skLineSegment(sketch, "E15.17.19.7", {"start": v(162.96, -71.82) * mm, "end": v(161.39, -69.09) * mm});
            skCircle(sketch, "E15.0.19.8", {"center": v(164.54, -60.45) * mm, "radius": 2.73 * mm, "construction": true});
            skLineSegment(sketch, "E15.2.19.8", {"start": v(161.39, -60.45) * mm, "end": v(162.96, -57.72) * mm});
            skLineSegment(sketch, "E15.5.19.8", {"start": v(162.96, -57.72) * mm, "end": v(166.12, -57.72) * mm});
            skLineSegment(sketch, "E15.8.19.8", {"start": v(166.12, -57.72) * mm, "end": v(167.7, -60.45) * mm});
            skLineSegment(sketch, "E15.11.19.8", {"start": v(167.7, -60.45) * mm, "end": v(166.12, -63.18) * mm});
            skLineSegment(sketch, "E15.14.19.8", {"start": v(166.12, -63.18) * mm, "end": v(162.96, -63.18) * mm});
            skLineSegment(sketch, "E15.17.19.8", {"start": v(162.96, -63.18) * mm, "end": v(161.39, -60.45) * mm});
            skCircle(sketch, "E15.0.19.9", {"center": v(164.54, -51.82) * mm, "radius": 2.73 * mm, "construction": true});
            skLineSegment(sketch, "E15.2.19.9", {"start": v(161.39, -51.82) * mm, "end": v(162.96, -49.09) * mm});
            skLineSegment(sketch, "E15.5.19.9", {"start": v(162.96, -49.09) * mm, "end": v(166.12, -49.09) * mm});
            skLineSegment(sketch, "E15.8.19.9", {"start": v(166.12, -49.09) * mm, "end": v(167.7, -51.82) * mm});
            skLineSegment(sketch, "E15.11.19.9", {"start": v(167.7, -51.82) * mm, "end": v(166.12, -54.55) * mm});
            skLineSegment(sketch, "E15.14.19.9", {"start": v(166.12, -54.55) * mm, "end": v(162.96, -54.55) * mm});
            skLineSegment(sketch, "E15.17.19.9", {"start": v(162.96, -54.55) * mm, "end": v(161.39, -51.82) * mm});
            skCircle(sketch, "E15.0.19.10", {"center": v(164.54, -43.18) * mm, "radius": 2.73 * mm, "construction": true});
            skLineSegment(sketch, "E15.2.19.10", {"start": v(161.39, -43.18) * mm, "end": v(162.96, -40.45) * mm});
            skLineSegment(sketch, "E15.5.19.10", {"start": v(162.96, -40.45) * mm, "end": v(166.12, -40.45) * mm});
            skLineSegment(sketch, "E15.8.19.10", {"start": v(166.12, -40.45) * mm, "end": v(167.7, -43.18) * mm});
            skLineSegment(sketch, "E15.11.19.10", {"start": v(167.7, -43.18) * mm, "end": v(166.12, -45.91) * mm});
            skLineSegment(sketch, "E15.14.19.10", {"start": v(166.12, -45.91) * mm, "end": v(162.96, -45.91) * mm});
            skLineSegment(sketch, "E15.17.19.10", {"start": v(162.96, -45.91) * mm, "end": v(161.39, -43.18) * mm});
            skCircle(sketch, "E15.0.19.11", {"center": v(164.54, -34.54) * mm, "radius": 2.73 * mm, "construction": true});
            skLineSegment(sketch, "E15.2.19.11", {"start": v(161.39, -34.54) * mm, "end": v(162.96, -31.81) * mm});
            skLineSegment(sketch, "E15.5.19.11", {"start": v(162.96, -31.81) * mm, "end": v(166.12, -31.81) * mm});
            skLineSegment(sketch, "E15.8.19.11", {"start": v(166.12, -31.81) * mm, "end": v(167.7, -34.54) * mm});
            skLineSegment(sketch, "E15.11.19.11", {"start": v(167.7, -34.54) * mm, "end": v(166.12, -37.27) * mm});
            skLineSegment(sketch, "E15.14.19.11", {"start": v(166.12, -37.27) * mm, "end": v(162.96, -37.27) * mm});
            skLineSegment(sketch, "E15.17.19.11", {"start": v(162.96, -37.27) * mm, "end": v(161.39, -34.54) * mm});
            skCircle(sketch, "E15.0.19.12", {"center": v(164.54, -25.9) * mm, "radius": 2.73 * mm, "construction": true});
            skLineSegment(sketch, "E15.2.19.12", {"start": v(161.39, -25.9) * mm, "end": v(162.96, -23.18) * mm});
            skLineSegment(sketch, "E15.5.19.12", {"start": v(162.96, -23.18) * mm, "end": v(166.12, -23.18) * mm});
            skLineSegment(sketch, "E15.8.19.12", {"start": v(166.12, -23.18) * mm, "end": v(167.7, -25.9) * mm});
            skLineSegment(sketch, "E15.11.19.12", {"start": v(167.7, -25.9) * mm, "end": v(166.12, -28.64) * mm});
            skLineSegment(sketch, "E15.14.19.12", {"start": v(166.12, -28.64) * mm, "end": v(162.96, -28.64) * mm});
            skLineSegment(sketch, "E15.17.19.12", {"start": v(162.96, -28.64) * mm, "end": v(161.39, -25.9) * mm});
            skCircle(sketch, "E15.0.19.13", {"center": v(164.54, -17.27) * mm, "radius": 2.73 * mm, "construction": true});
            skLineSegment(sketch, "E15.2.19.13", {"start": v(161.39, -17.27) * mm, "end": v(162.96, -14.54) * mm});
            skLineSegment(sketch, "E15.5.19.13", {"start": v(162.96, -14.54) * mm, "end": v(166.12, -14.54) * mm});
            skLineSegment(sketch, "E15.8.19.13", {"start": v(166.12, -14.54) * mm, "end": v(167.7, -17.27) * mm});
            skLineSegment(sketch, "E15.11.19.13", {"start": v(167.7, -17.27) * mm, "end": v(166.12, -20) * mm});
            skLineSegment(sketch, "E15.14.19.13", {"start": v(166.12, -20) * mm, "end": v(162.96, -20) * mm});
            skLineSegment(sketch, "E15.17.19.13", {"start": v(162.96, -20) * mm, "end": v(161.39, -17.27) * mm});
            skCircle(sketch, "E15.0.19.14", {"center": v(164.54, -8.64) * mm, "radius": 2.73 * mm, "construction": true});
            skLineSegment(sketch, "E15.2.19.14", {"start": v(161.39, -8.64) * mm, "end": v(162.96, -5.9) * mm});
            skLineSegment(sketch, "E15.5.19.14", {"start": v(162.96, -5.9) * mm, "end": v(166.12, -5.9) * mm});
            skLineSegment(sketch, "E15.8.19.14", {"start": v(166.12, -5.9) * mm, "end": v(167.7, -8.64) * mm});
            skLineSegment(sketch, "E15.11.19.14", {"start": v(167.7, -8.64) * mm, "end": v(166.12, -11.37) * mm});
            skLineSegment(sketch, "E15.14.19.14", {"start": v(166.12, -11.37) * mm, "end": v(162.96, -11.37) * mm});
            skLineSegment(sketch, "E15.17.19.14", {"start": v(162.96, -11.37) * mm, "end": v(161.39, -8.64) * mm});
            skCircle(sketch, "E15.0.19.15", {"center": v(164.54, 0) * mm, "radius": 2.73 * mm, "construction": true});
            skLineSegment(sketch, "E15.2.19.15", {"start": v(161.39, 0) * mm, "end": v(162.96, 2.73) * mm});
            skLineSegment(sketch, "E15.5.19.15", {"start": v(162.96, 2.73) * mm, "end": v(166.12, 2.73) * mm});
            skLineSegment(sketch, "E15.8.19.15", {"start": v(166.12, 2.73) * mm, "end": v(167.7, 0) * mm});
            skLineSegment(sketch, "E15.11.19.15", {"start": v(167.7, 0) * mm, "end": v(166.12, -2.73) * mm});
            skLineSegment(sketch, "E15.14.19.15", {"start": v(166.12, -2.73) * mm, "end": v(162.96, -2.73) * mm});
            skLineSegment(sketch, "E15.17.19.15", {"start": v(162.96, -2.73) * mm, "end": v(161.39, 0) * mm});
            skCircle(sketch, "E15.0.19.16", {"center": v(164.54, 8.64) * mm, "radius": 2.73 * mm, "construction": true});
            skLineSegment(sketch, "E15.2.19.16", {"start": v(161.39, 8.64) * mm, "end": v(162.96, 11.37) * mm});
            skLineSegment(sketch, "E15.5.19.16", {"start": v(162.96, 11.37) * mm, "end": v(166.12, 11.37) * mm});
            skLineSegment(sketch, "E15.8.19.16", {"start": v(166.12, 11.37) * mm, "end": v(167.7, 8.64) * mm});
            skLineSegment(sketch, "E15.11.19.16", {"start": v(167.7, 8.64) * mm, "end": v(166.12, 5.9) * mm});
            skLineSegment(sketch, "E15.14.19.16", {"start": v(166.12, 5.9) * mm, "end": v(162.96, 5.9) * mm});
            skLineSegment(sketch, "E15.17.19.16", {"start": v(162.96, 5.9) * mm, "end": v(161.39, 8.64) * mm});
            skCircle(sketch, "E15.0.19.17", {"center": v(164.54, 17.27) * mm, "radius": 2.73 * mm, "construction": true});
            skLineSegment(sketch, "E15.2.19.17", {"start": v(161.39, 17.27) * mm, "end": v(162.96, 20) * mm});
            skLineSegment(sketch, "E15.5.19.17", {"start": v(162.96, 20) * mm, "end": v(166.12, 20) * mm});
            skLineSegment(sketch, "E15.8.19.17", {"start": v(166.12, 20) * mm, "end": v(167.7, 17.27) * mm});
            skLineSegment(sketch, "E15.11.19.17", {"start": v(167.7, 17.27) * mm, "end": v(166.12, 14.54) * mm});
            skLineSegment(sketch, "E15.14.19.17", {"start": v(166.12, 14.54) * mm, "end": v(162.96, 14.54) * mm});
            skLineSegment(sketch, "E15.17.19.17", {"start": v(162.96, 14.54) * mm, "end": v(161.39, 17.27) * mm});
            skCircle(sketch, "E15.0.19.18", {"center": v(164.54, 25.9) * mm, "radius": 2.73 * mm, "construction": true});
            skLineSegment(sketch, "E15.2.19.18", {"start": v(161.39, 25.9) * mm, "end": v(162.96, 28.64) * mm});
            skLineSegment(sketch, "E15.5.19.18", {"start": v(162.96, 28.64) * mm, "end": v(166.12, 28.64) * mm});
            skLineSegment(sketch, "E15.8.19.18", {"start": v(166.12, 28.64) * mm, "end": v(167.7, 25.9) * mm});
            skLineSegment(sketch, "E15.11.19.18", {"start": v(167.7, 25.9) * mm, "end": v(166.12, 23.18) * mm});
            skLineSegment(sketch, "E15.14.19.18", {"start": v(166.12, 23.18) * mm, "end": v(162.96, 23.18) * mm});
            skLineSegment(sketch, "E15.17.19.18", {"start": v(162.96, 23.18) * mm, "end": v(161.39, 25.9) * mm});
            skCircle(sketch, "E15.0.19.19", {"center": v(164.54, 34.54) * mm, "radius": 2.73 * mm, "construction": true});
            skLineSegment(sketch, "E15.2.19.19", {"start": v(161.39, 34.54) * mm, "end": v(162.96, 37.27) * mm});
            skLineSegment(sketch, "E15.5.19.19", {"start": v(162.96, 37.27) * mm, "end": v(166.12, 37.27) * mm});
            skLineSegment(sketch, "E15.8.19.19", {"start": v(166.12, 37.27) * mm, "end": v(167.7, 34.54) * mm});
            skLineSegment(sketch, "E15.11.19.19", {"start": v(167.7, 34.54) * mm, "end": v(166.12, 31.81) * mm});
            skLineSegment(sketch, "E15.14.19.19", {"start": v(166.12, 31.81) * mm, "end": v(162.96, 31.81) * mm});
            skLineSegment(sketch, "E15.17.19.19", {"start": v(162.96, 31.81) * mm, "end": v(161.39, 34.54) * mm});
            skCircle(sketch, "E16.0.0.20", {"center": v(-119.66, 43.18) * mm, "radius": 2.73 * mm, "construction": true});
            skLineSegment(sketch, "E16.2.0.20", {"start": v(-122.82, 43.18) * mm, "end": v(-121.24, 45.91) * mm});
            skLineSegment(sketch, "E16.5.0.20", {"start": v(-121.24, 45.91) * mm, "end": v(-118.09, 45.91) * mm});
            skLineSegment(sketch, "E16.8.0.20", {"start": v(-118.09, 45.91) * mm, "end": v(-116.51, 43.18) * mm});
            skLineSegment(sketch, "E16.11.0.20", {"start": v(-116.51, 43.18) * mm, "end": v(-118.09, 40.45) * mm});
            skLineSegment(sketch, "E16.14.0.20", {"start": v(-118.09, 40.45) * mm, "end": v(-121.24, 40.45) * mm});
            skLineSegment(sketch, "E16.17.0.20", {"start": v(-121.24, 40.45) * mm, "end": v(-122.82, 43.18) * mm});
            skCircle(sketch, "E16.0.0.21", {"center": v(-119.66, 51.82) * mm, "radius": 2.73 * mm, "construction": true});
            skLineSegment(sketch, "E16.2.0.21", {"start": v(-122.82, 51.82) * mm, "end": v(-121.24, 54.55) * mm});
            skLineSegment(sketch, "E16.5.0.21", {"start": v(-121.24, 54.55) * mm, "end": v(-118.09, 54.55) * mm});
            skLineSegment(sketch, "E16.8.0.21", {"start": v(-118.09, 54.55) * mm, "end": v(-116.51, 51.82) * mm});
            skLineSegment(sketch, "E16.11.0.21", {"start": v(-116.51, 51.82) * mm, "end": v(-118.09, 49.09) * mm});
            skLineSegment(sketch, "E16.14.0.21", {"start": v(-118.09, 49.09) * mm, "end": v(-121.24, 49.09) * mm});
            skLineSegment(sketch, "E16.17.0.21", {"start": v(-121.24, 49.09) * mm, "end": v(-122.82, 51.82) * mm});
            skCircle(sketch, "E16.0.0.22", {"center": v(-119.66, 60.45) * mm, "radius": 2.73 * mm, "construction": true});
            skLineSegment(sketch, "E16.2.0.22", {"start": v(-122.82, 60.45) * mm, "end": v(-121.24, 63.18) * mm});
            skLineSegment(sketch, "E16.5.0.22", {"start": v(-121.24, 63.18) * mm, "end": v(-118.09, 63.18) * mm});
            skLineSegment(sketch, "E16.8.0.22", {"start": v(-118.09, 63.18) * mm, "end": v(-116.51, 60.45) * mm});
            skLineSegment(sketch, "E16.11.0.22", {"start": v(-116.51, 60.45) * mm, "end": v(-118.09, 57.72) * mm});
            skLineSegment(sketch, "E16.14.0.22", {"start": v(-118.09, 57.72) * mm, "end": v(-121.24, 57.72) * mm});
            skLineSegment(sketch, "E16.17.0.22", {"start": v(-121.24, 57.72) * mm, "end": v(-122.82, 60.45) * mm});
            skCircle(sketch, "E16.0.0.23", {"center": v(-119.66, 69.09) * mm, "radius": 2.73 * mm, "construction": true});
            skLineSegment(sketch, "E16.2.0.23", {"start": v(-122.82, 69.09) * mm, "end": v(-121.24, 71.82) * mm});
            skLineSegment(sketch, "E16.5.0.23", {"start": v(-121.24, 71.82) * mm, "end": v(-118.09, 71.82) * mm});
            skLineSegment(sketch, "E16.8.0.23", {"start": v(-118.09, 71.82) * mm, "end": v(-116.51, 69.09) * mm});
            skLineSegment(sketch, "E16.11.0.23", {"start": v(-116.51, 69.09) * mm, "end": v(-118.09, 66.36) * mm});
            skLineSegment(sketch, "E16.14.0.23", {"start": v(-118.09, 66.36) * mm, "end": v(-121.24, 66.36) * mm});
            skLineSegment(sketch, "E16.17.0.23", {"start": v(-121.24, 66.36) * mm, "end": v(-122.82, 69.09) * mm});
            skCircle(sketch, "E16.0.0.24", {"center": v(-119.66, 77.72) * mm, "radius": 2.73 * mm, "construction": true});
            skLineSegment(sketch, "E16.2.0.24", {"start": v(-122.82, 77.72) * mm, "end": v(-121.24, 80.45) * mm});
            skLineSegment(sketch, "E16.5.0.24", {"start": v(-121.24, 80.45) * mm, "end": v(-118.09, 80.45) * mm});
            skLineSegment(sketch, "E16.8.0.24", {"start": v(-118.09, 80.45) * mm, "end": v(-116.51, 77.72) * mm});
            skLineSegment(sketch, "E16.11.0.24", {"start": v(-116.51, 77.72) * mm, "end": v(-118.09, 75) * mm});
            skLineSegment(sketch, "E16.14.0.24", {"start": v(-118.09, 75) * mm, "end": v(-121.24, 75) * mm});
            skLineSegment(sketch, "E16.17.0.24", {"start": v(-121.24, 75) * mm, "end": v(-122.82, 77.72) * mm});
            skCircle(sketch, "E16.0.1.20", {"center": v(-104.7, 43.18) * mm, "radius": 2.73 * mm, "construction": true});
            skLineSegment(sketch, "E16.2.1.20", {"start": v(-107.86, 43.18) * mm, "end": v(-106.28, 45.91) * mm});
            skLineSegment(sketch, "E16.5.1.20", {"start": v(-106.28, 45.91) * mm, "end": v(-103.13, 45.91) * mm});
            skLineSegment(sketch, "E16.8.1.20", {"start": v(-103.13, 45.91) * mm, "end": v(-101.55, 43.18) * mm});
            skLineSegment(sketch, "E16.11.1.20", {"start": v(-101.55, 43.18) * mm, "end": v(-103.13, 40.45) * mm});
            skLineSegment(sketch, "E16.14.1.20", {"start": v(-103.13, 40.45) * mm, "end": v(-106.28, 40.45) * mm});
            skLineSegment(sketch, "E16.17.1.20", {"start": v(-106.28, 40.45) * mm, "end": v(-107.86, 43.18) * mm});
            skCircle(sketch, "E16.0.1.21", {"center": v(-104.7, 51.82) * mm, "radius": 2.73 * mm, "construction": true});
            skLineSegment(sketch, "E16.2.1.21", {"start": v(-107.86, 51.82) * mm, "end": v(-106.28, 54.55) * mm});
            skLineSegment(sketch, "E16.5.1.21", {"start": v(-106.28, 54.55) * mm, "end": v(-103.13, 54.55) * mm});
            skLineSegment(sketch, "E16.8.1.21", {"start": v(-103.13, 54.55) * mm, "end": v(-101.55, 51.82) * mm});
            skLineSegment(sketch, "E16.11.1.21", {"start": v(-101.55, 51.82) * mm, "end": v(-103.13, 49.09) * mm});
            skLineSegment(sketch, "E16.14.1.21", {"start": v(-103.13, 49.09) * mm, "end": v(-106.28, 49.09) * mm});
            skLineSegment(sketch, "E16.17.1.21", {"start": v(-106.28, 49.09) * mm, "end": v(-107.86, 51.82) * mm});
            skCircle(sketch, "E16.0.1.22", {"center": v(-104.7, 60.45) * mm, "radius": 2.73 * mm, "construction": true});
            skLineSegment(sketch, "E16.2.1.22", {"start": v(-107.86, 60.45) * mm, "end": v(-106.28, 63.18) * mm});
            skLineSegment(sketch, "E16.5.1.22", {"start": v(-106.28, 63.18) * mm, "end": v(-103.13, 63.18) * mm});
            skLineSegment(sketch, "E16.8.1.22", {"start": v(-103.13, 63.18) * mm, "end": v(-101.55, 60.45) * mm});
            skLineSegment(sketch, "E16.11.1.22", {"start": v(-101.55, 60.45) * mm, "end": v(-103.13, 57.72) * mm});
            skLineSegment(sketch, "E16.14.1.22", {"start": v(-103.13, 57.72) * mm, "end": v(-106.28, 57.72) * mm});
            skLineSegment(sketch, "E16.17.1.22", {"start": v(-106.28, 57.72) * mm, "end": v(-107.86, 60.45) * mm});
            skCircle(sketch, "E16.0.1.23", {"center": v(-104.7, 69.09) * mm, "radius": 2.73 * mm, "construction": true});
            skLineSegment(sketch, "E16.2.1.23", {"start": v(-107.86, 69.09) * mm, "end": v(-106.28, 71.82) * mm});
            skLineSegment(sketch, "E16.5.1.23", {"start": v(-106.28, 71.82) * mm, "end": v(-103.13, 71.82) * mm});
            skLineSegment(sketch, "E16.8.1.23", {"start": v(-103.13, 71.82) * mm, "end": v(-101.55, 69.09) * mm});
            skLineSegment(sketch, "E16.11.1.23", {"start": v(-101.55, 69.09) * mm, "end": v(-103.13, 66.36) * mm});
            skLineSegment(sketch, "E16.14.1.23", {"start": v(-103.13, 66.36) * mm, "end": v(-106.28, 66.36) * mm});
            skLineSegment(sketch, "E16.17.1.23", {"start": v(-106.28, 66.36) * mm, "end": v(-107.86, 69.09) * mm});
            skCircle(sketch, "E16.0.1.24", {"center": v(-104.7, 77.72) * mm, "radius": 2.73 * mm, "construction": true});
            skLineSegment(sketch, "E16.2.1.24", {"start": v(-107.86, 77.72) * mm, "end": v(-106.28, 80.45) * mm});
            skLineSegment(sketch, "E16.5.1.24", {"start": v(-106.28, 80.45) * mm, "end": v(-103.13, 80.45) * mm});
            skLineSegment(sketch, "E16.8.1.24", {"start": v(-103.13, 80.45) * mm, "end": v(-101.55, 77.72) * mm});
            skLineSegment(sketch, "E16.11.1.24", {"start": v(-101.55, 77.72) * mm, "end": v(-103.13, 75) * mm});
            skLineSegment(sketch, "E16.14.1.24", {"start": v(-103.13, 75) * mm, "end": v(-106.28, 75) * mm});
            skLineSegment(sketch, "E16.17.1.24", {"start": v(-106.28, 75) * mm, "end": v(-107.86, 77.72) * mm});
            skCircle(sketch, "E16.0.2.20", {"center": v(-89.75, 43.18) * mm, "radius": 2.73 * mm, "construction": true});
            skLineSegment(sketch, "E16.2.2.20", {"start": v(-92.9, 43.18) * mm, "end": v(-91.32, 45.91) * mm});
            skLineSegment(sketch, "E16.5.2.20", {"start": v(-91.32, 45.91) * mm, "end": v(-88.17, 45.91) * mm});
            skLineSegment(sketch, "E16.8.2.20", {"start": v(-88.17, 45.91) * mm, "end": v(-86.6, 43.18) * mm});
            skLineSegment(sketch, "E16.11.2.20", {"start": v(-86.6, 43.18) * mm, "end": v(-88.17, 40.45) * mm});
            skLineSegment(sketch, "E16.14.2.20", {"start": v(-88.17, 40.45) * mm, "end": v(-91.32, 40.45) * mm});
            skLineSegment(sketch, "E16.17.2.20", {"start": v(-91.32, 40.45) * mm, "end": v(-92.9, 43.18) * mm});
            skCircle(sketch, "E16.0.2.21", {"center": v(-89.75, 51.82) * mm, "radius": 2.73 * mm, "construction": true});
            skLineSegment(sketch, "E16.2.2.21", {"start": v(-92.9, 51.82) * mm, "end": v(-91.32, 54.55) * mm});
            skLineSegment(sketch, "E16.5.2.21", {"start": v(-91.32, 54.55) * mm, "end": v(-88.17, 54.55) * mm});
            skLineSegment(sketch, "E16.8.2.21", {"start": v(-88.17, 54.55) * mm, "end": v(-86.6, 51.82) * mm});
            skLineSegment(sketch, "E16.11.2.21", {"start": v(-86.6, 51.82) * mm, "end": v(-88.17, 49.09) * mm});
            skLineSegment(sketch, "E16.14.2.21", {"start": v(-88.17, 49.09) * mm, "end": v(-91.32, 49.09) * mm});
            skLineSegment(sketch, "E16.17.2.21", {"start": v(-91.32, 49.09) * mm, "end": v(-92.9, 51.82) * mm});
            skCircle(sketch, "E16.0.2.22", {"center": v(-89.75, 60.45) * mm, "radius": 2.73 * mm, "construction": true});
            skLineSegment(sketch, "E16.2.2.22", {"start": v(-92.9, 60.45) * mm, "end": v(-91.32, 63.18) * mm});
            skLineSegment(sketch, "E16.5.2.22", {"start": v(-91.32, 63.18) * mm, "end": v(-88.17, 63.18) * mm});
            skLineSegment(sketch, "E16.8.2.22", {"start": v(-88.17, 63.18) * mm, "end": v(-86.6, 60.45) * mm});
            skLineSegment(sketch, "E16.11.2.22", {"start": v(-86.6, 60.45) * mm, "end": v(-88.17, 57.72) * mm});
            skLineSegment(sketch, "E16.14.2.22", {"start": v(-88.17, 57.72) * mm, "end": v(-91.32, 57.72) * mm});
            skLineSegment(sketch, "E16.17.2.22", {"start": v(-91.32, 57.72) * mm, "end": v(-92.9, 60.45) * mm});
            skCircle(sketch, "E16.0.2.23", {"center": v(-89.75, 69.09) * mm, "radius": 2.73 * mm, "construction": true});
            skLineSegment(sketch, "E16.2.2.23", {"start": v(-92.9, 69.09) * mm, "end": v(-91.32, 71.82) * mm});
            skLineSegment(sketch, "E16.5.2.23", {"start": v(-91.32, 71.82) * mm, "end": v(-88.17, 71.82) * mm});
            skLineSegment(sketch, "E16.8.2.23", {"start": v(-88.17, 71.82) * mm, "end": v(-86.6, 69.09) * mm});
            skLineSegment(sketch, "E16.11.2.23", {"start": v(-86.6, 69.09) * mm, "end": v(-88.17, 66.36) * mm});
            skLineSegment(sketch, "E16.14.2.23", {"start": v(-88.17, 66.36) * mm, "end": v(-91.32, 66.36) * mm});
            skLineSegment(sketch, "E16.17.2.23", {"start": v(-91.32, 66.36) * mm, "end": v(-92.9, 69.09) * mm});
            skCircle(sketch, "E16.0.2.24", {"center": v(-89.75, 77.72) * mm, "radius": 2.73 * mm, "construction": true});
            skLineSegment(sketch, "E16.2.2.24", {"start": v(-92.9, 77.72) * mm, "end": v(-91.32, 80.45) * mm});
            skLineSegment(sketch, "E16.5.2.24", {"start": v(-91.32, 80.45) * mm, "end": v(-88.17, 80.45) * mm});
            skLineSegment(sketch, "E16.8.2.24", {"start": v(-88.17, 80.45) * mm, "end": v(-86.6, 77.72) * mm});
            skLineSegment(sketch, "E16.11.2.24", {"start": v(-86.6, 77.72) * mm, "end": v(-88.17, 75) * mm});
            skLineSegment(sketch, "E16.14.2.24", {"start": v(-88.17, 75) * mm, "end": v(-91.32, 75) * mm});
            skLineSegment(sketch, "E16.17.2.24", {"start": v(-91.32, 75) * mm, "end": v(-92.9, 77.72) * mm});
            skCircle(sketch, "E16.0.3.20", {"center": v(-74.8, 43.18) * mm, "radius": 2.73 * mm, "construction": true});
            skLineSegment(sketch, "E16.2.3.20", {"start": v(-77.94, 43.18) * mm, "end": v(-76.37, 45.91) * mm});
            skLineSegment(sketch, "E16.5.3.20", {"start": v(-76.37, 45.91) * mm, "end": v(-73.21, 45.91) * mm});
            skLineSegment(sketch, "E16.8.3.20", {"start": v(-73.21, 45.91) * mm, "end": v(-71.64, 43.18) * mm});
            skLineSegment(sketch, "E16.11.3.20", {"start": v(-71.64, 43.18) * mm, "end": v(-73.21, 40.45) * mm});
            skLineSegment(sketch, "E16.14.3.20", {"start": v(-73.21, 40.45) * mm, "end": v(-76.37, 40.45) * mm});
            skLineSegment(sketch, "E16.17.3.20", {"start": v(-76.37, 40.45) * mm, "end": v(-77.94, 43.18) * mm});
            skCircle(sketch, "E16.0.3.21", {"center": v(-74.8, 51.82) * mm, "radius": 2.73 * mm, "construction": true});
            skLineSegment(sketch, "E16.2.3.21", {"start": v(-77.94, 51.82) * mm, "end": v(-76.37, 54.55) * mm});
            skLineSegment(sketch, "E16.5.3.21", {"start": v(-76.37, 54.55) * mm, "end": v(-73.21, 54.55) * mm});
            skLineSegment(sketch, "E16.8.3.21", {"start": v(-73.21, 54.55) * mm, "end": v(-71.64, 51.82) * mm});
            skLineSegment(sketch, "E16.11.3.21", {"start": v(-71.64, 51.82) * mm, "end": v(-73.21, 49.09) * mm});
            skLineSegment(sketch, "E16.14.3.21", {"start": v(-73.21, 49.09) * mm, "end": v(-76.37, 49.09) * mm});
            skLineSegment(sketch, "E16.17.3.21", {"start": v(-76.37, 49.09) * mm, "end": v(-77.94, 51.82) * mm});
            skCircle(sketch, "E16.0.3.22", {"center": v(-74.8, 60.45) * mm, "radius": 2.73 * mm, "construction": true});
            skLineSegment(sketch, "E16.2.3.22", {"start": v(-77.94, 60.45) * mm, "end": v(-76.37, 63.18) * mm});
            skLineSegment(sketch, "E16.5.3.22", {"start": v(-76.37, 63.18) * mm, "end": v(-73.21, 63.18) * mm});
            skLineSegment(sketch, "E16.8.3.22", {"start": v(-73.21, 63.18) * mm, "end": v(-71.64, 60.45) * mm});
            skLineSegment(sketch, "E16.11.3.22", {"start": v(-71.64, 60.45) * mm, "end": v(-73.21, 57.72) * mm});
            skLineSegment(sketch, "E16.14.3.22", {"start": v(-73.21, 57.72) * mm, "end": v(-76.37, 57.72) * mm});
            skLineSegment(sketch, "E16.17.3.22", {"start": v(-76.37, 57.72) * mm, "end": v(-77.94, 60.45) * mm});
            skCircle(sketch, "E16.0.3.23", {"center": v(-74.8, 69.09) * mm, "radius": 2.73 * mm, "construction": true});
            skLineSegment(sketch, "E16.2.3.23", {"start": v(-77.94, 69.09) * mm, "end": v(-76.37, 71.82) * mm});
            skLineSegment(sketch, "E16.5.3.23", {"start": v(-76.37, 71.82) * mm, "end": v(-73.21, 71.82) * mm});
            skLineSegment(sketch, "E16.8.3.23", {"start": v(-73.21, 71.82) * mm, "end": v(-71.64, 69.09) * mm});
            skLineSegment(sketch, "E16.11.3.23", {"start": v(-71.64, 69.09) * mm, "end": v(-73.21, 66.36) * mm});
            skLineSegment(sketch, "E16.14.3.23", {"start": v(-73.21, 66.36) * mm, "end": v(-76.37, 66.36) * mm});
            skLineSegment(sketch, "E16.17.3.23", {"start": v(-76.37, 66.36) * mm, "end": v(-77.94, 69.09) * mm});
            skCircle(sketch, "E16.0.3.24", {"center": v(-74.8, 77.72) * mm, "radius": 2.73 * mm, "construction": true});
            skLineSegment(sketch, "E16.2.3.24", {"start": v(-77.94, 77.72) * mm, "end": v(-76.37, 80.45) * mm});
            skLineSegment(sketch, "E16.5.3.24", {"start": v(-76.37, 80.45) * mm, "end": v(-73.21, 80.45) * mm});
            skLineSegment(sketch, "E16.8.3.24", {"start": v(-73.21, 80.45) * mm, "end": v(-71.64, 77.72) * mm});
            skLineSegment(sketch, "E16.11.3.24", {"start": v(-71.64, 77.72) * mm, "end": v(-73.21, 75) * mm});
            skLineSegment(sketch, "E16.14.3.24", {"start": v(-73.21, 75) * mm, "end": v(-76.37, 75) * mm});
            skLineSegment(sketch, "E16.17.3.24", {"start": v(-76.37, 75) * mm, "end": v(-77.94, 77.72) * mm});
            skCircle(sketch, "E16.0.4.20", {"center": v(-59.83, 43.18) * mm, "radius": 2.73 * mm, "construction": true});
            skLineSegment(sketch, "E16.2.4.20", {"start": v(-62.99, 43.18) * mm, "end": v(-61.4, 45.91) * mm});
            skLineSegment(sketch, "E16.5.4.20", {"start": v(-61.4, 45.91) * mm, "end": v(-58.26, 45.91) * mm});
            skLineSegment(sketch, "E16.8.4.20", {"start": v(-58.26, 45.91) * mm, "end": v(-56.68, 43.18) * mm});
            skLineSegment(sketch, "E16.11.4.20", {"start": v(-56.68, 43.18) * mm, "end": v(-58.26, 40.45) * mm});
            skLineSegment(sketch, "E16.14.4.20", {"start": v(-58.26, 40.45) * mm, "end": v(-61.4, 40.45) * mm});
            skLineSegment(sketch, "E16.17.4.20", {"start": v(-61.4, 40.45) * mm, "end": v(-62.99, 43.18) * mm});
            skCircle(sketch, "E16.0.4.21", {"center": v(-59.83, 51.82) * mm, "radius": 2.73 * mm, "construction": true});
            skLineSegment(sketch, "E16.2.4.21", {"start": v(-62.99, 51.82) * mm, "end": v(-61.4, 54.55) * mm});
            skLineSegment(sketch, "E16.5.4.21", {"start": v(-61.4, 54.55) * mm, "end": v(-58.26, 54.55) * mm});
            skLineSegment(sketch, "E16.8.4.21", {"start": v(-58.26, 54.55) * mm, "end": v(-56.68, 51.82) * mm});
            skLineSegment(sketch, "E16.11.4.21", {"start": v(-56.68, 51.82) * mm, "end": v(-58.26, 49.09) * mm});
            skLineSegment(sketch, "E16.14.4.21", {"start": v(-58.26, 49.09) * mm, "end": v(-61.4, 49.09) * mm});
            skLineSegment(sketch, "E16.17.4.21", {"start": v(-61.4, 49.09) * mm, "end": v(-62.99, 51.82) * mm});
            skCircle(sketch, "E16.0.4.22", {"center": v(-59.83, 60.45) * mm, "radius": 2.73 * mm, "construction": true});
            skLineSegment(sketch, "E16.2.4.22", {"start": v(-62.99, 60.45) * mm, "end": v(-61.4, 63.18) * mm});
            skLineSegment(sketch, "E16.5.4.22", {"start": v(-61.4, 63.18) * mm, "end": v(-58.26, 63.18) * mm});
            skLineSegment(sketch, "E16.8.4.22", {"start": v(-58.26, 63.18) * mm, "end": v(-56.68, 60.45) * mm});
            skLineSegment(sketch, "E16.11.4.22", {"start": v(-56.68, 60.45) * mm, "end": v(-58.26, 57.72) * mm});
            skLineSegment(sketch, "E16.14.4.22", {"start": v(-58.26, 57.72) * mm, "end": v(-61.4, 57.72) * mm});
            skLineSegment(sketch, "E16.17.4.22", {"start": v(-61.4, 57.72) * mm, "end": v(-62.99, 60.45) * mm});
            skCircle(sketch, "E16.0.4.23", {"center": v(-59.83, 69.09) * mm, "radius": 2.73 * mm, "construction": true});
            skLineSegment(sketch, "E16.2.4.23", {"start": v(-62.99, 69.09) * mm, "end": v(-61.4, 71.82) * mm});
            skLineSegment(sketch, "E16.5.4.23", {"start": v(-61.4, 71.82) * mm, "end": v(-58.26, 71.82) * mm});
            skLineSegment(sketch, "E16.8.4.23", {"start": v(-58.26, 71.82) * mm, "end": v(-56.68, 69.09) * mm});
            skLineSegment(sketch, "E16.11.4.23", {"start": v(-56.68, 69.09) * mm, "end": v(-58.26, 66.36) * mm});
            skLineSegment(sketch, "E16.14.4.23", {"start": v(-58.26, 66.36) * mm, "end": v(-61.4, 66.36) * mm});
            skLineSegment(sketch, "E16.17.4.23", {"start": v(-61.4, 66.36) * mm, "end": v(-62.99, 69.09) * mm});
            skCircle(sketch, "E16.0.4.24", {"center": v(-59.83, 77.72) * mm, "radius": 2.73 * mm, "construction": true});
            skLineSegment(sketch, "E16.2.4.24", {"start": v(-62.99, 77.72) * mm, "end": v(-61.4, 80.45) * mm});
            skLineSegment(sketch, "E16.5.4.24", {"start": v(-61.4, 80.45) * mm, "end": v(-58.26, 80.45) * mm});
            skLineSegment(sketch, "E16.8.4.24", {"start": v(-58.26, 80.45) * mm, "end": v(-56.68, 77.72) * mm});
            skLineSegment(sketch, "E16.11.4.24", {"start": v(-56.68, 77.72) * mm, "end": v(-58.26, 75) * mm});
            skLineSegment(sketch, "E16.14.4.24", {"start": v(-58.26, 75) * mm, "end": v(-61.4, 75) * mm});
            skLineSegment(sketch, "E16.17.4.24", {"start": v(-61.4, 75) * mm, "end": v(-62.99, 77.72) * mm});
            skCircle(sketch, "E16.0.5.20", {"center": v(-44.87, 43.18) * mm, "radius": 2.73 * mm, "construction": true});
            skLineSegment(sketch, "E16.2.5.20", {"start": v(-48.03, 43.18) * mm, "end": v(-46.45, 45.91) * mm});
            skLineSegment(sketch, "E16.5.5.20", {"start": v(-46.45, 45.91) * mm, "end": v(-43.3, 45.91) * mm});
            skLineSegment(sketch, "E16.8.5.20", {"start": v(-43.3, 45.91) * mm, "end": v(-41.72, 43.18) * mm});
            skLineSegment(sketch, "E16.11.5.20", {"start": v(-41.72, 43.18) * mm, "end": v(-43.3, 40.45) * mm});
            skLineSegment(sketch, "E16.14.5.20", {"start": v(-43.3, 40.45) * mm, "end": v(-46.45, 40.45) * mm});
            skLineSegment(sketch, "E16.17.5.20", {"start": v(-46.45, 40.45) * mm, "end": v(-48.03, 43.18) * mm});
            skCircle(sketch, "E16.0.5.21", {"center": v(-44.87, 51.82) * mm, "radius": 2.73 * mm, "construction": true});
            skLineSegment(sketch, "E16.2.5.21", {"start": v(-48.03, 51.82) * mm, "end": v(-46.45, 54.55) * mm});
            skLineSegment(sketch, "E16.5.5.21", {"start": v(-46.45, 54.55) * mm, "end": v(-43.3, 54.55) * mm});
            skLineSegment(sketch, "E16.8.5.21", {"start": v(-43.3, 54.55) * mm, "end": v(-41.72, 51.82) * mm});
            skLineSegment(sketch, "E16.11.5.21", {"start": v(-41.72, 51.82) * mm, "end": v(-43.3, 49.09) * mm});
            skLineSegment(sketch, "E16.14.5.21", {"start": v(-43.3, 49.09) * mm, "end": v(-46.45, 49.09) * mm});
            skLineSegment(sketch, "E16.17.5.21", {"start": v(-46.45, 49.09) * mm, "end": v(-48.03, 51.82) * mm});
            skCircle(sketch, "E16.0.5.22", {"center": v(-44.87, 60.45) * mm, "radius": 2.73 * mm, "construction": true});
            skLineSegment(sketch, "E16.2.5.22", {"start": v(-48.03, 60.45) * mm, "end": v(-46.45, 63.18) * mm});
            skLineSegment(sketch, "E16.5.5.22", {"start": v(-46.45, 63.18) * mm, "end": v(-43.3, 63.18) * mm});
            skLineSegment(sketch, "E16.8.5.22", {"start": v(-43.3, 63.18) * mm, "end": v(-41.72, 60.45) * mm});
            skLineSegment(sketch, "E16.11.5.22", {"start": v(-41.72, 60.45) * mm, "end": v(-43.3, 57.72) * mm});
            skLineSegment(sketch, "E16.14.5.22", {"start": v(-43.3, 57.72) * mm, "end": v(-46.45, 57.72) * mm});
            skLineSegment(sketch, "E16.17.5.22", {"start": v(-46.45, 57.72) * mm, "end": v(-48.03, 60.45) * mm});
            skCircle(sketch, "E16.0.5.23", {"center": v(-44.87, 69.09) * mm, "radius": 2.73 * mm, "construction": true});
            skLineSegment(sketch, "E16.2.5.23", {"start": v(-48.03, 69.09) * mm, "end": v(-46.45, 71.82) * mm});
            skLineSegment(sketch, "E16.5.5.23", {"start": v(-46.45, 71.82) * mm, "end": v(-43.3, 71.82) * mm});
            skLineSegment(sketch, "E16.8.5.23", {"start": v(-43.3, 71.82) * mm, "end": v(-41.72, 69.09) * mm});
            skLineSegment(sketch, "E16.11.5.23", {"start": v(-41.72, 69.09) * mm, "end": v(-43.3, 66.36) * mm});
            skLineSegment(sketch, "E16.14.5.23", {"start": v(-43.3, 66.36) * mm, "end": v(-46.45, 66.36) * mm});
            skLineSegment(sketch, "E16.17.5.23", {"start": v(-46.45, 66.36) * mm, "end": v(-48.03, 69.09) * mm});
            skCircle(sketch, "E16.0.5.24", {"center": v(-44.87, 77.72) * mm, "radius": 2.73 * mm, "construction": true});
            skLineSegment(sketch, "E16.2.5.24", {"start": v(-48.03, 77.72) * mm, "end": v(-46.45, 80.45) * mm});
            skLineSegment(sketch, "E16.5.5.24", {"start": v(-46.45, 80.45) * mm, "end": v(-43.3, 80.45) * mm});
            skLineSegment(sketch, "E16.8.5.24", {"start": v(-43.3, 80.45) * mm, "end": v(-41.72, 77.72) * mm});
            skLineSegment(sketch, "E16.11.5.24", {"start": v(-41.72, 77.72) * mm, "end": v(-43.3, 75) * mm});
            skLineSegment(sketch, "E16.14.5.24", {"start": v(-43.3, 75) * mm, "end": v(-46.45, 75) * mm});
            skLineSegment(sketch, "E16.17.5.24", {"start": v(-46.45, 75) * mm, "end": v(-48.03, 77.72) * mm});
            skCircle(sketch, "E16.0.6.20", {"center": v(-29.92, 43.18) * mm, "radius": 2.73 * mm, "construction": true});
            skLineSegment(sketch, "E16.2.6.20", {"start": v(-33.07, 43.18) * mm, "end": v(-31.5, 45.91) * mm});
            skLineSegment(sketch, "E16.5.6.20", {"start": v(-31.5, 45.91) * mm, "end": v(-28.34, 45.91) * mm});
            skLineSegment(sketch, "E16.8.6.20", {"start": v(-28.34, 45.91) * mm, "end": v(-26.76, 43.18) * mm});
            skLineSegment(sketch, "E16.11.6.20", {"start": v(-26.76, 43.18) * mm, "end": v(-28.34, 40.45) * mm});
            skLineSegment(sketch, "E16.14.6.20", {"start": v(-28.34, 40.45) * mm, "end": v(-31.5, 40.45) * mm});
            skLineSegment(sketch, "E16.17.6.20", {"start": v(-31.5, 40.45) * mm, "end": v(-33.07, 43.18) * mm});
            skCircle(sketch, "E16.0.6.21", {"center": v(-29.92, 51.82) * mm, "radius": 2.73 * mm, "construction": true});
            skLineSegment(sketch, "E16.2.6.21", {"start": v(-33.07, 51.82) * mm, "end": v(-31.5, 54.55) * mm});
            skLineSegment(sketch, "E16.5.6.21", {"start": v(-31.5, 54.55) * mm, "end": v(-28.34, 54.55) * mm});
            skLineSegment(sketch, "E16.8.6.21", {"start": v(-28.34, 54.55) * mm, "end": v(-26.76, 51.82) * mm});
            skLineSegment(sketch, "E16.11.6.21", {"start": v(-26.76, 51.82) * mm, "end": v(-28.34, 49.09) * mm});
            skLineSegment(sketch, "E16.14.6.21", {"start": v(-28.34, 49.09) * mm, "end": v(-31.5, 49.09) * mm});
            skLineSegment(sketch, "E16.17.6.21", {"start": v(-31.5, 49.09) * mm, "end": v(-33.07, 51.82) * mm});
            skCircle(sketch, "E16.0.6.22", {"center": v(-29.92, 60.45) * mm, "radius": 2.73 * mm, "construction": true});
            skLineSegment(sketch, "E16.2.6.22", {"start": v(-33.07, 60.45) * mm, "end": v(-31.5, 63.18) * mm});
            skLineSegment(sketch, "E16.5.6.22", {"start": v(-31.5, 63.18) * mm, "end": v(-28.34, 63.18) * mm});
            skLineSegment(sketch, "E16.8.6.22", {"start": v(-28.34, 63.18) * mm, "end": v(-26.76, 60.45) * mm});
            skLineSegment(sketch, "E16.11.6.22", {"start": v(-26.76, 60.45) * mm, "end": v(-28.34, 57.72) * mm});
            skLineSegment(sketch, "E16.14.6.22", {"start": v(-28.34, 57.72) * mm, "end": v(-31.5, 57.72) * mm});
            skLineSegment(sketch, "E16.17.6.22", {"start": v(-31.5, 57.72) * mm, "end": v(-33.07, 60.45) * mm});
            skCircle(sketch, "E16.0.6.23", {"center": v(-29.92, 69.09) * mm, "radius": 2.73 * mm, "construction": true});
            skLineSegment(sketch, "E16.2.6.23", {"start": v(-33.07, 69.09) * mm, "end": v(-31.5, 71.82) * mm});
            skLineSegment(sketch, "E16.5.6.23", {"start": v(-31.5, 71.82) * mm, "end": v(-28.34, 71.82) * mm});
            skLineSegment(sketch, "E16.8.6.23", {"start": v(-28.34, 71.82) * mm, "end": v(-26.76, 69.09) * mm});
            skLineSegment(sketch, "E16.11.6.23", {"start": v(-26.76, 69.09) * mm, "end": v(-28.34, 66.36) * mm});
            skLineSegment(sketch, "E16.14.6.23", {"start": v(-28.34, 66.36) * mm, "end": v(-31.5, 66.36) * mm});
            skLineSegment(sketch, "E16.17.6.23", {"start": v(-31.5, 66.36) * mm, "end": v(-33.07, 69.09) * mm});
            skCircle(sketch, "E16.0.6.24", {"center": v(-29.92, 77.72) * mm, "radius": 2.73 * mm, "construction": true});
            skLineSegment(sketch, "E16.2.6.24", {"start": v(-33.07, 77.72) * mm, "end": v(-31.5, 80.45) * mm});
            skLineSegment(sketch, "E16.5.6.24", {"start": v(-31.5, 80.45) * mm, "end": v(-28.34, 80.45) * mm});
            skLineSegment(sketch, "E16.8.6.24", {"start": v(-28.34, 80.45) * mm, "end": v(-26.76, 77.72) * mm});
            skLineSegment(sketch, "E16.11.6.24", {"start": v(-26.76, 77.72) * mm, "end": v(-28.34, 75) * mm});
            skLineSegment(sketch, "E16.14.6.24", {"start": v(-28.34, 75) * mm, "end": v(-31.5, 75) * mm});
            skLineSegment(sketch, "E16.17.6.24", {"start": v(-31.5, 75) * mm, "end": v(-33.07, 77.72) * mm});
            skCircle(sketch, "E16.0.7.20", {"center": v(-14.96, 43.18) * mm, "radius": 2.73 * mm, "construction": true});
            skLineSegment(sketch, "E16.2.7.20", {"start": v(-18.11, 43.18) * mm, "end": v(-16.53, 45.91) * mm});
            skLineSegment(sketch, "E16.5.7.20", {"start": v(-16.53, 45.91) * mm, "end": v(-13.38, 45.91) * mm});
            skLineSegment(sketch, "E16.8.7.20", {"start": v(-13.38, 45.91) * mm, "end": v(-11.8, 43.18) * mm});
            skLineSegment(sketch, "E16.11.7.20", {"start": v(-11.8, 43.18) * mm, "end": v(-13.38, 40.45) * mm});
            skLineSegment(sketch, "E16.14.7.20", {"start": v(-13.38, 40.45) * mm, "end": v(-16.53, 40.45) * mm});
            skLineSegment(sketch, "E16.17.7.20", {"start": v(-16.53, 40.45) * mm, "end": v(-18.11, 43.18) * mm});
            skCircle(sketch, "E16.0.7.21", {"center": v(-14.96, 51.82) * mm, "radius": 2.73 * mm, "construction": true});
            skLineSegment(sketch, "E16.2.7.21", {"start": v(-18.11, 51.82) * mm, "end": v(-16.53, 54.55) * mm});
            skLineSegment(sketch, "E16.5.7.21", {"start": v(-16.53, 54.55) * mm, "end": v(-13.38, 54.55) * mm});
            skLineSegment(sketch, "E16.8.7.21", {"start": v(-13.38, 54.55) * mm, "end": v(-11.8, 51.82) * mm});
            skLineSegment(sketch, "E16.11.7.21", {"start": v(-11.8, 51.82) * mm, "end": v(-13.38, 49.09) * mm});
            skLineSegment(sketch, "E16.14.7.21", {"start": v(-13.38, 49.09) * mm, "end": v(-16.53, 49.09) * mm});
            skLineSegment(sketch, "E16.17.7.21", {"start": v(-16.53, 49.09) * mm, "end": v(-18.11, 51.82) * mm});
            skCircle(sketch, "E16.0.7.22", {"center": v(-14.96, 60.45) * mm, "radius": 2.73 * mm, "construction": true});
            skLineSegment(sketch, "E16.2.7.22", {"start": v(-18.11, 60.45) * mm, "end": v(-16.53, 63.18) * mm});
            skLineSegment(sketch, "E16.5.7.22", {"start": v(-16.53, 63.18) * mm, "end": v(-13.38, 63.18) * mm});
            skLineSegment(sketch, "E16.8.7.22", {"start": v(-13.38, 63.18) * mm, "end": v(-11.8, 60.45) * mm});
            skLineSegment(sketch, "E16.11.7.22", {"start": v(-11.8, 60.45) * mm, "end": v(-13.38, 57.72) * mm});
            skLineSegment(sketch, "E16.14.7.22", {"start": v(-13.38, 57.72) * mm, "end": v(-16.53, 57.72) * mm});
            skLineSegment(sketch, "E16.17.7.22", {"start": v(-16.53, 57.72) * mm, "end": v(-18.11, 60.45) * mm});
            skCircle(sketch, "E16.0.7.23", {"center": v(-14.96, 69.09) * mm, "radius": 2.73 * mm, "construction": true});
            skLineSegment(sketch, "E16.2.7.23", {"start": v(-18.11, 69.09) * mm, "end": v(-16.53, 71.82) * mm});
            skLineSegment(sketch, "E16.5.7.23", {"start": v(-16.53, 71.82) * mm, "end": v(-13.38, 71.82) * mm});
            skLineSegment(sketch, "E16.8.7.23", {"start": v(-13.38, 71.82) * mm, "end": v(-11.8, 69.09) * mm});
            skLineSegment(sketch, "E16.11.7.23", {"start": v(-11.8, 69.09) * mm, "end": v(-13.38, 66.36) * mm});
            skLineSegment(sketch, "E16.14.7.23", {"start": v(-13.38, 66.36) * mm, "end": v(-16.53, 66.36) * mm});
            skLineSegment(sketch, "E16.17.7.23", {"start": v(-16.53, 66.36) * mm, "end": v(-18.11, 69.09) * mm});
            skCircle(sketch, "E16.0.7.24", {"center": v(-14.96, 77.72) * mm, "radius": 2.73 * mm, "construction": true});
            skLineSegment(sketch, "E16.2.7.24", {"start": v(-18.11, 77.72) * mm, "end": v(-16.53, 80.45) * mm});
            skLineSegment(sketch, "E16.5.7.24", {"start": v(-16.53, 80.45) * mm, "end": v(-13.38, 80.45) * mm});
            skLineSegment(sketch, "E16.8.7.24", {"start": v(-13.38, 80.45) * mm, "end": v(-11.8, 77.72) * mm});
            skLineSegment(sketch, "E16.11.7.24", {"start": v(-11.8, 77.72) * mm, "end": v(-13.38, 75) * mm});
            skLineSegment(sketch, "E16.14.7.24", {"start": v(-13.38, 75) * mm, "end": v(-16.53, 75) * mm});
            skLineSegment(sketch, "E16.17.7.24", {"start": v(-16.53, 75) * mm, "end": v(-18.11, 77.72) * mm});
            skCircle(sketch, "E16.0.8.20", {"center": v(0, 43.18) * mm, "radius": 2.73 * mm, "construction": true});
            skLineSegment(sketch, "E16.2.8.20", {"start": v(-3.15, 43.18) * mm, "end": v(-1.58, 45.91) * mm});
            skLineSegment(sketch, "E16.5.8.20", {"start": v(-1.58, 45.91) * mm, "end": v(1.58, 45.91) * mm});
            skLineSegment(sketch, "E16.8.8.20", {"start": v(1.58, 45.91) * mm, "end": v(3.15, 43.18) * mm});
            skLineSegment(sketch, "E16.11.8.20", {"start": v(3.15, 43.18) * mm, "end": v(1.58, 40.45) * mm});
            skLineSegment(sketch, "E16.14.8.20", {"start": v(1.58, 40.45) * mm, "end": v(-1.58, 40.45) * mm});
            skLineSegment(sketch, "E16.17.8.20", {"start": v(-1.58, 40.45) * mm, "end": v(-3.15, 43.18) * mm});
            skCircle(sketch, "E16.0.8.21", {"center": v(0, 51.82) * mm, "radius": 2.73 * mm, "construction": true});
            skLineSegment(sketch, "E16.2.8.21", {"start": v(-3.15, 51.82) * mm, "end": v(-1.58, 54.55) * mm});
            skLineSegment(sketch, "E16.5.8.21", {"start": v(-1.58, 54.55) * mm, "end": v(1.58, 54.55) * mm});
            skLineSegment(sketch, "E16.8.8.21", {"start": v(1.58, 54.55) * mm, "end": v(3.15, 51.82) * mm});
            skLineSegment(sketch, "E16.11.8.21", {"start": v(3.15, 51.82) * mm, "end": v(1.58, 49.09) * mm});
            skLineSegment(sketch, "E16.14.8.21", {"start": v(1.58, 49.09) * mm, "end": v(-1.58, 49.09) * mm});
            skLineSegment(sketch, "E16.17.8.21", {"start": v(-1.58, 49.09) * mm, "end": v(-3.15, 51.82) * mm});
            skCircle(sketch, "E16.0.8.22", {"center": v(0, 60.45) * mm, "radius": 2.73 * mm, "construction": true});
            skLineSegment(sketch, "E16.2.8.22", {"start": v(-3.15, 60.45) * mm, "end": v(-1.58, 63.18) * mm});
            skLineSegment(sketch, "E16.5.8.22", {"start": v(-1.58, 63.18) * mm, "end": v(1.58, 63.18) * mm});
            skLineSegment(sketch, "E16.8.8.22", {"start": v(1.58, 63.18) * mm, "end": v(3.15, 60.45) * mm});
            skLineSegment(sketch, "E16.11.8.22", {"start": v(3.15, 60.45) * mm, "end": v(1.58, 57.72) * mm});
            skLineSegment(sketch, "E16.14.8.22", {"start": v(1.58, 57.72) * mm, "end": v(-1.58, 57.72) * mm});
            skLineSegment(sketch, "E16.17.8.22", {"start": v(-1.58, 57.72) * mm, "end": v(-3.15, 60.45) * mm});
            skCircle(sketch, "E16.0.8.23", {"center": v(0, 69.09) * mm, "radius": 2.73 * mm, "construction": true});
            skLineSegment(sketch, "E16.2.8.23", {"start": v(-3.15, 69.09) * mm, "end": v(-1.58, 71.82) * mm});
            skLineSegment(sketch, "E16.5.8.23", {"start": v(-1.58, 71.82) * mm, "end": v(1.58, 71.82) * mm});
            skLineSegment(sketch, "E16.8.8.23", {"start": v(1.58, 71.82) * mm, "end": v(3.15, 69.09) * mm});
            skLineSegment(sketch, "E16.11.8.23", {"start": v(3.15, 69.09) * mm, "end": v(1.58, 66.36) * mm});
            skLineSegment(sketch, "E16.14.8.23", {"start": v(1.58, 66.36) * mm, "end": v(-1.58, 66.36) * mm});
            skLineSegment(sketch, "E16.17.8.23", {"start": v(-1.58, 66.36) * mm, "end": v(-3.15, 69.09) * mm});
            skCircle(sketch, "E16.0.8.24", {"center": v(0, 77.72) * mm, "radius": 2.73 * mm, "construction": true});
            skLineSegment(sketch, "E16.2.8.24", {"start": v(-3.15, 77.72) * mm, "end": v(-1.58, 80.45) * mm});
            skLineSegment(sketch, "E16.5.8.24", {"start": v(-1.58, 80.45) * mm, "end": v(1.58, 80.45) * mm});
            skLineSegment(sketch, "E16.8.8.24", {"start": v(1.58, 80.45) * mm, "end": v(3.15, 77.72) * mm});
            skLineSegment(sketch, "E16.11.8.24", {"start": v(3.15, 77.72) * mm, "end": v(1.58, 75) * mm});
            skLineSegment(sketch, "E16.14.8.24", {"start": v(1.58, 75) * mm, "end": v(-1.58, 75) * mm});
            skLineSegment(sketch, "E16.17.8.24", {"start": v(-1.58, 75) * mm, "end": v(-3.15, 77.72) * mm});
            skCircle(sketch, "E16.0.9.20", {"center": v(14.96, 43.18) * mm, "radius": 2.73 * mm, "construction": true});
            skLineSegment(sketch, "E16.2.9.20", {"start": v(11.8, 43.18) * mm, "end": v(13.38, 45.91) * mm});
            skLineSegment(sketch, "E16.5.9.20", {"start": v(13.38, 45.91) * mm, "end": v(16.53, 45.91) * mm});
            skLineSegment(sketch, "E16.8.9.20", {"start": v(16.53, 45.91) * mm, "end": v(18.11, 43.18) * mm});
            skLineSegment(sketch, "E16.11.9.20", {"start": v(18.11, 43.18) * mm, "end": v(16.53, 40.45) * mm});
            skLineSegment(sketch, "E16.14.9.20", {"start": v(16.53, 40.45) * mm, "end": v(13.38, 40.45) * mm});
            skLineSegment(sketch, "E16.17.9.20", {"start": v(13.38, 40.45) * mm, "end": v(11.8, 43.18) * mm});
            skCircle(sketch, "E16.0.9.21", {"center": v(14.96, 51.82) * mm, "radius": 2.73 * mm, "construction": true});
            skLineSegment(sketch, "E16.2.9.21", {"start": v(11.8, 51.82) * mm, "end": v(13.38, 54.55) * mm});
            skLineSegment(sketch, "E16.5.9.21", {"start": v(13.38, 54.55) * mm, "end": v(16.53, 54.55) * mm});
            skLineSegment(sketch, "E16.8.9.21", {"start": v(16.53, 54.55) * mm, "end": v(18.11, 51.82) * mm});
            skLineSegment(sketch, "E16.11.9.21", {"start": v(18.11, 51.82) * mm, "end": v(16.53, 49.09) * mm});
            skLineSegment(sketch, "E16.14.9.21", {"start": v(16.53, 49.09) * mm, "end": v(13.38, 49.09) * mm});
            skLineSegment(sketch, "E16.17.9.21", {"start": v(13.38, 49.09) * mm, "end": v(11.8, 51.82) * mm});
            skCircle(sketch, "E16.0.9.22", {"center": v(14.96, 60.45) * mm, "radius": 2.73 * mm, "construction": true});
            skLineSegment(sketch, "E16.2.9.22", {"start": v(11.8, 60.45) * mm, "end": v(13.38, 63.18) * mm});
            skLineSegment(sketch, "E16.5.9.22", {"start": v(13.38, 63.18) * mm, "end": v(16.53, 63.18) * mm});
            skLineSegment(sketch, "E16.8.9.22", {"start": v(16.53, 63.18) * mm, "end": v(18.11, 60.45) * mm});
            skLineSegment(sketch, "E16.11.9.22", {"start": v(18.11, 60.45) * mm, "end": v(16.53, 57.72) * mm});
            skLineSegment(sketch, "E16.14.9.22", {"start": v(16.53, 57.72) * mm, "end": v(13.38, 57.72) * mm});
            skLineSegment(sketch, "E16.17.9.22", {"start": v(13.38, 57.72) * mm, "end": v(11.8, 60.45) * mm});
            skCircle(sketch, "E16.0.9.23", {"center": v(14.96, 69.09) * mm, "radius": 2.73 * mm, "construction": true});
            skLineSegment(sketch, "E16.2.9.23", {"start": v(11.8, 69.09) * mm, "end": v(13.38, 71.82) * mm});
            skLineSegment(sketch, "E16.5.9.23", {"start": v(13.38, 71.82) * mm, "end": v(16.53, 71.82) * mm});
            skLineSegment(sketch, "E16.8.9.23", {"start": v(16.53, 71.82) * mm, "end": v(18.11, 69.09) * mm});
            skLineSegment(sketch, "E16.11.9.23", {"start": v(18.11, 69.09) * mm, "end": v(16.53, 66.36) * mm});
            skLineSegment(sketch, "E16.14.9.23", {"start": v(16.53, 66.36) * mm, "end": v(13.38, 66.36) * mm});
            skLineSegment(sketch, "E16.17.9.23", {"start": v(13.38, 66.36) * mm, "end": v(11.8, 69.09) * mm});
            skCircle(sketch, "E16.0.9.24", {"center": v(14.96, 77.72) * mm, "radius": 2.73 * mm, "construction": true});
            skLineSegment(sketch, "E16.2.9.24", {"start": v(11.8, 77.72) * mm, "end": v(13.38, 80.45) * mm});
            skLineSegment(sketch, "E16.5.9.24", {"start": v(13.38, 80.45) * mm, "end": v(16.53, 80.45) * mm});
            skLineSegment(sketch, "E16.8.9.24", {"start": v(16.53, 80.45) * mm, "end": v(18.11, 77.72) * mm});
            skLineSegment(sketch, "E16.11.9.24", {"start": v(18.11, 77.72) * mm, "end": v(16.53, 75) * mm});
            skLineSegment(sketch, "E16.14.9.24", {"start": v(16.53, 75) * mm, "end": v(13.38, 75) * mm});
            skLineSegment(sketch, "E16.17.9.24", {"start": v(13.38, 75) * mm, "end": v(11.8, 77.72) * mm});
            skCircle(sketch, "E16.0.10.20", {"center": v(29.92, 43.18) * mm, "radius": 2.73 * mm, "construction": true});
            skLineSegment(sketch, "E16.2.10.20", {"start": v(26.76, 43.18) * mm, "end": v(28.34, 45.91) * mm});
            skLineSegment(sketch, "E16.5.10.20", {"start": v(28.34, 45.91) * mm, "end": v(31.5, 45.91) * mm});
            skLineSegment(sketch, "E16.8.10.20", {"start": v(31.5, 45.91) * mm, "end": v(33.07, 43.18) * mm});
            skLineSegment(sketch, "E16.11.10.20", {"start": v(33.07, 43.18) * mm, "end": v(31.5, 40.45) * mm});
            skLineSegment(sketch, "E16.14.10.20", {"start": v(31.5, 40.45) * mm, "end": v(28.34, 40.45) * mm});
            skLineSegment(sketch, "E16.17.10.20", {"start": v(28.34, 40.45) * mm, "end": v(26.76, 43.18) * mm});
            skCircle(sketch, "E16.0.10.21", {"center": v(29.92, 51.82) * mm, "radius": 2.73 * mm, "construction": true});
            skLineSegment(sketch, "E16.2.10.21", {"start": v(26.76, 51.82) * mm, "end": v(28.34, 54.55) * mm});
            skLineSegment(sketch, "E16.5.10.21", {"start": v(28.34, 54.55) * mm, "end": v(31.5, 54.55) * mm});
            skLineSegment(sketch, "E16.8.10.21", {"start": v(31.5, 54.55) * mm, "end": v(33.07, 51.82) * mm});
            skLineSegment(sketch, "E16.11.10.21", {"start": v(33.07, 51.82) * mm, "end": v(31.5, 49.09) * mm});
            skLineSegment(sketch, "E16.14.10.21", {"start": v(31.5, 49.09) * mm, "end": v(28.34, 49.09) * mm});
            skLineSegment(sketch, "E16.17.10.21", {"start": v(28.34, 49.09) * mm, "end": v(26.76, 51.82) * mm});
            skCircle(sketch, "E16.0.10.22", {"center": v(29.92, 60.45) * mm, "radius": 2.73 * mm, "construction": true});
            skLineSegment(sketch, "E16.2.10.22", {"start": v(26.76, 60.45) * mm, "end": v(28.34, 63.18) * mm});
            skLineSegment(sketch, "E16.5.10.22", {"start": v(28.34, 63.18) * mm, "end": v(31.5, 63.18) * mm});
            skLineSegment(sketch, "E16.8.10.22", {"start": v(31.5, 63.18) * mm, "end": v(33.07, 60.45) * mm});
            skLineSegment(sketch, "E16.11.10.22", {"start": v(33.07, 60.45) * mm, "end": v(31.5, 57.72) * mm});
            skLineSegment(sketch, "E16.14.10.22", {"start": v(31.5, 57.72) * mm, "end": v(28.34, 57.72) * mm});
            skLineSegment(sketch, "E16.17.10.22", {"start": v(28.34, 57.72) * mm, "end": v(26.76, 60.45) * mm});
            skCircle(sketch, "E16.0.10.23", {"center": v(29.92, 69.09) * mm, "radius": 2.73 * mm, "construction": true});
            skLineSegment(sketch, "E16.2.10.23", {"start": v(26.76, 69.09) * mm, "end": v(28.34, 71.82) * mm});
            skLineSegment(sketch, "E16.5.10.23", {"start": v(28.34, 71.82) * mm, "end": v(31.5, 71.82) * mm});
            skLineSegment(sketch, "E16.8.10.23", {"start": v(31.5, 71.82) * mm, "end": v(33.07, 69.09) * mm});
            skLineSegment(sketch, "E16.11.10.23", {"start": v(33.07, 69.09) * mm, "end": v(31.5, 66.36) * mm});
            skLineSegment(sketch, "E16.14.10.23", {"start": v(31.5, 66.36) * mm, "end": v(28.34, 66.36) * mm});
            skLineSegment(sketch, "E16.17.10.23", {"start": v(28.34, 66.36) * mm, "end": v(26.76, 69.09) * mm});
            skCircle(sketch, "E16.0.10.24", {"center": v(29.92, 77.72) * mm, "radius": 2.73 * mm, "construction": true});
            skLineSegment(sketch, "E16.2.10.24", {"start": v(26.76, 77.72) * mm, "end": v(28.34, 80.45) * mm});
            skLineSegment(sketch, "E16.5.10.24", {"start": v(28.34, 80.45) * mm, "end": v(31.5, 80.45) * mm});
            skLineSegment(sketch, "E16.8.10.24", {"start": v(31.5, 80.45) * mm, "end": v(33.07, 77.72) * mm});
            skLineSegment(sketch, "E16.11.10.24", {"start": v(33.07, 77.72) * mm, "end": v(31.5, 75) * mm});
            skLineSegment(sketch, "E16.14.10.24", {"start": v(31.5, 75) * mm, "end": v(28.34, 75) * mm});
            skLineSegment(sketch, "E16.17.10.24", {"start": v(28.34, 75) * mm, "end": v(26.76, 77.72) * mm});
            skCircle(sketch, "E16.0.11.20", {"center": v(44.87, 43.18) * mm, "radius": 2.73 * mm, "construction": true});
            skLineSegment(sketch, "E16.2.11.20", {"start": v(41.72, 43.18) * mm, "end": v(43.3, 45.91) * mm});
            skLineSegment(sketch, "E16.5.11.20", {"start": v(43.3, 45.91) * mm, "end": v(46.45, 45.91) * mm});
            skLineSegment(sketch, "E16.8.11.20", {"start": v(46.45, 45.91) * mm, "end": v(48.03, 43.18) * mm});
            skLineSegment(sketch, "E16.11.11.20", {"start": v(48.03, 43.18) * mm, "end": v(46.45, 40.45) * mm});
            skLineSegment(sketch, "E16.14.11.20", {"start": v(46.45, 40.45) * mm, "end": v(43.3, 40.45) * mm});
            skLineSegment(sketch, "E16.17.11.20", {"start": v(43.3, 40.45) * mm, "end": v(41.72, 43.18) * mm});
            skCircle(sketch, "E16.0.11.21", {"center": v(44.87, 51.82) * mm, "radius": 2.73 * mm, "construction": true});
            skLineSegment(sketch, "E16.2.11.21", {"start": v(41.72, 51.82) * mm, "end": v(43.3, 54.55) * mm});
            skLineSegment(sketch, "E16.5.11.21", {"start": v(43.3, 54.55) * mm, "end": v(46.45, 54.55) * mm});
            skLineSegment(sketch, "E16.8.11.21", {"start": v(46.45, 54.55) * mm, "end": v(48.03, 51.82) * mm});
            skLineSegment(sketch, "E16.11.11.21", {"start": v(48.03, 51.82) * mm, "end": v(46.45, 49.09) * mm});
            skLineSegment(sketch, "E16.14.11.21", {"start": v(46.45, 49.09) * mm, "end": v(43.3, 49.09) * mm});
            skLineSegment(sketch, "E16.17.11.21", {"start": v(43.3, 49.09) * mm, "end": v(41.72, 51.82) * mm});
            skCircle(sketch, "E16.0.11.22", {"center": v(44.87, 60.45) * mm, "radius": 2.73 * mm, "construction": true});
            skLineSegment(sketch, "E16.2.11.22", {"start": v(41.72, 60.45) * mm, "end": v(43.3, 63.18) * mm});
            skLineSegment(sketch, "E16.5.11.22", {"start": v(43.3, 63.18) * mm, "end": v(46.45, 63.18) * mm});
            skLineSegment(sketch, "E16.8.11.22", {"start": v(46.45, 63.18) * mm, "end": v(48.03, 60.45) * mm});
            skLineSegment(sketch, "E16.11.11.22", {"start": v(48.03, 60.45) * mm, "end": v(46.45, 57.72) * mm});
            skLineSegment(sketch, "E16.14.11.22", {"start": v(46.45, 57.72) * mm, "end": v(43.3, 57.72) * mm});
            skLineSegment(sketch, "E16.17.11.22", {"start": v(43.3, 57.72) * mm, "end": v(41.72, 60.45) * mm});
            skCircle(sketch, "E16.0.11.23", {"center": v(44.87, 69.09) * mm, "radius": 2.73 * mm, "construction": true});
            skLineSegment(sketch, "E16.2.11.23", {"start": v(41.72, 69.09) * mm, "end": v(43.3, 71.82) * mm});
            skLineSegment(sketch, "E16.5.11.23", {"start": v(43.3, 71.82) * mm, "end": v(46.45, 71.82) * mm});
            skLineSegment(sketch, "E16.8.11.23", {"start": v(46.45, 71.82) * mm, "end": v(48.03, 69.09) * mm});
            skLineSegment(sketch, "E16.11.11.23", {"start": v(48.03, 69.09) * mm, "end": v(46.45, 66.36) * mm});
            skLineSegment(sketch, "E16.14.11.23", {"start": v(46.45, 66.36) * mm, "end": v(43.3, 66.36) * mm});
            skLineSegment(sketch, "E16.17.11.23", {"start": v(43.3, 66.36) * mm, "end": v(41.72, 69.09) * mm});
            skCircle(sketch, "E16.0.11.24", {"center": v(44.87, 77.72) * mm, "radius": 2.73 * mm, "construction": true});
            skLineSegment(sketch, "E16.2.11.24", {"start": v(41.72, 77.72) * mm, "end": v(43.3, 80.45) * mm});
            skLineSegment(sketch, "E16.5.11.24", {"start": v(43.3, 80.45) * mm, "end": v(46.45, 80.45) * mm});
            skLineSegment(sketch, "E16.8.11.24", {"start": v(46.45, 80.45) * mm, "end": v(48.03, 77.72) * mm});
            skLineSegment(sketch, "E16.11.11.24", {"start": v(48.03, 77.72) * mm, "end": v(46.45, 75) * mm});
            skLineSegment(sketch, "E16.14.11.24", {"start": v(46.45, 75) * mm, "end": v(43.3, 75) * mm});
            skLineSegment(sketch, "E16.17.11.24", {"start": v(43.3, 75) * mm, "end": v(41.72, 77.72) * mm});
            skCircle(sketch, "E16.0.12.20", {"center": v(59.83, 43.18) * mm, "radius": 2.73 * mm, "construction": true});
            skLineSegment(sketch, "E16.2.12.20", {"start": v(56.68, 43.18) * mm, "end": v(58.26, 45.91) * mm});
            skLineSegment(sketch, "E16.5.12.20", {"start": v(58.26, 45.91) * mm, "end": v(61.4, 45.91) * mm});
            skLineSegment(sketch, "E16.8.12.20", {"start": v(61.4, 45.91) * mm, "end": v(62.99, 43.18) * mm});
            skLineSegment(sketch, "E16.11.12.20", {"start": v(62.99, 43.18) * mm, "end": v(61.4, 40.45) * mm});
            skLineSegment(sketch, "E16.14.12.20", {"start": v(61.4, 40.45) * mm, "end": v(58.26, 40.45) * mm});
            skLineSegment(sketch, "E16.17.12.20", {"start": v(58.26, 40.45) * mm, "end": v(56.68, 43.18) * mm});
            skCircle(sketch, "E16.0.12.21", {"center": v(59.83, 51.82) * mm, "radius": 2.73 * mm, "construction": true});
            skLineSegment(sketch, "E16.2.12.21", {"start": v(56.68, 51.82) * mm, "end": v(58.26, 54.55) * mm});
            skLineSegment(sketch, "E16.5.12.21", {"start": v(58.26, 54.55) * mm, "end": v(61.4, 54.55) * mm});
            skLineSegment(sketch, "E16.8.12.21", {"start": v(61.4, 54.55) * mm, "end": v(62.99, 51.82) * mm});
            skLineSegment(sketch, "E16.11.12.21", {"start": v(62.99, 51.82) * mm, "end": v(61.4, 49.09) * mm});
            skLineSegment(sketch, "E16.14.12.21", {"start": v(61.4, 49.09) * mm, "end": v(58.26, 49.09) * mm});
            skLineSegment(sketch, "E16.17.12.21", {"start": v(58.26, 49.09) * mm, "end": v(56.68, 51.82) * mm});
            skCircle(sketch, "E16.0.12.22", {"center": v(59.83, 60.45) * mm, "radius": 2.73 * mm, "construction": true});
            skLineSegment(sketch, "E16.2.12.22", {"start": v(56.68, 60.45) * mm, "end": v(58.26, 63.18) * mm});
            skLineSegment(sketch, "E16.5.12.22", {"start": v(58.26, 63.18) * mm, "end": v(61.4, 63.18) * mm});
            skLineSegment(sketch, "E16.8.12.22", {"start": v(61.4, 63.18) * mm, "end": v(62.99, 60.45) * mm});
            skLineSegment(sketch, "E16.11.12.22", {"start": v(62.99, 60.45) * mm, "end": v(61.4, 57.72) * mm});
            skLineSegment(sketch, "E16.14.12.22", {"start": v(61.4, 57.72) * mm, "end": v(58.26, 57.72) * mm});
            skLineSegment(sketch, "E16.17.12.22", {"start": v(58.26, 57.72) * mm, "end": v(56.68, 60.45) * mm});
            skCircle(sketch, "E16.0.12.23", {"center": v(59.83, 69.09) * mm, "radius": 2.73 * mm, "construction": true});
            skLineSegment(sketch, "E16.2.12.23", {"start": v(56.68, 69.09) * mm, "end": v(58.26, 71.82) * mm});
            skLineSegment(sketch, "E16.5.12.23", {"start": v(58.26, 71.82) * mm, "end": v(61.4, 71.82) * mm});
            skLineSegment(sketch, "E16.8.12.23", {"start": v(61.4, 71.82) * mm, "end": v(62.99, 69.09) * mm});
            skLineSegment(sketch, "E16.11.12.23", {"start": v(62.99, 69.09) * mm, "end": v(61.4, 66.36) * mm});
            skLineSegment(sketch, "E16.14.12.23", {"start": v(61.4, 66.36) * mm, "end": v(58.26, 66.36) * mm});
            skLineSegment(sketch, "E16.17.12.23", {"start": v(58.26, 66.36) * mm, "end": v(56.68, 69.09) * mm});
            skCircle(sketch, "E16.0.12.24", {"center": v(59.83, 77.72) * mm, "radius": 2.73 * mm, "construction": true});
            skLineSegment(sketch, "E16.2.12.24", {"start": v(56.68, 77.72) * mm, "end": v(58.26, 80.45) * mm});
            skLineSegment(sketch, "E16.5.12.24", {"start": v(58.26, 80.45) * mm, "end": v(61.4, 80.45) * mm});
            skLineSegment(sketch, "E16.8.12.24", {"start": v(61.4, 80.45) * mm, "end": v(62.99, 77.72) * mm});
            skLineSegment(sketch, "E16.11.12.24", {"start": v(62.99, 77.72) * mm, "end": v(61.4, 75) * mm});
            skLineSegment(sketch, "E16.14.12.24", {"start": v(61.4, 75) * mm, "end": v(58.26, 75) * mm});
            skLineSegment(sketch, "E16.17.12.24", {"start": v(58.26, 75) * mm, "end": v(56.68, 77.72) * mm});
            skCircle(sketch, "E16.0.13.20", {"center": v(74.8, 43.18) * mm, "radius": 2.73 * mm, "construction": true});
            skLineSegment(sketch, "E16.2.13.20", {"start": v(71.64, 43.18) * mm, "end": v(73.21, 45.91) * mm});
            skLineSegment(sketch, "E16.5.13.20", {"start": v(73.21, 45.91) * mm, "end": v(76.37, 45.91) * mm});
            skLineSegment(sketch, "E16.8.13.20", {"start": v(76.37, 45.91) * mm, "end": v(77.94, 43.18) * mm});
            skLineSegment(sketch, "E16.11.13.20", {"start": v(77.94, 43.18) * mm, "end": v(76.37, 40.45) * mm});
            skLineSegment(sketch, "E16.14.13.20", {"start": v(76.37, 40.45) * mm, "end": v(73.21, 40.45) * mm});
            skLineSegment(sketch, "E16.17.13.20", {"start": v(73.21, 40.45) * mm, "end": v(71.64, 43.18) * mm});
            skCircle(sketch, "E16.0.13.21", {"center": v(74.8, 51.82) * mm, "radius": 2.73 * mm, "construction": true});
            skLineSegment(sketch, "E16.2.13.21", {"start": v(71.64, 51.82) * mm, "end": v(73.21, 54.55) * mm});
            skLineSegment(sketch, "E16.5.13.21", {"start": v(73.21, 54.55) * mm, "end": v(76.37, 54.55) * mm});
            skLineSegment(sketch, "E16.8.13.21", {"start": v(76.37, 54.55) * mm, "end": v(77.94, 51.82) * mm});
            skLineSegment(sketch, "E16.11.13.21", {"start": v(77.94, 51.82) * mm, "end": v(76.37, 49.09) * mm});
            skLineSegment(sketch, "E16.14.13.21", {"start": v(76.37, 49.09) * mm, "end": v(73.21, 49.09) * mm});
            skLineSegment(sketch, "E16.17.13.21", {"start": v(73.21, 49.09) * mm, "end": v(71.64, 51.82) * mm});
            skCircle(sketch, "E16.0.13.22", {"center": v(74.8, 60.45) * mm, "radius": 2.73 * mm, "construction": true});
            skLineSegment(sketch, "E16.2.13.22", {"start": v(71.64, 60.45) * mm, "end": v(73.21, 63.18) * mm});
            skLineSegment(sketch, "E16.5.13.22", {"start": v(73.21, 63.18) * mm, "end": v(76.37, 63.18) * mm});
            skLineSegment(sketch, "E16.8.13.22", {"start": v(76.37, 63.18) * mm, "end": v(77.94, 60.45) * mm});
            skLineSegment(sketch, "E16.11.13.22", {"start": v(77.94, 60.45) * mm, "end": v(76.37, 57.72) * mm});
            skLineSegment(sketch, "E16.14.13.22", {"start": v(76.37, 57.72) * mm, "end": v(73.21, 57.72) * mm});
            skLineSegment(sketch, "E16.17.13.22", {"start": v(73.21, 57.72) * mm, "end": v(71.64, 60.45) * mm});
            skCircle(sketch, "E16.0.13.23", {"center": v(74.8, 69.09) * mm, "radius": 2.73 * mm, "construction": true});
            skLineSegment(sketch, "E16.2.13.23", {"start": v(71.64, 69.09) * mm, "end": v(73.21, 71.82) * mm});
            skLineSegment(sketch, "E16.5.13.23", {"start": v(73.21, 71.82) * mm, "end": v(76.37, 71.82) * mm});
            skLineSegment(sketch, "E16.8.13.23", {"start": v(76.37, 71.82) * mm, "end": v(77.94, 69.09) * mm});
            skLineSegment(sketch, "E16.11.13.23", {"start": v(77.94, 69.09) * mm, "end": v(76.37, 66.36) * mm});
            skLineSegment(sketch, "E16.14.13.23", {"start": v(76.37, 66.36) * mm, "end": v(73.21, 66.36) * mm});
            skLineSegment(sketch, "E16.17.13.23", {"start": v(73.21, 66.36) * mm, "end": v(71.64, 69.09) * mm});
            skCircle(sketch, "E16.0.13.24", {"center": v(74.8, 77.72) * mm, "radius": 2.73 * mm, "construction": true});
            skLineSegment(sketch, "E16.2.13.24", {"start": v(71.64, 77.72) * mm, "end": v(73.21, 80.45) * mm});
            skLineSegment(sketch, "E16.5.13.24", {"start": v(73.21, 80.45) * mm, "end": v(76.37, 80.45) * mm});
            skLineSegment(sketch, "E16.8.13.24", {"start": v(76.37, 80.45) * mm, "end": v(77.94, 77.72) * mm});
            skLineSegment(sketch, "E16.11.13.24", {"start": v(77.94, 77.72) * mm, "end": v(76.37, 75) * mm});
            skLineSegment(sketch, "E16.14.13.24", {"start": v(76.37, 75) * mm, "end": v(73.21, 75) * mm});
            skLineSegment(sketch, "E16.17.13.24", {"start": v(73.21, 75) * mm, "end": v(71.64, 77.72) * mm});
            skCircle(sketch, "E16.0.14.20", {"center": v(89.75, 43.18) * mm, "radius": 2.73 * mm, "construction": true});
            skLineSegment(sketch, "E16.2.14.20", {"start": v(86.6, 43.18) * mm, "end": v(88.17, 45.91) * mm});
            skLineSegment(sketch, "E16.5.14.20", {"start": v(88.17, 45.91) * mm, "end": v(91.32, 45.91) * mm});
            skLineSegment(sketch, "E16.8.14.20", {"start": v(91.32, 45.91) * mm, "end": v(92.9, 43.18) * mm});
            skLineSegment(sketch, "E16.11.14.20", {"start": v(92.9, 43.18) * mm, "end": v(91.32, 40.45) * mm});
            skLineSegment(sketch, "E16.14.14.20", {"start": v(91.32, 40.45) * mm, "end": v(88.17, 40.45) * mm});
            skLineSegment(sketch, "E16.17.14.20", {"start": v(88.17, 40.45) * mm, "end": v(86.6, 43.18) * mm});
            skCircle(sketch, "E16.0.14.21", {"center": v(89.75, 51.82) * mm, "radius": 2.73 * mm, "construction": true});
            skLineSegment(sketch, "E16.2.14.21", {"start": v(86.6, 51.82) * mm, "end": v(88.17, 54.55) * mm});
            skLineSegment(sketch, "E16.5.14.21", {"start": v(88.17, 54.55) * mm, "end": v(91.32, 54.55) * mm});
            skLineSegment(sketch, "E16.8.14.21", {"start": v(91.32, 54.55) * mm, "end": v(92.9, 51.82) * mm});
            skLineSegment(sketch, "E16.11.14.21", {"start": v(92.9, 51.82) * mm, "end": v(91.32, 49.09) * mm});
            skLineSegment(sketch, "E16.14.14.21", {"start": v(91.32, 49.09) * mm, "end": v(88.17, 49.09) * mm});
            skLineSegment(sketch, "E16.17.14.21", {"start": v(88.17, 49.09) * mm, "end": v(86.6, 51.82) * mm});
            skCircle(sketch, "E16.0.14.22", {"center": v(89.75, 60.45) * mm, "radius": 2.73 * mm, "construction": true});
            skLineSegment(sketch, "E16.2.14.22", {"start": v(86.6, 60.45) * mm, "end": v(88.17, 63.18) * mm});
            skLineSegment(sketch, "E16.5.14.22", {"start": v(88.17, 63.18) * mm, "end": v(91.32, 63.18) * mm});
            skLineSegment(sketch, "E16.8.14.22", {"start": v(91.32, 63.18) * mm, "end": v(92.9, 60.45) * mm});
            skLineSegment(sketch, "E16.11.14.22", {"start": v(92.9, 60.45) * mm, "end": v(91.32, 57.72) * mm});
            skLineSegment(sketch, "E16.14.14.22", {"start": v(91.32, 57.72) * mm, "end": v(88.17, 57.72) * mm});
            skLineSegment(sketch, "E16.17.14.22", {"start": v(88.17, 57.72) * mm, "end": v(86.6, 60.45) * mm});
            skCircle(sketch, "E16.0.14.23", {"center": v(89.75, 69.09) * mm, "radius": 2.73 * mm, "construction": true});
            skLineSegment(sketch, "E16.2.14.23", {"start": v(86.6, 69.09) * mm, "end": v(88.17, 71.82) * mm});
            skLineSegment(sketch, "E16.5.14.23", {"start": v(88.17, 71.82) * mm, "end": v(91.32, 71.82) * mm});
            skLineSegment(sketch, "E16.8.14.23", {"start": v(91.32, 71.82) * mm, "end": v(92.9, 69.09) * mm});
            skLineSegment(sketch, "E16.11.14.23", {"start": v(92.9, 69.09) * mm, "end": v(91.32, 66.36) * mm});
            skLineSegment(sketch, "E16.14.14.23", {"start": v(91.32, 66.36) * mm, "end": v(88.17, 66.36) * mm});
            skLineSegment(sketch, "E16.17.14.23", {"start": v(88.17, 66.36) * mm, "end": v(86.6, 69.09) * mm});
            skCircle(sketch, "E16.0.14.24", {"center": v(89.75, 77.72) * mm, "radius": 2.73 * mm, "construction": true});
            skLineSegment(sketch, "E16.2.14.24", {"start": v(86.6, 77.72) * mm, "end": v(88.17, 80.45) * mm});
            skLineSegment(sketch, "E16.5.14.24", {"start": v(88.17, 80.45) * mm, "end": v(91.32, 80.45) * mm});
            skLineSegment(sketch, "E16.8.14.24", {"start": v(91.32, 80.45) * mm, "end": v(92.9, 77.72) * mm});
            skLineSegment(sketch, "E16.11.14.24", {"start": v(92.9, 77.72) * mm, "end": v(91.32, 75) * mm});
            skLineSegment(sketch, "E16.14.14.24", {"start": v(91.32, 75) * mm, "end": v(88.17, 75) * mm});
            skLineSegment(sketch, "E16.17.14.24", {"start": v(88.17, 75) * mm, "end": v(86.6, 77.72) * mm});
            skCircle(sketch, "E16.0.15.20", {"center": v(104.7, 43.18) * mm, "radius": 2.73 * mm, "construction": true});
            skLineSegment(sketch, "E16.2.15.20", {"start": v(101.55, 43.18) * mm, "end": v(103.13, 45.91) * mm});
            skLineSegment(sketch, "E16.5.15.20", {"start": v(103.13, 45.91) * mm, "end": v(106.28, 45.91) * mm});
            skLineSegment(sketch, "E16.8.15.20", {"start": v(106.28, 45.91) * mm, "end": v(107.86, 43.18) * mm});
            skLineSegment(sketch, "E16.11.15.20", {"start": v(107.86, 43.18) * mm, "end": v(106.28, 40.45) * mm});
            skLineSegment(sketch, "E16.14.15.20", {"start": v(106.28, 40.45) * mm, "end": v(103.13, 40.45) * mm});
            skLineSegment(sketch, "E16.17.15.20", {"start": v(103.13, 40.45) * mm, "end": v(101.55, 43.18) * mm});
            skCircle(sketch, "E16.0.15.21", {"center": v(104.7, 51.82) * mm, "radius": 2.73 * mm, "construction": true});
            skLineSegment(sketch, "E16.2.15.21", {"start": v(101.55, 51.82) * mm, "end": v(103.13, 54.55) * mm});
            skLineSegment(sketch, "E16.5.15.21", {"start": v(103.13, 54.55) * mm, "end": v(106.28, 54.55) * mm});
            skLineSegment(sketch, "E16.8.15.21", {"start": v(106.28, 54.55) * mm, "end": v(107.86, 51.82) * mm});
            skLineSegment(sketch, "E16.11.15.21", {"start": v(107.86, 51.82) * mm, "end": v(106.28, 49.09) * mm});
            skLineSegment(sketch, "E16.14.15.21", {"start": v(106.28, 49.09) * mm, "end": v(103.13, 49.09) * mm});
            skLineSegment(sketch, "E16.17.15.21", {"start": v(103.13, 49.09) * mm, "end": v(101.55, 51.82) * mm});
            skCircle(sketch, "E16.0.15.22", {"center": v(104.7, 60.45) * mm, "radius": 2.73 * mm, "construction": true});
            skLineSegment(sketch, "E16.2.15.22", {"start": v(101.55, 60.45) * mm, "end": v(103.13, 63.18) * mm});
            skLineSegment(sketch, "E16.5.15.22", {"start": v(103.13, 63.18) * mm, "end": v(106.28, 63.18) * mm});
            skLineSegment(sketch, "E16.8.15.22", {"start": v(106.28, 63.18) * mm, "end": v(107.86, 60.45) * mm});
            skLineSegment(sketch, "E16.11.15.22", {"start": v(107.86, 60.45) * mm, "end": v(106.28, 57.72) * mm});
            skLineSegment(sketch, "E16.14.15.22", {"start": v(106.28, 57.72) * mm, "end": v(103.13, 57.72) * mm});
            skLineSegment(sketch, "E16.17.15.22", {"start": v(103.13, 57.72) * mm, "end": v(101.55, 60.45) * mm});
            skCircle(sketch, "E16.0.15.23", {"center": v(104.7, 69.09) * mm, "radius": 2.73 * mm, "construction": true});
            skLineSegment(sketch, "E16.2.15.23", {"start": v(101.55, 69.09) * mm, "end": v(103.13, 71.82) * mm});
            skLineSegment(sketch, "E16.5.15.23", {"start": v(103.13, 71.82) * mm, "end": v(106.28, 71.82) * mm});
            skLineSegment(sketch, "E16.8.15.23", {"start": v(106.28, 71.82) * mm, "end": v(107.86, 69.09) * mm});
            skLineSegment(sketch, "E16.11.15.23", {"start": v(107.86, 69.09) * mm, "end": v(106.28, 66.36) * mm});
            skLineSegment(sketch, "E16.14.15.23", {"start": v(106.28, 66.36) * mm, "end": v(103.13, 66.36) * mm});
            skLineSegment(sketch, "E16.17.15.23", {"start": v(103.13, 66.36) * mm, "end": v(101.55, 69.09) * mm});
            skCircle(sketch, "E16.0.15.24", {"center": v(104.7, 77.72) * mm, "radius": 2.73 * mm, "construction": true});
            skLineSegment(sketch, "E16.2.15.24", {"start": v(101.55, 77.72) * mm, "end": v(103.13, 80.45) * mm});
            skLineSegment(sketch, "E16.5.15.24", {"start": v(103.13, 80.45) * mm, "end": v(106.28, 80.45) * mm});
            skLineSegment(sketch, "E16.8.15.24", {"start": v(106.28, 80.45) * mm, "end": v(107.86, 77.72) * mm});
            skLineSegment(sketch, "E16.11.15.24", {"start": v(107.86, 77.72) * mm, "end": v(106.28, 75) * mm});
            skLineSegment(sketch, "E16.14.15.24", {"start": v(106.28, 75) * mm, "end": v(103.13, 75) * mm});
            skLineSegment(sketch, "E16.17.15.24", {"start": v(103.13, 75) * mm, "end": v(101.55, 77.72) * mm});
            skCircle(sketch, "E16.0.16.20", {"center": v(119.66, 43.18) * mm, "radius": 2.73 * mm, "construction": true});
            skLineSegment(sketch, "E16.2.16.20", {"start": v(116.51, 43.18) * mm, "end": v(118.09, 45.91) * mm});
            skLineSegment(sketch, "E16.5.16.20", {"start": v(118.09, 45.91) * mm, "end": v(121.24, 45.91) * mm});
            skLineSegment(sketch, "E16.8.16.20", {"start": v(121.24, 45.91) * mm, "end": v(122.82, 43.18) * mm});
            skLineSegment(sketch, "E16.11.16.20", {"start": v(122.82, 43.18) * mm, "end": v(121.24, 40.45) * mm});
            skLineSegment(sketch, "E16.14.16.20", {"start": v(121.24, 40.45) * mm, "end": v(118.09, 40.45) * mm});
            skLineSegment(sketch, "E16.17.16.20", {"start": v(118.09, 40.45) * mm, "end": v(116.51, 43.18) * mm});
            skCircle(sketch, "E16.0.16.21", {"center": v(119.66, 51.82) * mm, "radius": 2.73 * mm, "construction": true});
            skLineSegment(sketch, "E16.2.16.21", {"start": v(116.51, 51.82) * mm, "end": v(118.09, 54.55) * mm});
            skLineSegment(sketch, "E16.5.16.21", {"start": v(118.09, 54.55) * mm, "end": v(121.24, 54.55) * mm});
            skLineSegment(sketch, "E16.8.16.21", {"start": v(121.24, 54.55) * mm, "end": v(122.82, 51.82) * mm});
            skLineSegment(sketch, "E16.11.16.21", {"start": v(122.82, 51.82) * mm, "end": v(121.24, 49.09) * mm});
            skLineSegment(sketch, "E16.14.16.21", {"start": v(121.24, 49.09) * mm, "end": v(118.09, 49.09) * mm});
            skLineSegment(sketch, "E16.17.16.21", {"start": v(118.09, 49.09) * mm, "end": v(116.51, 51.82) * mm});
            skCircle(sketch, "E16.0.16.22", {"center": v(119.66, 60.45) * mm, "radius": 2.73 * mm, "construction": true});
            skLineSegment(sketch, "E16.2.16.22", {"start": v(116.51, 60.45) * mm, "end": v(118.09, 63.18) * mm});
            skLineSegment(sketch, "E16.5.16.22", {"start": v(118.09, 63.18) * mm, "end": v(121.24, 63.18) * mm});
            skLineSegment(sketch, "E16.8.16.22", {"start": v(121.24, 63.18) * mm, "end": v(122.82, 60.45) * mm});
            skLineSegment(sketch, "E16.11.16.22", {"start": v(122.82, 60.45) * mm, "end": v(121.24, 57.72) * mm});
            skLineSegment(sketch, "E16.14.16.22", {"start": v(121.24, 57.72) * mm, "end": v(118.09, 57.72) * mm});
            skLineSegment(sketch, "E16.17.16.22", {"start": v(118.09, 57.72) * mm, "end": v(116.51, 60.45) * mm});
            skCircle(sketch, "E16.0.16.23", {"center": v(119.66, 69.09) * mm, "radius": 2.73 * mm, "construction": true});
            skLineSegment(sketch, "E16.2.16.23", {"start": v(116.51, 69.09) * mm, "end": v(118.09, 71.82) * mm});
            skLineSegment(sketch, "E16.5.16.23", {"start": v(118.09, 71.82) * mm, "end": v(121.24, 71.82) * mm});
            skLineSegment(sketch, "E16.8.16.23", {"start": v(121.24, 71.82) * mm, "end": v(122.82, 69.09) * mm});
            skLineSegment(sketch, "E16.11.16.23", {"start": v(122.82, 69.09) * mm, "end": v(121.24, 66.36) * mm});
            skLineSegment(sketch, "E16.14.16.23", {"start": v(121.24, 66.36) * mm, "end": v(118.09, 66.36) * mm});
            skLineSegment(sketch, "E16.17.16.23", {"start": v(118.09, 66.36) * mm, "end": v(116.51, 69.09) * mm});
            skCircle(sketch, "E16.0.16.24", {"center": v(119.66, 77.72) * mm, "radius": 2.73 * mm, "construction": true});
            skLineSegment(sketch, "E16.2.16.24", {"start": v(116.51, 77.72) * mm, "end": v(118.09, 80.45) * mm});
            skLineSegment(sketch, "E16.5.16.24", {"start": v(118.09, 80.45) * mm, "end": v(121.24, 80.45) * mm});
            skLineSegment(sketch, "E16.8.16.24", {"start": v(121.24, 80.45) * mm, "end": v(122.82, 77.72) * mm});
            skLineSegment(sketch, "E16.11.16.24", {"start": v(122.82, 77.72) * mm, "end": v(121.24, 75) * mm});
            skLineSegment(sketch, "E16.14.16.24", {"start": v(121.24, 75) * mm, "end": v(118.09, 75) * mm});
            skLineSegment(sketch, "E16.17.16.24", {"start": v(118.09, 75) * mm, "end": v(116.51, 77.72) * mm});
            skCircle(sketch, "E16.0.17.20", {"center": v(134.62, 43.18) * mm, "radius": 2.73 * mm, "construction": true});
            skLineSegment(sketch, "E16.2.17.20", {"start": v(131.47, 43.18) * mm, "end": v(133.05, 45.91) * mm});
            skLineSegment(sketch, "E16.5.17.20", {"start": v(133.05, 45.91) * mm, "end": v(136.2, 45.91) * mm});
            skLineSegment(sketch, "E16.8.17.20", {"start": v(136.2, 45.91) * mm, "end": v(137.78, 43.18) * mm});
            skLineSegment(sketch, "E16.11.17.20", {"start": v(137.78, 43.18) * mm, "end": v(136.2, 40.45) * mm});
            skLineSegment(sketch, "E16.14.17.20", {"start": v(136.2, 40.45) * mm, "end": v(133.05, 40.45) * mm});
            skLineSegment(sketch, "E16.17.17.20", {"start": v(133.05, 40.45) * mm, "end": v(131.47, 43.18) * mm});
            skCircle(sketch, "E16.0.17.21", {"center": v(134.62, 51.82) * mm, "radius": 2.73 * mm, "construction": true});
            skLineSegment(sketch, "E16.2.17.21", {"start": v(131.47, 51.82) * mm, "end": v(133.05, 54.55) * mm});
            skLineSegment(sketch, "E16.5.17.21", {"start": v(133.05, 54.55) * mm, "end": v(136.2, 54.55) * mm});
            skLineSegment(sketch, "E16.8.17.21", {"start": v(136.2, 54.55) * mm, "end": v(137.78, 51.82) * mm});
            skLineSegment(sketch, "E16.11.17.21", {"start": v(137.78, 51.82) * mm, "end": v(136.2, 49.09) * mm});
            skLineSegment(sketch, "E16.14.17.21", {"start": v(136.2, 49.09) * mm, "end": v(133.05, 49.09) * mm});
            skLineSegment(sketch, "E16.17.17.21", {"start": v(133.05, 49.09) * mm, "end": v(131.47, 51.82) * mm});
            skCircle(sketch, "E16.0.17.22", {"center": v(134.62, 60.45) * mm, "radius": 2.73 * mm, "construction": true});
            skLineSegment(sketch, "E16.2.17.22", {"start": v(131.47, 60.45) * mm, "end": v(133.05, 63.18) * mm});
            skLineSegment(sketch, "E16.5.17.22", {"start": v(133.05, 63.18) * mm, "end": v(136.2, 63.18) * mm});
            skLineSegment(sketch, "E16.8.17.22", {"start": v(136.2, 63.18) * mm, "end": v(137.78, 60.45) * mm});
            skLineSegment(sketch, "E16.11.17.22", {"start": v(137.78, 60.45) * mm, "end": v(136.2, 57.72) * mm});
            skLineSegment(sketch, "E16.14.17.22", {"start": v(136.2, 57.72) * mm, "end": v(133.05, 57.72) * mm});
            skLineSegment(sketch, "E16.17.17.22", {"start": v(133.05, 57.72) * mm, "end": v(131.47, 60.45) * mm});
            skCircle(sketch, "E16.0.17.23", {"center": v(134.62, 69.09) * mm, "radius": 2.73 * mm, "construction": true});
            skLineSegment(sketch, "E16.2.17.23", {"start": v(131.47, 69.09) * mm, "end": v(133.05, 71.82) * mm});
            skLineSegment(sketch, "E16.5.17.23", {"start": v(133.05, 71.82) * mm, "end": v(136.2, 71.82) * mm});
            skLineSegment(sketch, "E16.8.17.23", {"start": v(136.2, 71.82) * mm, "end": v(137.78, 69.09) * mm});
            skLineSegment(sketch, "E16.11.17.23", {"start": v(137.78, 69.09) * mm, "end": v(136.2, 66.36) * mm});
            skLineSegment(sketch, "E16.14.17.23", {"start": v(136.2, 66.36) * mm, "end": v(133.05, 66.36) * mm});
            skLineSegment(sketch, "E16.17.17.23", {"start": v(133.05, 66.36) * mm, "end": v(131.47, 69.09) * mm});
            skCircle(sketch, "E16.0.17.24", {"center": v(134.62, 77.72) * mm, "radius": 2.73 * mm, "construction": true});
            skLineSegment(sketch, "E16.2.17.24", {"start": v(131.47, 77.72) * mm, "end": v(133.05, 80.45) * mm});
            skLineSegment(sketch, "E16.5.17.24", {"start": v(133.05, 80.45) * mm, "end": v(136.2, 80.45) * mm});
            skLineSegment(sketch, "E16.8.17.24", {"start": v(136.2, 80.45) * mm, "end": v(137.78, 77.72) * mm});
            skLineSegment(sketch, "E16.11.17.24", {"start": v(137.78, 77.72) * mm, "end": v(136.2, 75) * mm});
            skLineSegment(sketch, "E16.14.17.24", {"start": v(136.2, 75) * mm, "end": v(133.05, 75) * mm});
            skLineSegment(sketch, "E16.17.17.24", {"start": v(133.05, 75) * mm, "end": v(131.47, 77.72) * mm});
            skCircle(sketch, "E16.0.18.20", {"center": v(149.58, 43.18) * mm, "radius": 2.73 * mm, "construction": true});
            skLineSegment(sketch, "E16.2.18.20", {"start": v(146.43, 43.18) * mm, "end": v(148, 45.91) * mm});
            skLineSegment(sketch, "E16.5.18.20", {"start": v(148, 45.91) * mm, "end": v(151.16, 45.91) * mm});
            skLineSegment(sketch, "E16.8.18.20", {"start": v(151.16, 45.91) * mm, "end": v(152.73, 43.18) * mm});
            skLineSegment(sketch, "E16.11.18.20", {"start": v(152.73, 43.18) * mm, "end": v(151.16, 40.45) * mm});
            skLineSegment(sketch, "E16.14.18.20", {"start": v(151.16, 40.45) * mm, "end": v(148, 40.45) * mm});
            skLineSegment(sketch, "E16.17.18.20", {"start": v(148, 40.45) * mm, "end": v(146.43, 43.18) * mm});
            skCircle(sketch, "E16.0.18.21", {"center": v(149.58, 51.82) * mm, "radius": 2.73 * mm, "construction": true});
            skLineSegment(sketch, "E16.2.18.21", {"start": v(146.43, 51.82) * mm, "end": v(148, 54.55) * mm});
            skLineSegment(sketch, "E16.5.18.21", {"start": v(148, 54.55) * mm, "end": v(151.16, 54.55) * mm});
            skLineSegment(sketch, "E16.8.18.21", {"start": v(151.16, 54.55) * mm, "end": v(152.73, 51.82) * mm});
            skLineSegment(sketch, "E16.11.18.21", {"start": v(152.73, 51.82) * mm, "end": v(151.16, 49.09) * mm});
            skLineSegment(sketch, "E16.14.18.21", {"start": v(151.16, 49.09) * mm, "end": v(148, 49.09) * mm});
            skLineSegment(sketch, "E16.17.18.21", {"start": v(148, 49.09) * mm, "end": v(146.43, 51.82) * mm});
            skCircle(sketch, "E16.0.18.22", {"center": v(149.58, 60.45) * mm, "radius": 2.73 * mm, "construction": true});
            skLineSegment(sketch, "E16.2.18.22", {"start": v(146.43, 60.45) * mm, "end": v(148, 63.18) * mm});
            skLineSegment(sketch, "E16.5.18.22", {"start": v(148, 63.18) * mm, "end": v(151.16, 63.18) * mm});
            skLineSegment(sketch, "E16.8.18.22", {"start": v(151.16, 63.18) * mm, "end": v(152.73, 60.45) * mm});
            skLineSegment(sketch, "E16.11.18.22", {"start": v(152.73, 60.45) * mm, "end": v(151.16, 57.72) * mm});
            skLineSegment(sketch, "E16.14.18.22", {"start": v(151.16, 57.72) * mm, "end": v(148, 57.72) * mm});
            skLineSegment(sketch, "E16.17.18.22", {"start": v(148, 57.72) * mm, "end": v(146.43, 60.45) * mm});
            skCircle(sketch, "E16.0.18.23", {"center": v(149.58, 69.09) * mm, "radius": 2.73 * mm, "construction": true});
            skLineSegment(sketch, "E16.2.18.23", {"start": v(146.43, 69.09) * mm, "end": v(148, 71.82) * mm});
            skLineSegment(sketch, "E16.5.18.23", {"start": v(148, 71.82) * mm, "end": v(151.16, 71.82) * mm});
            skLineSegment(sketch, "E16.8.18.23", {"start": v(151.16, 71.82) * mm, "end": v(152.73, 69.09) * mm});
            skLineSegment(sketch, "E16.11.18.23", {"start": v(152.73, 69.09) * mm, "end": v(151.16, 66.36) * mm});
            skLineSegment(sketch, "E16.14.18.23", {"start": v(151.16, 66.36) * mm, "end": v(148, 66.36) * mm});
            skLineSegment(sketch, "E16.17.18.23", {"start": v(148, 66.36) * mm, "end": v(146.43, 69.09) * mm});
            skCircle(sketch, "E16.0.18.24", {"center": v(149.58, 77.72) * mm, "radius": 2.73 * mm, "construction": true});
            skLineSegment(sketch, "E16.2.18.24", {"start": v(146.43, 77.72) * mm, "end": v(148, 80.45) * mm});
            skLineSegment(sketch, "E16.5.18.24", {"start": v(148, 80.45) * mm, "end": v(151.16, 80.45) * mm});
            skLineSegment(sketch, "E16.8.18.24", {"start": v(151.16, 80.45) * mm, "end": v(152.73, 77.72) * mm});
            skLineSegment(sketch, "E16.11.18.24", {"start": v(152.73, 77.72) * mm, "end": v(151.16, 75) * mm});
            skLineSegment(sketch, "E16.14.18.24", {"start": v(151.16, 75) * mm, "end": v(148, 75) * mm});
            skLineSegment(sketch, "E16.17.18.24", {"start": v(148, 75) * mm, "end": v(146.43, 77.72) * mm});
            skCircle(sketch, "E16.0.19.20", {"center": v(164.54, 43.18) * mm, "radius": 2.73 * mm, "construction": true});
            skLineSegment(sketch, "E16.2.19.20", {"start": v(161.39, 43.18) * mm, "end": v(162.96, 45.91) * mm});
            skLineSegment(sketch, "E16.5.19.20", {"start": v(162.96, 45.91) * mm, "end": v(166.12, 45.91) * mm});
            skLineSegment(sketch, "E16.8.19.20", {"start": v(166.12, 45.91) * mm, "end": v(167.7, 43.18) * mm});
            skLineSegment(sketch, "E16.11.19.20", {"start": v(167.7, 43.18) * mm, "end": v(166.12, 40.45) * mm});
            skLineSegment(sketch, "E16.14.19.20", {"start": v(166.12, 40.45) * mm, "end": v(162.96, 40.45) * mm});
            skLineSegment(sketch, "E16.17.19.20", {"start": v(162.96, 40.45) * mm, "end": v(161.39, 43.18) * mm});
            skCircle(sketch, "E16.0.19.21", {"center": v(164.54, 51.82) * mm, "radius": 2.73 * mm, "construction": true});
            skLineSegment(sketch, "E16.2.19.21", {"start": v(161.39, 51.82) * mm, "end": v(162.96, 54.55) * mm});
            skLineSegment(sketch, "E16.5.19.21", {"start": v(162.96, 54.55) * mm, "end": v(166.12, 54.55) * mm});
            skLineSegment(sketch, "E16.8.19.21", {"start": v(166.12, 54.55) * mm, "end": v(167.7, 51.82) * mm});
            skLineSegment(sketch, "E16.11.19.21", {"start": v(167.7, 51.82) * mm, "end": v(166.12, 49.09) * mm});
            skLineSegment(sketch, "E16.14.19.21", {"start": v(166.12, 49.09) * mm, "end": v(162.96, 49.09) * mm});
            skLineSegment(sketch, "E16.17.19.21", {"start": v(162.96, 49.09) * mm, "end": v(161.39, 51.82) * mm});
            skCircle(sketch, "E16.0.19.22", {"center": v(164.54, 60.45) * mm, "radius": 2.73 * mm, "construction": true});
            skLineSegment(sketch, "E16.2.19.22", {"start": v(161.39, 60.45) * mm, "end": v(162.96, 63.18) * mm});
            skLineSegment(sketch, "E16.5.19.22", {"start": v(162.96, 63.18) * mm, "end": v(166.12, 63.18) * mm});
            skLineSegment(sketch, "E16.8.19.22", {"start": v(166.12, 63.18) * mm, "end": v(167.7, 60.45) * mm});
            skLineSegment(sketch, "E16.11.19.22", {"start": v(167.7, 60.45) * mm, "end": v(166.12, 57.72) * mm});
            skLineSegment(sketch, "E16.14.19.22", {"start": v(166.12, 57.72) * mm, "end": v(162.96, 57.72) * mm});
            skLineSegment(sketch, "E16.17.19.22", {"start": v(162.96, 57.72) * mm, "end": v(161.39, 60.45) * mm});
            skCircle(sketch, "E16.0.19.23", {"center": v(164.54, 69.09) * mm, "radius": 2.73 * mm, "construction": true});
            skLineSegment(sketch, "E16.2.19.23", {"start": v(161.39, 69.09) * mm, "end": v(162.96, 71.82) * mm});
            skLineSegment(sketch, "E16.5.19.23", {"start": v(162.96, 71.82) * mm, "end": v(166.12, 71.82) * mm});
            skLineSegment(sketch, "E16.8.19.23", {"start": v(166.12, 71.82) * mm, "end": v(167.7, 69.09) * mm});
            skLineSegment(sketch, "E16.11.19.23", {"start": v(167.7, 69.09) * mm, "end": v(166.12, 66.36) * mm});
            skLineSegment(sketch, "E16.14.19.23", {"start": v(166.12, 66.36) * mm, "end": v(162.96, 66.36) * mm});
            skLineSegment(sketch, "E16.17.19.23", {"start": v(162.96, 66.36) * mm, "end": v(161.39, 69.09) * mm});
            skCircle(sketch, "E16.0.19.24", {"center": v(164.54, 77.72) * mm, "radius": 2.73 * mm, "construction": true});
            skLineSegment(sketch, "E16.2.19.24", {"start": v(161.39, 77.72) * mm, "end": v(162.96, 80.45) * mm});
            skLineSegment(sketch, "E16.5.19.24", {"start": v(162.96, 80.45) * mm, "end": v(166.12, 80.45) * mm});
            skLineSegment(sketch, "E16.8.19.24", {"start": v(166.12, 80.45) * mm, "end": v(167.7, 77.72) * mm});
            skLineSegment(sketch, "E16.11.19.24", {"start": v(167.7, 77.72) * mm, "end": v(166.12, 75) * mm});
            skLineSegment(sketch, "E16.14.19.24", {"start": v(166.12, 75) * mm, "end": v(162.96, 75) * mm});
            skLineSegment(sketch, "E16.17.19.24", {"start": v(162.96, 75) * mm, "end": v(161.39, 77.72) * mm});
            skLineSegment(sketch, "E17.0.0.20", {"start": v(-128.72, 41.6) * mm, "end": v(-125.57, 41.6) * mm});
            skLineSegment(sketch, "E17.3.0.20", {"start": v(-125.57, 41.6) * mm, "end": v(-124, 38.86) * mm});
            skLineSegment(sketch, "E17.6.0.20", {"start": v(-124, 38.86) * mm, "end": v(-125.57, 36.13) * mm});
            skCircle(sketch, "E17.9.0.20", {"center": v(-127.14, 38.86) * mm, "radius": 2.73 * mm, "construction": true});
            skLineSegment(sketch, "E17.11.0.20", {"start": v(-125.57, 36.13) * mm, "end": v(-128.72, 36.13) * mm});
            skLineSegment(sketch, "E17.14.0.20", {"start": v(-128.72, 36.13) * mm, "end": v(-130.3, 38.86) * mm});
            skLineSegment(sketch, "E17.17.0.20", {"start": v(-130.3, 38.86) * mm, "end": v(-128.72, 41.6) * mm});
            skLineSegment(sketch, "E17.0.0.21", {"start": v(-128.72, 50.23) * mm, "end": v(-125.57, 50.23) * mm});
            skLineSegment(sketch, "E17.3.0.21", {"start": v(-125.57, 50.23) * mm, "end": v(-124, 47.5) * mm});
            skLineSegment(sketch, "E17.6.0.21", {"start": v(-124, 47.5) * mm, "end": v(-125.57, 44.77) * mm});
            skCircle(sketch, "E17.9.0.21", {"center": v(-127.14, 47.5) * mm, "radius": 2.73 * mm, "construction": true});
            skLineSegment(sketch, "E17.11.0.21", {"start": v(-125.57, 44.77) * mm, "end": v(-128.72, 44.77) * mm});
            skLineSegment(sketch, "E17.14.0.21", {"start": v(-128.72, 44.77) * mm, "end": v(-130.3, 47.5) * mm});
            skLineSegment(sketch, "E17.17.0.21", {"start": v(-130.3, 47.5) * mm, "end": v(-128.72, 50.23) * mm});
            skLineSegment(sketch, "E17.0.0.22", {"start": v(-128.72, 58.86) * mm, "end": v(-125.57, 58.86) * mm});
            skLineSegment(sketch, "E17.3.0.22", {"start": v(-125.57, 58.86) * mm, "end": v(-124, 56.13) * mm});
            skLineSegment(sketch, "E17.6.0.22", {"start": v(-124, 56.13) * mm, "end": v(-125.57, 53.4) * mm});
            skCircle(sketch, "E17.9.0.22", {"center": v(-127.14, 56.13) * mm, "radius": 2.73 * mm, "construction": true});
            skLineSegment(sketch, "E17.11.0.22", {"start": v(-125.57, 53.4) * mm, "end": v(-128.72, 53.4) * mm});
            skLineSegment(sketch, "E17.14.0.22", {"start": v(-128.72, 53.4) * mm, "end": v(-130.3, 56.13) * mm});
            skLineSegment(sketch, "E17.17.0.22", {"start": v(-130.3, 56.13) * mm, "end": v(-128.72, 58.86) * mm});
            skLineSegment(sketch, "E17.0.0.23", {"start": v(-128.72, 67.5) * mm, "end": v(-125.57, 67.5) * mm});
            skLineSegment(sketch, "E17.3.0.23", {"start": v(-125.57, 67.5) * mm, "end": v(-124, 64.77) * mm});
            skLineSegment(sketch, "E17.6.0.23", {"start": v(-124, 64.77) * mm, "end": v(-125.57, 62.04) * mm});
            skCircle(sketch, "E17.9.0.23", {"center": v(-127.14, 64.77) * mm, "radius": 2.73 * mm, "construction": true});
            skLineSegment(sketch, "E17.11.0.23", {"start": v(-125.57, 62.04) * mm, "end": v(-128.72, 62.04) * mm});
            skLineSegment(sketch, "E17.14.0.23", {"start": v(-128.72, 62.04) * mm, "end": v(-130.3, 64.77) * mm});
            skLineSegment(sketch, "E17.17.0.23", {"start": v(-130.3, 64.77) * mm, "end": v(-128.72, 67.5) * mm});
            skLineSegment(sketch, "E17.0.0.24", {"start": v(-128.72, 76.14) * mm, "end": v(-125.57, 76.14) * mm});
            skLineSegment(sketch, "E17.3.0.24", {"start": v(-125.57, 76.14) * mm, "end": v(-124, 73.4) * mm});
            skLineSegment(sketch, "E17.6.0.24", {"start": v(-124, 73.4) * mm, "end": v(-125.57, 70.68) * mm});
            skCircle(sketch, "E17.9.0.24", {"center": v(-127.14, 73.4) * mm, "radius": 2.73 * mm, "construction": true});
            skLineSegment(sketch, "E17.11.0.24", {"start": v(-125.57, 70.68) * mm, "end": v(-128.72, 70.68) * mm});
            skLineSegment(sketch, "E17.14.0.24", {"start": v(-128.72, 70.68) * mm, "end": v(-130.3, 73.4) * mm});
            skLineSegment(sketch, "E17.17.0.24", {"start": v(-130.3, 73.4) * mm, "end": v(-128.72, 76.14) * mm});
            skLineSegment(sketch, "E17.0.1.20", {"start": v(-113.76, 41.6) * mm, "end": v(-110.6, 41.6) * mm});
            skLineSegment(sketch, "E17.3.1.20", {"start": v(-110.6, 41.6) * mm, "end": v(-109.03, 38.86) * mm});
            skLineSegment(sketch, "E17.6.1.20", {"start": v(-109.03, 38.86) * mm, "end": v(-110.6, 36.13) * mm});
            skCircle(sketch, "E17.9.1.20", {"center": v(-112.19, 38.86) * mm, "radius": 2.73 * mm, "construction": true});
            skLineSegment(sketch, "E17.11.1.20", {"start": v(-110.6, 36.13) * mm, "end": v(-113.76, 36.13) * mm});
            skLineSegment(sketch, "E17.14.1.20", {"start": v(-113.76, 36.13) * mm, "end": v(-115.34, 38.86) * mm});
            skLineSegment(sketch, "E17.17.1.20", {"start": v(-115.34, 38.86) * mm, "end": v(-113.76, 41.6) * mm});
            skLineSegment(sketch, "E17.0.1.21", {"start": v(-113.76, 50.23) * mm, "end": v(-110.6, 50.23) * mm});
            skLineSegment(sketch, "E17.3.1.21", {"start": v(-110.6, 50.23) * mm, "end": v(-109.03, 47.5) * mm});
            skLineSegment(sketch, "E17.6.1.21", {"start": v(-109.03, 47.5) * mm, "end": v(-110.6, 44.77) * mm});
            skCircle(sketch, "E17.9.1.21", {"center": v(-112.19, 47.5) * mm, "radius": 2.73 * mm, "construction": true});
            skLineSegment(sketch, "E17.11.1.21", {"start": v(-110.6, 44.77) * mm, "end": v(-113.76, 44.77) * mm});
            skLineSegment(sketch, "E17.14.1.21", {"start": v(-113.76, 44.77) * mm, "end": v(-115.34, 47.5) * mm});
            skLineSegment(sketch, "E17.17.1.21", {"start": v(-115.34, 47.5) * mm, "end": v(-113.76, 50.23) * mm});
            skLineSegment(sketch, "E17.0.1.22", {"start": v(-113.76, 58.86) * mm, "end": v(-110.6, 58.86) * mm});
            skLineSegment(sketch, "E17.3.1.22", {"start": v(-110.6, 58.86) * mm, "end": v(-109.03, 56.13) * mm});
            skLineSegment(sketch, "E17.6.1.22", {"start": v(-109.03, 56.13) * mm, "end": v(-110.6, 53.4) * mm});
            skCircle(sketch, "E17.9.1.22", {"center": v(-112.19, 56.13) * mm, "radius": 2.73 * mm, "construction": true});
            skLineSegment(sketch, "E17.11.1.22", {"start": v(-110.6, 53.4) * mm, "end": v(-113.76, 53.4) * mm});
            skLineSegment(sketch, "E17.14.1.22", {"start": v(-113.76, 53.4) * mm, "end": v(-115.34, 56.13) * mm});
            skLineSegment(sketch, "E17.17.1.22", {"start": v(-115.34, 56.13) * mm, "end": v(-113.76, 58.86) * mm});
            skLineSegment(sketch, "E17.0.1.23", {"start": v(-113.76, 67.5) * mm, "end": v(-110.6, 67.5) * mm});
            skLineSegment(sketch, "E17.3.1.23", {"start": v(-110.6, 67.5) * mm, "end": v(-109.03, 64.77) * mm});
            skLineSegment(sketch, "E17.6.1.23", {"start": v(-109.03, 64.77) * mm, "end": v(-110.6, 62.04) * mm});
            skCircle(sketch, "E17.9.1.23", {"center": v(-112.19, 64.77) * mm, "radius": 2.73 * mm, "construction": true});
            skLineSegment(sketch, "E17.11.1.23", {"start": v(-110.6, 62.04) * mm, "end": v(-113.76, 62.04) * mm});
            skLineSegment(sketch, "E17.14.1.23", {"start": v(-113.76, 62.04) * mm, "end": v(-115.34, 64.77) * mm});
            skLineSegment(sketch, "E17.17.1.23", {"start": v(-115.34, 64.77) * mm, "end": v(-113.76, 67.5) * mm});
            skLineSegment(sketch, "E17.0.1.24", {"start": v(-113.76, 76.14) * mm, "end": v(-110.6, 76.14) * mm});
            skLineSegment(sketch, "E17.3.1.24", {"start": v(-110.6, 76.14) * mm, "end": v(-109.03, 73.4) * mm});
            skLineSegment(sketch, "E17.6.1.24", {"start": v(-109.03, 73.4) * mm, "end": v(-110.6, 70.68) * mm});
            skCircle(sketch, "E17.9.1.24", {"center": v(-112.19, 73.4) * mm, "radius": 2.73 * mm, "construction": true});
            skLineSegment(sketch, "E17.11.1.24", {"start": v(-110.6, 70.68) * mm, "end": v(-113.76, 70.68) * mm});
            skLineSegment(sketch, "E17.14.1.24", {"start": v(-113.76, 70.68) * mm, "end": v(-115.34, 73.4) * mm});
            skLineSegment(sketch, "E17.17.1.24", {"start": v(-115.34, 73.4) * mm, "end": v(-113.76, 76.14) * mm});
            skLineSegment(sketch, "E17.0.2.20", {"start": v(-98.8, 41.6) * mm, "end": v(-95.65, 41.6) * mm});
            skLineSegment(sketch, "E17.3.2.20", {"start": v(-95.65, 41.6) * mm, "end": v(-94.07, 38.86) * mm});
            skLineSegment(sketch, "E17.6.2.20", {"start": v(-94.07, 38.86) * mm, "end": v(-95.65, 36.13) * mm});
            skCircle(sketch, "E17.9.2.20", {"center": v(-97.23, 38.86) * mm, "radius": 2.73 * mm, "construction": true});
            skLineSegment(sketch, "E17.11.2.20", {"start": v(-95.65, 36.13) * mm, "end": v(-98.8, 36.13) * mm});
            skLineSegment(sketch, "E17.14.2.20", {"start": v(-98.8, 36.13) * mm, "end": v(-100.38, 38.86) * mm});
            skLineSegment(sketch, "E17.17.2.20", {"start": v(-100.38, 38.86) * mm, "end": v(-98.8, 41.6) * mm});
            skLineSegment(sketch, "E17.0.2.21", {"start": v(-98.8, 50.23) * mm, "end": v(-95.65, 50.23) * mm});
            skLineSegment(sketch, "E17.3.2.21", {"start": v(-95.65, 50.23) * mm, "end": v(-94.07, 47.5) * mm});
            skLineSegment(sketch, "E17.6.2.21", {"start": v(-94.07, 47.5) * mm, "end": v(-95.65, 44.77) * mm});
            skCircle(sketch, "E17.9.2.21", {"center": v(-97.23, 47.5) * mm, "radius": 2.73 * mm, "construction": true});
            skLineSegment(sketch, "E17.11.2.21", {"start": v(-95.65, 44.77) * mm, "end": v(-98.8, 44.77) * mm});
            skLineSegment(sketch, "E17.14.2.21", {"start": v(-98.8, 44.77) * mm, "end": v(-100.38, 47.5) * mm});
            skLineSegment(sketch, "E17.17.2.21", {"start": v(-100.38, 47.5) * mm, "end": v(-98.8, 50.23) * mm});
            skLineSegment(sketch, "E17.0.2.22", {"start": v(-98.8, 58.86) * mm, "end": v(-95.65, 58.86) * mm});
            skLineSegment(sketch, "E17.3.2.22", {"start": v(-95.65, 58.86) * mm, "end": v(-94.07, 56.13) * mm});
            skLineSegment(sketch, "E17.6.2.22", {"start": v(-94.07, 56.13) * mm, "end": v(-95.65, 53.4) * mm});
            skCircle(sketch, "E17.9.2.22", {"center": v(-97.23, 56.13) * mm, "radius": 2.73 * mm, "construction": true});
            skLineSegment(sketch, "E17.11.2.22", {"start": v(-95.65, 53.4) * mm, "end": v(-98.8, 53.4) * mm});
            skLineSegment(sketch, "E17.14.2.22", {"start": v(-98.8, 53.4) * mm, "end": v(-100.38, 56.13) * mm});
            skLineSegment(sketch, "E17.17.2.22", {"start": v(-100.38, 56.13) * mm, "end": v(-98.8, 58.86) * mm});
            skLineSegment(sketch, "E17.0.2.23", {"start": v(-98.8, 67.5) * mm, "end": v(-95.65, 67.5) * mm});
            skLineSegment(sketch, "E17.3.2.23", {"start": v(-95.65, 67.5) * mm, "end": v(-94.07, 64.77) * mm});
            skLineSegment(sketch, "E17.6.2.23", {"start": v(-94.07, 64.77) * mm, "end": v(-95.65, 62.04) * mm});
            skCircle(sketch, "E17.9.2.23", {"center": v(-97.23, 64.77) * mm, "radius": 2.73 * mm, "construction": true});
            skLineSegment(sketch, "E17.11.2.23", {"start": v(-95.65, 62.04) * mm, "end": v(-98.8, 62.04) * mm});
            skLineSegment(sketch, "E17.14.2.23", {"start": v(-98.8, 62.04) * mm, "end": v(-100.38, 64.77) * mm});
            skLineSegment(sketch, "E17.17.2.23", {"start": v(-100.38, 64.77) * mm, "end": v(-98.8, 67.5) * mm});
            skLineSegment(sketch, "E17.0.2.24", {"start": v(-98.8, 76.14) * mm, "end": v(-95.65, 76.14) * mm});
            skLineSegment(sketch, "E17.3.2.24", {"start": v(-95.65, 76.14) * mm, "end": v(-94.07, 73.4) * mm});
            skLineSegment(sketch, "E17.6.2.24", {"start": v(-94.07, 73.4) * mm, "end": v(-95.65, 70.68) * mm});
            skCircle(sketch, "E17.9.2.24", {"center": v(-97.23, 73.4) * mm, "radius": 2.73 * mm, "construction": true});
            skLineSegment(sketch, "E17.11.2.24", {"start": v(-95.65, 70.68) * mm, "end": v(-98.8, 70.68) * mm});
            skLineSegment(sketch, "E17.14.2.24", {"start": v(-98.8, 70.68) * mm, "end": v(-100.38, 73.4) * mm});
            skLineSegment(sketch, "E17.17.2.24", {"start": v(-100.38, 73.4) * mm, "end": v(-98.8, 76.14) * mm});
            skLineSegment(sketch, "E17.0.3.20", {"start": v(-83.85, 41.6) * mm, "end": v(-80.7, 41.6) * mm});
            skLineSegment(sketch, "E17.3.3.20", {"start": v(-80.7, 41.6) * mm, "end": v(-79.12, 38.86) * mm});
            skLineSegment(sketch, "E17.6.3.20", {"start": v(-79.12, 38.86) * mm, "end": v(-80.7, 36.13) * mm});
            skCircle(sketch, "E17.9.3.20", {"center": v(-82.27, 38.86) * mm, "radius": 2.73 * mm, "construction": true});
            skLineSegment(sketch, "E17.11.3.20", {"start": v(-80.7, 36.13) * mm, "end": v(-83.85, 36.13) * mm});
            skLineSegment(sketch, "E17.14.3.20", {"start": v(-83.85, 36.13) * mm, "end": v(-85.42, 38.86) * mm});
            skLineSegment(sketch, "E17.17.3.20", {"start": v(-85.42, 38.86) * mm, "end": v(-83.85, 41.6) * mm});
            skLineSegment(sketch, "E17.0.3.21", {"start": v(-83.85, 50.23) * mm, "end": v(-80.7, 50.23) * mm});
            skLineSegment(sketch, "E17.3.3.21", {"start": v(-80.7, 50.23) * mm, "end": v(-79.12, 47.5) * mm});
            skLineSegment(sketch, "E17.6.3.21", {"start": v(-79.12, 47.5) * mm, "end": v(-80.7, 44.77) * mm});
            skCircle(sketch, "E17.9.3.21", {"center": v(-82.27, 47.5) * mm, "radius": 2.73 * mm, "construction": true});
            skLineSegment(sketch, "E17.11.3.21", {"start": v(-80.7, 44.77) * mm, "end": v(-83.85, 44.77) * mm});
            skLineSegment(sketch, "E17.14.3.21", {"start": v(-83.85, 44.77) * mm, "end": v(-85.42, 47.5) * mm});
            skLineSegment(sketch, "E17.17.3.21", {"start": v(-85.42, 47.5) * mm, "end": v(-83.85, 50.23) * mm});
            skLineSegment(sketch, "E17.0.3.22", {"start": v(-83.85, 58.86) * mm, "end": v(-80.7, 58.86) * mm});
            skLineSegment(sketch, "E17.3.3.22", {"start": v(-80.7, 58.86) * mm, "end": v(-79.12, 56.13) * mm});
            skLineSegment(sketch, "E17.6.3.22", {"start": v(-79.12, 56.13) * mm, "end": v(-80.7, 53.4) * mm});
            skCircle(sketch, "E17.9.3.22", {"center": v(-82.27, 56.13) * mm, "radius": 2.73 * mm, "construction": true});
            skLineSegment(sketch, "E17.11.3.22", {"start": v(-80.7, 53.4) * mm, "end": v(-83.85, 53.4) * mm});
            skLineSegment(sketch, "E17.14.3.22", {"start": v(-83.85, 53.4) * mm, "end": v(-85.42, 56.13) * mm});
            skLineSegment(sketch, "E17.17.3.22", {"start": v(-85.42, 56.13) * mm, "end": v(-83.85, 58.86) * mm});
            skLineSegment(sketch, "E17.0.3.23", {"start": v(-83.85, 67.5) * mm, "end": v(-80.7, 67.5) * mm});
            skLineSegment(sketch, "E17.3.3.23", {"start": v(-80.7, 67.5) * mm, "end": v(-79.12, 64.77) * mm});
            skLineSegment(sketch, "E17.6.3.23", {"start": v(-79.12, 64.77) * mm, "end": v(-80.7, 62.04) * mm});
            skCircle(sketch, "E17.9.3.23", {"center": v(-82.27, 64.77) * mm, "radius": 2.73 * mm, "construction": true});
            skLineSegment(sketch, "E17.11.3.23", {"start": v(-80.7, 62.04) * mm, "end": v(-83.85, 62.04) * mm});
            skLineSegment(sketch, "E17.14.3.23", {"start": v(-83.85, 62.04) * mm, "end": v(-85.42, 64.77) * mm});
            skLineSegment(sketch, "E17.17.3.23", {"start": v(-85.42, 64.77) * mm, "end": v(-83.85, 67.5) * mm});
            skLineSegment(sketch, "E17.0.3.24", {"start": v(-83.85, 76.14) * mm, "end": v(-80.7, 76.14) * mm});
            skLineSegment(sketch, "E17.3.3.24", {"start": v(-80.7, 76.14) * mm, "end": v(-79.12, 73.4) * mm});
            skLineSegment(sketch, "E17.6.3.24", {"start": v(-79.12, 73.4) * mm, "end": v(-80.7, 70.68) * mm});
            skCircle(sketch, "E17.9.3.24", {"center": v(-82.27, 73.4) * mm, "radius": 2.73 * mm, "construction": true});
            skLineSegment(sketch, "E17.11.3.24", {"start": v(-80.7, 70.68) * mm, "end": v(-83.85, 70.68) * mm});
            skLineSegment(sketch, "E17.14.3.24", {"start": v(-83.85, 70.68) * mm, "end": v(-85.42, 73.4) * mm});
            skLineSegment(sketch, "E17.17.3.24", {"start": v(-85.42, 73.4) * mm, "end": v(-83.85, 76.14) * mm});
            skLineSegment(sketch, "E17.0.4.20", {"start": v(-68.89, 41.6) * mm, "end": v(-65.73, 41.6) * mm});
            skLineSegment(sketch, "E17.3.4.20", {"start": v(-65.73, 41.6) * mm, "end": v(-64.16, 38.86) * mm});
            skLineSegment(sketch, "E17.6.4.20", {"start": v(-64.16, 38.86) * mm, "end": v(-65.73, 36.13) * mm});
            skCircle(sketch, "E17.9.4.20", {"center": v(-67.31, 38.86) * mm, "radius": 2.73 * mm, "construction": true});
            skLineSegment(sketch, "E17.11.4.20", {"start": v(-65.73, 36.13) * mm, "end": v(-68.89, 36.13) * mm});
            skLineSegment(sketch, "E17.14.4.20", {"start": v(-68.89, 36.13) * mm, "end": v(-70.46, 38.86) * mm});
            skLineSegment(sketch, "E17.17.4.20", {"start": v(-70.46, 38.86) * mm, "end": v(-68.89, 41.6) * mm});
            skLineSegment(sketch, "E17.0.4.21", {"start": v(-68.89, 50.23) * mm, "end": v(-65.73, 50.23) * mm});
            skLineSegment(sketch, "E17.3.4.21", {"start": v(-65.73, 50.23) * mm, "end": v(-64.16, 47.5) * mm});
            skLineSegment(sketch, "E17.6.4.21", {"start": v(-64.16, 47.5) * mm, "end": v(-65.73, 44.77) * mm});
            skCircle(sketch, "E17.9.4.21", {"center": v(-67.31, 47.5) * mm, "radius": 2.73 * mm, "construction": true});
            skLineSegment(sketch, "E17.11.4.21", {"start": v(-65.73, 44.77) * mm, "end": v(-68.89, 44.77) * mm});
            skLineSegment(sketch, "E17.14.4.21", {"start": v(-68.89, 44.77) * mm, "end": v(-70.46, 47.5) * mm});
            skLineSegment(sketch, "E17.17.4.21", {"start": v(-70.46, 47.5) * mm, "end": v(-68.89, 50.23) * mm});
            skLineSegment(sketch, "E17.0.4.22", {"start": v(-68.89, 58.86) * mm, "end": v(-65.73, 58.86) * mm});
            skLineSegment(sketch, "E17.3.4.22", {"start": v(-65.73, 58.86) * mm, "end": v(-64.16, 56.13) * mm});
            skLineSegment(sketch, "E17.6.4.22", {"start": v(-64.16, 56.13) * mm, "end": v(-65.73, 53.4) * mm});
            skCircle(sketch, "E17.9.4.22", {"center": v(-67.31, 56.13) * mm, "radius": 2.73 * mm, "construction": true});
            skLineSegment(sketch, "E17.11.4.22", {"start": v(-65.73, 53.4) * mm, "end": v(-68.89, 53.4) * mm});
            skLineSegment(sketch, "E17.14.4.22", {"start": v(-68.89, 53.4) * mm, "end": v(-70.46, 56.13) * mm});
            skLineSegment(sketch, "E17.17.4.22", {"start": v(-70.46, 56.13) * mm, "end": v(-68.89, 58.86) * mm});
            skLineSegment(sketch, "E17.0.4.23", {"start": v(-68.89, 67.5) * mm, "end": v(-65.73, 67.5) * mm});
            skLineSegment(sketch, "E17.3.4.23", {"start": v(-65.73, 67.5) * mm, "end": v(-64.16, 64.77) * mm});
            skLineSegment(sketch, "E17.6.4.23", {"start": v(-64.16, 64.77) * mm, "end": v(-65.73, 62.04) * mm});
            skCircle(sketch, "E17.9.4.23", {"center": v(-67.31, 64.77) * mm, "radius": 2.73 * mm, "construction": true});
            skLineSegment(sketch, "E17.11.4.23", {"start": v(-65.73, 62.04) * mm, "end": v(-68.89, 62.04) * mm});
            skLineSegment(sketch, "E17.14.4.23", {"start": v(-68.89, 62.04) * mm, "end": v(-70.46, 64.77) * mm});
            skLineSegment(sketch, "E17.17.4.23", {"start": v(-70.46, 64.77) * mm, "end": v(-68.89, 67.5) * mm});
            skLineSegment(sketch, "E17.0.4.24", {"start": v(-68.89, 76.14) * mm, "end": v(-65.73, 76.14) * mm});
            skLineSegment(sketch, "E17.3.4.24", {"start": v(-65.73, 76.14) * mm, "end": v(-64.16, 73.4) * mm});
            skLineSegment(sketch, "E17.6.4.24", {"start": v(-64.16, 73.4) * mm, "end": v(-65.73, 70.68) * mm});
            skCircle(sketch, "E17.9.4.24", {"center": v(-67.31, 73.4) * mm, "radius": 2.73 * mm, "construction": true});
            skLineSegment(sketch, "E17.11.4.24", {"start": v(-65.73, 70.68) * mm, "end": v(-68.89, 70.68) * mm});
            skLineSegment(sketch, "E17.14.4.24", {"start": v(-68.89, 70.68) * mm, "end": v(-70.46, 73.4) * mm});
            skLineSegment(sketch, "E17.17.4.24", {"start": v(-70.46, 73.4) * mm, "end": v(-68.89, 76.14) * mm});
            skLineSegment(sketch, "E17.0.5.20", {"start": v(-53.93, 41.6) * mm, "end": v(-50.78, 41.6) * mm});
            skLineSegment(sketch, "E17.3.5.20", {"start": v(-50.78, 41.6) * mm, "end": v(-49.2, 38.86) * mm});
            skLineSegment(sketch, "E17.6.5.20", {"start": v(-49.2, 38.86) * mm, "end": v(-50.78, 36.13) * mm});
            skCircle(sketch, "E17.9.5.20", {"center": v(-52.35, 38.86) * mm, "radius": 2.73 * mm, "construction": true});
            skLineSegment(sketch, "E17.11.5.20", {"start": v(-50.78, 36.13) * mm, "end": v(-53.93, 36.13) * mm});
            skLineSegment(sketch, "E17.14.5.20", {"start": v(-53.93, 36.13) * mm, "end": v(-55.5, 38.86) * mm});
            skLineSegment(sketch, "E17.17.5.20", {"start": v(-55.5, 38.86) * mm, "end": v(-53.93, 41.6) * mm});
            skLineSegment(sketch, "E17.0.5.21", {"start": v(-53.93, 50.23) * mm, "end": v(-50.78, 50.23) * mm});
            skLineSegment(sketch, "E17.3.5.21", {"start": v(-50.78, 50.23) * mm, "end": v(-49.2, 47.5) * mm});
            skLineSegment(sketch, "E17.6.5.21", {"start": v(-49.2, 47.5) * mm, "end": v(-50.78, 44.77) * mm});
            skCircle(sketch, "E17.9.5.21", {"center": v(-52.35, 47.5) * mm, "radius": 2.73 * mm, "construction": true});
            skLineSegment(sketch, "E17.11.5.21", {"start": v(-50.78, 44.77) * mm, "end": v(-53.93, 44.77) * mm});
            skLineSegment(sketch, "E17.14.5.21", {"start": v(-53.93, 44.77) * mm, "end": v(-55.5, 47.5) * mm});
            skLineSegment(sketch, "E17.17.5.21", {"start": v(-55.5, 47.5) * mm, "end": v(-53.93, 50.23) * mm});
            skLineSegment(sketch, "E17.0.5.22", {"start": v(-53.93, 58.86) * mm, "end": v(-50.78, 58.86) * mm});
            skLineSegment(sketch, "E17.3.5.22", {"start": v(-50.78, 58.86) * mm, "end": v(-49.2, 56.13) * mm});
            skLineSegment(sketch, "E17.6.5.22", {"start": v(-49.2, 56.13) * mm, "end": v(-50.78, 53.4) * mm});
            skCircle(sketch, "E17.9.5.22", {"center": v(-52.35, 56.13) * mm, "radius": 2.73 * mm, "construction": true});
            skLineSegment(sketch, "E17.11.5.22", {"start": v(-50.78, 53.4) * mm, "end": v(-53.93, 53.4) * mm});
            skLineSegment(sketch, "E17.14.5.22", {"start": v(-53.93, 53.4) * mm, "end": v(-55.5, 56.13) * mm});
            skLineSegment(sketch, "E17.17.5.22", {"start": v(-55.5, 56.13) * mm, "end": v(-53.93, 58.86) * mm});
            skLineSegment(sketch, "E17.0.5.23", {"start": v(-53.93, 67.5) * mm, "end": v(-50.78, 67.5) * mm});
            skLineSegment(sketch, "E17.3.5.23", {"start": v(-50.78, 67.5) * mm, "end": v(-49.2, 64.77) * mm});
            skLineSegment(sketch, "E17.6.5.23", {"start": v(-49.2, 64.77) * mm, "end": v(-50.78, 62.04) * mm});
            skCircle(sketch, "E17.9.5.23", {"center": v(-52.35, 64.77) * mm, "radius": 2.73 * mm, "construction": true});
            skLineSegment(sketch, "E17.11.5.23", {"start": v(-50.78, 62.04) * mm, "end": v(-53.93, 62.04) * mm});
            skLineSegment(sketch, "E17.14.5.23", {"start": v(-53.93, 62.04) * mm, "end": v(-55.5, 64.77) * mm});
            skLineSegment(sketch, "E17.17.5.23", {"start": v(-55.5, 64.77) * mm, "end": v(-53.93, 67.5) * mm});
            skLineSegment(sketch, "E17.0.5.24", {"start": v(-53.93, 76.14) * mm, "end": v(-50.78, 76.14) * mm});
            skLineSegment(sketch, "E17.3.5.24", {"start": v(-50.78, 76.14) * mm, "end": v(-49.2, 73.4) * mm});
            skLineSegment(sketch, "E17.6.5.24", {"start": v(-49.2, 73.4) * mm, "end": v(-50.78, 70.68) * mm});
            skCircle(sketch, "E17.9.5.24", {"center": v(-52.35, 73.4) * mm, "radius": 2.73 * mm, "construction": true});
            skLineSegment(sketch, "E17.11.5.24", {"start": v(-50.78, 70.68) * mm, "end": v(-53.93, 70.68) * mm});
            skLineSegment(sketch, "E17.14.5.24", {"start": v(-53.93, 70.68) * mm, "end": v(-55.5, 73.4) * mm});
            skLineSegment(sketch, "E17.17.5.24", {"start": v(-55.5, 73.4) * mm, "end": v(-53.93, 76.14) * mm});
            skLineSegment(sketch, "E17.0.6.20", {"start": v(-38.97, 41.6) * mm, "end": v(-35.82, 41.6) * mm});
            skLineSegment(sketch, "E17.3.6.20", {"start": v(-35.82, 41.6) * mm, "end": v(-34.24, 38.86) * mm});
            skLineSegment(sketch, "E17.6.6.20", {"start": v(-34.24, 38.86) * mm, "end": v(-35.82, 36.13) * mm});
            skCircle(sketch, "E17.9.6.20", {"center": v(-37.4, 38.86) * mm, "radius": 2.73 * mm, "construction": true});
            skLineSegment(sketch, "E17.11.6.20", {"start": v(-35.82, 36.13) * mm, "end": v(-38.97, 36.13) * mm});
            skLineSegment(sketch, "E17.14.6.20", {"start": v(-38.97, 36.13) * mm, "end": v(-40.55, 38.86) * mm});
            skLineSegment(sketch, "E17.17.6.20", {"start": v(-40.55, 38.86) * mm, "end": v(-38.97, 41.6) * mm});
            skLineSegment(sketch, "E17.0.6.21", {"start": v(-38.97, 50.23) * mm, "end": v(-35.82, 50.23) * mm});
            skLineSegment(sketch, "E17.3.6.21", {"start": v(-35.82, 50.23) * mm, "end": v(-34.24, 47.5) * mm});
            skLineSegment(sketch, "E17.6.6.21", {"start": v(-34.24, 47.5) * mm, "end": v(-35.82, 44.77) * mm});
            skCircle(sketch, "E17.9.6.21", {"center": v(-37.4, 47.5) * mm, "radius": 2.73 * mm, "construction": true});
            skLineSegment(sketch, "E17.11.6.21", {"start": v(-35.82, 44.77) * mm, "end": v(-38.97, 44.77) * mm});
            skLineSegment(sketch, "E17.14.6.21", {"start": v(-38.97, 44.77) * mm, "end": v(-40.55, 47.5) * mm});
            skLineSegment(sketch, "E17.17.6.21", {"start": v(-40.55, 47.5) * mm, "end": v(-38.97, 50.23) * mm});
            skLineSegment(sketch, "E17.0.6.22", {"start": v(-38.97, 58.86) * mm, "end": v(-35.82, 58.86) * mm});
            skLineSegment(sketch, "E17.3.6.22", {"start": v(-35.82, 58.86) * mm, "end": v(-34.24, 56.13) * mm});
            skLineSegment(sketch, "E17.6.6.22", {"start": v(-34.24, 56.13) * mm, "end": v(-35.82, 53.4) * mm});
            skCircle(sketch, "E17.9.6.22", {"center": v(-37.4, 56.13) * mm, "radius": 2.73 * mm, "construction": true});
            skLineSegment(sketch, "E17.11.6.22", {"start": v(-35.82, 53.4) * mm, "end": v(-38.97, 53.4) * mm});
            skLineSegment(sketch, "E17.14.6.22", {"start": v(-38.97, 53.4) * mm, "end": v(-40.55, 56.13) * mm});
            skLineSegment(sketch, "E17.17.6.22", {"start": v(-40.55, 56.13) * mm, "end": v(-38.97, 58.86) * mm});
            skLineSegment(sketch, "E17.0.6.23", {"start": v(-38.97, 67.5) * mm, "end": v(-35.82, 67.5) * mm});
            skLineSegment(sketch, "E17.3.6.23", {"start": v(-35.82, 67.5) * mm, "end": v(-34.24, 64.77) * mm});
            skLineSegment(sketch, "E17.6.6.23", {"start": v(-34.24, 64.77) * mm, "end": v(-35.82, 62.04) * mm});
            skCircle(sketch, "E17.9.6.23", {"center": v(-37.4, 64.77) * mm, "radius": 2.73 * mm, "construction": true});
            skLineSegment(sketch, "E17.11.6.23", {"start": v(-35.82, 62.04) * mm, "end": v(-38.97, 62.04) * mm});
            skLineSegment(sketch, "E17.14.6.23", {"start": v(-38.97, 62.04) * mm, "end": v(-40.55, 64.77) * mm});
            skLineSegment(sketch, "E17.17.6.23", {"start": v(-40.55, 64.77) * mm, "end": v(-38.97, 67.5) * mm});
            skLineSegment(sketch, "E17.0.6.24", {"start": v(-38.97, 76.14) * mm, "end": v(-35.82, 76.14) * mm});
            skLineSegment(sketch, "E17.3.6.24", {"start": v(-35.82, 76.14) * mm, "end": v(-34.24, 73.4) * mm});
            skLineSegment(sketch, "E17.6.6.24", {"start": v(-34.24, 73.4) * mm, "end": v(-35.82, 70.68) * mm});
            skCircle(sketch, "E17.9.6.24", {"center": v(-37.4, 73.4) * mm, "radius": 2.73 * mm, "construction": true});
            skLineSegment(sketch, "E17.11.6.24", {"start": v(-35.82, 70.68) * mm, "end": v(-38.97, 70.68) * mm});
            skLineSegment(sketch, "E17.14.6.24", {"start": v(-38.97, 70.68) * mm, "end": v(-40.55, 73.4) * mm});
            skLineSegment(sketch, "E17.17.6.24", {"start": v(-40.55, 73.4) * mm, "end": v(-38.97, 76.14) * mm});
            skLineSegment(sketch, "E17.0.7.20", {"start": v(-24.01, 41.6) * mm, "end": v(-20.86, 41.6) * mm});
            skLineSegment(sketch, "E17.3.7.20", {"start": v(-20.86, 41.6) * mm, "end": v(-19.28, 38.86) * mm});
            skLineSegment(sketch, "E17.6.7.20", {"start": v(-19.28, 38.86) * mm, "end": v(-20.86, 36.13) * mm});
            skCircle(sketch, "E17.9.7.20", {"center": v(-22.44, 38.86) * mm, "radius": 2.73 * mm, "construction": true});
            skLineSegment(sketch, "E17.11.7.20", {"start": v(-20.86, 36.13) * mm, "end": v(-24.01, 36.13) * mm});
            skLineSegment(sketch, "E17.14.7.20", {"start": v(-24.01, 36.13) * mm, "end": v(-25.59, 38.86) * mm});
            skLineSegment(sketch, "E17.17.7.20", {"start": v(-25.59, 38.86) * mm, "end": v(-24.01, 41.6) * mm});
            skLineSegment(sketch, "E17.0.7.21", {"start": v(-24.01, 50.23) * mm, "end": v(-20.86, 50.23) * mm});
            skLineSegment(sketch, "E17.3.7.21", {"start": v(-20.86, 50.23) * mm, "end": v(-19.28, 47.5) * mm});
            skLineSegment(sketch, "E17.6.7.21", {"start": v(-19.28, 47.5) * mm, "end": v(-20.86, 44.77) * mm});
            skCircle(sketch, "E17.9.7.21", {"center": v(-22.44, 47.5) * mm, "radius": 2.73 * mm, "construction": true});
            skLineSegment(sketch, "E17.11.7.21", {"start": v(-20.86, 44.77) * mm, "end": v(-24.01, 44.77) * mm});
            skLineSegment(sketch, "E17.14.7.21", {"start": v(-24.01, 44.77) * mm, "end": v(-25.59, 47.5) * mm});
            skLineSegment(sketch, "E17.17.7.21", {"start": v(-25.59, 47.5) * mm, "end": v(-24.01, 50.23) * mm});
            skLineSegment(sketch, "E17.0.7.22", {"start": v(-24.01, 58.86) * mm, "end": v(-20.86, 58.86) * mm});
            skLineSegment(sketch, "E17.3.7.22", {"start": v(-20.86, 58.86) * mm, "end": v(-19.28, 56.13) * mm});
            skLineSegment(sketch, "E17.6.7.22", {"start": v(-19.28, 56.13) * mm, "end": v(-20.86, 53.4) * mm});
            skCircle(sketch, "E17.9.7.22", {"center": v(-22.44, 56.13) * mm, "radius": 2.73 * mm, "construction": true});
            skLineSegment(sketch, "E17.11.7.22", {"start": v(-20.86, 53.4) * mm, "end": v(-24.01, 53.4) * mm});
            skLineSegment(sketch, "E17.14.7.22", {"start": v(-24.01, 53.4) * mm, "end": v(-25.59, 56.13) * mm});
            skLineSegment(sketch, "E17.17.7.22", {"start": v(-25.59, 56.13) * mm, "end": v(-24.01, 58.86) * mm});
            skLineSegment(sketch, "E17.0.7.23", {"start": v(-24.01, 67.5) * mm, "end": v(-20.86, 67.5) * mm});
            skLineSegment(sketch, "E17.3.7.23", {"start": v(-20.86, 67.5) * mm, "end": v(-19.28, 64.77) * mm});
            skLineSegment(sketch, "E17.6.7.23", {"start": v(-19.28, 64.77) * mm, "end": v(-20.86, 62.04) * mm});
            skCircle(sketch, "E17.9.7.23", {"center": v(-22.44, 64.77) * mm, "radius": 2.73 * mm, "construction": true});
            skLineSegment(sketch, "E17.11.7.23", {"start": v(-20.86, 62.04) * mm, "end": v(-24.01, 62.04) * mm});
            skLineSegment(sketch, "E17.14.7.23", {"start": v(-24.01, 62.04) * mm, "end": v(-25.59, 64.77) * mm});
            skLineSegment(sketch, "E17.17.7.23", {"start": v(-25.59, 64.77) * mm, "end": v(-24.01, 67.5) * mm});
            skLineSegment(sketch, "E17.0.7.24", {"start": v(-24.01, 76.14) * mm, "end": v(-20.86, 76.14) * mm});
            skLineSegment(sketch, "E17.3.7.24", {"start": v(-20.86, 76.14) * mm, "end": v(-19.28, 73.4) * mm});
            skLineSegment(sketch, "E17.6.7.24", {"start": v(-19.28, 73.4) * mm, "end": v(-20.86, 70.68) * mm});
            skCircle(sketch, "E17.9.7.24", {"center": v(-22.44, 73.4) * mm, "radius": 2.73 * mm, "construction": true});
            skLineSegment(sketch, "E17.11.7.24", {"start": v(-20.86, 70.68) * mm, "end": v(-24.01, 70.68) * mm});
            skLineSegment(sketch, "E17.14.7.24", {"start": v(-24.01, 70.68) * mm, "end": v(-25.59, 73.4) * mm});
            skLineSegment(sketch, "E17.17.7.24", {"start": v(-25.59, 73.4) * mm, "end": v(-24.01, 76.14) * mm});
            skLineSegment(sketch, "E17.0.8.20", {"start": v(-9.06, 41.6) * mm, "end": v(-5.9, 41.6) * mm});
            skLineSegment(sketch, "E17.3.8.20", {"start": v(-5.9, 41.6) * mm, "end": v(-4.33, 38.86) * mm});
            skLineSegment(sketch, "E17.6.8.20", {"start": v(-4.33, 38.86) * mm, "end": v(-5.9, 36.13) * mm});
            skCircle(sketch, "E17.9.8.20", {"center": v(-7.48, 38.86) * mm, "radius": 2.73 * mm, "construction": true});
            skLineSegment(sketch, "E17.11.8.20", {"start": v(-5.9, 36.13) * mm, "end": v(-9.06, 36.13) * mm});
            skLineSegment(sketch, "E17.14.8.20", {"start": v(-9.06, 36.13) * mm, "end": v(-10.63, 38.86) * mm});
            skLineSegment(sketch, "E17.17.8.20", {"start": v(-10.63, 38.86) * mm, "end": v(-9.06, 41.6) * mm});
            skLineSegment(sketch, "E17.0.8.21", {"start": v(-9.06, 50.23) * mm, "end": v(-5.9, 50.23) * mm});
            skLineSegment(sketch, "E17.3.8.21", {"start": v(-5.9, 50.23) * mm, "end": v(-4.33, 47.5) * mm});
            skLineSegment(sketch, "E17.6.8.21", {"start": v(-4.33, 47.5) * mm, "end": v(-5.9, 44.77) * mm});
            skCircle(sketch, "E17.9.8.21", {"center": v(-7.48, 47.5) * mm, "radius": 2.73 * mm, "construction": true});
            skLineSegment(sketch, "E17.11.8.21", {"start": v(-5.9, 44.77) * mm, "end": v(-9.06, 44.77) * mm});
            skLineSegment(sketch, "E17.14.8.21", {"start": v(-9.06, 44.77) * mm, "end": v(-10.63, 47.5) * mm});
            skLineSegment(sketch, "E17.17.8.21", {"start": v(-10.63, 47.5) * mm, "end": v(-9.06, 50.23) * mm});
            skLineSegment(sketch, "E17.0.8.22", {"start": v(-9.06, 58.86) * mm, "end": v(-5.9, 58.86) * mm});
            skLineSegment(sketch, "E17.3.8.22", {"start": v(-5.9, 58.86) * mm, "end": v(-4.33, 56.13) * mm});
            skLineSegment(sketch, "E17.6.8.22", {"start": v(-4.33, 56.13) * mm, "end": v(-5.9, 53.4) * mm});
            skCircle(sketch, "E17.9.8.22", {"center": v(-7.48, 56.13) * mm, "radius": 2.73 * mm, "construction": true});
            skLineSegment(sketch, "E17.11.8.22", {"start": v(-5.9, 53.4) * mm, "end": v(-9.06, 53.4) * mm});
            skLineSegment(sketch, "E17.14.8.22", {"start": v(-9.06, 53.4) * mm, "end": v(-10.63, 56.13) * mm});
            skLineSegment(sketch, "E17.17.8.22", {"start": v(-10.63, 56.13) * mm, "end": v(-9.06, 58.86) * mm});
            skLineSegment(sketch, "E17.0.8.23", {"start": v(-9.06, 67.5) * mm, "end": v(-5.9, 67.5) * mm});
            skLineSegment(sketch, "E17.3.8.23", {"start": v(-5.9, 67.5) * mm, "end": v(-4.33, 64.77) * mm});
            skLineSegment(sketch, "E17.6.8.23", {"start": v(-4.33, 64.77) * mm, "end": v(-5.9, 62.04) * mm});
            skCircle(sketch, "E17.9.8.23", {"center": v(-7.48, 64.77) * mm, "radius": 2.73 * mm, "construction": true});
            skLineSegment(sketch, "E17.11.8.23", {"start": v(-5.9, 62.04) * mm, "end": v(-9.06, 62.04) * mm});
            skLineSegment(sketch, "E17.14.8.23", {"start": v(-9.06, 62.04) * mm, "end": v(-10.63, 64.77) * mm});
            skLineSegment(sketch, "E17.17.8.23", {"start": v(-10.63, 64.77) * mm, "end": v(-9.06, 67.5) * mm});
            skLineSegment(sketch, "E17.0.8.24", {"start": v(-9.06, 76.14) * mm, "end": v(-5.9, 76.14) * mm});
            skLineSegment(sketch, "E17.3.8.24", {"start": v(-5.9, 76.14) * mm, "end": v(-4.33, 73.4) * mm});
            skLineSegment(sketch, "E17.6.8.24", {"start": v(-4.33, 73.4) * mm, "end": v(-5.9, 70.68) * mm});
            skCircle(sketch, "E17.9.8.24", {"center": v(-7.48, 73.4) * mm, "radius": 2.73 * mm, "construction": true});
            skLineSegment(sketch, "E17.11.8.24", {"start": v(-5.9, 70.68) * mm, "end": v(-9.06, 70.68) * mm});
            skLineSegment(sketch, "E17.14.8.24", {"start": v(-9.06, 70.68) * mm, "end": v(-10.63, 73.4) * mm});
            skLineSegment(sketch, "E17.17.8.24", {"start": v(-10.63, 73.4) * mm, "end": v(-9.06, 76.14) * mm});
            skLineSegment(sketch, "E17.0.9.20", {"start": v(5.9, 41.6) * mm, "end": v(9.06, 41.6) * mm});
            skLineSegment(sketch, "E17.3.9.20", {"start": v(9.06, 41.6) * mm, "end": v(10.63, 38.86) * mm});
            skLineSegment(sketch, "E17.6.9.20", {"start": v(10.63, 38.86) * mm, "end": v(9.06, 36.13) * mm});
            skCircle(sketch, "E17.9.9.20", {"center": v(7.48, 38.86) * mm, "radius": 2.73 * mm, "construction": true});
            skLineSegment(sketch, "E17.11.9.20", {"start": v(9.06, 36.13) * mm, "end": v(5.9, 36.13) * mm});
            skLineSegment(sketch, "E17.14.9.20", {"start": v(5.9, 36.13) * mm, "end": v(4.33, 38.86) * mm});
            skLineSegment(sketch, "E17.17.9.20", {"start": v(4.33, 38.86) * mm, "end": v(5.9, 41.6) * mm});
            skLineSegment(sketch, "E17.0.9.21", {"start": v(5.9, 50.23) * mm, "end": v(9.06, 50.23) * mm});
            skLineSegment(sketch, "E17.3.9.21", {"start": v(9.06, 50.23) * mm, "end": v(10.63, 47.5) * mm});
            skLineSegment(sketch, "E17.6.9.21", {"start": v(10.63, 47.5) * mm, "end": v(9.06, 44.77) * mm});
            skCircle(sketch, "E17.9.9.21", {"center": v(7.48, 47.5) * mm, "radius": 2.73 * mm, "construction": true});
            skLineSegment(sketch, "E17.11.9.21", {"start": v(9.06, 44.77) * mm, "end": v(5.9, 44.77) * mm});
            skLineSegment(sketch, "E17.14.9.21", {"start": v(5.9, 44.77) * mm, "end": v(4.33, 47.5) * mm});
            skLineSegment(sketch, "E17.17.9.21", {"start": v(4.33, 47.5) * mm, "end": v(5.9, 50.23) * mm});
            skLineSegment(sketch, "E17.0.9.22", {"start": v(5.9, 58.86) * mm, "end": v(9.06, 58.86) * mm});
            skLineSegment(sketch, "E17.3.9.22", {"start": v(9.06, 58.86) * mm, "end": v(10.63, 56.13) * mm});
            skLineSegment(sketch, "E17.6.9.22", {"start": v(10.63, 56.13) * mm, "end": v(9.06, 53.4) * mm});
            skCircle(sketch, "E17.9.9.22", {"center": v(7.48, 56.13) * mm, "radius": 2.73 * mm, "construction": true});
            skLineSegment(sketch, "E17.11.9.22", {"start": v(9.06, 53.4) * mm, "end": v(5.9, 53.4) * mm});
            skLineSegment(sketch, "E17.14.9.22", {"start": v(5.9, 53.4) * mm, "end": v(4.33, 56.13) * mm});
            skLineSegment(sketch, "E17.17.9.22", {"start": v(4.33, 56.13) * mm, "end": v(5.9, 58.86) * mm});
            skLineSegment(sketch, "E17.0.9.23", {"start": v(5.9, 67.5) * mm, "end": v(9.06, 67.5) * mm});
            skLineSegment(sketch, "E17.3.9.23", {"start": v(9.06, 67.5) * mm, "end": v(10.63, 64.77) * mm});
            skLineSegment(sketch, "E17.6.9.23", {"start": v(10.63, 64.77) * mm, "end": v(9.06, 62.04) * mm});
            skCircle(sketch, "E17.9.9.23", {"center": v(7.48, 64.77) * mm, "radius": 2.73 * mm, "construction": true});
            skLineSegment(sketch, "E17.11.9.23", {"start": v(9.06, 62.04) * mm, "end": v(5.9, 62.04) * mm});
            skLineSegment(sketch, "E17.14.9.23", {"start": v(5.9, 62.04) * mm, "end": v(4.33, 64.77) * mm});
            skLineSegment(sketch, "E17.17.9.23", {"start": v(4.33, 64.77) * mm, "end": v(5.9, 67.5) * mm});
            skLineSegment(sketch, "E17.0.9.24", {"start": v(5.9, 76.14) * mm, "end": v(9.06, 76.14) * mm});
            skLineSegment(sketch, "E17.3.9.24", {"start": v(9.06, 76.14) * mm, "end": v(10.63, 73.4) * mm});
            skLineSegment(sketch, "E17.6.9.24", {"start": v(10.63, 73.4) * mm, "end": v(9.06, 70.68) * mm});
            skCircle(sketch, "E17.9.9.24", {"center": v(7.48, 73.4) * mm, "radius": 2.73 * mm, "construction": true});
            skLineSegment(sketch, "E17.11.9.24", {"start": v(9.06, 70.68) * mm, "end": v(5.9, 70.68) * mm});
            skLineSegment(sketch, "E17.14.9.24", {"start": v(5.9, 70.68) * mm, "end": v(4.33, 73.4) * mm});
            skLineSegment(sketch, "E17.17.9.24", {"start": v(4.33, 73.4) * mm, "end": v(5.9, 76.14) * mm});
            skLineSegment(sketch, "E17.0.10.20", {"start": v(20.86, 41.6) * mm, "end": v(24.01, 41.6) * mm});
            skLineSegment(sketch, "E17.3.10.20", {"start": v(24.01, 41.6) * mm, "end": v(25.6, 38.86) * mm});
            skLineSegment(sketch, "E17.6.10.20", {"start": v(25.6, 38.86) * mm, "end": v(24.01, 36.13) * mm});
            skCircle(sketch, "E17.9.10.20", {"center": v(22.44, 38.86) * mm, "radius": 2.73 * mm, "construction": true});
            skLineSegment(sketch, "E17.11.10.20", {"start": v(24.01, 36.13) * mm, "end": v(20.86, 36.13) * mm});
            skLineSegment(sketch, "E17.14.10.20", {"start": v(20.86, 36.13) * mm, "end": v(19.28, 38.86) * mm});
            skLineSegment(sketch, "E17.17.10.20", {"start": v(19.28, 38.86) * mm, "end": v(20.86, 41.6) * mm});
            skLineSegment(sketch, "E17.0.10.21", {"start": v(20.86, 50.23) * mm, "end": v(24.01, 50.23) * mm});
            skLineSegment(sketch, "E17.3.10.21", {"start": v(24.01, 50.23) * mm, "end": v(25.6, 47.5) * mm});
            skLineSegment(sketch, "E17.6.10.21", {"start": v(25.6, 47.5) * mm, "end": v(24.01, 44.77) * mm});
            skCircle(sketch, "E17.9.10.21", {"center": v(22.44, 47.5) * mm, "radius": 2.73 * mm, "construction": true});
            skLineSegment(sketch, "E17.11.10.21", {"start": v(24.01, 44.77) * mm, "end": v(20.86, 44.77) * mm});
            skLineSegment(sketch, "E17.14.10.21", {"start": v(20.86, 44.77) * mm, "end": v(19.28, 47.5) * mm});
            skLineSegment(sketch, "E17.17.10.21", {"start": v(19.28, 47.5) * mm, "end": v(20.86, 50.23) * mm});
            skLineSegment(sketch, "E17.0.10.22", {"start": v(20.86, 58.86) * mm, "end": v(24.01, 58.86) * mm});
            skLineSegment(sketch, "E17.3.10.22", {"start": v(24.01, 58.86) * mm, "end": v(25.6, 56.13) * mm});
            skLineSegment(sketch, "E17.6.10.22", {"start": v(25.6, 56.13) * mm, "end": v(24.01, 53.4) * mm});
            skCircle(sketch, "E17.9.10.22", {"center": v(22.44, 56.13) * mm, "radius": 2.73 * mm, "construction": true});
            skLineSegment(sketch, "E17.11.10.22", {"start": v(24.01, 53.4) * mm, "end": v(20.86, 53.4) * mm});
            skLineSegment(sketch, "E17.14.10.22", {"start": v(20.86, 53.4) * mm, "end": v(19.28, 56.13) * mm});
            skLineSegment(sketch, "E17.17.10.22", {"start": v(19.28, 56.13) * mm, "end": v(20.86, 58.86) * mm});
            skLineSegment(sketch, "E17.0.10.23", {"start": v(20.86, 67.5) * mm, "end": v(24.01, 67.5) * mm});
            skLineSegment(sketch, "E17.3.10.23", {"start": v(24.01, 67.5) * mm, "end": v(25.6, 64.77) * mm});
            skLineSegment(sketch, "E17.6.10.23", {"start": v(25.6, 64.77) * mm, "end": v(24.01, 62.04) * mm});
            skCircle(sketch, "E17.9.10.23", {"center": v(22.44, 64.77) * mm, "radius": 2.73 * mm, "construction": true});
            skLineSegment(sketch, "E17.11.10.23", {"start": v(24.01, 62.04) * mm, "end": v(20.86, 62.04) * mm});
            skLineSegment(sketch, "E17.14.10.23", {"start": v(20.86, 62.04) * mm, "end": v(19.28, 64.77) * mm});
            skLineSegment(sketch, "E17.17.10.23", {"start": v(19.28, 64.77) * mm, "end": v(20.86, 67.5) * mm});
            skLineSegment(sketch, "E17.0.10.24", {"start": v(20.86, 76.14) * mm, "end": v(24.01, 76.14) * mm});
            skLineSegment(sketch, "E17.3.10.24", {"start": v(24.01, 76.14) * mm, "end": v(25.6, 73.4) * mm});
            skLineSegment(sketch, "E17.6.10.24", {"start": v(25.6, 73.4) * mm, "end": v(24.01, 70.68) * mm});
            skCircle(sketch, "E17.9.10.24", {"center": v(22.44, 73.4) * mm, "radius": 2.73 * mm, "construction": true});
            skLineSegment(sketch, "E17.11.10.24", {"start": v(24.01, 70.68) * mm, "end": v(20.86, 70.68) * mm});
            skLineSegment(sketch, "E17.14.10.24", {"start": v(20.86, 70.68) * mm, "end": v(19.28, 73.4) * mm});
            skLineSegment(sketch, "E17.17.10.24", {"start": v(19.28, 73.4) * mm, "end": v(20.86, 76.14) * mm});
            skLineSegment(sketch, "E17.0.11.20", {"start": v(35.82, 41.6) * mm, "end": v(38.97, 41.6) * mm});
            skLineSegment(sketch, "E17.3.11.20", {"start": v(38.97, 41.6) * mm, "end": v(40.55, 38.86) * mm});
            skLineSegment(sketch, "E17.6.11.20", {"start": v(40.55, 38.86) * mm, "end": v(38.97, 36.13) * mm});
            skCircle(sketch, "E17.9.11.20", {"center": v(37.4, 38.86) * mm, "radius": 2.73 * mm, "construction": true});
            skLineSegment(sketch, "E17.11.11.20", {"start": v(38.97, 36.13) * mm, "end": v(35.82, 36.13) * mm});
            skLineSegment(sketch, "E17.14.11.20", {"start": v(35.82, 36.13) * mm, "end": v(34.24, 38.86) * mm});
            skLineSegment(sketch, "E17.17.11.20", {"start": v(34.24, 38.86) * mm, "end": v(35.82, 41.6) * mm});
            skLineSegment(sketch, "E17.0.11.21", {"start": v(35.82, 50.23) * mm, "end": v(38.97, 50.23) * mm});
            skLineSegment(sketch, "E17.3.11.21", {"start": v(38.97, 50.23) * mm, "end": v(40.55, 47.5) * mm});
            skLineSegment(sketch, "E17.6.11.21", {"start": v(40.55, 47.5) * mm, "end": v(38.97, 44.77) * mm});
            skCircle(sketch, "E17.9.11.21", {"center": v(37.4, 47.5) * mm, "radius": 2.73 * mm, "construction": true});
            skLineSegment(sketch, "E17.11.11.21", {"start": v(38.97, 44.77) * mm, "end": v(35.82, 44.77) * mm});
            skLineSegment(sketch, "E17.14.11.21", {"start": v(35.82, 44.77) * mm, "end": v(34.24, 47.5) * mm});
            skLineSegment(sketch, "E17.17.11.21", {"start": v(34.24, 47.5) * mm, "end": v(35.82, 50.23) * mm});
            skLineSegment(sketch, "E17.0.11.22", {"start": v(35.82, 58.86) * mm, "end": v(38.97, 58.86) * mm});
            skLineSegment(sketch, "E17.3.11.22", {"start": v(38.97, 58.86) * mm, "end": v(40.55, 56.13) * mm});
            skLineSegment(sketch, "E17.6.11.22", {"start": v(40.55, 56.13) * mm, "end": v(38.97, 53.4) * mm});
            skCircle(sketch, "E17.9.11.22", {"center": v(37.4, 56.13) * mm, "radius": 2.73 * mm, "construction": true});
            skLineSegment(sketch, "E17.11.11.22", {"start": v(38.97, 53.4) * mm, "end": v(35.82, 53.4) * mm});
            skLineSegment(sketch, "E17.14.11.22", {"start": v(35.82, 53.4) * mm, "end": v(34.24, 56.13) * mm});
            skLineSegment(sketch, "E17.17.11.22", {"start": v(34.24, 56.13) * mm, "end": v(35.82, 58.86) * mm});
            skLineSegment(sketch, "E17.0.11.23", {"start": v(35.82, 67.5) * mm, "end": v(38.97, 67.5) * mm});
            skLineSegment(sketch, "E17.3.11.23", {"start": v(38.97, 67.5) * mm, "end": v(40.55, 64.77) * mm});
            skLineSegment(sketch, "E17.6.11.23", {"start": v(40.55, 64.77) * mm, "end": v(38.97, 62.04) * mm});
            skCircle(sketch, "E17.9.11.23", {"center": v(37.4, 64.77) * mm, "radius": 2.73 * mm, "construction": true});
            skLineSegment(sketch, "E17.11.11.23", {"start": v(38.97, 62.04) * mm, "end": v(35.82, 62.04) * mm});
            skLineSegment(sketch, "E17.14.11.23", {"start": v(35.82, 62.04) * mm, "end": v(34.24, 64.77) * mm});
            skLineSegment(sketch, "E17.17.11.23", {"start": v(34.24, 64.77) * mm, "end": v(35.82, 67.5) * mm});
            skLineSegment(sketch, "E17.0.11.24", {"start": v(35.82, 76.14) * mm, "end": v(38.97, 76.14) * mm});
            skLineSegment(sketch, "E17.3.11.24", {"start": v(38.97, 76.14) * mm, "end": v(40.55, 73.4) * mm});
            skLineSegment(sketch, "E17.6.11.24", {"start": v(40.55, 73.4) * mm, "end": v(38.97, 70.68) * mm});
            skCircle(sketch, "E17.9.11.24", {"center": v(37.4, 73.4) * mm, "radius": 2.73 * mm, "construction": true});
            skLineSegment(sketch, "E17.11.11.24", {"start": v(38.97, 70.68) * mm, "end": v(35.82, 70.68) * mm});
            skLineSegment(sketch, "E17.14.11.24", {"start": v(35.82, 70.68) * mm, "end": v(34.24, 73.4) * mm});
            skLineSegment(sketch, "E17.17.11.24", {"start": v(34.24, 73.4) * mm, "end": v(35.82, 76.14) * mm});
            skLineSegment(sketch, "E17.0.12.20", {"start": v(50.78, 41.6) * mm, "end": v(53.93, 41.6) * mm});
            skLineSegment(sketch, "E17.3.12.20", {"start": v(53.93, 41.6) * mm, "end": v(55.5, 38.86) * mm});
            skLineSegment(sketch, "E17.6.12.20", {"start": v(55.5, 38.86) * mm, "end": v(53.93, 36.13) * mm});
            skCircle(sketch, "E17.9.12.20", {"center": v(52.35, 38.86) * mm, "radius": 2.73 * mm, "construction": true});
            skLineSegment(sketch, "E17.11.12.20", {"start": v(53.93, 36.13) * mm, "end": v(50.78, 36.13) * mm});
            skLineSegment(sketch, "E17.14.12.20", {"start": v(50.78, 36.13) * mm, "end": v(49.2, 38.86) * mm});
            skLineSegment(sketch, "E17.17.12.20", {"start": v(49.2, 38.86) * mm, "end": v(50.78, 41.6) * mm});
            skLineSegment(sketch, "E17.0.12.21", {"start": v(50.78, 50.23) * mm, "end": v(53.93, 50.23) * mm});
            skLineSegment(sketch, "E17.3.12.21", {"start": v(53.93, 50.23) * mm, "end": v(55.5, 47.5) * mm});
            skLineSegment(sketch, "E17.6.12.21", {"start": v(55.5, 47.5) * mm, "end": v(53.93, 44.77) * mm});
            skCircle(sketch, "E17.9.12.21", {"center": v(52.35, 47.5) * mm, "radius": 2.73 * mm, "construction": true});
            skLineSegment(sketch, "E17.11.12.21", {"start": v(53.93, 44.77) * mm, "end": v(50.78, 44.77) * mm});
            skLineSegment(sketch, "E17.14.12.21", {"start": v(50.78, 44.77) * mm, "end": v(49.2, 47.5) * mm});
            skLineSegment(sketch, "E17.17.12.21", {"start": v(49.2, 47.5) * mm, "end": v(50.78, 50.23) * mm});
            skLineSegment(sketch, "E17.0.12.22", {"start": v(50.78, 58.86) * mm, "end": v(53.93, 58.86) * mm});
            skLineSegment(sketch, "E17.3.12.22", {"start": v(53.93, 58.86) * mm, "end": v(55.5, 56.13) * mm});
            skLineSegment(sketch, "E17.6.12.22", {"start": v(55.5, 56.13) * mm, "end": v(53.93, 53.4) * mm});
            skCircle(sketch, "E17.9.12.22", {"center": v(52.35, 56.13) * mm, "radius": 2.73 * mm, "construction": true});
            skLineSegment(sketch, "E17.11.12.22", {"start": v(53.93, 53.4) * mm, "end": v(50.78, 53.4) * mm});
            skLineSegment(sketch, "E17.14.12.22", {"start": v(50.78, 53.4) * mm, "end": v(49.2, 56.13) * mm});
            skLineSegment(sketch, "E17.17.12.22", {"start": v(49.2, 56.13) * mm, "end": v(50.78, 58.86) * mm});
            skLineSegment(sketch, "E17.0.12.23", {"start": v(50.78, 67.5) * mm, "end": v(53.93, 67.5) * mm});
            skLineSegment(sketch, "E17.3.12.23", {"start": v(53.93, 67.5) * mm, "end": v(55.5, 64.77) * mm});
            skLineSegment(sketch, "E17.6.12.23", {"start": v(55.5, 64.77) * mm, "end": v(53.93, 62.04) * mm});
            skCircle(sketch, "E17.9.12.23", {"center": v(52.35, 64.77) * mm, "radius": 2.73 * mm, "construction": true});
            skLineSegment(sketch, "E17.11.12.23", {"start": v(53.93, 62.04) * mm, "end": v(50.78, 62.04) * mm});
            skLineSegment(sketch, "E17.14.12.23", {"start": v(50.78, 62.04) * mm, "end": v(49.2, 64.77) * mm});
            skLineSegment(sketch, "E17.17.12.23", {"start": v(49.2, 64.77) * mm, "end": v(50.78, 67.5) * mm});
            skLineSegment(sketch, "E17.0.12.24", {"start": v(50.78, 76.14) * mm, "end": v(53.93, 76.14) * mm});
            skLineSegment(sketch, "E17.3.12.24", {"start": v(53.93, 76.14) * mm, "end": v(55.5, 73.4) * mm});
            skLineSegment(sketch, "E17.6.12.24", {"start": v(55.5, 73.4) * mm, "end": v(53.93, 70.68) * mm});
            skCircle(sketch, "E17.9.12.24", {"center": v(52.35, 73.4) * mm, "radius": 2.73 * mm, "construction": true});
            skLineSegment(sketch, "E17.11.12.24", {"start": v(53.93, 70.68) * mm, "end": v(50.78, 70.68) * mm});
            skLineSegment(sketch, "E17.14.12.24", {"start": v(50.78, 70.68) * mm, "end": v(49.2, 73.4) * mm});
            skLineSegment(sketch, "E17.17.12.24", {"start": v(49.2, 73.4) * mm, "end": v(50.78, 76.14) * mm});
            skLineSegment(sketch, "E17.0.13.20", {"start": v(65.73, 41.6) * mm, "end": v(68.89, 41.6) * mm});
            skLineSegment(sketch, "E17.3.13.20", {"start": v(68.89, 41.6) * mm, "end": v(70.46, 38.86) * mm});
            skLineSegment(sketch, "E17.6.13.20", {"start": v(70.46, 38.86) * mm, "end": v(68.89, 36.13) * mm});
            skCircle(sketch, "E17.9.13.20", {"center": v(67.31, 38.86) * mm, "radius": 2.73 * mm, "construction": true});
            skLineSegment(sketch, "E17.11.13.20", {"start": v(68.89, 36.13) * mm, "end": v(65.73, 36.13) * mm});
            skLineSegment(sketch, "E17.14.13.20", {"start": v(65.73, 36.13) * mm, "end": v(64.16, 38.86) * mm});
            skLineSegment(sketch, "E17.17.13.20", {"start": v(64.16, 38.86) * mm, "end": v(65.73, 41.6) * mm});
            skLineSegment(sketch, "E17.0.13.21", {"start": v(65.73, 50.23) * mm, "end": v(68.89, 50.23) * mm});
            skLineSegment(sketch, "E17.3.13.21", {"start": v(68.89, 50.23) * mm, "end": v(70.46, 47.5) * mm});
            skLineSegment(sketch, "E17.6.13.21", {"start": v(70.46, 47.5) * mm, "end": v(68.89, 44.77) * mm});
            skCircle(sketch, "E17.9.13.21", {"center": v(67.31, 47.5) * mm, "radius": 2.73 * mm, "construction": true});
            skLineSegment(sketch, "E17.11.13.21", {"start": v(68.89, 44.77) * mm, "end": v(65.73, 44.77) * mm});
            skLineSegment(sketch, "E17.14.13.21", {"start": v(65.73, 44.77) * mm, "end": v(64.16, 47.5) * mm});
            skLineSegment(sketch, "E17.17.13.21", {"start": v(64.16, 47.5) * mm, "end": v(65.73, 50.23) * mm});
            skLineSegment(sketch, "E17.0.13.22", {"start": v(65.73, 58.86) * mm, "end": v(68.89, 58.86) * mm});
            skLineSegment(sketch, "E17.3.13.22", {"start": v(68.89, 58.86) * mm, "end": v(70.46, 56.13) * mm});
            skLineSegment(sketch, "E17.6.13.22", {"start": v(70.46, 56.13) * mm, "end": v(68.89, 53.4) * mm});
            skCircle(sketch, "E17.9.13.22", {"center": v(67.31, 56.13) * mm, "radius": 2.73 * mm, "construction": true});
            skLineSegment(sketch, "E17.11.13.22", {"start": v(68.89, 53.4) * mm, "end": v(65.73, 53.4) * mm});
            skLineSegment(sketch, "E17.14.13.22", {"start": v(65.73, 53.4) * mm, "end": v(64.16, 56.13) * mm});
            skLineSegment(sketch, "E17.17.13.22", {"start": v(64.16, 56.13) * mm, "end": v(65.73, 58.86) * mm});
            skLineSegment(sketch, "E17.0.13.23", {"start": v(65.73, 67.5) * mm, "end": v(68.89, 67.5) * mm});
            skLineSegment(sketch, "E17.3.13.23", {"start": v(68.89, 67.5) * mm, "end": v(70.46, 64.77) * mm});
            skLineSegment(sketch, "E17.6.13.23", {"start": v(70.46, 64.77) * mm, "end": v(68.89, 62.04) * mm});
            skCircle(sketch, "E17.9.13.23", {"center": v(67.31, 64.77) * mm, "radius": 2.73 * mm, "construction": true});
            skLineSegment(sketch, "E17.11.13.23", {"start": v(68.89, 62.04) * mm, "end": v(65.73, 62.04) * mm});
            skLineSegment(sketch, "E17.14.13.23", {"start": v(65.73, 62.04) * mm, "end": v(64.16, 64.77) * mm});
            skLineSegment(sketch, "E17.17.13.23", {"start": v(64.16, 64.77) * mm, "end": v(65.73, 67.5) * mm});
            skLineSegment(sketch, "E17.0.13.24", {"start": v(65.73, 76.14) * mm, "end": v(68.89, 76.14) * mm});
            skLineSegment(sketch, "E17.3.13.24", {"start": v(68.89, 76.14) * mm, "end": v(70.46, 73.4) * mm});
            skLineSegment(sketch, "E17.6.13.24", {"start": v(70.46, 73.4) * mm, "end": v(68.89, 70.68) * mm});
            skCircle(sketch, "E17.9.13.24", {"center": v(67.31, 73.4) * mm, "radius": 2.73 * mm, "construction": true});
            skLineSegment(sketch, "E17.11.13.24", {"start": v(68.89, 70.68) * mm, "end": v(65.73, 70.68) * mm});
            skLineSegment(sketch, "E17.14.13.24", {"start": v(65.73, 70.68) * mm, "end": v(64.16, 73.4) * mm});
            skLineSegment(sketch, "E17.17.13.24", {"start": v(64.16, 73.4) * mm, "end": v(65.73, 76.14) * mm});
            skLineSegment(sketch, "E17.0.14.20", {"start": v(80.7, 41.6) * mm, "end": v(83.85, 41.6) * mm});
            skLineSegment(sketch, "E17.3.14.20", {"start": v(83.85, 41.6) * mm, "end": v(85.42, 38.86) * mm});
            skLineSegment(sketch, "E17.6.14.20", {"start": v(85.42, 38.86) * mm, "end": v(83.85, 36.13) * mm});
            skCircle(sketch, "E17.9.14.20", {"center": v(82.27, 38.86) * mm, "radius": 2.73 * mm, "construction": true});
            skLineSegment(sketch, "E17.11.14.20", {"start": v(83.85, 36.13) * mm, "end": v(80.7, 36.13) * mm});
            skLineSegment(sketch, "E17.14.14.20", {"start": v(80.7, 36.13) * mm, "end": v(79.12, 38.86) * mm});
            skLineSegment(sketch, "E17.17.14.20", {"start": v(79.12, 38.86) * mm, "end": v(80.7, 41.6) * mm});
            skLineSegment(sketch, "E17.0.14.21", {"start": v(80.7, 50.23) * mm, "end": v(83.85, 50.23) * mm});
            skLineSegment(sketch, "E17.3.14.21", {"start": v(83.85, 50.23) * mm, "end": v(85.42, 47.5) * mm});
            skLineSegment(sketch, "E17.6.14.21", {"start": v(85.42, 47.5) * mm, "end": v(83.85, 44.77) * mm});
            skCircle(sketch, "E17.9.14.21", {"center": v(82.27, 47.5) * mm, "radius": 2.73 * mm, "construction": true});
            skLineSegment(sketch, "E17.11.14.21", {"start": v(83.85, 44.77) * mm, "end": v(80.7, 44.77) * mm});
            skLineSegment(sketch, "E17.14.14.21", {"start": v(80.7, 44.77) * mm, "end": v(79.12, 47.5) * mm});
            skLineSegment(sketch, "E17.17.14.21", {"start": v(79.12, 47.5) * mm, "end": v(80.7, 50.23) * mm});
            skLineSegment(sketch, "E17.0.14.22", {"start": v(80.7, 58.86) * mm, "end": v(83.85, 58.86) * mm});
            skLineSegment(sketch, "E17.3.14.22", {"start": v(83.85, 58.86) * mm, "end": v(85.42, 56.13) * mm});
            skLineSegment(sketch, "E17.6.14.22", {"start": v(85.42, 56.13) * mm, "end": v(83.85, 53.4) * mm});
            skCircle(sketch, "E17.9.14.22", {"center": v(82.27, 56.13) * mm, "radius": 2.73 * mm, "construction": true});
            skLineSegment(sketch, "E17.11.14.22", {"start": v(83.85, 53.4) * mm, "end": v(80.7, 53.4) * mm});
            skLineSegment(sketch, "E17.14.14.22", {"start": v(80.7, 53.4) * mm, "end": v(79.12, 56.13) * mm});
            skLineSegment(sketch, "E17.17.14.22", {"start": v(79.12, 56.13) * mm, "end": v(80.7, 58.86) * mm});
            skLineSegment(sketch, "E17.0.14.23", {"start": v(80.7, 67.5) * mm, "end": v(83.85, 67.5) * mm});
            skLineSegment(sketch, "E17.3.14.23", {"start": v(83.85, 67.5) * mm, "end": v(85.42, 64.77) * mm});
            skLineSegment(sketch, "E17.6.14.23", {"start": v(85.42, 64.77) * mm, "end": v(83.85, 62.04) * mm});
            skCircle(sketch, "E17.9.14.23", {"center": v(82.27, 64.77) * mm, "radius": 2.73 * mm, "construction": true});
            skLineSegment(sketch, "E17.11.14.23", {"start": v(83.85, 62.04) * mm, "end": v(80.7, 62.04) * mm});
            skLineSegment(sketch, "E17.14.14.23", {"start": v(80.7, 62.04) * mm, "end": v(79.12, 64.77) * mm});
            skLineSegment(sketch, "E17.17.14.23", {"start": v(79.12, 64.77) * mm, "end": v(80.7, 67.5) * mm});
            skLineSegment(sketch, "E17.0.14.24", {"start": v(80.7, 76.14) * mm, "end": v(83.85, 76.14) * mm});
            skLineSegment(sketch, "E17.3.14.24", {"start": v(83.85, 76.14) * mm, "end": v(85.42, 73.4) * mm});
            skLineSegment(sketch, "E17.6.14.24", {"start": v(85.42, 73.4) * mm, "end": v(83.85, 70.68) * mm});
            skCircle(sketch, "E17.9.14.24", {"center": v(82.27, 73.4) * mm, "radius": 2.73 * mm, "construction": true});
            skLineSegment(sketch, "E17.11.14.24", {"start": v(83.85, 70.68) * mm, "end": v(80.7, 70.68) * mm});
            skLineSegment(sketch, "E17.14.14.24", {"start": v(80.7, 70.68) * mm, "end": v(79.12, 73.4) * mm});
            skLineSegment(sketch, "E17.17.14.24", {"start": v(79.12, 73.4) * mm, "end": v(80.7, 76.14) * mm});
            skLineSegment(sketch, "E17.0.15.20", {"start": v(95.65, 41.6) * mm, "end": v(98.8, 41.6) * mm});
            skLineSegment(sketch, "E17.3.15.20", {"start": v(98.8, 41.6) * mm, "end": v(100.38, 38.86) * mm});
            skLineSegment(sketch, "E17.6.15.20", {"start": v(100.38, 38.86) * mm, "end": v(98.8, 36.13) * mm});
            skCircle(sketch, "E17.9.15.20", {"center": v(97.23, 38.86) * mm, "radius": 2.73 * mm, "construction": true});
            skLineSegment(sketch, "E17.11.15.20", {"start": v(98.8, 36.13) * mm, "end": v(95.65, 36.13) * mm});
            skLineSegment(sketch, "E17.14.15.20", {"start": v(95.65, 36.13) * mm, "end": v(94.07, 38.86) * mm});
            skLineSegment(sketch, "E17.17.15.20", {"start": v(94.07, 38.86) * mm, "end": v(95.65, 41.6) * mm});
            skLineSegment(sketch, "E17.0.15.21", {"start": v(95.65, 50.23) * mm, "end": v(98.8, 50.23) * mm});
            skLineSegment(sketch, "E17.3.15.21", {"start": v(98.8, 50.23) * mm, "end": v(100.38, 47.5) * mm});
            skLineSegment(sketch, "E17.6.15.21", {"start": v(100.38, 47.5) * mm, "end": v(98.8, 44.77) * mm});
            skCircle(sketch, "E17.9.15.21", {"center": v(97.23, 47.5) * mm, "radius": 2.73 * mm, "construction": true});
            skLineSegment(sketch, "E17.11.15.21", {"start": v(98.8, 44.77) * mm, "end": v(95.65, 44.77) * mm});
            skLineSegment(sketch, "E17.14.15.21", {"start": v(95.65, 44.77) * mm, "end": v(94.07, 47.5) * mm});
            skLineSegment(sketch, "E17.17.15.21", {"start": v(94.07, 47.5) * mm, "end": v(95.65, 50.23) * mm});
            skLineSegment(sketch, "E17.0.15.22", {"start": v(95.65, 58.86) * mm, "end": v(98.8, 58.86) * mm});
            skLineSegment(sketch, "E17.3.15.22", {"start": v(98.8, 58.86) * mm, "end": v(100.38, 56.13) * mm});
            skLineSegment(sketch, "E17.6.15.22", {"start": v(100.38, 56.13) * mm, "end": v(98.8, 53.4) * mm});
            skCircle(sketch, "E17.9.15.22", {"center": v(97.23, 56.13) * mm, "radius": 2.73 * mm, "construction": true});
            skLineSegment(sketch, "E17.11.15.22", {"start": v(98.8, 53.4) * mm, "end": v(95.65, 53.4) * mm});
            skLineSegment(sketch, "E17.14.15.22", {"start": v(95.65, 53.4) * mm, "end": v(94.07, 56.13) * mm});
            skLineSegment(sketch, "E17.17.15.22", {"start": v(94.07, 56.13) * mm, "end": v(95.65, 58.86) * mm});
            skLineSegment(sketch, "E17.0.15.23", {"start": v(95.65, 67.5) * mm, "end": v(98.8, 67.5) * mm});
            skLineSegment(sketch, "E17.3.15.23", {"start": v(98.8, 67.5) * mm, "end": v(100.38, 64.77) * mm});
            skLineSegment(sketch, "E17.6.15.23", {"start": v(100.38, 64.77) * mm, "end": v(98.8, 62.04) * mm});
            skCircle(sketch, "E17.9.15.23", {"center": v(97.23, 64.77) * mm, "radius": 2.73 * mm, "construction": true});
            skLineSegment(sketch, "E17.11.15.23", {"start": v(98.8, 62.04) * mm, "end": v(95.65, 62.04) * mm});
            skLineSegment(sketch, "E17.14.15.23", {"start": v(95.65, 62.04) * mm, "end": v(94.07, 64.77) * mm});
            skLineSegment(sketch, "E17.17.15.23", {"start": v(94.07, 64.77) * mm, "end": v(95.65, 67.5) * mm});
            skLineSegment(sketch, "E17.0.15.24", {"start": v(95.65, 76.14) * mm, "end": v(98.8, 76.14) * mm});
            skLineSegment(sketch, "E17.3.15.24", {"start": v(98.8, 76.14) * mm, "end": v(100.38, 73.4) * mm});
            skLineSegment(sketch, "E17.6.15.24", {"start": v(100.38, 73.4) * mm, "end": v(98.8, 70.68) * mm});
            skCircle(sketch, "E17.9.15.24", {"center": v(97.23, 73.4) * mm, "radius": 2.73 * mm, "construction": true});
            skLineSegment(sketch, "E17.11.15.24", {"start": v(98.8, 70.68) * mm, "end": v(95.65, 70.68) * mm});
            skLineSegment(sketch, "E17.14.15.24", {"start": v(95.65, 70.68) * mm, "end": v(94.07, 73.4) * mm});
            skLineSegment(sketch, "E17.17.15.24", {"start": v(94.07, 73.4) * mm, "end": v(95.65, 76.14) * mm});
            skLineSegment(sketch, "E17.0.16.20", {"start": v(110.6, 41.6) * mm, "end": v(113.76, 41.6) * mm});
            skLineSegment(sketch, "E17.3.16.20", {"start": v(113.76, 41.6) * mm, "end": v(115.34, 38.86) * mm});
            skLineSegment(sketch, "E17.6.16.20", {"start": v(115.34, 38.86) * mm, "end": v(113.76, 36.13) * mm});
            skCircle(sketch, "E17.9.16.20", {"center": v(112.19, 38.86) * mm, "radius": 2.73 * mm, "construction": true});
            skLineSegment(sketch, "E17.11.16.20", {"start": v(113.76, 36.13) * mm, "end": v(110.6, 36.13) * mm});
            skLineSegment(sketch, "E17.14.16.20", {"start": v(110.6, 36.13) * mm, "end": v(109.03, 38.86) * mm});
            skLineSegment(sketch, "E17.17.16.20", {"start": v(109.03, 38.86) * mm, "end": v(110.6, 41.6) * mm});
            skLineSegment(sketch, "E17.0.16.21", {"start": v(110.6, 50.23) * mm, "end": v(113.76, 50.23) * mm});
            skLineSegment(sketch, "E17.3.16.21", {"start": v(113.76, 50.23) * mm, "end": v(115.34, 47.5) * mm});
            skLineSegment(sketch, "E17.6.16.21", {"start": v(115.34, 47.5) * mm, "end": v(113.76, 44.77) * mm});
            skCircle(sketch, "E17.9.16.21", {"center": v(112.19, 47.5) * mm, "radius": 2.73 * mm, "construction": true});
            skLineSegment(sketch, "E17.11.16.21", {"start": v(113.76, 44.77) * mm, "end": v(110.6, 44.77) * mm});
            skLineSegment(sketch, "E17.14.16.21", {"start": v(110.6, 44.77) * mm, "end": v(109.03, 47.5) * mm});
            skLineSegment(sketch, "E17.17.16.21", {"start": v(109.03, 47.5) * mm, "end": v(110.6, 50.23) * mm});
            skLineSegment(sketch, "E17.0.16.22", {"start": v(110.6, 58.86) * mm, "end": v(113.76, 58.86) * mm});
            skLineSegment(sketch, "E17.3.16.22", {"start": v(113.76, 58.86) * mm, "end": v(115.34, 56.13) * mm});
            skLineSegment(sketch, "E17.6.16.22", {"start": v(115.34, 56.13) * mm, "end": v(113.76, 53.4) * mm});
            skCircle(sketch, "E17.9.16.22", {"center": v(112.19, 56.13) * mm, "radius": 2.73 * mm, "construction": true});
            skLineSegment(sketch, "E17.11.16.22", {"start": v(113.76, 53.4) * mm, "end": v(110.6, 53.4) * mm});
            skLineSegment(sketch, "E17.14.16.22", {"start": v(110.6, 53.4) * mm, "end": v(109.03, 56.13) * mm});
            skLineSegment(sketch, "E17.17.16.22", {"start": v(109.03, 56.13) * mm, "end": v(110.6, 58.86) * mm});
            skLineSegment(sketch, "E17.0.16.23", {"start": v(110.6, 67.5) * mm, "end": v(113.76, 67.5) * mm});
            skLineSegment(sketch, "E17.3.16.23", {"start": v(113.76, 67.5) * mm, "end": v(115.34, 64.77) * mm});
            skLineSegment(sketch, "E17.6.16.23", {"start": v(115.34, 64.77) * mm, "end": v(113.76, 62.04) * mm});
            skCircle(sketch, "E17.9.16.23", {"center": v(112.19, 64.77) * mm, "radius": 2.73 * mm, "construction": true});
            skLineSegment(sketch, "E17.11.16.23", {"start": v(113.76, 62.04) * mm, "end": v(110.6, 62.04) * mm});
            skLineSegment(sketch, "E17.14.16.23", {"start": v(110.6, 62.04) * mm, "end": v(109.03, 64.77) * mm});
            skLineSegment(sketch, "E17.17.16.23", {"start": v(109.03, 64.77) * mm, "end": v(110.6, 67.5) * mm});
            skLineSegment(sketch, "E17.0.16.24", {"start": v(110.6, 76.14) * mm, "end": v(113.76, 76.14) * mm});
            skLineSegment(sketch, "E17.3.16.24", {"start": v(113.76, 76.14) * mm, "end": v(115.34, 73.4) * mm});
            skLineSegment(sketch, "E17.6.16.24", {"start": v(115.34, 73.4) * mm, "end": v(113.76, 70.68) * mm});
            skCircle(sketch, "E17.9.16.24", {"center": v(112.19, 73.4) * mm, "radius": 2.73 * mm, "construction": true});
            skLineSegment(sketch, "E17.11.16.24", {"start": v(113.76, 70.68) * mm, "end": v(110.6, 70.68) * mm});
            skLineSegment(sketch, "E17.14.16.24", {"start": v(110.6, 70.68) * mm, "end": v(109.03, 73.4) * mm});
            skLineSegment(sketch, "E17.17.16.24", {"start": v(109.03, 73.4) * mm, "end": v(110.6, 76.14) * mm});
            skLineSegment(sketch, "E17.0.17.20", {"start": v(125.57, 41.6) * mm, "end": v(128.72, 41.6) * mm});
            skLineSegment(sketch, "E17.3.17.20", {"start": v(128.72, 41.6) * mm, "end": v(130.3, 38.86) * mm});
            skLineSegment(sketch, "E17.6.17.20", {"start": v(130.3, 38.86) * mm, "end": v(128.72, 36.13) * mm});
            skCircle(sketch, "E17.9.17.20", {"center": v(127.14, 38.86) * mm, "radius": 2.73 * mm, "construction": true});
            skLineSegment(sketch, "E17.11.17.20", {"start": v(128.72, 36.13) * mm, "end": v(125.57, 36.13) * mm});
            skLineSegment(sketch, "E17.14.17.20", {"start": v(125.57, 36.13) * mm, "end": v(124, 38.86) * mm});
            skLineSegment(sketch, "E17.17.17.20", {"start": v(124, 38.86) * mm, "end": v(125.57, 41.6) * mm});
            skLineSegment(sketch, "E17.0.17.21", {"start": v(125.57, 50.23) * mm, "end": v(128.72, 50.23) * mm});
            skLineSegment(sketch, "E17.3.17.21", {"start": v(128.72, 50.23) * mm, "end": v(130.3, 47.5) * mm});
            skLineSegment(sketch, "E17.6.17.21", {"start": v(130.3, 47.5) * mm, "end": v(128.72, 44.77) * mm});
            skCircle(sketch, "E17.9.17.21", {"center": v(127.14, 47.5) * mm, "radius": 2.73 * mm, "construction": true});
            skLineSegment(sketch, "E17.11.17.21", {"start": v(128.72, 44.77) * mm, "end": v(125.57, 44.77) * mm});
            skLineSegment(sketch, "E17.14.17.21", {"start": v(125.57, 44.77) * mm, "end": v(124, 47.5) * mm});
            skLineSegment(sketch, "E17.17.17.21", {"start": v(124, 47.5) * mm, "end": v(125.57, 50.23) * mm});
            skLineSegment(sketch, "E17.0.17.22", {"start": v(125.57, 58.86) * mm, "end": v(128.72, 58.86) * mm});
            skLineSegment(sketch, "E17.3.17.22", {"start": v(128.72, 58.86) * mm, "end": v(130.3, 56.13) * mm});
            skLineSegment(sketch, "E17.6.17.22", {"start": v(130.3, 56.13) * mm, "end": v(128.72, 53.4) * mm});
            skCircle(sketch, "E17.9.17.22", {"center": v(127.14, 56.13) * mm, "radius": 2.73 * mm, "construction": true});
            skLineSegment(sketch, "E17.11.17.22", {"start": v(128.72, 53.4) * mm, "end": v(125.57, 53.4) * mm});
            skLineSegment(sketch, "E17.14.17.22", {"start": v(125.57, 53.4) * mm, "end": v(124, 56.13) * mm});
            skLineSegment(sketch, "E17.17.17.22", {"start": v(124, 56.13) * mm, "end": v(125.57, 58.86) * mm});
            skLineSegment(sketch, "E17.0.17.23", {"start": v(125.57, 67.5) * mm, "end": v(128.72, 67.5) * mm});
            skLineSegment(sketch, "E17.3.17.23", {"start": v(128.72, 67.5) * mm, "end": v(130.3, 64.77) * mm});
            skLineSegment(sketch, "E17.6.17.23", {"start": v(130.3, 64.77) * mm, "end": v(128.72, 62.04) * mm});
            skCircle(sketch, "E17.9.17.23", {"center": v(127.14, 64.77) * mm, "radius": 2.73 * mm, "construction": true});
            skLineSegment(sketch, "E17.11.17.23", {"start": v(128.72, 62.04) * mm, "end": v(125.57, 62.04) * mm});
            skLineSegment(sketch, "E17.14.17.23", {"start": v(125.57, 62.04) * mm, "end": v(124, 64.77) * mm});
            skLineSegment(sketch, "E17.17.17.23", {"start": v(124, 64.77) * mm, "end": v(125.57, 67.5) * mm});
            skLineSegment(sketch, "E17.0.17.24", {"start": v(125.57, 76.14) * mm, "end": v(128.72, 76.14) * mm});
            skLineSegment(sketch, "E17.3.17.24", {"start": v(128.72, 76.14) * mm, "end": v(130.3, 73.4) * mm});
            skLineSegment(sketch, "E17.6.17.24", {"start": v(130.3, 73.4) * mm, "end": v(128.72, 70.68) * mm});
            skCircle(sketch, "E17.9.17.24", {"center": v(127.14, 73.4) * mm, "radius": 2.73 * mm, "construction": true});
            skLineSegment(sketch, "E17.11.17.24", {"start": v(128.72, 70.68) * mm, "end": v(125.57, 70.68) * mm});
            skLineSegment(sketch, "E17.14.17.24", {"start": v(125.57, 70.68) * mm, "end": v(124, 73.4) * mm});
            skLineSegment(sketch, "E17.17.17.24", {"start": v(124, 73.4) * mm, "end": v(125.57, 76.14) * mm});
            skLineSegment(sketch, "E17.0.18.20", {"start": v(140.53, 41.6) * mm, "end": v(143.68, 41.6) * mm});
            skLineSegment(sketch, "E17.3.18.20", {"start": v(143.68, 41.6) * mm, "end": v(145.25, 38.86) * mm});
            skLineSegment(sketch, "E17.6.18.20", {"start": v(145.25, 38.86) * mm, "end": v(143.68, 36.13) * mm});
            skCircle(sketch, "E17.9.18.20", {"center": v(142.1, 38.86) * mm, "radius": 2.73 * mm, "construction": true});
            skLineSegment(sketch, "E17.11.18.20", {"start": v(143.68, 36.13) * mm, "end": v(140.53, 36.13) * mm});
            skLineSegment(sketch, "E17.14.18.20", {"start": v(140.53, 36.13) * mm, "end": v(138.95, 38.86) * mm});
            skLineSegment(sketch, "E17.17.18.20", {"start": v(138.95, 38.86) * mm, "end": v(140.53, 41.6) * mm});
            skLineSegment(sketch, "E17.0.18.21", {"start": v(140.53, 50.23) * mm, "end": v(143.68, 50.23) * mm});
            skLineSegment(sketch, "E17.3.18.21", {"start": v(143.68, 50.23) * mm, "end": v(145.25, 47.5) * mm});
            skLineSegment(sketch, "E17.6.18.21", {"start": v(145.25, 47.5) * mm, "end": v(143.68, 44.77) * mm});
            skCircle(sketch, "E17.9.18.21", {"center": v(142.1, 47.5) * mm, "radius": 2.73 * mm, "construction": true});
            skLineSegment(sketch, "E17.11.18.21", {"start": v(143.68, 44.77) * mm, "end": v(140.53, 44.77) * mm});
            skLineSegment(sketch, "E17.14.18.21", {"start": v(140.53, 44.77) * mm, "end": v(138.95, 47.5) * mm});
            skLineSegment(sketch, "E17.17.18.21", {"start": v(138.95, 47.5) * mm, "end": v(140.53, 50.23) * mm});
            skLineSegment(sketch, "E17.0.18.22", {"start": v(140.53, 58.86) * mm, "end": v(143.68, 58.86) * mm});
            skLineSegment(sketch, "E17.3.18.22", {"start": v(143.68, 58.86) * mm, "end": v(145.25, 56.13) * mm});
            skLineSegment(sketch, "E17.6.18.22", {"start": v(145.25, 56.13) * mm, "end": v(143.68, 53.4) * mm});
            skCircle(sketch, "E17.9.18.22", {"center": v(142.1, 56.13) * mm, "radius": 2.73 * mm, "construction": true});
            skLineSegment(sketch, "E17.11.18.22", {"start": v(143.68, 53.4) * mm, "end": v(140.53, 53.4) * mm});
            skLineSegment(sketch, "E17.14.18.22", {"start": v(140.53, 53.4) * mm, "end": v(138.95, 56.13) * mm});
            skLineSegment(sketch, "E17.17.18.22", {"start": v(138.95, 56.13) * mm, "end": v(140.53, 58.86) * mm});
            skLineSegment(sketch, "E17.0.18.23", {"start": v(140.53, 67.5) * mm, "end": v(143.68, 67.5) * mm});
            skLineSegment(sketch, "E17.3.18.23", {"start": v(143.68, 67.5) * mm, "end": v(145.25, 64.77) * mm});
            skLineSegment(sketch, "E17.6.18.23", {"start": v(145.25, 64.77) * mm, "end": v(143.68, 62.04) * mm});
            skCircle(sketch, "E17.9.18.23", {"center": v(142.1, 64.77) * mm, "radius": 2.73 * mm, "construction": true});
            skLineSegment(sketch, "E17.11.18.23", {"start": v(143.68, 62.04) * mm, "end": v(140.53, 62.04) * mm});
            skLineSegment(sketch, "E17.14.18.23", {"start": v(140.53, 62.04) * mm, "end": v(138.95, 64.77) * mm});
            skLineSegment(sketch, "E17.17.18.23", {"start": v(138.95, 64.77) * mm, "end": v(140.53, 67.5) * mm});
            skLineSegment(sketch, "E17.0.18.24", {"start": v(140.53, 76.14) * mm, "end": v(143.68, 76.14) * mm});
            skLineSegment(sketch, "E17.3.18.24", {"start": v(143.68, 76.14) * mm, "end": v(145.25, 73.4) * mm});
            skLineSegment(sketch, "E17.6.18.24", {"start": v(145.25, 73.4) * mm, "end": v(143.68, 70.68) * mm});
            skCircle(sketch, "E17.9.18.24", {"center": v(142.1, 73.4) * mm, "radius": 2.73 * mm, "construction": true});
            skLineSegment(sketch, "E17.11.18.24", {"start": v(143.68, 70.68) * mm, "end": v(140.53, 70.68) * mm});
            skLineSegment(sketch, "E17.14.18.24", {"start": v(140.53, 70.68) * mm, "end": v(138.95, 73.4) * mm});
            skLineSegment(sketch, "E17.17.18.24", {"start": v(138.95, 73.4) * mm, "end": v(140.53, 76.14) * mm});
            skLineSegment(sketch, "E17.0.19.20", {"start": v(155.48, 41.6) * mm, "end": v(158.64, 41.6) * mm});
            skLineSegment(sketch, "E17.3.19.20", {"start": v(158.64, 41.6) * mm, "end": v(160.21, 38.86) * mm});
            skLineSegment(sketch, "E17.6.19.20", {"start": v(160.21, 38.86) * mm, "end": v(158.64, 36.13) * mm});
            skCircle(sketch, "E17.9.19.20", {"center": v(157.06, 38.86) * mm, "radius": 2.73 * mm, "construction": true});
            skLineSegment(sketch, "E17.11.19.20", {"start": v(158.64, 36.13) * mm, "end": v(155.48, 36.13) * mm});
            skLineSegment(sketch, "E17.14.19.20", {"start": v(155.48, 36.13) * mm, "end": v(153.9, 38.86) * mm});
            skLineSegment(sketch, "E17.17.19.20", {"start": v(153.9, 38.86) * mm, "end": v(155.48, 41.6) * mm});
            skLineSegment(sketch, "E17.0.19.21", {"start": v(155.48, 50.23) * mm, "end": v(158.64, 50.23) * mm});
            skLineSegment(sketch, "E17.3.19.21", {"start": v(158.64, 50.23) * mm, "end": v(160.21, 47.5) * mm});
            skLineSegment(sketch, "E17.6.19.21", {"start": v(160.21, 47.5) * mm, "end": v(158.64, 44.77) * mm});
            skCircle(sketch, "E17.9.19.21", {"center": v(157.06, 47.5) * mm, "radius": 2.73 * mm, "construction": true});
            skLineSegment(sketch, "E17.11.19.21", {"start": v(158.64, 44.77) * mm, "end": v(155.48, 44.77) * mm});
            skLineSegment(sketch, "E17.14.19.21", {"start": v(155.48, 44.77) * mm, "end": v(153.9, 47.5) * mm});
            skLineSegment(sketch, "E17.17.19.21", {"start": v(153.9, 47.5) * mm, "end": v(155.48, 50.23) * mm});
            skLineSegment(sketch, "E17.0.19.22", {"start": v(155.48, 58.86) * mm, "end": v(158.64, 58.86) * mm});
            skLineSegment(sketch, "E17.3.19.22", {"start": v(158.64, 58.86) * mm, "end": v(160.21, 56.13) * mm});
            skLineSegment(sketch, "E17.6.19.22", {"start": v(160.21, 56.13) * mm, "end": v(158.64, 53.4) * mm});
            skCircle(sketch, "E17.9.19.22", {"center": v(157.06, 56.13) * mm, "radius": 2.73 * mm, "construction": true});
            skLineSegment(sketch, "E17.11.19.22", {"start": v(158.64, 53.4) * mm, "end": v(155.48, 53.4) * mm});
            skLineSegment(sketch, "E17.14.19.22", {"start": v(155.48, 53.4) * mm, "end": v(153.9, 56.13) * mm});
            skLineSegment(sketch, "E17.17.19.22", {"start": v(153.9, 56.13) * mm, "end": v(155.48, 58.86) * mm});
            skLineSegment(sketch, "E17.0.19.23", {"start": v(155.48, 67.5) * mm, "end": v(158.64, 67.5) * mm});
            skLineSegment(sketch, "E17.3.19.23", {"start": v(158.64, 67.5) * mm, "end": v(160.21, 64.77) * mm});
            skLineSegment(sketch, "E17.6.19.23", {"start": v(160.21, 64.77) * mm, "end": v(158.64, 62.04) * mm});
            skCircle(sketch, "E17.9.19.23", {"center": v(157.06, 64.77) * mm, "radius": 2.73 * mm, "construction": true});
            skLineSegment(sketch, "E17.11.19.23", {"start": v(158.64, 62.04) * mm, "end": v(155.48, 62.04) * mm});
            skLineSegment(sketch, "E17.14.19.23", {"start": v(155.48, 62.04) * mm, "end": v(153.9, 64.77) * mm});
            skLineSegment(sketch, "E17.17.19.23", {"start": v(153.9, 64.77) * mm, "end": v(155.48, 67.5) * mm});
            skLineSegment(sketch, "E17.0.19.24", {"start": v(155.48, 76.14) * mm, "end": v(158.64, 76.14) * mm});
            skLineSegment(sketch, "E17.3.19.24", {"start": v(158.64, 76.14) * mm, "end": v(160.21, 73.4) * mm});
            skLineSegment(sketch, "E17.6.19.24", {"start": v(160.21, 73.4) * mm, "end": v(158.64, 70.68) * mm});
            skCircle(sketch, "E17.9.19.24", {"center": v(157.06, 73.4) * mm, "radius": 2.73 * mm, "construction": true});
            skLineSegment(sketch, "E17.11.19.24", {"start": v(158.64, 70.68) * mm, "end": v(155.48, 70.68) * mm});
            skLineSegment(sketch, "E17.14.19.24", {"start": v(155.48, 70.68) * mm, "end": v(153.9, 73.4) * mm});
            skLineSegment(sketch, "E17.17.19.24", {"start": v(153.9, 73.4) * mm, "end": v(155.48, 76.14) * mm});
            skSolve(sketch);
        }
        {
            var Q0;
            Q0=qSketchRegion(id+"F2",true);
            extrude(context, id + "F3", {"entities" : qUnion([Q0]), "operationType" : NewBodyOperationType.REMOVE, "oppositeDirection" : true, "depth" : 25.4 * mm, "offsetDistance" : 25.4 * mm});
        }
        {
            var Q0;
            Q0=makeQuery(id+"F1.opExtrude","CAP_FACE",FACE,{"disambiguationData":[OSD([sQuery(id+"F0.wireOp",EDGE,"E0")])],"isStart":false});
            var sketch = newSketch(context, id + "F4", { "sketchPlane" : qUnion([Q0])});
            skCircle(sketch, "E18", {"center": v(0, 0) * mm, "radius": 115.89 * mm});
            skCircle(sketch, "E19", {"center": v(0, 0) * mm, "radius": 123.02 * mm});
            skSolve(sketch);
        }
        {
            var Q0;
            Q0=qSketchRegion(id+"F4",true);
            var Q1;
            Q1=makeQuery(id+"F1.opExtrude","CAP_FACE",FACE,{"disambiguationData":[OSD([sQuery(id+"F0.wireOp",EDGE,"E0")])],"isStart":true});
            extrude(context, id + "F5", {"entities" : qUnion([Q0]), "operationType" : NewBodyOperationType.ADD, "endBound" : BoundingType.UP_TO_SURFACE, "oppositeDirection" : true, "depth" : 25.4 * mm, "endBoundEntityFace" : qUnion([Q1]), "offsetDistance" : 25.4 * mm});
        }
        {
            var Q0;
            Q0=makeQuery(id+"F5.boolean.opBoolean","MERGE",FACE,{"derivedFrom":[makeQuery(id+"F1.opExtrude","CAP_FACE",FACE,{"disambiguationData":[OSD([sQuery(id+"F0.wireOp",EDGE,"E0")])],"isStart":false}),makeQuery(id+"F5.opExtrude","CAP_FACE",FACE,{"disambiguationData":[OSD([sQuery(id+"F4.wireOp",EDGE,"gzat5XN6-aFc3-cK17-7gGf-ptE3Ki8R4cpB"),sQuery(id+"F4.wireOp",EDGE,"E18")])],"isStart":true})]});
            var sketch = newSketch(context, id + "F6", { "sketchPlane" : qUnion([Q0])});
            skLineSegment(sketch, "E20.bottom", {"start": v(-111.14, -36.87) * mm, "end": v(-108.38, -36.87) * mm});
            skLineSegment(sketch, "E20.top", {"start": v(-111.14, -39.87) * mm, "end": v(-108.38, -39.87) * mm});
            skLineSegment(sketch, "E20.left", {"start": v(-111.14, -36.87) * mm, "end": v(-111.14, -39.87) * mm});
            skLineSegment(sketch, "E20.right", {"start": v(-108.38, -36.87) * mm, "end": v(-108.38, -39.87) * mm});
            skLineSegment(sketch, "E21.bottom", {"start": v(-89.68, -74.2) * mm, "end": v(-86.66, -74.2) * mm});
            skLineSegment(sketch, "E21.top", {"start": v(-89.68, -76.77) * mm, "end": v(-86.66, -76.77) * mm});
            skLineSegment(sketch, "E21.left", {"start": v(-89.68, -74.2) * mm, "end": v(-89.68, -76.77) * mm});
            skLineSegment(sketch, "E21.right", {"start": v(-86.66, -74.2) * mm, "end": v(-86.66, -76.77) * mm});
            skLineSegment(sketch, "E22.bottom", {"start": v(-22.86, -113.02) * mm, "end": v(-19.56, -113.02) * mm});
            skLineSegment(sketch, "E22.top", {"start": v(-22.86, -115.1) * mm, "end": v(-19.56, -115.1) * mm});
            skLineSegment(sketch, "E22.left", {"start": v(-22.86, -113.02) * mm, "end": v(-22.86, -115.1) * mm});
            skLineSegment(sketch, "E22.right", {"start": v(-19.56, -113.02) * mm, "end": v(-19.56, -115.1) * mm});
            skLineSegment(sketch, "E23.bottom", {"start": v(23.22, -112.84) * mm, "end": v(19.66, -112.84) * mm});
            skLineSegment(sketch, "E23.top", {"start": v(23.22, -115.45) * mm, "end": v(19.66, -115.45) * mm});
            skLineSegment(sketch, "E23.left", {"start": v(23.22, -112.84) * mm, "end": v(23.22, -115.45) * mm});
            skLineSegment(sketch, "E23.right", {"start": v(19.66, -112.84) * mm, "end": v(19.66, -115.45) * mm});
            skLineSegment(sketch, "E24.bottom", {"start": v(89.64, -73.9) * mm, "end": v(86.67, -73.9) * mm});
            skLineSegment(sketch, "E24.top", {"start": v(89.64, -77.36) * mm, "end": v(86.67, -77.36) * mm});
            skLineSegment(sketch, "E24.left", {"start": v(89.64, -73.9) * mm, "end": v(89.64, -77.36) * mm});
            skLineSegment(sketch, "E24.right", {"start": v(86.67, -73.9) * mm, "end": v(86.67, -77.36) * mm});
            skLineSegment(sketch, "E25.bottom", {"start": v(110.54, -36.67) * mm, "end": v(107.96, -36.67) * mm});
            skLineSegment(sketch, "E25.top", {"start": v(110.54, -40.43) * mm, "end": v(107.96, -40.43) * mm});
            skLineSegment(sketch, "E25.left", {"start": v(110.54, -36.67) * mm, "end": v(110.54, -40.43) * mm});
            skLineSegment(sketch, "E25.right", {"start": v(107.96, -36.67) * mm, "end": v(107.96, -40.43) * mm});
            skSolve(sketch);
        }
        {
            var Q0;
            Q0=qSketchRegion(id+"F6",true);
            var Q1;
            Q1=makeQuery(id+"F5.boolean.opBoolean","MERGE",FACE,{"derivedFrom":[makeQuery(id+"F1.opExtrude","CAP_FACE",FACE,{"disambiguationData":[OSD([sQuery(id+"F0.wireOp",EDGE,"E0")])],"isStart":true}),makeQuery(id+"F5.opExtrude","CAP_FACE",FACE,{"disambiguationData":[OSD([sQuery(id+"F4.wireOp",EDGE,"gzat5XN6-aFc3-cK17-7gGf-ptE3Ki8R4cpB"),sQuery(id+"F4.wireOp",EDGE,"E18")])],"isStart":false})]});
            extrude(context, id + "F7", {"entities" : qUnion([Q0]), "operationType" : NewBodyOperationType.ADD, "endBound" : BoundingType.UP_TO_SURFACE, "oppositeDirection" : true, "depth" : 25.4 * mm, "endBoundEntityFace" : qUnion([Q1]), "offsetDistance" : 25.4 * mm});
        }
        {
            var Q0;
            Q0=makeQuery(id+"F7.boolean.opBoolean","MERGE",FACE,{"derivedFrom":[makeQuery(id+"F5.boolean.opBoolean","MERGE",FACE,{"derivedFrom":[makeQuery(id+"F1.opExtrude","CAP_FACE",FACE,{"disambiguationData":[OSD([sQuery(id+"F0.wireOp",EDGE,"E0")])],"isStart":false}),makeQuery(id+"F5.opExtrude","CAP_FACE",FACE,{"disambiguationData":[OSD([sQuery(id+"F4.wireOp",EDGE,"E18"),sQuery(id+"F4.wireOp",EDGE,"E19")])],"isStart":true})]}),makeQuery(id+"F7.opExtrude","CAP_FACE",FACE,{"disambiguationData":[OSD([sQuery(id+"F6.wireOp",EDGE,"E20.bottom"),sQuery(id+"F6.wireOp",EDGE,"E20.top"),sQuery(id+"F6.wireOp",EDGE,"E20.left"),sQuery(id+"F6.wireOp",EDGE,"E20.right")])],"isStart":true}),makeQuery(id+"F7.opExtrude","CAP_FACE",FACE,{"disambiguationData":[OSD([sQuery(id+"F6.wireOp",EDGE,"E21.bottom"),sQuery(id+"F6.wireOp",EDGE,"E21.top"),sQuery(id+"F6.wireOp",EDGE,"E21.left"),sQuery(id+"F6.wireOp",EDGE,"E21.right")])],"isStart":true}),makeQuery(id+"F7.opExtrude","CAP_FACE",FACE,{"disambiguationData":[OSD([sQuery(id+"F6.wireOp",EDGE,"E22.bottom"),sQuery(id+"F6.wireOp",EDGE,"E22.top"),sQuery(id+"F6.wireOp",EDGE,"E22.left"),sQuery(id+"F6.wireOp",EDGE,"E22.right")])],"isStart":true}),makeQuery(id+"F7.opExtrude","CAP_FACE",FACE,{"disambiguationData":[OSD([sQuery(id+"F6.wireOp",EDGE,"E23.bottom"),sQuery(id+"F6.wireOp",EDGE,"E23.top"),sQuery(id+"F6.wireOp",EDGE,"E23.left"),sQuery(id+"F6.wireOp",EDGE,"E23.right")])],"isStart":true}),makeQuery(id+"F7.opExtrude","CAP_FACE",FACE,{"disambiguationData":[OSD([sQuery(id+"F6.wireOp",EDGE,"E24.bottom"),sQuery(id+"F6.wireOp",EDGE,"E24.top"),sQuery(id+"F6.wireOp",EDGE,"E24.left"),sQuery(id+"F6.wireOp",EDGE,"E24.right")])],"isStart":true}),makeQuery(id+"F7.opExtrude","CAP_FACE",FACE,{"disambiguationData":[OSD([sQuery(id+"F6.wireOp",EDGE,"E25.bottom"),sQuery(id+"F6.wireOp",EDGE,"E25.top"),sQuery(id+"F6.wireOp",EDGE,"E25.left"),sQuery(id+"F6.wireOp",EDGE,"E25.right")])],"isStart":true})]});
            var sketch = newSketch(context, id + "F8", { "sketchPlane" : qUnion([Q0])});
            skLineSegment(sketch, "E26.bottom", {"start": v(-152.36, 126.72) * mm, "end": v(169.88, 126.72) * mm});
            skLineSegment(sketch, "E26.top", {"start": v(-152.36, 0) * mm, "end": v(169.88, 0) * mm});
            skLineSegment(sketch, "E26.left", {"start": v(-152.36, 126.72) * mm, "end": v(-152.36, 0) * mm});
            skLineSegment(sketch, "E26.right", {"start": v(169.88, 126.72) * mm, "end": v(169.88, 0) * mm});
            skSolve(sketch);
        }
        {
            var Q0;
            Q0 = qSketchRegion(id + "F8", true);
            extrude(context, id + "F9", {"entities" : qUnion([Q0]), "operationType" : NewBodyOperationType.REMOVE, "oppositeDirection" : true, "depth" : 25.4 * mm, "offsetDistance" : 25.4 * mm});
        }
        {
            var Q0;
            Q0=makeQuery(id+"F1.opExtrude","SWEPT_BODY",BODY,{"disambiguationData":[OSD([sQuery(id+"F0.wireOp",EDGE,"E0")])]});
            var Q1;
            Q1=qCreatedBy(makeId("Front.planeOp"),FACE);
            mirror(context, id + "F10", {"operationType" : NewBodyOperationType.ADD, "entities" : qUnion([Q0]), "mirrorPlane" : qUnion([Q1])});
        }
    });
